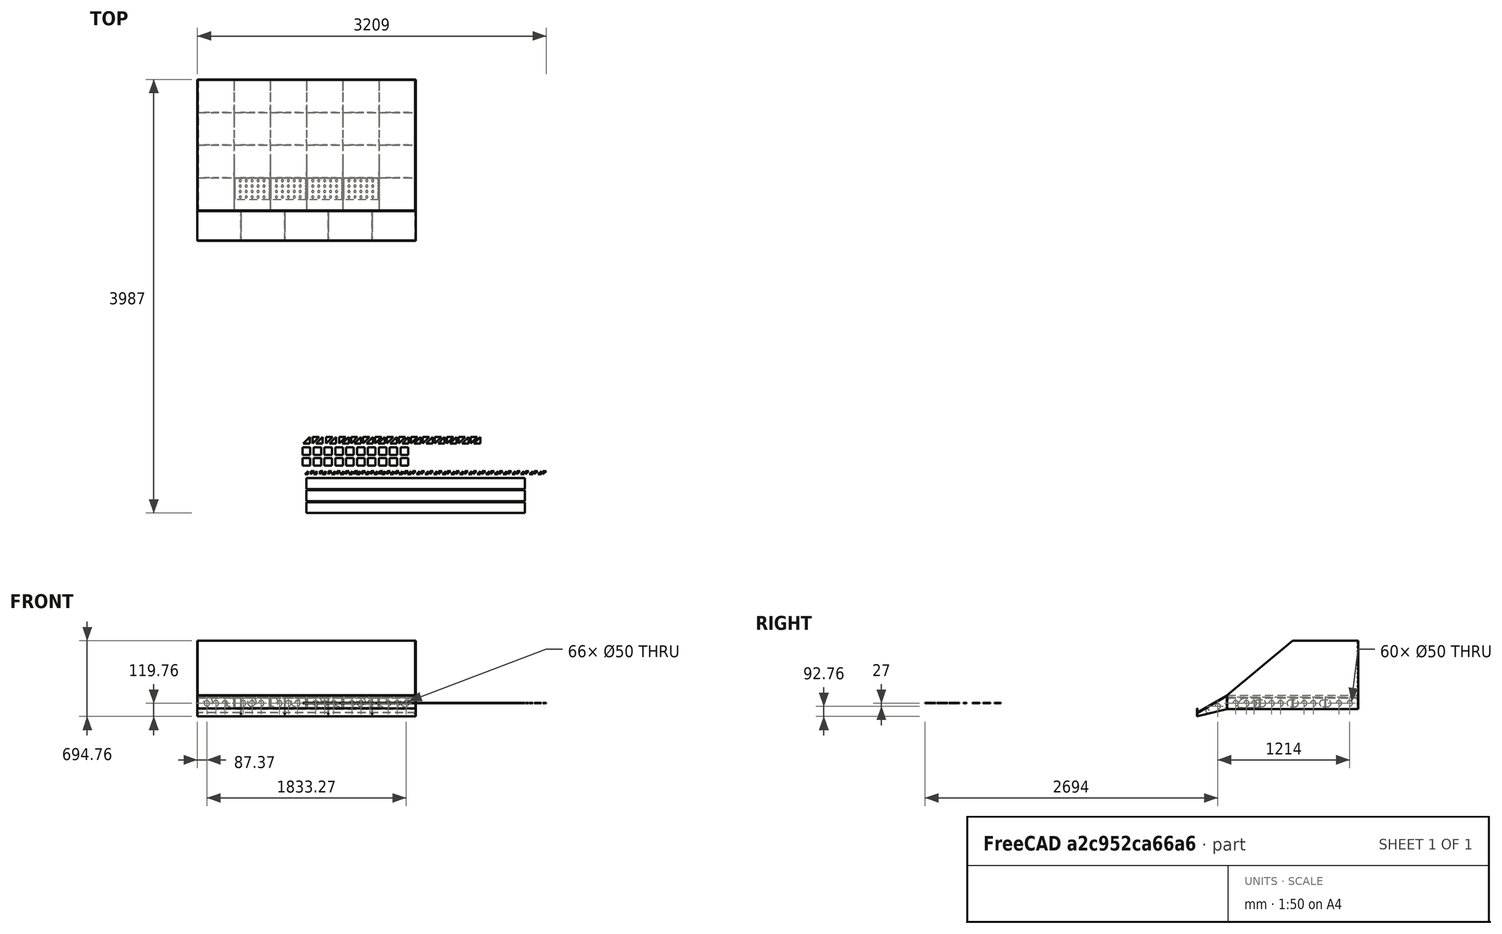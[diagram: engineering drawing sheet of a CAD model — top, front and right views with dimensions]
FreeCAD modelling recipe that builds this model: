
FCSTD DOCUMENT  (FreeCAD 0.19R24291 (Git))
Label: MJ-bord
License: All rights reserved
LicenseURL: http://en.wikipedia.org/wiki/All_rights_reserved
objects: TechDraw::DrawViewDimension×234, Sketcher::SketchObject×198, PartDesign::Pad×155, PartDesign::Body×155, App::DocumentObjectGroupPython×45, PartDesign::Pocket×40, TechDraw::DrawViewPart×18, TechDraw::DrawViewSection×18, TechDraw::DrawSVGTemplate×13, TechDraw::DrawPage×13, PartDesign::Fillet×8, Part::Feature×7, TechDraw::DrawProjGroupItem×3, TechDraw::DrawProjGroup×3, Spreadsheet::Sheet×1, App::DocumentObjectGroup×1
note: 766 computed .brp shape members not serialized (recipe doc carries the construction recipe); baked Part::Feature solids carry a one-line shape summary decoded from their .brp

FEATURE [Sketcher::SketchObject] Sketch
  FullyConstrained = true
  MapMode = 5
  Placement = pos=(0,0,0) rot=(1,0,0;1.5708rad)
  Support = -> [XZ_Plane]
  sketch-geometry (5):
    g0: LineSegment StartX=-1000 StartY=-50 StartZ=0 EndX=-1000 EndY=50 EndZ=0
    g1: LineSegment StartX=-1000 StartY=50 StartZ=0 EndX=1000 EndY=50 EndZ=0
    g2: LineSegment StartX=1000 StartY=50 StartZ=0 EndX=1000 EndY=-50 EndZ=0
    g3: LineSegment StartX=1000 StartY=-50 StartZ=0 EndX=-1000 EndY=-50 EndZ=0
    g4: GeomPoint X=0 Y=0 Z=0
  constraints (12):
    c: Coincident(g0,g1)
    c: Coincident(g1,g2)
    c: Coincident(g2,g3)
    c: Coincident(g3,g0)
    c: Horizontal(g1)
    c: Horizontal(g3)
    c: Vertical(g0)
    c: Vertical(g2)
    c: Symmetric(g1,g0,g4)
    c: Coincident(g4,g-1)
    c: DistanceY(g2,g1) = 100
    c: DistanceX(g0,g1) = 2000
FEATURE [PartDesign::Pad] Pad
  Direction = (0,-1,2e-16)
  Length = 4
  Length2 = 10
  Placement = pos=(0,0,0) rot=(1,0,0;1.5708rad)
  Profile = -> Sketch
  Type = 0
FEATURE [Sketcher::SketchObject] Sketch001
  ExternalGeometry = -> [Pad]
  FullyConstrained = false
  MapMode = 5
  Placement = pos=(0,-4,1.8e-15) rot=(1,0,0;1.5708rad)
  Support = -> [Pad]
  sketch-geometry (94):
    g0: GeomPoint X=-666.66 Y=0 Z=0
    g1: GeomPoint X=333.33 Y=0 Z=0
    g2: GeomPoint X=666.66 Y=0 Z=0
    g3: GeomPoint X=-333.33 Y=0 Z=0
    g4: Circle CenterX=-916.63 CenterY=-1.8e-15 CenterZ=0 NormalX=0 NormalY=0 NormalZ=1 AngleXU=0 Radius=25
    g5: Circle CenterX=-833.3 CenterY=-1.8e-15 CenterZ=0 NormalX=0 NormalY=0 NormalZ=1 AngleXU=0 Radius=25
    g6: Circle CenterX=-583.31 CenterY=-1.8e-15 CenterZ=0 NormalX=0 NormalY=0 NormalZ=1 AngleXU=0 Radius=25
    g7: Circle CenterX=-499.98 CenterY=-1.8e-15 CenterZ=0 NormalX=0 NormalY=0 NormalZ=1 AngleXU=0 Radius=25
    g8: Circle CenterX=-249.99 CenterY=-1.8e-15 CenterZ=0 NormalX=0 NormalY=0 NormalZ=1 AngleXU=0 Radius=25
    g9: Circle CenterX=-166.66 CenterY=-1.8e-15 CenterZ=0 NormalX=0 NormalY=0 NormalZ=1 AngleXU=0 Radius=25
    g10: Circle CenterX=83.33 CenterY=-1.8e-15 CenterZ=0 NormalX=0 NormalY=0 NormalZ=1 AngleXU=0 Radius=25
    g11: Circle CenterX=166.66 CenterY=-1.8e-15 CenterZ=0 NormalX=0 NormalY=0 NormalZ=1 AngleXU=0 Radius=25
    g12: Circle CenterX=416.65 CenterY=-1.8e-15 CenterZ=0 NormalX=0 NormalY=0 NormalZ=1 AngleXU=0 Radius=25
    g13: Circle CenterX=499.98 CenterY=-1.8e-15 CenterZ=0 NormalX=0 NormalY=0 NormalZ=1 AngleXU=0 Radius=25
    g14: Circle CenterX=749.97 CenterY=-1.8e-15 CenterZ=0 NormalX=0 NormalY=0 NormalZ=1 AngleXU=0 Radius=25
    g15: Circle CenterX=833.3 CenterY=-1.8e-15 CenterZ=0 NormalX=0 NormalY=0 NormalZ=1 AngleXU=0 Radius=25
    g16: Circle CenterX=-749.97 CenterY=-1.8e-15 CenterZ=0 NormalX=0 NormalY=0 NormalZ=1 AngleXU=0 Radius=25
    g17: Circle CenterX=-416.65 CenterY=-1.8e-15 CenterZ=0 NormalX=0 NormalY=0 NormalZ=1 AngleXU=0 Radius=25
    g18: Circle CenterX=-83.33 CenterY=-1.8e-15 CenterZ=0 NormalX=0 NormalY=0 NormalZ=1 AngleXU=0 Radius=25
    g19: Circle CenterX=249.99 CenterY=-1.8e-15 CenterZ=0 NormalX=0 NormalY=0 NormalZ=1 AngleXU=0 Radius=25
    g20: Circle CenterX=583.31 CenterY=-1.8e-15 CenterZ=0 NormalX=0 NormalY=0 NormalZ=1 AngleXU=0 Radius=25
    g21: Circle CenterX=916.64 CenterY=-1.8e-15 CenterZ=0 NormalX=0 NormalY=0 NormalZ=1 AngleXU=0 Radius=25
    g22: LineSegment StartX=-1000 StartY=50 StartZ=0 EndX=-996 EndY=50 EndZ=0
    g23: LineSegment StartX=-996 StartY=50 StartZ=0 EndX=-996 EndY=30 EndZ=0
    g24: LineSegment StartX=-996 StartY=30 StartZ=0 EndX=-1000 EndY=30 EndZ=0
    g25: LineSegment StartX=-1000 StartY=30 StartZ=0 EndX=-1000 EndY=50 EndZ=0
    g26: LineSegment StartX=-1000 StartY=10 StartZ=0 EndX=-996 EndY=10 EndZ=0
    g27: LineSegment StartX=-996 StartY=10 StartZ=0 EndX=-996 EndY=-10 EndZ=0
    g28: LineSegment StartX=-996 StartY=-10 StartZ=0 EndX=-1000 EndY=-10 EndZ=0
    g29: LineSegment StartX=-1000 StartY=-10 StartZ=0 EndX=-1000 EndY=10 EndZ=0
    g30: LineSegment StartX=1000 StartY=50 StartZ=0 EndX=996 EndY=50 EndZ=0
    g31: LineSegment StartX=996 StartY=50 StartZ=0 EndX=996 EndY=30 EndZ=0
    g32: LineSegment StartX=996 StartY=30 StartZ=0 EndX=1000 EndY=30 EndZ=0
    g33: LineSegment StartX=1000 StartY=30 StartZ=0 EndX=1000 EndY=50 EndZ=0
    g34: LineSegment StartX=1000 StartY=10 StartZ=0 EndX=996 EndY=10 EndZ=0
    g35: LineSegment StartX=996 StartY=10 StartZ=0 EndX=996 EndY=-10 EndZ=0
    g36: LineSegment StartX=996 StartY=-10 StartZ=0 EndX=1000 EndY=-10 EndZ=0
    g37: LineSegment StartX=1000 StartY=-10 StartZ=0 EndX=1000 EndY=10 EndZ=0
    g38: GeomPoint X=-666.64 Y=-51.5587 Z=0
    g39: GeomPoint X=333.32 Y=-51.5587 Z=0
    g40: GeomPoint X=666.64 Y=-51.5587 Z=0
    g41: GeomPoint X=999.97 Y=-51.5587 Z=0
    g42: GeomPoint X=-999.96 Y=-51.5587 Z=0
    g43: LineSegment StartX=-668.66 StartY=50 StartZ=0 EndX=-664.66 EndY=50 EndZ=0
    g44: LineSegment StartX=-664.66 StartY=50 StartZ=0 EndX=-664.66 EndY=30 EndZ=0
    g45: LineSegment StartX=-664.66 StartY=30 StartZ=0 EndX=-668.66 EndY=30 EndZ=0
    g46: LineSegment StartX=-668.66 StartY=30 StartZ=0 EndX=-668.66 EndY=50 EndZ=0
    g47: LineSegment StartX=-668.66 StartY=-50 StartZ=0 EndX=-664.66 EndY=-50 EndZ=0
    g48: LineSegment StartX=-664.66 StartY=-50 StartZ=0 EndX=-664.66 EndY=-30 EndZ=0
    g49: LineSegment StartX=-664.66 StartY=-30 StartZ=0 EndX=-668.66 EndY=-30 EndZ=0
    g50: LineSegment StartX=-668.66 StartY=-30 StartZ=0 EndX=-668.66 EndY=-50 EndZ=0
    g51: LineSegment StartX=-335.33 StartY=50 StartZ=0 EndX=-331.33 EndY=50 EndZ=0
    g52: LineSegment StartX=-331.33 StartY=50 StartZ=0 EndX=-331.33 EndY=30 EndZ=0
    g53: LineSegment StartX=-331.33 StartY=30 StartZ=0 EndX=-335.33 EndY=30 EndZ=0
    g54: LineSegment StartX=-335.33 StartY=30 StartZ=0 EndX=-335.33 EndY=50 EndZ=0
    g55: LineSegment StartX=-335.33 StartY=-50 StartZ=0 EndX=-331.33 EndY=-50 EndZ=0
    g56: LineSegment StartX=-331.33 StartY=-50 StartZ=0 EndX=-331.33 EndY=-30 EndZ=0
    g57: LineSegment StartX=-331.33 StartY=-30 StartZ=0 EndX=-335.33 EndY=-30 EndZ=0
    g58: LineSegment StartX=-335.33 StartY=-30 StartZ=0 EndX=-335.33 EndY=-50 EndZ=0
    g59: GeomPoint X=-333.32 Y=-51.5587 Z=0
    g60: LineSegment StartX=-2 StartY=50 StartZ=0 EndX=2 EndY=50 EndZ=0
    g61: LineSegment StartX=2 StartY=50 StartZ=0 EndX=2 EndY=30 EndZ=0
    g62: LineSegment StartX=2 StartY=30 StartZ=0 EndX=-2 EndY=30 EndZ=0
    g63: LineSegment StartX=-2 StartY=30 StartZ=0 EndX=-2 EndY=50 EndZ=0
    g64: LineSegment StartX=2 StartY=-50 StartZ=0 EndX=-2 EndY=-50 EndZ=0
    g65: LineSegment StartX=-2 StartY=-50 StartZ=0 EndX=-2 EndY=-30 EndZ=0
    g66: LineSegment StartX=-2 StartY=-30 StartZ=0 EndX=2 EndY=-30 EndZ=0
    g67: LineSegment StartX=2 StartY=-30 StartZ=0 EndX=2 EndY=-50 EndZ=0
    g68: LineSegment StartX=331.33 StartY=50 StartZ=0 EndX=335.33 EndY=50 EndZ=0
    g69: LineSegment StartX=335.33 StartY=50 StartZ=0 EndX=335.33 EndY=30 EndZ=0
    g70: LineSegment StartX=335.33 StartY=30 StartZ=0 EndX=331.33 EndY=30 EndZ=0
    g71: LineSegment StartX=331.33 StartY=30 StartZ=0 EndX=331.33 EndY=50 EndZ=0
    g72: LineSegment StartX=331.33 StartY=-30 StartZ=0 EndX=335.33 EndY=-30 EndZ=0
    g73: LineSegment StartX=335.33 StartY=-30 StartZ=0 EndX=335.33 EndY=-50 EndZ=0
    g74: LineSegment StartX=335.33 StartY=-50 StartZ=0 EndX=331.33 EndY=-50 EndZ=0
    g75: LineSegment StartX=331.33 StartY=-50 StartZ=0 EndX=331.33 EndY=-30 EndZ=0
    g76: LineSegment StartX=664.66 StartY=50 StartZ=0 EndX=668.66 EndY=50 EndZ=0
    g77: LineSegment StartX=668.66 StartY=50 StartZ=0 EndX=668.66 EndY=30 EndZ=0
    g78: LineSegment StartX=668.66 StartY=30 StartZ=0 EndX=664.66 EndY=30 EndZ=0
    g79: LineSegment StartX=664.66 StartY=30 StartZ=0 EndX=664.66 EndY=50 EndZ=0
    g80: LineSegment StartX=668.66 StartY=-50 StartZ=0 EndX=664.66 EndY=-50 EndZ=0
    g81: LineSegment StartX=664.66 StartY=-50 StartZ=0 EndX=664.66 EndY=-30 EndZ=0
    g82: LineSegment StartX=664.66 StartY=-30 StartZ=0 EndX=668.66 EndY=-30 EndZ=0
    g83: LineSegment StartX=668.66 StartY=-30 StartZ=0 EndX=668.66 EndY=-50 EndZ=0
    g84: GeomPoint X=-999.99 Y=50.4552 Z=0
    g85: GeomPoint X=999.99 Y=51.0014 Z=0
    g86: LineSegment StartX=-996 StartY=-50 StartZ=0 EndX=-1000 EndY=-50 EndZ=0
    g87: LineSegment StartX=-1000 StartY=-50 StartZ=0 EndX=-1000 EndY=-30 EndZ=0
    g88: LineSegment StartX=-1000 StartY=-30 StartZ=0 EndX=-996 EndY=-30 EndZ=0
    g89: LineSegment StartX=-996 StartY=-30 StartZ=0 EndX=-996 EndY=-50 EndZ=0
    g90: LineSegment StartX=996 StartY=-30 StartZ=0 EndX=1000 EndY=-30 EndZ=0
    g91: LineSegment StartX=1000 StartY=-30 StartZ=0 EndX=1000 EndY=-50 EndZ=0
    g92: LineSegment StartX=1000 StartY=-50 StartZ=0 EndX=996 EndY=-50 EndZ=0
    g93: LineSegment StartX=996 StartY=-50 StartZ=0 EndX=996 EndY=-30 EndZ=0
  constraints (263):
    c: DistanceY(g-4,g4) = 50
    c: Horizontal(g4,g5)
    c: Horizontal(g5,g16)
    c: Horizontal(g16,g6)
    c: Horizontal(g6,g7)
    c: Horizontal(g7,g17)
    c: Horizontal(g17,g8)
    c: Horizontal(g8,g9)
    c: Horizontal(g9,g18)
    c: Horizontal(g18,g10)
    c: Horizontal(g10,g11)
    c: Horizontal(g11,g19)
    c: Horizontal(g19,g12)
    c: Horizontal(g12,g13)
    c: Horizontal(g13,g20)
    c: Horizontal(g20,g14)
    c: Horizontal(g14,g15)
    c: Horizontal(g15,g21)
    c: Coincident(g22,g23)
    c: Coincident(g23,g24)
    c: Coincident(g24,g25)
    c: Coincident(g25,g22)
    c: Horizontal(g22)
    c: Horizontal(g24)
    c: Vertical(g23)
    c: Vertical(g25)
    c: Coincident(g26,g27)
    c: Coincident(g27,g28)
    c: Coincident(g28,g29)
    c: Coincident(g29,g26)
    c: Horizontal(g26)
    c: Horizontal(g28)
    c: Vertical(g27)
    c: Vertical(g29)
    c: Vertical(g-3,g22)
    c: Vertical(g24,g26)
    c: DistanceX(g-3,g22) = 4
    c: Vertical(g23,g26)
    c: DistanceY(g22,g-3) = 0
    c: DistanceY(g24,g22) = 20
    c: DistanceY(g26,g24) = 20
    c: DistanceY(g28,g26) = 20
    c: Coincident(g30,g31)
    c: Coincident(g31,g32)
    c: Coincident(g32,g33)
    c: Coincident(g33,g30)
    c: Horizontal(g30)
    c: Horizontal(g32)
    c: Vertical(g31)
    c: Vertical(g33)
    c: Coincident(g34,g35)
    c: Coincident(g35,g36)
    c: Coincident(g36,g37)
    c: Coincident(g37,g34)
    c: Horizontal(g34)
    c: Horizontal(g36)
    c: Vertical(g35)
    c: Vertical(g37)
    c: Vertical(g-5,g30)
    c: Vertical(g32,g34)
    c: DistanceX(g30,g30) = 4
    c: Vertical(g31,g34)
    c: Horizontal(g22,g30)
    c: Horizontal(g31,g23)
    c: Horizontal(g26,g34)
    c: Horizontal(g35,g27)
    c: Diameter(g4) = 50
    c: DistanceX(g4,g5) = 83.33
    c: Equal(g4,g5)
    c: DistanceX(g5,g16) = 83.33
    c: Equal(g5,g16)
    c: DistanceX(g0,g3) = 333.33
    c: DistanceX(g3,g-1) = 333.33
    c: DistanceX(g6,g7) = 83.33
    c: DistanceX(g7,g17) = 83.33
    c: Equal(g16,g6)
    c: Equal(g6,g7)
    c: Equal(g7,g17)
    c: DistanceX(g16,g38) = 83.33
    c: DistanceX(g38,g6) = 83.33
    c: DistanceX(g8,g9) = 83.33
    c: DistanceX(g9,g18) = 83.33
    c: DistanceX(g18,g-1) = 83.33
    c: Equal(g17,g8)
    c: Equal(g8,g9)
    c: Equal(g9,g18)
    c: DistanceX(g-1,g10) = 83.33
    c: DistanceX(g10,g11) = 83.33
    c: DistanceX(g11,g19) = 83.33
    c: Equal(g18,g10)
    c: Equal(g10,g11)
    c: Equal(g11,g19)
    c: DistanceX(g19,g39) = 83.33
    c: DistanceX(g39,g12) = 83.33
    c: DistanceX(g12,g13) = 83.33
    c: DistanceX(g13,g20) = 83.33
    c: Equal(g19,g12)
    c: Equal(g12,g13)
    c: Equal(g13,g20)
    c: DistanceX(g20,g40) = 83.33
    c: DistanceX(g40,g14) = 83.33
    c: DistanceX(g14,g15) = 83.33
    c: DistanceX(g15,g21) = 83.34
    c: DistanceX(g21,g41) = 83.33
    c: Equal(g20,g14)
    c: Equal(g14,g15)
    c: Equal(g15,g21)
    c: DistanceX(g42,g4) = 83.33
    c: Coincident(g43,g44)
    c: Coincident(g44,g45)
    c: Coincident(g45,g46)
    c: Coincident(g46,g43)
    c: Horizontal(g43)
    c: Horizontal(g45)
    c: Vertical(g44)
    c: Vertical(g46)
    c: Horizontal(g-3,g43)
    c: DistanceX(g43,g0) = 2
    c: DistanceX(g43,g43) = 4
    c: DistanceY(g45,g43) = 20
    c: Coincident(g47,g48)
    c: Coincident(g48,g49)
    c: Coincident(g49,g50)
    c: Coincident(g50,g47)
    c: Horizontal(g47)
    c: Horizontal(g49)
    c: Vertical(g48)
    c: Vertical(g50)
    c: Vertical(g45,g49)
    c: Vertical(g48,g44)
    c: Horizontal(g-4,g47)
    c: DistanceY(g47,g49) = 20
    c: Coincident(g51,g52)
    c: Coincident(g52,g53)
    c: Coincident(g53,g54)
    c: Coincident(g54,g51)
    c: Horizontal(g51)
    c: Horizontal(g53)
    c: Vertical(g52)
    c: Vertical(g54)
    c: Horizontal(g43,g51)
    c: DistanceX(g51,g3) = 2
    c: DistanceX(g51,g51) = 4
    c: Horizontal(g44,g53)
    c: Coincident(g55,g56)
    c: Coincident(g56,g57)
    c: Coincident(g57,g58)
    c: Coincident(g58,g55)
    c: Horizontal(g55)
    c: Horizontal(g57)
    c: Vertical(g56)
    c: Vertical(g58)
    c: Horizontal(g47,g55)
    c: Horizontal(g57,g48)
    c: Vertical(g53,g57)
    c: Vertical(g56,g52)
    c: DistanceX(g17,g59) = 83.33
    c: DistanceX(g59,g8) = 83.33
    c: Coincident(g60,g61)
    c: Coincident(g61,g62)
    c: Coincident(g62,g63)
    c: Coincident(g63,g60)
    c: Horizontal(g60)
    c: Horizontal(g62)
    c: Vertical(g61)
    c: Vertical(g63)
    c: Coincident(g64,g65)
    c: Coincident(g65,g66)
    c: Coincident(g66,g67)
    c: Coincident(g67,g64)
    c: Horizontal(g64)
    c: Horizontal(g66)
    c: Vertical(g65)
    c: Vertical(g67)
    c: Horizontal(g55,g64)
    c: Horizontal(g65,g56)
    c: Horizontal(g52,g62)
    c: Horizontal(g60,g51)
    c: DistanceX(g60,g-1) = 2
    c: DistanceX(g60,g60) = 4
    c: Vertical(g61,g66)
    c: Vertical(g62,g65)
    c: Coincident(g68,g69)
    c: Coincident(g69,g70)
    c: Coincident(g70,g71)
    c: Coincident(g71,g68)
    c: Horizontal(g68)
    c: Horizontal(g70)
    c: Vertical(g69)
    c: Vertical(g71)
    c: Coincident(g72,g73)
    c: Coincident(g73,g74)
    c: Coincident(g74,g75)
    c: Coincident(g75,g72)
    c: Horizontal(g72)
    c: Horizontal(g74)
    c: Vertical(g73)
    c: Vertical(g75)
    c: Horizontal(g64,g74)
    c: Horizontal(g66,g72)
    c: Horizontal(g68,g60)
    c: Horizontal(g70,g61)
    c: DistanceX(g-1,g1) = 333.33
    c: DistanceX(g68,g1) = 2
    c: DistanceX(g68,g68) = 4
    c: Vertical(g70,g72)
    c: Vertical(g69,g72)
    c: DistanceX(g1,g2) = 333.33
    c: Coincident(g76,g77)
    c: Coincident(g77,g78)
    c: Coincident(g78,g79)
    c: Coincident(g79,g76)
    c: Horizontal(g76)
    c: Horizontal(g78)
    c: Vertical(g77)
    c: Vertical(g79)
    c: Coincident(g80,g81)
    c: Coincident(g81,g82)
    c: Coincident(g82,g83)
    c: Coincident(g83,g80)
    c: Horizontal(g80)
    c: Horizontal(g82)
    c: Vertical(g81)
    c: Vertical(g83)
    c: Horizontal(g73,g80)
    c: Horizontal(g81,g72)
    c: Horizontal(g69,g78)
    c: Horizontal(g76,g68)
    c: DistanceX(g76,g2) = 2
    c: DistanceX(g76,g76) = 4
    c: Vertical(g78,g81)
    c: Vertical(g82,g77)
    c: Horizontal(g42,g38)
    c: Horizontal(g38,g59)
    c: Horizontal(g59,g39)
    c: Horizontal(g39,g40)
    c: Horizontal(g40,g41)
    c: DistanceX(g84,g0) = 333.33
    c: DistanceX(g2,g85) = 333.33
    c: Coincident(g86,g87)
    c: Coincident(g87,g88)
    c: Coincident(g88,g89)
    c: Coincident(g89,g86)
    c: Horizontal(g86)
    c: Horizontal(g88)
    c: Vertical(g87)
    c: Vertical(g89)
    c: Vertical(g88,g27)
    c: Vertical(g28,g87)
    c: DistanceY(g87,g28) = 20
    c: DistanceY(g86,g87) = 20
    c: Coincident(g90,g91)
    c: Coincident(g91,g92)
    c: Coincident(g92,g93)
    c: Coincident(g93,g90)
    c: Horizontal(g90)
    c: Horizontal(g92)
    c: Vertical(g91)
    c: Vertical(g93)
    c: Vertical(g36,g90)
    c: Vertical(g35,g90)
    c: Horizontal(g90,g88)
    c: Horizontal(g86,g92)
FEATURE [PartDesign::Pocket] Pocket
  BaseFeature = -> Pad
  Length = 4
  Length2 = 5
  Placement = pos=(0,0,0) rot=(1,0,0;1.5708rad)
  Profile = -> Sketch001
  Type = 0
FEATURE [PartDesign::Body] Body  label="LangSprygel-1"
  Group = -> [Sketch,Pad,Sketch001,Pocket]
  Origin = -> Origin
  Placement = pos=(0,302,0) rot=(0,0,1;0rad)
  Tip = -> Pocket
FEATURE [Sketcher::SketchObject] Sketch002
  FullyConstrained = true
  MapMode = 5
  Placement = pos=(0,0,0) rot=(1,0,0;1.5708rad)
  Support = -> [XZ_Plane001]
  sketch-geometry (5):
    g0: LineSegment StartX=-1000 StartY=-50 StartZ=0 EndX=-1000 EndY=50 EndZ=0
    g1: LineSegment StartX=-1000 StartY=50 StartZ=0 EndX=1000 EndY=50 EndZ=0
    g2: LineSegment StartX=1000 StartY=50 StartZ=0 EndX=1000 EndY=-50 EndZ=0
    g3: LineSegment StartX=1000 StartY=-50 StartZ=0 EndX=-1000 EndY=-50 EndZ=0
    g4: GeomPoint X=0 Y=0 Z=0
  constraints (12):
    c: Coincident(g0,g1)
    c: Coincident(g1,g2)
    c: Coincident(g2,g3)
    c: Coincident(g3,g0)
    c: Horizontal(g1)
    c: Horizontal(g3)
    c: Vertical(g0)
    c: Vertical(g2)
    c: Symmetric(g1,g0,g4)
    c: Coincident(g4,g-1)
    c: DistanceX(g0,g2) = 2000
    c: DistanceY(g0,g0) = 100
FEATURE [PartDesign::Pad] Pad001
  Direction = (0,-1,2e-16)
  Length = 4
  Length2 = 10
  Placement = pos=(0,0,0) rot=(1,0,0;1.5708rad)
  Profile = -> Sketch002
  Type = 0
FEATURE [Sketcher::SketchObject] Sketch003
  ExternalGeometry = -> [Pad001]
  FullyConstrained = false
  MapMode = 5
  Placement = pos=(0,-4,1.8e-15) rot=(1,0,0;1.5708rad)
  Support = -> [Pad001]
  sketch-geometry (91):
    g0: LineSegment StartX=-1000 StartY=50 StartZ=0 EndX=-996 EndY=50 EndZ=0
    g1: LineSegment StartX=-996 StartY=50 StartZ=0 EndX=-996 EndY=30 EndZ=0
    g2: LineSegment StartX=-996 StartY=30 StartZ=0 EndX=-1000 EndY=30 EndZ=0
    g3: LineSegment StartX=-1000 StartY=30 StartZ=0 EndX=-1000 EndY=50 EndZ=0
    g4: LineSegment StartX=-1000 StartY=10 StartZ=0 EndX=-996 EndY=10 EndZ=0
    g5: LineSegment StartX=-996 StartY=10 StartZ=0 EndX=-996 EndY=-10 EndZ=0
    g6: LineSegment StartX=-996 StartY=-10 StartZ=0 EndX=-1000 EndY=-10 EndZ=0
    g7: LineSegment StartX=-1000 StartY=-10 StartZ=0 EndX=-1000 EndY=10 EndZ=0
    g8: LineSegment StartX=-1000 StartY=-30 StartZ=0 EndX=-996 EndY=-30 EndZ=0
    g9: LineSegment StartX=-996 StartY=-30 StartZ=0 EndX=-996 EndY=-50 EndZ=0
    g10: LineSegment StartX=-996 StartY=-50 StartZ=0 EndX=-1000 EndY=-50 EndZ=0
    g11: LineSegment StartX=-1000 StartY=-50 StartZ=0 EndX=-1000 EndY=-30 EndZ=0
    g12: LineSegment StartX=1000 StartY=50 StartZ=0 EndX=996 EndY=50 EndZ=0
    g13: LineSegment StartX=996 StartY=50 StartZ=0 EndX=996 EndY=30 EndZ=0
    g14: LineSegment StartX=996 StartY=30 StartZ=0 EndX=1000 EndY=30 EndZ=0
    g15: LineSegment StartX=1000 StartY=30 StartZ=0 EndX=1000 EndY=50 EndZ=0
    g16: LineSegment StartX=1000 StartY=-50 StartZ=0 EndX=996 EndY=-50 EndZ=0
    g17: LineSegment StartX=996 StartY=-50 StartZ=0 EndX=996 EndY=-30 EndZ=0
    g18: LineSegment StartX=996 StartY=-30 StartZ=0 EndX=1000 EndY=-30 EndZ=0
    g19: LineSegment StartX=1000 StartY=-30 StartZ=0 EndX=1000 EndY=-50 EndZ=0
    g20: LineSegment StartX=1000 StartY=-10 StartZ=0 EndX=996 EndY=-10 EndZ=0
    g21: LineSegment StartX=996 StartY=-10 StartZ=0 EndX=996 EndY=10 EndZ=0
    g22: LineSegment StartX=996 StartY=10 StartZ=0 EndX=1000 EndY=10 EndZ=0
    g23: LineSegment StartX=1000 StartY=10 StartZ=0 EndX=1000 EndY=-10 EndZ=0
    g24: GeomPoint X=-666.67 Y=0 Z=0
    g25: GeomPoint X=-333.34 Y=0 Z=0
    g26: GeomPoint X=-0.01 Y=0 Z=0
    g27: GeomPoint X=333.32 Y=0 Z=0
    g28: GeomPoint X=666.65 Y=0 Z=0
    g29: GeomPoint X=1000 Y=10 Z=0
    g30: GeomPoint X=999.98 Y=-53.2776 Z=0
    g31: LineSegment StartX=-664.67 StartY=-10 StartZ=0 EndX=-668.67 EndY=-10 EndZ=0
    g32: LineSegment StartX=-668.67 StartY=-10 StartZ=0 EndX=-668.67 EndY=10 EndZ=0
    g33: LineSegment StartX=-668.67 StartY=10 StartZ=0 EndX=-664.67 EndY=10 EndZ=0
    g34: LineSegment StartX=-664.67 StartY=10 StartZ=0 EndX=-664.67 EndY=-10 EndZ=0
    g35: LineSegment StartX=-668.67 StartY=50 StartZ=0 EndX=-664.67 EndY=50 EndZ=0
    g36: LineSegment StartX=-664.67 StartY=50 StartZ=0 EndX=-664.67 EndY=30 EndZ=0
    g37: LineSegment StartX=-664.67 StartY=30 StartZ=0 EndX=-668.67 EndY=30 EndZ=0
    g38: LineSegment StartX=-668.67 StartY=30 StartZ=0 EndX=-668.67 EndY=50 EndZ=0
    g39: LineSegment StartX=-668.67 StartY=-50 StartZ=0 EndX=-664.67 EndY=-50 EndZ=0
    g40: LineSegment StartX=-664.67 StartY=-50 StartZ=0 EndX=-664.67 EndY=-30 EndZ=0
    g41: LineSegment StartX=-664.67 StartY=-30 StartZ=0 EndX=-668.67 EndY=-30 EndZ=0
    g42: LineSegment StartX=-668.67 StartY=-30 StartZ=0 EndX=-668.67 EndY=-50 EndZ=0
    g43: LineSegment StartX=-335.34 StartY=50 StartZ=0 EndX=-331.34 EndY=50 EndZ=0
    g44: LineSegment StartX=-331.34 StartY=50 StartZ=0 EndX=-331.34 EndY=30 EndZ=0
    g45: LineSegment StartX=-331.34 StartY=30 StartZ=0 EndX=-335.34 EndY=30 EndZ=0
    g46: LineSegment StartX=-335.34 StartY=30 StartZ=0 EndX=-335.34 EndY=50 EndZ=0
    g47: LineSegment StartX=-335.34 StartY=10 StartZ=0 EndX=-331.34 EndY=10 EndZ=0
    g48: LineSegment StartX=-331.34 StartY=10 StartZ=0 EndX=-331.34 EndY=-10 EndZ=0
    g49: LineSegment StartX=-331.34 StartY=-10 StartZ=0 EndX=-335.34 EndY=-10 EndZ=0
    g50: LineSegment StartX=-335.34 StartY=-10 StartZ=0 EndX=-335.34 EndY=10 EndZ=0
    g51: LineSegment StartX=-335.34 StartY=-30 StartZ=0 EndX=-331.34 EndY=-30 EndZ=0
    g52: LineSegment StartX=-331.34 StartY=-30 StartZ=0 EndX=-331.34 EndY=-50 EndZ=0
    g53: LineSegment StartX=-331.34 StartY=-50 StartZ=0 EndX=-335.34 EndY=-50 EndZ=0
    g54: LineSegment StartX=-335.34 StartY=-50 StartZ=0 EndX=-335.34 EndY=-30 EndZ=0
    g55: LineSegment StartX=-2.01 StartY=50 StartZ=0 EndX=1.99 EndY=50 EndZ=0
    g56: LineSegment StartX=1.99 StartY=50 StartZ=0 EndX=1.99 EndY=30 EndZ=0
    g57: LineSegment StartX=1.99 StartY=30 StartZ=0 EndX=-2.01 EndY=30 EndZ=0
    g58: LineSegment StartX=-2.01 StartY=30 StartZ=0 EndX=-2.01 EndY=50 EndZ=0
    g59: LineSegment StartX=-2.01 StartY=10 StartZ=0 EndX=1.99 EndY=10 EndZ=0
    g60: LineSegment StartX=1.99 StartY=10 StartZ=0 EndX=1.99 EndY=-10 EndZ=0
    g61: LineSegment StartX=1.99 StartY=-10 StartZ=0 EndX=-2.01 EndY=-10 EndZ=0
    g62: LineSegment StartX=-2.01 StartY=-10 StartZ=0 EndX=-2.01 EndY=10 EndZ=0
    g63: LineSegment StartX=-2.01 StartY=-30 StartZ=0 EndX=1.99 EndY=-30 EndZ=0
    g64: LineSegment StartX=1.99 StartY=-30 StartZ=0 EndX=1.99 EndY=-50 EndZ=0
    g65: LineSegment StartX=1.99 StartY=-50 StartZ=0 EndX=-2.01 EndY=-50 EndZ=0
    g66: LineSegment StartX=-2.01 StartY=-50 StartZ=0 EndX=-2.01 EndY=-30 EndZ=0
    g67: LineSegment StartX=331.32 StartY=50 StartZ=0 EndX=335.32 EndY=50 EndZ=0
    g68: LineSegment StartX=335.32 StartY=50 StartZ=0 EndX=335.32 EndY=30 EndZ=0
    g69: LineSegment StartX=335.32 StartY=30 StartZ=0 EndX=331.32 EndY=30 EndZ=0
    g70: LineSegment StartX=331.32 StartY=30 StartZ=0 EndX=331.32 EndY=50 EndZ=0
    g71: LineSegment StartX=331.32 StartY=10 StartZ=0 EndX=335.32 EndY=10 EndZ=0
    g72: LineSegment StartX=335.32 StartY=10 StartZ=0 EndX=335.32 EndY=-10 EndZ=0
    g73: LineSegment StartX=335.32 StartY=-10 StartZ=0 EndX=331.32 EndY=-10 EndZ=0
    g74: LineSegment StartX=331.32 StartY=-10 StartZ=0 EndX=331.32 EndY=10 EndZ=0
    g75: LineSegment StartX=331.32 StartY=-30 StartZ=0 EndX=335.32 EndY=-30 EndZ=0
    g76: LineSegment StartX=335.32 StartY=-30 StartZ=0 EndX=335.32 EndY=-50 EndZ=0
    g77: LineSegment StartX=335.32 StartY=-50 StartZ=0 EndX=331.32 EndY=-50 EndZ=0
    g78: LineSegment StartX=331.32 StartY=-50 StartZ=0 EndX=331.32 EndY=-30 EndZ=0
    g79: LineSegment StartX=664.65 StartY=50 StartZ=0 EndX=668.65 EndY=50 EndZ=0
    g80: LineSegment StartX=668.65 StartY=50 StartZ=0 EndX=668.65 EndY=30 EndZ=0
    g81: LineSegment StartX=668.65 StartY=30 StartZ=0 EndX=664.65 EndY=30 EndZ=0
    g82: LineSegment StartX=664.65 StartY=30 StartZ=0 EndX=664.65 EndY=50 EndZ=0
    g83: LineSegment StartX=664.65 StartY=10 StartZ=0 EndX=668.65 EndY=10 EndZ=0
    g84: LineSegment StartX=668.65 StartY=10 StartZ=0 EndX=668.65 EndY=-10 EndZ=0
    g85: LineSegment StartX=668.65 StartY=-10 StartZ=0 EndX=664.65 EndY=-10 EndZ=0
    g86: LineSegment StartX=664.65 StartY=-10 StartZ=0 EndX=664.65 EndY=10 EndZ=0
    g87: LineSegment StartX=664.65 StartY=-30 StartZ=0 EndX=668.65 EndY=-30 EndZ=0
    g88: LineSegment StartX=668.65 StartY=-30 StartZ=0 EndX=668.65 EndY=-50 EndZ=0
    g89: LineSegment StartX=668.65 StartY=-50 StartZ=0 EndX=664.65 EndY=-50 EndZ=0
    g90: LineSegment StartX=664.65 StartY=-50 StartZ=0 EndX=664.65 EndY=-30 EndZ=0
  constraints (259):
    c: Coincident(g0,g1)
    c: Coincident(g1,g2)
    c: Coincident(g2,g3)
    c: Coincident(g3,g0)
    c: Horizontal(g0)
    c: Horizontal(g2)
    c: Vertical(g1)
    c: Vertical(g3)
    c: Coincident(g0,g-3)
    c: Coincident(g4,g5)
    c: Coincident(g5,g6)
    c: Coincident(g6,g7)
    c: Coincident(g7,g4)
    c: Horizontal(g4)
    c: Horizontal(g6)
    c: Vertical(g5)
    c: Vertical(g7)
    c: Coincident(g8,g9)
    c: Coincident(g9,g10)
    c: Coincident(g10,g11)
    c: Coincident(g11,g8)
    c: Horizontal(g8)
    c: Horizontal(g10)
    c: Vertical(g9)
    c: Vertical(g11)
    c: DistanceX(g0,g0) = 4
    c: DistanceY(g2,g0) = 20
    c: DistanceY(g4,g2) = 20
    c: DistanceY(g6,g4) = 20
    c: DistanceY(g8,g6) = 20
    c: DistanceY(g10,g8) = 20
    c: Vertical(g4,g1)
    c: Vertical(g8,g5)
    c: Coincident(g12,g13)
    c: Coincident(g13,g14)
    c: Coincident(g14,g15)
    c: Coincident(g15,g12)
    c: Horizontal(g12)
    c: Horizontal(g14)
    c: Vertical(g13)
    c: Vertical(g15)
    c: Coincident(g12,g-5)
    c: Coincident(g16,g17)
    c: Coincident(g17,g18)
    c: Coincident(g18,g19)
    c: Coincident(g19,g16)
    c: Horizontal(g16)
    c: Horizontal(g18)
    c: Vertical(g17)
    c: Vertical(g19)
    c: Coincident(g16,g-6)
    c: Coincident(g20,g21)
    c: Coincident(g21,g22)
    c: Coincident(g22,g23)
    c: Coincident(g23,g20)
    c: Horizontal(g20)
    c: Horizontal(g22)
    c: Vertical(g21)
    c: Vertical(g23)
    c: DistanceX(g12,g12) = 4
    c: Vertical(g21,g13)
    c: Vertical(g17,g20)
    c: Horizontal(g13,g1)
    c: Horizontal(g4,g21)
    c: Horizontal(g20,g5)
    c: Horizontal(g8,g17)
    c: Vertical(g14,g22)
    c: Vertical(g2,g4)
    c: Vertical(g6,g8)
    c: DistanceX(g0,g24) = 333.33
    c: DistanceX(g24,g25) = 333.33
    c: PointOnObject(g26,g-1)
    c: DistanceX(g25,g26) = 333.33
    c: PointOnObject(g27,g-1)
    c: PointOnObject(g28,g-1)
    c: DistanceX(g26,g27) = 333.33
    c: DistanceX(g27,g28) = 333.33
    c: Coincident(g29,g22)
    c: DistanceX(g28,g30) = 333.33
    c: Coincident(g31,g32)
    c: Coincident(g32,g33)
    c: Coincident(g33,g34)
    c: Coincident(g34,g31)
    c: Horizontal(g31)
    c: Horizontal(g33)
    c: Vertical(g32)
    c: Vertical(g34)
    c: Horizontal(g4,g32)
    c: Horizontal(g31,g5)
    c: Coincident(g35,g36)
    c: Coincident(g36,g37)
    c: Coincident(g37,g38)
    c: Coincident(g38,g35)
    c: Horizontal(g35)
    c: Horizontal(g37)
    c: Vertical(g36)
    c: Vertical(g38)
    c: DistanceX(g35,g35) = 4
    c: Horizontal(g35,g0)
    c: DistanceX(g35,g24) = 2
    c: Horizontal(g37,g1)
    c: Vertical(g36,g33)
    c: Vertical(g32,g37)
    c: Coincident(g39,g40)
    c: Coincident(g40,g41)
    c: Coincident(g41,g42)
    c: Coincident(g42,g39)
    c: Horizontal(g39)
    c: Horizontal(g41)
    c: Vertical(g40)
    c: Vertical(g42)
    c: Vertical(g31,g41)
    c: Vertical(g31,g40)
    c: Horizontal(g8,g41)
    c: Horizontal(g39,g9)
    c: Coincident(g43,g44)
    c: Coincident(g44,g45)
    c: Coincident(g45,g46)
    c: Coincident(g46,g43)
    c: Horizontal(g43)
    c: Horizontal(g45)
    c: Vertical(g44)
    c: Vertical(g46)
    c: Coincident(g47,g48)
    c: Coincident(g48,g49)
    c: Coincident(g49,g50)
    c: Coincident(g50,g47)
    c: Horizontal(g47)
    c: Horizontal(g49)
    c: Vertical(g48)
    c: Vertical(g50)
    c: Coincident(g51,g52)
    c: Coincident(g52,g53)
    c: Coincident(g53,g54)
    c: Coincident(g54,g51)
    c: Horizontal(g51)
    c: Horizontal(g53)
    c: Vertical(g52)
    c: Vertical(g54)
    c: Horizontal(g43,g35)
    c: Horizontal(g36,g45)
    c: Horizontal(g33,g47)
    c: Horizontal(g31,g49)
    c: Horizontal(g51,g40)
    c: Horizontal(g39,g53)
    c: Vertical(g45,g47)
    c: Vertical(g44,g47)
    c: Vertical(g51,g49)
    c: Vertical(g51,g48)
    c: DistanceX(g43,g43) = 4
    c: DistanceX(g43,g25) = 2
    c: Coincident(g55,g56)
    c: Coincident(g56,g57)
    c: Coincident(g57,g58)
    c: Coincident(g58,g55)
    c: Horizontal(g55)
    c: Horizontal(g57)
    c: Vertical(g56)
    c: Vertical(g58)
    c: Coincident(g59,g60)
    c: Coincident(g60,g61)
    c: Coincident(g61,g62)
    c: Coincident(g62,g59)
    c: Horizontal(g59)
    c: Horizontal(g61)
    c: Vertical(g60)
    c: Vertical(g62)
    c: Coincident(g63,g64)
    c: Coincident(g64,g65)
    c: Coincident(g65,g66)
    c: Coincident(g66,g63)
    c: Horizontal(g63)
    c: Horizontal(g65)
    c: Vertical(g64)
    c: Vertical(g66)
    c: Horizontal(g43,g55)
    c: Horizontal(g44,g57)
    c: Horizontal(g47,g59)
    c: Horizontal(g48,g61)
    c: Horizontal(g63,g51)
    c: Horizontal(g52,g65)
    c: Vertical(g57,g59)
    c: Vertical(g63,g61)
    c: Vertical(g63,g60)
    c: Vertical(g59,g56)
    c: DistanceX(g55,g55) = 4
    c: DistanceX(g55,g26) = 2
    c: Coincident(g67,g68)
    c: Coincident(g68,g69)
    c: Coincident(g69,g70)
    c: Coincident(g70,g67)
    c: Horizontal(g67)
    c: Horizontal(g69)
    c: Vertical(g68)
    c: Vertical(g70)
    c: Coincident(g71,g72)
    c: Coincident(g72,g73)
    c: Coincident(g73,g74)
    c: Coincident(g74,g71)
    c: Horizontal(g71)
    c: Horizontal(g73)
    c: Vertical(g72)
    c: Vertical(g74)
    c: Coincident(g75,g76)
    c: Coincident(g76,g77)
    c: Coincident(g77,g78)
    c: Coincident(g78,g75)
    c: Horizontal(g75)
    c: Horizontal(g77)
    c: Vertical(g76)
    c: Vertical(g78)
    c: Horizontal(g55,g67)
    c: Horizontal(g56,g69)
    c: Horizontal(g59,g71)
    c: Horizontal(g60,g73)
    c: Horizontal(g63,g75)
    c: Horizontal(g64,g77)
    c: Vertical(g69,g71)
    c: Vertical(g73,g75)
    c: Vertical(g68,g71)
    c: Vertical(g72,g75)
    c: DistanceX(g67,g67) = 4
    c: DistanceX(g67,g27) = 2
    c: Coincident(g79,g80)
    c: Coincident(g80,g81)
    c: Coincident(g81,g82)
    c: Coincident(g82,g79)
    c: Horizontal(g79)
    c: Horizontal(g81)
    c: Vertical(g80)
    c: Vertical(g82)
    c: Coincident(g83,g84)
    c: Coincident(g84,g85)
    c: Coincident(g85,g86)
    c: Coincident(g86,g83)
    c: Horizontal(g83)
    c: Horizontal(g85)
    c: Vertical(g84)
    c: Vertical(g86)
    c: Coincident(g87,g88)
    c: Coincident(g88,g89)
    c: Coincident(g89,g90)
    c: Coincident(g90,g87)
    c: Horizontal(g87)
    c: Horizontal(g89)
    c: Vertical(g88)
    c: Vertical(g90)
    c: Horizontal(g67,g79)
    c: Horizontal(g68,g81)
    c: Horizontal(g71,g83)
    c: Horizontal(g72,g85)
    c: Horizontal(g75,g87)
    c: Horizontal(g76,g89)
    c: Vertical(g81,g83)
    c: Vertical(g85,g87)
    c: Vertical(g80,g83)
    c: Vertical(g84,g87)
    c: DistanceX(g79,g79) = 4
    c: DistanceX(g79,g28) = 2
FEATURE [PartDesign::Pocket] Pocket001
  BaseFeature = -> Pad001
  Length = 4
  Length2 = 5
  Placement = pos=(0,0,0) rot=(1,0,0;1.5708rad)
  Profile = -> Sketch003
  Type = 0
FEATURE [PartDesign::Body] Body001  label="Fram/Bakkant-Inre-1"
  Group = -> [Sketch002,Pad001,Sketch003,Pocket001]
  Origin = -> Origin001
  Placement = pos=(0,-596,0) rot=(0,0,1;0rad)
  Tip = -> Pocket001
FEATURE [Sketcher::SketchObject] Sketch004
  FullyConstrained = true
  MapMode = 5
  Placement = pos=(0,0,0) rot=(1,0,0;1.5708rad)
  Support = -> [XZ_Plane002]
  sketch-geometry (5):
    g0: LineSegment StartX=-1000 StartY=-50 StartZ=0 EndX=-1000 EndY=50 EndZ=0
    g1: LineSegment StartX=-1000 StartY=50 StartZ=0 EndX=1000 EndY=50 EndZ=0
    g2: LineSegment StartX=1000 StartY=50 StartZ=0 EndX=1000 EndY=-50 EndZ=0
    g3: LineSegment StartX=1000 StartY=-50 StartZ=0 EndX=-1000 EndY=-50 EndZ=0
    g4: GeomPoint X=0 Y=0 Z=0
  constraints (12):
    c: Coincident(g0,g1)
    c: Coincident(g1,g2)
    c: Coincident(g2,g3)
    c: Coincident(g3,g0)
    c: Horizontal(g1)
    c: Horizontal(g3)
    c: Vertical(g0)
    c: Vertical(g2)
    c: Symmetric(g1,g0,g4)
    c: Coincident(g4,g-1)
    c: DistanceX(g0,g2) = 2000
    c: DistanceY(g0,g0) = 100
FEATURE [PartDesign::Pad] Pad002
  Direction = (0,-1,-2e-16)
  Length = 4
  Length2 = 10
  Placement = pos=(0,0,0) rot=(1,0,0;1.5708rad)
  Profile = -> Sketch004
  Type = 0
FEATURE [Sketcher::SketchObject] Sketch005
  ExternalGeometry = -> [Pad002]
  FullyConstrained = false
  MapMode = 5
  Placement = pos=(0,-4,0) rot=(1,0,0;1.5708rad)
  Support = -> [Pad002]
  sketch-geometry (91):
    g0: LineSegment StartX=-1000 StartY=50 StartZ=0 EndX=-996 EndY=50 EndZ=0
    g1: LineSegment StartX=-996 StartY=50 StartZ=0 EndX=-996 EndY=30 EndZ=0
    g2: LineSegment StartX=-996 StartY=30 StartZ=0 EndX=-1000 EndY=30 EndZ=0
    g3: LineSegment StartX=-1000 StartY=30 StartZ=0 EndX=-1000 EndY=50 EndZ=0
    g4: LineSegment StartX=-1000 StartY=10 StartZ=0 EndX=-996 EndY=10 EndZ=0
    g5: LineSegment StartX=-996 StartY=10 StartZ=0 EndX=-996 EndY=-10 EndZ=0
    g6: LineSegment StartX=-996 StartY=-10 StartZ=0 EndX=-1000 EndY=-10 EndZ=0
    g7: LineSegment StartX=-1000 StartY=-10 StartZ=0 EndX=-1000 EndY=10 EndZ=0
    g8: LineSegment StartX=-1000 StartY=-30 StartZ=0 EndX=-996 EndY=-30 EndZ=0
    g9: LineSegment StartX=-996 StartY=-30 StartZ=0 EndX=-996 EndY=-50 EndZ=0
    g10: LineSegment StartX=-996 StartY=-50 StartZ=0 EndX=-1000 EndY=-50 EndZ=0
    g11: LineSegment StartX=-1000 StartY=-50 StartZ=0 EndX=-1000 EndY=-30 EndZ=0
    g12: LineSegment StartX=1000 StartY=50 StartZ=0 EndX=996 EndY=50 EndZ=0
    g13: LineSegment StartX=996 StartY=50 StartZ=0 EndX=996 EndY=30 EndZ=0
    g14: LineSegment StartX=996 StartY=30 StartZ=0 EndX=1000 EndY=30 EndZ=0
    g15: LineSegment StartX=1000 StartY=30 StartZ=0 EndX=1000 EndY=50 EndZ=0
    g16: LineSegment StartX=1000 StartY=-50 StartZ=0 EndX=996 EndY=-50 EndZ=0
    g17: LineSegment StartX=996 StartY=-50 StartZ=0 EndX=996 EndY=-30 EndZ=0
    g18: LineSegment StartX=996 StartY=-30 StartZ=0 EndX=1000 EndY=-30 EndZ=0
    g19: LineSegment StartX=1000 StartY=-30 StartZ=0 EndX=1000 EndY=-50 EndZ=0
    g20: LineSegment StartX=1000 StartY=-10 StartZ=0 EndX=996 EndY=-10 EndZ=0
    g21: LineSegment StartX=996 StartY=-10 StartZ=0 EndX=996 EndY=10 EndZ=0
    g22: LineSegment StartX=996 StartY=10 StartZ=0 EndX=1000 EndY=10 EndZ=0
    g23: LineSegment StartX=1000 StartY=10 StartZ=0 EndX=1000 EndY=-10 EndZ=0
    g24: GeomPoint X=-666.67 Y=0 Z=0
    g25: GeomPoint X=-333.34 Y=0 Z=0
    g26: GeomPoint X=-0.01 Y=0 Z=0
    g27: GeomPoint X=333.32 Y=0 Z=0
    g28: GeomPoint X=666.65 Y=0 Z=0
    g29: GeomPoint X=1000 Y=10 Z=0
    g30: GeomPoint X=999.98 Y=-53.2776 Z=0
    g31: LineSegment StartX=-664.67 StartY=-10 StartZ=0 EndX=-668.67 EndY=-10 EndZ=0
    g32: LineSegment StartX=-668.67 StartY=-10 StartZ=0 EndX=-668.67 EndY=10 EndZ=0
    g33: LineSegment StartX=-668.67 StartY=10 StartZ=0 EndX=-664.67 EndY=10 EndZ=0
    g34: LineSegment StartX=-664.67 StartY=10 StartZ=0 EndX=-664.67 EndY=-10 EndZ=0
    g35: LineSegment StartX=-668.67 StartY=50 StartZ=0 EndX=-664.67 EndY=50 EndZ=0
    g36: LineSegment StartX=-664.67 StartY=50 StartZ=0 EndX=-664.67 EndY=30 EndZ=0
    g37: LineSegment StartX=-664.67 StartY=30 StartZ=0 EndX=-668.67 EndY=30 EndZ=0
    g38: LineSegment StartX=-668.67 StartY=30 StartZ=0 EndX=-668.67 EndY=50 EndZ=0
    g39: LineSegment StartX=-668.67 StartY=-50 StartZ=0 EndX=-664.67 EndY=-50 EndZ=0
    g40: LineSegment StartX=-664.67 StartY=-50 StartZ=0 EndX=-664.67 EndY=-30 EndZ=0
    g41: LineSegment StartX=-664.67 StartY=-30 StartZ=0 EndX=-668.67 EndY=-30 EndZ=0
    g42: LineSegment StartX=-668.67 StartY=-30 StartZ=0 EndX=-668.67 EndY=-50 EndZ=0
    g43: LineSegment StartX=-335.34 StartY=50 StartZ=0 EndX=-331.34 EndY=50 EndZ=0
    g44: LineSegment StartX=-331.34 StartY=50 StartZ=0 EndX=-331.34 EndY=30 EndZ=0
    g45: LineSegment StartX=-331.34 StartY=30 StartZ=0 EndX=-335.34 EndY=30 EndZ=0
    g46: LineSegment StartX=-335.34 StartY=30 StartZ=0 EndX=-335.34 EndY=50 EndZ=0
    g47: LineSegment StartX=-335.34 StartY=10 StartZ=0 EndX=-331.34 EndY=10 EndZ=0
    g48: LineSegment StartX=-331.34 StartY=10 StartZ=0 EndX=-331.34 EndY=-10 EndZ=0
    g49: LineSegment StartX=-331.34 StartY=-10 StartZ=0 EndX=-335.34 EndY=-10 EndZ=0
    g50: LineSegment StartX=-335.34 StartY=-10 StartZ=0 EndX=-335.34 EndY=10 EndZ=0
    g51: LineSegment StartX=-335.34 StartY=-30 StartZ=0 EndX=-331.34 EndY=-30 EndZ=0
    g52: LineSegment StartX=-331.34 StartY=-30 StartZ=0 EndX=-331.34 EndY=-50 EndZ=0
    g53: LineSegment StartX=-331.34 StartY=-50 StartZ=0 EndX=-335.34 EndY=-50 EndZ=0
    g54: LineSegment StartX=-335.34 StartY=-50 StartZ=0 EndX=-335.34 EndY=-30 EndZ=0
    g55: LineSegment StartX=-2.01 StartY=50 StartZ=0 EndX=1.99 EndY=50 EndZ=0
    g56: LineSegment StartX=1.99 StartY=50 StartZ=0 EndX=1.99 EndY=30 EndZ=0
    g57: LineSegment StartX=1.99 StartY=30 StartZ=0 EndX=-2.01 EndY=30 EndZ=0
    g58: LineSegment StartX=-2.01 StartY=30 StartZ=0 EndX=-2.01 EndY=50 EndZ=0
    g59: LineSegment StartX=-2.01 StartY=10 StartZ=0 EndX=1.99 EndY=10 EndZ=0
    g60: LineSegment StartX=1.99 StartY=10 StartZ=0 EndX=1.99 EndY=-10 EndZ=0
    g61: LineSegment StartX=1.99 StartY=-10 StartZ=0 EndX=-2.01 EndY=-10 EndZ=0
    g62: LineSegment StartX=-2.01 StartY=-10 StartZ=0 EndX=-2.01 EndY=10 EndZ=0
    g63: LineSegment StartX=-2.01 StartY=-30 StartZ=0 EndX=1.99 EndY=-30 EndZ=0
    g64: LineSegment StartX=1.99 StartY=-30 StartZ=0 EndX=1.99 EndY=-50 EndZ=0
    g65: LineSegment StartX=1.99 StartY=-50 StartZ=0 EndX=-2.01 EndY=-50 EndZ=0
    g66: LineSegment StartX=-2.01 StartY=-50 StartZ=0 EndX=-2.01 EndY=-30 EndZ=0
    g67: LineSegment StartX=331.32 StartY=50 StartZ=0 EndX=335.32 EndY=50 EndZ=0
    g68: LineSegment StartX=335.32 StartY=50 StartZ=0 EndX=335.32 EndY=30 EndZ=0
    g69: LineSegment StartX=335.32 StartY=30 StartZ=0 EndX=331.32 EndY=30 EndZ=0
    g70: LineSegment StartX=331.32 StartY=30 StartZ=0 EndX=331.32 EndY=50 EndZ=0
    g71: LineSegment StartX=331.32 StartY=10 StartZ=0 EndX=335.32 EndY=10 EndZ=0
    g72: LineSegment StartX=335.32 StartY=10 StartZ=0 EndX=335.32 EndY=-10 EndZ=0
    g73: LineSegment StartX=335.32 StartY=-10 StartZ=0 EndX=331.32 EndY=-10 EndZ=0
    g74: LineSegment StartX=331.32 StartY=-10 StartZ=0 EndX=331.32 EndY=10 EndZ=0
    g75: LineSegment StartX=331.32 StartY=-30 StartZ=0 EndX=335.32 EndY=-30 EndZ=0
    g76: LineSegment StartX=335.32 StartY=-30 StartZ=0 EndX=335.32 EndY=-50 EndZ=0
    g77: LineSegment StartX=335.32 StartY=-50 StartZ=0 EndX=331.32 EndY=-50 EndZ=0
    g78: LineSegment StartX=331.32 StartY=-50 StartZ=0 EndX=331.32 EndY=-30 EndZ=0
    g79: LineSegment StartX=664.65 StartY=50 StartZ=0 EndX=668.65 EndY=50 EndZ=0
    g80: LineSegment StartX=668.65 StartY=50 StartZ=0 EndX=668.65 EndY=30 EndZ=0
    g81: LineSegment StartX=668.65 StartY=30 StartZ=0 EndX=664.65 EndY=30 EndZ=0
    g82: LineSegment StartX=664.65 StartY=30 StartZ=0 EndX=664.65 EndY=50 EndZ=0
    g83: LineSegment StartX=664.65 StartY=10 StartZ=0 EndX=668.65 EndY=10 EndZ=0
    g84: LineSegment StartX=668.65 StartY=10 StartZ=0 EndX=668.65 EndY=-10 EndZ=0
    g85: LineSegment StartX=668.65 StartY=-10 StartZ=0 EndX=664.65 EndY=-10 EndZ=0
    g86: LineSegment StartX=664.65 StartY=-10 StartZ=0 EndX=664.65 EndY=10 EndZ=0
    g87: LineSegment StartX=664.65 StartY=-30 StartZ=0 EndX=668.65 EndY=-30 EndZ=0
    g88: LineSegment StartX=668.65 StartY=-30 StartZ=0 EndX=668.65 EndY=-50 EndZ=0
    g89: LineSegment StartX=668.65 StartY=-50 StartZ=0 EndX=664.65 EndY=-50 EndZ=0
    g90: LineSegment StartX=664.65 StartY=-50 StartZ=0 EndX=664.65 EndY=-30 EndZ=0
  constraints (259):
    c: Coincident(g0,g1)
    c: Coincident(g1,g2)
    c: Coincident(g2,g3)
    c: Coincident(g3,g0)
    c: Horizontal(g0)
    c: Horizontal(g2)
    c: Vertical(g1)
    c: Vertical(g3)
    c: Coincident(g0,g-3)
    c: Coincident(g4,g5)
    c: Coincident(g5,g6)
    c: Coincident(g6,g7)
    c: Coincident(g7,g4)
    c: Horizontal(g4)
    c: Horizontal(g6)
    c: Vertical(g5)
    c: Vertical(g7)
    c: Coincident(g8,g9)
    c: Coincident(g9,g10)
    c: Coincident(g10,g11)
    c: Coincident(g11,g8)
    c: Horizontal(g8)
    c: Horizontal(g10)
    c: Vertical(g9)
    c: Vertical(g11)
    c: DistanceX(g0,g0) = 4
    c: DistanceY(g2,g0) = 20
    c: DistanceY(g4,g2) = 20
    c: DistanceY(g6,g4) = 20
    c: DistanceY(g8,g6) = 20
    c: DistanceY(g10,g8) = 20
    c: Vertical(g4,g1)
    c: Vertical(g8,g5)
    c: Coincident(g12,g13)
    c: Coincident(g13,g14)
    c: Coincident(g14,g15)
    c: Coincident(g15,g12)
    c: Horizontal(g12)
    c: Horizontal(g14)
    c: Vertical(g13)
    c: Vertical(g15)
    c: Coincident(g12,g-5)
    c: Coincident(g16,g17)
    c: Coincident(g17,g18)
    c: Coincident(g18,g19)
    c: Coincident(g19,g16)
    c: Horizontal(g16)
    c: Horizontal(g18)
    c: Vertical(g17)
    c: Vertical(g19)
    c: Coincident(g16,g-6)
    c: Coincident(g20,g21)
    c: Coincident(g21,g22)
    c: Coincident(g22,g23)
    c: Coincident(g23,g20)
    c: Horizontal(g20)
    c: Horizontal(g22)
    c: Vertical(g21)
    c: Vertical(g23)
    c: DistanceX(g12,g12) = 4
    c: Vertical(g21,g13)
    c: Vertical(g17,g20)
    c: Horizontal(g13,g1)
    c: Horizontal(g4,g21)
    c: Horizontal(g20,g5)
    c: Horizontal(g8,g17)
    c: Vertical(g14,g22)
    c: Vertical(g2,g4)
    c: Vertical(g6,g8)
    c: DistanceX(g0,g24) = 333.33
    c: DistanceX(g24,g25) = 333.33
    c: PointOnObject(g26,g-1)
    c: DistanceX(g25,g26) = 333.33
    c: PointOnObject(g27,g-1)
    c: PointOnObject(g28,g-1)
    c: DistanceX(g26,g27) = 333.33
    c: DistanceX(g27,g28) = 333.33
    c: Coincident(g29,g22)
    c: DistanceX(g28,g30) = 333.33
    c: Coincident(g31,g32)
    c: Coincident(g32,g33)
    c: Coincident(g33,g34)
    c: Coincident(g34,g31)
    c: Horizontal(g31)
    c: Horizontal(g33)
    c: Vertical(g32)
    c: Vertical(g34)
    c: Horizontal(g4,g32)
    c: Horizontal(g31,g5)
    c: Coincident(g35,g36)
    c: Coincident(g36,g37)
    c: Coincident(g37,g38)
    c: Coincident(g38,g35)
    c: Horizontal(g35)
    c: Horizontal(g37)
    c: Vertical(g36)
    c: Vertical(g38)
    c: DistanceX(g35,g35) = 4
    c: Horizontal(g35,g0)
    c: DistanceX(g35,g24) = 2
    c: Horizontal(g37,g1)
    c: Vertical(g36,g33)
    c: Vertical(g32,g37)
    c: Coincident(g39,g40)
    c: Coincident(g40,g41)
    c: Coincident(g41,g42)
    c: Coincident(g42,g39)
    c: Horizontal(g39)
    c: Horizontal(g41)
    c: Vertical(g40)
    c: Vertical(g42)
    c: Vertical(g31,g41)
    c: Vertical(g31,g40)
    c: Horizontal(g8,g41)
    c: Horizontal(g39,g9)
    c: Coincident(g43,g44)
    c: Coincident(g44,g45)
    c: Coincident(g45,g46)
    c: Coincident(g46,g43)
    c: Horizontal(g43)
    c: Horizontal(g45)
    c: Vertical(g44)
    c: Vertical(g46)
    c: Coincident(g47,g48)
    c: Coincident(g48,g49)
    c: Coincident(g49,g50)
    c: Coincident(g50,g47)
    c: Horizontal(g47)
    c: Horizontal(g49)
    c: Vertical(g48)
    c: Vertical(g50)
    c: Coincident(g51,g52)
    c: Coincident(g52,g53)
    c: Coincident(g53,g54)
    c: Coincident(g54,g51)
    c: Horizontal(g51)
    c: Horizontal(g53)
    c: Vertical(g52)
    c: Vertical(g54)
    c: Horizontal(g43,g35)
    c: Horizontal(g36,g45)
    c: Horizontal(g33,g47)
    c: Horizontal(g31,g49)
    c: Horizontal(g51,g40)
    c: Horizontal(g39,g53)
    c: Vertical(g45,g47)
    c: Vertical(g44,g47)
    c: Vertical(g51,g49)
    c: Vertical(g51,g48)
    c: DistanceX(g43,g43) = 4
    c: DistanceX(g43,g25) = 2
    c: Coincident(g55,g56)
    c: Coincident(g56,g57)
    c: Coincident(g57,g58)
    c: Coincident(g58,g55)
    c: Horizontal(g55)
    c: Horizontal(g57)
    c: Vertical(g56)
    c: Vertical(g58)
    c: Coincident(g59,g60)
    c: Coincident(g60,g61)
    c: Coincident(g61,g62)
    c: Coincident(g62,g59)
    c: Horizontal(g59)
    c: Horizontal(g61)
    c: Vertical(g60)
    c: Vertical(g62)
    c: Coincident(g63,g64)
    c: Coincident(g64,g65)
    c: Coincident(g65,g66)
    c: Coincident(g66,g63)
    c: Horizontal(g63)
    c: Horizontal(g65)
    c: Vertical(g64)
    c: Vertical(g66)
    c: Horizontal(g43,g55)
    c: Horizontal(g44,g57)
    c: Horizontal(g47,g59)
    c: Horizontal(g48,g61)
    c: Horizontal(g63,g51)
    c: Horizontal(g52,g65)
    c: Vertical(g57,g59)
    c: Vertical(g63,g61)
    c: Vertical(g63,g60)
    c: Vertical(g59,g56)
    c: DistanceX(g55,g55) = 4
    c: DistanceX(g55,g26) = 2
    c: Coincident(g67,g68)
    c: Coincident(g68,g69)
    c: Coincident(g69,g70)
    c: Coincident(g70,g67)
    c: Horizontal(g67)
    c: Horizontal(g69)
    c: Vertical(g68)
    c: Vertical(g70)
    c: Coincident(g71,g72)
    c: Coincident(g72,g73)
    c: Coincident(g73,g74)
    c: Coincident(g74,g71)
    c: Horizontal(g71)
    c: Horizontal(g73)
    c: Vertical(g72)
    c: Vertical(g74)
    c: Coincident(g75,g76)
    c: Coincident(g76,g77)
    c: Coincident(g77,g78)
    c: Coincident(g78,g75)
    c: Horizontal(g75)
    c: Horizontal(g77)
    c: Vertical(g76)
    c: Vertical(g78)
    c: Horizontal(g55,g67)
    c: Horizontal(g56,g69)
    c: Horizontal(g59,g71)
    c: Horizontal(g60,g73)
    c: Horizontal(g63,g75)
    c: Horizontal(g64,g77)
    c: Vertical(g69,g71)
    c: Vertical(g73,g75)
    c: Vertical(g68,g71)
    c: Vertical(g72,g75)
    c: DistanceX(g67,g67) = 4
    c: DistanceX(g67,g27) = 2
    c: Coincident(g79,g80)
    c: Coincident(g80,g81)
    c: Coincident(g81,g82)
    c: Coincident(g82,g79)
    c: Horizontal(g79)
    c: Horizontal(g81)
    c: Vertical(g80)
    c: Vertical(g82)
    c: Coincident(g83,g84)
    c: Coincident(g84,g85)
    c: Coincident(g85,g86)
    c: Coincident(g86,g83)
    c: Horizontal(g83)
    c: Horizontal(g85)
    c: Vertical(g84)
    c: Vertical(g86)
    c: Coincident(g87,g88)
    c: Coincident(g88,g89)
    c: Coincident(g89,g90)
    c: Coincident(g90,g87)
    c: Horizontal(g87)
    c: Horizontal(g89)
    c: Vertical(g88)
    c: Vertical(g90)
    c: Horizontal(g67,g79)
    c: Horizontal(g68,g81)
    c: Horizontal(g71,g83)
    c: Horizontal(g72,g85)
    c: Horizontal(g75,g87)
    c: Horizontal(g76,g89)
    c: Vertical(g81,g83)
    c: Vertical(g85,g87)
    c: Vertical(g80,g83)
    c: Vertical(g84,g87)
    c: DistanceX(g79,g79) = 4
    c: DistanceX(g79,g28) = 2
FEATURE [PartDesign::Pocket] Pocket002
  BaseFeature = -> Pad002
  Length = 4
  Length2 = 5
  Placement = pos=(0,0,0) rot=(1,0,0;1.5708rad)
  Profile = -> Sketch005
  Type = 0
FEATURE [PartDesign::Body] Body002  label="Fram/Bakkant-Inre-2"
  Group = -> [Sketch004,Pad002,Sketch005,Pocket002]
  Origin = -> Origin002
  Placement = pos=(0,600,0) rot=(0,0,1;0rad)
  Tip = -> Pocket002
FEATURE [Sketcher::SketchObject] Sketch006
  FullyConstrained = false
  MapMode = 5
  Placement = pos=(0,0,0) rot=(0.57735,0.57735,0.57735;2.0944rad)
  Support = -> [YZ_Plane003]
  sketch-geometry (4):
    g0: LineSegment StartX=-600 StartY=-50 StartZ=0 EndX=-600 EndY=50 EndZ=0
    g1: LineSegment StartX=-600 StartY=50 StartZ=0 EndX=600 EndY=50 EndZ=0
    g2: LineSegment StartX=600 StartY=50 StartZ=0 EndX=600 EndY=-50 EndZ=0
    g3: LineSegment StartX=600 StartY=-50 StartZ=0 EndX=-600 EndY=-50 EndZ=0
  constraints (10):
    c: Coincident(g0,g1)
    c: Coincident(g1,g2)
    c: Coincident(g2,g3)
    c: Coincident(g3,g0)
    c: Horizontal(g1)
    c: Horizontal(g3)
    c: Vertical(g0)
    c: Vertical(g2)
    c: DistanceY(g0,g0) = 100
    c: DistanceX(g0,g2) = 1200
FEATURE [PartDesign::Pad] Pad003
  Direction = (1,-2e-16,3e-16)
  Length = 4
  Length2 = 10
  Placement = pos=(0,0,0) rot=(0.57735,0.57735,0.57735;2.0944rad)
  Profile = -> Sketch006
  Type = 0
FEATURE [Sketcher::SketchObject] Sketch007
  FullyConstrained = true
  MapMode = 5
  Placement = pos=(0,0,0) rot=(0.57735,0.57735,0.57735;2.0944rad)
  Support = -> [YZ_Plane003]
FEATURE [Sketcher::SketchObject] Sketch008
  ExternalGeometry = -> [Pad003]
  FullyConstrained = false
  MapMode = 5
  Placement = pos=(4,-9e-16,9e-16) rot=(0.57735,0.57735,0.57735;2.0944rad)
  Support = -> [Pad003]
  sketch-geometry (45):
    g0: GeomPoint X=-300 Y=0 Z=0
    g1: GeomPoint X=300 Y=0 Z=0
    g2: GeomPoint X=-2.189e-13 Y=0 Z=0
    g3: GeomPoint X=600 Y=0 Z=0
    g4: LineSegment StartX=-600 StartY=30 StartZ=0 EndX=-596 EndY=30 EndZ=0
    g5: LineSegment StartX=-596 StartY=30 StartZ=0 EndX=-596 EndY=10 EndZ=0
    g6: LineSegment StartX=-596 StartY=10 StartZ=0 EndX=-600 EndY=10 EndZ=0
    g7: LineSegment StartX=-600 StartY=10 StartZ=0 EndX=-600 EndY=30 EndZ=0
    g8: LineSegment StartX=-600 StartY=-10 StartZ=0 EndX=-596 EndY=-10 EndZ=0
    g9: LineSegment StartX=-596 StartY=-10 StartZ=0 EndX=-596 EndY=-30 EndZ=0
    g10: LineSegment StartX=-596 StartY=-30 StartZ=0 EndX=-600 EndY=-30 EndZ=0
    g11: LineSegment StartX=-600 StartY=-30 StartZ=0 EndX=-600 EndY=-10 EndZ=0
    g12: LineSegment StartX=-302 StartY=-10 StartZ=0 EndX=-298 EndY=-10 EndZ=0
    g13: LineSegment StartX=-298 StartY=-10 StartZ=0 EndX=-298 EndY=-30 EndZ=0
    g14: LineSegment StartX=-298 StartY=-30 StartZ=0 EndX=-302 EndY=-30 EndZ=0
    g15: LineSegment StartX=-302 StartY=-30 StartZ=0 EndX=-302 EndY=-10 EndZ=0
    g16: LineSegment StartX=-2 StartY=30 StartZ=0 EndX=2 EndY=30 EndZ=0
    g17: LineSegment StartX=2 StartY=30 StartZ=0 EndX=2 EndY=10 EndZ=0
    g18: LineSegment StartX=2 StartY=10 StartZ=0 EndX=-2 EndY=10 EndZ=0
    g19: LineSegment StartX=-2 StartY=10 StartZ=0 EndX=-2 EndY=30 EndZ=0
    g20: LineSegment StartX=-2 StartY=-10 StartZ=0 EndX=2 EndY=-10 EndZ=0
    g21: LineSegment StartX=2 StartY=-10 StartZ=0 EndX=2 EndY=-30 EndZ=0
    g22: LineSegment StartX=2 StartY=-30 StartZ=0 EndX=-2 EndY=-30 EndZ=0
    g23: LineSegment StartX=-2 StartY=-30 StartZ=0 EndX=-2 EndY=-10 EndZ=0
    g24: LineSegment StartX=298 StartY=30 StartZ=0 EndX=302 EndY=30 EndZ=0
    g25: LineSegment StartX=302 StartY=30 StartZ=0 EndX=302 EndY=10 EndZ=0
    g26: LineSegment StartX=302 StartY=10 StartZ=0 EndX=298 EndY=10 EndZ=0
    g27: LineSegment StartX=298 StartY=10 StartZ=0 EndX=298 EndY=30 EndZ=0
    g28: LineSegment StartX=298 StartY=-10 StartZ=0 EndX=302 EndY=-10 EndZ=0
    g29: LineSegment StartX=302 StartY=-10 StartZ=0 EndX=302 EndY=-30 EndZ=0
    g30: LineSegment StartX=302 StartY=-30 StartZ=0 EndX=298 EndY=-30 EndZ=0
    g31: LineSegment StartX=298 StartY=-30 StartZ=0 EndX=298 EndY=-10 EndZ=0
    g32: LineSegment StartX=600 StartY=30 StartZ=0 EndX=596 EndY=30 EndZ=0
    g33: LineSegment StartX=596 StartY=30 StartZ=0 EndX=596 EndY=10 EndZ=0
    g34: LineSegment StartX=596 StartY=10 StartZ=0 EndX=600 EndY=10 EndZ=0
    g35: LineSegment StartX=600 StartY=10 StartZ=0 EndX=600 EndY=30 EndZ=0
    g36: GeomPoint X=-600 Y=-50 Z=0
    g37: LineSegment StartX=-302 StartY=30 StartZ=0 EndX=-298 EndY=30 EndZ=0
    g38: LineSegment StartX=-298 StartY=30 StartZ=0 EndX=-298 EndY=10 EndZ=0
    g39: LineSegment StartX=-298 StartY=10 StartZ=0 EndX=-302 EndY=10 EndZ=0
    g40: LineSegment StartX=-302 StartY=10 StartZ=0 EndX=-302 EndY=30 EndZ=0
    g41: LineSegment StartX=600 StartY=-30 StartZ=0 EndX=596 EndY=-30 EndZ=0
    g42: LineSegment StartX=596 StartY=-30 StartZ=0 EndX=596 EndY=-10 EndZ=0
    g43: LineSegment StartX=596 StartY=-10 StartZ=0 EndX=600 EndY=-10 EndZ=0
    g44: LineSegment StartX=600 StartY=-10 StartZ=0 EndX=600 EndY=-30 EndZ=0
  constraints (125):
    c: DistanceX(g-3,g0) = 300
    c: DistanceX(g0,g2) = 300
    c: DistanceX(g2,g1) = 300
    c: DistanceX(g1,g3) = 300
    c: Coincident(g4,g5)
    c: Coincident(g5,g6)
    c: Coincident(g6,g7)
    c: Coincident(g7,g4)
    c: Horizontal(g4)
    c: Horizontal(g6)
    c: Vertical(g5)
    c: Vertical(g7)
    c: Coincident(g8,g9)
    c: Coincident(g9,g10)
    c: Coincident(g10,g11)
    c: Coincident(g11,g8)
    c: Horizontal(g8)
    c: Horizontal(g10)
    c: Vertical(g9)
    c: Vertical(g11)
    c: Coincident(g12,g13)
    c: Coincident(g13,g14)
    c: Coincident(g14,g15)
    c: Coincident(g15,g12)
    c: Horizontal(g12)
    c: Horizontal(g14)
    c: Vertical(g13)
    c: Vertical(g15)
    c: Coincident(g16,g17)
    c: Coincident(g17,g18)
    c: Coincident(g18,g19)
    c: Coincident(g19,g16)
    c: Horizontal(g16)
    c: Horizontal(g18)
    c: Vertical(g17)
    c: Vertical(g19)
    c: Coincident(g20,g21)
    c: Coincident(g21,g22)
    c: Coincident(g22,g23)
    c: Coincident(g23,g20)
    c: Horizontal(g20)
    c: Horizontal(g22)
    c: Vertical(g21)
    c: Vertical(g23)
    c: Coincident(g24,g25)
    c: Coincident(g25,g26)
    c: Coincident(g26,g27)
    c: Coincident(g27,g24)
    c: Horizontal(g24)
    c: Horizontal(g26)
    c: Vertical(g25)
    c: Vertical(g27)
    c: Coincident(g28,g29)
    c: Coincident(g29,g30)
    c: Coincident(g30,g31)
    c: Coincident(g31,g28)
    c: Horizontal(g28)
    c: Horizontal(g30)
    c: Vertical(g29)
    c: Vertical(g31)
    c: Coincident(g32,g33)
    c: Coincident(g33,g34)
    c: Coincident(g34,g35)
    c: Coincident(g35,g32)
    c: Horizontal(g32)
    c: Horizontal(g34)
    c: Vertical(g33)
    c: Vertical(g35)
    c: Vertical(g-3,g4)
    c: Vertical(g6,g8)
    c: Vertical(g8,g5)
    c: DistanceX(g4,g4) = 4
    c: DistanceY(g4,g-3) = 20
    c: DistanceY(g6,g4) = 20
    c: DistanceY(g8,g6) = 20
    c: DistanceY(g10,g8) = 20
    c: DistanceY(g36,g10) = 20
    c: Coincident(g37,g38)
    c: Coincident(g38,g39)
    c: Coincident(g39,g40)
    c: Coincident(g40,g37)
    c: Horizontal(g37)
    c: Horizontal(g39)
    c: Vertical(g38)
    c: Vertical(g40)
    c: Horizontal(g4,g37)
    c: Horizontal(g5,g39)
    c: Horizontal(g8,g12)
    c: Horizontal(g9,g14)
    c: Vertical(g39,g12)
    c: Vertical(g38,g12)
    c: DistanceX(g37,g37) = 4
    c: DistanceX(g37,g0) = 2
    c: Horizontal(g37,g16)
    c: Horizontal(g38,g18)
    c: Horizontal(g12,g20)
    c: Horizontal(g13,g22)
    c: Vertical(g18,g20)
    c: Vertical(g17,g20)
    c: DistanceX(g16,g16) = 4
    c: DistanceX(g16,g2) = 2
    c: Horizontal(g16,g24)
    c: Horizontal(g17,g26)
    c: Horizontal(g20,g28)
    c: Horizontal(g21,g30)
    c: Vertical(g26,g28)
    c: Vertical(g25,g28)
    c: DistanceX(g24,g24) = 4
    c: DistanceX(g24,g1) = 2
    c: Coincident(g41,g42)
    c: Coincident(g42,g43)
    c: Coincident(g43,g44)
    c: Coincident(g44,g41)
    c: Horizontal(g41)
    c: Horizontal(g43)
    c: Vertical(g42)
    c: Vertical(g44)
    c: Horizontal(g24,g32)
    c: Horizontal(g25,g33)
    c: Horizontal(g28,g42)
    c: Horizontal(g29,g41)
    c: Vertical(g33,g42)
    c: Vertical(g34,g43)
    c: DistanceX(g32,g32) = 4
    c: Vertical(g-6,g32)
FEATURE [PartDesign::Pocket] Pocket003
  BaseFeature = -> Pad003
  Length = 4
  Length2 = 5
  Placement = pos=(0,0,0) rot=(0.57735,0.57735,0.57735;2.0944rad)
  Profile = -> Sketch008
  Type = 0
FEATURE [PartDesign::Body] Body003  label="Sidkant-Inre-1"
  Group = -> [Sketch006,Pad003,Sketch007,Sketch008,Pocket003]
  Origin = -> Origin003
  Placement = pos=(-1000,0,0) rot=(0,0,1;0rad)
  Tip = -> Pocket003
FEATURE [Sketcher::SketchObject] Sketch009
  FullyConstrained = false
  MapMode = 5
  Placement = pos=(0,0,0) rot=(0.57735,0.57735,0.57735;2.0944rad)
  Support = -> [YZ_Plane004]
  sketch-geometry (4):
    g0: LineSegment StartX=-600 StartY=-50 StartZ=0 EndX=-600 EndY=50 EndZ=0
    g1: LineSegment StartX=-600 StartY=50 StartZ=0 EndX=600 EndY=50 EndZ=0
    g2: LineSegment StartX=600 StartY=50 StartZ=0 EndX=600 EndY=-50 EndZ=0
    g3: LineSegment StartX=600 StartY=-50 StartZ=0 EndX=-600 EndY=-50 EndZ=0
  constraints (10):
    c: Coincident(g0,g1)
    c: Coincident(g1,g2)
    c: Coincident(g2,g3)
    c: Coincident(g3,g0)
    c: Horizontal(g1)
    c: Horizontal(g3)
    c: Vertical(g0)
    c: Vertical(g2)
    c: DistanceY(g0,g0) = 100
    c: DistanceX(g0,g2) = 1200
FEATURE [PartDesign::Pad] Pad004
  Direction = (1,-2e-16,3e-16)
  Length = 4
  Length2 = 10
  Placement = pos=(0,0,0) rot=(0.57735,0.57735,0.57735;2.0944rad)
  Profile = -> Sketch009
  Type = 0
FEATURE [Sketcher::SketchObject] Sketch010
  FullyConstrained = true
  MapMode = 5
  Placement = pos=(0,0,0) rot=(0.57735,0.57735,0.57735;2.0944rad)
  Support = -> [YZ_Plane004]
FEATURE [Sketcher::SketchObject] Sketch011
  ExternalGeometry = -> [Pad004]
  FullyConstrained = false
  MapMode = 5
  Placement = pos=(4,-9e-16,9e-16) rot=(0.57735,0.57735,0.57735;2.0944rad)
  Support = -> [Pad004]
  sketch-geometry (45):
    g0: GeomPoint X=-300 Y=0 Z=0
    g1: GeomPoint X=300 Y=0 Z=0
    g2: GeomPoint X=-2.189e-13 Y=0 Z=0
    g3: GeomPoint X=600 Y=0 Z=0
    g4: LineSegment StartX=-600 StartY=30 StartZ=0 EndX=-596 EndY=30 EndZ=0
    g5: LineSegment StartX=-596 StartY=30 StartZ=0 EndX=-596 EndY=10 EndZ=0
    g6: LineSegment StartX=-596 StartY=10 StartZ=0 EndX=-600 EndY=10 EndZ=0
    g7: LineSegment StartX=-600 StartY=10 StartZ=0 EndX=-600 EndY=30 EndZ=0
    g8: LineSegment StartX=-600 StartY=-10 StartZ=0 EndX=-596 EndY=-10 EndZ=0
    g9: LineSegment StartX=-596 StartY=-10 StartZ=0 EndX=-596 EndY=-30 EndZ=0
    g10: LineSegment StartX=-596 StartY=-30 StartZ=0 EndX=-600 EndY=-30 EndZ=0
    g11: LineSegment StartX=-600 StartY=-30 StartZ=0 EndX=-600 EndY=-10 EndZ=0
    g12: LineSegment StartX=-302 StartY=-10 StartZ=0 EndX=-298 EndY=-10 EndZ=0
    g13: LineSegment StartX=-298 StartY=-10 StartZ=0 EndX=-298 EndY=-30 EndZ=0
    g14: LineSegment StartX=-298 StartY=-30 StartZ=0 EndX=-302 EndY=-30 EndZ=0
    g15: LineSegment StartX=-302 StartY=-30 StartZ=0 EndX=-302 EndY=-10 EndZ=0
    g16: LineSegment StartX=-2 StartY=30 StartZ=0 EndX=2 EndY=30 EndZ=0
    g17: LineSegment StartX=2 StartY=30 StartZ=0 EndX=2 EndY=10 EndZ=0
    g18: LineSegment StartX=2 StartY=10 StartZ=0 EndX=-2 EndY=10 EndZ=0
    g19: LineSegment StartX=-2 StartY=10 StartZ=0 EndX=-2 EndY=30 EndZ=0
    g20: LineSegment StartX=-2 StartY=-10 StartZ=0 EndX=2 EndY=-10 EndZ=0
    g21: LineSegment StartX=2 StartY=-10 StartZ=0 EndX=2 EndY=-30 EndZ=0
    g22: LineSegment StartX=2 StartY=-30 StartZ=0 EndX=-2 EndY=-30 EndZ=0
    g23: LineSegment StartX=-2 StartY=-30 StartZ=0 EndX=-2 EndY=-10 EndZ=0
    g24: LineSegment StartX=298 StartY=30 StartZ=0 EndX=302 EndY=30 EndZ=0
    g25: LineSegment StartX=302 StartY=30 StartZ=0 EndX=302 EndY=10 EndZ=0
    g26: LineSegment StartX=302 StartY=10 StartZ=0 EndX=298 EndY=10 EndZ=0
    g27: LineSegment StartX=298 StartY=10 StartZ=0 EndX=298 EndY=30 EndZ=0
    g28: LineSegment StartX=298 StartY=-10 StartZ=0 EndX=302 EndY=-10 EndZ=0
    g29: LineSegment StartX=302 StartY=-10 StartZ=0 EndX=302 EndY=-30 EndZ=0
    g30: LineSegment StartX=302 StartY=-30 StartZ=0 EndX=298 EndY=-30 EndZ=0
    g31: LineSegment StartX=298 StartY=-30 StartZ=0 EndX=298 EndY=-10 EndZ=0
    g32: LineSegment StartX=600 StartY=30 StartZ=0 EndX=596 EndY=30 EndZ=0
    g33: LineSegment StartX=596 StartY=30 StartZ=0 EndX=596 EndY=10 EndZ=0
    g34: LineSegment StartX=596 StartY=10 StartZ=0 EndX=600 EndY=10 EndZ=0
    g35: LineSegment StartX=600 StartY=10 StartZ=0 EndX=600 EndY=30 EndZ=0
    g36: GeomPoint X=-600 Y=-50 Z=0
    g37: LineSegment StartX=-302 StartY=30 StartZ=0 EndX=-298 EndY=30 EndZ=0
    g38: LineSegment StartX=-298 StartY=30 StartZ=0 EndX=-298 EndY=10 EndZ=0
    g39: LineSegment StartX=-298 StartY=10 StartZ=0 EndX=-302 EndY=10 EndZ=0
    g40: LineSegment StartX=-302 StartY=10 StartZ=0 EndX=-302 EndY=30 EndZ=0
    g41: LineSegment StartX=600 StartY=-30 StartZ=0 EndX=596 EndY=-30 EndZ=0
    g42: LineSegment StartX=596 StartY=-30 StartZ=0 EndX=596 EndY=-10 EndZ=0
    g43: LineSegment StartX=596 StartY=-10 StartZ=0 EndX=600 EndY=-10 EndZ=0
    g44: LineSegment StartX=600 StartY=-10 StartZ=0 EndX=600 EndY=-30 EndZ=0
  constraints (125):
    c: DistanceX(g-3,g0) = 300
    c: DistanceX(g0,g2) = 300
    c: DistanceX(g2,g1) = 300
    c: DistanceX(g1,g3) = 300
    c: Coincident(g4,g5)
    c: Coincident(g5,g6)
    c: Coincident(g6,g7)
    c: Coincident(g7,g4)
    c: Horizontal(g4)
    c: Horizontal(g6)
    c: Vertical(g5)
    c: Vertical(g7)
    c: Coincident(g8,g9)
    c: Coincident(g9,g10)
    c: Coincident(g10,g11)
    c: Coincident(g11,g8)
    c: Horizontal(g8)
    c: Horizontal(g10)
    c: Vertical(g9)
    c: Vertical(g11)
    c: Coincident(g12,g13)
    c: Coincident(g13,g14)
    c: Coincident(g14,g15)
    c: Coincident(g15,g12)
    c: Horizontal(g12)
    c: Horizontal(g14)
    c: Vertical(g13)
    c: Vertical(g15)
    c: Coincident(g16,g17)
    c: Coincident(g17,g18)
    c: Coincident(g18,g19)
    c: Coincident(g19,g16)
    c: Horizontal(g16)
    c: Horizontal(g18)
    c: Vertical(g17)
    c: Vertical(g19)
    c: Coincident(g20,g21)
    c: Coincident(g21,g22)
    c: Coincident(g22,g23)
    c: Coincident(g23,g20)
    c: Horizontal(g20)
    c: Horizontal(g22)
    c: Vertical(g21)
    c: Vertical(g23)
    c: Coincident(g24,g25)
    c: Coincident(g25,g26)
    c: Coincident(g26,g27)
    c: Coincident(g27,g24)
    c: Horizontal(g24)
    c: Horizontal(g26)
    c: Vertical(g25)
    c: Vertical(g27)
    c: Coincident(g28,g29)
    c: Coincident(g29,g30)
    c: Coincident(g30,g31)
    c: Coincident(g31,g28)
    c: Horizontal(g28)
    c: Horizontal(g30)
    c: Vertical(g29)
    c: Vertical(g31)
    c: Coincident(g32,g33)
    c: Coincident(g33,g34)
    c: Coincident(g34,g35)
    c: Coincident(g35,g32)
    c: Horizontal(g32)
    c: Horizontal(g34)
    c: Vertical(g33)
    c: Vertical(g35)
    c: Vertical(g-3,g4)
    c: Vertical(g6,g8)
    c: Vertical(g8,g5)
    c: DistanceX(g4,g4) = 4
    c: DistanceY(g4,g-3) = 20
    c: DistanceY(g6,g4) = 20
    c: DistanceY(g8,g6) = 20
    c: DistanceY(g10,g8) = 20
    c: DistanceY(g36,g10) = 20
    c: Coincident(g37,g38)
    c: Coincident(g38,g39)
    c: Coincident(g39,g40)
    c: Coincident(g40,g37)
    c: Horizontal(g37)
    c: Horizontal(g39)
    c: Vertical(g38)
    c: Vertical(g40)
    c: Horizontal(g4,g37)
    c: Horizontal(g5,g39)
    c: Horizontal(g8,g12)
    c: Horizontal(g9,g14)
    c: Vertical(g39,g12)
    c: Vertical(g38,g12)
    c: DistanceX(g37,g37) = 4
    c: DistanceX(g37,g0) = 2
    c: Horizontal(g37,g16)
    c: Horizontal(g38,g18)
    c: Horizontal(g12,g20)
    c: Horizontal(g13,g22)
    c: Vertical(g18,g20)
    c: Vertical(g17,g20)
    c: DistanceX(g16,g16) = 4
    c: DistanceX(g16,g2) = 2
    c: Horizontal(g16,g24)
    c: Horizontal(g17,g26)
    c: Horizontal(g20,g28)
    c: Horizontal(g21,g30)
    c: Vertical(g26,g28)
    c: Vertical(g25,g28)
    c: DistanceX(g24,g24) = 4
    c: DistanceX(g24,g1) = 2
    c: Coincident(g41,g42)
    c: Coincident(g42,g43)
    c: Coincident(g43,g44)
    c: Coincident(g44,g41)
    c: Horizontal(g41)
    c: Horizontal(g43)
    c: Vertical(g42)
    c: Vertical(g44)
    c: Horizontal(g24,g32)
    c: Horizontal(g25,g33)
    c: Horizontal(g28,g42)
    c: Horizontal(g29,g41)
    c: Vertical(g33,g42)
    c: Vertical(g34,g43)
    c: DistanceX(g32,g32) = 4
    c: Vertical(g-6,g32)
FEATURE [PartDesign::Pocket] Pocket004
  BaseFeature = -> Pad004
  Length = 4
  Length2 = 5
  Placement = pos=(0,0,0) rot=(0.57735,0.57735,0.57735;2.0944rad)
  Profile = -> Sketch011
  Type = 0
FEATURE [PartDesign::Body] Body004  label="Sidkant-Inre-2"
  Group = -> [Sketch009,Pad004,Sketch010,Sketch011,Pocket004]
  Origin = -> Origin004
  Placement = pos=(996,0,0) rot=(0,0,1;0rad)
  Tip = -> Pocket004
FEATURE [Sketcher::SketchObject] Sketch012
  FullyConstrained = true
  MapMode = 5
  Placement = pos=(0,0,0) rot=(1,0,0;1.5708rad)
  Support = -> [XZ_Plane005]
  sketch-geometry (5):
    g0: LineSegment StartX=-1000 StartY=-50 StartZ=0 EndX=-1000 EndY=50 EndZ=0
    g1: LineSegment StartX=-1000 StartY=50 StartZ=0 EndX=1000 EndY=50 EndZ=0
    g2: LineSegment StartX=1000 StartY=50 StartZ=0 EndX=1000 EndY=-50 EndZ=0
    g3: LineSegment StartX=1000 StartY=-50 StartZ=0 EndX=-1000 EndY=-50 EndZ=0
    g4: GeomPoint X=0 Y=0 Z=0
  constraints (12):
    c: Coincident(g0,g1)
    c: Coincident(g1,g2)
    c: Coincident(g2,g3)
    c: Coincident(g3,g0)
    c: Horizontal(g1)
    c: Horizontal(g3)
    c: Vertical(g0)
    c: Vertical(g2)
    c: Symmetric(g1,g0,g4)
    c: Coincident(g4,g-1)
    c: DistanceY(g2,g1) = 100
    c: DistanceX(g0,g1) = 2000
FEATURE [PartDesign::Pad] Pad005
  Direction = (0,-1,2e-16)
  Length = 4
  Length2 = 10
  Placement = pos=(0,0,0) rot=(1,0,0;1.5708rad)
  Profile = -> Sketch012
  Type = 0
FEATURE [Sketcher::SketchObject] Sketch013
  ExternalGeometry = -> [Pad005]
  FullyConstrained = false
  MapMode = 5
  Placement = pos=(0,-4,1.8e-15) rot=(1,0,0;1.5708rad)
  Support = -> [Pad005]
  sketch-geometry (94):
    g0: GeomPoint X=-666.66 Y=0 Z=0
    g1: GeomPoint X=333.33 Y=0 Z=0
    g2: GeomPoint X=666.66 Y=0 Z=0
    g3: GeomPoint X=-333.33 Y=0 Z=0
    g4: Circle CenterX=-916.63 CenterY=-1.8e-15 CenterZ=0 NormalX=0 NormalY=0 NormalZ=1 AngleXU=0 Radius=25
    g5: Circle CenterX=-833.3 CenterY=-1.8e-15 CenterZ=0 NormalX=0 NormalY=0 NormalZ=1 AngleXU=0 Radius=25
    g6: Circle CenterX=-583.31 CenterY=-1.8e-15 CenterZ=0 NormalX=0 NormalY=0 NormalZ=1 AngleXU=0 Radius=25
    g7: Circle CenterX=-499.98 CenterY=-1.8e-15 CenterZ=0 NormalX=0 NormalY=0 NormalZ=1 AngleXU=0 Radius=25
    g8: Circle CenterX=-249.99 CenterY=-1.8e-15 CenterZ=0 NormalX=0 NormalY=0 NormalZ=1 AngleXU=0 Radius=25
    g9: Circle CenterX=-166.66 CenterY=-1.8e-15 CenterZ=0 NormalX=0 NormalY=0 NormalZ=1 AngleXU=0 Radius=25
    g10: Circle CenterX=83.33 CenterY=-1.8e-15 CenterZ=0 NormalX=0 NormalY=0 NormalZ=1 AngleXU=0 Radius=25
    g11: Circle CenterX=166.66 CenterY=-1.8e-15 CenterZ=0 NormalX=0 NormalY=0 NormalZ=1 AngleXU=0 Radius=25
    g12: Circle CenterX=416.65 CenterY=-1.8e-15 CenterZ=0 NormalX=0 NormalY=0 NormalZ=1 AngleXU=0 Radius=25
    g13: Circle CenterX=499.98 CenterY=-1.8e-15 CenterZ=0 NormalX=0 NormalY=0 NormalZ=1 AngleXU=0 Radius=25
    g14: Circle CenterX=749.97 CenterY=-1.8e-15 CenterZ=0 NormalX=0 NormalY=0 NormalZ=1 AngleXU=0 Radius=25
    g15: Circle CenterX=833.3 CenterY=-1.8e-15 CenterZ=0 NormalX=0 NormalY=0 NormalZ=1 AngleXU=0 Radius=25
    g16: Circle CenterX=-749.97 CenterY=-1.8e-15 CenterZ=0 NormalX=0 NormalY=0 NormalZ=1 AngleXU=0 Radius=25
    g17: Circle CenterX=-416.65 CenterY=-1.8e-15 CenterZ=0 NormalX=0 NormalY=0 NormalZ=1 AngleXU=0 Radius=25
    g18: Circle CenterX=-83.33 CenterY=-1.8e-15 CenterZ=0 NormalX=0 NormalY=0 NormalZ=1 AngleXU=0 Radius=25
    g19: Circle CenterX=249.99 CenterY=-1.8e-15 CenterZ=0 NormalX=0 NormalY=0 NormalZ=1 AngleXU=0 Radius=25
    g20: Circle CenterX=583.31 CenterY=-1.8e-15 CenterZ=0 NormalX=0 NormalY=0 NormalZ=1 AngleXU=0 Radius=25
    g21: Circle CenterX=916.64 CenterY=-1.8e-15 CenterZ=0 NormalX=0 NormalY=0 NormalZ=1 AngleXU=0 Radius=25
    g22: LineSegment StartX=-1000 StartY=50 StartZ=0 EndX=-996 EndY=50 EndZ=0
    g23: LineSegment StartX=-996 StartY=50 StartZ=0 EndX=-996 EndY=30 EndZ=0
    g24: LineSegment StartX=-996 StartY=30 StartZ=0 EndX=-1000 EndY=30 EndZ=0
    g25: LineSegment StartX=-1000 StartY=30 StartZ=0 EndX=-1000 EndY=50 EndZ=0
    g26: LineSegment StartX=-1000 StartY=10 StartZ=0 EndX=-996 EndY=10 EndZ=0
    g27: LineSegment StartX=-996 StartY=10 StartZ=0 EndX=-996 EndY=-10 EndZ=0
    g28: LineSegment StartX=-996 StartY=-10 StartZ=0 EndX=-1000 EndY=-10 EndZ=0
    g29: LineSegment StartX=-1000 StartY=-10 StartZ=0 EndX=-1000 EndY=10 EndZ=0
    g30: LineSegment StartX=1000 StartY=50 StartZ=0 EndX=996 EndY=50 EndZ=0
    g31: LineSegment StartX=996 StartY=50 StartZ=0 EndX=996 EndY=30 EndZ=0
    g32: LineSegment StartX=996 StartY=30 StartZ=0 EndX=1000 EndY=30 EndZ=0
    g33: LineSegment StartX=1000 StartY=30 StartZ=0 EndX=1000 EndY=50 EndZ=0
    g34: LineSegment StartX=1000 StartY=10 StartZ=0 EndX=996 EndY=10 EndZ=0
    g35: LineSegment StartX=996 StartY=10 StartZ=0 EndX=996 EndY=-10 EndZ=0
    g36: LineSegment StartX=996 StartY=-10 StartZ=0 EndX=1000 EndY=-10 EndZ=0
    g37: LineSegment StartX=1000 StartY=-10 StartZ=0 EndX=1000 EndY=10 EndZ=0
    g38: GeomPoint X=-666.64 Y=-51.5587 Z=0
    g39: GeomPoint X=333.32 Y=-51.5587 Z=0
    g40: GeomPoint X=666.64 Y=-51.5587 Z=0
    g41: GeomPoint X=999.97 Y=-51.5587 Z=0
    g42: GeomPoint X=-999.96 Y=-51.5587 Z=0
    g43: LineSegment StartX=-668.66 StartY=50 StartZ=0 EndX=-664.66 EndY=50 EndZ=0
    g44: LineSegment StartX=-664.66 StartY=50 StartZ=0 EndX=-664.66 EndY=30 EndZ=0
    g45: LineSegment StartX=-664.66 StartY=30 StartZ=0 EndX=-668.66 EndY=30 EndZ=0
    g46: LineSegment StartX=-668.66 StartY=30 StartZ=0 EndX=-668.66 EndY=50 EndZ=0
    g47: LineSegment StartX=-668.66 StartY=-50 StartZ=0 EndX=-664.66 EndY=-50 EndZ=0
    g48: LineSegment StartX=-664.66 StartY=-50 StartZ=0 EndX=-664.66 EndY=-30 EndZ=0
    g49: LineSegment StartX=-664.66 StartY=-30 StartZ=0 EndX=-668.66 EndY=-30 EndZ=0
    g50: LineSegment StartX=-668.66 StartY=-30 StartZ=0 EndX=-668.66 EndY=-50 EndZ=0
    g51: LineSegment StartX=-335.33 StartY=50 StartZ=0 EndX=-331.33 EndY=50 EndZ=0
    g52: LineSegment StartX=-331.33 StartY=50 StartZ=0 EndX=-331.33 EndY=30 EndZ=0
    g53: LineSegment StartX=-331.33 StartY=30 StartZ=0 EndX=-335.33 EndY=30 EndZ=0
    g54: LineSegment StartX=-335.33 StartY=30 StartZ=0 EndX=-335.33 EndY=50 EndZ=0
    g55: LineSegment StartX=-335.33 StartY=-50 StartZ=0 EndX=-331.33 EndY=-50 EndZ=0
    g56: LineSegment StartX=-331.33 StartY=-50 StartZ=0 EndX=-331.33 EndY=-30 EndZ=0
    g57: LineSegment StartX=-331.33 StartY=-30 StartZ=0 EndX=-335.33 EndY=-30 EndZ=0
    g58: LineSegment StartX=-335.33 StartY=-30 StartZ=0 EndX=-335.33 EndY=-50 EndZ=0
    g59: GeomPoint X=-333.32 Y=-51.5587 Z=0
    g60: LineSegment StartX=-2 StartY=50 StartZ=0 EndX=2 EndY=50 EndZ=0
    g61: LineSegment StartX=2 StartY=50 StartZ=0 EndX=2 EndY=30 EndZ=0
    g62: LineSegment StartX=2 StartY=30 StartZ=0 EndX=-2 EndY=30 EndZ=0
    g63: LineSegment StartX=-2 StartY=30 StartZ=0 EndX=-2 EndY=50 EndZ=0
    g64: LineSegment StartX=2 StartY=-50 StartZ=0 EndX=-2 EndY=-50 EndZ=0
    g65: LineSegment StartX=-2 StartY=-50 StartZ=0 EndX=-2 EndY=-30 EndZ=0
    g66: LineSegment StartX=-2 StartY=-30 StartZ=0 EndX=2 EndY=-30 EndZ=0
    g67: LineSegment StartX=2 StartY=-30 StartZ=0 EndX=2 EndY=-50 EndZ=0
    g68: LineSegment StartX=331.33 StartY=50 StartZ=0 EndX=335.33 EndY=50 EndZ=0
    g69: LineSegment StartX=335.33 StartY=50 StartZ=0 EndX=335.33 EndY=30 EndZ=0
    g70: LineSegment StartX=335.33 StartY=30 StartZ=0 EndX=331.33 EndY=30 EndZ=0
    g71: LineSegment StartX=331.33 StartY=30 StartZ=0 EndX=331.33 EndY=50 EndZ=0
    g72: LineSegment StartX=331.33 StartY=-30 StartZ=0 EndX=335.33 EndY=-30 EndZ=0
    g73: LineSegment StartX=335.33 StartY=-30 StartZ=0 EndX=335.33 EndY=-50 EndZ=0
    g74: LineSegment StartX=335.33 StartY=-50 StartZ=0 EndX=331.33 EndY=-50 EndZ=0
    g75: LineSegment StartX=331.33 StartY=-50 StartZ=0 EndX=331.33 EndY=-30 EndZ=0
    g76: LineSegment StartX=664.66 StartY=50 StartZ=0 EndX=668.66 EndY=50 EndZ=0
    g77: LineSegment StartX=668.66 StartY=50 StartZ=0 EndX=668.66 EndY=30 EndZ=0
    g78: LineSegment StartX=668.66 StartY=30 StartZ=0 EndX=664.66 EndY=30 EndZ=0
    g79: LineSegment StartX=664.66 StartY=30 StartZ=0 EndX=664.66 EndY=50 EndZ=0
    g80: LineSegment StartX=668.66 StartY=-50 StartZ=0 EndX=664.66 EndY=-50 EndZ=0
    g81: LineSegment StartX=664.66 StartY=-50 StartZ=0 EndX=664.66 EndY=-30 EndZ=0
    g82: LineSegment StartX=664.66 StartY=-30 StartZ=0 EndX=668.66 EndY=-30 EndZ=0
    g83: LineSegment StartX=668.66 StartY=-30 StartZ=0 EndX=668.66 EndY=-50 EndZ=0
    g84: GeomPoint X=-999.99 Y=50.4552 Z=0
    g85: GeomPoint X=999.99 Y=51.0014 Z=0
    g86: LineSegment StartX=-996 StartY=-50 StartZ=0 EndX=-1000 EndY=-50 EndZ=0
    g87: LineSegment StartX=-1000 StartY=-50 StartZ=0 EndX=-1000 EndY=-30 EndZ=0
    g88: LineSegment StartX=-1000 StartY=-30 StartZ=0 EndX=-996 EndY=-30 EndZ=0
    g89: LineSegment StartX=-996 StartY=-30 StartZ=0 EndX=-996 EndY=-50 EndZ=0
    g90: LineSegment StartX=996 StartY=-30 StartZ=0 EndX=1000 EndY=-30 EndZ=0
    g91: LineSegment StartX=1000 StartY=-30 StartZ=0 EndX=1000 EndY=-50 EndZ=0
    g92: LineSegment StartX=1000 StartY=-50 StartZ=0 EndX=996 EndY=-50 EndZ=0
    g93: LineSegment StartX=996 StartY=-50 StartZ=0 EndX=996 EndY=-30 EndZ=0
  constraints (263):
    c: DistanceY(g-4,g4) = 50
    c: Horizontal(g4,g5)
    c: Horizontal(g5,g16)
    c: Horizontal(g16,g6)
    c: Horizontal(g6,g7)
    c: Horizontal(g7,g17)
    c: Horizontal(g17,g8)
    c: Horizontal(g8,g9)
    c: Horizontal(g9,g18)
    c: Horizontal(g18,g10)
    c: Horizontal(g10,g11)
    c: Horizontal(g11,g19)
    c: Horizontal(g19,g12)
    c: Horizontal(g12,g13)
    c: Horizontal(g13,g20)
    c: Horizontal(g20,g14)
    c: Horizontal(g14,g15)
    c: Horizontal(g15,g21)
    c: Coincident(g22,g23)
    c: Coincident(g23,g24)
    c: Coincident(g24,g25)
    c: Coincident(g25,g22)
    c: Horizontal(g22)
    c: Horizontal(g24)
    c: Vertical(g23)
    c: Vertical(g25)
    c: Coincident(g26,g27)
    c: Coincident(g27,g28)
    c: Coincident(g28,g29)
    c: Coincident(g29,g26)
    c: Horizontal(g26)
    c: Horizontal(g28)
    c: Vertical(g27)
    c: Vertical(g29)
    c: Vertical(g-3,g22)
    c: Vertical(g24,g26)
    c: DistanceX(g-3,g22) = 4
    c: Vertical(g23,g26)
    c: DistanceY(g22,g-3) = 0
    c: DistanceY(g24,g22) = 20
    c: DistanceY(g26,g24) = 20
    c: DistanceY(g28,g26) = 20
    c: Coincident(g30,g31)
    c: Coincident(g31,g32)
    c: Coincident(g32,g33)
    c: Coincident(g33,g30)
    c: Horizontal(g30)
    c: Horizontal(g32)
    c: Vertical(g31)
    c: Vertical(g33)
    c: Coincident(g34,g35)
    c: Coincident(g35,g36)
    c: Coincident(g36,g37)
    c: Coincident(g37,g34)
    c: Horizontal(g34)
    c: Horizontal(g36)
    c: Vertical(g35)
    c: Vertical(g37)
    c: Vertical(g-5,g30)
    c: Vertical(g32,g34)
    c: DistanceX(g30,g30) = 4
    c: Vertical(g31,g34)
    c: Horizontal(g22,g30)
    c: Horizontal(g31,g23)
    c: Horizontal(g26,g34)
    c: Horizontal(g35,g27)
    c: Diameter(g4) = 50
    c: DistanceX(g4,g5) = 83.33
    c: Equal(g4,g5)
    c: DistanceX(g5,g16) = 83.33
    c: Equal(g5,g16)
    c: DistanceX(g0,g3) = 333.33
    c: DistanceX(g3,g-1) = 333.33
    c: DistanceX(g6,g7) = 83.33
    c: DistanceX(g7,g17) = 83.33
    c: Equal(g16,g6)
    c: Equal(g6,g7)
    c: Equal(g7,g17)
    c: DistanceX(g16,g38) = 83.33
    c: DistanceX(g38,g6) = 83.33
    c: DistanceX(g8,g9) = 83.33
    c: DistanceX(g9,g18) = 83.33
    c: DistanceX(g18,g-1) = 83.33
    c: Equal(g17,g8)
    c: Equal(g8,g9)
    c: Equal(g9,g18)
    c: DistanceX(g-1,g10) = 83.33
    c: DistanceX(g10,g11) = 83.33
    c: DistanceX(g11,g19) = 83.33
    c: Equal(g18,g10)
    c: Equal(g10,g11)
    c: Equal(g11,g19)
    c: DistanceX(g19,g39) = 83.33
    c: DistanceX(g39,g12) = 83.33
    c: DistanceX(g12,g13) = 83.33
    c: DistanceX(g13,g20) = 83.33
    c: Equal(g19,g12)
    c: Equal(g12,g13)
    c: Equal(g13,g20)
    c: DistanceX(g20,g40) = 83.33
    c: DistanceX(g40,g14) = 83.33
    c: DistanceX(g14,g15) = 83.33
    c: DistanceX(g15,g21) = 83.34
    c: DistanceX(g21,g41) = 83.33
    c: Equal(g20,g14)
    c: Equal(g14,g15)
    c: Equal(g15,g21)
    c: DistanceX(g42,g4) = 83.33
    c: Coincident(g43,g44)
    c: Coincident(g44,g45)
    c: Coincident(g45,g46)
    c: Coincident(g46,g43)
    c: Horizontal(g43)
    c: Horizontal(g45)
    c: Vertical(g44)
    c: Vertical(g46)
    c: Horizontal(g-3,g43)
    c: DistanceX(g43,g0) = 2
    c: DistanceX(g43,g43) = 4
    c: DistanceY(g45,g43) = 20
    c: Coincident(g47,g48)
    c: Coincident(g48,g49)
    c: Coincident(g49,g50)
    c: Coincident(g50,g47)
    c: Horizontal(g47)
    c: Horizontal(g49)
    c: Vertical(g48)
    c: Vertical(g50)
    c: Vertical(g45,g49)
    c: Vertical(g48,g44)
    c: Horizontal(g-4,g47)
    c: DistanceY(g47,g49) = 20
    c: Coincident(g51,g52)
    c: Coincident(g52,g53)
    c: Coincident(g53,g54)
    c: Coincident(g54,g51)
    c: Horizontal(g51)
    c: Horizontal(g53)
    c: Vertical(g52)
    c: Vertical(g54)
    c: Horizontal(g43,g51)
    c: DistanceX(g51,g3) = 2
    c: DistanceX(g51,g51) = 4
    c: Horizontal(g44,g53)
    c: Coincident(g55,g56)
    c: Coincident(g56,g57)
    c: Coincident(g57,g58)
    c: Coincident(g58,g55)
    c: Horizontal(g55)
    c: Horizontal(g57)
    c: Vertical(g56)
    c: Vertical(g58)
    c: Horizontal(g47,g55)
    c: Horizontal(g57,g48)
    c: Vertical(g53,g57)
    c: Vertical(g56,g52)
    c: DistanceX(g17,g59) = 83.33
    c: DistanceX(g59,g8) = 83.33
    c: Coincident(g60,g61)
    c: Coincident(g61,g62)
    c: Coincident(g62,g63)
    c: Coincident(g63,g60)
    c: Horizontal(g60)
    c: Horizontal(g62)
    c: Vertical(g61)
    c: Vertical(g63)
    c: Coincident(g64,g65)
    c: Coincident(g65,g66)
    c: Coincident(g66,g67)
    c: Coincident(g67,g64)
    c: Horizontal(g64)
    c: Horizontal(g66)
    c: Vertical(g65)
    c: Vertical(g67)
    c: Horizontal(g55,g64)
    c: Horizontal(g65,g56)
    c: Horizontal(g52,g62)
    c: Horizontal(g60,g51)
    c: DistanceX(g60,g-1) = 2
    c: DistanceX(g60,g60) = 4
    c: Vertical(g61,g66)
    c: Vertical(g62,g65)
    c: Coincident(g68,g69)
    c: Coincident(g69,g70)
    c: Coincident(g70,g71)
    c: Coincident(g71,g68)
    c: Horizontal(g68)
    c: Horizontal(g70)
    c: Vertical(g69)
    c: Vertical(g71)
    c: Coincident(g72,g73)
    c: Coincident(g73,g74)
    c: Coincident(g74,g75)
    c: Coincident(g75,g72)
    c: Horizontal(g72)
    c: Horizontal(g74)
    c: Vertical(g73)
    c: Vertical(g75)
    c: Horizontal(g64,g74)
    c: Horizontal(g66,g72)
    c: Horizontal(g68,g60)
    c: Horizontal(g70,g61)
    c: DistanceX(g-1,g1) = 333.33
    c: DistanceX(g68,g1) = 2
    c: DistanceX(g68,g68) = 4
    c: Vertical(g70,g72)
    c: Vertical(g69,g72)
    c: DistanceX(g1,g2) = 333.33
    c: Coincident(g76,g77)
    c: Coincident(g77,g78)
    c: Coincident(g78,g79)
    c: Coincident(g79,g76)
    c: Horizontal(g76)
    c: Horizontal(g78)
    c: Vertical(g77)
    c: Vertical(g79)
    c: Coincident(g80,g81)
    c: Coincident(g81,g82)
    c: Coincident(g82,g83)
    c: Coincident(g83,g80)
    c: Horizontal(g80)
    c: Horizontal(g82)
    c: Vertical(g81)
    c: Vertical(g83)
    c: Horizontal(g73,g80)
    c: Horizontal(g81,g72)
    c: Horizontal(g69,g78)
    c: Horizontal(g76,g68)
    c: DistanceX(g76,g2) = 2
    c: DistanceX(g76,g76) = 4
    c: Vertical(g78,g81)
    c: Vertical(g82,g77)
    c: Horizontal(g42,g38)
    c: Horizontal(g38,g59)
    c: Horizontal(g59,g39)
    c: Horizontal(g39,g40)
    c: Horizontal(g40,g41)
    c: DistanceX(g84,g0) = 333.33
    c: DistanceX(g2,g85) = 333.33
    c: Coincident(g86,g87)
    c: Coincident(g87,g88)
    c: Coincident(g88,g89)
    c: Coincident(g89,g86)
    c: Horizontal(g86)
    c: Horizontal(g88)
    c: Vertical(g87)
    c: Vertical(g89)
    c: Vertical(g88,g27)
    c: Vertical(g28,g87)
    c: DistanceY(g87,g28) = 20
    c: DistanceY(g86,g87) = 20
    c: Coincident(g90,g91)
    c: Coincident(g91,g92)
    c: Coincident(g92,g93)
    c: Coincident(g93,g90)
    c: Horizontal(g90)
    c: Horizontal(g92)
    c: Vertical(g91)
    c: Vertical(g93)
    c: Vertical(g36,g90)
    c: Vertical(g35,g90)
    c: Horizontal(g90,g88)
    c: Horizontal(g86,g92)
FEATURE [PartDesign::Pocket] Pocket005
  BaseFeature = -> Pad005
  Length = 4
  Length2 = 5
  Placement = pos=(0,0,0) rot=(1,0,0;1.5708rad)
  Profile = -> Sketch013
  Type = 0
FEATURE [PartDesign::Body] Body005  label="LangSprygel-2"
  Group = -> [Sketch012,Pad005,Sketch013,Pocket005]
  Origin = -> Origin005
  Placement = pos=(0,2,0) rot=(0,0,1;0rad)
  Tip = -> Pocket005
FEATURE [Sketcher::SketchObject] Sketch014
  FullyConstrained = true
  MapMode = 5
  Placement = pos=(0,0,0) rot=(1,0,0;1.5708rad)
  Support = -> [XZ_Plane006]
  sketch-geometry (5):
    g0: LineSegment StartX=-1000 StartY=-50 StartZ=0 EndX=-1000 EndY=50 EndZ=0
    g1: LineSegment StartX=-1000 StartY=50 StartZ=0 EndX=1000 EndY=50 EndZ=0
    g2: LineSegment StartX=1000 StartY=50 StartZ=0 EndX=1000 EndY=-50 EndZ=0
    g3: LineSegment StartX=1000 StartY=-50 StartZ=0 EndX=-1000 EndY=-50 EndZ=0
    g4: GeomPoint X=0 Y=0 Z=0
  constraints (12):
    c: Coincident(g0,g1)
    c: Coincident(g1,g2)
    c: Coincident(g2,g3)
    c: Coincident(g3,g0)
    c: Horizontal(g1)
    c: Horizontal(g3)
    c: Vertical(g0)
    c: Vertical(g2)
    c: Symmetric(g1,g0,g4)
    c: Coincident(g4,g-1)
    c: DistanceY(g2,g1) = 100
    c: DistanceX(g0,g1) = 2000
FEATURE [PartDesign::Pad] Pad006
  Direction = (0,-1,2e-16)
  Length = 4
  Length2 = 10
  Placement = pos=(0,0,0) rot=(1,0,0;1.5708rad)
  Profile = -> Sketch014
  Type = 0
FEATURE [Sketcher::SketchObject] Sketch015
  ExternalGeometry = -> [Pad006]
  FullyConstrained = false
  MapMode = 5
  Placement = pos=(0,-4,1.8e-15) rot=(1,0,0;1.5708rad)
  Support = -> [Pad006]
  sketch-geometry (94):
    g0: GeomPoint X=-666.66 Y=0 Z=0
    g1: GeomPoint X=333.33 Y=0 Z=0
    g2: GeomPoint X=666.66 Y=0 Z=0
    g3: GeomPoint X=-333.33 Y=0 Z=0
    g4: Circle CenterX=-916.63 CenterY=-1.8e-15 CenterZ=0 NormalX=0 NormalY=0 NormalZ=1 AngleXU=0 Radius=25
    g5: Circle CenterX=-833.3 CenterY=-1.8e-15 CenterZ=0 NormalX=0 NormalY=0 NormalZ=1 AngleXU=0 Radius=25
    g6: Circle CenterX=-583.31 CenterY=-1.8e-15 CenterZ=0 NormalX=0 NormalY=0 NormalZ=1 AngleXU=0 Radius=25
    g7: Circle CenterX=-499.98 CenterY=-1.8e-15 CenterZ=0 NormalX=0 NormalY=0 NormalZ=1 AngleXU=0 Radius=25
    g8: Circle CenterX=-249.99 CenterY=-1.8e-15 CenterZ=0 NormalX=0 NormalY=0 NormalZ=1 AngleXU=0 Radius=25
    g9: Circle CenterX=-166.66 CenterY=-1.8e-15 CenterZ=0 NormalX=0 NormalY=0 NormalZ=1 AngleXU=0 Radius=25
    g10: Circle CenterX=83.33 CenterY=-1.8e-15 CenterZ=0 NormalX=0 NormalY=0 NormalZ=1 AngleXU=0 Radius=25
    g11: Circle CenterX=166.66 CenterY=-1.8e-15 CenterZ=0 NormalX=0 NormalY=0 NormalZ=1 AngleXU=0 Radius=25
    g12: Circle CenterX=416.65 CenterY=-1.8e-15 CenterZ=0 NormalX=0 NormalY=0 NormalZ=1 AngleXU=0 Radius=25
    g13: Circle CenterX=499.98 CenterY=-1.8e-15 CenterZ=0 NormalX=0 NormalY=0 NormalZ=1 AngleXU=0 Radius=25
    g14: Circle CenterX=749.97 CenterY=-1.8e-15 CenterZ=0 NormalX=0 NormalY=0 NormalZ=1 AngleXU=0 Radius=25
    g15: Circle CenterX=833.3 CenterY=-1.8e-15 CenterZ=0 NormalX=0 NormalY=0 NormalZ=1 AngleXU=0 Radius=25
    g16: Circle CenterX=-749.97 CenterY=-1.8e-15 CenterZ=0 NormalX=0 NormalY=0 NormalZ=1 AngleXU=0 Radius=25
    g17: Circle CenterX=-416.65 CenterY=-1.8e-15 CenterZ=0 NormalX=0 NormalY=0 NormalZ=1 AngleXU=0 Radius=25
    g18: Circle CenterX=-83.33 CenterY=-1.8e-15 CenterZ=0 NormalX=0 NormalY=0 NormalZ=1 AngleXU=0 Radius=25
    g19: Circle CenterX=249.99 CenterY=-1.8e-15 CenterZ=0 NormalX=0 NormalY=0 NormalZ=1 AngleXU=0 Radius=25
    g20: Circle CenterX=583.31 CenterY=-1.8e-15 CenterZ=0 NormalX=0 NormalY=0 NormalZ=1 AngleXU=0 Radius=25
    g21: Circle CenterX=916.64 CenterY=-1.8e-15 CenterZ=0 NormalX=0 NormalY=0 NormalZ=1 AngleXU=0 Radius=25
    g22: LineSegment StartX=-1000 StartY=50 StartZ=0 EndX=-996 EndY=50 EndZ=0
    g23: LineSegment StartX=-996 StartY=50 StartZ=0 EndX=-996 EndY=30 EndZ=0
    g24: LineSegment StartX=-996 StartY=30 StartZ=0 EndX=-1000 EndY=30 EndZ=0
    g25: LineSegment StartX=-1000 StartY=30 StartZ=0 EndX=-1000 EndY=50 EndZ=0
    g26: LineSegment StartX=-1000 StartY=10 StartZ=0 EndX=-996 EndY=10 EndZ=0
    g27: LineSegment StartX=-996 StartY=10 StartZ=0 EndX=-996 EndY=-10 EndZ=0
    g28: LineSegment StartX=-996 StartY=-10 StartZ=0 EndX=-1000 EndY=-10 EndZ=0
    g29: LineSegment StartX=-1000 StartY=-10 StartZ=0 EndX=-1000 EndY=10 EndZ=0
    g30: LineSegment StartX=1000 StartY=50 StartZ=0 EndX=996 EndY=50 EndZ=0
    g31: LineSegment StartX=996 StartY=50 StartZ=0 EndX=996 EndY=30 EndZ=0
    g32: LineSegment StartX=996 StartY=30 StartZ=0 EndX=1000 EndY=30 EndZ=0
    g33: LineSegment StartX=1000 StartY=30 StartZ=0 EndX=1000 EndY=50 EndZ=0
    g34: LineSegment StartX=1000 StartY=10 StartZ=0 EndX=996 EndY=10 EndZ=0
    g35: LineSegment StartX=996 StartY=10 StartZ=0 EndX=996 EndY=-10 EndZ=0
    g36: LineSegment StartX=996 StartY=-10 StartZ=0 EndX=1000 EndY=-10 EndZ=0
    g37: LineSegment StartX=1000 StartY=-10 StartZ=0 EndX=1000 EndY=10 EndZ=0
    g38: GeomPoint X=-666.64 Y=-51.5587 Z=0
    g39: GeomPoint X=333.32 Y=-51.5587 Z=0
    g40: GeomPoint X=666.64 Y=-51.5587 Z=0
    g41: GeomPoint X=999.97 Y=-51.5587 Z=0
    g42: GeomPoint X=-999.96 Y=-51.5587 Z=0
    g43: LineSegment StartX=-668.66 StartY=50 StartZ=0 EndX=-664.66 EndY=50 EndZ=0
    g44: LineSegment StartX=-664.66 StartY=50 StartZ=0 EndX=-664.66 EndY=30 EndZ=0
    g45: LineSegment StartX=-664.66 StartY=30 StartZ=0 EndX=-668.66 EndY=30 EndZ=0
    g46: LineSegment StartX=-668.66 StartY=30 StartZ=0 EndX=-668.66 EndY=50 EndZ=0
    g47: LineSegment StartX=-668.66 StartY=-50 StartZ=0 EndX=-664.66 EndY=-50 EndZ=0
    g48: LineSegment StartX=-664.66 StartY=-50 StartZ=0 EndX=-664.66 EndY=-30 EndZ=0
    g49: LineSegment StartX=-664.66 StartY=-30 StartZ=0 EndX=-668.66 EndY=-30 EndZ=0
    g50: LineSegment StartX=-668.66 StartY=-30 StartZ=0 EndX=-668.66 EndY=-50 EndZ=0
    g51: LineSegment StartX=-335.33 StartY=50 StartZ=0 EndX=-331.33 EndY=50 EndZ=0
    g52: LineSegment StartX=-331.33 StartY=50 StartZ=0 EndX=-331.33 EndY=30 EndZ=0
    g53: LineSegment StartX=-331.33 StartY=30 StartZ=0 EndX=-335.33 EndY=30 EndZ=0
    g54: LineSegment StartX=-335.33 StartY=30 StartZ=0 EndX=-335.33 EndY=50 EndZ=0
    g55: LineSegment StartX=-335.33 StartY=-50 StartZ=0 EndX=-331.33 EndY=-50 EndZ=0
    g56: LineSegment StartX=-331.33 StartY=-50 StartZ=0 EndX=-331.33 EndY=-30 EndZ=0
    g57: LineSegment StartX=-331.33 StartY=-30 StartZ=0 EndX=-335.33 EndY=-30 EndZ=0
    g58: LineSegment StartX=-335.33 StartY=-30 StartZ=0 EndX=-335.33 EndY=-50 EndZ=0
    g59: GeomPoint X=-333.32 Y=-51.5587 Z=0
    g60: LineSegment StartX=-2 StartY=50 StartZ=0 EndX=2 EndY=50 EndZ=0
    g61: LineSegment StartX=2 StartY=50 StartZ=0 EndX=2 EndY=30 EndZ=0
    g62: LineSegment StartX=2 StartY=30 StartZ=0 EndX=-2 EndY=30 EndZ=0
    g63: LineSegment StartX=-2 StartY=30 StartZ=0 EndX=-2 EndY=50 EndZ=0
    g64: LineSegment StartX=2 StartY=-50 StartZ=0 EndX=-2 EndY=-50 EndZ=0
    g65: LineSegment StartX=-2 StartY=-50 StartZ=0 EndX=-2 EndY=-30 EndZ=0
    g66: LineSegment StartX=-2 StartY=-30 StartZ=0 EndX=2 EndY=-30 EndZ=0
    g67: LineSegment StartX=2 StartY=-30 StartZ=0 EndX=2 EndY=-50 EndZ=0
    g68: LineSegment StartX=331.33 StartY=50 StartZ=0 EndX=335.33 EndY=50 EndZ=0
    g69: LineSegment StartX=335.33 StartY=50 StartZ=0 EndX=335.33 EndY=30 EndZ=0
    g70: LineSegment StartX=335.33 StartY=30 StartZ=0 EndX=331.33 EndY=30 EndZ=0
    g71: LineSegment StartX=331.33 StartY=30 StartZ=0 EndX=331.33 EndY=50 EndZ=0
    g72: LineSegment StartX=331.33 StartY=-30 StartZ=0 EndX=335.33 EndY=-30 EndZ=0
    g73: LineSegment StartX=335.33 StartY=-30 StartZ=0 EndX=335.33 EndY=-50 EndZ=0
    g74: LineSegment StartX=335.33 StartY=-50 StartZ=0 EndX=331.33 EndY=-50 EndZ=0
    g75: LineSegment StartX=331.33 StartY=-50 StartZ=0 EndX=331.33 EndY=-30 EndZ=0
    g76: LineSegment StartX=664.66 StartY=50 StartZ=0 EndX=668.66 EndY=50 EndZ=0
    g77: LineSegment StartX=668.66 StartY=50 StartZ=0 EndX=668.66 EndY=30 EndZ=0
    g78: LineSegment StartX=668.66 StartY=30 StartZ=0 EndX=664.66 EndY=30 EndZ=0
    g79: LineSegment StartX=664.66 StartY=30 StartZ=0 EndX=664.66 EndY=50 EndZ=0
    g80: LineSegment StartX=668.66 StartY=-50 StartZ=0 EndX=664.66 EndY=-50 EndZ=0
    g81: LineSegment StartX=664.66 StartY=-50 StartZ=0 EndX=664.66 EndY=-30 EndZ=0
    g82: LineSegment StartX=664.66 StartY=-30 StartZ=0 EndX=668.66 EndY=-30 EndZ=0
    g83: LineSegment StartX=668.66 StartY=-30 StartZ=0 EndX=668.66 EndY=-50 EndZ=0
    g84: GeomPoint X=-999.99 Y=50.4552 Z=0
    g85: GeomPoint X=999.99 Y=51.0014 Z=0
    g86: LineSegment StartX=-996 StartY=-50 StartZ=0 EndX=-1000 EndY=-50 EndZ=0
    g87: LineSegment StartX=-1000 StartY=-50 StartZ=0 EndX=-1000 EndY=-30 EndZ=0
    g88: LineSegment StartX=-1000 StartY=-30 StartZ=0 EndX=-996 EndY=-30 EndZ=0
    g89: LineSegment StartX=-996 StartY=-30 StartZ=0 EndX=-996 EndY=-50 EndZ=0
    g90: LineSegment StartX=996 StartY=-30 StartZ=0 EndX=1000 EndY=-30 EndZ=0
    g91: LineSegment StartX=1000 StartY=-30 StartZ=0 EndX=1000 EndY=-50 EndZ=0
    g92: LineSegment StartX=1000 StartY=-50 StartZ=0 EndX=996 EndY=-50 EndZ=0
    g93: LineSegment StartX=996 StartY=-50 StartZ=0 EndX=996 EndY=-30 EndZ=0
  constraints (263):
    c: DistanceY(g-4,g4) = 50
    c: Horizontal(g4,g5)
    c: Horizontal(g5,g16)
    c: Horizontal(g16,g6)
    c: Horizontal(g6,g7)
    c: Horizontal(g7,g17)
    c: Horizontal(g17,g8)
    c: Horizontal(g8,g9)
    c: Horizontal(g9,g18)
    c: Horizontal(g18,g10)
    c: Horizontal(g10,g11)
    c: Horizontal(g11,g19)
    c: Horizontal(g19,g12)
    c: Horizontal(g12,g13)
    c: Horizontal(g13,g20)
    c: Horizontal(g20,g14)
    c: Horizontal(g14,g15)
    c: Horizontal(g15,g21)
    c: Coincident(g22,g23)
    c: Coincident(g23,g24)
    c: Coincident(g24,g25)
    c: Coincident(g25,g22)
    c: Horizontal(g22)
    c: Horizontal(g24)
    c: Vertical(g23)
    c: Vertical(g25)
    c: Coincident(g26,g27)
    c: Coincident(g27,g28)
    c: Coincident(g28,g29)
    c: Coincident(g29,g26)
    c: Horizontal(g26)
    c: Horizontal(g28)
    c: Vertical(g27)
    c: Vertical(g29)
    c: Vertical(g-3,g22)
    c: Vertical(g24,g26)
    c: DistanceX(g-3,g22) = 4
    c: Vertical(g23,g26)
    c: DistanceY(g22,g-3) = 0
    c: DistanceY(g24,g22) = 20
    c: DistanceY(g26,g24) = 20
    c: DistanceY(g28,g26) = 20
    c: Coincident(g30,g31)
    c: Coincident(g31,g32)
    c: Coincident(g32,g33)
    c: Coincident(g33,g30)
    c: Horizontal(g30)
    c: Horizontal(g32)
    c: Vertical(g31)
    c: Vertical(g33)
    c: Coincident(g34,g35)
    c: Coincident(g35,g36)
    c: Coincident(g36,g37)
    c: Coincident(g37,g34)
    c: Horizontal(g34)
    c: Horizontal(g36)
    c: Vertical(g35)
    c: Vertical(g37)
    c: Vertical(g-5,g30)
    c: Vertical(g32,g34)
    c: DistanceX(g30,g30) = 4
    c: Vertical(g31,g34)
    c: Horizontal(g22,g30)
    c: Horizontal(g31,g23)
    c: Horizontal(g26,g34)
    c: Horizontal(g35,g27)
    c: Diameter(g4) = 50
    c: DistanceX(g4,g5) = 83.33
    c: Equal(g4,g5)
    c: DistanceX(g5,g16) = 83.33
    c: Equal(g5,g16)
    c: DistanceX(g0,g3) = 333.33
    c: DistanceX(g3,g-1) = 333.33
    c: DistanceX(g6,g7) = 83.33
    c: DistanceX(g7,g17) = 83.33
    c: Equal(g16,g6)
    c: Equal(g6,g7)
    c: Equal(g7,g17)
    c: DistanceX(g16,g38) = 83.33
    c: DistanceX(g38,g6) = 83.33
    c: DistanceX(g8,g9) = 83.33
    c: DistanceX(g9,g18) = 83.33
    c: DistanceX(g18,g-1) = 83.33
    c: Equal(g17,g8)
    c: Equal(g8,g9)
    c: Equal(g9,g18)
    c: DistanceX(g-1,g10) = 83.33
    c: DistanceX(g10,g11) = 83.33
    c: DistanceX(g11,g19) = 83.33
    c: Equal(g18,g10)
    c: Equal(g10,g11)
    c: Equal(g11,g19)
    c: DistanceX(g19,g39) = 83.33
    c: DistanceX(g39,g12) = 83.33
    c: DistanceX(g12,g13) = 83.33
    c: DistanceX(g13,g20) = 83.33
    c: Equal(g19,g12)
    c: Equal(g12,g13)
    c: Equal(g13,g20)
    c: DistanceX(g20,g40) = 83.33
    c: DistanceX(g40,g14) = 83.33
    c: DistanceX(g14,g15) = 83.33
    c: DistanceX(g15,g21) = 83.34
    c: DistanceX(g21,g41) = 83.33
    c: Equal(g20,g14)
    c: Equal(g14,g15)
    c: Equal(g15,g21)
    c: DistanceX(g42,g4) = 83.33
    c: Coincident(g43,g44)
    c: Coincident(g44,g45)
    c: Coincident(g45,g46)
    c: Coincident(g46,g43)
    c: Horizontal(g43)
    c: Horizontal(g45)
    c: Vertical(g44)
    c: Vertical(g46)
    c: Horizontal(g-3,g43)
    c: DistanceX(g43,g0) = 2
    c: DistanceX(g43,g43) = 4
    c: DistanceY(g45,g43) = 20
    c: Coincident(g47,g48)
    c: Coincident(g48,g49)
    c: Coincident(g49,g50)
    c: Coincident(g50,g47)
    c: Horizontal(g47)
    c: Horizontal(g49)
    c: Vertical(g48)
    c: Vertical(g50)
    c: Vertical(g45,g49)
    c: Vertical(g48,g44)
    c: Horizontal(g-4,g47)
    c: DistanceY(g47,g49) = 20
    c: Coincident(g51,g52)
    c: Coincident(g52,g53)
    c: Coincident(g53,g54)
    c: Coincident(g54,g51)
    c: Horizontal(g51)
    c: Horizontal(g53)
    c: Vertical(g52)
    c: Vertical(g54)
    c: Horizontal(g43,g51)
    c: DistanceX(g51,g3) = 2
    c: DistanceX(g51,g51) = 4
    c: Horizontal(g44,g53)
    c: Coincident(g55,g56)
    c: Coincident(g56,g57)
    c: Coincident(g57,g58)
    c: Coincident(g58,g55)
    c: Horizontal(g55)
    c: Horizontal(g57)
    c: Vertical(g56)
    c: Vertical(g58)
    c: Horizontal(g47,g55)
    c: Horizontal(g57,g48)
    c: Vertical(g53,g57)
    c: Vertical(g56,g52)
    c: DistanceX(g17,g59) = 83.33
    c: DistanceX(g59,g8) = 83.33
    c: Coincident(g60,g61)
    c: Coincident(g61,g62)
    c: Coincident(g62,g63)
    c: Coincident(g63,g60)
    c: Horizontal(g60)
    c: Horizontal(g62)
    c: Vertical(g61)
    c: Vertical(g63)
    c: Coincident(g64,g65)
    c: Coincident(g65,g66)
    c: Coincident(g66,g67)
    c: Coincident(g67,g64)
    c: Horizontal(g64)
    c: Horizontal(g66)
    c: Vertical(g65)
    c: Vertical(g67)
    c: Horizontal(g55,g64)
    c: Horizontal(g65,g56)
    c: Horizontal(g52,g62)
    c: Horizontal(g60,g51)
    c: DistanceX(g60,g-1) = 2
    c: DistanceX(g60,g60) = 4
    c: Vertical(g61,g66)
    c: Vertical(g62,g65)
    c: Coincident(g68,g69)
    c: Coincident(g69,g70)
    c: Coincident(g70,g71)
    c: Coincident(g71,g68)
    c: Horizontal(g68)
    c: Horizontal(g70)
    c: Vertical(g69)
    c: Vertical(g71)
    c: Coincident(g72,g73)
    c: Coincident(g73,g74)
    c: Coincident(g74,g75)
    c: Coincident(g75,g72)
    c: Horizontal(g72)
    c: Horizontal(g74)
    c: Vertical(g73)
    c: Vertical(g75)
    c: Horizontal(g64,g74)
    c: Horizontal(g66,g72)
    c: Horizontal(g68,g60)
    c: Horizontal(g70,g61)
    c: DistanceX(g-1,g1) = 333.33
    c: DistanceX(g68,g1) = 2
    c: DistanceX(g68,g68) = 4
    c: Vertical(g70,g72)
    c: Vertical(g69,g72)
    c: DistanceX(g1,g2) = 333.33
    c: Coincident(g76,g77)
    c: Coincident(g77,g78)
    c: Coincident(g78,g79)
    c: Coincident(g79,g76)
    c: Horizontal(g76)
    c: Horizontal(g78)
    c: Vertical(g77)
    c: Vertical(g79)
    c: Coincident(g80,g81)
    c: Coincident(g81,g82)
    c: Coincident(g82,g83)
    c: Coincident(g83,g80)
    c: Horizontal(g80)
    c: Horizontal(g82)
    c: Vertical(g81)
    c: Vertical(g83)
    c: Horizontal(g73,g80)
    c: Horizontal(g81,g72)
    c: Horizontal(g69,g78)
    c: Horizontal(g76,g68)
    c: DistanceX(g76,g2) = 2
    c: DistanceX(g76,g76) = 4
    c: Vertical(g78,g81)
    c: Vertical(g82,g77)
    c: Horizontal(g42,g38)
    c: Horizontal(g38,g59)
    c: Horizontal(g59,g39)
    c: Horizontal(g39,g40)
    c: Horizontal(g40,g41)
    c: DistanceX(g84,g0) = 333.33
    c: DistanceX(g2,g85) = 333.33
    c: Coincident(g86,g87)
    c: Coincident(g87,g88)
    c: Coincident(g88,g89)
    c: Coincident(g89,g86)
    c: Horizontal(g86)
    c: Horizontal(g88)
    c: Vertical(g87)
    c: Vertical(g89)
    c: Vertical(g88,g27)
    c: Vertical(g28,g87)
    c: DistanceY(g87,g28) = 20
    c: DistanceY(g86,g87) = 20
    c: Coincident(g90,g91)
    c: Coincident(g91,g92)
    c: Coincident(g92,g93)
    c: Coincident(g93,g90)
    c: Horizontal(g90)
    c: Horizontal(g92)
    c: Vertical(g91)
    c: Vertical(g93)
    c: Vertical(g36,g90)
    c: Vertical(g35,g90)
    c: Horizontal(g90,g88)
    c: Horizontal(g86,g92)
FEATURE [PartDesign::Pocket] Pocket006
  BaseFeature = -> Pad006
  Length = 4
  Length2 = 5
  Placement = pos=(0,0,0) rot=(1,0,0;1.5708rad)
  Profile = -> Sketch015
  Type = 0
FEATURE [PartDesign::Body] Body006  label="LangSprygel-3"
  Group = -> [Sketch014,Pad006,Sketch015,Pocket006]
  Origin = -> Origin006
  Placement = pos=(0,-298,0) rot=(0,0,1;0rad)
  Tip = -> Pocket006
FEATURE [Sketcher::SketchObject] Sketch016
  FullyConstrained = true
  MapMode = 5
  Support = -> [XY_Plane007]
  sketch-geometry (5):
    g0: LineSegment StartX=1000 StartY=600 StartZ=0 EndX=1000 EndY=-600 EndZ=0
    g1: LineSegment StartX=1000 StartY=-600 StartZ=0 EndX=-1000 EndY=-600 EndZ=0
    g2: LineSegment StartX=-1000 StartY=-600 StartZ=0 EndX=-1000 EndY=600 EndZ=0
    g3: LineSegment StartX=-1000 StartY=600 StartZ=0 EndX=1000 EndY=600 EndZ=0
    g4: GeomPoint X=0 Y=0 Z=0
  constraints (12):
    c: Coincident(g0,g1)
    c: Coincident(g1,g2)
    c: Coincident(g2,g3)
    c: Coincident(g3,g0)
    c: Horizontal(g1)
    c: Horizontal(g3)
    c: Vertical(g0)
    c: Vertical(g2)
    c: Symmetric(g1,g0,g4)
    c: Coincident(g4,g-1)
    c: DistanceX(g2,g0) = 2000
    c: DistanceY(g0,g0) = 1200
FEATURE [PartDesign::Pad] Pad007
  Direction = (0,0,1)
  Length = 4
  Length2 = 10
  Profile = -> Sketch016
  Type = 0
FEATURE [PartDesign::Body] Body007  label="Bordskiva"
  Group = -> [Sketch016,Pad007]
  Origin = -> Origin007
  Placement = pos=(0,0,50) rot=(0,0,1;0rad)
  Tip = -> Pad007
FEATURE [Sketcher::SketchObject] Sketch017
  FullyConstrained = true
  MapMode = 5
  Placement = pos=(0,0,0) rot=(0.57735,0.57735,0.57735;2.0944rad)
  Support = -> [YZ_Plane008]
  sketch-geometry (10):
    g0: LineSegment StartX=604 StartY=-52 StartZ=0 EndX=-604 EndY=-52 EndZ=0
    g1: LineSegment StartX=-604 StartY=-52 StartZ=0 EndX=-604 EndY=75 EndZ=0
    g2: LineSegment StartX=604 StartY=75 StartZ=0 EndX=604 EndY=-52 EndZ=0
    g3: LineSegment StartX=604 StartY=75 StartZ=0 EndX=604 EndY=575 EndZ=0
    g4: LineSegment StartX=-604 StartY=75 StartZ=0 EndX=0 EndY=575 EndZ=0
    g5: Circle CenterX=0 CenterY=575 CenterZ=0 NormalX=0 NormalY=0 NormalZ=1 AngleXU=0 Radius=1
    g6: Circle CenterX=604 CenterY=575 CenterZ=0 NormalX=0 NormalY=0 NormalZ=1 AngleXU=0 Radius=1
    g7: BSplineCurve PolesCount=2 KnotsCount=2 Degree=1 IsPeriodic=0
    g8: GeomPoint X=0 Y=575 Z=0
    g9: GeomPoint X=604 Y=575 Z=0
  constraints (24):
    c: Coincident(g0,g1)
    c: Coincident(g2,g0)
    c: Horizontal(g0)
    c: Vertical(g1)
    c: Vertical(g2)
    c: DistanceX(g0,g-1) = 604
    c: DistanceX(g0,g0) = 1208
    c: DistanceY(g0,g-1) = 52
    c: DistanceY(g-1,g1) = 75
    c: Coincident(g3,g2)
    c: Vertical(g3)
    c: Horizontal(g1,g2)
    c: DistanceY(g2,g3) = 500
    c: Coincident(g4,g1)
    c: PointOnObject(g4,g-2)
    c: Horizontal(g4,g3)
    c: Weight(g5) = 1
    c: Coincident(g7,g4)
    c: Equal(g5,g6)
    c: Coincident(g7,g3)
    c: InternalAlignment(g5,g7)
    c: InternalAlignment(g6,g7)
    c: InternalAlignment(g8,g7)
    c: InternalAlignment(g9,g7)
FEATURE [PartDesign::Pad] Pad008
  Direction = (1,-2e-16,3e-16)
  Length = 4
  Length2 = 10
  Placement = pos=(0,0,0) rot=(0.57735,0.57735,0.57735;2.0944rad)
  Profile = -> Sketch017
  Type = 0
FEATURE [Sketcher::SketchObject] Sketch018
  ExternalGeometry = -> [Pad008]
  FullyConstrained = true
  MapMode = 5
  Placement = pos=(4,-9e-16,9e-16) rot=(0.57735,0.57735,0.57735;2.0944rad)
  Support = -> [Pad008]
  sketch-geometry (80):
    g0: LineSegment StartX=-604 StartY=-52 StartZ=0 EndX=-600 EndY=-52 EndZ=0
    g1: LineSegment StartX=-600 StartY=-52 StartZ=0 EndX=-600 EndY=-32 EndZ=0
    g2: LineSegment StartX=-600 StartY=-32 StartZ=0 EndX=-604 EndY=-32 EndZ=0
    g3: LineSegment StartX=-604 StartY=-32 StartZ=0 EndX=-604 EndY=-52 EndZ=0
    g4: LineSegment StartX=-604 StartY=48 StartZ=0 EndX=-600 EndY=48 EndZ=0
    g5: LineSegment StartX=-600 StartY=48 StartZ=0 EndX=-600 EndY=28 EndZ=0
    g6: LineSegment StartX=-600 StartY=28 StartZ=0 EndX=-604 EndY=28 EndZ=0
    g7: LineSegment StartX=-604 StartY=28 StartZ=0 EndX=-604 EndY=48 EndZ=0
    g8: LineSegment StartX=604 StartY=-52 StartZ=0 EndX=600 EndY=-52 EndZ=0
    g9: LineSegment StartX=600 StartY=-52 StartZ=0 EndX=600 EndY=-32 EndZ=0
    g10: LineSegment StartX=600 StartY=-32 StartZ=0 EndX=604 EndY=-32 EndZ=0
    g11: LineSegment StartX=604 StartY=-32 StartZ=0 EndX=604 EndY=-52 EndZ=0
    g12: LineSegment StartX=600 StartY=8 StartZ=0 EndX=604 EndY=8 EndZ=0
    g13: LineSegment StartX=604 StartY=8 StartZ=0 EndX=604 EndY=-12 EndZ=0
    g14: LineSegment StartX=604 StartY=-12 StartZ=0 EndX=600 EndY=-12 EndZ=0
    g15: LineSegment StartX=600 StartY=-12 StartZ=0 EndX=600 EndY=8 EndZ=0
    g16: LineSegment StartX=600 StartY=48 StartZ=0 EndX=604 EndY=48 EndZ=0
    g17: LineSegment StartX=604 StartY=48 StartZ=0 EndX=604 EndY=28 EndZ=0
    g18: LineSegment StartX=604 StartY=28 StartZ=0 EndX=600 EndY=28 EndZ=0
    g19: LineSegment StartX=600 StartY=28 StartZ=0 EndX=600 EndY=48 EndZ=0
    g20: LineSegment StartX=600 StartY=88 StartZ=0 EndX=604 EndY=88 EndZ=0
    g21: LineSegment StartX=604 StartY=88 StartZ=0 EndX=604 EndY=68 EndZ=0
    g22: LineSegment StartX=604 StartY=68 StartZ=0 EndX=600 EndY=68 EndZ=0
    g23: LineSegment StartX=600 StartY=68 StartZ=0 EndX=600 EndY=88 EndZ=0
    g24: LineSegment StartX=600 StartY=128 StartZ=0 EndX=604 EndY=128 EndZ=0
    g25: LineSegment StartX=604 StartY=128 StartZ=0 EndX=604 EndY=108 EndZ=0
    g26: LineSegment StartX=604 StartY=108 StartZ=0 EndX=600 EndY=108 EndZ=0
    g27: LineSegment StartX=600 StartY=108 StartZ=0 EndX=600 EndY=128 EndZ=0
    g28: LineSegment StartX=600 StartY=168 StartZ=0 EndX=604 EndY=168 EndZ=0
    g29: LineSegment StartX=604 StartY=168 StartZ=0 EndX=604 EndY=148 EndZ=0
    g30: LineSegment StartX=604 StartY=148 StartZ=0 EndX=600 EndY=148 EndZ=0
    g31: LineSegment StartX=600 StartY=148 StartZ=0 EndX=600 EndY=168 EndZ=0
    g32: LineSegment StartX=604 StartY=208 StartZ=0 EndX=600 EndY=208 EndZ=0
    g33: LineSegment StartX=600 StartY=208 StartZ=0 EndX=600 EndY=188 EndZ=0
    g34: LineSegment StartX=600 StartY=188 StartZ=0 EndX=604 EndY=188 EndZ=0
    g35: LineSegment StartX=604 StartY=188 StartZ=0 EndX=604 EndY=208 EndZ=0
    g36: LineSegment StartX=604 StartY=248 StartZ=0 EndX=600 EndY=248 EndZ=0
    g37: LineSegment StartX=600 StartY=248 StartZ=0 EndX=600 EndY=228 EndZ=0
    g38: LineSegment StartX=600 StartY=228 StartZ=0 EndX=604 EndY=228 EndZ=0
    g39: LineSegment StartX=604 StartY=228 StartZ=0 EndX=604 EndY=248 EndZ=0
    g40: LineSegment StartX=604 StartY=288 StartZ=0 EndX=600 EndY=288 EndZ=0
    g41: LineSegment StartX=600 StartY=288 StartZ=0 EndX=600 EndY=268 EndZ=0
    g42: LineSegment StartX=600 StartY=268 StartZ=0 EndX=604 EndY=268 EndZ=0
    g43: LineSegment StartX=604 StartY=268 StartZ=0 EndX=604 EndY=288 EndZ=0
    g44: LineSegment StartX=604 StartY=328 StartZ=0 EndX=600 EndY=328 EndZ=0
    g45: LineSegment StartX=600 StartY=328 StartZ=0 EndX=600 EndY=308 EndZ=0
    g46: LineSegment StartX=600 StartY=308 StartZ=0 EndX=604 EndY=308 EndZ=0
    g47: LineSegment StartX=604 StartY=308 StartZ=0 EndX=604 EndY=328 EndZ=0
    g48: LineSegment StartX=604 StartY=368 StartZ=0 EndX=600 EndY=368 EndZ=0
    g49: LineSegment StartX=600 StartY=368 StartZ=0 EndX=600 EndY=348 EndZ=0
    g50: LineSegment StartX=600 StartY=348 StartZ=0 EndX=604 EndY=348 EndZ=0
    g51: LineSegment StartX=604 StartY=348 StartZ=0 EndX=604 EndY=368 EndZ=0
    g52: LineSegment StartX=604 StartY=408 StartZ=0 EndX=600 EndY=408 EndZ=0
    g53: LineSegment StartX=600 StartY=408 StartZ=0 EndX=600 EndY=388 EndZ=0
    g54: LineSegment StartX=600 StartY=388 StartZ=0 EndX=604 EndY=388 EndZ=0
    g55: LineSegment StartX=604 StartY=388 StartZ=0 EndX=604 EndY=408 EndZ=0
    g56: LineSegment StartX=604 StartY=448 StartZ=0 EndX=600 EndY=448 EndZ=0
    g57: LineSegment StartX=600 StartY=448 StartZ=0 EndX=600 EndY=428 EndZ=0
    g58: LineSegment StartX=600 StartY=428 StartZ=0 EndX=604 EndY=428 EndZ=0
    g59: LineSegment StartX=604 StartY=428 StartZ=0 EndX=604 EndY=448 EndZ=0
    g60: LineSegment StartX=604 StartY=488 StartZ=0 EndX=600 EndY=488 EndZ=0
    g61: LineSegment StartX=600 StartY=488 StartZ=0 EndX=600 EndY=468 EndZ=0
    g62: LineSegment StartX=600 StartY=468 StartZ=0 EndX=604 EndY=468 EndZ=0
    g63: LineSegment StartX=604 StartY=468 StartZ=0 EndX=604 EndY=488 EndZ=0
    g64: LineSegment StartX=604 StartY=528 StartZ=0 EndX=600 EndY=528 EndZ=0
    g65: LineSegment StartX=600 StartY=528 StartZ=0 EndX=600 EndY=508 EndZ=0
    g66: LineSegment StartX=600 StartY=508 StartZ=0 EndX=604 EndY=508 EndZ=0
    g67: LineSegment StartX=604 StartY=508 StartZ=0 EndX=604 EndY=528 EndZ=0
    g68: LineSegment StartX=604 StartY=568 StartZ=0 EndX=600 EndY=568 EndZ=0
    g69: LineSegment StartX=600 StartY=568 StartZ=0 EndX=600 EndY=548 EndZ=0
    g70: LineSegment StartX=600 StartY=548 StartZ=0 EndX=604 EndY=548 EndZ=0
    g71: LineSegment StartX=604 StartY=548 StartZ=0 EndX=604 EndY=568 EndZ=0
    g72: LineSegment StartX=-604 StartY=8 StartZ=0 EndX=-600 EndY=8 EndZ=0
    g73: LineSegment StartX=-600 StartY=8 StartZ=0 EndX=-600 EndY=-12 EndZ=0
    g74: LineSegment StartX=-600 StartY=-12 StartZ=0 EndX=-604 EndY=-12 EndZ=0
    g75: LineSegment StartX=-604 StartY=-12 StartZ=0 EndX=-604 EndY=8 EndZ=0
    g76: LineSegment StartX=-604 StartY=75 StartZ=0 EndX=-600 EndY=75 EndZ=0
    g77: LineSegment StartX=-600 StartY=75 StartZ=0 EndX=-600 EndY=68 EndZ=0
    g78: LineSegment StartX=-600 StartY=68 StartZ=0 EndX=-604 EndY=68 EndZ=0
    g79: LineSegment StartX=-604 StartY=68 StartZ=0 EndX=-604 EndY=75 EndZ=0
  constraints (239):
    c: Coincident(g0,g1)
    c: Coincident(g1,g2)
    c: Coincident(g2,g3)
    c: Coincident(g3,g0)
    c: Horizontal(g0)
    c: Horizontal(g2)
    c: Vertical(g1)
    c: Vertical(g3)
    c: DistanceX(g-3,g0) = 0
    c: DistanceY(g0,g-3) = 0
    c: DistanceX(g0,g0) = 4
    c: DistanceY(g0,g2) = 20
    c: Coincident(g4,g5)
    c: Coincident(g5,g6)
    c: Coincident(g6,g7)
    c: Coincident(g7,g4)
    c: Horizontal(g4)
    c: Horizontal(g6)
    c: Vertical(g5)
    c: Vertical(g7)
    c: DistanceY(g6,g4) = 20
    c: Coincident(g8,g9)
    c: Coincident(g9,g10)
    c: Coincident(g10,g11)
    c: Coincident(g11,g8)
    c: Horizontal(g8)
    c: Horizontal(g10)
    c: Vertical(g9)
    c: Vertical(g11)
    c: Coincident(g8,g-4)
    c: DistanceX(g8,g8) = 4
    c: DistanceY(g8,g10) = 20
    c: Coincident(g12,g13)
    c: Coincident(g13,g14)
    c: Coincident(g14,g15)
    c: Coincident(g15,g12)
    c: Horizontal(g12)
    c: Horizontal(g14)
    c: Vertical(g13)
    c: Vertical(g15)
    c: Vertical(g9,g14)
    c: Vertical(g13,g10)
    c: DistanceY(g10,g13) = 20
    c: DistanceY(g13,g12) = 20
    c: Coincident(g16,g17)
    c: Coincident(g17,g18)
    c: Coincident(g18,g19)
    c: Coincident(g19,g16)
    c: Horizontal(g16)
    c: Horizontal(g18)
    c: Vertical(g17)
    c: Vertical(g19)
    c: Vertical(g12,g18)
    c: DistanceY(g12,g17) = 20
    c: DistanceY(g17,g16) = 20
    c: Coincident(g20,g21)
    c: Coincident(g21,g22)
    c: Coincident(g22,g23)
    c: Coincident(g23,g20)
    c: Horizontal(g20)
    c: Horizontal(g22)
    c: Vertical(g21)
    c: Vertical(g23)
    c: Coincident(g24,g25)
    c: Coincident(g25,g26)
    c: Coincident(g26,g27)
    c: Coincident(g27,g24)
    c: Horizontal(g24)
    c: Horizontal(g26)
    c: Vertical(g25)
    c: Vertical(g27)
    c: Coincident(g28,g29)
    c: Coincident(g29,g30)
    c: Coincident(g30,g31)
    c: Coincident(g31,g28)
    c: Horizontal(g28)
    c: Horizontal(g30)
    c: Vertical(g29)
    c: Vertical(g31)
    c: Vertical(g16,g21)
    c: Vertical(g20,g25)
    c: Vertical(g24,g29)
    c: Vertical(g30,g24)
    c: Vertical(g26,g20)
    c: Vertical(g22,g16)
    c: DistanceY(g16,g21) = 20
    c: DistanceY(g21,g20) = 20
    c: DistanceY(g20,g25) = 20
    c: DistanceY(g25,g24) = 20
    c: DistanceY(g24,g29) = 20
    c: DistanceY(g29,g28) = 20
    c: Vertical(g12,g17)
    c: Coincident(g32,g33)
    c: Coincident(g33,g34)
    c: Coincident(g34,g35)
    c: Coincident(g35,g32)
    c: Horizontal(g32)
    c: Horizontal(g34)
    c: Vertical(g33)
    c: Vertical(g35)
    c: Coincident(g36,g37)
    c: Coincident(g37,g38)
    c: Coincident(g38,g39)
    c: Coincident(g39,g36)
    c: Horizontal(g36)
    c: Horizontal(g38)
    c: Vertical(g37)
    c: Vertical(g39)
    c: Coincident(g40,g41)
    c: Coincident(g41,g42)
    c: Coincident(g42,g43)
    c: Coincident(g43,g40)
    c: Horizontal(g40)
    c: Horizontal(g42)
    c: Vertical(g41)
    c: Vertical(g43)
    c: Coincident(g44,g45)
    c: Coincident(g45,g46)
    c: Coincident(g46,g47)
    c: Coincident(g47,g44)
    c: Horizontal(g44)
    c: Horizontal(g46)
    c: Vertical(g45)
    c: Vertical(g47)
    c: Coincident(g48,g49)
    c: Coincident(g49,g50)
    c: Coincident(g50,g51)
    c: Coincident(g51,g48)
    c: Horizontal(g48)
    c: Horizontal(g50)
    c: Vertical(g49)
    c: Vertical(g51)
    c: Coincident(g52,g53)
    c: Coincident(g53,g54)
    c: Coincident(g54,g55)
    c: Coincident(g55,g52)
    c: Horizontal(g52)
    c: Horizontal(g54)
    c: Vertical(g53)
    c: Vertical(g55)
    c: Vertical(g28,g34)
    c: Vertical(g28,g33)
    c: Vertical(g32,g37)
    c: Vertical(g38,g32)
    c: Vertical(g36,g42)
    c: Vertical(g36,g41)
    c: Vertical(g40,g45)
    c: Vertical(g46,g40)
    c: Vertical(g49,g44)
    c: Vertical(g44,g50)
    c: Vertical(g48,g53)
    c: Vertical(g54,g48)
    c: DistanceY(g28,g34) = 20
    c: DistanceY(g34,g32) = 20
    c: DistanceY(g32,g38) = 20
    c: DistanceY(g38,g36) = 20
    c: DistanceY(g36,g42) = 20
    c: DistanceY(g42,g40) = 20
    c: DistanceY(g40,g46) = 20
    c: DistanceY(g46,g44) = 20
    c: DistanceY(g44,g50) = 20
    c: DistanceY(g50,g48) = 20
    c: DistanceY(g48,g54) = 20
    c: DistanceY(g54,g52) = 20
    c: Coincident(g56,g57)
    c: Coincident(g57,g58)
    c: Coincident(g58,g59)
    c: Coincident(g59,g56)
    c: Horizontal(g56)
    c: Horizontal(g58)
    c: Vertical(g57)
    c: Vertical(g59)
    c: Coincident(g60,g61)
    c: Coincident(g61,g62)
    c: Coincident(g62,g63)
    c: Coincident(g63,g60)
    c: Horizontal(g60)
    c: Horizontal(g62)
    c: Vertical(g61)
    c: Vertical(g63)
    c: Coincident(g64,g65)
    c: Coincident(g65,g66)
    c: Coincident(g66,g67)
    c: Coincident(g67,g64)
    c: Horizontal(g64)
    c: Horizontal(g66)
    c: Vertical(g65)
    c: Vertical(g67)
    c: Coincident(g68,g69)
    c: Coincident(g69,g70)
    c: Coincident(g70,g71)
    c: Coincident(g71,g68)
    c: Horizontal(g68)
    c: Horizontal(g70)
    c: Vertical(g69)
    c: Vertical(g71)
    c: Vertical(g52,g58)
    c: Vertical(g56,g62)
    c: Vertical(g60,g66)
    c: Vertical(g52,g57)
    c: Vertical(g61,g56)
    c: Vertical(g65,g60)
    c: DistanceY(g52,g58) = 20
    c: DistanceY(g58,g56) = 20
    c: DistanceY(g56,g62) = 20
    c: DistanceY(g62,g60) = 20
    c: DistanceY(g60,g66) = 20
    c: DistanceY(g66,g64) = 20
    c: DistanceY(g64,g70) = 20
    c: Vertical(g70,g64)
    c: Vertical(g64,g69)
    c: DistanceY(g70,g68) = 20
    c: Coincident(g72,g73)
    c: Coincident(g73,g74)
    c: Coincident(g74,g75)
    c: Coincident(g75,g72)
    c: Horizontal(g72)
    c: Horizontal(g74)
    c: Vertical(g73)
    c: Vertical(g75)
    c: Vertical(g2,g74)
    c: Vertical(g72,g6)
    c: Vertical(g72,g5)
    c: Vertical(g73,g1)
    c: DistanceY(g72,g6) = 20
    c: DistanceY(g74,g72) = 20
    c: DistanceY(g2,g74) = 20
    c: Coincident(g76,g77)
    c: Coincident(g77,g78)
    c: Coincident(g78,g79)
    c: Coincident(g79,g76)
    c: Horizontal(g76)
    c: Horizontal(g78)
    c: Vertical(g77)
    c: Vertical(g79)
    c: Vertical(g4,g78)
    c: Vertical(g77,g4)
    c: DistanceY(g4,g78) = 20
    c: DistanceY(g78,g76) = 7
FEATURE [PartDesign::Pocket] Pocket007
  BaseFeature = -> Pad008
  Length = 4
  Length2 = 5
  Placement = pos=(0,0,0) rot=(0.57735,0.57735,0.57735;2.0944rad)
  Profile = -> Sketch018
  Type = 0
FEATURE [PartDesign::Body] Body008  label="Sidkant-Yttre-1"
  Group = -> [Sketch017,Pad008,Sketch018,Pocket007]
  Origin = -> Origin008
  Placement = pos=(1000,0,0) rot=(0,0,1;0rad)
  Tip = -> Pocket007
FEATURE [Sketcher::SketchObject] Sketch019
  FullyConstrained = true
  MapMode = 5
  Placement = pos=(0,0,0) rot=(0.57735,0.57735,0.57735;2.0944rad)
  Support = -> [YZ_Plane009]
  sketch-geometry (10):
    g0: LineSegment StartX=604 StartY=-52 StartZ=0 EndX=-604 EndY=-52 EndZ=0
    g1: LineSegment StartX=-604 StartY=-52 StartZ=0 EndX=-604 EndY=75 EndZ=0
    g2: LineSegment StartX=604 StartY=75 StartZ=0 EndX=604 EndY=-52 EndZ=0
    g3: LineSegment StartX=604 StartY=75 StartZ=0 EndX=604 EndY=575 EndZ=0
    g4: LineSegment StartX=-604 StartY=75 StartZ=0 EndX=0 EndY=575 EndZ=0
    g5: Circle CenterX=0 CenterY=575 CenterZ=0 NormalX=0 NormalY=0 NormalZ=1 AngleXU=0 Radius=1
    g6: Circle CenterX=604 CenterY=575 CenterZ=0 NormalX=0 NormalY=0 NormalZ=1 AngleXU=0 Radius=1
    g7: BSplineCurve PolesCount=2 KnotsCount=2 Degree=1 IsPeriodic=0
    g8: GeomPoint X=0 Y=575 Z=0
    g9: GeomPoint X=604 Y=575 Z=0
  constraints (24):
    c: Coincident(g0,g1)
    c: Coincident(g2,g0)
    c: Horizontal(g0)
    c: Vertical(g1)
    c: Vertical(g2)
    c: DistanceX(g0,g-1) = 604
    c: DistanceX(g0,g0) = 1208
    c: DistanceY(g0,g-1) = 52
    c: DistanceY(g-1,g1) = 75
    c: Coincident(g3,g2)
    c: Vertical(g3)
    c: Horizontal(g1,g2)
    c: DistanceY(g2,g3) = 500
    c: Coincident(g4,g1)
    c: PointOnObject(g4,g-2)
    c: Horizontal(g4,g3)
    c: Weight(g5) = 1
    c: Coincident(g7,g4)
    c: Equal(g5,g6)
    c: Coincident(g7,g3)
    c: InternalAlignment(g5,g7)
    c: InternalAlignment(g6,g7)
    c: InternalAlignment(g8,g7)
    c: InternalAlignment(g9,g7)
FEATURE [PartDesign::Pad] Pad009
  Direction = (1,-2e-16,3e-16)
  Length = 4
  Length2 = 10
  Placement = pos=(0,0,0) rot=(0.57735,0.57735,0.57735;2.0944rad)
  Profile = -> Sketch019
  Type = 0
FEATURE [Sketcher::SketchObject] Sketch020
  ExternalGeometry = -> [Pad009]
  FullyConstrained = true
  MapMode = 5
  Placement = pos=(4,-9e-16,9e-16) rot=(0.57735,0.57735,0.57735;2.0944rad)
  Support = -> [Pad009]
  sketch-geometry (80):
    g0: LineSegment StartX=-604 StartY=-52 StartZ=0 EndX=-600 EndY=-52 EndZ=0
    g1: LineSegment StartX=-600 StartY=-52 StartZ=0 EndX=-600 EndY=-32 EndZ=0
    g2: LineSegment StartX=-600 StartY=-32 StartZ=0 EndX=-604 EndY=-32 EndZ=0
    g3: LineSegment StartX=-604 StartY=-32 StartZ=0 EndX=-604 EndY=-52 EndZ=0
    g4: LineSegment StartX=-604 StartY=48 StartZ=0 EndX=-600 EndY=48 EndZ=0
    g5: LineSegment StartX=-600 StartY=48 StartZ=0 EndX=-600 EndY=28 EndZ=0
    g6: LineSegment StartX=-600 StartY=28 StartZ=0 EndX=-604 EndY=28 EndZ=0
    g7: LineSegment StartX=-604 StartY=28 StartZ=0 EndX=-604 EndY=48 EndZ=0
    g8: LineSegment StartX=604 StartY=-52 StartZ=0 EndX=600 EndY=-52 EndZ=0
    g9: LineSegment StartX=600 StartY=-52 StartZ=0 EndX=600 EndY=-32 EndZ=0
    g10: LineSegment StartX=600 StartY=-32 StartZ=0 EndX=604 EndY=-32 EndZ=0
    g11: LineSegment StartX=604 StartY=-32 StartZ=0 EndX=604 EndY=-52 EndZ=0
    g12: LineSegment StartX=600 StartY=8 StartZ=0 EndX=604 EndY=8 EndZ=0
    g13: LineSegment StartX=604 StartY=8 StartZ=0 EndX=604 EndY=-12 EndZ=0
    g14: LineSegment StartX=604 StartY=-12 StartZ=0 EndX=600 EndY=-12 EndZ=0
    g15: LineSegment StartX=600 StartY=-12 StartZ=0 EndX=600 EndY=8 EndZ=0
    g16: LineSegment StartX=600 StartY=48 StartZ=0 EndX=604 EndY=48 EndZ=0
    g17: LineSegment StartX=604 StartY=48 StartZ=0 EndX=604 EndY=28 EndZ=0
    g18: LineSegment StartX=604 StartY=28 StartZ=0 EndX=600 EndY=28 EndZ=0
    g19: LineSegment StartX=600 StartY=28 StartZ=0 EndX=600 EndY=48 EndZ=0
    g20: LineSegment StartX=600 StartY=88 StartZ=0 EndX=604 EndY=88 EndZ=0
    g21: LineSegment StartX=604 StartY=88 StartZ=0 EndX=604 EndY=68 EndZ=0
    g22: LineSegment StartX=604 StartY=68 StartZ=0 EndX=600 EndY=68 EndZ=0
    g23: LineSegment StartX=600 StartY=68 StartZ=0 EndX=600 EndY=88 EndZ=0
    g24: LineSegment StartX=600 StartY=128 StartZ=0 EndX=604 EndY=128 EndZ=0
    g25: LineSegment StartX=604 StartY=128 StartZ=0 EndX=604 EndY=108 EndZ=0
    g26: LineSegment StartX=604 StartY=108 StartZ=0 EndX=600 EndY=108 EndZ=0
    g27: LineSegment StartX=600 StartY=108 StartZ=0 EndX=600 EndY=128 EndZ=0
    g28: LineSegment StartX=600 StartY=168 StartZ=0 EndX=604 EndY=168 EndZ=0
    g29: LineSegment StartX=604 StartY=168 StartZ=0 EndX=604 EndY=148 EndZ=0
    g30: LineSegment StartX=604 StartY=148 StartZ=0 EndX=600 EndY=148 EndZ=0
    g31: LineSegment StartX=600 StartY=148 StartZ=0 EndX=600 EndY=168 EndZ=0
    g32: LineSegment StartX=604 StartY=208 StartZ=0 EndX=600 EndY=208 EndZ=0
    g33: LineSegment StartX=600 StartY=208 StartZ=0 EndX=600 EndY=188 EndZ=0
    g34: LineSegment StartX=600 StartY=188 StartZ=0 EndX=604 EndY=188 EndZ=0
    g35: LineSegment StartX=604 StartY=188 StartZ=0 EndX=604 EndY=208 EndZ=0
    g36: LineSegment StartX=604 StartY=248 StartZ=0 EndX=600 EndY=248 EndZ=0
    g37: LineSegment StartX=600 StartY=248 StartZ=0 EndX=600 EndY=228 EndZ=0
    g38: LineSegment StartX=600 StartY=228 StartZ=0 EndX=604 EndY=228 EndZ=0
    g39: LineSegment StartX=604 StartY=228 StartZ=0 EndX=604 EndY=248 EndZ=0
    g40: LineSegment StartX=604 StartY=288 StartZ=0 EndX=600 EndY=288 EndZ=0
    g41: LineSegment StartX=600 StartY=288 StartZ=0 EndX=600 EndY=268 EndZ=0
    g42: LineSegment StartX=600 StartY=268 StartZ=0 EndX=604 EndY=268 EndZ=0
    g43: LineSegment StartX=604 StartY=268 StartZ=0 EndX=604 EndY=288 EndZ=0
    g44: LineSegment StartX=604 StartY=328 StartZ=0 EndX=600 EndY=328 EndZ=0
    g45: LineSegment StartX=600 StartY=328 StartZ=0 EndX=600 EndY=308 EndZ=0
    g46: LineSegment StartX=600 StartY=308 StartZ=0 EndX=604 EndY=308 EndZ=0
    g47: LineSegment StartX=604 StartY=308 StartZ=0 EndX=604 EndY=328 EndZ=0
    g48: LineSegment StartX=604 StartY=368 StartZ=0 EndX=600 EndY=368 EndZ=0
    g49: LineSegment StartX=600 StartY=368 StartZ=0 EndX=600 EndY=348 EndZ=0
    g50: LineSegment StartX=600 StartY=348 StartZ=0 EndX=604 EndY=348 EndZ=0
    g51: LineSegment StartX=604 StartY=348 StartZ=0 EndX=604 EndY=368 EndZ=0
    g52: LineSegment StartX=604 StartY=408 StartZ=0 EndX=600 EndY=408 EndZ=0
    g53: LineSegment StartX=600 StartY=408 StartZ=0 EndX=600 EndY=388 EndZ=0
    g54: LineSegment StartX=600 StartY=388 StartZ=0 EndX=604 EndY=388 EndZ=0
    g55: LineSegment StartX=604 StartY=388 StartZ=0 EndX=604 EndY=408 EndZ=0
    g56: LineSegment StartX=604 StartY=448 StartZ=0 EndX=600 EndY=448 EndZ=0
    g57: LineSegment StartX=600 StartY=448 StartZ=0 EndX=600 EndY=428 EndZ=0
    g58: LineSegment StartX=600 StartY=428 StartZ=0 EndX=604 EndY=428 EndZ=0
    g59: LineSegment StartX=604 StartY=428 StartZ=0 EndX=604 EndY=448 EndZ=0
    g60: LineSegment StartX=604 StartY=488 StartZ=0 EndX=600 EndY=488 EndZ=0
    g61: LineSegment StartX=600 StartY=488 StartZ=0 EndX=600 EndY=468 EndZ=0
    g62: LineSegment StartX=600 StartY=468 StartZ=0 EndX=604 EndY=468 EndZ=0
    g63: LineSegment StartX=604 StartY=468 StartZ=0 EndX=604 EndY=488 EndZ=0
    g64: LineSegment StartX=604 StartY=528 StartZ=0 EndX=600 EndY=528 EndZ=0
    g65: LineSegment StartX=600 StartY=528 StartZ=0 EndX=600 EndY=508 EndZ=0
    g66: LineSegment StartX=600 StartY=508 StartZ=0 EndX=604 EndY=508 EndZ=0
    g67: LineSegment StartX=604 StartY=508 StartZ=0 EndX=604 EndY=528 EndZ=0
    g68: LineSegment StartX=604 StartY=568 StartZ=0 EndX=600 EndY=568 EndZ=0
    g69: LineSegment StartX=600 StartY=568 StartZ=0 EndX=600 EndY=548 EndZ=0
    g70: LineSegment StartX=600 StartY=548 StartZ=0 EndX=604 EndY=548 EndZ=0
    g71: LineSegment StartX=604 StartY=548 StartZ=0 EndX=604 EndY=568 EndZ=0
    g72: LineSegment StartX=-604 StartY=8 StartZ=0 EndX=-600 EndY=8 EndZ=0
    g73: LineSegment StartX=-600 StartY=8 StartZ=0 EndX=-600 EndY=-12 EndZ=0
    g74: LineSegment StartX=-600 StartY=-12 StartZ=0 EndX=-604 EndY=-12 EndZ=0
    g75: LineSegment StartX=-604 StartY=-12 StartZ=0 EndX=-604 EndY=8 EndZ=0
    g76: LineSegment StartX=-604 StartY=75 StartZ=0 EndX=-600 EndY=75 EndZ=0
    g77: LineSegment StartX=-600 StartY=75 StartZ=0 EndX=-600 EndY=68 EndZ=0
    g78: LineSegment StartX=-600 StartY=68 StartZ=0 EndX=-604 EndY=68 EndZ=0
    g79: LineSegment StartX=-604 StartY=68 StartZ=0 EndX=-604 EndY=75 EndZ=0
  constraints (239):
    c: Coincident(g0,g1)
    c: Coincident(g1,g2)
    c: Coincident(g2,g3)
    c: Coincident(g3,g0)
    c: Horizontal(g0)
    c: Horizontal(g2)
    c: Vertical(g1)
    c: Vertical(g3)
    c: DistanceX(g-3,g0) = 0
    c: DistanceY(g0,g-3) = 0
    c: DistanceX(g0,g0) = 4
    c: DistanceY(g0,g2) = 20
    c: Coincident(g4,g5)
    c: Coincident(g5,g6)
    c: Coincident(g6,g7)
    c: Coincident(g7,g4)
    c: Horizontal(g4)
    c: Horizontal(g6)
    c: Vertical(g5)
    c: Vertical(g7)
    c: DistanceY(g6,g4) = 20
    c: Coincident(g8,g9)
    c: Coincident(g9,g10)
    c: Coincident(g10,g11)
    c: Coincident(g11,g8)
    c: Horizontal(g8)
    c: Horizontal(g10)
    c: Vertical(g9)
    c: Vertical(g11)
    c: Coincident(g8,g-4)
    c: DistanceX(g8,g8) = 4
    c: DistanceY(g8,g10) = 20
    c: Coincident(g12,g13)
    c: Coincident(g13,g14)
    c: Coincident(g14,g15)
    c: Coincident(g15,g12)
    c: Horizontal(g12)
    c: Horizontal(g14)
    c: Vertical(g13)
    c: Vertical(g15)
    c: Vertical(g9,g14)
    c: Vertical(g13,g10)
    c: DistanceY(g10,g13) = 20
    c: DistanceY(g13,g12) = 20
    c: Coincident(g16,g17)
    c: Coincident(g17,g18)
    c: Coincident(g18,g19)
    c: Coincident(g19,g16)
    c: Horizontal(g16)
    c: Horizontal(g18)
    c: Vertical(g17)
    c: Vertical(g19)
    c: Vertical(g12,g18)
    c: DistanceY(g12,g17) = 20
    c: DistanceY(g17,g16) = 20
    c: Coincident(g20,g21)
    c: Coincident(g21,g22)
    c: Coincident(g22,g23)
    c: Coincident(g23,g20)
    c: Horizontal(g20)
    c: Horizontal(g22)
    c: Vertical(g21)
    c: Vertical(g23)
    c: Coincident(g24,g25)
    c: Coincident(g25,g26)
    c: Coincident(g26,g27)
    c: Coincident(g27,g24)
    c: Horizontal(g24)
    c: Horizontal(g26)
    c: Vertical(g25)
    c: Vertical(g27)
    c: Coincident(g28,g29)
    c: Coincident(g29,g30)
    c: Coincident(g30,g31)
    c: Coincident(g31,g28)
    c: Horizontal(g28)
    c: Horizontal(g30)
    c: Vertical(g29)
    c: Vertical(g31)
    c: Vertical(g16,g21)
    c: Vertical(g20,g25)
    c: Vertical(g24,g29)
    c: Vertical(g30,g24)
    c: Vertical(g26,g20)
    c: Vertical(g22,g16)
    c: DistanceY(g16,g21) = 20
    c: DistanceY(g21,g20) = 20
    c: DistanceY(g20,g25) = 20
    c: DistanceY(g25,g24) = 20
    c: DistanceY(g24,g29) = 20
    c: DistanceY(g29,g28) = 20
    c: Vertical(g12,g17)
    c: Coincident(g32,g33)
    c: Coincident(g33,g34)
    c: Coincident(g34,g35)
    c: Coincident(g35,g32)
    c: Horizontal(g32)
    c: Horizontal(g34)
    c: Vertical(g33)
    c: Vertical(g35)
    c: Coincident(g36,g37)
    c: Coincident(g37,g38)
    c: Coincident(g38,g39)
    c: Coincident(g39,g36)
    c: Horizontal(g36)
    c: Horizontal(g38)
    c: Vertical(g37)
    c: Vertical(g39)
    c: Coincident(g40,g41)
    c: Coincident(g41,g42)
    c: Coincident(g42,g43)
    c: Coincident(g43,g40)
    c: Horizontal(g40)
    c: Horizontal(g42)
    c: Vertical(g41)
    c: Vertical(g43)
    c: Coincident(g44,g45)
    c: Coincident(g45,g46)
    c: Coincident(g46,g47)
    c: Coincident(g47,g44)
    c: Horizontal(g44)
    c: Horizontal(g46)
    c: Vertical(g45)
    c: Vertical(g47)
    c: Coincident(g48,g49)
    c: Coincident(g49,g50)
    c: Coincident(g50,g51)
    c: Coincident(g51,g48)
    c: Horizontal(g48)
    c: Horizontal(g50)
    c: Vertical(g49)
    c: Vertical(g51)
    c: Coincident(g52,g53)
    c: Coincident(g53,g54)
    c: Coincident(g54,g55)
    c: Coincident(g55,g52)
    c: Horizontal(g52)
    c: Horizontal(g54)
    c: Vertical(g53)
    c: Vertical(g55)
    c: Vertical(g28,g34)
    c: Vertical(g28,g33)
    c: Vertical(g32,g37)
    c: Vertical(g38,g32)
    c: Vertical(g36,g42)
    c: Vertical(g36,g41)
    c: Vertical(g40,g45)
    c: Vertical(g46,g40)
    c: Vertical(g49,g44)
    c: Vertical(g44,g50)
    c: Vertical(g48,g53)
    c: Vertical(g54,g48)
    c: DistanceY(g28,g34) = 20
    c: DistanceY(g34,g32) = 20
    c: DistanceY(g32,g38) = 20
    c: DistanceY(g38,g36) = 20
    c: DistanceY(g36,g42) = 20
    c: DistanceY(g42,g40) = 20
    c: DistanceY(g40,g46) = 20
    c: DistanceY(g46,g44) = 20
    c: DistanceY(g44,g50) = 20
    c: DistanceY(g50,g48) = 20
    c: DistanceY(g48,g54) = 20
    c: DistanceY(g54,g52) = 20
    c: Coincident(g56,g57)
    c: Coincident(g57,g58)
    c: Coincident(g58,g59)
    c: Coincident(g59,g56)
    c: Horizontal(g56)
    c: Horizontal(g58)
    c: Vertical(g57)
    c: Vertical(g59)
    c: Coincident(g60,g61)
    c: Coincident(g61,g62)
    c: Coincident(g62,g63)
    c: Coincident(g63,g60)
    c: Horizontal(g60)
    c: Horizontal(g62)
    c: Vertical(g61)
    c: Vertical(g63)
    c: Coincident(g64,g65)
    c: Coincident(g65,g66)
    c: Coincident(g66,g67)
    c: Coincident(g67,g64)
    c: Horizontal(g64)
    c: Horizontal(g66)
    c: Vertical(g65)
    c: Vertical(g67)
    c: Coincident(g68,g69)
    c: Coincident(g69,g70)
    c: Coincident(g70,g71)
    c: Coincident(g71,g68)
    c: Horizontal(g68)
    c: Horizontal(g70)
    c: Vertical(g69)
    c: Vertical(g71)
    c: Vertical(g52,g58)
    c: Vertical(g56,g62)
    c: Vertical(g60,g66)
    c: Vertical(g52,g57)
    c: Vertical(g61,g56)
    c: Vertical(g65,g60)
    c: DistanceY(g52,g58) = 20
    c: DistanceY(g58,g56) = 20
    c: DistanceY(g56,g62) = 20
    c: DistanceY(g62,g60) = 20
    c: DistanceY(g60,g66) = 20
    c: DistanceY(g66,g64) = 20
    c: DistanceY(g64,g70) = 20
    c: Vertical(g70,g64)
    c: Vertical(g64,g69)
    c: DistanceY(g70,g68) = 20
    c: Coincident(g72,g73)
    c: Coincident(g73,g74)
    c: Coincident(g74,g75)
    c: Coincident(g75,g72)
    c: Horizontal(g72)
    c: Horizontal(g74)
    c: Vertical(g73)
    c: Vertical(g75)
    c: Vertical(g2,g74)
    c: Vertical(g72,g6)
    c: Vertical(g5,g72)
    c: Vertical(g73,g1)
    c: DistanceY(g2,g74) = 20
    c: DistanceY(g74,g72) = 20
    c: DistanceY(g72,g6) = 20
    c: Coincident(g76,g77)
    c: Coincident(g77,g78)
    c: Coincident(g78,g79)
    c: Coincident(g79,g76)
    c: Horizontal(g76)
    c: Horizontal(g78)
    c: Vertical(g77)
    c: Vertical(g79)
    c: Vertical(g4,g78)
    c: Vertical(g77,g4)
    c: DistanceY(g4,g78) = 20
    c: DistanceY(g78,g76) = 7
FEATURE [PartDesign::Pocket] Pocket008
  BaseFeature = -> Pad009
  Length = 4
  Length2 = 5
  Placement = pos=(0,0,0) rot=(0.57735,0.57735,0.57735;2.0944rad)
  Profile = -> Sketch020
  Type = 0
FEATURE [PartDesign::Body] Body009  label="Sidkant-Yttre-2"
  Group = -> [Sketch019,Pad009,Sketch020,Pocket008]
  Origin = -> Origin009
  Placement = pos=(-1004,0,0) rot=(0,0,1;0rad)
  Tip = -> Pocket008
FEATURE [Sketcher::SketchObject] Sketch021
  FullyConstrained = true
  MapMode = 5
  Placement = pos=(0,0,0) rot=(1,0,0;1.5708rad)
  Support = -> [XZ_Plane010]
  sketch-geometry (4):
    g0: LineSegment StartX=-1004 StartY=-52 StartZ=0 EndX=1004 EndY=-52 EndZ=0
    g1: LineSegment StartX=1004 StartY=-52 StartZ=0 EndX=1004 EndY=75 EndZ=0
    g2: LineSegment StartX=1004 StartY=75 StartZ=0 EndX=-1004 EndY=75 EndZ=0
    g3: LineSegment StartX=-1004 StartY=75 StartZ=0 EndX=-1004 EndY=-52 EndZ=0
  constraints (12):
    c: Coincident(g0,g1)
    c: Coincident(g1,g2)
    c: Coincident(g2,g3)
    c: Coincident(g3,g0)
    c: Horizontal(g0)
    c: Horizontal(g2)
    c: Vertical(g1)
    c: Vertical(g3)
    c: DistanceY(g0,g-1) = 52
    c: DistanceX(g0,g-1) = 1004
    c: DistanceX(g0,g0) = 2008
    c: DistanceY(g-1,g2) = 75
FEATURE [PartDesign::Pad] Pad010
  Direction = (0,-1,-2e-16)
  Length = 4
  Length2 = 10
  Placement = pos=(0,0,0) rot=(1,0,0;1.5708rad)
  Profile = -> Sketch021
  Type = 0
FEATURE [Sketcher::SketchObject] Sketch024
  FullyConstrained = true
  MapMode = 5
  Placement = pos=(0,0,0) rot=(1,0,0;1.5708rad)
  Support = -> [XZ_Plane011]
  sketch-geometry (4):
    g0: LineSegment StartX=-1004 StartY=575 StartZ=0 EndX=1004 EndY=575 EndZ=0
    g1: LineSegment StartX=1004 StartY=575 StartZ=0 EndX=1004 EndY=-52 EndZ=0
    g2: LineSegment StartX=1004 StartY=-52 StartZ=0 EndX=-1004 EndY=-52 EndZ=0
    g3: LineSegment StartX=-1004 StartY=-52 StartZ=0 EndX=-1004 EndY=575 EndZ=0
  constraints (12):
    c: Coincident(g0,g1)
    c: Coincident(g1,g2)
    c: Coincident(g2,g3)
    c: Coincident(g3,g0)
    c: Horizontal(g0)
    c: Horizontal(g2)
    c: Vertical(g1)
    c: Vertical(g3)
    c: DistanceY(g2,g-1) = 52
    c: DistanceX(g2,g-1) = 1004
    c: DistanceX(g2,g1) = 2008
    c: DistanceY(g-1,g0) = 575
FEATURE [PartDesign::Pad] Pad011
  Direction = (0,-1,2e-16)
  Length = 4
  Length2 = 10
  Placement = pos=(0,0,0) rot=(1,0,0;1.5708rad)
  Profile = -> Sketch024
  Type = 0
FEATURE [Sketcher::SketchObject] Sketch025
  ExternalGeometry = -> [Pad011]
  FullyConstrained = true
  MapMode = 5
  Placement = pos=(0,-4,0) rot=(1,0,0;1.5708rad)
  Support = -> [Pad011]
  sketch-geometry (128):
    g0: LineSegment StartX=-1004 StartY=-12 StartZ=0 EndX=-1000 EndY=-12 EndZ=0
    g1: LineSegment StartX=-1000 StartY=-12 StartZ=0 EndX=-1000 EndY=-32 EndZ=0
    g2: LineSegment StartX=-1000 StartY=-32 StartZ=0 EndX=-1004 EndY=-32 EndZ=0
    g3: LineSegment StartX=-1004 StartY=-32 StartZ=0 EndX=-1004 EndY=-12 EndZ=0
    g4: LineSegment StartX=-1004 StartY=28 StartZ=0 EndX=-1000 EndY=28 EndZ=0
    g5: LineSegment StartX=-1000 StartY=28 StartZ=0 EndX=-1000 EndY=8 EndZ=0
    g6: LineSegment StartX=-1000 StartY=8 StartZ=0 EndX=-1004 EndY=8 EndZ=0
    g7: LineSegment StartX=-1004 StartY=8 StartZ=0 EndX=-1004 EndY=28 EndZ=0
    g8: LineSegment StartX=-1004 StartY=68 StartZ=0 EndX=-1000 EndY=68 EndZ=0
    g9: LineSegment StartX=-1000 StartY=68 StartZ=0 EndX=-1000 EndY=48 EndZ=0
    g10: LineSegment StartX=-1000 StartY=48 StartZ=0 EndX=-1004 EndY=48 EndZ=0
    g11: LineSegment StartX=-1004 StartY=48 StartZ=0 EndX=-1004 EndY=68 EndZ=0
    g12: LineSegment StartX=-1004 StartY=108 StartZ=0 EndX=-1000 EndY=108 EndZ=0
    g13: LineSegment StartX=-1000 StartY=108 StartZ=0 EndX=-1000 EndY=88 EndZ=0
    g14: LineSegment StartX=-1000 StartY=88 StartZ=0 EndX=-1004 EndY=88 EndZ=0
    g15: LineSegment StartX=-1004 StartY=88 StartZ=0 EndX=-1004 EndY=108 EndZ=0
    g16: LineSegment StartX=-1004 StartY=148 StartZ=0 EndX=-1000 EndY=148 EndZ=0
    g17: LineSegment StartX=-1000 StartY=148 StartZ=0 EndX=-1000 EndY=128 EndZ=0
    g18: LineSegment StartX=-1000 StartY=128 StartZ=0 EndX=-1004 EndY=128 EndZ=0
    g19: LineSegment StartX=-1004 StartY=128 StartZ=0 EndX=-1004 EndY=148 EndZ=0
    g20: LineSegment StartX=-1004 StartY=188 StartZ=0 EndX=-1000 EndY=188 EndZ=0
    g21: LineSegment StartX=-1000 StartY=188 StartZ=0 EndX=-1000 EndY=168 EndZ=0
    g22: LineSegment StartX=-1000 StartY=168 StartZ=0 EndX=-1004 EndY=168 EndZ=0
    g23: LineSegment StartX=-1004 StartY=168 StartZ=0 EndX=-1004 EndY=188 EndZ=0
    g24: LineSegment StartX=-1004 StartY=228 StartZ=0 EndX=-1000 EndY=228 EndZ=0
    g25: LineSegment StartX=-1000 StartY=228 StartZ=0 EndX=-1000 EndY=208 EndZ=0
    g26: LineSegment StartX=-1000 StartY=208 StartZ=0 EndX=-1004 EndY=208 EndZ=0
    g27: LineSegment StartX=-1004 StartY=208 StartZ=0 EndX=-1004 EndY=228 EndZ=0
    g28: LineSegment StartX=-1004 StartY=268 StartZ=0 EndX=-1000 EndY=268 EndZ=0
    g29: LineSegment StartX=-1000 StartY=268 StartZ=0 EndX=-1000 EndY=248 EndZ=0
    g30: LineSegment StartX=-1000 StartY=248 StartZ=0 EndX=-1004 EndY=248 EndZ=0
    g31: LineSegment StartX=-1004 StartY=248 StartZ=0 EndX=-1004 EndY=268 EndZ=0
    g32: LineSegment StartX=-1004 StartY=308 StartZ=0 EndX=-1000 EndY=308 EndZ=0
    g33: LineSegment StartX=-1000 StartY=308 StartZ=0 EndX=-1000 EndY=288 EndZ=0
    g34: LineSegment StartX=-1000 StartY=288 StartZ=0 EndX=-1004 EndY=288 EndZ=0
    g35: LineSegment StartX=-1004 StartY=288 StartZ=0 EndX=-1004 EndY=308 EndZ=0
    g36: LineSegment StartX=-1004 StartY=348 StartZ=0 EndX=-1000 EndY=348 EndZ=0
    g37: LineSegment StartX=-1000 StartY=348 StartZ=0 EndX=-1000 EndY=328 EndZ=0
    g38: LineSegment StartX=-1000 StartY=328 StartZ=0 EndX=-1004 EndY=328 EndZ=0
    g39: LineSegment StartX=-1004 StartY=328 StartZ=0 EndX=-1004 EndY=348 EndZ=0
    g40: LineSegment StartX=-1004 StartY=388 StartZ=0 EndX=-1000 EndY=388 EndZ=0
    g41: LineSegment StartX=-1000 StartY=388 StartZ=0 EndX=-1000 EndY=368 EndZ=0
    g42: LineSegment StartX=-1000 StartY=368 StartZ=0 EndX=-1004 EndY=368 EndZ=0
    g43: LineSegment StartX=-1004 StartY=368 StartZ=0 EndX=-1004 EndY=388 EndZ=0
    g44: LineSegment StartX=-1004 StartY=428 StartZ=0 EndX=-1000 EndY=428 EndZ=0
    g45: LineSegment StartX=-1000 StartY=428 StartZ=0 EndX=-1000 EndY=408 EndZ=0
    g46: LineSegment StartX=-1000 StartY=408 StartZ=0 EndX=-1004 EndY=408 EndZ=0
    g47: LineSegment StartX=-1004 StartY=408 StartZ=0 EndX=-1004 EndY=428 EndZ=0
    g48: LineSegment StartX=-1004 StartY=468 StartZ=0 EndX=-1000 EndY=468 EndZ=0
    g49: LineSegment StartX=-1000 StartY=468 StartZ=0 EndX=-1000 EndY=448 EndZ=0
    g50: LineSegment StartX=-1000 StartY=448 StartZ=0 EndX=-1004 EndY=448 EndZ=0
    g51: LineSegment StartX=-1004 StartY=448 StartZ=0 EndX=-1004 EndY=468 EndZ=0
    g52: LineSegment StartX=-1004 StartY=508 StartZ=0 EndX=-1000 EndY=508 EndZ=0
    g53: LineSegment StartX=-1000 StartY=508 StartZ=0 EndX=-1000 EndY=488 EndZ=0
    g54: LineSegment StartX=-1000 StartY=488 StartZ=0 EndX=-1004 EndY=488 EndZ=0
    g55: LineSegment StartX=-1004 StartY=488 StartZ=0 EndX=-1004 EndY=508 EndZ=0
    g56: LineSegment StartX=-1004 StartY=548 StartZ=0 EndX=-1000 EndY=548 EndZ=0
    g57: LineSegment StartX=-1000 StartY=548 StartZ=0 EndX=-1000 EndY=528 EndZ=0
    g58: LineSegment StartX=-1000 StartY=528 StartZ=0 EndX=-1004 EndY=528 EndZ=0
    g59: LineSegment StartX=-1004 StartY=528 StartZ=0 EndX=-1004 EndY=548 EndZ=0
    g60: LineSegment StartX=-1004 StartY=575 StartZ=0 EndX=-1000 EndY=575 EndZ=0
    g61: LineSegment StartX=-1000 StartY=575 StartZ=0 EndX=-1000 EndY=568 EndZ=0
    g62: LineSegment StartX=-1000 StartY=568 StartZ=0 EndX=-1004 EndY=568 EndZ=0
    g63: LineSegment StartX=-1004 StartY=568 StartZ=0 EndX=-1004 EndY=575 EndZ=0
    g64: LineSegment StartX=1000 StartY=-12 StartZ=0 EndX=1004 EndY=-12 EndZ=0
    g65: LineSegment StartX=1004 StartY=-12 StartZ=0 EndX=1004 EndY=-32 EndZ=0
    g66: LineSegment StartX=1004 StartY=-32 StartZ=0 EndX=1000 EndY=-32 EndZ=0
    g67: LineSegment StartX=1000 StartY=-32 StartZ=0 EndX=1000 EndY=-12 EndZ=0
    g68: LineSegment StartX=1000 StartY=28 StartZ=0 EndX=1004 EndY=28 EndZ=0
    g69: LineSegment StartX=1004 StartY=28 StartZ=0 EndX=1004 EndY=8 EndZ=0
    g70: LineSegment StartX=1004 StartY=8 StartZ=0 EndX=1000 EndY=8 EndZ=0
    g71: LineSegment StartX=1000 StartY=8 StartZ=0 EndX=1000 EndY=28 EndZ=0
    g72: LineSegment StartX=1000 StartY=68 StartZ=0 EndX=1004 EndY=68 EndZ=0
    g73: LineSegment StartX=1004 StartY=68 StartZ=0 EndX=1004 EndY=48 EndZ=0
    g74: LineSegment StartX=1004 StartY=48 StartZ=0 EndX=1000 EndY=48 EndZ=0
    g75: LineSegment StartX=1000 StartY=48 StartZ=0 EndX=1000 EndY=68 EndZ=0
    g76: LineSegment StartX=1000 StartY=108 StartZ=0 EndX=1004 EndY=108 EndZ=0
    g77: LineSegment StartX=1004 StartY=108 StartZ=0 EndX=1004 EndY=88 EndZ=0
    g78: LineSegment StartX=1004 StartY=88 StartZ=0 EndX=1000 EndY=88 EndZ=0
    g79: LineSegment StartX=1000 StartY=88 StartZ=0 EndX=1000 EndY=108 EndZ=0
    g80: LineSegment StartX=1000 StartY=148 StartZ=0 EndX=1004 EndY=148 EndZ=0
    g81: LineSegment StartX=1004 StartY=148 StartZ=0 EndX=1004 EndY=128 EndZ=0
    g82: LineSegment StartX=1004 StartY=128 StartZ=0 EndX=1000 EndY=128 EndZ=0
    g83: LineSegment StartX=1000 StartY=128 StartZ=0 EndX=1000 EndY=148 EndZ=0
    g84: LineSegment StartX=1000 StartY=188 StartZ=0 EndX=1004 EndY=188 EndZ=0
    g85: LineSegment StartX=1004 StartY=188 StartZ=0 EndX=1004 EndY=168 EndZ=0
    g86: LineSegment StartX=1004 StartY=168 StartZ=0 EndX=1000 EndY=168 EndZ=0
    g87: LineSegment StartX=1000 StartY=168 StartZ=0 EndX=1000 EndY=188 EndZ=0
    g88: LineSegment StartX=1000 StartY=228 StartZ=0 EndX=1004 EndY=228 EndZ=0
    g89: LineSegment StartX=1004 StartY=228 StartZ=0 EndX=1004 EndY=208 EndZ=0
    g90: LineSegment StartX=1004 StartY=208 StartZ=0 EndX=1000 EndY=208 EndZ=0
    g91: LineSegment StartX=1000 StartY=208 StartZ=0 EndX=1000 EndY=228 EndZ=0
    g92: LineSegment StartX=1000 StartY=268 StartZ=0 EndX=1004 EndY=268 EndZ=0
    g93: LineSegment StartX=1004 StartY=268 StartZ=0 EndX=1004 EndY=248 EndZ=0
    g94: LineSegment StartX=1004 StartY=248 StartZ=0 EndX=1000 EndY=248 EndZ=0
    g95: LineSegment StartX=1000 StartY=248 StartZ=0 EndX=1000 EndY=268 EndZ=0
    g96: LineSegment StartX=1000 StartY=308 StartZ=0 EndX=1004 EndY=308 EndZ=0
    g97: LineSegment StartX=1004 StartY=308 StartZ=0 EndX=1004 EndY=288 EndZ=0
    g98: LineSegment StartX=1004 StartY=288 StartZ=0 EndX=1000 EndY=288 EndZ=0
    g99: LineSegment StartX=1000 StartY=288 StartZ=0 EndX=1000 EndY=308 EndZ=0
    g100: LineSegment StartX=1000 StartY=348 StartZ=0 EndX=1004 EndY=348 EndZ=0
    g101: LineSegment StartX=1004 StartY=348 StartZ=0 EndX=1004 EndY=328 EndZ=0
    g102: LineSegment StartX=1004 StartY=328 StartZ=0 EndX=1000 EndY=328 EndZ=0
    g103: LineSegment StartX=1000 StartY=328 StartZ=0 EndX=1000 EndY=348 EndZ=0
    g104: LineSegment StartX=1000 StartY=388 StartZ=0 EndX=1004 EndY=388 EndZ=0
    g105: LineSegment StartX=1004 StartY=388 StartZ=0 EndX=1004 EndY=368 EndZ=0
    g106: LineSegment StartX=1004 StartY=368 StartZ=0 EndX=1000 EndY=368 EndZ=0
    g107: LineSegment StartX=1000 StartY=368 StartZ=0 EndX=1000 EndY=388 EndZ=0
    g108: LineSegment StartX=1000 StartY=428 StartZ=0 EndX=1004 EndY=428 EndZ=0
    g109: LineSegment StartX=1004 StartY=428 StartZ=0 EndX=1004 EndY=408 EndZ=0
    g110: LineSegment StartX=1004 StartY=408 StartZ=0 EndX=1000 EndY=408 EndZ=0
    g111: LineSegment StartX=1000 StartY=408 StartZ=0 EndX=1000 EndY=428 EndZ=0
    g112: LineSegment StartX=1000 StartY=468 StartZ=0 EndX=1004 EndY=468 EndZ=0
    g113: LineSegment StartX=1004 StartY=468 StartZ=0 EndX=1004 EndY=448 EndZ=0
    g114: LineSegment StartX=1004 StartY=448 StartZ=0 EndX=1000 EndY=448 EndZ=0
    g115: LineSegment StartX=1000 StartY=448 StartZ=0 EndX=1000 EndY=468 EndZ=0
    g116: LineSegment StartX=1000 StartY=508 StartZ=0 EndX=1004 EndY=508 EndZ=0
    g117: LineSegment StartX=1004 StartY=508 StartZ=0 EndX=1004 EndY=488 EndZ=0
    g118: LineSegment StartX=1004 StartY=488 StartZ=0 EndX=1000 EndY=488 EndZ=0
    g119: LineSegment StartX=1000 StartY=488 StartZ=0 EndX=1000 EndY=508 EndZ=0
    g120: LineSegment StartX=1000 StartY=548 StartZ=0 EndX=1004 EndY=548 EndZ=0
    g121: LineSegment StartX=1004 StartY=548 StartZ=0 EndX=1004 EndY=528 EndZ=0
    g122: LineSegment StartX=1004 StartY=528 StartZ=0 EndX=1000 EndY=528 EndZ=0
    g123: LineSegment StartX=1000 StartY=528 StartZ=0 EndX=1000 EndY=548 EndZ=0
    g124: LineSegment StartX=1000 StartY=575 StartZ=0 EndX=1004 EndY=575 EndZ=0
    g125: LineSegment StartX=1004 StartY=575 StartZ=0 EndX=1004 EndY=568 EndZ=0
    g126: LineSegment StartX=1004 StartY=568 StartZ=0 EndX=1000 EndY=568 EndZ=0
    g127: LineSegment StartX=1000 StartY=568 StartZ=0 EndX=1000 EndY=575 EndZ=0
  constraints (384):
    c: Coincident(g0,g1)
    c: Coincident(g1,g2)
    c: Coincident(g2,g3)
    c: Coincident(g3,g0)
    c: Horizontal(g0)
    c: Horizontal(g2)
    c: Vertical(g1)
    c: Vertical(g3)
    c: Coincident(g4,g5)
    c: Coincident(g5,g6)
    c: Coincident(g6,g7)
    c: Coincident(g7,g4)
    c: Horizontal(g4)
    c: Horizontal(g6)
    c: Vertical(g5)
    c: Vertical(g7)
    c: Coincident(g8,g9)
    c: Coincident(g9,g10)
    c: Coincident(g10,g11)
    c: Coincident(g11,g8)
    c: Horizontal(g8)
    c: Horizontal(g10)
    c: Vertical(g9)
    c: Vertical(g11)
    c: Coincident(g12,g13)
    c: Coincident(g13,g14)
    c: Coincident(g14,g15)
    c: Coincident(g15,g12)
    c: Horizontal(g12)
    c: Horizontal(g14)
    c: Vertical(g13)
    c: Vertical(g15)
    c: Vertical(g0,g6)
    c: Vertical(g4,g10)
    c: Vertical(g8,g14)
    c: Vertical(g13,g8)
    c: Vertical(g9,g4)
    c: Vertical(g5,g0)
    c: DistanceY(g2,g0) = 20
    c: DistanceY(g0,g6) = 20
    c: DistanceY(g6,g4) = 20
    c: DistanceY(g4,g10) = 20
    c: DistanceY(g10,g8) = 20
    c: DistanceY(g8,g14) = 20
    c: DistanceY(g14,g12) = 20
    c: DistanceX(g2,g1) = 4
    c: Coincident(g16,g17)
    c: Coincident(g17,g18)
    c: Coincident(g18,g19)
    c: Coincident(g19,g16)
    c: Horizontal(g16)
    c: Horizontal(g18)
    c: Vertical(g17)
    c: Vertical(g19)
    c: Coincident(g20,g21)
    c: Coincident(g21,g22)
    c: Coincident(g22,g23)
    c: Coincident(g23,g20)
    c: Horizontal(g20)
    c: Horizontal(g22)
    c: Vertical(g21)
    c: Vertical(g23)
    c: Coincident(g24,g25)
    c: Coincident(g25,g26)
    c: Coincident(g26,g27)
    c: Coincident(g27,g24)
    c: Horizontal(g24)
    c: Horizontal(g26)
    c: Vertical(g25)
    c: Vertical(g27)
    c: Vertical(g16,g22)
    c: Vertical(g20,g26)
    c: Vertical(g25,g20)
    c: Vertical(g21,g16)
    c: DistanceY(g18,g16) = 20
    c: DistanceY(g16,g22) = 20
    c: DistanceY(g22,g20) = 20
    c: DistanceY(g20,g26) = 20
    c: DistanceY(g26,g24) = 20
    c: Vertical(g18,g12)
    c: Vertical(g12,g17)
    c: DistanceY(g12,g18) = 20
    c: Coincident(g28,g29)
    c: Coincident(g29,g30)
    c: Coincident(g30,g31)
    c: Coincident(g31,g28)
    c: Horizontal(g28)
    c: Horizontal(g30)
    c: Vertical(g29)
    c: Vertical(g31)
    c: Coincident(g32,g33)
    c: Coincident(g33,g34)
    c: Coincident(g34,g35)
    c: Coincident(g35,g32)
    c: Horizontal(g32)
    c: Horizontal(g34)
    c: Vertical(g33)
    c: Vertical(g35)
    c: Coincident(g36,g37)
    c: Coincident(g37,g38)
    c: Coincident(g38,g39)
    c: Coincident(g39,g36)
    c: Horizontal(g36)
    c: Horizontal(g38)
    c: Vertical(g37)
    c: Vertical(g39)
    c: Vertical(g28,g34)
    c: Vertical(g32,g38)
    c: Vertical(g37,g32)
    c: Vertical(g33,g28)
    c: DistanceY(g30,g28) = 20
    c: DistanceY(g28,g34) = 20
    c: DistanceY(g34,g32) = 20
    c: DistanceY(g32,g38) = 20
    c: DistanceY(g38,g36) = 20
    c: Coincident(g40,g41)
    c: Coincident(g41,g42)
    c: Coincident(g42,g43)
    c: Coincident(g43,g40)
    c: Horizontal(g40)
    c: Horizontal(g42)
    c: Vertical(g41)
    c: Vertical(g43)
    c: Coincident(g44,g45)
    c: Coincident(g45,g46)
    c: Coincident(g46,g47)
    c: Coincident(g47,g44)
    c: Horizontal(g44)
    c: Horizontal(g46)
    c: Vertical(g45)
    c: Vertical(g47)
    c: Coincident(g48,g49)
    c: Coincident(g49,g50)
    c: Coincident(g50,g51)
    c: Coincident(g51,g48)
    c: Horizontal(g48)
    c: Horizontal(g50)
    c: Vertical(g49)
    c: Vertical(g51)
    c: Vertical(g40,g46)
    c: Vertical(g44,g50)
    c: Vertical(g49,g44)
    c: Vertical(g45,g40)
    c: DistanceY(g42,g40) = 20
    c: DistanceY(g40,g46) = 20
    c: DistanceY(g46,g44) = 20
    c: DistanceY(g44,g50) = 20
    c: DistanceY(g50,g48) = 20
    c: Vertical(g42,g36)
    c: Vertical(g36,g41)
    c: DistanceY(g36,g42) = 20
    c: Vertical(g30,g24)
    c: Vertical(g29,g24)
    c: DistanceY(g24,g30) = 20
    c: Vertical(g-3,g2)
    c: DistanceY(g-3,g2) = 20
    c: Coincident(g52,g53)
    c: Coincident(g53,g54)
    c: Coincident(g54,g55)
    c: Coincident(g55,g52)
    c: Horizontal(g52)
    c: Horizontal(g54)
    c: Vertical(g53)
    c: Vertical(g55)
    c: Coincident(g56,g57)
    c: Coincident(g57,g58)
    c: Coincident(g58,g59)
    c: Coincident(g59,g56)
    c: Horizontal(g56)
    c: Horizontal(g58)
    c: Vertical(g57)
    c: Vertical(g59)
    c: Coincident(g60,g61)
    c: Coincident(g61,g62)
    c: Coincident(g62,g63)
    c: Coincident(g63,g60)
    c: Horizontal(g60)
    c: Horizontal(g62)
    c: Vertical(g61)
    c: Vertical(g63)
    c: Vertical(g52,g58)
    c: Vertical(g56,g62)
    c: Vertical(g61,g56)
    c: Vertical(g57,g52)
    c: DistanceY(g54,g52) = 20
    c: DistanceY(g52,g58) = 20
    c: DistanceY(g58,g56) = 20
    c: DistanceY(g56,g62) = 20
    c: DistanceY(g62,g60) = 7
    c: Vertical(g54,g48)
    c: Vertical(g53,g48)
    c: DistanceY(g48,g54) = 20
    c: Coincident(g64,g65)
    c: Coincident(g65,g66)
    c: Coincident(g66,g67)
    c: Coincident(g67,g64)
    c: Horizontal(g64)
    c: Horizontal(g66)
    c: Vertical(g65)
    c: Vertical(g67)
    c: Coincident(g68,g69)
    c: Coincident(g69,g70)
    c: Coincident(g70,g71)
    c: Coincident(g71,g68)
    c: Horizontal(g68)
    c: Horizontal(g70)
    c: Vertical(g69)
    c: Vertical(g71)
    c: Coincident(g72,g73)
    c: Coincident(g73,g74)
    c: Coincident(g74,g75)
    c: Coincident(g75,g72)
    c: Horizontal(g72)
    c: Horizontal(g74)
    c: Vertical(g73)
    c: Vertical(g75)
    c: Coincident(g76,g77)
    c: Coincident(g77,g78)
    c: Coincident(g78,g79)
    c: Coincident(g79,g76)
    c: Horizontal(g76)
    c: Horizontal(g78)
    c: Vertical(g77)
    c: Vertical(g79)
    c: Vertical(g64,g70)
    c: Vertical(g68,g74)
    c: Vertical(g72,g78)
    c: Vertical(g77,g72)
    c: Vertical(g73,g68)
    c: Vertical(g69,g64)
    c: DistanceY(g66,g64) = 20
    c: DistanceY(g64,g70) = 20
    c: DistanceY(g70,g68) = 20
    c: DistanceY(g68,g74) = 20
    c: DistanceY(g74,g72) = 20
    c: DistanceY(g72,g78) = 20
    c: DistanceY(g78,g76) = 20
    c: DistanceX(g66,g65) = 4
    c: Coincident(g80,g81)
    c: Coincident(g81,g82)
    c: Coincident(g82,g83)
    c: Coincident(g83,g80)
    c: Horizontal(g80)
    c: Horizontal(g82)
    c: Vertical(g81)
    c: Vertical(g83)
    c: Coincident(g84,g85)
    c: Coincident(g85,g86)
    c: Coincident(g86,g87)
    c: Coincident(g87,g84)
    c: Horizontal(g84)
    c: Horizontal(g86)
    c: Vertical(g85)
    c: Vertical(g87)
    c: Coincident(g88,g89)
    c: Coincident(g89,g90)
    c: Coincident(g90,g91)
    c: Coincident(g91,g88)
    c: Horizontal(g88)
    c: Horizontal(g90)
    c: Vertical(g89)
    c: Vertical(g91)
    c: Vertical(g80,g86)
    c: Vertical(g84,g90)
    c: Vertical(g89,g84)
    c: Vertical(g85,g80)
    c: DistanceY(g82,g80) = 20
    c: DistanceY(g80,g86) = 20
    c: DistanceY(g86,g84) = 20
    c: DistanceY(g84,g90) = 20
    c: DistanceY(g90,g88) = 20
    c: Vertical(g82,g76)
    c: Vertical(g76,g81)
    c: DistanceY(g76,g82) = 20
    c: Coincident(g92,g93)
    c: Coincident(g93,g94)
    c: Coincident(g94,g95)
    c: Coincident(g95,g92)
    c: Horizontal(g92)
    c: Horizontal(g94)
    c: Vertical(g93)
    c: Vertical(g95)
    c: Coincident(g96,g97)
    c: Coincident(g97,g98)
    c: Coincident(g98,g99)
    c: Coincident(g99,g96)
    c: Horizontal(g96)
    c: Horizontal(g98)
    c: Vertical(g97)
    c: Vertical(g99)
    c: Coincident(g100,g101)
    c: Coincident(g101,g102)
    c: Coincident(g102,g103)
    c: Coincident(g103,g100)
    c: Horizontal(g100)
    c: Horizontal(g102)
    c: Vertical(g101)
    c: Vertical(g103)
    c: Vertical(g92,g98)
    c: Vertical(g96,g102)
    c: Vertical(g101,g96)
    c: Vertical(g97,g92)
    c: DistanceY(g94,g92) = 20
    c: DistanceY(g92,g98) = 20
    c: DistanceY(g98,g96) = 20
    c: DistanceY(g96,g102) = 20
    c: DistanceY(g102,g100) = 20
    c: Coincident(g104,g105)
    c: Coincident(g105,g106)
    c: Coincident(g106,g107)
    c: Coincident(g107,g104)
    c: Horizontal(g104)
    c: Horizontal(g106)
    c: Vertical(g105)
    c: Vertical(g107)
    c: Coincident(g108,g109)
    c: Coincident(g109,g110)
    c: Coincident(g110,g111)
    c: Coincident(g111,g108)
    c: Horizontal(g108)
    c: Horizontal(g110)
    c: Vertical(g109)
    c: Vertical(g111)
    c: Coincident(g112,g113)
    c: Coincident(g113,g114)
    c: Coincident(g114,g115)
    c: Coincident(g115,g112)
    c: Horizontal(g112)
    c: Horizontal(g114)
    c: Vertical(g113)
    c: Vertical(g115)
    c: Vertical(g104,g110)
    c: Vertical(g108,g114)
    c: Vertical(g113,g108)
    c: Vertical(g109,g104)
    c: DistanceY(g106,g104) = 20
    c: DistanceY(g104,g110) = 20
    c: DistanceY(g110,g108) = 20
    c: DistanceY(g108,g114) = 20
    c: DistanceY(g114,g112) = 20
    c: Vertical(g106,g100)
    c: Vertical(g100,g105)
    c: DistanceY(g100,g106) = 20
    c: Vertical(g94,g88)
    c: Vertical(g93,g88)
    c: DistanceY(g88,g94) = 20
    c: Coincident(g116,g117)
    c: Coincident(g117,g118)
    c: Coincident(g118,g119)
    c: Coincident(g119,g116)
    c: Horizontal(g116)
    c: Horizontal(g118)
    c: Vertical(g117)
    c: Vertical(g119)
    c: Coincident(g120,g121)
    c: Coincident(g121,g122)
    c: Coincident(g122,g123)
    c: Coincident(g123,g120)
    c: Horizontal(g120)
    c: Horizontal(g122)
    c: Vertical(g121)
    c: Vertical(g123)
    c: Coincident(g124,g125)
    c: Coincident(g125,g126)
    c: Coincident(g126,g127)
    c: Coincident(g127,g124)
    c: Horizontal(g124)
    c: Horizontal(g126)
    c: Vertical(g125)
    c: Vertical(g127)
    c: Vertical(g116,g122)
    c: Vertical(g120,g126)
    c: Vertical(g125,g120)
    c: Vertical(g121,g116)
    c: DistanceY(g118,g116) = 20
    c: DistanceY(g116,g122) = 20
    c: DistanceY(g122,g120) = 20
    c: DistanceY(g120,g126) = 20
    c: DistanceY(g126,g124) = 7
    c: Vertical(g118,g112)
    c: Vertical(g117,g112)
    c: DistanceY(g112,g118) = 20
    c: Vertical(g-5,g65)
    c: DistanceY(g-5,g65) = 20
FEATURE [PartDesign::Pocket] Pocket010
  BaseFeature = -> Pad011
  Length = 4
  Length2 = 5
  Placement = pos=(0,0,0) rot=(1,0,0;1.5708rad)
  Profile = -> Sketch025
  Type = 0
FEATURE [PartDesign::Body] Body011  label="Bakkant-Yttre"
  Group = -> [Sketch024,Pad011,Sketch025,Pocket010]
  Origin = -> Origin011
  Placement = pos=(0,604,0) rot=(0,0,1;0rad)
  Tip = -> Pocket010
FEATURE [Sketcher::SketchObject] Sketch026
  FullyConstrained = true
  MapMode = 5
  Support = -> [XY_Plane012]
  sketch-geometry (5):
    g0: LineSegment StartX=-1000 StartY=-600 StartZ=0 EndX=-1000 EndY=600 EndZ=0
    g1: LineSegment StartX=-1000 StartY=600 StartZ=0 EndX=1000 EndY=600 EndZ=0
    g2: LineSegment StartX=1000 StartY=600 StartZ=0 EndX=1000 EndY=-600 EndZ=0
    g3: LineSegment StartX=1000 StartY=-600 StartZ=0 EndX=-1000 EndY=-600 EndZ=0
    g4: GeomPoint X=0 Y=0 Z=0
  constraints (12):
    c: Coincident(g0,g1)
    c: Coincident(g1,g2)
    c: Coincident(g2,g3)
    c: Coincident(g3,g0)
    c: Horizontal(g1)
    c: Horizontal(g3)
    c: Vertical(g0)
    c: Vertical(g2)
    c: Symmetric(g1,g0,g4)
    c: Coincident(g4,g-1)
    c: DistanceX(g0,g2) = 2000
    c: DistanceY(g0,g0) = 1200
FEATURE [PartDesign::Pad] Pad012
  Direction = (0,0,1)
  Length = 20
  Length2 = 10
  Profile = -> Sketch026
  Type = 0
FEATURE [PartDesign::Body] Body012  label="Cellplast-topp"
  Group = -> [Sketch026,Pad012]
  Origin = -> Origin012
  Placement = pos=(0,0,55) rot=(0,0,1;0rad)
  Tip = -> Pad012
FEATURE [Sketcher::SketchObject] Sketch027
  FullyConstrained = true
  MapMode = 5
  Placement = pos=(0,0,0) rot=(0.57735,0.57735,0.57735;2.0944rad)
  Support = -> [YZ_Plane013]
  sketch-geometry (5):
    g0: LineSegment StartX=-600 StartY=-50 StartZ=0 EndX=-600 EndY=50 EndZ=0
    g1: LineSegment StartX=-600 StartY=50 StartZ=0 EndX=600 EndY=50 EndZ=0
    g2: LineSegment StartX=600 StartY=50 StartZ=0 EndX=600 EndY=-50 EndZ=0
    g3: LineSegment StartX=600 StartY=-50 StartZ=0 EndX=-600 EndY=-50 EndZ=0
    g4: GeomPoint X=0 Y=0 Z=0
  constraints (12):
    c: Coincident(g0,g1)
    c: Coincident(g1,g2)
    c: Coincident(g2,g3)
    c: Coincident(g3,g0)
    c: Horizontal(g1)
    c: Horizontal(g3)
    c: Vertical(g0)
    c: Vertical(g2)
    c: Symmetric(g1,g0,g4)
    c: Coincident(g4,g-1)
    c: DistanceX(g0,g2) = 1200
    c: DistanceY(g0,g0) = 100
FEATURE [PartDesign::Pad] Pad013
  Direction = (1,-2e-16,3e-16)
  Length = 4
  Length2 = 10
  Placement = pos=(0,0,0) rot=(0.57735,0.57735,0.57735;2.0944rad)
  Profile = -> Sketch027
  Type = 0
FEATURE [Sketcher::SketchObject] Sketch028
  ExternalGeometry = -> [Pad013]
  FullyConstrained = false
  MapMode = 5
  Placement = pos=(4,-9e-16,9e-16) rot=(0.57735,0.57735,0.57735;2.0944rad)
  Support = -> [Pad013]
  sketch-geometry (40):
    g0: LineSegment StartX=-600 StartY=-10 StartZ=0 EndX=-596 EndY=-10 EndZ=0
    g1: LineSegment StartX=-596 StartY=-10 StartZ=0 EndX=-596 EndY=-30 EndZ=0
    g2: LineSegment StartX=-596 StartY=-30 StartZ=0 EndX=-600 EndY=-30 EndZ=0
    g3: LineSegment StartX=-600 StartY=-30 StartZ=0 EndX=-600 EndY=-10 EndZ=0
    g4: LineSegment StartX=-600 StartY=30 StartZ=0 EndX=-596 EndY=30 EndZ=0
    g5: LineSegment StartX=-596 StartY=30 StartZ=0 EndX=-596 EndY=10 EndZ=0
    g6: LineSegment StartX=-596 StartY=10 StartZ=0 EndX=-600 EndY=10 EndZ=0
    g7: LineSegment StartX=-600 StartY=10 StartZ=0 EndX=-600 EndY=30 EndZ=0
    g8: LineSegment StartX=596 StartY=-10 StartZ=0 EndX=600 EndY=-10 EndZ=0
    g9: LineSegment StartX=600 StartY=-10 StartZ=0 EndX=600 EndY=-30 EndZ=0
    g10: LineSegment StartX=600 StartY=-30 StartZ=0 EndX=596 EndY=-30 EndZ=0
    g11: LineSegment StartX=596 StartY=-30 StartZ=0 EndX=596 EndY=-10 EndZ=0
    g12: LineSegment StartX=596 StartY=30 StartZ=0 EndX=600 EndY=30 EndZ=0
    g13: LineSegment StartX=600 StartY=30 StartZ=0 EndX=600 EndY=10 EndZ=0
    g14: LineSegment StartX=600 StartY=10 StartZ=0 EndX=596 EndY=10 EndZ=0
    g15: LineSegment StartX=596 StartY=10 StartZ=0 EndX=596 EndY=30 EndZ=0
    g16: GeomPoint X=-300 Y=0 Z=0
    g17: GeomPoint X=-2.222e-13 Y=0 Z=0
    g18: GeomPoint X=300 Y=0 Z=0
    g19: GeomPoint X=600 Y=-50.3976 Z=0
    g20: ArcOfCircle CenterX=-322.5 CenterY=0 CenterZ=0 NormalX=0 NormalY=0 NormalZ=1 AngleXU=0 Radius=30 StartAngle=1.5708 EndAngle=4.71239
    g21: ArcOfCircle CenterX=-277.5 CenterY=-1.4e-15 CenterZ=0 NormalX=0 NormalY=0 NormalZ=1 AngleXU=0 Radius=30 StartAngle=4.71239 EndAngle=7.85398
    g22: LineSegment StartX=-322.5 StartY=-30 StartZ=0 EndX=-277.5 EndY=-30 EndZ=0
    g23: LineSegment StartX=-277.5 StartY=30 StartZ=0 EndX=-322.5 EndY=30 EndZ=0
    g24: ArcOfCircle CenterX=-22.5 CenterY=-1.4e-15 CenterZ=0 NormalX=0 NormalY=0 NormalZ=1 AngleXU=0 Radius=30 StartAngle=1.5708 EndAngle=4.71239
    g25: ArcOfCircle CenterX=22.5 CenterY=-5e-16 CenterZ=0 NormalX=0 NormalY=0 NormalZ=1 AngleXU=0 Radius=30 StartAngle=4.71239 EndAngle=7.85398
    g26: LineSegment StartX=-22.5 StartY=-30 StartZ=0 EndX=22.5 EndY=-30 EndZ=0
    g27: LineSegment StartX=22.5 StartY=30 StartZ=0 EndX=-22.5 EndY=30 EndZ=0
    g28: ArcOfCircle CenterX=277.5 CenterY=-5e-16 CenterZ=0 NormalX=0 NormalY=0 NormalZ=1 AngleXU=0 Radius=30 StartAngle=1.5708 EndAngle=4.71239
    g29: ArcOfCircle CenterX=322.5 CenterY=-1e-15 CenterZ=0 NormalX=0 NormalY=0 NormalZ=1 AngleXU=0 Radius=30 StartAngle=4.71239 EndAngle=7.85398
    g30: LineSegment StartX=277.5 StartY=-30 StartZ=0 EndX=322.5 EndY=-30 EndZ=0
    g31: LineSegment StartX=322.5 StartY=30 StartZ=0 EndX=277.5 EndY=30 EndZ=0
    g32: Circle CenterX=-525 CenterY=0 CenterZ=0 NormalX=0 NormalY=0 NormalZ=1 AngleXU=0 Radius=25
    g33: Circle CenterX=-194.17 CenterY=-1.4e-15 CenterZ=0 NormalX=0 NormalY=0 NormalZ=1 AngleXU=0 Radius=25
    g34: Circle CenterX=105.83 CenterY=-5e-16 CenterZ=0 NormalX=0 NormalY=0 NormalZ=1 AngleXU=0 Radius=25
    g35: Circle CenterX=525 CenterY=-1e-15 CenterZ=0 NormalX=0 NormalY=0 NormalZ=1 AngleXU=0 Radius=25
    g36: Circle CenterX=-425 CenterY=0 CenterZ=0 NormalX=0 NormalY=0 NormalZ=1 AngleXU=0 Radius=25
    g37: Circle CenterX=-110.84 CenterY=0 CenterZ=0 NormalX=0 NormalY=0 NormalZ=1 AngleXU=0 Radius=25
    g38: Circle CenterX=189.16 CenterY=0 CenterZ=0 NormalX=0 NormalY=0 NormalZ=1 AngleXU=0 Radius=25
    g39: Circle CenterX=425 CenterY=0 CenterZ=0 NormalX=0 NormalY=0 NormalZ=1 AngleXU=0 Radius=25
  constraints (109):
    c: Coincident(g0,g1)
    c: Coincident(g1,g2)
    c: Coincident(g2,g3)
    c: Coincident(g3,g0)
    c: Horizontal(g0)
    c: Horizontal(g2)
    c: Vertical(g1)
    c: Vertical(g3)
    c: Coincident(g4,g5)
    c: Coincident(g5,g6)
    c: Coincident(g6,g7)
    c: Coincident(g7,g4)
    c: Horizontal(g4)
    c: Horizontal(g6)
    c: Vertical(g5)
    c: Vertical(g7)
    c: Vertical(g-4,g0)
    c: Vertical(g0,g6)
    c: Vertical(g5,g0)
    c: DistanceY(g2,g0) = 20
    c: DistanceY(g0,g6) = 20
    c: DistanceY(g6,g4) = 20
    c: DistanceX(g2,g1) = 4
    c: Coincident(g8,g9)
    c: Coincident(g9,g10)
    c: Coincident(g10,g11)
    c: Coincident(g11,g8)
    c: Horizontal(g8)
    c: Horizontal(g10)
    c: Vertical(g9)
    c: Vertical(g11)
    c: Coincident(g12,g13)
    c: Coincident(g13,g14)
    c: Coincident(g14,g15)
    c: Coincident(g15,g12)
    c: Horizontal(g12)
    c: Horizontal(g14)
    c: Vertical(g13)
    c: Vertical(g15)
    c: Vertical(g8,g14)
    c: Vertical(g13,g8)
    c: DistanceY(g10,g8) = 20
    c: DistanceY(g8,g14) = 20
    c: DistanceY(g14,g12) = 20
    c: DistanceX(g10,g9) = 4
    c: Vertical(g-6,g9)
    c: DistanceY(g-4,g2) = 20
    c: Horizontal(g4,g12)
    c: PointOnObject(g16,g-1)
    c: DistanceX(g-3,g16) = 300
    c: PointOnObject(g17,g-1)
    c: DistanceX(g16,g17) = 300
    c: PointOnObject(g18,g-1)
    c: DistanceX(g17,g18) = 300
    c: DistanceX(g18,g19) = 300
    c: Tangent(g20,g22) = -1.5708
    c: Tangent(g22,g21) = -1.5708
    c: Tangent(g21,g23) = -1.5708
    c: Tangent(g23,g20) = -1.5708
    c: Equal(g20,g21)
    c: Horizontal(g22)
    c: DistanceY(g20,g20) = 60
    c: DistanceY(g16,g20) = 0
    c: DistanceX(g20,g21) = 45
    c: DistanceX(g20,g16) = 22.5
    c: Tangent(g24,g26) = -1.5708
    c: Tangent(g26,g25) = -1.5708
    c: Tangent(g25,g27) = -1.5708
    c: Tangent(g27,g24) = -1.5708
    c: Equal(g24,g25)
    c: Horizontal(g26)
    c: DistanceY(g24,g24) = 60
    c: DistanceX(g24,g25) = 45
    c: DistanceX(g24,g17) = 22.5
    c: Horizontal(g24,g21)
    c: Tangent(g28,g30) = -1.5708
    c: Tangent(g30,g29) = -1.5708
    c: Tangent(g29,g31) = -1.5708
    c: Tangent(g31,g28) = -1.5708
    c: Equal(g28,g29)
    c: Horizontal(g30)
    c: DistanceY(g28,g28) = 60
    c: DistanceX(g28,g29) = 45
    c: Horizontal(g25,g28)
    c: DistanceX(g28,g18) = 22.5
    c: Horizontal(g20,g32)
    c: Horizontal(g21,g33)
    c: Horizontal(g25,g34)
    c: Horizontal(g29,g35)
    c: Diameter(g32) = 50
    c: Equal(g32,g33)
    c: Equal(g33,g34)
    c: Equal(g34,g35)
    c: DistanceX(g-4,g32) = 75
    c: PointOnObject(g36,g-1)
    c: Equal(g32,g36)
    c: DistanceX(g32,g36) = 100
    c: DistanceX(g21,g33) = 83.33
    c: PointOnObject(g37,g-1)
    c: Equal(g33,g37)
    c: DistanceX(g33,g37) = 83.33
    c: DistanceX(g25,g34) = 83.33
    c: PointOnObject(g38,g-1)
    c: Equal(g34,g38)
    c: DistanceX(g34,g38) = 83.33
    c: DistanceX(g35,g19) = 75
    c: PointOnObject(g39,g-1)
    c: Equal(g35,g39)
    c: DistanceX(g39,g35) = 100
FEATURE [PartDesign::Pocket] Pocket011
  BaseFeature = -> Pad013
  Length = 4
  Length2 = 5
  Placement = pos=(0,0,0) rot=(0.57735,0.57735,0.57735;2.0944rad)
  Profile = -> Sketch028
  Type = 0
FEATURE [PartDesign::Body] Body013  label="KortSprygel-1"
  Group = -> [Sketch027,Pad013,Sketch028,Pocket011]
  Origin = -> Origin013
  Placement = pos=(-668.66,0,0) rot=(0,0,1;0rad)
  Tip = -> Pocket011
FEATURE [Sketcher::SketchObject] Sketch029
  FullyConstrained = true
  MapMode = 5
  Placement = pos=(0,0,0) rot=(0.57735,0.57735,0.57735;2.0944rad)
  Support = -> [YZ_Plane014]
  sketch-geometry (5):
    g0: LineSegment StartX=-600 StartY=-50 StartZ=0 EndX=-600 EndY=50 EndZ=0
    g1: LineSegment StartX=-600 StartY=50 StartZ=0 EndX=600 EndY=50 EndZ=0
    g2: LineSegment StartX=600 StartY=50 StartZ=0 EndX=600 EndY=-50 EndZ=0
    g3: LineSegment StartX=600 StartY=-50 StartZ=0 EndX=-600 EndY=-50 EndZ=0
    g4: GeomPoint X=0 Y=0 Z=0
  constraints (12):
    c: Coincident(g0,g1)
    c: Coincident(g1,g2)
    c: Coincident(g2,g3)
    c: Coincident(g3,g0)
    c: Horizontal(g1)
    c: Horizontal(g3)
    c: Vertical(g0)
    c: Vertical(g2)
    c: Symmetric(g1,g0,g4)
    c: Coincident(g4,g-1)
    c: DistanceX(g0,g2) = 1200
    c: DistanceY(g0,g0) = 100
FEATURE [PartDesign::Pad] Pad014
  Direction = (1,-2e-16,3e-16)
  Length = 4
  Length2 = 10
  Placement = pos=(0,0,0) rot=(0.57735,0.57735,0.57735;2.0944rad)
  Profile = -> Sketch029
  Type = 0
FEATURE [Sketcher::SketchObject] Sketch030
  ExternalGeometry = -> [Pad014]
  FullyConstrained = false
  MapMode = 5
  Placement = pos=(4,-9e-16,9e-16) rot=(0.57735,0.57735,0.57735;2.0944rad)
  Support = -> [Pad014]
  sketch-geometry (40):
    g0: LineSegment StartX=-600 StartY=-10 StartZ=0 EndX=-596 EndY=-10 EndZ=0
    g1: LineSegment StartX=-596 StartY=-10 StartZ=0 EndX=-596 EndY=-30 EndZ=0
    g2: LineSegment StartX=-596 StartY=-30 StartZ=0 EndX=-600 EndY=-30 EndZ=0
    g3: LineSegment StartX=-600 StartY=-30 StartZ=0 EndX=-600 EndY=-10 EndZ=0
    g4: LineSegment StartX=-600 StartY=30 StartZ=0 EndX=-596 EndY=30 EndZ=0
    g5: LineSegment StartX=-596 StartY=30 StartZ=0 EndX=-596 EndY=10 EndZ=0
    g6: LineSegment StartX=-596 StartY=10 StartZ=0 EndX=-600 EndY=10 EndZ=0
    g7: LineSegment StartX=-600 StartY=10 StartZ=0 EndX=-600 EndY=30 EndZ=0
    g8: LineSegment StartX=596 StartY=-10 StartZ=0 EndX=600 EndY=-10 EndZ=0
    g9: LineSegment StartX=600 StartY=-10 StartZ=0 EndX=600 EndY=-30 EndZ=0
    g10: LineSegment StartX=600 StartY=-30 StartZ=0 EndX=596 EndY=-30 EndZ=0
    g11: LineSegment StartX=596 StartY=-30 StartZ=0 EndX=596 EndY=-10 EndZ=0
    g12: LineSegment StartX=596 StartY=30 StartZ=0 EndX=600 EndY=30 EndZ=0
    g13: LineSegment StartX=600 StartY=30 StartZ=0 EndX=600 EndY=10 EndZ=0
    g14: LineSegment StartX=600 StartY=10 StartZ=0 EndX=596 EndY=10 EndZ=0
    g15: LineSegment StartX=596 StartY=10 StartZ=0 EndX=596 EndY=30 EndZ=0
    g16: GeomPoint X=-300 Y=0 Z=0
    g17: GeomPoint X=-2.222e-13 Y=0 Z=0
    g18: GeomPoint X=300 Y=0 Z=0
    g19: GeomPoint X=600 Y=-50.3976 Z=0
    g20: ArcOfCircle CenterX=-322.5 CenterY=0 CenterZ=0 NormalX=0 NormalY=0 NormalZ=1 AngleXU=0 Radius=30 StartAngle=1.5708 EndAngle=4.71239
    g21: ArcOfCircle CenterX=-277.5 CenterY=-1.4e-15 CenterZ=0 NormalX=0 NormalY=0 NormalZ=1 AngleXU=0 Radius=30 StartAngle=4.71239 EndAngle=7.85398
    g22: LineSegment StartX=-322.5 StartY=-30 StartZ=0 EndX=-277.5 EndY=-30 EndZ=0
    g23: LineSegment StartX=-277.5 StartY=30 StartZ=0 EndX=-322.5 EndY=30 EndZ=0
    g24: ArcOfCircle CenterX=-22.5 CenterY=-1.4e-15 CenterZ=0 NormalX=0 NormalY=0 NormalZ=1 AngleXU=0 Radius=30 StartAngle=1.5708 EndAngle=4.71239
    g25: ArcOfCircle CenterX=22.5 CenterY=-5e-16 CenterZ=0 NormalX=0 NormalY=0 NormalZ=1 AngleXU=0 Radius=30 StartAngle=4.71239 EndAngle=7.85398
    g26: LineSegment StartX=-22.5 StartY=-30 StartZ=0 EndX=22.5 EndY=-30 EndZ=0
    g27: LineSegment StartX=22.5 StartY=30 StartZ=0 EndX=-22.5 EndY=30 EndZ=0
    g28: ArcOfCircle CenterX=277.5 CenterY=-5e-16 CenterZ=0 NormalX=0 NormalY=0 NormalZ=1 AngleXU=0 Radius=30 StartAngle=1.5708 EndAngle=4.71239
    g29: ArcOfCircle CenterX=322.5 CenterY=-1e-15 CenterZ=0 NormalX=0 NormalY=0 NormalZ=1 AngleXU=0 Radius=30 StartAngle=4.71239 EndAngle=7.85398
    g30: LineSegment StartX=277.5 StartY=-30 StartZ=0 EndX=322.5 EndY=-30 EndZ=0
    g31: LineSegment StartX=322.5 StartY=30 StartZ=0 EndX=277.5 EndY=30 EndZ=0
    g32: Circle CenterX=-525 CenterY=0 CenterZ=0 NormalX=0 NormalY=0 NormalZ=1 AngleXU=0 Radius=25
    g33: Circle CenterX=-194.17 CenterY=-1.4e-15 CenterZ=0 NormalX=0 NormalY=0 NormalZ=1 AngleXU=0 Radius=25
    g34: Circle CenterX=105.83 CenterY=-5e-16 CenterZ=0 NormalX=0 NormalY=0 NormalZ=1 AngleXU=0 Radius=25
    g35: Circle CenterX=525 CenterY=-1e-15 CenterZ=0 NormalX=0 NormalY=0 NormalZ=1 AngleXU=0 Radius=25
    g36: Circle CenterX=-425 CenterY=0 CenterZ=0 NormalX=0 NormalY=0 NormalZ=1 AngleXU=0 Radius=25
    g37: Circle CenterX=-110.84 CenterY=0 CenterZ=0 NormalX=0 NormalY=0 NormalZ=1 AngleXU=0 Radius=25
    g38: Circle CenterX=189.16 CenterY=0 CenterZ=0 NormalX=0 NormalY=0 NormalZ=1 AngleXU=0 Radius=25
    g39: Circle CenterX=425 CenterY=0 CenterZ=0 NormalX=0 NormalY=0 NormalZ=1 AngleXU=0 Radius=25
  constraints (109):
    c: Coincident(g0,g1)
    c: Coincident(g1,g2)
    c: Coincident(g2,g3)
    c: Coincident(g3,g0)
    c: Horizontal(g0)
    c: Horizontal(g2)
    c: Vertical(g1)
    c: Vertical(g3)
    c: Coincident(g4,g5)
    c: Coincident(g5,g6)
    c: Coincident(g6,g7)
    c: Coincident(g7,g4)
    c: Horizontal(g4)
    c: Horizontal(g6)
    c: Vertical(g5)
    c: Vertical(g7)
    c: Vertical(g-4,g0)
    c: Vertical(g0,g6)
    c: Vertical(g5,g0)
    c: DistanceY(g2,g0) = 20
    c: DistanceY(g0,g6) = 20
    c: DistanceY(g6,g4) = 20
    c: DistanceX(g2,g1) = 4
    c: Coincident(g8,g9)
    c: Coincident(g9,g10)
    c: Coincident(g10,g11)
    c: Coincident(g11,g8)
    c: Horizontal(g8)
    c: Horizontal(g10)
    c: Vertical(g9)
    c: Vertical(g11)
    c: Coincident(g12,g13)
    c: Coincident(g13,g14)
    c: Coincident(g14,g15)
    c: Coincident(g15,g12)
    c: Horizontal(g12)
    c: Horizontal(g14)
    c: Vertical(g13)
    c: Vertical(g15)
    c: Vertical(g8,g14)
    c: Vertical(g13,g8)
    c: DistanceY(g10,g8) = 20
    c: DistanceY(g8,g14) = 20
    c: DistanceY(g14,g12) = 20
    c: DistanceX(g10,g9) = 4
    c: Vertical(g-6,g9)
    c: DistanceY(g-4,g2) = 20
    c: Horizontal(g4,g12)
    c: PointOnObject(g16,g-1)
    c: DistanceX(g-3,g16) = 300
    c: PointOnObject(g17,g-1)
    c: DistanceX(g16,g17) = 300
    c: PointOnObject(g18,g-1)
    c: DistanceX(g17,g18) = 300
    c: DistanceX(g18,g19) = 300
    c: Tangent(g20,g22) = -1.5708
    c: Tangent(g22,g21) = -1.5708
    c: Tangent(g21,g23) = -1.5708
    c: Tangent(g23,g20) = -1.5708
    c: Equal(g20,g21)
    c: Horizontal(g22)
    c: DistanceY(g20,g20) = 60
    c: DistanceY(g16,g20) = 0
    c: DistanceX(g20,g21) = 45
    c: DistanceX(g20,g16) = 22.5
    c: Tangent(g24,g26) = -1.5708
    c: Tangent(g26,g25) = -1.5708
    c: Tangent(g25,g27) = -1.5708
    c: Tangent(g27,g24) = -1.5708
    c: Equal(g24,g25)
    c: Horizontal(g26)
    c: DistanceY(g24,g24) = 60
    c: DistanceX(g24,g25) = 45
    c: DistanceX(g24,g17) = 22.5
    c: Horizontal(g24,g21)
    c: Tangent(g28,g30) = -1.5708
    c: Tangent(g30,g29) = -1.5708
    c: Tangent(g29,g31) = -1.5708
    c: Tangent(g31,g28) = -1.5708
    c: Equal(g28,g29)
    c: Horizontal(g30)
    c: DistanceY(g28,g28) = 60
    c: DistanceX(g28,g29) = 45
    c: Horizontal(g25,g28)
    c: DistanceX(g28,g18) = 22.5
    c: Horizontal(g20,g32)
    c: Horizontal(g21,g33)
    c: Horizontal(g25,g34)
    c: Horizontal(g29,g35)
    c: Diameter(g32) = 50
    c: Equal(g32,g33)
    c: Equal(g33,g34)
    c: Equal(g34,g35)
    c: DistanceX(g-4,g32) = 75
    c: PointOnObject(g36,g-1)
    c: Equal(g32,g36)
    c: DistanceX(g32,g36) = 100
    c: DistanceX(g21,g33) = 83.33
    c: PointOnObject(g37,g-1)
    c: Equal(g33,g37)
    c: DistanceX(g33,g37) = 83.33
    c: DistanceX(g25,g34) = 83.33
    c: PointOnObject(g38,g-1)
    c: Equal(g34,g38)
    c: DistanceX(g34,g38) = 83.33
    c: DistanceX(g35,g19) = 75
    c: PointOnObject(g39,g-1)
    c: Equal(g35,g39)
    c: DistanceX(g39,g35) = 100
FEATURE [PartDesign::Pocket] Pocket012
  BaseFeature = -> Pad014
  Length = 4
  Length2 = 5
  Placement = pos=(0,0,0) rot=(0.57735,0.57735,0.57735;2.0944rad)
  Profile = -> Sketch030
  Type = 0
FEATURE [PartDesign::Body] Body014  label="KortSprygel-2"
  Group = -> [Sketch029,Pad014,Sketch030,Pocket012]
  Origin = -> Origin014
  Placement = pos=(-335.33,0,0) rot=(0,0,1;0rad)
  Tip = -> Pocket012
FEATURE [Sketcher::SketchObject] Sketch031
  FullyConstrained = true
  MapMode = 5
  Placement = pos=(0,0,0) rot=(0.57735,0.57735,0.57735;2.0944rad)
  Support = -> [YZ_Plane015]
  sketch-geometry (5):
    g0: LineSegment StartX=-600 StartY=-50 StartZ=0 EndX=-600 EndY=50 EndZ=0
    g1: LineSegment StartX=-600 StartY=50 StartZ=0 EndX=600 EndY=50 EndZ=0
    g2: LineSegment StartX=600 StartY=50 StartZ=0 EndX=600 EndY=-50 EndZ=0
    g3: LineSegment StartX=600 StartY=-50 StartZ=0 EndX=-600 EndY=-50 EndZ=0
    g4: GeomPoint X=0 Y=0 Z=0
  constraints (12):
    c: Coincident(g0,g1)
    c: Coincident(g1,g2)
    c: Coincident(g2,g3)
    c: Coincident(g3,g0)
    c: Horizontal(g1)
    c: Horizontal(g3)
    c: Vertical(g0)
    c: Vertical(g2)
    c: Symmetric(g1,g0,g4)
    c: Coincident(g4,g-1)
    c: DistanceX(g0,g2) = 1200
    c: DistanceY(g0,g0) = 100
FEATURE [PartDesign::Pad] Pad015
  Direction = (1,-2e-16,3e-16)
  Length = 4
  Length2 = 10
  Placement = pos=(0,0,0) rot=(0.57735,0.57735,0.57735;2.0944rad)
  Profile = -> Sketch031
  Type = 0
FEATURE [Sketcher::SketchObject] Sketch032
  ExternalGeometry = -> [Pad015]
  FullyConstrained = false
  MapMode = 5
  Placement = pos=(4,-9e-16,9e-16) rot=(0.57735,0.57735,0.57735;2.0944rad)
  Support = -> [Pad015]
  sketch-geometry (40):
    g0: LineSegment StartX=-600 StartY=-10 StartZ=0 EndX=-596 EndY=-10 EndZ=0
    g1: LineSegment StartX=-596 StartY=-10 StartZ=0 EndX=-596 EndY=-30 EndZ=0
    g2: LineSegment StartX=-596 StartY=-30 StartZ=0 EndX=-600 EndY=-30 EndZ=0
    g3: LineSegment StartX=-600 StartY=-30 StartZ=0 EndX=-600 EndY=-10 EndZ=0
    g4: LineSegment StartX=-600 StartY=30 StartZ=0 EndX=-596 EndY=30 EndZ=0
    g5: LineSegment StartX=-596 StartY=30 StartZ=0 EndX=-596 EndY=10 EndZ=0
    g6: LineSegment StartX=-596 StartY=10 StartZ=0 EndX=-600 EndY=10 EndZ=0
    g7: LineSegment StartX=-600 StartY=10 StartZ=0 EndX=-600 EndY=30 EndZ=0
    g8: LineSegment StartX=596 StartY=-10 StartZ=0 EndX=600 EndY=-10 EndZ=0
    g9: LineSegment StartX=600 StartY=-10 StartZ=0 EndX=600 EndY=-30 EndZ=0
    g10: LineSegment StartX=600 StartY=-30 StartZ=0 EndX=596 EndY=-30 EndZ=0
    g11: LineSegment StartX=596 StartY=-30 StartZ=0 EndX=596 EndY=-10 EndZ=0
    g12: LineSegment StartX=596 StartY=30 StartZ=0 EndX=600 EndY=30 EndZ=0
    g13: LineSegment StartX=600 StartY=30 StartZ=0 EndX=600 EndY=10 EndZ=0
    g14: LineSegment StartX=600 StartY=10 StartZ=0 EndX=596 EndY=10 EndZ=0
    g15: LineSegment StartX=596 StartY=10 StartZ=0 EndX=596 EndY=30 EndZ=0
    g16: GeomPoint X=-300 Y=0 Z=0
    g17: GeomPoint X=-2.222e-13 Y=0 Z=0
    g18: GeomPoint X=300 Y=0 Z=0
    g19: GeomPoint X=600 Y=-50.3976 Z=0
    g20: ArcOfCircle CenterX=-322.5 CenterY=0 CenterZ=0 NormalX=0 NormalY=0 NormalZ=1 AngleXU=0 Radius=30 StartAngle=1.5708 EndAngle=4.71239
    g21: ArcOfCircle CenterX=-277.5 CenterY=-1.4e-15 CenterZ=0 NormalX=0 NormalY=0 NormalZ=1 AngleXU=0 Radius=30 StartAngle=4.71239 EndAngle=7.85398
    g22: LineSegment StartX=-322.5 StartY=-30 StartZ=0 EndX=-277.5 EndY=-30 EndZ=0
    g23: LineSegment StartX=-277.5 StartY=30 StartZ=0 EndX=-322.5 EndY=30 EndZ=0
    g24: ArcOfCircle CenterX=-22.5 CenterY=-1.4e-15 CenterZ=0 NormalX=0 NormalY=0 NormalZ=1 AngleXU=0 Radius=30 StartAngle=1.5708 EndAngle=4.71239
    g25: ArcOfCircle CenterX=22.5 CenterY=-5e-16 CenterZ=0 NormalX=0 NormalY=0 NormalZ=1 AngleXU=0 Radius=30 StartAngle=4.71239 EndAngle=7.85398
    g26: LineSegment StartX=-22.5 StartY=-30 StartZ=0 EndX=22.5 EndY=-30 EndZ=0
    g27: LineSegment StartX=22.5 StartY=30 StartZ=0 EndX=-22.5 EndY=30 EndZ=0
    g28: ArcOfCircle CenterX=277.5 CenterY=-5e-16 CenterZ=0 NormalX=0 NormalY=0 NormalZ=1 AngleXU=0 Radius=30 StartAngle=1.5708 EndAngle=4.71239
    g29: ArcOfCircle CenterX=322.5 CenterY=-1e-15 CenterZ=0 NormalX=0 NormalY=0 NormalZ=1 AngleXU=0 Radius=30 StartAngle=4.71239 EndAngle=7.85398
    g30: LineSegment StartX=277.5 StartY=-30 StartZ=0 EndX=322.5 EndY=-30 EndZ=0
    g31: LineSegment StartX=322.5 StartY=30 StartZ=0 EndX=277.5 EndY=30 EndZ=0
    g32: Circle CenterX=-525 CenterY=0 CenterZ=0 NormalX=0 NormalY=0 NormalZ=1 AngleXU=0 Radius=25
    g33: Circle CenterX=-194.17 CenterY=-1.4e-15 CenterZ=0 NormalX=0 NormalY=0 NormalZ=1 AngleXU=0 Radius=25
    g34: Circle CenterX=105.83 CenterY=-5e-16 CenterZ=0 NormalX=0 NormalY=0 NormalZ=1 AngleXU=0 Radius=25
    g35: Circle CenterX=525 CenterY=-1e-15 CenterZ=0 NormalX=0 NormalY=0 NormalZ=1 AngleXU=0 Radius=25
    g36: Circle CenterX=-425 CenterY=0 CenterZ=0 NormalX=0 NormalY=0 NormalZ=1 AngleXU=0 Radius=25
    g37: Circle CenterX=-110.84 CenterY=0 CenterZ=0 NormalX=0 NormalY=0 NormalZ=1 AngleXU=0 Radius=25
    g38: Circle CenterX=189.16 CenterY=0 CenterZ=0 NormalX=0 NormalY=0 NormalZ=1 AngleXU=0 Radius=25
    g39: Circle CenterX=425 CenterY=0 CenterZ=0 NormalX=0 NormalY=0 NormalZ=1 AngleXU=0 Radius=25
  constraints (109):
    c: Coincident(g0,g1)
    c: Coincident(g1,g2)
    c: Coincident(g2,g3)
    c: Coincident(g3,g0)
    c: Horizontal(g0)
    c: Horizontal(g2)
    c: Vertical(g1)
    c: Vertical(g3)
    c: Coincident(g4,g5)
    c: Coincident(g5,g6)
    c: Coincident(g6,g7)
    c: Coincident(g7,g4)
    c: Horizontal(g4)
    c: Horizontal(g6)
    c: Vertical(g5)
    c: Vertical(g7)
    c: Vertical(g-4,g0)
    c: Vertical(g0,g6)
    c: Vertical(g5,g0)
    c: DistanceY(g2,g0) = 20
    c: DistanceY(g0,g6) = 20
    c: DistanceY(g6,g4) = 20
    c: DistanceX(g2,g1) = 4
    c: Coincident(g8,g9)
    c: Coincident(g9,g10)
    c: Coincident(g10,g11)
    c: Coincident(g11,g8)
    c: Horizontal(g8)
    c: Horizontal(g10)
    c: Vertical(g9)
    c: Vertical(g11)
    c: Coincident(g12,g13)
    c: Coincident(g13,g14)
    c: Coincident(g14,g15)
    c: Coincident(g15,g12)
    c: Horizontal(g12)
    c: Horizontal(g14)
    c: Vertical(g13)
    c: Vertical(g15)
    c: Vertical(g8,g14)
    c: Vertical(g13,g8)
    c: DistanceY(g10,g8) = 20
    c: DistanceY(g8,g14) = 20
    c: DistanceY(g14,g12) = 20
    c: DistanceX(g10,g9) = 4
    c: Vertical(g-6,g9)
    c: DistanceY(g-4,g2) = 20
    c: Horizontal(g4,g12)
    c: PointOnObject(g16,g-1)
    c: DistanceX(g-3,g16) = 300
    c: PointOnObject(g17,g-1)
    c: DistanceX(g16,g17) = 300
    c: PointOnObject(g18,g-1)
    c: DistanceX(g17,g18) = 300
    c: DistanceX(g18,g19) = 300
    c: Tangent(g20,g22) = -1.5708
    c: Tangent(g22,g21) = -1.5708
    c: Tangent(g21,g23) = -1.5708
    c: Tangent(g23,g20) = -1.5708
    c: Equal(g20,g21)
    c: Horizontal(g22)
    c: DistanceY(g20,g20) = 60
    c: DistanceY(g16,g20) = 0
    c: DistanceX(g20,g21) = 45
    c: DistanceX(g20,g16) = 22.5
    c: Tangent(g24,g26) = -1.5708
    c: Tangent(g26,g25) = -1.5708
    c: Tangent(g25,g27) = -1.5708
    c: Tangent(g27,g24) = -1.5708
    c: Equal(g24,g25)
    c: Horizontal(g26)
    c: DistanceY(g24,g24) = 60
    c: DistanceX(g24,g25) = 45
    c: DistanceX(g24,g17) = 22.5
    c: Horizontal(g24,g21)
    c: Tangent(g28,g30) = -1.5708
    c: Tangent(g30,g29) = -1.5708
    c: Tangent(g29,g31) = -1.5708
    c: Tangent(g31,g28) = -1.5708
    c: Equal(g28,g29)
    c: Horizontal(g30)
    c: DistanceY(g28,g28) = 60
    c: DistanceX(g28,g29) = 45
    c: Horizontal(g25,g28)
    c: DistanceX(g28,g18) = 22.5
    c: Horizontal(g20,g32)
    c: Horizontal(g21,g33)
    c: Horizontal(g25,g34)
    c: Horizontal(g29,g35)
    c: Diameter(g32) = 50
    c: Equal(g32,g33)
    c: Equal(g33,g34)
    c: Equal(g34,g35)
    c: DistanceX(g-4,g32) = 75
    c: PointOnObject(g36,g-1)
    c: Equal(g32,g36)
    c: DistanceX(g32,g36) = 100
    c: DistanceX(g21,g33) = 83.33
    c: PointOnObject(g37,g-1)
    c: Equal(g33,g37)
    c: DistanceX(g33,g37) = 83.33
    c: DistanceX(g25,g34) = 83.33
    c: PointOnObject(g38,g-1)
    c: Equal(g34,g38)
    c: DistanceX(g34,g38) = 83.33
    c: DistanceX(g35,g19) = 75
    c: PointOnObject(g39,g-1)
    c: Equal(g35,g39)
    c: DistanceX(g39,g35) = 100
FEATURE [PartDesign::Pocket] Pocket013
  BaseFeature = -> Pad015
  Length = 4
  Length2 = 5
  Placement = pos=(0,0,0) rot=(0.57735,0.57735,0.57735;2.0944rad)
  Profile = -> Sketch032
  Type = 0
FEATURE [PartDesign::Body] Body015  label="KortSprygel-3"
  Group = -> [Sketch031,Pad015,Sketch032,Pocket013]
  Origin = -> Origin015
  Placement = pos=(-2,0,0) rot=(0,0,1;0rad)
  Tip = -> Pocket013
FEATURE [Sketcher::SketchObject] Sketch033
  FullyConstrained = true
  MapMode = 5
  Placement = pos=(0,0,0) rot=(0.57735,0.57735,0.57735;2.0944rad)
  Support = -> [YZ_Plane016]
  sketch-geometry (5):
    g0: LineSegment StartX=-600 StartY=-50 StartZ=0 EndX=-600 EndY=50 EndZ=0
    g1: LineSegment StartX=-600 StartY=50 StartZ=0 EndX=600 EndY=50 EndZ=0
    g2: LineSegment StartX=600 StartY=50 StartZ=0 EndX=600 EndY=-50 EndZ=0
    g3: LineSegment StartX=600 StartY=-50 StartZ=0 EndX=-600 EndY=-50 EndZ=0
    g4: GeomPoint X=0 Y=0 Z=0
  constraints (12):
    c: Coincident(g0,g1)
    c: Coincident(g1,g2)
    c: Coincident(g2,g3)
    c: Coincident(g3,g0)
    c: Horizontal(g1)
    c: Horizontal(g3)
    c: Vertical(g0)
    c: Vertical(g2)
    c: Symmetric(g1,g0,g4)
    c: Coincident(g4,g-1)
    c: DistanceX(g0,g2) = 1200
    c: DistanceY(g0,g0) = 100
FEATURE [PartDesign::Pad] Pad016
  Direction = (1,-2e-16,3e-16)
  Length = 4
  Length2 = 10
  Placement = pos=(0,0,0) rot=(0.57735,0.57735,0.57735;2.0944rad)
  Profile = -> Sketch033
  Type = 0
FEATURE [Sketcher::SketchObject] Sketch034
  ExternalGeometry = -> [Pad016]
  FullyConstrained = false
  MapMode = 5
  Placement = pos=(4,-9e-16,9e-16) rot=(0.57735,0.57735,0.57735;2.0944rad)
  Support = -> [Pad016]
  sketch-geometry (40):
    g0: LineSegment StartX=-600 StartY=-10 StartZ=0 EndX=-596 EndY=-10 EndZ=0
    g1: LineSegment StartX=-596 StartY=-10 StartZ=0 EndX=-596 EndY=-30 EndZ=0
    g2: LineSegment StartX=-596 StartY=-30 StartZ=0 EndX=-600 EndY=-30 EndZ=0
    g3: LineSegment StartX=-600 StartY=-30 StartZ=0 EndX=-600 EndY=-10 EndZ=0
    g4: LineSegment StartX=-600 StartY=30 StartZ=0 EndX=-596 EndY=30 EndZ=0
    g5: LineSegment StartX=-596 StartY=30 StartZ=0 EndX=-596 EndY=10 EndZ=0
    g6: LineSegment StartX=-596 StartY=10 StartZ=0 EndX=-600 EndY=10 EndZ=0
    g7: LineSegment StartX=-600 StartY=10 StartZ=0 EndX=-600 EndY=30 EndZ=0
    g8: LineSegment StartX=596 StartY=-10 StartZ=0 EndX=600 EndY=-10 EndZ=0
    g9: LineSegment StartX=600 StartY=-10 StartZ=0 EndX=600 EndY=-30 EndZ=0
    g10: LineSegment StartX=600 StartY=-30 StartZ=0 EndX=596 EndY=-30 EndZ=0
    g11: LineSegment StartX=596 StartY=-30 StartZ=0 EndX=596 EndY=-10 EndZ=0
    g12: LineSegment StartX=596 StartY=30 StartZ=0 EndX=600 EndY=30 EndZ=0
    g13: LineSegment StartX=600 StartY=30 StartZ=0 EndX=600 EndY=10 EndZ=0
    g14: LineSegment StartX=600 StartY=10 StartZ=0 EndX=596 EndY=10 EndZ=0
    g15: LineSegment StartX=596 StartY=10 StartZ=0 EndX=596 EndY=30 EndZ=0
    g16: GeomPoint X=-300 Y=0 Z=0
    g17: GeomPoint X=-2.222e-13 Y=0 Z=0
    g18: GeomPoint X=300 Y=0 Z=0
    g19: GeomPoint X=600 Y=-50.3976 Z=0
    g20: ArcOfCircle CenterX=-322.5 CenterY=0 CenterZ=0 NormalX=0 NormalY=0 NormalZ=1 AngleXU=0 Radius=30 StartAngle=1.5708 EndAngle=4.71239
    g21: ArcOfCircle CenterX=-277.5 CenterY=-1.4e-15 CenterZ=0 NormalX=0 NormalY=0 NormalZ=1 AngleXU=0 Radius=30 StartAngle=4.71239 EndAngle=7.85398
    g22: LineSegment StartX=-322.5 StartY=-30 StartZ=0 EndX=-277.5 EndY=-30 EndZ=0
    g23: LineSegment StartX=-277.5 StartY=30 StartZ=0 EndX=-322.5 EndY=30 EndZ=0
    g24: ArcOfCircle CenterX=-22.5 CenterY=-1.4e-15 CenterZ=0 NormalX=0 NormalY=0 NormalZ=1 AngleXU=0 Radius=30 StartAngle=1.5708 EndAngle=4.71239
    g25: ArcOfCircle CenterX=22.5 CenterY=-5e-16 CenterZ=0 NormalX=0 NormalY=0 NormalZ=1 AngleXU=0 Radius=30 StartAngle=4.71239 EndAngle=7.85398
    g26: LineSegment StartX=-22.5 StartY=-30 StartZ=0 EndX=22.5 EndY=-30 EndZ=0
    g27: LineSegment StartX=22.5 StartY=30 StartZ=0 EndX=-22.5 EndY=30 EndZ=0
    g28: ArcOfCircle CenterX=277.5 CenterY=-5e-16 CenterZ=0 NormalX=0 NormalY=0 NormalZ=1 AngleXU=0 Radius=30 StartAngle=1.5708 EndAngle=4.71239
    g29: ArcOfCircle CenterX=322.5 CenterY=-1e-15 CenterZ=0 NormalX=0 NormalY=0 NormalZ=1 AngleXU=0 Radius=30 StartAngle=4.71239 EndAngle=7.85398
    g30: LineSegment StartX=277.5 StartY=-30 StartZ=0 EndX=322.5 EndY=-30 EndZ=0
    g31: LineSegment StartX=322.5 StartY=30 StartZ=0 EndX=277.5 EndY=30 EndZ=0
    g32: Circle CenterX=-525 CenterY=0 CenterZ=0 NormalX=0 NormalY=0 NormalZ=1 AngleXU=0 Radius=25
    g33: Circle CenterX=-194.17 CenterY=-1.4e-15 CenterZ=0 NormalX=0 NormalY=0 NormalZ=1 AngleXU=0 Radius=25
    g34: Circle CenterX=105.83 CenterY=-5e-16 CenterZ=0 NormalX=0 NormalY=0 NormalZ=1 AngleXU=0 Radius=25
    g35: Circle CenterX=525 CenterY=-1e-15 CenterZ=0 NormalX=0 NormalY=0 NormalZ=1 AngleXU=0 Radius=25
    g36: Circle CenterX=-425 CenterY=0 CenterZ=0 NormalX=0 NormalY=0 NormalZ=1 AngleXU=0 Radius=25
    g37: Circle CenterX=-110.84 CenterY=0 CenterZ=0 NormalX=0 NormalY=0 NormalZ=1 AngleXU=0 Radius=25
    g38: Circle CenterX=189.16 CenterY=0 CenterZ=0 NormalX=0 NormalY=0 NormalZ=1 AngleXU=0 Radius=25
    g39: Circle CenterX=425 CenterY=0 CenterZ=0 NormalX=0 NormalY=0 NormalZ=1 AngleXU=0 Radius=25
  constraints (109):
    c: Coincident(g0,g1)
    c: Coincident(g1,g2)
    c: Coincident(g2,g3)
    c: Coincident(g3,g0)
    c: Horizontal(g0)
    c: Horizontal(g2)
    c: Vertical(g1)
    c: Vertical(g3)
    c: Coincident(g4,g5)
    c: Coincident(g5,g6)
    c: Coincident(g6,g7)
    c: Coincident(g7,g4)
    c: Horizontal(g4)
    c: Horizontal(g6)
    c: Vertical(g5)
    c: Vertical(g7)
    c: Vertical(g-4,g0)
    c: Vertical(g0,g6)
    c: Vertical(g5,g0)
    c: DistanceY(g2,g0) = 20
    c: DistanceY(g0,g6) = 20
    c: DistanceY(g6,g4) = 20
    c: DistanceX(g2,g1) = 4
    c: Coincident(g8,g9)
    c: Coincident(g9,g10)
    c: Coincident(g10,g11)
    c: Coincident(g11,g8)
    c: Horizontal(g8)
    c: Horizontal(g10)
    c: Vertical(g9)
    c: Vertical(g11)
    c: Coincident(g12,g13)
    c: Coincident(g13,g14)
    c: Coincident(g14,g15)
    c: Coincident(g15,g12)
    c: Horizontal(g12)
    c: Horizontal(g14)
    c: Vertical(g13)
    c: Vertical(g15)
    c: Vertical(g8,g14)
    c: Vertical(g13,g8)
    c: DistanceY(g10,g8) = 20
    c: DistanceY(g8,g14) = 20
    c: DistanceY(g14,g12) = 20
    c: DistanceX(g10,g9) = 4
    c: Vertical(g-6,g9)
    c: DistanceY(g-4,g2) = 20
    c: Horizontal(g4,g12)
    c: PointOnObject(g16,g-1)
    c: DistanceX(g-3,g16) = 300
    c: PointOnObject(g17,g-1)
    c: DistanceX(g16,g17) = 300
    c: PointOnObject(g18,g-1)
    c: DistanceX(g17,g18) = 300
    c: DistanceX(g18,g19) = 300
    c: Tangent(g20,g22) = -1.5708
    c: Tangent(g22,g21) = -1.5708
    c: Tangent(g21,g23) = -1.5708
    c: Tangent(g23,g20) = -1.5708
    c: Equal(g20,g21)
    c: Horizontal(g22)
    c: DistanceY(g20,g20) = 60
    c: DistanceY(g16,g20) = 0
    c: DistanceX(g20,g21) = 45
    c: DistanceX(g20,g16) = 22.5
    c: Tangent(g24,g26) = -1.5708
    c: Tangent(g26,g25) = -1.5708
    c: Tangent(g25,g27) = -1.5708
    c: Tangent(g27,g24) = -1.5708
    c: Equal(g24,g25)
    c: Horizontal(g26)
    c: DistanceY(g24,g24) = 60
    c: DistanceX(g24,g25) = 45
    c: DistanceX(g24,g17) = 22.5
    c: Horizontal(g24,g21)
    c: Tangent(g28,g30) = -1.5708
    c: Tangent(g30,g29) = -1.5708
    c: Tangent(g29,g31) = -1.5708
    c: Tangent(g31,g28) = -1.5708
    c: Equal(g28,g29)
    c: Horizontal(g30)
    c: DistanceY(g28,g28) = 60
    c: DistanceX(g28,g29) = 45
    c: Horizontal(g25,g28)
    c: DistanceX(g28,g18) = 22.5
    c: Horizontal(g20,g32)
    c: Horizontal(g21,g33)
    c: Horizontal(g25,g34)
    c: Horizontal(g29,g35)
    c: Diameter(g32) = 50
    c: Equal(g32,g33)
    c: Equal(g33,g34)
    c: Equal(g34,g35)
    c: DistanceX(g-4,g32) = 75
    c: PointOnObject(g36,g-1)
    c: Equal(g32,g36)
    c: DistanceX(g32,g36) = 100
    c: DistanceX(g21,g33) = 83.33
    c: PointOnObject(g37,g-1)
    c: Equal(g33,g37)
    c: DistanceX(g33,g37) = 83.33
    c: DistanceX(g25,g34) = 83.33
    c: PointOnObject(g38,g-1)
    c: Equal(g34,g38)
    c: DistanceX(g34,g38) = 83.33
    c: DistanceX(g35,g19) = 75
    c: PointOnObject(g39,g-1)
    c: Equal(g35,g39)
    c: DistanceX(g39,g35) = 100
FEATURE [PartDesign::Pocket] Pocket014
  BaseFeature = -> Pad016
  Length = 4
  Length2 = 5
  Placement = pos=(0,0,0) rot=(0.57735,0.57735,0.57735;2.0944rad)
  Profile = -> Sketch034
  Type = 0
FEATURE [PartDesign::Body] Body016  label="KortSprygel-4"
  Group = -> [Sketch033,Pad016,Sketch034,Pocket014]
  Origin = -> Origin016
  Placement = pos=(331.33,0,0) rot=(0,0,1;0rad)
  Tip = -> Pocket014
FEATURE [Sketcher::SketchObject] Sketch035
  FullyConstrained = true
  MapMode = 5
  Placement = pos=(0,0,0) rot=(0.57735,0.57735,0.57735;2.0944rad)
  Support = -> [YZ_Plane017]
  sketch-geometry (5):
    g0: LineSegment StartX=-600 StartY=-50 StartZ=0 EndX=-600 EndY=50 EndZ=0
    g1: LineSegment StartX=-600 StartY=50 StartZ=0 EndX=600 EndY=50 EndZ=0
    g2: LineSegment StartX=600 StartY=50 StartZ=0 EndX=600 EndY=-50 EndZ=0
    g3: LineSegment StartX=600 StartY=-50 StartZ=0 EndX=-600 EndY=-50 EndZ=0
    g4: GeomPoint X=0 Y=0 Z=0
  constraints (12):
    c: Coincident(g0,g1)
    c: Coincident(g1,g2)
    c: Coincident(g2,g3)
    c: Coincident(g3,g0)
    c: Horizontal(g1)
    c: Horizontal(g3)
    c: Vertical(g0)
    c: Vertical(g2)
    c: Symmetric(g1,g0,g4)
    c: Coincident(g4,g-1)
    c: DistanceX(g0,g2) = 1200
    c: DistanceY(g0,g0) = 100
FEATURE [PartDesign::Pad] Pad017
  Direction = (1,-2e-16,3e-16)
  Length = 4
  Length2 = 10
  Placement = pos=(0,0,0) rot=(0.57735,0.57735,0.57735;2.0944rad)
  Profile = -> Sketch035
  Type = 0
FEATURE [Sketcher::SketchObject] Sketch036
  ExternalGeometry = -> [Pad017]
  FullyConstrained = false
  MapMode = 5
  Placement = pos=(4,-9e-16,9e-16) rot=(0.57735,0.57735,0.57735;2.0944rad)
  Support = -> [Pad017]
  sketch-geometry (40):
    g0: LineSegment StartX=-600 StartY=-10 StartZ=0 EndX=-596 EndY=-10 EndZ=0
    g1: LineSegment StartX=-596 StartY=-10 StartZ=0 EndX=-596 EndY=-30 EndZ=0
    g2: LineSegment StartX=-596 StartY=-30 StartZ=0 EndX=-600 EndY=-30 EndZ=0
    g3: LineSegment StartX=-600 StartY=-30 StartZ=0 EndX=-600 EndY=-10 EndZ=0
    g4: LineSegment StartX=-600 StartY=30 StartZ=0 EndX=-596 EndY=30 EndZ=0
    g5: LineSegment StartX=-596 StartY=30 StartZ=0 EndX=-596 EndY=10 EndZ=0
    g6: LineSegment StartX=-596 StartY=10 StartZ=0 EndX=-600 EndY=10 EndZ=0
    g7: LineSegment StartX=-600 StartY=10 StartZ=0 EndX=-600 EndY=30 EndZ=0
    g8: LineSegment StartX=596 StartY=-10 StartZ=0 EndX=600 EndY=-10 EndZ=0
    g9: LineSegment StartX=600 StartY=-10 StartZ=0 EndX=600 EndY=-30 EndZ=0
    g10: LineSegment StartX=600 StartY=-30 StartZ=0 EndX=596 EndY=-30 EndZ=0
    g11: LineSegment StartX=596 StartY=-30 StartZ=0 EndX=596 EndY=-10 EndZ=0
    g12: LineSegment StartX=596 StartY=30 StartZ=0 EndX=600 EndY=30 EndZ=0
    g13: LineSegment StartX=600 StartY=30 StartZ=0 EndX=600 EndY=10 EndZ=0
    g14: LineSegment StartX=600 StartY=10 StartZ=0 EndX=596 EndY=10 EndZ=0
    g15: LineSegment StartX=596 StartY=10 StartZ=0 EndX=596 EndY=30 EndZ=0
    g16: GeomPoint X=-300 Y=0 Z=0
    g17: GeomPoint X=-2.222e-13 Y=0 Z=0
    g18: GeomPoint X=300 Y=0 Z=0
    g19: GeomPoint X=600 Y=-50.3976 Z=0
    g20: ArcOfCircle CenterX=-322.5 CenterY=0 CenterZ=0 NormalX=0 NormalY=0 NormalZ=1 AngleXU=0 Radius=30 StartAngle=1.5708 EndAngle=4.71239
    g21: ArcOfCircle CenterX=-277.5 CenterY=-1.4e-15 CenterZ=0 NormalX=0 NormalY=0 NormalZ=1 AngleXU=0 Radius=30 StartAngle=4.71239 EndAngle=7.85398
    g22: LineSegment StartX=-322.5 StartY=-30 StartZ=0 EndX=-277.5 EndY=-30 EndZ=0
    g23: LineSegment StartX=-277.5 StartY=30 StartZ=0 EndX=-322.5 EndY=30 EndZ=0
    g24: ArcOfCircle CenterX=-22.5 CenterY=-1.4e-15 CenterZ=0 NormalX=0 NormalY=0 NormalZ=1 AngleXU=0 Radius=30 StartAngle=1.5708 EndAngle=4.71239
    g25: ArcOfCircle CenterX=22.5 CenterY=-5e-16 CenterZ=0 NormalX=0 NormalY=0 NormalZ=1 AngleXU=0 Radius=30 StartAngle=4.71239 EndAngle=7.85398
    g26: LineSegment StartX=-22.5 StartY=-30 StartZ=0 EndX=22.5 EndY=-30 EndZ=0
    g27: LineSegment StartX=22.5 StartY=30 StartZ=0 EndX=-22.5 EndY=30 EndZ=0
    g28: ArcOfCircle CenterX=277.5 CenterY=-5e-16 CenterZ=0 NormalX=0 NormalY=0 NormalZ=1 AngleXU=0 Radius=30 StartAngle=1.5708 EndAngle=4.71239
    g29: ArcOfCircle CenterX=322.5 CenterY=-1e-15 CenterZ=0 NormalX=0 NormalY=0 NormalZ=1 AngleXU=0 Radius=30 StartAngle=4.71239 EndAngle=7.85398
    g30: LineSegment StartX=277.5 StartY=-30 StartZ=0 EndX=322.5 EndY=-30 EndZ=0
    g31: LineSegment StartX=322.5 StartY=30 StartZ=0 EndX=277.5 EndY=30 EndZ=0
    g32: Circle CenterX=-525 CenterY=0 CenterZ=0 NormalX=0 NormalY=0 NormalZ=1 AngleXU=0 Radius=25
    g33: Circle CenterX=-194.17 CenterY=-1.4e-15 CenterZ=0 NormalX=0 NormalY=0 NormalZ=1 AngleXU=0 Radius=25
    g34: Circle CenterX=105.83 CenterY=-5e-16 CenterZ=0 NormalX=0 NormalY=0 NormalZ=1 AngleXU=0 Radius=25
    g35: Circle CenterX=525 CenterY=-1e-15 CenterZ=0 NormalX=0 NormalY=0 NormalZ=1 AngleXU=0 Radius=25
    g36: Circle CenterX=-425 CenterY=0 CenterZ=0 NormalX=0 NormalY=0 NormalZ=1 AngleXU=0 Radius=25
    g37: Circle CenterX=-110.84 CenterY=0 CenterZ=0 NormalX=0 NormalY=0 NormalZ=1 AngleXU=0 Radius=25
    g38: Circle CenterX=189.16 CenterY=0 CenterZ=0 NormalX=0 NormalY=0 NormalZ=1 AngleXU=0 Radius=25
    g39: Circle CenterX=425 CenterY=0 CenterZ=0 NormalX=0 NormalY=0 NormalZ=1 AngleXU=0 Radius=25
  constraints (109):
    c: Coincident(g0,g1)
    c: Coincident(g1,g2)
    c: Coincident(g2,g3)
    c: Coincident(g3,g0)
    c: Horizontal(g0)
    c: Horizontal(g2)
    c: Vertical(g1)
    c: Vertical(g3)
    c: Coincident(g4,g5)
    c: Coincident(g5,g6)
    c: Coincident(g6,g7)
    c: Coincident(g7,g4)
    c: Horizontal(g4)
    c: Horizontal(g6)
    c: Vertical(g5)
    c: Vertical(g7)
    c: Vertical(g-4,g0)
    c: Vertical(g0,g6)
    c: Vertical(g5,g0)
    c: DistanceY(g2,g0) = 20
    c: DistanceY(g0,g6) = 20
    c: DistanceY(g6,g4) = 20
    c: DistanceX(g2,g1) = 4
    c: Coincident(g8,g9)
    c: Coincident(g9,g10)
    c: Coincident(g10,g11)
    c: Coincident(g11,g8)
    c: Horizontal(g8)
    c: Horizontal(g10)
    c: Vertical(g9)
    c: Vertical(g11)
    c: Coincident(g12,g13)
    c: Coincident(g13,g14)
    c: Coincident(g14,g15)
    c: Coincident(g15,g12)
    c: Horizontal(g12)
    c: Horizontal(g14)
    c: Vertical(g13)
    c: Vertical(g15)
    c: Vertical(g8,g14)
    c: Vertical(g13,g8)
    c: DistanceY(g10,g8) = 20
    c: DistanceY(g8,g14) = 20
    c: DistanceY(g14,g12) = 20
    c: DistanceX(g10,g9) = 4
    c: Vertical(g-6,g9)
    c: DistanceY(g-4,g2) = 20
    c: Horizontal(g4,g12)
    c: PointOnObject(g16,g-1)
    c: DistanceX(g-3,g16) = 300
    c: PointOnObject(g17,g-1)
    c: DistanceX(g16,g17) = 300
    c: PointOnObject(g18,g-1)
    c: DistanceX(g17,g18) = 300
    c: DistanceX(g18,g19) = 300
    c: Tangent(g20,g22) = -1.5708
    c: Tangent(g22,g21) = -1.5708
    c: Tangent(g21,g23) = -1.5708
    c: Tangent(g23,g20) = -1.5708
    c: Equal(g20,g21)
    c: Horizontal(g22)
    c: DistanceY(g20,g20) = 60
    c: DistanceY(g16,g20) = 0
    c: DistanceX(g20,g21) = 45
    c: DistanceX(g20,g16) = 22.5
    c: Tangent(g24,g26) = -1.5708
    c: Tangent(g26,g25) = -1.5708
    c: Tangent(g25,g27) = -1.5708
    c: Tangent(g27,g24) = -1.5708
    c: Equal(g24,g25)
    c: Horizontal(g26)
    c: DistanceY(g24,g24) = 60
    c: DistanceX(g24,g25) = 45
    c: DistanceX(g24,g17) = 22.5
    c: Horizontal(g24,g21)
    c: Tangent(g28,g30) = -1.5708
    c: Tangent(g30,g29) = -1.5708
    c: Tangent(g29,g31) = -1.5708
    c: Tangent(g31,g28) = -1.5708
    c: Equal(g28,g29)
    c: Horizontal(g30)
    c: DistanceY(g28,g28) = 60
    c: DistanceX(g28,g29) = 45
    c: Horizontal(g25,g28)
    c: DistanceX(g28,g18) = 22.5
    c: Horizontal(g20,g32)
    c: Horizontal(g21,g33)
    c: Horizontal(g25,g34)
    c: Horizontal(g29,g35)
    c: Diameter(g32) = 50
    c: Equal(g32,g33)
    c: Equal(g33,g34)
    c: Equal(g34,g35)
    c: DistanceX(g-4,g32) = 75
    c: PointOnObject(g36,g-1)
    c: Equal(g32,g36)
    c: DistanceX(g32,g36) = 100
    c: DistanceX(g21,g33) = 83.33
    c: PointOnObject(g37,g-1)
    c: Equal(g33,g37)
    c: DistanceX(g33,g37) = 83.33
    c: DistanceX(g25,g34) = 83.33
    c: PointOnObject(g38,g-1)
    c: Equal(g34,g38)
    c: DistanceX(g34,g38) = 83.33
    c: DistanceX(g35,g19) = 75
    c: PointOnObject(g39,g-1)
    c: Equal(g35,g39)
    c: DistanceX(g39,g35) = 100
FEATURE [PartDesign::Pocket] Pocket015
  BaseFeature = -> Pad017
  Length = 4
  Length2 = 5
  Placement = pos=(0,0,0) rot=(0.57735,0.57735,0.57735;2.0944rad)
  Profile = -> Sketch036
  Type = 0
FEATURE [PartDesign::Body] Body017  label="KortSprygel-5"
  Group = -> [Sketch035,Pad017,Sketch036,Pocket015]
  Origin = -> Origin017
  Placement = pos=(664.66,0,0) rot=(0,0,1;0rad)
  Tip = -> Pocket015
FEATURE [App::DocumentObjectGroupPython] SimpleGroup011  # scripted group (container) (typed FeaturePython)
  AnimationStepTime = 0.01
  AnimationSteps = 200
  Distance = 100
  Revolutions = 0
FEATURE [App::DocumentObjectGroupPython] SimpleGroup012  # scripted group (container) (typed FeaturePython)
  AnimationStepTime = 0.01
  AnimationSteps = 200
  Distance = 3000
  Revolutions = 0
FEATURE [App::DocumentObjectGroupPython] SimpleGroup013  # scripted group (container) (typed FeaturePython)
  AnimationStepTime = 0.01
  AnimationSteps = 200
  Distance = 0
  Revolutions = -0.25
FEATURE [App::DocumentObjectGroupPython] SimpleGroup014  # scripted group (container) (typed FeaturePython)
  AnimationStepTime = 0.01
  AnimationSteps = 200
  Distance = 100
  Revolutions = 0
FEATURE [App::DocumentObjectGroupPython] SimpleGroup015  # scripted group (container) (typed FeaturePython)
  AnimationStepTime = 0.01
  AnimationSteps = 200
  Distance = 2000
  Revolutions = 0
FEATURE [App::DocumentObjectGroupPython] SimpleGroup016  # scripted group (container) (typed FeaturePython)
  AnimationStepTime = 0.01
  AnimationSteps = 200
  Distance = 2000
  Revolutions = 0
FEATURE [App::DocumentObjectGroupPython] SimpleGroup017  # scripted group (container) (typed FeaturePython)
  AnimationStepTime = 0.01
  AnimationSteps = 200
  Distance = 0
  Revolutions = -0.25
FEATURE [App::DocumentObjectGroupPython] SimpleGroup018  # scripted group (container) (typed FeaturePython)
  AnimationStepTime = 0.01
  AnimationSteps = 200
  Distance = 100
  Revolutions = 0
FEATURE [App::DocumentObjectGroupPython] SimpleGroup019  # scripted group (container) (typed FeaturePython)
  AnimationStepTime = 0.01
  AnimationSteps = 200
  Distance = 2000
  Revolutions = 0
FEATURE [App::DocumentObjectGroupPython] SimpleGroup020  # scripted group (container) (typed FeaturePython)
  AnimationStepTime = 0.01
  AnimationSteps = 200
  Distance = 3100
  Revolutions = 0
FEATURE [App::DocumentObjectGroupPython] SimpleGroup021  # scripted group (container) (typed FeaturePython)
  AnimationStepTime = 0.01
  AnimationSteps = 200
  Distance = 0
  Revolutions = -0.25
FEATURE [App::DocumentObjectGroupPython] SimpleGroup022  # scripted group (container) (typed FeaturePython)
  AnimationStepTime = 0.01
  AnimationSteps = 200
  Distance = 100
  Revolutions = 0
FEATURE [App::DocumentObjectGroupPython] SimpleGroup023  # scripted group (container) (typed FeaturePython)
  AnimationStepTime = 0.01
  AnimationSteps = 200
  Distance = 0
  Revolutions = 0.25
FEATURE [App::DocumentObjectGroupPython] SimpleGroup024  # scripted group (container) (typed FeaturePython)
  AnimationStepTime = 0.01
  AnimationSteps = 200
  Distance = 100
  Revolutions = 0
FEATURE [App::DocumentObjectGroupPython] SimpleGroup025  # scripted group (container) (typed FeaturePython)
  AnimationStepTime = 0.01
  AnimationSteps = 200
  Distance = 0
  Revolutions = -0.25
FEATURE [App::DocumentObjectGroupPython] SimpleGroup026  # scripted group (container) (typed FeaturePython)
  AnimationStepTime = 0.01
  AnimationSteps = 200
  Distance = 100
  Revolutions = 0
FEATURE [App::DocumentObjectGroupPython] SimpleGroup027  # scripted group (container) (typed FeaturePython)
  AnimationStepTime = 0.01
  AnimationSteps = 200
  Distance = 0
  Revolutions = -0.25
FEATURE [App::DocumentObjectGroupPython] SimpleGroup028  # scripted group (container) (typed FeaturePython)
  AnimationStepTime = 0.01
  AnimationSteps = 200
  Distance = 100
  Revolutions = 0
FEATURE [App::DocumentObjectGroupPython] SimpleGroup029  # scripted group (container) (typed FeaturePython)
  AnimationStepTime = 0.01
  AnimationSteps = 200
  Distance = 1300
  Revolutions = 0
FEATURE [App::DocumentObjectGroupPython] SimpleGroup030  # scripted group (container) (typed FeaturePython)
  AnimationStepTime = 0.01
  AnimationSteps = 200
  Distance = 0
  Revolutions = -0.25
FEATURE [App::DocumentObjectGroupPython] SimpleGroup031  # scripted group (container) (typed FeaturePython)
  AnimationStepTime = 0.01
  AnimationSteps = 200
  Distance = 0
  Revolutions = 0.25
FEATURE [App::DocumentObjectGroupPython] SimpleGroup032  # scripted group (container) (typed FeaturePython)
  AnimationStepTime = 0.01
  AnimationSteps = 200
  Distance = 2000
  Revolutions = 0
FEATURE [App::DocumentObjectGroupPython] SimpleGroup033  # scripted group (container) (typed FeaturePython)
  AnimationStepTime = 0.01
  AnimationSteps = 200
  Distance = 50
  Revolutions = 0
FEATURE [App::DocumentObjectGroupPython] SimpleGroup034  # scripted group (container) (typed FeaturePython)
  AnimationStepTime = 0.01
  AnimationSteps = 200
  Distance = 0
  Revolutions = 0.25
FEATURE [App::DocumentObjectGroupPython] SimpleGroup035  # scripted group (container) (typed FeaturePython)
  AnimationStepTime = 0.01
  AnimationSteps = 200
  Distance = 2000
  Revolutions = 0
FEATURE [App::DocumentObjectGroupPython] SimpleGroup036  # scripted group (container) (typed FeaturePython)
  AnimationStepTime = 0.01
  AnimationSteps = 200
  Distance = 50
  Revolutions = 0
FEATURE [App::DocumentObjectGroupPython] SimpleGroup037  # scripted group (container) (typed FeaturePython)
  AnimationStepTime = 0.01
  AnimationSteps = 200
  Distance = 0
  Revolutions = 0.25
FEATURE [App::DocumentObjectGroupPython] SimpleGroup038  # scripted group (container) (typed FeaturePython)
  AnimationStepTime = 0.01
  AnimationSteps = 200
  Distance = 2000
  Revolutions = 0
FEATURE [App::DocumentObjectGroupPython] SimpleGroup039  # scripted group (container) (typed FeaturePython)
  AnimationStepTime = 0.01
  AnimationSteps = 50
  Distance = 50
  Revolutions = 0
FEATURE [App::DocumentObjectGroupPython] SimpleGroup040 .. SimpleGroup044  x5 (patterned run collapsed; names and placements below)
  AnimationStepTime = 0.01
  AnimationSteps = 200
  Distance = 0
  Revolutions = 0.25
FEATURE [TechDraw::DrawSVGTemplate] Template
  Height = 297
  Orientation = 1
  Width = 420
FEATURE [TechDraw::DrawViewPart] View
  CoarseView = false
  Direction = (0,1,0)
  Focus = 100
  HardHidden = false
  IsoCount = 0
  IsoHidden = false
  IsoVisible = false
  LockPosition = false
  Perspective = false
  Rotation = 0
  Scale = 0.15
  ScaleType = 0
  SeamHidden = false
  SeamVisible = true
  SmoothHidden = false
  SmoothVisible = true
  Source = -> [Body]
  X = 200.58
  XDirection = (1,0,0)
  Y = 178.5
FEATURE [TechDraw::DrawViewDimension] Dimension
  Arbitrary = false
  ArbitraryTolerances = false
  EqualTolerance = true
  FormatSpec = %.2f
  FormatSpecOverTolerance = %+.2f
  FormatSpecUnderTolerance = %+.2f
  Inverted = false
  LockPosition = false
  MeasureType = 1
  OverTolerance = 0
  References2D = -> [View]
  Rotation = 0
  ScaleType = 0
  TheoreticalExact = false
  Type = 1
  UnderTolerance = 0
  X = 0.939646
  Y = 69.1707
FEATURE [TechDraw::DrawViewDimension] Dimension001
  Arbitrary = false
  ArbitraryTolerances = false
  EqualTolerance = true
  FormatSpec = %.2f
  FormatSpecOverTolerance = %+.2f
  FormatSpecUnderTolerance = %+.2f
  Inverted = false
  LockPosition = false
  MeasureType = 1
  OverTolerance = 0
  References2D = -> [View]
  Rotation = 0
  ScaleType = 0
  TheoreticalExact = false
  Type = 1
  UnderTolerance = 0
  X = -135.55
  Y = 26.4905
FEATURE [TechDraw::DrawViewDimension] Dimension002
  Arbitrary = false
  ArbitraryTolerances = false
  EqualTolerance = true
  FormatSpec = %.2f
  FormatSpecOverTolerance = %+.2f
  FormatSpecUnderTolerance = %+.2f
  Inverted = false
  LockPosition = false
  MeasureType = 1
  OverTolerance = 0
  References2D = -> [View]
  Rotation = 0
  ScaleType = 0
  TheoreticalExact = false
  Type = 1
  UnderTolerance = 0
  X = -126.38
  Y = 34.9769
FEATURE [TechDraw::DrawViewDimension] Dimension009
  Arbitrary = false
  ArbitraryTolerances = false
  EqualTolerance = true
  FormatSpec = %.2f
  FormatSpecOverTolerance = %+.2f
  FormatSpecUnderTolerance = %+.2f
  Inverted = false
  LockPosition = false
  MeasureType = 1
  OverTolerance = 0
  References2D = -> [View]
  Rotation = 0
  ScaleType = 0
  TheoreticalExact = false
  Type = 2
  UnderTolerance = 0
  X = -181.93
  Y = 22.6799
FEATURE [TechDraw::DrawViewDimension] Dimension010
  Arbitrary = false
  ArbitraryTolerances = false
  EqualTolerance = true
  FormatSpec = %.2f
  FormatSpecOverTolerance = %+.2f
  FormatSpecUnderTolerance = %+.2f
  Inverted = false
  LockPosition = false
  MeasureType = 1
  OverTolerance = 0
  References2D = -> [View]
  Rotation = 0
  ScaleType = 0
  TheoreticalExact = false
  Type = 2
  UnderTolerance = 0
  X = -176.257
  Y = 22.5839
FEATURE [TechDraw::DrawViewDimension] Dimension011
  Arbitrary = false
  ArbitraryTolerances = false
  EqualTolerance = true
  FormatSpec = %.2f
  FormatSpecOverTolerance = %+.2f
  FormatSpecUnderTolerance = %+.2f
  Inverted = false
  LockPosition = false
  MeasureType = 1
  OverTolerance = 0
  References2D = -> [View]
  Rotation = 0
  ScaleType = 0
  TheoreticalExact = false
  Type = 2
  UnderTolerance = 0
  X = -170.701
  Y = 22.478
FEATURE [TechDraw::DrawViewDimension] Dimension012
  Arbitrary = false
  ArbitraryTolerances = false
  EqualTolerance = true
  FormatSpec = %.2f
  FormatSpecOverTolerance = %+.2f
  FormatSpecUnderTolerance = %+.2f
  Inverted = false
  LockPosition = false
  MeasureType = 1
  OverTolerance = 0
  References2D = -> [View]
  Rotation = 0
  ScaleType = 0
  TheoreticalExact = false
  Type = 2
  UnderTolerance = 0
  X = -165.243
  Y = 22.4385
FEATURE [TechDraw::DrawViewDimension] Dimension013
  Arbitrary = false
  ArbitraryTolerances = false
  EqualTolerance = true
  FormatSpec = %.2f
  FormatSpecOverTolerance = %+.2f
  FormatSpecUnderTolerance = %+.2f
  Inverted = false
  LockPosition = false
  MeasureType = 1
  OverTolerance = 0
  References2D = -> [View]
  Rotation = 0
  ScaleType = 0
  TheoreticalExact = false
  Type = 1
  UnderTolerance = 0
  X = -84.3708
  Y = 15.0247
FEATURE [TechDraw::DrawViewDimension] Dimension015
  Arbitrary = false
  ArbitraryTolerances = false
  EqualTolerance = true
  FormatSpec = %.2f
  FormatSpecOverTolerance = %+.2f
  FormatSpecUnderTolerance = %+.2f
  Inverted = false
  LockPosition = false
  MeasureType = 1
  OverTolerance = 0
  References2D = -> [View]
  Rotation = 0
  ScaleType = 0
  TheoreticalExact = false
  Type = 1
  UnderTolerance = 0
  X = -124.631
  Y = -152.292
FEATURE [TechDraw::DrawViewDimension] Dimension016
  Arbitrary = false
  ArbitraryTolerances = false
  EqualTolerance = true
  FormatSpec = %.2f
  FormatSpecOverTolerance = %+.2f
  FormatSpecUnderTolerance = %+.2f
  Inverted = false
  LockPosition = false
  MeasureType = 1
  OverTolerance = 0
  References2D = -> [View]
  Rotation = 0
  ScaleType = 0
  TheoreticalExact = false
  Type = 1
  UnderTolerance = 0
  X = -111.172
  Y = -143.752
FEATURE [TechDraw::DrawViewDimension] Dimension017
  Arbitrary = false
  ArbitraryTolerances = false
  EqualTolerance = true
  FormatSpec = %.2f
  FormatSpecOverTolerance = %+.2f
  FormatSpecUnderTolerance = %+.2f
  Inverted = false
  LockPosition = false
  MeasureType = 1
  OverTolerance = 0
  References2D = -> [View]
  Rotation = 0
  ScaleType = 0
  TheoreticalExact = false
  Type = 1
  UnderTolerance = 0
  X = -98.9298
  Y = -135.651
FEATURE [TechDraw::DrawViewDimension] Dimension018
  Arbitrary = false
  ArbitraryTolerances = false
  EqualTolerance = true
  FormatSpec = %.2f
  FormatSpecOverTolerance = %+.2f
  FormatSpecUnderTolerance = %+.2f
  Inverted = false
  LockPosition = false
  MeasureType = 1
  OverTolerance = 0
  References2D = -> [View]
  Rotation = 0
  ScaleType = 0
  TheoreticalExact = false
  Type = 1
  UnderTolerance = 0
  X = -75.1145
  Y = -128.366
FEATURE [TechDraw::DrawViewDimension] Dimension019
  Arbitrary = false
  ArbitraryTolerances = false
  EqualTolerance = true
  FormatSpec = %.2f
  FormatSpecOverTolerance = %+.2f
  FormatSpecUnderTolerance = %+.2f
  Inverted = false
  LockPosition = false
  MeasureType = 1
  OverTolerance = 0
  References2D = -> [View]
  Rotation = 0
  ScaleType = 0
  TheoreticalExact = false
  Type = 1
  UnderTolerance = 0
  X = -61.7272
  Y = -120.258
FEATURE [TechDraw::DrawViewDimension] Dimension020
  Arbitrary = false
  ArbitraryTolerances = false
  EqualTolerance = true
  FormatSpec = %.2f
  FormatSpecOverTolerance = %+.2f
  FormatSpecUnderTolerance = %+.2f
  Inverted = false
  LockPosition = false
  MeasureType = 1
  OverTolerance = 0
  References2D = -> [View]
  Rotation = 0
  ScaleType = 0
  TheoreticalExact = false
  Type = 1
  UnderTolerance = 0
  X = -49.7516
  Y = -113.348
FEATURE [TechDraw::DrawViewDimension] Dimension021
  Arbitrary = false
  ArbitraryTolerances = false
  EqualTolerance = true
  FormatSpec = %.2f
  FormatSpecOverTolerance = %+.2f
  FormatSpecUnderTolerance = %+.2f
  Inverted = false
  LockPosition = false
  MeasureType = 1
  OverTolerance = 0
  References2D = -> [View]
  Rotation = 0
  ScaleType = 0
  TheoreticalExact = false
  Type = 1
  UnderTolerance = 0
  X = -24.4879
  Y = -106.164
FEATURE [TechDraw::DrawViewDimension] Dimension022
  Arbitrary = false
  ArbitraryTolerances = false
  EqualTolerance = true
  FormatSpec = %.2f
  FormatSpecOverTolerance = %+.2f
  FormatSpecUnderTolerance = %+.2f
  Inverted = false
  LockPosition = false
  MeasureType = 1
  OverTolerance = 0
  References2D = -> [View]
  Rotation = 0
  ScaleType = 0
  TheoreticalExact = false
  Type = 1
  UnderTolerance = 0
  X = -11.8737
  Y = -99.4211
FEATURE [TechDraw::DrawViewDimension] Dimension023
  Arbitrary = false
  ArbitraryTolerances = false
  EqualTolerance = true
  FormatSpec = %.2f
  FormatSpecOverTolerance = %+.2f
  FormatSpecUnderTolerance = %+.2f
  Inverted = false
  LockPosition = false
  MeasureType = 1
  OverTolerance = 0
  References2D = -> [View]
  Rotation = 0
  ScaleType = 0
  TheoreticalExact = false
  Type = 1
  UnderTolerance = 0
  X = 1.03011
  Y = -91.7243
FEATURE [TechDraw::DrawViewDimension] Dimension024
  Arbitrary = false
  ArbitraryTolerances = false
  EqualTolerance = true
  FormatSpec = %.2f
  FormatSpecOverTolerance = %+.2f
  FormatSpecUnderTolerance = %+.2f
  Inverted = false
  LockPosition = false
  MeasureType = 1
  OverTolerance = 0
  References2D = -> [View]
  Rotation = 0
  ScaleType = 0
  TheoreticalExact = false
  Type = 1
  UnderTolerance = 0
  X = 26.3552
  Y = -84.7478
FEATURE [TechDraw::DrawViewDimension] Dimension025
  Arbitrary = false
  ArbitraryTolerances = false
  EqualTolerance = true
  FormatSpec = %.2f
  FormatSpecOverTolerance = %+.2f
  FormatSpecUnderTolerance = %+.2f
  Inverted = false
  LockPosition = false
  MeasureType = 1
  OverTolerance = 0
  References2D = -> [View]
  Rotation = 0
  ScaleType = 0
  TheoreticalExact = false
  Type = 1
  UnderTolerance = 0
  X = 38.4663
  Y = -76.9057
FEATURE [TechDraw::DrawViewDimension] Dimension026
  Arbitrary = false
  ArbitraryTolerances = false
  EqualTolerance = true
  FormatSpec = %.2f
  FormatSpecOverTolerance = %+.2f
  FormatSpecUnderTolerance = %+.2f
  Inverted = false
  LockPosition = false
  MeasureType = 1
  OverTolerance = 0
  References2D = -> [View]
  Rotation = 0
  ScaleType = 0
  TheoreticalExact = false
  Type = 1
  UnderTolerance = 0
  X = 50.9443
  Y = -68.8336
FEATURE [TechDraw::DrawViewDimension] Dimension027
  Arbitrary = false
  ArbitraryTolerances = false
  EqualTolerance = true
  FormatSpec = %.2f
  FormatSpecOverTolerance = %+.2f
  FormatSpecUnderTolerance = %+.2f
  Inverted = false
  LockPosition = false
  MeasureType = 1
  OverTolerance = 0
  References2D = -> [View]
  Rotation = 0
  ScaleType = 0
  TheoreticalExact = false
  Type = 1
  UnderTolerance = 0
  X = 75.6093
  Y = -62.0294
FEATURE [TechDraw::DrawViewDimension] Dimension028
  Arbitrary = false
  ArbitraryTolerances = false
  EqualTolerance = true
  FormatSpec = %.2f
  FormatSpecOverTolerance = %+.2f
  FormatSpecUnderTolerance = %+.2f
  Inverted = false
  LockPosition = false
  MeasureType = 1
  OverTolerance = 0
  References2D = -> [View]
  Rotation = 0
  ScaleType = 0
  TheoreticalExact = false
  Type = 1
  UnderTolerance = 0
  X = 87.8695
  Y = -54.5099
FEATURE [TechDraw::DrawViewDimension] Dimension029
  Arbitrary = false
  ArbitraryTolerances = false
  EqualTolerance = true
  FormatSpec = %.2f
  FormatSpecOverTolerance = %+.2f
  FormatSpecUnderTolerance = %+.2f
  Inverted = false
  LockPosition = false
  MeasureType = 1
  OverTolerance = 0
  References2D = -> [View]
  Rotation = 0
  ScaleType = 0
  TheoreticalExact = false
  Type = 1
  UnderTolerance = 0
  X = 100.39
  Y = -46.6054
FEATURE [TechDraw::DrawViewDimension] Dimension030
  Arbitrary = false
  ArbitraryTolerances = false
  EqualTolerance = true
  FormatSpec = %.2f
  FormatSpecOverTolerance = %+.2f
  FormatSpecUnderTolerance = %+.2f
  Inverted = false
  LockPosition = false
  MeasureType = 1
  OverTolerance = 0
  References2D = -> [View]
  Rotation = 0
  ScaleType = 0
  TheoreticalExact = false
  Type = 1
  UnderTolerance = 0
  X = 125.383
  Y = -39.6188
FEATURE [TechDraw::DrawViewDimension] Dimension031
  Arbitrary = false
  ArbitraryTolerances = false
  EqualTolerance = true
  FormatSpec = %.2f
  FormatSpecOverTolerance = %+.2f
  FormatSpecUnderTolerance = %+.2f
  Inverted = false
  LockPosition = false
  MeasureType = 1
  OverTolerance = 0
  References2D = -> [View]
  Rotation = 0
  ScaleType = 0
  TheoreticalExact = false
  Type = 1
  UnderTolerance = 0
  X = 138.779
  Y = -31.9918
FEATURE [TechDraw::DrawViewDimension] Dimension032
  Arbitrary = false
  ArbitraryTolerances = false
  EqualTolerance = true
  FormatSpec = %.2f
  FormatSpecOverTolerance = %+.2f
  FormatSpecUnderTolerance = %+.2f
  Inverted = false
  LockPosition = false
  MeasureType = 1
  OverTolerance = 0
  References2D = -> [View]
  Rotation = 0
  ScaleType = 0
  TheoreticalExact = false
  Type = 1
  UnderTolerance = 0
  X = 152.019
  Y = -23.7622
FEATURE [TechDraw::DrawViewDimension] Dimension033
  Arbitrary = false
  ArbitraryTolerances = false
  EqualTolerance = true
  FormatSpec = ⌀%.2f
  FormatSpecOverTolerance = %+.2f
  FormatSpecUnderTolerance = %+.2f
  Inverted = false
  LockPosition = false
  MeasureType = 1
  OverTolerance = 0
  References2D = -> [View]
  Rotation = 0
  ScaleType = 0
  TheoreticalExact = false
  Type = 5
  UnderTolerance = 0
  X = -123.847
  Y = 18.2977
FEATURE [TechDraw::DrawViewDimension] Dimension034
  Arbitrary = false
  ArbitraryTolerances = false
  EqualTolerance = true
  FormatSpec = %.2f
  FormatSpecOverTolerance = %+.2f
  FormatSpecUnderTolerance = %+.2f
  Inverted = false
  LockPosition = false
  MeasureType = 1
  OverTolerance = 0
  References2D = -> [View]
  Rotation = 0
  ScaleType = 0
  TheoreticalExact = false
  Type = 1
  UnderTolerance = 0
  X = -101.026
  Y = 41.0614
FEATURE [TechDraw::DrawViewDimension] Dimension035
  Arbitrary = false
  ArbitraryTolerances = false
  EqualTolerance = true
  FormatSpec = %.2f
  FormatSpecOverTolerance = %+.2f
  FormatSpecUnderTolerance = %+.2f
  Inverted = false
  LockPosition = false
  MeasureType = 1
  OverTolerance = 0
  References2D = -> [View]
  Rotation = 0
  ScaleType = 0
  TheoreticalExact = false
  Type = 1
  UnderTolerance = 0
  X = -73.1496
  Y = 47.3418
FEATURE [TechDraw::DrawViewDimension] Dimension036
  Arbitrary = false
  ArbitraryTolerances = false
  EqualTolerance = true
  FormatSpec = %.2f
  FormatSpecOverTolerance = %+.2f
  FormatSpecUnderTolerance = %+.2f
  Inverted = false
  LockPosition = false
  MeasureType = 1
  OverTolerance = 0
  References2D = -> [View]
  Rotation = 0
  ScaleType = 0
  TheoreticalExact = false
  Type = 1
  UnderTolerance = 0
  X = -46.4135
  Y = 53.4497
FEATURE [TechDraw::DrawViewDimension] Dimension037
  Arbitrary = false
  ArbitraryTolerances = false
  EqualTolerance = true
  FormatSpec = %.2f
  FormatSpecOverTolerance = %+.2f
  FormatSpecUnderTolerance = %+.2f
  Inverted = false
  LockPosition = false
  MeasureType = 1
  OverTolerance = 0
  References2D = -> [View]
  Rotation = 0
  ScaleType = 0
  TheoreticalExact = false
  Type = 1
  UnderTolerance = 0
  X = -23.8741
  Y = 60.0363
FEATURE [TechDraw::DrawViewSection] SectionView  label="Section A - A"
  BaseView = -> View
  CoarseView = false
  CutSurfaceDisplay = 2
  Direction = (-1,0,0)
  FileGeomPattern = <userpath>/AppData/Local/Programs/FreeCAD 0.19/data/Mod/TechDraw/PAT/FCPAT.pat
  FileHatchPattern = <userpath>/AppData/Local/Programs/FreeCAD 0.19/data/Mod/TechDraw/Patterns/simple.svg
  Focus = 100
  FuseBeforeCut = false
  HardHidden = false
  HatchScale = 1
  IsoCount = 0
  IsoHidden = false
  IsoVisible = false
  LockPosition = false
  NameGeomPattern = Diamond
  Perspective = false
  Rotation = 0
  Scale = 0.15
  ScaleType = 0
  SeamHidden = false
  SeamVisible = true
  SectionDirection = 0
  SectionNormal = (-1,0,0)
  SectionOrigin = (880,300,0)
  SectionSymbol = A
  SmoothHidden = false
  SmoothVisible = true
  Source = -> [Body]
  X = 380
  XDirection = (0,1,0)
  Y = 178.5
FEATURE [TechDraw::DrawViewDimension] Dimension038
  Arbitrary = false
  ArbitraryTolerances = false
  EqualTolerance = true
  FormatSpec = %.2f
  FormatSpecOverTolerance = %+.2f
  FormatSpecUnderTolerance = %+.2f
  Inverted = false
  LockPosition = false
  MeasureType = 1
  OverTolerance = 0
  References2D = -> [SectionView]
  Rotation = 0
  ScaleType = 0
  TheoreticalExact = false
  Type = 1
  UnderTolerance = 0
  X = 12.3066
  Y = 16.3968
FEATURE [TechDraw::DrawSVGTemplate] Template001
  Height = 297
  Orientation = 1
  Width = 420
FEATURE [TechDraw::DrawViewPart] View001
  CoarseView = false
  Direction = (1,0,0)
  Focus = 100
  HardHidden = false
  IsoCount = 0
  IsoHidden = false
  IsoVisible = false
  LockPosition = false
  Perspective = false
  Rotation = 0
  Scale = 0.15
  ScaleType = 0
  SeamHidden = false
  SeamVisible = true
  SmoothHidden = false
  SmoothVisible = true
  Source = -> [Body013]
  X = 210
  XDirection = (1,1,0)
  Y = 128.5
FEATURE [TechDraw::DrawViewDimension] Dimension039
  Arbitrary = false
  ArbitraryTolerances = false
  EqualTolerance = true
  FormatSpec = %.2f
  FormatSpecOverTolerance = %+.2f
  FormatSpecUnderTolerance = %+.2f
  Inverted = false
  LockPosition = false
  MeasureType = 1
  OverTolerance = 0
  References2D = -> [View001]
  Rotation = 0
  ScaleType = 0
  TheoreticalExact = false
  Type = 1
  UnderTolerance = 0
  X = 9.80048
  Y = 116.828
FEATURE [TechDraw::DrawViewDimension] Dimension040
  Arbitrary = false
  ArbitraryTolerances = false
  EqualTolerance = true
  FormatSpec = %.2f
  FormatSpecOverTolerance = %+.2f
  FormatSpecUnderTolerance = %+.2f
  Inverted = false
  LockPosition = false
  MeasureType = 1
  OverTolerance = 0
  References2D = -> [View001]
  Rotation = 0
  ScaleType = 0
  TheoreticalExact = false
  Type = 1
  UnderTolerance = 0
  X = 113.321
  Y = 110.547
FEATURE [TechDraw::DrawViewDimension] Dimension041
  Arbitrary = false
  ArbitraryTolerances = false
  EqualTolerance = true
  FormatSpec = %.2f
  FormatSpecOverTolerance = %+.2f
  FormatSpecUnderTolerance = %+.2f
  Inverted = false
  LockPosition = false
  MeasureType = 1
  OverTolerance = 0
  References2D = -> [View001]
  Rotation = 0
  ScaleType = 0
  TheoreticalExact = false
  Type = 1
  UnderTolerance = 0
  X = 112.576
  Y = 104.917
FEATURE [TechDraw::DrawViewDimension] Dimension042
  Arbitrary = false
  ArbitraryTolerances = false
  EqualTolerance = true
  FormatSpec = %.2f
  FormatSpecOverTolerance = %+.2f
  FormatSpecUnderTolerance = %+.2f
  Inverted = false
  LockPosition = false
  MeasureType = 1
  OverTolerance = 0
  References2D = -> [View001]
  Rotation = 0
  ScaleType = 0
  TheoreticalExact = false
  Type = 1
  UnderTolerance = 0
  X = 112.14
  Y = 99.1999
FEATURE [TechDraw::DrawViewDimension] Dimension043
  Arbitrary = false
  ArbitraryTolerances = false
  EqualTolerance = true
  FormatSpec = %.2f
  FormatSpecOverTolerance = %+.2f
  FormatSpecUnderTolerance = %+.2f
  Inverted = false
  LockPosition = false
  MeasureType = 1
  OverTolerance = 0
  References2D = -> [View001]
  Rotation = 0
  ScaleType = 0
  TheoreticalExact = false
  Type = 1
  UnderTolerance = 0
  X = 112.532
  Y = 93.6292
FEATURE [TechDraw::DrawViewDimension] Dimension044
  Arbitrary = false
  ArbitraryTolerances = false
  EqualTolerance = true
  FormatSpec = %.2f
  FormatSpecOverTolerance = %+.2f
  FormatSpecUnderTolerance = %+.2f
  Inverted = false
  LockPosition = false
  MeasureType = 1
  OverTolerance = 0
  References2D = -> [View001]
  Rotation = 0
  ScaleType = 0
  TheoreticalExact = false
  Type = 1
  UnderTolerance = 0
  X = 111.99
  Y = 88.2291
FEATURE [TechDraw::DrawViewDimension] Dimension045
  Arbitrary = false
  ArbitraryTolerances = false
  EqualTolerance = true
  FormatSpec = %.2f
  FormatSpecOverTolerance = %+.2f
  FormatSpecUnderTolerance = %+.2f
  Inverted = false
  LockPosition = false
  MeasureType = 1
  OverTolerance = 0
  References2D = -> [View001]
  Rotation = 0
  ScaleType = 0
  TheoreticalExact = false
  Type = 1
  UnderTolerance = 0
  X = 112.189
  Y = 83.0256
FEATURE [TechDraw::DrawViewDimension] Dimension046
  Arbitrary = false
  ArbitraryTolerances = false
  EqualTolerance = true
  FormatSpec = %.2f
  FormatSpecOverTolerance = %+.2f
  FormatSpecUnderTolerance = %+.2f
  Inverted = false
  LockPosition = false
  MeasureType = 1
  OverTolerance = 0
  References2D = -> [View001]
  Rotation = 0
  ScaleType = 0
  TheoreticalExact = false
  Type = 1
  UnderTolerance = 0
  X = 112.04
  Y = 77.4215
FEATURE [TechDraw::DrawViewDimension] Dimension047
  Arbitrary = false
  ArbitraryTolerances = false
  EqualTolerance = true
  FormatSpec = %.2f
  FormatSpecOverTolerance = %+.2f
  FormatSpecUnderTolerance = %+.2f
  Inverted = false
  LockPosition = false
  MeasureType = 1
  OverTolerance = 0
  References2D = -> [View001]
  Rotation = 0
  ScaleType = 0
  TheoreticalExact = false
  Type = 1
  UnderTolerance = 0
  X = 112.301
  Y = 71.542
FEATURE [TechDraw::DrawViewDimension] Dimension048
  Arbitrary = false
  ArbitraryTolerances = false
  EqualTolerance = true
  FormatSpec = %.2f
  FormatSpecOverTolerance = %+.2f
  FormatSpecUnderTolerance = %+.2f
  Inverted = false
  LockPosition = false
  MeasureType = 1
  OverTolerance = 0
  References2D = -> [View001]
  Rotation = 0
  ScaleType = 0
  TheoreticalExact = false
  Type = 1
  UnderTolerance = 0
  X = 112.445
  Y = 66.2691
FEATURE [TechDraw::DrawViewDimension] Dimension049
  Arbitrary = false
  ArbitraryTolerances = false
  EqualTolerance = true
  FormatSpec = %.2f
  FormatSpecOverTolerance = %+.2f
  FormatSpecUnderTolerance = %+.2f
  Inverted = false
  LockPosition = false
  MeasureType = 1
  OverTolerance = 0
  References2D = -> [View001]
  Rotation = 0
  ScaleType = 0
  TheoreticalExact = false
  Type = 1
  UnderTolerance = 0
  X = 112.363
  Y = 60.4457
FEATURE [TechDraw::DrawViewDimension] Dimension050
  Arbitrary = false
  ArbitraryTolerances = false
  EqualTolerance = true
  FormatSpec = %.2f
  FormatSpecOverTolerance = %+.2f
  FormatSpecUnderTolerance = %+.2f
  Inverted = false
  LockPosition = false
  MeasureType = 1
  OverTolerance = 0
  References2D = -> [View001]
  Rotation = 0
  ScaleType = 0
  TheoreticalExact = false
  Type = 1
  UnderTolerance = 0
  X = 112.367
  Y = 54.437
FEATURE [TechDraw::DrawViewDimension] Dimension051
  Arbitrary = false
  ArbitraryTolerances = false
  EqualTolerance = true
  FormatSpec = %.2f
  FormatSpecOverTolerance = %+.2f
  FormatSpecUnderTolerance = %+.2f
  Inverted = false
  LockPosition = false
  MeasureType = 1
  OverTolerance = 0
  References2D = -> [View001]
  Rotation = 0
  ScaleType = 0
  TheoreticalExact = false
  Type = 1
  UnderTolerance = 0
  X = 112.361
  Y = 48.5961
FEATURE [TechDraw::DrawViewDimension] Dimension052
  Arbitrary = false
  ArbitraryTolerances = false
  EqualTolerance = true
  FormatSpec = %.2f
  FormatSpecOverTolerance = %+.2f
  FormatSpecUnderTolerance = %+.2f
  Inverted = false
  LockPosition = false
  MeasureType = 1
  OverTolerance = 0
  References2D = -> [View001]
  Rotation = 0
  ScaleType = 0
  TheoreticalExact = false
  Type = 1
  UnderTolerance = 0
  X = 111.66
  Y = 42.0047
FEATURE [TechDraw::DrawViewDimension] Dimension053
  Arbitrary = false
  ArbitraryTolerances = false
  EqualTolerance = true
  FormatSpec = %.2f
  FormatSpecOverTolerance = %+.2f
  FormatSpecUnderTolerance = %+.2f
  Inverted = false
  LockPosition = false
  MeasureType = 1
  OverTolerance = 0
  References2D = -> [View001]
  Rotation = 0
  ScaleType = 0
  TheoreticalExact = false
  Type = 1
  UnderTolerance = 0
  X = 111.591
  Y = 36.0782
FEATURE [TechDraw::DrawViewDimension] Dimension054
  Arbitrary = false
  ArbitraryTolerances = false
  EqualTolerance = true
  FormatSpec = ⌀%.2f
  FormatSpecOverTolerance = %+.2f
  FormatSpecUnderTolerance = %+.2f
  Inverted = false
  LockPosition = false
  MeasureType = 1
  OverTolerance = 0
  References2D = -> [View001]
  Rotation = 0
  ScaleType = 0
  TheoreticalExact = false
  Type = 5
  UnderTolerance = 0
  X = -61.8419
  Y = -15.4867
FEATURE [TechDraw::DrawViewDimension] Dimension055
  Arbitrary = false
  ArbitraryTolerances = false
  EqualTolerance = true
  FormatSpec = R%.2f
  FormatSpecOverTolerance = %+.2f
  FormatSpecUnderTolerance = %+.2f
  Inverted = false
  LockPosition = false
  MeasureType = 1
  OverTolerance = 0
  References2D = -> [View001]
  Rotation = 0
  ScaleType = 0
  TheoreticalExact = false
  Type = 4
  UnderTolerance = 0
  X = -31.0439
  Y = -15.1567
FEATURE [TechDraw::DrawViewDimension] Dimension056
  Arbitrary = false
  ArbitraryTolerances = false
  EqualTolerance = true
  FormatSpec = R%.2f
  FormatSpecOverTolerance = %+.2f
  FormatSpecUnderTolerance = %+.2f
  Inverted = false
  LockPosition = false
  MeasureType = 1
  OverTolerance = 0
  References2D = -> [View001]
  Rotation = 0
  ScaleType = 0
  TheoreticalExact = false
  Type = 4
  UnderTolerance = 0
  X = -23.9221
  Y = -15.1567
FEATURE [TechDraw::DrawViewDimension] Dimension057
  Arbitrary = false
  ArbitraryTolerances = false
  EqualTolerance = true
  FormatSpec = %.2f
  FormatSpecOverTolerance = %+.2f
  FormatSpecUnderTolerance = %+.2f
  Inverted = false
  LockPosition = false
  MeasureType = 1
  OverTolerance = 0
  References2D = -> [View001]
  Rotation = 0
  ScaleType = 0
  TheoreticalExact = false
  Type = 1
  UnderTolerance = 0
  X = -106.495
  Y = -20.372
FEATURE [TechDraw::DrawViewDimension] Dimension058
  Arbitrary = false
  ArbitraryTolerances = false
  EqualTolerance = true
  FormatSpec = %.2f
  FormatSpecOverTolerance = %+.2f
  FormatSpecUnderTolerance = %+.2f
  Inverted = false
  LockPosition = false
  MeasureType = 1
  OverTolerance = 0
  References2D = -> [View001]
  Rotation = 0
  ScaleType = 0
  TheoreticalExact = false
  Type = 2
  UnderTolerance = 0
  X = -136.285
  Y = 21.0815
FEATURE [TechDraw::DrawViewDimension] Dimension059
  Arbitrary = false
  ArbitraryTolerances = false
  EqualTolerance = true
  FormatSpec = %.2f
  FormatSpecOverTolerance = %+.2f
  FormatSpecUnderTolerance = %+.2f
  Inverted = false
  LockPosition = false
  MeasureType = 1
  OverTolerance = 0
  References2D = -> [View001]
  Rotation = 0
  ScaleType = 0
  TheoreticalExact = false
  Type = 2
  UnderTolerance = 0
  X = -129.92
  Y = 21.248
FEATURE [TechDraw::DrawViewSection] SectionView001  label="Section B - B"
  BaseView = -> View001
  CoarseView = false
  CutSurfaceDisplay = 2
  Direction = (0,-1,0)
  FileGeomPattern = <userpath>/AppData/Local/Programs/FreeCAD 0.19/data/Mod/TechDraw/PAT/FCPAT.pat
  FileHatchPattern = <userpath>/AppData/Local/Programs/FreeCAD 0.19/data/Mod/TechDraw/Patterns/simple.svg
  Focus = 100
  FuseBeforeCut = false
  HardHidden = false
  HatchScale = 1
  IsoCount = 0
  IsoHidden = false
  IsoVisible = false
  LockPosition = false
  NameGeomPattern = Diamond
  Perspective = false
  Rotation = 0
  Scale = 0.15
  ScaleType = 0
  SeamHidden = false
  SeamVisible = true
  SectionDirection = 0
  SectionNormal = (0,-1,0)
  SectionOrigin = (-666.66,480,0)
  SectionSymbol = B
  SmoothHidden = false
  SmoothVisible = true
  Source = -> [Body013]
  X = 350
  XDirection = (1,0,0)
  Y = 128.5
FEATURE [TechDraw::DrawViewDimension] Dimension060
  Arbitrary = false
  ArbitraryTolerances = false
  EqualTolerance = true
  FormatSpec = %.2f
  FormatSpecOverTolerance = %+.2f
  FormatSpecUnderTolerance = %+.2f
  Inverted = false
  LockPosition = false
  MeasureType = 1
  OverTolerance = 0
  References2D = -> [SectionView001]
  Rotation = 0
  ScaleType = 0
  TheoreticalExact = false
  Type = 1
  UnderTolerance = 0
  X = 18.6264
  Y = 19.3332
FEATURE [TechDraw::DrawSVGTemplate] Template002
  Height = 297
  Orientation = 1
  Width = 420
FEATURE [TechDraw::DrawViewPart] View002
  CoarseView = false
  Direction = (0,-1,0)
  Focus = 100
  HardHidden = false
  IsoCount = 0
  IsoHidden = false
  IsoVisible = false
  LockPosition = false
  Perspective = false
  Rotation = 0
  Scale = 0.15
  ScaleType = 0
  SeamHidden = false
  SeamVisible = true
  SmoothHidden = false
  SmoothVisible = true
  Source = -> [Body001]
  X = 210
  XDirection = (1,0,0)
  Y = 148.5
FEATURE [TechDraw::DrawViewDimension] Dimension061
  Arbitrary = false
  ArbitraryTolerances = false
  EqualTolerance = true
  FormatSpec = %.2f
  FormatSpecOverTolerance = %+.2f
  FormatSpecUnderTolerance = %+.2f
  Inverted = false
  LockPosition = false
  MeasureType = 1
  OverTolerance = 0
  References2D = -> [View002]
  Rotation = 0
  Scale = 0.15
  ScaleType = 0
  TheoreticalExact = false
  Type = 1
  UnderTolerance = 0
  X = 1.67781
  Y = 71.8795
FEATURE [TechDraw::DrawViewDimension] Dimension062
  Arbitrary = false
  ArbitraryTolerances = false
  EqualTolerance = true
  FormatSpec = %.2f
  FormatSpecOverTolerance = %+.2f
  FormatSpecUnderTolerance = %+.2f
  Inverted = false
  LockPosition = false
  MeasureType = 1
  OverTolerance = 0
  References2D = -> [View002]
  Rotation = 0
  Scale = 0.15
  ScaleType = 0
  TheoreticalExact = false
  Type = 1
  UnderTolerance = 0
  X = 123.968
  Y = 64.9592
FEATURE [TechDraw::DrawViewDimension] Dimension063
  Arbitrary = false
  ArbitraryTolerances = false
  EqualTolerance = true
  FormatSpec = %.2f
  FormatSpecOverTolerance = %+.2f
  FormatSpecUnderTolerance = %+.2f
  Inverted = false
  LockPosition = false
  MeasureType = 1
  OverTolerance = 0
  References2D = -> [View002]
  Rotation = 0
  Scale = 0.15
  ScaleType = 0
  TheoreticalExact = false
  Type = 1
  UnderTolerance = 0
  X = 123.83
  Y = 59.0251
FEATURE [TechDraw::DrawViewDimension] Dimension064
  Arbitrary = false
  ArbitraryTolerances = false
  EqualTolerance = true
  FormatSpec = %.2f
  FormatSpecOverTolerance = %+.2f
  FormatSpecUnderTolerance = %+.2f
  Inverted = false
  LockPosition = false
  MeasureType = 1
  OverTolerance = 0
  References2D = -> [View002]
  Rotation = 0
  Scale = 0.15
  ScaleType = 0
  TheoreticalExact = false
  Type = 1
  UnderTolerance = 0
  X = 123.731
  Y = 53.5871
FEATURE [TechDraw::DrawViewDimension] Dimension065
  Arbitrary = false
  ArbitraryTolerances = false
  EqualTolerance = true
  FormatSpec = %.2f
  FormatSpecOverTolerance = %+.2f
  FormatSpecUnderTolerance = %+.2f
  Inverted = false
  LockPosition = false
  MeasureType = 1
  OverTolerance = 0
  References2D = -> [View002]
  Rotation = 0
  Scale = 0.15
  ScaleType = 0
  TheoreticalExact = false
  Type = 1
  UnderTolerance = 0
  X = 123.725
  Y = 47.1954
FEATURE [TechDraw::DrawViewDimension] Dimension066
  Arbitrary = false
  ArbitraryTolerances = false
  EqualTolerance = true
  FormatSpec = %.2f
  FormatSpecOverTolerance = %+.2f
  FormatSpecUnderTolerance = %+.2f
  Inverted = false
  LockPosition = false
  MeasureType = 1
  OverTolerance = 0
  References2D = -> [View002]
  Rotation = 0
  Scale = 0.15
  ScaleType = 0
  TheoreticalExact = false
  Type = 1
  UnderTolerance = 0
  X = 123.463
  Y = 40.9439
FEATURE [TechDraw::DrawViewDimension] Dimension068
  Arbitrary = false
  ArbitraryTolerances = false
  EqualTolerance = true
  FormatSpec = %.2f
  FormatSpecOverTolerance = %+.2f
  FormatSpecUnderTolerance = %+.2f
  Inverted = false
  LockPosition = false
  MeasureType = 1
  OverTolerance = 0
  References2D = -> [View002]
  Rotation = 0
  Scale = 0.15
  ScaleType = 0
  TheoreticalExact = false
  Type = 2
  UnderTolerance = 0
  X = -191.519
  Y = 29.8048
FEATURE [TechDraw::DrawViewDimension] Dimension069
  Arbitrary = false
  ArbitraryTolerances = false
  EqualTolerance = true
  FormatSpec = %.2f
  FormatSpecOverTolerance = %+.2f
  FormatSpecUnderTolerance = %+.2f
  Inverted = false
  LockPosition = false
  MeasureType = 1
  OverTolerance = 0
  References2D = -> [View002]
  Rotation = 0
  Scale = 0.15
  ScaleType = 0
  TheoreticalExact = false
  Type = 2
  UnderTolerance = 0
  X = -185.518
  Y = 29.6054
FEATURE [TechDraw::DrawViewDimension] Dimension070
  Arbitrary = false
  ArbitraryTolerances = false
  EqualTolerance = true
  FormatSpec = %.2f
  FormatSpecOverTolerance = %+.2f
  FormatSpecUnderTolerance = %+.2f
  Inverted = false
  LockPosition = false
  MeasureType = 1
  OverTolerance = 0
  References2D = -> [View002]
  Rotation = 0
  Scale = 0.15
  ScaleType = 0
  TheoreticalExact = false
  Type = 2
  UnderTolerance = 0
  X = -179.917
  Y = 29.406
FEATURE [TechDraw::DrawViewDimension] Dimension071
  Arbitrary = false
  ArbitraryTolerances = false
  EqualTolerance = true
  FormatSpec = %.2f
  FormatSpecOverTolerance = %+.2f
  FormatSpecUnderTolerance = %+.2f
  Inverted = false
  LockPosition = false
  MeasureType = 1
  OverTolerance = 0
  References2D = -> [View002]
  Rotation = 0
  Scale = 0.15
  ScaleType = 0
  TheoreticalExact = false
  Type = 2
  UnderTolerance = 0
  X = -173.915
  Y = 29.6066
FEATURE [TechDraw::DrawViewDimension] Dimension072
  Arbitrary = false
  ArbitraryTolerances = false
  EqualTolerance = true
  FormatSpec = %.2f
  FormatSpecOverTolerance = %+.2f
  FormatSpecUnderTolerance = %+.2f
  Inverted = false
  LockPosition = false
  MeasureType = 1
  OverTolerance = 0
  References2D = -> [View002]
  Rotation = 0
  Scale = 0.15
  ScaleType = 0
  TheoreticalExact = false
  Type = 2
  UnderTolerance = 0
  X = -168.114
  Y = 29.4072
FEATURE [TechDraw::DrawViewDimension] Dimension073
  Arbitrary = false
  ArbitraryTolerances = false
  EqualTolerance = true
  FormatSpec = %.2f
  FormatSpecOverTolerance = %+.2f
  FormatSpecUnderTolerance = %+.2f
  Inverted = false
  LockPosition = false
  MeasureType = 1
  OverTolerance = 0
  References2D = -> [View002]
  Rotation = 0
  Scale = 0.15
  ScaleType = 0
  TheoreticalExact = false
  Type = 1
  UnderTolerance = 0
  X = -138.355
  Y = -17.0322
FEATURE [TechDraw::DrawViewDimension] Dimension074
  Arbitrary = false
  ArbitraryTolerances = false
  EqualTolerance = true
  FormatSpec = %.2f
  FormatSpecOverTolerance = %+.2f
  FormatSpecUnderTolerance = %+.2f
  Inverted = false
  LockPosition = false
  MeasureType = 1
  OverTolerance = 0
  References2D = -> [View002]
  Rotation = 0
  Scale = 0.15
  ScaleType = 0
  TheoreticalExact = false
  Type = 1
  UnderTolerance = 0
  X = -89.2344
  Y = -16.9263
FEATURE [TechDraw::DrawViewSection] SectionView002  label="Section C - C"
  BaseView = -> View002
  CoarseView = false
  CutSurfaceDisplay = 2
  Direction = (-1,0,0)
  FileGeomPattern = <userpath>/AppData/Local/Programs/FreeCAD 0.19/data/Mod/TechDraw/PAT/FCPAT.pat
  FileHatchPattern = <userpath>/AppData/Local/Programs/FreeCAD 0.19/data/Mod/TechDraw/Patterns/simple.svg
  Focus = 100
  FuseBeforeCut = false
  HardHidden = false
  HatchScale = 1
  IsoCount = 0
  IsoHidden = false
  IsoVisible = false
  LockPosition = false
  NameGeomPattern = Diamond
  Perspective = false
  Rotation = 0
  Scale = 0.15
  ScaleType = 0
  SeamHidden = false
  SeamVisible = true
  SectionDirection = 0
  SectionNormal = (-1,0,0)
  SectionOrigin = (840,-598,0)
  SectionSymbol = C
  SmoothHidden = false
  SmoothVisible = true
  Source = -> [Body001]
  X = 380
  XDirection = (0,-1,0)
  Y = 148.5
FEATURE [TechDraw::DrawSVGTemplate] Template003
  Height = 297
  Orientation = 1
  Width = 420
FEATURE [TechDraw::DrawViewPart] View003
  CoarseView = false
  Direction = (1,0,0)
  Focus = 100
  HardHidden = false
  IsoCount = 0
  IsoHidden = false
  IsoVisible = false
  LockPosition = false
  Perspective = false
  Rotation = 0
  Scale = 0.15
  ScaleType = 0
  SeamHidden = false
  SeamVisible = true
  SmoothHidden = false
  SmoothVisible = true
  Source = -> [Body003]
  X = 190
  XDirection = (-0.707107,0.707107,0)
  Y = 148.5
FEATURE [TechDraw::DrawViewDimension] Dimension075
  Arbitrary = false
  ArbitraryTolerances = false
  EqualTolerance = true
  FormatSpec = %.2f
  FormatSpecOverTolerance = %+.2f
  FormatSpecUnderTolerance = %+.2f
  Inverted = false
  LockPosition = false
  MeasureType = 1
  OverTolerance = 0
  References2D = -> [View003]
  Rotation = 0
  ScaleType = 0
  TheoreticalExact = false
  Type = 1
  UnderTolerance = 0
  X = -0.84804
  Y = 59.1216
FEATURE [TechDraw::DrawViewDimension] Dimension076
  Arbitrary = false
  ArbitraryTolerances = false
  EqualTolerance = true
  FormatSpec = %.2f
  FormatSpecOverTolerance = %+.2f
  FormatSpecUnderTolerance = %+.2f
  Inverted = false
  LockPosition = false
  MeasureType = 1
  OverTolerance = 0
  References2D = -> [View]
  Rotation = 0
  ScaleType = 0
  TheoreticalExact = false
  Type = 2
  UnderTolerance = 0
  X = 199.81
  Y = 33.1267
FEATURE [TechDraw::DrawPage] Page  label="Long_Table_structure_Drawing"
  KeepUpdated = true
  NextBalloonIndex = 1
  ProjectionType = 0
  Template = -> Template
  Views = -> [View,Dimension,Dimension001,Dimension002,Dimension009,Dimension010,Dimension011,Dimension012,Dimension013,Dimension015,Dimension016,Dimension017,Dimension018,Dimension019,Dimension020,Dimension021,Dimension022,Dimension023,Dimension024,Dimension025,Dimension026,Dimension027,Dimension028,Dimension029,Dimension030,Dimension031,Dimension032,Dimension033,Dimension034,Dimension035,Dimension036,+4 more]
FEATURE [TechDraw::DrawViewDimension] Dimension077
  Arbitrary = false
  ArbitraryTolerances = false
  EqualTolerance = true
  FormatSpec = %.2f
  FormatSpecOverTolerance = %+.2f
  FormatSpecUnderTolerance = %+.2f
  Inverted = false
  LockPosition = false
  MeasureType = 1
  OverTolerance = 0
  References2D = -> [View001]
  Rotation = 0
  ScaleType = 0
  TheoreticalExact = false
  Type = 2
  UnderTolerance = 0
  X = 174.253
  Y = 26.1909
FEATURE [TechDraw::DrawViewDimension] Dimension078
  Arbitrary = false
  ArbitraryTolerances = false
  EqualTolerance = true
  FormatSpec = %.2f
  FormatSpecOverTolerance = %+.2f
  FormatSpecUnderTolerance = %+.2f
  Inverted = false
  LockPosition = false
  MeasureType = 1
  OverTolerance = 0
  References2D = -> [View003]
  Rotation = 0
  ScaleType = 0
  TheoreticalExact = false
  Type = 1
  UnderTolerance = 0
  X = 64.3352
  Y = 52.4303
FEATURE [TechDraw::DrawViewDimension] Dimension079
  Arbitrary = false
  ArbitraryTolerances = false
  EqualTolerance = true
  FormatSpec = %.2f
  FormatSpecOverTolerance = %+.2f
  FormatSpecUnderTolerance = %+.2f
  Inverted = false
  LockPosition = false
  MeasureType = 1
  OverTolerance = 0
  References2D = -> [View003]
  Rotation = 0
  ScaleType = 0
  TheoreticalExact = false
  Type = 1
  UnderTolerance = 0
  X = 64.6307
  Y = 46.8309
FEATURE [TechDraw::DrawViewDimension] Dimension080
  Arbitrary = false
  ArbitraryTolerances = false
  EqualTolerance = true
  FormatSpec = %.2f
  FormatSpecOverTolerance = %+.2f
  FormatSpecUnderTolerance = %+.2f
  Inverted = false
  LockPosition = false
  MeasureType = 1
  OverTolerance = 0
  References2D = -> [View003]
  Rotation = 0
  ScaleType = 0
  TheoreticalExact = false
  Type = 1
  UnderTolerance = 0
  X = 64.4549
  Y = 40.9507
FEATURE [TechDraw::DrawViewDimension] Dimension081
  Arbitrary = false
  ArbitraryTolerances = false
  EqualTolerance = true
  FormatSpec = %.2f
  FormatSpecOverTolerance = %+.2f
  FormatSpecUnderTolerance = %+.2f
  Inverted = false
  LockPosition = false
  MeasureType = 1
  OverTolerance = 0
  References2D = -> [SectionView002]
  Rotation = 0
  Scale = 0.15
  ScaleType = 0
  TheoreticalExact = false
  Type = 1
  UnderTolerance = 0
  X = 11.6754
  Y = 22.331
FEATURE [TechDraw::DrawViewDimension] Dimension082
  Arbitrary = false
  ArbitraryTolerances = false
  EqualTolerance = true
  FormatSpec = %.2f
  FormatSpecOverTolerance = %+.2f
  FormatSpecUnderTolerance = %+.2f
  Inverted = false
  LockPosition = false
  MeasureType = 1
  OverTolerance = 0
  References2D = -> [View002]
  Rotation = 0
  Scale = 0.15
  ScaleType = 0
  TheoreticalExact = false
  Type = 2
  UnderTolerance = 0
  X = 191.053
  Y = 30.6086
FEATURE [TechDraw::DrawPage] Page002  label="Inner_front_rear_frame_Drawing"
  KeepUpdated = true
  NextBalloonIndex = 1
  ProjectionType = 0
  Scale = 0.15
  Template = -> Template002
  Views = -> [View002,Dimension061,Dimension062,Dimension063,Dimension064,Dimension065,Dimension066,Dimension068,Dimension069,Dimension070,Dimension071,Dimension072,Dimension073,Dimension074,SectionView002,Dimension081,Dimension082]
FEATURE [TechDraw::DrawViewDimension] Dimension083
  Arbitrary = false
  ArbitraryTolerances = false
  EqualTolerance = true
  FormatSpec = %.2f
  FormatSpecOverTolerance = %+.2f
  FormatSpecUnderTolerance = %+.2f
  Inverted = false
  LockPosition = false
  MeasureType = 1
  OverTolerance = 0
  References2D = -> [View003]
  Rotation = 0
  ScaleType = 0
  TheoreticalExact = false
  Type = 1
  UnderTolerance = 0
  X = -33.5977
  Y = -20.105
FEATURE [TechDraw::DrawViewDimension] Dimension084
  Arbitrary = false
  ArbitraryTolerances = false
  EqualTolerance = true
  FormatSpec = %.2f
  FormatSpecOverTolerance = %+.2f
  FormatSpecUnderTolerance = %+.2f
  Inverted = false
  LockPosition = false
  MeasureType = 1
  OverTolerance = 0
  References2D = -> [View003]
  Rotation = 0
  ScaleType = 0
  TheoreticalExact = false
  Type = 1
  UnderTolerance = 0
  X = -78.2977
  Y = -20.3051
FEATURE [TechDraw::DrawViewDimension] Dimension085
  Arbitrary = false
  ArbitraryTolerances = false
  EqualTolerance = true
  FormatSpec = %.2f
  FormatSpecOverTolerance = %+.2f
  FormatSpecUnderTolerance = %+.2f
  Inverted = false
  LockPosition = false
  MeasureType = 1
  OverTolerance = 0
  References2D = -> [View003]
  Rotation = 0
  ScaleType = 0
  TheoreticalExact = false
  Type = 2
  UnderTolerance = 0
  X = -122.316
  Y = 20.6048
FEATURE [TechDraw::DrawViewDimension] Dimension086
  Arbitrary = false
  ArbitraryTolerances = false
  EqualTolerance = true
  FormatSpec = %.2f
  FormatSpecOverTolerance = %+.2f
  FormatSpecUnderTolerance = %+.2f
  Inverted = false
  LockPosition = false
  MeasureType = 1
  OverTolerance = 0
  References2D = -> [View003]
  Rotation = 0
  ScaleType = 0
  TheoreticalExact = false
  Type = 2
  UnderTolerance = 0
  X = -116.715
  Y = 20.6042
FEATURE [TechDraw::DrawViewDimension] Dimension087
  Arbitrary = false
  ArbitraryTolerances = false
  EqualTolerance = true
  FormatSpec = %.2f
  FormatSpecOverTolerance = %+.2f
  FormatSpecUnderTolerance = %+.2f
  Inverted = false
  LockPosition = false
  MeasureType = 1
  OverTolerance = 0
  References2D = -> [View003]
  Rotation = 0
  ScaleType = 0
  TheoreticalExact = false
  Type = 2
  UnderTolerance = 0
  X = -111.113
  Y = 20.4035
FEATURE [TechDraw::DrawViewDimension] Dimension088
  Arbitrary = false
  ArbitraryTolerances = false
  EqualTolerance = true
  FormatSpec = %.2f
  FormatSpecOverTolerance = %+.2f
  FormatSpecUnderTolerance = %+.2f
  Inverted = false
  LockPosition = false
  MeasureType = 1
  OverTolerance = 0
  References2D = -> [View003]
  Rotation = 0
  ScaleType = 0
  TheoreticalExact = false
  Type = 2
  UnderTolerance = 0
  X = -105.458
  Y = 20.2029
FEATURE [TechDraw::DrawViewDimension] Dimension089
  Arbitrary = false
  ArbitraryTolerances = false
  EqualTolerance = true
  FormatSpec = %.2f
  FormatSpecOverTolerance = %+.2f
  FormatSpecUnderTolerance = %+.2f
  Inverted = false
  LockPosition = false
  MeasureType = 1
  OverTolerance = 0
  References2D = -> [View001]
  Rotation = 0
  ScaleType = 0
  TheoreticalExact = false
  Type = 2
  UnderTolerance = 0
  X = -123.833
  Y = 21.2428
FEATURE [TechDraw::DrawViewDimension] Dimension090
  Arbitrary = false
  ArbitraryTolerances = false
  EqualTolerance = true
  FormatSpec = %.2f
  FormatSpecOverTolerance = %+.2f
  FormatSpecUnderTolerance = %+.2f
  Inverted = false
  LockPosition = false
  MeasureType = 1
  OverTolerance = 0
  References2D = -> [View001]
  Rotation = 0
  ScaleType = 0
  TheoreticalExact = false
  Type = 2
  UnderTolerance = 0
  X = -116.844
  Y = 21.4699
FEATURE [TechDraw::DrawViewDimension] Dimension091
  Arbitrary = false
  ArbitraryTolerances = false
  EqualTolerance = true
  FormatSpec = %.2f
  FormatSpecOverTolerance = %+.2f
  FormatSpecUnderTolerance = %+.2f
  Inverted = false
  LockPosition = false
  MeasureType = 1
  OverTolerance = 0
  References2D = -> [View001]
  Rotation = 0
  ScaleType = 0
  TheoreticalExact = false
  Type = 2
  UnderTolerance = 0
  X = -109.539
  Y = 21.7569
FEATURE [TechDraw::DrawPage] Page001  label="Short_Table_structure_Drawing"
  KeepUpdated = true
  NextBalloonIndex = 1
  ProjectionType = 0
  Template = -> Template001
  Views = -> [View001,Dimension039,Dimension040,Dimension041,Dimension042,Dimension043,Dimension044,Dimension045,Dimension046,Dimension047,Dimension048,Dimension049,Dimension050,Dimension051,Dimension052,Dimension053,Dimension054,Dimension055,Dimension056,Dimension057,Dimension058,Dimension059,SectionView001,Dimension060,Dimension077,Dimension089,Dimension090,Dimension091]
FEATURE [TechDraw::DrawViewSection] SectionView003  label="Section D - D"
  BaseView = -> View003
  CoarseView = false
  CutSurfaceDisplay = 2
  Direction = (0,-1,0)
  FileGeomPattern = <userpath>/AppData/Local/Programs/FreeCAD 0.19/data/Mod/TechDraw/PAT/FCPAT.pat
  FileHatchPattern = <userpath>/AppData/Local/Programs/FreeCAD 0.19/data/Mod/TechDraw/Patterns/simple.svg
  Focus = 100
  FuseBeforeCut = false
  HardHidden = false
  HatchScale = 1
  IsoCount = 0
  IsoHidden = false
  IsoVisible = false
  LockPosition = false
  NameGeomPattern = Diamond
  Perspective = false
  Rotation = 0
  Scale = 0.15
  ScaleType = 0
  SeamHidden = false
  SeamVisible = true
  SectionDirection = 0
  SectionNormal = (0,-1,0)
  SectionOrigin = (-998,445,0)
  SectionSymbol = D
  SmoothHidden = false
  SmoothVisible = true
  Source = -> [Body003]
  X = 310
  XDirection = (1,0,0)
  Y = 148.5
FEATURE [TechDraw::DrawViewDimension] Dimension092
  Arbitrary = false
  ArbitraryTolerances = false
  EqualTolerance = true
  FormatSpec = %.2f
  FormatSpecOverTolerance = %+.2f
  FormatSpecUnderTolerance = %+.2f
  Inverted = false
  LockPosition = false
  MeasureType = 1
  OverTolerance = 0
  References2D = -> [View003]
  Rotation = 0
  ScaleType = 0
  TheoreticalExact = false
  Type = 2
  UnderTolerance = 0
  X = 144.011
  Y = 29.606
FEATURE [TechDraw::DrawViewDimension] Dimension093
  Arbitrary = false
  ArbitraryTolerances = false
  EqualTolerance = true
  FormatSpec = %.2f
  FormatSpecOverTolerance = %+.2f
  FormatSpecUnderTolerance = %+.2f
  Inverted = false
  LockPosition = false
  MeasureType = 1
  OverTolerance = 0
  References2D = -> [SectionView003]
  Rotation = 0
  ScaleType = 0
  TheoreticalExact = false
  Type = 1
  UnderTolerance = 0
  X = 11.4023
  Y = 32.105
FEATURE [TechDraw::DrawPage] Page003  label="Inner_side_frame_Drawing"
  KeepUpdated = true
  NextBalloonIndex = 1
  ProjectionType = 0
  Template = -> Template003
  Views = -> [View003,Dimension075,Dimension078,Dimension079,Dimension080,Dimension083,Dimension084,Dimension085,Dimension086,Dimension087,Dimension088,SectionView003,Dimension092,Dimension093]
FEATURE [TechDraw::DrawSVGTemplate] Template004
  Height = 297
  Orientation = 1
  Width = 420
FEATURE [TechDraw::DrawViewPart] View004
  CoarseView = false
  Direction = (0,-1,0)
  Focus = 100
  HardHidden = false
  IsoCount = 0
  IsoHidden = false
  IsoVisible = false
  LockPosition = false
  Perspective = false
  Rotation = 0
  Scale = 0.15
  ScaleType = 0
  SeamHidden = false
  SeamVisible = true
  SmoothHidden = false
  SmoothVisible = true
  Source = -> [Body011]
  X = 200
  XDirection = (1,0,0)
  Y = 148.5
FEATURE [TechDraw::DrawViewDimension] Dimension094
  Arbitrary = false
  ArbitraryTolerances = false
  EqualTolerance = true
  FormatSpec = %.2f
  FormatSpecOverTolerance = %+.2f
  FormatSpecUnderTolerance = %+.2f
  Inverted = false
  LockPosition = false
  MeasureType = 1
  OverTolerance = 0
  References2D = -> [View004]
  Rotation = 0
  ScaleType = 0
  TheoreticalExact = false
  Type = 1
  UnderTolerance = 0
  X = -162.903
  Y = 73.6492
FEATURE [TechDraw::DrawViewDimension] Dimension095
  Arbitrary = false
  ArbitraryTolerances = false
  EqualTolerance = true
  FormatSpec = %.2f
  FormatSpecOverTolerance = %+.2f
  FormatSpecUnderTolerance = %+.2f
  Inverted = false
  LockPosition = false
  MeasureType = 1
  OverTolerance = 0
  References2D = -> [View004]
  Rotation = 0
  ScaleType = 0
  TheoreticalExact = false
  Type = 2
  UnderTolerance = 0
  X = -182.086
  Y = 60.2822
FEATURE [TechDraw::DrawViewDimension] Dimension096
  Arbitrary = false
  ArbitraryTolerances = false
  EqualTolerance = true
  FormatSpec = %.2f
  FormatSpecOverTolerance = %+.2f
  FormatSpecUnderTolerance = %+.2f
  Inverted = false
  LockPosition = false
  MeasureType = 1
  OverTolerance = 0
  References2D = -> [View004]
  Rotation = 0
  ScaleType = 0
  TheoreticalExact = false
  Type = 2
  UnderTolerance = 0
  X = -175.621
  Y = 60.9629
FEATURE [TechDraw::DrawViewDimension] Dimension097
  Arbitrary = false
  ArbitraryTolerances = false
  EqualTolerance = true
  FormatSpec = %.2f
  FormatSpecOverTolerance = %+.2f
  FormatSpecUnderTolerance = %+.2f
  Inverted = false
  LockPosition = false
  MeasureType = 1
  OverTolerance = 0
  References2D = -> [View004]
  Rotation = 0
  ScaleType = 0
  TheoreticalExact = false
  Type = 2
  UnderTolerance = 0
  X = -169.056
  Y = 60.8668
FEATURE [TechDraw::DrawViewDimension] Dimension098
  Arbitrary = false
  ArbitraryTolerances = false
  EqualTolerance = true
  FormatSpec = %.2f
  FormatSpecOverTolerance = %+.2f
  FormatSpecUnderTolerance = %+.2f
  Inverted = false
  LockPosition = false
  MeasureType = 1
  OverTolerance = 0
  References2D = -> [View004]
  Rotation = 0
  ScaleType = 0
  TheoreticalExact = false
  Type = 2
  UnderTolerance = 0
  X = -166.937
  Y = -59.2112
FEATURE [TechDraw::DrawViewDimension] Dimension099
  Arbitrary = false
  ArbitraryTolerances = false
  EqualTolerance = true
  FormatSpec = %.2f
  FormatSpecOverTolerance = %+.2f
  FormatSpecUnderTolerance = %+.2f
  Inverted = false
  LockPosition = false
  MeasureType = 1
  OverTolerance = 0
  References2D = -> [View004]
  Rotation = 0
  ScaleType = 0
  TheoreticalExact = false
  Type = 1
  UnderTolerance = 0
  X = -0.060236
  Y = 81.269
FEATURE [TechDraw::DrawViewSection] SectionView004  label="Section  - "
  BaseView = -> View004
  CoarseView = false
  CutSurfaceDisplay = 2
  Direction = (-1,0,0)
  FileGeomPattern = <userpath>/AppData/Local/Programs/FreeCAD 0.19/data/Mod/TechDraw/PAT/FCPAT.pat
  FileHatchPattern = <userpath>/AppData/Local/Programs/FreeCAD 0.19/data/Mod/TechDraw/Patterns/simple.svg
  Focus = 100
  FuseBeforeCut = false
  HardHidden = false
  HatchScale = 1
  IsoCount = 0
  IsoHidden = false
  IsoVisible = false
  LockPosition = false
  NameGeomPattern = Diamond
  Perspective = false
  Rotation = 0
  Scale = 0.15
  ScaleType = 0
  SeamHidden = false
  SeamVisible = true
  SectionDirection = 0
  SectionNormal = (-1,0,0)
  SectionOrigin = (940,602,262.5)
  SmoothHidden = false
  SmoothVisible = true
  Source = -> [Body011]
  X = 380
  XDirection = (0,-1,0)
  Y = 148.5
FEATURE [TechDraw::DrawViewDimension] Dimension100
  Arbitrary = false
  ArbitraryTolerances = false
  EqualTolerance = true
  FormatSpec = %.2f
  FormatSpecOverTolerance = %+.2f
  FormatSpecUnderTolerance = %+.2f
  Inverted = false
  LockPosition = false
  MeasureType = 1
  OverTolerance = 0
  References2D = -> [SectionView004]
  Rotation = 0
  ScaleType = 0
  TheoreticalExact = false
  Type = 1
  UnderTolerance = 0
  X = 11.3356
  Y = 68.7128
FEATURE [TechDraw::DrawViewDimension] Dimension101
  Arbitrary = false
  ArbitraryTolerances = false
  EqualTolerance = true
  FormatSpec = %.2f
  FormatSpecOverTolerance = %+.2f
  FormatSpecUnderTolerance = %+.2f
  Inverted = false
  LockPosition = false
  MeasureType = 1
  OverTolerance = 0
  References2D = -> [View004]
  Rotation = 0
  ScaleType = 0
  TheoreticalExact = false
  Type = 2
  UnderTolerance = 0
  X = 195.003
  Y = -2.6296
FEATURE [TechDraw::DrawPage] Page004  label="Outer_rear_frame_Drawing"
  KeepUpdated = true
  NextBalloonIndex = 1
  ProjectionType = 0
  Template = -> Template004
  Views = -> [View004,Dimension094,Dimension095,Dimension096,Dimension097,Dimension098,Dimension099,SectionView004,Dimension100,Dimension101]
FEATURE [TechDraw::DrawSVGTemplate] Template005
  Height = 297
  Orientation = 1
  Width = 420
FEATURE [TechDraw::DrawViewPart] View005
  CoarseView = false
  Direction = (1,0,0)
  Focus = 100
  HardHidden = false
  IsoCount = 0
  IsoHidden = false
  IsoVisible = false
  LockPosition = false
  Perspective = false
  Rotation = 0
  Scale = 0.15
  ScaleType = 0
  SeamHidden = false
  SeamVisible = true
  SmoothHidden = false
  SmoothVisible = true
  Source = -> [Body008]
  X = 209.944
  XDirection = (0,1,0)
  Y = 148.5
FEATURE [TechDraw::DrawViewDimension] Dimension107
  Arbitrary = false
  ArbitraryTolerances = false
  EqualTolerance = true
  FormatSpec = %.2f
  FormatSpecOverTolerance = %+.2f
  FormatSpecUnderTolerance = %+.2f
  Inverted = false
  LockPosition = false
  MeasureType = 1
  OverTolerance = 0
  References2D = -> [View005]
  Rotation = 0
  ScaleType = 0
  TheoreticalExact = false
  Type = 2
  UnderTolerance = 0
  X = -136.889
  Y = -2.82077
FEATURE [TechDraw::DrawViewDimension] Dimension112
  Arbitrary = false
  ArbitraryTolerances = false
  EqualTolerance = true
  FormatSpec = %.2f
  FormatSpecOverTolerance = %+.2f
  FormatSpecUnderTolerance = %+.2f
  Inverted = false
  LockPosition = false
  MeasureType = 1
  OverTolerance = 0
  References2D = -> [View005]
  Rotation = 0
  ScaleType = 0
  TheoreticalExact = false
  Type = 1
  UnderTolerance = 0
  X = 78.3148
  Y = 74.0433
FEATURE [TechDraw::DrawViewSection] SectionView005  label="Section F - F"
  BaseView = -> View005
  CoarseView = false
  CutSurfaceDisplay = 2
  Direction = (0,-1,0)
  FileGeomPattern = <userpath>/AppData/Local/Programs/FreeCAD 0.19/data/Mod/TechDraw/PAT/FCPAT.pat
  FileHatchPattern = <userpath>/AppData/Local/Programs/FreeCAD 0.19/data/Mod/TechDraw/Patterns/simple.svg
  Focus = 100
  FuseBeforeCut = false
  HardHidden = false
  HatchScale = 1
  IsoCount = 0
  IsoHidden = false
  IsoVisible = false
  LockPosition = false
  NameGeomPattern = Diamond
  Perspective = false
  Rotation = 0
  Scale = 0.15
  ScaleType = 0
  SeamHidden = false
  SeamVisible = true
  SectionDirection = 0
  SectionNormal = (0,-1,0)
  SectionOrigin = (1002,571,262.5)
  SectionSymbol = F
  SmoothHidden = false
  SmoothVisible = true
  Source = -> [Body008]
  X = 370
  XDirection = (1,0,0)
  Y = 148.5
FEATURE [TechDraw::DrawViewDimension] Dimension117
  Arbitrary = false
  ArbitraryTolerances = false
  EqualTolerance = true
  FormatSpec = %.2f
  FormatSpecOverTolerance = %+.2f
  FormatSpecUnderTolerance = %+.2f
  Inverted = false
  LockPosition = false
  MeasureType = 1
  OverTolerance = 0
  References2D = -> [SectionView005]
  Rotation = 0
  ScaleType = 0
  TheoreticalExact = false
  Type = 1
  UnderTolerance = 0
  X = 24.196
  Y = 61.7883
FEATURE [TechDraw::DrawViewSection] SectionView006  label="Section G - G"
  BaseView = -> View005
  CoarseView = false
  CutSurfaceDisplay = 2
  Direction = (0,1,0)
  FileGeomPattern = <userpath>/AppData/Local/Programs/FreeCAD 0.19/data/Mod/TechDraw/PAT/FCPAT.pat
  FileHatchPattern = <userpath>/AppData/Local/Programs/FreeCAD 0.19/data/Mod/TechDraw/Patterns/simple.svg
  Focus = 100
  FuseBeforeCut = false
  HardHidden = false
  HatchScale = 1
  IsoCount = 0
  IsoHidden = false
  IsoVisible = false
  LockPosition = false
  NameGeomPattern = Diamond
  Perspective = false
  Rotation = 0
  Scale = 0.15
  ScaleType = 0
  SeamHidden = false
  SeamVisible = true
  SectionDirection = 1
  SectionNormal = (0,1,0)
  SectionOrigin = (1002,-603,262.5)
  SectionSymbol = G
  SmoothHidden = false
  SmoothVisible = true
  Source = -> [Body008]
  X = 53.9646
  XDirection = (-1,0,0)
  Y = 112.5
FEATURE [TechDraw::DrawViewDimension] Dimension119
  Arbitrary = false
  ArbitraryTolerances = false
  EqualTolerance = true
  FormatSpec = %.2f
  FormatSpecOverTolerance = %+.2f
  FormatSpecUnderTolerance = %+.2f
  Inverted = false
  LockPosition = false
  MeasureType = 1
  OverTolerance = 0
  References2D = -> [SectionView006]
  Rotation = 0
  ScaleType = 0
  TheoreticalExact = false
  Type = 1
  UnderTolerance = 0
  X = -12.8305
  Y = 20.8111
FEATURE [TechDraw::DrawSVGTemplate] Template006
  Height = 297
  Orientation = 1
  Width = 420
FEATURE [TechDraw::DrawSVGTemplate] Template007
  Height = 297
  Orientation = 1
  Width = 420
FEATURE [TechDraw::DrawViewPart] View007
  CoarseView = false
  Direction = (0,0,1)
  Focus = 100
  HardHidden = false
  IsoCount = 0
  IsoHidden = false
  IsoVisible = false
  LockPosition = false
  Perspective = false
  Rotation = 0
  Scale = 0.15
  ScaleType = 0
  SeamHidden = false
  SeamVisible = true
  SmoothHidden = false
  SmoothVisible = true
  Source = -> [Body007]
  X = 200
  XDirection = (1,0,0)
  Y = 170.5
FEATURE [TechDraw::DrawViewDimension] Dimension120
  Arbitrary = false
  ArbitraryTolerances = false
  EqualTolerance = true
  FormatSpec = %.2f
  FormatSpecOverTolerance = %+.2f
  FormatSpecUnderTolerance = %+.2f
  Inverted = false
  LockPosition = false
  MeasureType = 1
  OverTolerance = 0
  References2D = -> [View007]
  Rotation = 0
  ScaleType = 0
  TheoreticalExact = false
  Type = 1
  UnderTolerance = 0
  X = 1.57626
  Y = 107.754
FEATURE [TechDraw::DrawViewDimension] Dimension121
  Arbitrary = false
  ArbitraryTolerances = false
  EqualTolerance = true
  FormatSpec = %.2f
  FormatSpecOverTolerance = %+.2f
  FormatSpecUnderTolerance = %+.2f
  Inverted = false
  LockPosition = false
  MeasureType = 1
  OverTolerance = 0
  References2D = -> [View007]
  Rotation = 0
  ScaleType = 0
  TheoreticalExact = false
  Type = 2
  UnderTolerance = 0
  X = 199.279
  Y = 3.23548
FEATURE [TechDraw::DrawViewSection] SectionView007  label="Section I - I"
  BaseView = -> View007
  CoarseView = false
  CutSurfaceDisplay = 2
  Direction = (-1,0,0)
  FileGeomPattern = <userpath>/AppData/Local/Programs/FreeCAD 0.19/data/Mod/TechDraw/PAT/FCPAT.pat
  FileHatchPattern = <userpath>/AppData/Local/Programs/FreeCAD 0.19/data/Mod/TechDraw/Patterns/simple.svg
  Focus = 100
  FuseBeforeCut = false
  HardHidden = false
  HatchScale = 1
  IsoCount = 0
  IsoHidden = false
  IsoVisible = false
  LockPosition = false
  NameGeomPattern = Diamond
  Perspective = false
  Rotation = 0
  Scale = 0.15
  ScaleType = 0
  SeamHidden = false
  SeamVisible = true
  SectionDirection = 0
  SectionNormal = (-1,0,0)
  SectionOrigin = (0,0,52)
  SectionSymbol = I
  SmoothHidden = false
  SmoothVisible = true
  Source = -> [Body007]
  X = 380
  XDirection = (0,0,1)
  Y = 170.5
FEATURE [TechDraw::DrawViewDimension] Dimension122
  Arbitrary = false
  ArbitraryTolerances = false
  EqualTolerance = true
  FormatSpec = %.2f
  FormatSpecOverTolerance = %+.2f
  FormatSpecUnderTolerance = %+.2f
  Inverted = false
  LockPosition = false
  MeasureType = 1
  OverTolerance = 0
  References2D = -> [SectionView007]
  Rotation = 0
  ScaleType = 0
  TheoreticalExact = false
  Type = 1
  UnderTolerance = 0
  X = 15.2809
  Y = 105.698
FEATURE [TechDraw::DrawPage] Page007  label="Top_structure_Drawing"
  KeepUpdated = true
  NextBalloonIndex = 1
  ProjectionType = 0
  Template = -> Template007
  Views = -> [View007,Dimension120,Dimension121,SectionView007,Dimension122]
FEATURE [TechDraw::DrawSVGTemplate] Template008
  Height = 297
  Orientation = 1
  Width = 420
FEATURE [TechDraw::DrawViewPart] View008
  CoarseView = false
  Direction = (0,0,1)
  Focus = 100
  HardHidden = false
  IsoCount = 0
  IsoHidden = false
  IsoVisible = false
  LockPosition = false
  Perspective = false
  Rotation = 0
  Scale = 0.15
  ScaleType = 0
  SeamHidden = false
  SeamVisible = true
  SmoothHidden = false
  SmoothVisible = true
  Source = -> [Body012]
  X = 199.502
  XDirection = (0,0,0.06)
  Y = 170.5
FEATURE [TechDraw::DrawViewDimension] Dimension123
  Arbitrary = false
  ArbitraryTolerances = false
  EqualTolerance = true
  FormatSpec = %.2f
  FormatSpecOverTolerance = %+.2f
  FormatSpecUnderTolerance = %+.2f
  Inverted = false
  LockPosition = false
  MeasureType = 1
  OverTolerance = 0
  References2D = -> [View008]
  Rotation = 0
  ScaleType = 0
  TheoreticalExact = false
  Type = 1
  UnderTolerance = 0
  X = -7.60475
  Y = 113.851
FEATURE [TechDraw::DrawViewSection] SectionView008  label="Section  - 001"
  BaseView = -> View008
  CoarseView = false
  CutSurfaceDisplay = 2
  Direction = (-1,0,0)
  FileGeomPattern = <userpath>/AppData/Local/Programs/FreeCAD 0.19/data/Mod/TechDraw/PAT/FCPAT.pat
  FileHatchPattern = <userpath>/AppData/Local/Programs/FreeCAD 0.19/data/Mod/TechDraw/Patterns/simple.svg
  Focus = 100
  FuseBeforeCut = false
  HardHidden = false
  HatchScale = 1
  IsoCount = 0
  IsoHidden = false
  IsoVisible = false
  LockPosition = false
  NameGeomPattern = Diamond
  Perspective = false
  Rotation = 0
  Scale = 0.15
  ScaleType = 0
  SeamHidden = false
  SeamVisible = true
  SectionDirection = 0
  SectionNormal = (-1,0,0)
  SectionOrigin = (0,0,65)
  SmoothHidden = false
  SmoothVisible = true
  Source = -> [Body012]
  X = 380
  XDirection = (0,0,1)
  Y = 170.5
FEATURE [TechDraw::DrawViewDimension] Dimension125
  Arbitrary = false
  ArbitraryTolerances = false
  EqualTolerance = true
  FormatSpec = %.2f
  FormatSpecOverTolerance = %+.2f
  FormatSpecUnderTolerance = %+.2f
  Inverted = false
  LockPosition = false
  MeasureType = 1
  OverTolerance = 0
  References2D = -> [View008]
  Rotation = 0
  ScaleType = 0
  TheoreticalExact = false
  Type = 2
  UnderTolerance = 0
  X = 192.863
  Y = -1.03701
FEATURE [TechDraw::DrawViewDimension] Dimension126
  Arbitrary = false
  ArbitraryTolerances = false
  EqualTolerance = true
  FormatSpec = %.2f
  FormatSpecOverTolerance = %+.2f
  FormatSpecUnderTolerance = %+.2f
  Inverted = false
  LockPosition = false
  MeasureType = 1
  OverTolerance = 0
  References2D = -> [SectionView008]
  Rotation = 0
  ScaleType = 0
  TheoreticalExact = false
  Type = 1
  UnderTolerance = 0
  X = 0
  Y = 105.901
FEATURE [TechDraw::DrawPage] Page008  label="Top_foam_surface_Drawing"
  KeepUpdated = true
  NextBalloonIndex = 1
  ProjectionType = 0
  Template = -> Template008
  Views = -> [View008,Dimension123,SectionView008,Dimension125,Dimension126]
FEATURE [Spreadsheet::Sheet] Spreadsheet  label="PartSpecification"
  cells = A1=Part Name:; B1=No Pieces:; C1=Material:; D1=Material thickness [mm]:; E1=Material density [Kg/dm2]:; F1=Part volume [dm2]; G1=Part mass [kg]:; H1=Total mass:; I1=Post CNC cutout processing; A2=Langsprygel; B2=3; C2=Oak plywood; D2=4; E2=0.6; F2==<<LangSprygel-1>>.Shape.Volume / 1000000; G2==E2 * F2; H2==G2 * B2; A3=Kortsprygel; B3=5; C3=Oak plywood; D3=4; E3=0.6; F3==<<KortSprygel-1>>.Shape.Volume / 1000000; G3==E3 * F3; H3==G3 * B3; A4=Sidkant-inre; B4=2; C4=Oak plywood; D4=4; E4=0.6; F4==<<Sidkant-Inre-1>>.Shape.Volume / 1000000; G4==E4 * F4; H4==G4 * B4; A5=Fram/Bakkant-inre; B5=2; C5=Oak plywood; D5=4; E5=0.6; F5==<<Fram/Bakkant-Inre-1>>.Shape.Volume / 1000000; G5==E5 * F5; H5==G5 * B5; A6=Framkant-yttre; B6=1; C6=Oak plywood; D6=4; E6=0.6; F6==<<Framkant-Yttre-1>>.Shape.Volume / 1000000; G6==E6 * F6; H6==G6 * B6; A7=Bakkant-yttre; B7=1; C7=Oak plywood; D7=4; E7=0.6; F7==<<Bakkant-Yttre>>.Shape.Volume / 1000000; G7==E7 * F7; H7==G7 * B7; I7=2.29; A8=Sidkant-yttre; B8=2; C8=Oak plywood; D8=4; E8=0.6; F8==<<Sidkant-Yttre-1>>.Shape.Volume / 1000000; G8==E8 * F8; H8==G8 * B8; I8=2.84; A9=Bordskiva; B9=1; C9=Oak plywood; D9=4; E9=0.6; F9==<<Bordskiva>>.Shape.Volume / 1000000; G9==E9 * F9; H9==G9 * B9; A10=Foamskiva; B10=1; C10=Extruded foam; D10=20; E10=0.02; F10==<<Cellplast-topp>>.Shape.Volume / 1000000; G10==E10 * F10; H10==G10 * B10; A11=Undersida; B11=1; C11=Oak plywood; D11=2; E11=0.6; F11==<<Undersida>>.Shape.Volume / 1000000; G11==E11 * F11; H11==G11 * B11; A12=Körbord-bakkant; B12=1; C12=Oak plywood; D12=4; E12=0.6; F12==<<KorbordBaksida>>.Shape.Volume / 1000000; G12==E12 * F12; H12==G12 * B12; A13=Körbord-framkant; B13=1; C13=Oak plywood; D13=4; E13=0.6; F13==<<KorbordFramsida>>.Shape.Volume / 1000000; G13==E13 * F13; H13==G13 * B13; A14=Körbord-sidor; B14=2; C14=Oak plywood; D14=4; E14=0.6; F14==<<KorBordSida-1>>.Shape.Volume / 1000000; G14==E14 * F14; H14==G14 * B14; A15=Körbord-spryglar; B15=4; C15=Oak plywood; D15=4; E15=0.6; F15==<<KorbordSprygel-1>>.Shape.Volume / 1000000; G15==E15 * F15; H15==G15 * B15; A16=Utrustnings-box; B16=4; C16=-; D16=-; E16=-; F16=-; G16==H17 + H18 + H19; H16==G16 * B16; A17=Utrustnings-box-baksida; B17=1; C17=Oak plywood; D17=4; E17=0.6; F17==<<UtrustningsBoxBakkant-1>>.Shape.Volume / 1000000; G17==E17 * F17; H17==G17 * B17; A18=Utrustnings-box-botten; B18=1; C18=Oak plywood; D18=4; E18=0.6; F18==<<UtrustningsBoxBakkant-1>>.Shape.Volume / 1000000; G18==E18 * F18; H18==G18 * B18; A19=Utrustnings-box-sidor; B19=2; C19=Oak plywood; D19=4; E19=0.6; F19==<<UtrustningsBoxSida-V-1>>.Shape.Volume / 1000000; G19==E19 * F19; H19==G19 * B19; A20=Totalweight; H20==sum(H2; H3; H4; H5; H6; H7; H8; H9; H10; H11; H12; H13; H14; H15; H16)
FEATURE [Sketcher::SketchObject] Sketch037
  ExternalGeometry = -> [Pad010]
  FullyConstrained = true
  MapMode = 5
  Placement = pos=(0,-4,0) rot=(1,0,0;1.5708rad)
  Support = -> [Pad010]
  sketch-geometry (24):
    g0: LineSegment StartX=-1000 StartY=-32 StartZ=0 EndX=-1004 EndY=-32 EndZ=0
    g1: LineSegment StartX=-1004 StartY=-32 StartZ=0 EndX=-1004 EndY=-12 EndZ=0
    g2: LineSegment StartX=-1004 StartY=-12 StartZ=0 EndX=-1000 EndY=-12 EndZ=0
    g3: LineSegment StartX=-1000 StartY=-12 StartZ=0 EndX=-1000 EndY=-32 EndZ=0
    g4: LineSegment StartX=-1004 StartY=28 StartZ=0 EndX=-1000 EndY=28 EndZ=0
    g5: LineSegment StartX=-1000 StartY=28 StartZ=0 EndX=-1000 EndY=8 EndZ=0
    g6: LineSegment StartX=-1000 StartY=8 StartZ=0 EndX=-1004 EndY=8 EndZ=0
    g7: LineSegment StartX=-1004 StartY=8 StartZ=0 EndX=-1004 EndY=28 EndZ=0
    g8: LineSegment StartX=-1004 StartY=68 StartZ=0 EndX=-1000 EndY=68 EndZ=0
    g9: LineSegment StartX=-1000 StartY=68 StartZ=0 EndX=-1000 EndY=48 EndZ=0
    g10: LineSegment StartX=-1000 StartY=48 StartZ=0 EndX=-1004 EndY=48 EndZ=0
    g11: LineSegment StartX=-1004 StartY=48 StartZ=0 EndX=-1004 EndY=68 EndZ=0
    g12: LineSegment StartX=1004 StartY=-32 StartZ=0 EndX=1000 EndY=-32 EndZ=0
    g13: LineSegment StartX=1000 StartY=-32 StartZ=0 EndX=1000 EndY=-12 EndZ=0
    g14: LineSegment StartX=1000 StartY=-12 StartZ=0 EndX=1004 EndY=-12 EndZ=0
    g15: LineSegment StartX=1004 StartY=-12 StartZ=0 EndX=1004 EndY=-32 EndZ=0
    g16: LineSegment StartX=1004 StartY=8 StartZ=0 EndX=1000 EndY=8 EndZ=0
    g17: LineSegment StartX=1000 StartY=8 StartZ=0 EndX=1000 EndY=28 EndZ=0
    g18: LineSegment StartX=1000 StartY=28 StartZ=0 EndX=1004 EndY=28 EndZ=0
    g19: LineSegment StartX=1004 StartY=28 StartZ=0 EndX=1004 EndY=8 EndZ=0
    g20: LineSegment StartX=1000 StartY=68 StartZ=0 EndX=1004 EndY=68 EndZ=0
    g21: LineSegment StartX=1004 StartY=68 StartZ=0 EndX=1004 EndY=48 EndZ=0
    g22: LineSegment StartX=1004 StartY=48 StartZ=0 EndX=1000 EndY=48 EndZ=0
    g23: LineSegment StartX=1000 StartY=48 StartZ=0 EndX=1000 EndY=68 EndZ=0
  constraints (72):
    c: Coincident(g0,g1)
    c: Coincident(g1,g2)
    c: Coincident(g2,g3)
    c: Coincident(g3,g0)
    c: Horizontal(g0)
    c: Horizontal(g2)
    c: Vertical(g1)
    c: Vertical(g3)
    c: Coincident(g4,g5)
    c: Coincident(g5,g6)
    c: Coincident(g6,g7)
    c: Coincident(g7,g4)
    c: Horizontal(g4)
    c: Horizontal(g6)
    c: Vertical(g5)
    c: Vertical(g7)
    c: Coincident(g8,g9)
    c: Coincident(g9,g10)
    c: Coincident(g10,g11)
    c: Coincident(g11,g8)
    c: Horizontal(g8)
    c: Horizontal(g10)
    c: Vertical(g9)
    c: Vertical(g11)
    c: Vertical(g1,g6)
    c: Vertical(g4,g10)
    c: Vertical(g2,g5)
    c: Vertical(g4,g9)
    c: DistanceY(g0,g1) = 20
    c: DistanceY(g1,g6) = 20
    c: DistanceY(g6,g4) = 20
    c: DistanceY(g4,g10) = 20
    c: DistanceY(g10,g8) = 20
    c: Coincident(g12,g13)
    c: Coincident(g13,g14)
    c: Coincident(g14,g15)
    c: Coincident(g15,g12)
    c: Horizontal(g12)
    c: Horizontal(g14)
    c: Vertical(g13)
    c: Vertical(g15)
    c: Coincident(g16,g17)
    c: Coincident(g17,g18)
    c: Coincident(g18,g19)
    c: Coincident(g19,g16)
    c: Horizontal(g16)
    c: Horizontal(g18)
    c: Vertical(g17)
    c: Vertical(g19)
    c: Vertical(g13,g16)
    c: Horizontal(g0,g12)
    c: Horizontal(g13,g2)
    c: Horizontal(g5,g16)
    c: Horizontal(g17,g4)
    c: DistanceY(g-3,g0) = 20
    c: DistanceX(g0,g0) = 4
    c: Coincident(g20,g21)
    c: Coincident(g21,g22)
    c: Coincident(g22,g23)
    c: Coincident(g23,g20)
    c: Horizontal(g20)
    c: Horizontal(g22)
    c: Vertical(g21)
    c: Vertical(g23)
    c: Vertical(g17,g22)
    c: Vertical(g18,g21)
    c: Horizontal(g22,g9)
    c: Horizontal(g8,g20)
    c: DistanceX(g-3,g0) = 0
    c: DistanceX(g12,g-6) = 0
    c: DistanceX(g12,g12) = 4
    c: Vertical(g14,g16)
FEATURE [PartDesign::Pocket] Pocket016
  BaseFeature = -> Pad010
  Length = 4
  Length2 = 100
  Placement = pos=(0,0,0) rot=(1,0,0;1.5708rad)
  Profile = -> Sketch037
  Type = 0
FEATURE [PartDesign::Body] Body010  label="Framkant-Yttre-1"
  Group = -> [Sketch021,Pad010,Sketch037,Pocket016]
  Origin = -> Origin010
  Placement = pos=(0,-600,0) rot=(0,0,1;0rad)
  Tip = -> Pocket016
FEATURE [TechDraw::DrawViewPart] View009
  CoarseView = false
  Direction = (0,-1,0)
  Focus = 100
  HardHidden = false
  IsoCount = 0
  IsoHidden = false
  IsoVisible = false
  LockPosition = false
  Perspective = false
  Rotation = 0
  Scale = 0.15
  ScaleType = 0
  SeamHidden = false
  SeamVisible = true
  SmoothHidden = false
  SmoothVisible = true
  Source = -> [Body010]
  X = 210
  XDirection = (1,0,0)
  Y = 148.5
FEATURE [TechDraw::DrawViewDimension] Dimension127
  Arbitrary = false
  ArbitraryTolerances = false
  EqualTolerance = true
  FormatSpec = %.2f
  FormatSpecOverTolerance = %+.2f
  FormatSpecUnderTolerance = %+.2f
  Inverted = false
  LockPosition = false
  MeasureType = 1
  OverTolerance = 0
  References2D = -> [View009]
  Rotation = 0
  ScaleType = 0
  TheoreticalExact = false
  Type = 1
  UnderTolerance = 0
  X = 1.30198
  Y = 36.3387
FEATURE [TechDraw::DrawViewDimension] Dimension128
  Arbitrary = false
  ArbitraryTolerances = false
  EqualTolerance = true
  FormatSpec = %.2f
  FormatSpecOverTolerance = %+.2f
  FormatSpecUnderTolerance = %+.2f
  Inverted = false
  LockPosition = false
  MeasureType = 1
  OverTolerance = 0
  References2D = -> [View009]
  Rotation = 0
  ScaleType = 0
  TheoreticalExact = false
  Type = 1
  UnderTolerance = 0
  X = -135.653
  Y = -19.1378
FEATURE [TechDraw::DrawViewDimension] Dimension129
  Arbitrary = false
  ArbitraryTolerances = false
  EqualTolerance = true
  FormatSpec = %.2f
  FormatSpecOverTolerance = %+.2f
  FormatSpecUnderTolerance = %+.2f
  Inverted = false
  LockPosition = false
  MeasureType = 1
  OverTolerance = 0
  References2D = -> [View009]
  Rotation = 0
  ScaleType = 0
  TheoreticalExact = false
  Type = 2
  UnderTolerance = 0
  X = -192.853
  Y = 24.9624
FEATURE [TechDraw::DrawViewDimension] Dimension130
  Arbitrary = false
  ArbitraryTolerances = false
  EqualTolerance = true
  FormatSpec = %.2f
  FormatSpecOverTolerance = %+.2f
  FormatSpecUnderTolerance = %+.2f
  Inverted = false
  LockPosition = false
  MeasureType = 1
  OverTolerance = 0
  References2D = -> [View009]
  Rotation = 0
  ScaleType = 0
  TheoreticalExact = false
  Type = 2
  UnderTolerance = 0
  X = -186.312
  Y = 23.7389
FEATURE [TechDraw::DrawViewDimension] Dimension131
  Arbitrary = false
  ArbitraryTolerances = false
  EqualTolerance = true
  FormatSpec = %.2f
  FormatSpecOverTolerance = %+.2f
  FormatSpecUnderTolerance = %+.2f
  Inverted = false
  LockPosition = false
  MeasureType = 1
  OverTolerance = 0
  References2D = -> [View009]
  Rotation = 0
  ScaleType = 0
  TheoreticalExact = false
  Type = 2
  UnderTolerance = 0
  X = -179.988
  Y = 23.6548
FEATURE [TechDraw::DrawViewDimension] Dimension132
  Arbitrary = false
  ArbitraryTolerances = false
  EqualTolerance = true
  FormatSpec = %.2f
  FormatSpecOverTolerance = %+.2f
  FormatSpecUnderTolerance = %+.2f
  Inverted = false
  LockPosition = false
  MeasureType = 1
  OverTolerance = 0
  References2D = -> [View009]
  Rotation = 0
  ScaleType = 0
  TheoreticalExact = false
  Type = 2
  UnderTolerance = 0
  X = -173.85
  Y = 23.6307
FEATURE [TechDraw::DrawViewDimension] Dimension133
  Arbitrary = false
  ArbitraryTolerances = false
  EqualTolerance = true
  FormatSpec = %.2f
  FormatSpecOverTolerance = %+.2f
  FormatSpecUnderTolerance = %+.2f
  Inverted = false
  LockPosition = false
  MeasureType = 1
  OverTolerance = 0
  References2D = -> [View009]
  Rotation = 0
  ScaleType = 0
  TheoreticalExact = false
  Type = 2
  UnderTolerance = 0
  X = -167.712
  Y = 23.7927
FEATURE [TechDraw::DrawViewDimension] Dimension134
  Arbitrary = false
  ArbitraryTolerances = false
  EqualTolerance = true
  FormatSpec = %.2f
  FormatSpecOverTolerance = %+.2f
  FormatSpecUnderTolerance = %+.2f
  Inverted = false
  LockPosition = false
  MeasureType = 1
  OverTolerance = 0
  References2D = -> [View009]
  Rotation = 0
  ScaleType = 0
  TheoreticalExact = false
  Type = 2
  UnderTolerance = 0
  X = -161.946
  Y = 23.7687
FEATURE [TechDraw::DrawViewDimension] Dimension135
  Arbitrary = false
  ArbitraryTolerances = false
  EqualTolerance = true
  FormatSpec = %.2f
  FormatSpecOverTolerance = %+.2f
  FormatSpecUnderTolerance = %+.2f
  Inverted = false
  LockPosition = false
  MeasureType = 1
  OverTolerance = 0
  References2D = -> [View009]
  Rotation = 0
  ScaleType = 0
  TheoreticalExact = false
  Type = 2
  UnderTolerance = 0
  X = -156.438
  Y = 23.5586
FEATURE [TechDraw::DrawViewSection] SectionView009  label="Section H - H"
  BaseView = -> View009
  CoarseView = false
  CutSurfaceDisplay = 2
  Direction = (-1,0,0)
  FileGeomPattern = <userpath>/AppData/Local/Programs/FreeCAD 0.19/data/Mod/TechDraw/PAT/FCPAT.pat
  FileHatchPattern = <userpath>/AppData/Local/Programs/FreeCAD 0.19/data/Mod/TechDraw/Patterns/simple.svg
  Focus = 100
  FuseBeforeCut = false
  HardHidden = false
  HatchScale = 1
  IsoCount = 0
  IsoHidden = false
  IsoVisible = false
  LockPosition = false
  NameGeomPattern = Diamond
  Perspective = false
  Rotation = 0
  Scale = 0.15
  ScaleType = 0
  SeamHidden = false
  SeamVisible = true
  SectionDirection = 0
  SectionNormal = (-1,0,0)
  SectionOrigin = (0,-602,12.5)
  SectionSymbol = H
  SmoothHidden = false
  SmoothVisible = true
  Source = -> [Body010]
  X = 383.036
  XDirection = (0,-1,0)
  Y = 148.5
FEATURE [TechDraw::DrawViewDimension] Dimension137
  Arbitrary = false
  ArbitraryTolerances = false
  EqualTolerance = true
  FormatSpec = %.2f
  FormatSpecOverTolerance = %+.2f
  FormatSpecUnderTolerance = %+.2f
  Inverted = false
  LockPosition = false
  MeasureType = 1
  OverTolerance = 0
  References2D = -> [SectionView009]
  Rotation = 0
  ScaleType = 0
  TheoreticalExact = false
  Type = 1
  UnderTolerance = 0
  X = -14.0968
  Y = 24.0377
FEATURE [TechDraw::DrawSVGTemplate] Template009
  Height = 297
  Orientation = 1
  Width = 420
FEATURE [TechDraw::DrawProjGroupItem] ProjItem  label="Front"
  CoarseView = false
  Direction = (0.299,-0.914,0.273)
  Focus = 100
  HardHidden = false
  IsoCount = 0
  IsoHidden = false
  IsoVisible = false
  LockPosition = true
  Perspective = false
  Rotation = 0
  RotationVector = (0.943,0.327,0.064)
  Scale = 0.07
  ScaleType = 2
  SeamHidden = false
  SeamVisible = true
  SmoothHidden = false
  SmoothVisible = true
  Source = -> [Body,Body001,Body002,Body003,Body004,Body005,Body006,Body013,Body014,Body015,Body016,Body017]
  Type = 0
  X = 0
  XDirection = (0.943,0.327,0.064)
  Y = 0
FEATURE [TechDraw::DrawProjGroup] ProjGroup
  Anchor = -> ProjItem
  AutoDistribute = true
  LockPosition = false
  ProjectionType = 0
  Rotation = 0
  Scale = 0.07
  ScaleType = 2
  Source = -> [Body,Body001,Body002,Body003,Body004,Body005,Body006,Body013,Body014,Body015,Body016,Body017]
  Views = -> [ProjItem]
  X = 124.937
  Y = 218.84
  spacingX = 15
  spacingY = 15
FEATURE [TechDraw::DrawProjGroupItem] ProjItem001  label="Front001"
  CoarseView = false
  Direction = (0.299,-0.914,0.273)
  Focus = 100
  HardHidden = false
  IsoCount = 0
  IsoHidden = false
  IsoVisible = false
  LockPosition = true
  Perspective = false
  Rotation = 0
  RotationVector = (0.943,0.327,0.064)
  Scale = 0.066667
  ScaleType = 2
  SeamHidden = false
  SeamVisible = true
  SmoothHidden = false
  SmoothVisible = true
  Source = -> [Body,Body002,Body003,Body004,Body005,Body006,Body008,Body009,Body010,Body011,Body013,Body014,Body015,Body016,Body017]
  Type = 0
  X = 0
  XDirection = (0.943,0.327,0.064)
  Y = 0
FEATURE [TechDraw::DrawProjGroup] ProjGroup001
  Anchor = -> ProjItem001
  AutoDistribute = true
  LockPosition = false
  ProjectionType = 0
  Rotation = 0
  Scale = 0.066667
  ScaleType = 2
  Source = -> [Body,Body002,Body003,Body004,Body005,Body006,Body008,Body009,Body010,Body011,Body013,Body014,Body015,Body016,Body017]
  Views = -> [ProjItem001]
  X = 312.512
  Y = 227.02
  spacingX = 15
  spacingY = 15
FEATURE [TechDraw::DrawProjGroupItem] ProjItem002  label="Front002"
  CoarseView = false
  Direction = (0.299,-0.914,0.273)
  Focus = 100
  HardHidden = false
  IsoCount = 0
  IsoHidden = false
  IsoVisible = false
  LockPosition = true
  Perspective = false
  Rotation = 0
  RotationVector = (0.943,0.327,0.064)
  Scale = 0.066667
  ScaleType = 2
  SeamHidden = false
  SeamVisible = true
  SmoothHidden = false
  SmoothVisible = true
  Source = -> [Body017,Body,Body001,Body002,Body003,Body004,Body005,Body006,Body007,Body008,Body009,Body010,Body011,Body012,Body013,Body014,Body015,Body016]
  Type = 0
  X = 0
  XDirection = (0.943,0.327,0.064)
  Y = 0
FEATURE [TechDraw::DrawProjGroup] ProjGroup002
  Anchor = -> ProjItem002
  AutoDistribute = true
  LockPosition = false
  ProjectionType = 0
  Rotation = 0
  Scale = 0.066667
  ScaleType = 2
  Source = -> [Body017,Body,Body001,Body002,Body003,Body004,Body005,Body006,Body007,Body008,Body009,Body010,Body011,Body012,Body013,Body014,Body015,Body016]
  Views = -> [ProjItem002]
  X = 126.028
  Y = 104.333
  spacingX = 15
  spacingY = 15
FEATURE [TechDraw::DrawPage] Page009  label="Explosion_Drawing"
  KeepUpdated = true
  NextBalloonIndex = 1
  ProjectionType = 0
  Template = -> Template009
  Views = -> [ProjGroup,ProjGroup001,ProjGroup002]
FEATURE [TechDraw::DrawViewDimension] Dimension138
  Arbitrary = false
  ArbitraryTolerances = false
  EqualTolerance = true
  FormatSpec = %.2f
  FormatSpecOverTolerance = %+.2f
  FormatSpecUnderTolerance = %+.2f
  Inverted = false
  LockPosition = false
  MeasureType = 1
  OverTolerance = 0
  References2D = -> [View009]
  Rotation = 0
  ScaleType = 0
  TheoreticalExact = false
  Type = 2
  UnderTolerance = 0
  X = 187.589
  Y = 24.1742
FEATURE [TechDraw::DrawViewDimension] Dimension139
  Arbitrary = false
  ArbitraryTolerances = false
  EqualTolerance = true
  FormatSpec = %.2f
  FormatSpecOverTolerance = %+.2f
  FormatSpecUnderTolerance = %+.2f
  Inverted = false
  LockPosition = false
  MeasureType = 1
  OverTolerance = 0
  References2D = -> [View005]
  Rotation = 0
  ScaleType = 0
  TheoreticalExact = false
  Type = 2
  UnderTolerance = 0
  X = -130.842
  Y = -3.012
FEATURE [TechDraw::DrawViewDimension] Dimension140
  Arbitrary = false
  ArbitraryTolerances = false
  EqualTolerance = true
  FormatSpec = %.2f
  FormatSpecOverTolerance = %+.2f
  FormatSpecUnderTolerance = %+.2f
  Inverted = false
  LockPosition = false
  MeasureType = 1
  OverTolerance = 0
  References2D = -> [View005]
  Rotation = 0
  ScaleType = 0
  TheoreticalExact = false
  Type = 2
  UnderTolerance = 0
  X = -125.122
  Y = -3.09239
FEATURE [TechDraw::DrawViewDimension] Dimension141
  Arbitrary = false
  ArbitraryTolerances = false
  EqualTolerance = true
  FormatSpec = %.2f
  FormatSpecOverTolerance = %+.2f
  FormatSpecUnderTolerance = %+.2f
  Inverted = false
  LockPosition = false
  MeasureType = 1
  OverTolerance = 0
  References2D = -> [View005]
  Rotation = 0
  ScaleType = 0
  TheoreticalExact = false
  Type = 2
  UnderTolerance = 0
  X = -119.3
  Y = -3.4264
FEATURE [TechDraw::DrawViewDimension] Dimension142
  Arbitrary = false
  ArbitraryTolerances = false
  EqualTolerance = true
  FormatSpec = %.2f
  FormatSpecOverTolerance = %+.2f
  FormatSpecUnderTolerance = %+.2f
  Inverted = false
  LockPosition = false
  MeasureType = 1
  OverTolerance = 0
  References2D = -> [View005]
  Rotation = 0
  ScaleType = 0
  TheoreticalExact = false
  Type = 2
  UnderTolerance = 0
  X = -113.478
  Y = -3.51889
FEATURE [TechDraw::DrawViewDimension] Dimension143
  Arbitrary = false
  ArbitraryTolerances = false
  EqualTolerance = true
  FormatSpec = %.2f
  FormatSpecOverTolerance = %+.2f
  FormatSpecUnderTolerance = %+.2f
  Inverted = false
  LockPosition = false
  MeasureType = 1
  OverTolerance = 0
  References2D = -> [View005]
  Rotation = 0
  ScaleType = 0
  TheoreticalExact = false
  Type = 2
  UnderTolerance = 0
  X = -107.667
  Y = -3.59928
FEATURE [TechDraw::DrawViewDimension] Dimension144
  Arbitrary = false
  ArbitraryTolerances = false
  EqualTolerance = true
  FormatSpec = %.2f
  FormatSpecOverTolerance = %+.2f
  FormatSpecUnderTolerance = %+.2f
  Inverted = false
  LockPosition = false
  MeasureType = 1
  OverTolerance = 0
  References2D = -> [View005]
  Rotation = 0
  ScaleType = 0
  TheoreticalExact = false
  Type = 2
  UnderTolerance = 0
  X = -101.893
  Y = -2.85507
FEATURE [TechDraw::DrawViewDimension] Dimension145
  Arbitrary = false
  ArbitraryTolerances = false
  EqualTolerance = true
  FormatSpec = %.2f
  FormatSpecOverTolerance = %+.2f
  FormatSpecUnderTolerance = %+.2f
  Inverted = false
  LockPosition = false
  MeasureType = 1
  OverTolerance = 0
  References2D = -> [View005]
  Rotation = 0
  ScaleType = 0
  TheoreticalExact = false
  Type = 2
  UnderTolerance = 0
  X = -190.144
  Y = 0.47803
FEATURE [TechDraw::DrawViewDimension] Dimension146
  Arbitrary = false
  ArbitraryTolerances = false
  EqualTolerance = true
  FormatSpec = %.2f
  FormatSpecOverTolerance = %+.2f
  FormatSpecUnderTolerance = %+.2f
  Inverted = false
  LockPosition = false
  MeasureType = 1
  OverTolerance = 0
  References2D = -> [View005]
  Rotation = 0
  ScaleType = 0
  TheoreticalExact = false
  Type = 1
  UnderTolerance = 0
  X = 47.7197
  Y = 81.9377
FEATURE [TechDraw::DrawViewDimension] Dimension147
  Arbitrary = false
  ArbitraryTolerances = false
  EqualTolerance = true
  FormatSpec = %.2f
  FormatSpecOverTolerance = %+.2f
  FormatSpecUnderTolerance = %+.2f
  Inverted = false
  LockPosition = false
  MeasureType = 1
  OverTolerance = 0
  References2D = -> [View005]
  Rotation = 0
  ScaleType = 0
  TheoreticalExact = false
  Type = 1
  UnderTolerance = 0
  X = -1.84072
  Y = -64.6298
FEATURE [TechDraw::DrawViewDimension] Dimension148
  Arbitrary = false
  ArbitraryTolerances = false
  EqualTolerance = true
  FormatSpec = %.2f
  FormatSpecOverTolerance = %+.2f
  FormatSpecUnderTolerance = %+.2f
  Inverted = false
  LockPosition = false
  MeasureType = 1
  OverTolerance = 0
  References2D = -> [View005]
  Rotation = 0
  ScaleType = 0
  TheoreticalExact = false
  Type = 2
  UnderTolerance = 0
  X = 182.719
  Y = 2.20045
FEATURE [TechDraw::DrawViewDimension] Dimension149
  Arbitrary = false
  ArbitraryTolerances = false
  EqualTolerance = true
  FormatSpec = %.2f
  FormatSpecOverTolerance = %+.2f
  FormatSpecUnderTolerance = %+.2f
  Inverted = false
  LockPosition = false
  MeasureType = 1
  OverTolerance = 0
  References2D = -> [View005]
  Rotation = 0
  ScaleType = 0
  TheoreticalExact = false
  Type = 2
  UnderTolerance = 0
  X = 105.103
  Y = -54.9269
FEATURE [TechDraw::DrawViewDimension] Dimension150
  Arbitrary = false
  ArbitraryTolerances = false
  EqualTolerance = true
  FormatSpec = %.2f
  FormatSpecOverTolerance = %+.2f
  FormatSpecUnderTolerance = %+.2f
  Inverted = false
  LockPosition = false
  MeasureType = 1
  OverTolerance = 0
  References2D = -> [View005]
  Rotation = 0
  ScaleType = 0
  TheoreticalExact = false
  Type = 2
  UnderTolerance = 0
  X = 114.705
  Y = -55.0156
FEATURE [TechDraw::DrawViewDimension] Dimension151
  Arbitrary = false
  ArbitraryTolerances = false
  EqualTolerance = true
  FormatSpec = %.2f
  FormatSpecOverTolerance = %+.2f
  FormatSpecUnderTolerance = %+.2f
  Inverted = false
  LockPosition = false
  MeasureType = 1
  OverTolerance = 0
  References2D = -> [View005]
  Rotation = 0
  ScaleType = 0
  TheoreticalExact = false
  Type = 2
  UnderTolerance = 0
  X = 104.625
  Y = 61.182
FEATURE [TechDraw::DrawViewDimension] Dimension152
  Arbitrary = false
  ArbitraryTolerances = false
  EqualTolerance = true
  FormatSpec = %.2f
  FormatSpecOverTolerance = %+.2f
  FormatSpecUnderTolerance = %+.2f
  Inverted = false
  LockPosition = false
  MeasureType = 1
  OverTolerance = 0
  References2D = -> [View005]
  Rotation = 0
  ScaleType = 0
  TheoreticalExact = false
  Type = 1
  UnderTolerance = 0
  X = -103.996
  Y = -83.4691
FEATURE [TechDraw::DrawPage] Page005  label="Outer_side_frame_Drawing"
  KeepUpdated = true
  NextBalloonIndex = 1
  ProjectionType = 0
  Template = -> Template005
  Views = -> [View005,Dimension107,Dimension112,SectionView005,Dimension117,SectionView006,Dimension119,Dimension139,Dimension140,Dimension141,Dimension142,Dimension143,Dimension144,Dimension145,Dimension146,Dimension147,Dimension148,Dimension149,Dimension150,Dimension151,Dimension152]
FEATURE [Sketcher::SketchObject] Sketch038
  FullyConstrained = true
  MapMode = 5
  Support = -> [XY_Plane018]
  sketch-geometry (4):
    g0: LineSegment StartX=-1000 StartY=600 StartZ=0 EndX=1000 EndY=600 EndZ=0
    g1: LineSegment StartX=1000 StartY=600 StartZ=0 EndX=1000 EndY=-600 EndZ=0
    g2: LineSegment StartX=1000 StartY=-600 StartZ=0 EndX=-1000 EndY=-600 EndZ=0
    g3: LineSegment StartX=-1000 StartY=-600 StartZ=0 EndX=-1000 EndY=600 EndZ=0
  constraints (11):
    c: Coincident(g0,g1)
    c: Coincident(g1,g2)
    c: Coincident(g2,g3)
    c: Coincident(g3,g0)
    c: Horizontal(g0)
    c: Horizontal(g2)
    c: Vertical(g1)
    c: Vertical(g3)
    c: Symmetric(g0,g1,g-1)
    c: DistanceX(g0,g0) = 2000
    c: DistanceY(g2,g0) = 1200
FEATURE [PartDesign::Pad] Pad018
  Direction = (1,1,1)
  Length = 2
  Length2 = 100
  Profile = -> Sketch038
  Type = 0
FEATURE [PartDesign::Body] Body018  label="Undersida"
  Group = -> [Sketch038,Pad018]
  Origin = -> Origin018
  Placement = pos=(0,0,-52) rot=(0,0,1;0rad)
  Tip = -> Pad018
FEATURE [App::DocumentObjectGroupPython] SimpleGroup045  label="SimpleGroup007"  # scripted group (container) (typed FeaturePython)
  AnimationStepTime = 0.01
  AnimationSteps = 200
  Distance = 1500
  Revolutions = 0
FEATURE [App::DocumentObjectGroupPython] SimpleGroup046  label="SimpleGroup008"  # scripted group (container) (typed FeaturePython)
  AnimationStepTime = 0.01
  AnimationSteps = 200
  Distance = 3000
  Revolutions = 0
FEATURE [App::DocumentObjectGroupPython] SimpleGroup047  label="SimpleGroup009"  # scripted group (container) (typed FeaturePython)
  AnimationStepTime = 0.01
  AnimationSteps = 200
  Distance = 0
  Revolutions = 0.25
FEATURE [Part::Feature] trajectory_line
  shape: bbox 2e-07 x 2e-07 x 600 mm, 0 faces, 0 solids (baked)
FEATURE [App::DocumentObjectGroupPython] SimpleGroup  # scripted group (container) (typed FeaturePython)
  AnimationStepTime = 0.01
  AnimationSteps = 200
  Distance = 600
  Group = -> [trajectory_line]
  Revolutions = 0
FEATURE [Part::Feature] trajectory_line001
  shape: bbox 3000 x 2e-07 x 2e-07 mm, 0 faces, 0 solids (baked)
FEATURE [App::DocumentObjectGroupPython] SimpleGroup001  # scripted group (container) (typed FeaturePython)
  AnimationStepTime = 0.01
  AnimationSteps = 200
  Distance = 3000
  Group = -> [trajectory_line001]
  Revolutions = 0
FEATURE [Part::Feature] trajectory_line002
  shape: bbox 2e-07 x 2e-07 x 704 mm, 0 faces, 0 solids (baked)
FEATURE [App::DocumentObjectGroupPython] SimpleGroup002  # scripted group (container) (typed FeaturePython)
  AnimationStepTime = 0.01
  AnimationSteps = 200
  Distance = 704
  Group = -> [trajectory_line002]
  Revolutions = 0
FEATURE [Part::Feature] trajectory_line003
  shape: bbox 2e-07 x 2e-07 x 600 mm, 0 faces, 0 solids (baked)
FEATURE [App::DocumentObjectGroupPython] SimpleGroup003  # scripted group (container) (typed FeaturePython)
  AnimationStepTime = 0.01
  AnimationSteps = 200
  Distance = 600
  Group = -> [trajectory_line003]
  Revolutions = 0
FEATURE [Part::Feature] trajectory_line004
  shape: bbox 3000 x 2e-07 x 2e-07 mm, 0 faces, 0 solids (baked)
FEATURE [App::DocumentObjectGroupPython] SimpleGroup004  # scripted group (container) (typed FeaturePython)
  AnimationStepTime = 0.01
  AnimationSteps = 200
  Distance = 3000
  Group = -> [trajectory_line004]
  Revolutions = 0
FEATURE [Part::Feature] trajectory_line005
  shape: bbox 2e-07 x 1300 x 2e-07 mm, 0 faces, 0 solids (baked)
FEATURE [App::DocumentObjectGroupPython] SimpleGroup005  # scripted group (container) (typed FeaturePython)
  AnimationStepTime = 0.01
  AnimationSteps = 200
  Distance = 1300
  Group = -> [trajectory_line005]
  Revolutions = 0
FEATURE [Part::Feature] trajectory_line006
  shape: bbox 2e-07 x 2e-07 x 700 mm, 0 faces, 0 solids (baked)
FEATURE [App::DocumentObjectGroupPython] SimpleGroup006  # scripted group (container) (typed FeaturePython)
  AnimationStepTime = 0.01
  AnimationSteps = 200
  Distance = 700
  Group = -> [trajectory_line006]
  Revolutions = 0
FEATURE [App::DocumentObjectGroupPython] ExplodedAssembly  # scripted group (container) (typed FeaturePython)
  AnimationStep = 0
  CurrentTrajectory = 0
  Group = -> [SimpleGroup,SimpleGroup001,SimpleGroup002,SimpleGroup003,SimpleGroup004,SimpleGroup005,SimpleGroup006,SimpleGroup045,SimpleGroup046,SimpleGroup047,SimpleGroup011,SimpleGroup012,SimpleGroup013,SimpleGroup014,SimpleGroup015,SimpleGroup016,SimpleGroup017,SimpleGroup018,SimpleGroup019,SimpleGroup020,SimpleGroup021,SimpleGroup022,SimpleGroup023,SimpleGroup024,SimpleGroup025,SimpleGroup026,+18 more]
  InAnimation = false
  RemoveAllTrajectories = false
  ResetAnimation = false
FEATURE [TechDraw::DrawSVGTemplate] Template010
  Height = 297
  Orientation = 1
  Width = 420
FEATURE [TechDraw::DrawViewPart] View010
  CoarseView = false
  Direction = (0,0,1)
  Focus = 100
  HardHidden = false
  IsoCount = 0
  IsoHidden = false
  IsoVisible = false
  LockPosition = false
  Perspective = false
  Rotation = 0
  Scale = 0.15
  ScaleType = 0
  SeamHidden = false
  SeamVisible = true
  SmoothHidden = false
  SmoothVisible = true
  Source = -> [Body018]
  X = 182.583
  XDirection = (1,0,0)
  Y = 166.798
FEATURE [TechDraw::DrawViewDimension] Dimension153
  Arbitrary = false
  ArbitraryTolerances = false
  EqualTolerance = true
  FormatSpec = %.2f
  FormatSpecOverTolerance = %+.2f
  FormatSpecUnderTolerance = %+.2f
  Inverted = false
  LockPosition = false
  MeasureType = 1
  OverTolerance = 0
  References2D = -> [View010]
  Rotation = 0
  ScaleType = 0
  TheoreticalExact = false
  Type = 1
  UnderTolerance = 0
  X = -0.497765
  Y = 117.211
FEATURE [TechDraw::DrawViewSection] SectionView010  label="Section K - K"
  BaseView = -> View010
  CoarseView = false
  CutSurfaceDisplay = 2
  Direction = (-1,0,0)
  FileGeomPattern = <userpath>/AppData/Local/Programs/FreeCAD 0.19/data/Mod/TechDraw/PAT/FCPAT.pat
  FileHatchPattern = <userpath>/AppData/Local/Programs/FreeCAD 0.19/data/Mod/TechDraw/Patterns/simple.svg
  Focus = 100
  FuseBeforeCut = false
  HardHidden = false
  HatchScale = 1
  IsoCount = 0
  IsoHidden = false
  IsoVisible = false
  LockPosition = false
  NameGeomPattern = Diamond
  Perspective = false
  Rotation = 0
  Scale = 0.15
  ScaleType = 0
  SeamHidden = false
  SeamVisible = true
  SectionDirection = 0
  SectionNormal = (-1,0,0)
  SectionOrigin = (0,0,-51)
  SectionSymbol = K
  SmoothHidden = false
  SmoothVisible = true
  Source = -> [Body018]
  X = 366.677
  XDirection = (0,0,1)
  Y = 166.915
FEATURE [TechDraw::DrawViewDimension] Dimension154
  Arbitrary = false
  ArbitraryTolerances = false
  EqualTolerance = true
  FormatSpec = %.2f
  FormatSpecOverTolerance = %+.2f
  FormatSpecUnderTolerance = %+.2f
  Inverted = false
  LockPosition = false
  MeasureType = 1
  OverTolerance = 0
  References2D = -> [View010]
  Rotation = 0
  ScaleType = 0
  TheoreticalExact = false
  Type = 2
  UnderTolerance = 0
  X = 206.413
  Y = -2.48883
FEATURE [TechDraw::DrawViewDimension] Dimension155
  Arbitrary = false
  ArbitraryTolerances = false
  EqualTolerance = true
  FormatSpec = %.2f
  FormatSpecOverTolerance = %+.2f
  FormatSpecUnderTolerance = %+.2f
  Inverted = false
  LockPosition = false
  MeasureType = 1
  OverTolerance = 0
  References2D = -> [SectionView010]
  Rotation = 0
  ScaleType = 0
  TheoreticalExact = false
  Type = 1
  UnderTolerance = 0
  X = 14.0034
  Y = 100.514
FEATURE [TechDraw::DrawPage] Page010  label="Bottom_cover_Drawing"
  KeepUpdated = true
  NextBalloonIndex = 1
  ProjectionType = 0
  Template = -> Template010
  Views = -> [View010,Dimension153,SectionView010,Dimension154,Dimension155]
FEATURE [Sketcher::SketchObject] Sketch039
  FullyConstrained = true
  MapMode = 5
  Placement = pos=(0,0,0) rot=(0.57735,0.57735,0.57735;2.0944rad)
  Support = -> [YZ_Plane019]
  sketch-geometry (7):
    g0: GeomPoint X=0 Y=70.3 Z=0
    g1: GeomPoint X=0 Y=-52 Z=0
    g2: LineSegment StartX=0 StartY=-52 StartZ=0 EndX=0 EndY=70.3 EndZ=0
    g3: LineSegment StartX=0 StartY=70.3 StartZ=0 EndX=-277.128 EndY=-89.7 EndZ=0
    g4: GeomPoint X=-277.128 Y=-119.7 Z=0
    g5: LineSegment StartX=-277.128 StartY=-89.7 StartZ=0 EndX=-277.128 EndY=-119.7 EndZ=0
    g6: LineSegment StartX=-277.128 StartY=-119.7 StartZ=0 EndX=0 EndY=-52 EndZ=0
  constraints (15):
    c: PointOnObject(g0,g-2)
    c: DistanceY(g-1,g0) = 70.3
    c: PointOnObject(g1,g-2)
    c: DistanceY(g1,g-1) = 52
    c: Coincident(g2,g1)
    c: Coincident(g2,g0)
    c: Coincident(g3,g2)
    c: Angle(g3,g2) = 1.0472
    c: Distance(g2,g3) = 320
    c: Vertical(g3,g4)
    c: Coincident(g5,g3)
    c: Coincident(g5,g4)
    c: Coincident(g6,g5)
    c: Coincident(g6,g2)
    c: DistanceY(g5,g3) = 30
FEATURE [PartDesign::Pad] Pad019
  Direction = (1,1,1)
  Length = 4
  Length2 = 100
  Placement = pos=(0,0,0) rot=(0.57735,0.57735,0.57735;2.0944rad)
  Profile = -> Sketch039
  Type = 0
FEATURE [Sketcher::SketchObject] Sketch040
  ExternalGeometry = -> [Pad019]
  FullyConstrained = true
  MapMode = 5
  Placement = pos=(4,-9e-16,9e-16) rot=(0.57735,0.57735,0.57735;2.0944rad)
  Support = -> [Pad019]
  sketch-geometry (20):
    g0: LineSegment StartX=0 StartY=-52 StartZ=0 EndX=-4 EndY=-52 EndZ=0
    g1: LineSegment StartX=-4 StartY=-52 StartZ=0 EndX=-4 EndY=-34.53 EndZ=0
    g2: LineSegment StartX=-4 StartY=-34.53 StartZ=0 EndX=0 EndY=-34.53 EndZ=0
    g3: LineSegment StartX=0 StartY=-34.53 StartZ=0 EndX=0 EndY=-52 EndZ=0
    g4: LineSegment StartX=0 StartY=-17.06 StartZ=0 EndX=-4 EndY=-17.06 EndZ=0
    g5: LineSegment StartX=-4 StartY=-17.06 StartZ=0 EndX=-4 EndY=0.41 EndZ=0
    g6: LineSegment StartX=-4 StartY=0.41 StartZ=0 EndX=0 EndY=0.41 EndZ=0
    g7: LineSegment StartX=0 StartY=0.41 StartZ=0 EndX=0 EndY=-17.06 EndZ=0
    g8: LineSegment StartX=0 StartY=17.88 StartZ=0 EndX=-4 EndY=17.88 EndZ=0
    g9: LineSegment StartX=-4 StartY=17.88 StartZ=0 EndX=-4 EndY=35.35 EndZ=0
    g10: LineSegment StartX=-4 StartY=35.35 StartZ=0 EndX=0 EndY=35.35 EndZ=0
    g11: LineSegment StartX=0 StartY=35.35 StartZ=0 EndX=0 EndY=17.88 EndZ=0
    g12: LineSegment StartX=-277.128 StartY=-99.7 StartZ=0 EndX=-273.128 EndY=-99.7 EndZ=0
    g13: LineSegment StartX=-273.128 StartY=-99.7 StartZ=0 EndX=-273.128 EndY=-109.7 EndZ=0
    g14: LineSegment StartX=-273.128 StartY=-109.7 StartZ=0 EndX=-277.128 EndY=-109.7 EndZ=0
    g15: LineSegment StartX=-277.128 StartY=-109.7 StartZ=0 EndX=-277.128 EndY=-99.7 EndZ=0
    g16: LineSegment StartX=0 StartY=52.83 StartZ=0 EndX=2.34e-14 EndY=70.3 EndZ=0
    g17: LineSegment StartX=2.34e-14 StartY=70.3 StartZ=0 EndX=-4 EndY=67.9906 EndZ=0
    g18: LineSegment StartX=-4 StartY=67.9906 StartZ=0 EndX=-4 EndY=52.83 EndZ=0
    g19: LineSegment StartX=-4 StartY=52.83 StartZ=0 EndX=0 EndY=52.83 EndZ=0
  constraints (59):
    c: DistanceY(g-4,g-3) = 122.3
    c: Coincident(g0,g1)
    c: Coincident(g1,g2)
    c: Coincident(g2,g3)
    c: Coincident(g3,g0)
    c: Horizontal(g0)
    c: Horizontal(g2)
    c: Vertical(g1)
    c: Vertical(g3)
    c: Coincident(g0,g-4)
    c: Coincident(g4,g5)
    c: Coincident(g5,g6)
    c: Coincident(g6,g7)
    c: Coincident(g7,g4)
    c: Horizontal(g4)
    c: Horizontal(g6)
    c: Vertical(g5)
    c: Vertical(g7)
    c: PointOnObject(g4,g-2)
    c: Coincident(g8,g9)
    c: Coincident(g9,g10)
    c: Coincident(g10,g11)
    c: Coincident(g11,g8)
    c: Horizontal(g8)
    c: Horizontal(g10)
    c: Vertical(g9)
    c: Vertical(g11)
    c: PointOnObject(g8,g-2)
    c: DistanceY(g0,g2) = 17.47
    c: Equal(g3,g7)
    c: Equal(g7,g11)
    c: DistanceY(g2,g4) = 17.47
    c: DistanceY(g6,g8) = 17.47
    c: Vertical(g1,g4)
    c: Vertical(g5,g8)
    c: DistanceX(g0,g0) = 4
    c: Coincident(g12,g13)
    c: Coincident(g13,g14)
    c: Coincident(g14,g15)
    c: Coincident(g15,g12)
    c: Horizontal(g12)
    c: Horizontal(g14)
    c: Vertical(g13)
    c: Vertical(g15)
    c: PointOnObject(g12,g-5)
    c: DistanceY(g-5,g14) = 10
    c: DistanceY(g14,g12) = 10
    c: DistanceX(g14,g13) = 4
    c: PointOnObject(g16,g-2)
    c: Coincident(g16,g-3)
    c: Equal(g11,g16)
    c: Coincident(g17,g16)
    c: PointOnObject(g17,g-3)
    c: Coincident(g18,g17)
    c: Vertical(g18)
    c: Coincident(g19,g18)
    c: Coincident(g19,g16)
    c: Horizontal(g18,g16)
    c: Vertical(g9,g18)
FEATURE [PartDesign::Pocket] Pocket017
  BaseFeature = -> Pad019
  Length = 4
  Length2 = 100
  Placement = pos=(0,0,0) rot=(0.57735,0.57735,0.57735;2.0944rad)
  Profile = -> Sketch040
  Type = 0
FEATURE [Sketcher::SketchObject] Sketch041
  FullyConstrained = true
  MapMode = 5
  Placement = pos=(0,0,0) rot=(1,0,0;1.5708rad)
  Support = -> [XZ_Plane020]
  sketch-geometry (4):
    g0: LineSegment StartX=-1004 StartY=75 StartZ=0 EndX=1004 EndY=75 EndZ=0
    g1: LineSegment StartX=1004 StartY=75 StartZ=0 EndX=1004 EndY=-52 EndZ=0
    g2: LineSegment StartX=1004 StartY=-52 StartZ=0 EndX=-1004 EndY=-52 EndZ=0
    g3: LineSegment StartX=-1004 StartY=-52 StartZ=0 EndX=-1004 EndY=75 EndZ=0
  constraints (12):
    c: Coincident(g0,g1)
    c: Coincident(g1,g2)
    c: Coincident(g2,g3)
    c: Coincident(g3,g0)
    c: Horizontal(g0)
    c: Horizontal(g2)
    c: Vertical(g1)
    c: Vertical(g3)
    c: DistanceX(g0,g0) = 2008
    c: DistanceX(g2,g-1) = 1004
    c: DistanceY(g1,g-1) = 52
    c: DistanceY(g-1,g0) = 75
FEATURE [PartDesign::Pad] Pad020
  Direction = (1,1,1)
  Length = 4
  Length2 = 100
  Placement = pos=(0,0,0) rot=(1,0,0;1.5708rad)
  Profile = -> Sketch041
  Type = 0
FEATURE [Sketcher::SketchObject] Sketch042
  ExternalGeometry = -> [Pad020]
  FullyConstrained = true
  MapMode = 5
  Placement = pos=(0,-4,1.8e-15) rot=(1,0,0;1.5708rad)
  Support = -> [Pad020]
  sketch-geometry (96):
    g0: GeomPoint X=100.4 Y=11.5 Z=0
    g1: GeomPoint X=301.2 Y=11.5 Z=0
    g2: GeomPoint X=502 Y=11.5 Z=0
    g3: GeomPoint X=702.8 Y=11.5 Z=0
    g4: GeomPoint X=903.6 Y=11.5 Z=0
    g5: Circle CenterX=100.4 CenterY=11.5 CenterZ=0 NormalX=0 NormalY=0 NormalZ=1 AngleXU=0 Radius=40
    g6: Circle CenterX=301.2 CenterY=11.5 CenterZ=0 NormalX=0 NormalY=0 NormalZ=1 AngleXU=0 Radius=40
    g7: Circle CenterX=502 CenterY=11.5 CenterZ=0 NormalX=0 NormalY=0 NormalZ=1 AngleXU=0 Radius=40
    g8: Circle CenterX=702.8 CenterY=11.5 CenterZ=0 NormalX=0 NormalY=0 NormalZ=1 AngleXU=0 Radius=40
    g9: Circle CenterX=903.6 CenterY=11.5 CenterZ=0 NormalX=0 NormalY=0 NormalZ=1 AngleXU=0 Radius=40
    g10: GeomPoint X=-100.4 Y=11.5 Z=0
    g11: GeomPoint X=-301.2 Y=11.5 Z=0
    g12: GeomPoint X=-502 Y=11.5 Z=0
    g13: GeomPoint X=-702.8 Y=11.5 Z=0
    g14: GeomPoint X=-903.6 Y=11.5 Z=0
    g15: Circle CenterX=-100.4 CenterY=11.5 CenterZ=0 NormalX=0 NormalY=0 NormalZ=1 AngleXU=0 Radius=40
    g16: Circle CenterX=-301.2 CenterY=11.5 CenterZ=0 NormalX=0 NormalY=0 NormalZ=1 AngleXU=0 Radius=40
    g17: Circle CenterX=-502 CenterY=11.5 CenterZ=0 NormalX=0 NormalY=0 NormalZ=1 AngleXU=0 Radius=40
    g18: Circle CenterX=-702.8 CenterY=11.5 CenterZ=0 NormalX=0 NormalY=0 NormalZ=1 AngleXU=0 Radius=40
    g19: Circle CenterX=-903.6 CenterY=11.5 CenterZ=0 NormalX=0 NormalY=0 NormalZ=1 AngleXU=0 Radius=40
    g20: LineSegment StartX=1004 StartY=-34.53 StartZ=0 EndX=1000 EndY=-34.53 EndZ=0
    g21: LineSegment StartX=1000 StartY=-34.53 StartZ=0 EndX=1000 EndY=-17.06 EndZ=0
    g22: LineSegment StartX=1000 StartY=-17.06 StartZ=0 EndX=1004 EndY=-17.06 EndZ=0
    g23: LineSegment StartX=1004 StartY=-17.06 StartZ=0 EndX=1004 EndY=-34.53 EndZ=0
    g24: LineSegment StartX=1004 StartY=0.39 StartZ=0 EndX=1000 EndY=0.39 EndZ=0
    g25: LineSegment StartX=1000 StartY=0.39 StartZ=0 EndX=1000 EndY=17.86 EndZ=0
    g26: LineSegment StartX=1000 StartY=17.86 StartZ=0 EndX=1004 EndY=17.86 EndZ=0
    g27: LineSegment StartX=1004 StartY=17.86 StartZ=0 EndX=1004 EndY=0.39 EndZ=0
    g28: LineSegment StartX=1004 StartY=35.33 StartZ=0 EndX=1000 EndY=35.33 EndZ=0
    g29: LineSegment StartX=1000 StartY=35.33 StartZ=0 EndX=1000 EndY=52.8 EndZ=0
    g30: LineSegment StartX=1000 StartY=52.8 StartZ=0 EndX=1004 EndY=52.8 EndZ=0
    g31: LineSegment StartX=1004 StartY=52.8 StartZ=0 EndX=1004 EndY=35.33 EndZ=0
    g32: LineSegment StartX=-1004 StartY=52.8 StartZ=0 EndX=-1000 EndY=52.8 EndZ=0
    g33: LineSegment StartX=-1000 StartY=52.8 StartZ=0 EndX=-1000 EndY=35.33 EndZ=0
    g34: LineSegment StartX=-1000 StartY=35.33 StartZ=0 EndX=-1004 EndY=35.33 EndZ=0
    g35: LineSegment StartX=-1004 StartY=35.33 StartZ=0 EndX=-1004 EndY=52.8 EndZ=0
    g36: LineSegment StartX=-1004 StartY=17.86 StartZ=0 EndX=-1000 EndY=17.86 EndZ=0
    g37: LineSegment StartX=-1000 StartY=17.86 StartZ=0 EndX=-1000 EndY=0.39 EndZ=0
    g38: LineSegment StartX=-1000 StartY=0.39 StartZ=0 EndX=-1004 EndY=0.39 EndZ=0
    g39: LineSegment StartX=-1004 StartY=0.39 StartZ=0 EndX=-1004 EndY=17.86 EndZ=0
    g40: LineSegment StartX=-1004 StartY=-17.06 StartZ=0 EndX=-1000 EndY=-17.06 EndZ=0
    g41: LineSegment StartX=-1000 StartY=-17.06 StartZ=0 EndX=-1000 EndY=-34.53 EndZ=0
    g42: LineSegment StartX=-1000 StartY=-34.53 StartZ=0 EndX=-1004 EndY=-34.53 EndZ=0
    g43: LineSegment StartX=-1004 StartY=-34.53 StartZ=0 EndX=-1004 EndY=-17.06 EndZ=0
    g44: LineSegment StartX=600.4 StartY=52.8 StartZ=0 EndX=604.4 EndY=52.8 EndZ=0
    g45: LineSegment StartX=604.4 StartY=52.8 StartZ=0 EndX=604.4 EndY=35.33 EndZ=0
    g46: LineSegment StartX=604.4 StartY=35.33 StartZ=0 EndX=600.4 EndY=35.33 EndZ=0
    g47: LineSegment StartX=600.4 StartY=35.33 StartZ=0 EndX=600.4 EndY=52.8 EndZ=0
    g48: LineSegment StartX=600.4 StartY=17.86 StartZ=0 EndX=604.4 EndY=17.86 EndZ=0
    g49: LineSegment StartX=604.4 StartY=17.86 StartZ=0 EndX=604.4 EndY=0.39 EndZ=0
    g50: LineSegment StartX=604.4 StartY=0.39 StartZ=0 EndX=600.4 EndY=0.39 EndZ=0
    g51: LineSegment StartX=600.4 StartY=0.39 StartZ=0 EndX=600.4 EndY=17.86 EndZ=0
    g52: LineSegment StartX=600.4 StartY=-17.06 StartZ=0 EndX=604.4 EndY=-17.06 EndZ=0
    g53: LineSegment StartX=604.4 StartY=-17.06 StartZ=0 EndX=604.4 EndY=-34.53 EndZ=0
    g54: LineSegment StartX=604.4 StartY=-34.53 StartZ=0 EndX=600.4 EndY=-34.53 EndZ=0
    g55: LineSegment StartX=600.4 StartY=-34.53 StartZ=0 EndX=600.4 EndY=-17.06 EndZ=0
    g56: GeomPoint X=602.4 Y=0 Z=0
    g57: LineSegment StartX=198.8 StartY=52.8 StartZ=0 EndX=202.8 EndY=52.8 EndZ=0
    g58: LineSegment StartX=202.8 StartY=52.8 StartZ=0 EndX=202.8 EndY=35.33 EndZ=0
    g59: LineSegment StartX=202.8 StartY=35.33 StartZ=0 EndX=198.8 EndY=35.33 EndZ=0
    g60: LineSegment StartX=198.8 StartY=35.33 StartZ=0 EndX=198.8 EndY=52.8 EndZ=0
    g61: LineSegment StartX=198.8 StartY=17.86 StartZ=0 EndX=202.8 EndY=17.86 EndZ=0
    g62: LineSegment StartX=202.8 StartY=17.86 StartZ=0 EndX=202.8 EndY=0.39 EndZ=0
    g63: LineSegment StartX=202.8 StartY=0.39 StartZ=0 EndX=198.8 EndY=0.39 EndZ=0
    g64: LineSegment StartX=198.8 StartY=0.39 StartZ=0 EndX=198.8 EndY=17.86 EndZ=0
    g65: LineSegment StartX=198.8 StartY=-17.06 StartZ=0 EndX=202.8 EndY=-17.06 EndZ=0
    g66: LineSegment StartX=202.8 StartY=-17.06 StartZ=0 EndX=202.8 EndY=-34.53 EndZ=0
    g67: LineSegment StartX=202.8 StartY=-34.53 StartZ=0 EndX=198.8 EndY=-34.53 EndZ=0
    g68: LineSegment StartX=198.8 StartY=-34.53 StartZ=0 EndX=198.8 EndY=-17.06 EndZ=0
    g69: GeomPoint X=200.8 Y=0 Z=0
    g70: LineSegment StartX=-202.8 StartY=52.8 StartZ=0 EndX=-198.8 EndY=52.8 EndZ=0
    g71: LineSegment StartX=-198.8 StartY=52.8 StartZ=0 EndX=-198.8 EndY=35.33 EndZ=0
    g72: LineSegment StartX=-198.8 StartY=35.33 StartZ=0 EndX=-202.8 EndY=35.33 EndZ=0
    g73: LineSegment StartX=-202.8 StartY=35.33 StartZ=0 EndX=-202.8 EndY=52.8 EndZ=0
    g74: LineSegment StartX=-202.8 StartY=17.86 StartZ=0 EndX=-198.8 EndY=17.86 EndZ=0
    g75: LineSegment StartX=-198.8 StartY=17.86 StartZ=0 EndX=-198.8 EndY=0.39 EndZ=0
    g76: LineSegment StartX=-198.8 StartY=0.39 StartZ=0 EndX=-202.8 EndY=0.39 EndZ=0
    g77: LineSegment StartX=-202.8 StartY=0.39 StartZ=0 EndX=-202.8 EndY=17.86 EndZ=0
    g78: LineSegment StartX=-202.8 StartY=-17.06 StartZ=0 EndX=-198.8 EndY=-17.06 EndZ=0
    g79: LineSegment StartX=-198.8 StartY=-17.06 StartZ=0 EndX=-198.8 EndY=-34.53 EndZ=0
    g80: LineSegment StartX=-198.8 StartY=-34.53 StartZ=0 EndX=-202.8 EndY=-34.53 EndZ=0
    g81: LineSegment StartX=-202.8 StartY=-34.53 StartZ=0 EndX=-202.8 EndY=-17.06 EndZ=0
    g82: GeomPoint X=-200.8 Y=0 Z=0
    g83: LineSegment StartX=-604.4 StartY=52.8 StartZ=0 EndX=-600.4 EndY=52.8 EndZ=0
    g84: LineSegment StartX=-600.4 StartY=52.8 StartZ=0 EndX=-600.4 EndY=35.33 EndZ=0
    g85: LineSegment StartX=-600.4 StartY=35.33 StartZ=0 EndX=-604.4 EndY=35.33 EndZ=0
    g86: LineSegment StartX=-604.4 StartY=35.33 StartZ=0 EndX=-604.4 EndY=52.8 EndZ=0
    g87: LineSegment StartX=-604.4 StartY=17.86 StartZ=0 EndX=-600.4 EndY=17.86 EndZ=0
    g88: LineSegment StartX=-600.4 StartY=17.86 StartZ=0 EndX=-600.4 EndY=0.39 EndZ=0
    g89: LineSegment StartX=-600.4 StartY=0.39 StartZ=0 EndX=-604.4 EndY=0.39 EndZ=0
    g90: LineSegment StartX=-604.4 StartY=0.39 StartZ=0 EndX=-604.4 EndY=17.86 EndZ=0
    g91: LineSegment StartX=-604.4 StartY=-17.06 StartZ=0 EndX=-600.4 EndY=-17.06 EndZ=0
    g92: LineSegment StartX=-600.4 StartY=-17.06 StartZ=0 EndX=-600.4 EndY=-34.53 EndZ=0
    g93: LineSegment StartX=-600.4 StartY=-34.53 StartZ=0 EndX=-604.4 EndY=-34.53 EndZ=0
    g94: LineSegment StartX=-604.4 StartY=-34.53 StartZ=0 EndX=-604.4 EndY=-17.06 EndZ=0
    g95: GeomPoint X=-602.4 Y=0 Z=0
  constraints (264):
    c: DistanceX(g4,g-3) = 100.4
    c: DistanceX(g3,g4) = 200.8
    c: DistanceX(g2,g3) = 200.8
    c: DistanceX(g1,g2) = 200.8
    c: DistanceX(g0,g1) = 200.8
    c: Horizontal(g4,g3)
    c: Horizontal(g3,g2)
    c: Horizontal(g2,g1)
    c: Horizontal(g1,g0)
    c: DistanceY(g4,g-4) = 63.5
    c: Coincident(g5,g0)
    c: Coincident(g6,g1)
    c: Coincident(g7,g2)
    c: Coincident(g8,g3)
    c: Coincident(g9,g4)
    c: Radius(g9) = 40
    c: Radius(g8) = 40
    c: Radius(g7) = 40
    c: Radius(g6) = 40
    c: Radius(g5) = 40
    c: Horizontal(g5,g10)
    c: Horizontal(g10,g11)
    c: Horizontal(g11,g12)
    c: Horizontal(g12,g13)
    c: Horizontal(g13,g14)
    c: DistanceX(g10,g5) = 200.8
    c: DistanceX(g11,g10) = 200.8
    c: DistanceX(g12,g11) = 200.8
    c: DistanceX(g13,g12) = 200.8
    c: DistanceX(g14,g13) = 200.8
    c: Coincident(g15,g10)
    c: Coincident(g16,g11)
    c: Coincident(g17,g12)
    c: Coincident(g18,g13)
    c: Coincident(g19,g14)
    c: Radius(g19) = 40
    c: Radius(g18) = 40
    c: Radius(g17) = 40
    c: Radius(g16) = 40
    c: Radius(g15) = 40
    c: Coincident(g20,g21)
    c: Coincident(g21,g22)
    c: Coincident(g22,g23)
    c: Coincident(g23,g20)
    c: Horizontal(g20)
    c: Horizontal(g22)
    c: Vertical(g21)
    c: Vertical(g23)
    c: Coincident(g24,g25)
    c: Coincident(g25,g26)
    c: Coincident(g26,g27)
    c: Coincident(g27,g24)
    c: Horizontal(g24)
    c: Horizontal(g26)
    c: Vertical(g25)
    c: Vertical(g27)
    c: Coincident(g28,g29)
    c: Coincident(g29,g30)
    c: Coincident(g30,g31)
    c: Coincident(g31,g28)
    c: Horizontal(g28)
    c: Horizontal(g30)
    c: Vertical(g29)
    c: Vertical(g31)
    c: Vertical(g-3,g20)
    c: Vertical(g22,g24)
    c: Vertical(g26,g28)
    c: Vertical(g21,g24)
    c: Vertical(g25,g28)
    c: Equal(g23,g27)
    c: Equal(g27,g31)
    c: DistanceY(g-3,g20) = 17.47
    c: DistanceY(g20,g22) = 17.47
    c: DistanceY(g22,g24) = 17.45
    c: DistanceY(g26,g28) = 17.47
    c: DistanceX(g20,g20) = 4
    c: Coincident(g32,g33)
    c: Coincident(g33,g34)
    c: Coincident(g34,g35)
    c: Coincident(g35,g32)
    c: Horizontal(g32)
    c: Horizontal(g34)
    c: Vertical(g33)
    c: Vertical(g35)
    c: Coincident(g36,g37)
    c: Coincident(g37,g38)
    c: Coincident(g38,g39)
    c: Coincident(g39,g36)
    c: Horizontal(g36)
    c: Horizontal(g38)
    c: Vertical(g37)
    c: Vertical(g39)
    c: Coincident(g40,g41)
    c: Coincident(g41,g42)
    c: Coincident(g42,g43)
    c: Coincident(g43,g40)
    c: Horizontal(g40)
    c: Horizontal(g42)
    c: Vertical(g41)
    c: Vertical(g43)
    c: Vertical(g-5,g42)
    c: Vertical(g40,g38)
    c: Vertical(g36,g34)
    c: Vertical(g40,g37)
    c: Vertical(g36,g33)
    c: DistanceX(g42,g41) = 4
    c: Horizontal(g41,g20)
    c: Horizontal(g21,g40)
    c: Horizontal(g37,g24)
    c: Horizontal(g25,g36)
    c: Horizontal(g33,g28)
    c: Equal(g39,g35)
    c: Coincident(g44,g45)
    c: Coincident(g45,g46)
    c: Coincident(g46,g47)
    c: Coincident(g47,g44)
    c: Horizontal(g44)
    c: Horizontal(g46)
    c: Vertical(g45)
    c: Vertical(g47)
    c: Coincident(g48,g49)
    c: Coincident(g49,g50)
    c: Coincident(g50,g51)
    c: Coincident(g51,g48)
    c: Horizontal(g48)
    c: Horizontal(g50)
    c: Vertical(g49)
    c: Vertical(g51)
    c: Coincident(g52,g53)
    c: Coincident(g53,g54)
    c: Coincident(g54,g55)
    c: Coincident(g55,g52)
    c: Horizontal(g52)
    c: Horizontal(g54)
    c: Vertical(g53)
    c: Vertical(g55)
    c: Vertical(g52,g49)
    c: Vertical(g48,g45)
    c: Vertical(g52,g50)
    c: Vertical(g48,g46)
    c: DistanceX(g54,g53) = 4
    c: PointOnObject(g56,g-1)
    c: DistanceX(g54,g56) = 2
    c: Coincident(g57,g58)
    c: Coincident(g58,g59)
    c: Coincident(g59,g60)
    c: Coincident(g60,g57)
    c: Horizontal(g57)
    c: Horizontal(g59)
    c: Vertical(g58)
    c: Vertical(g60)
    c: Coincident(g61,g62)
    c: Coincident(g62,g63)
    c: Coincident(g63,g64)
    c: Coincident(g64,g61)
    c: Horizontal(g61)
    c: Horizontal(g63)
    c: Vertical(g62)
    c: Vertical(g64)
    c: Coincident(g65,g66)
    c: Coincident(g66,g67)
    c: Coincident(g67,g68)
    c: Coincident(g68,g65)
    c: Horizontal(g65)
    c: Horizontal(g67)
    c: Vertical(g66)
    c: Vertical(g68)
    c: Vertical(g65,g62)
    c: Vertical(g61,g58)
    c: Vertical(g65,g63)
    c: Vertical(g61,g59)
    c: DistanceX(g67,g66) = 4
    c: DistanceX(g67,g69) = 2
    c: PointOnObject(g69,g-1)
    c: Coincident(g70,g71)
    c: Coincident(g71,g72)
    c: Coincident(g72,g73)
    c: Coincident(g73,g70)
    c: Horizontal(g70)
    c: Horizontal(g72)
    c: Vertical(g71)
    c: Vertical(g73)
    c: Coincident(g74,g75)
    c: Coincident(g75,g76)
    c: Coincident(g76,g77)
    c: Coincident(g77,g74)
    c: Horizontal(g74)
    c: Horizontal(g76)
    c: Vertical(g75)
    c: Vertical(g77)
    c: Coincident(g78,g79)
    c: Coincident(g79,g80)
    c: Coincident(g80,g81)
    c: Coincident(g81,g78)
    c: Horizontal(g78)
    c: Horizontal(g80)
    c: Vertical(g79)
    c: Vertical(g81)
    c: Vertical(g78,g75)
    c: Vertical(g74,g71)
    c: Vertical(g78,g76)
    c: Vertical(g74,g72)
    c: DistanceX(g80,g79) = 4
    c: DistanceX(g80,g82) = 2
    c: PointOnObject(g82,g-1)
    c: Coincident(g83,g84)
    c: Coincident(g84,g85)
    c: Coincident(g85,g86)
    c: Coincident(g86,g83)
    c: Horizontal(g83)
    c: Horizontal(g85)
    c: Vertical(g84)
    c: Vertical(g86)
    c: Coincident(g87,g88)
    c: Coincident(g88,g89)
    c: Coincident(g89,g90)
    c: Coincident(g90,g87)
    c: Horizontal(g87)
    c: Horizontal(g89)
    c: Vertical(g88)
    c: Vertical(g90)
    c: Coincident(g91,g92)
    c: Coincident(g92,g93)
    c: Coincident(g93,g94)
    c: Coincident(g94,g91)
    c: Horizontal(g91)
    c: Horizontal(g93)
    c: Vertical(g92)
    c: Vertical(g94)
    c: Vertical(g91,g88)
    c: Vertical(g87,g84)
    c: Vertical(g91,g89)
    c: Vertical(g87,g85)
    c: DistanceX(g93,g92) = 4
    c: DistanceX(g93,g95) = 2
    c: PointOnObject(g95,g-1)
    c: Horizontal(g41,g93)
    c: Horizontal(g91,g40)
    c: Horizontal(g37,g89)
    c: Horizontal(g87,g36)
    c: Horizontal(g33,g85)
    c: Horizontal(g83,g32)
    c: Horizontal(g92,g80)
    c: Horizontal(g91,g78)
    c: Horizontal(g76,g88)
    c: Horizontal(g74,g87)
    c: Horizontal(g84,g72)
    c: Horizontal(g83,g70)
    c: Horizontal(g79,g67)
    c: Horizontal(g78,g65)
    c: Horizontal(g75,g63)
    c: Horizontal(g74,g61)
    c: Horizontal(g71,g59)
    c: Horizontal(g70,g57)
    c: Horizontal(g66,g54)
    c: Horizontal(g65,g52)
    c: Horizontal(g62,g50)
    c: Horizontal(g61,g48)
    c: Horizontal(g58,g46)
    c: DistanceX(g-5,g95) = 401.6
    c: DistanceX(g95,g82) = 401.6
    c: DistanceX(g82,g69) = 401.6
    c: DistanceX(g69,g56) = 401.6
    c: Horizontal(g57,g44)
FEATURE [PartDesign::Pocket] Pocket018
  BaseFeature = -> Pad020
  Length = 4
  Length2 = 100
  Placement = pos=(0,0,0) rot=(1,0,0;1.5708rad)
  Profile = -> Sketch042
  Type = 0
FEATURE [PartDesign::Body] Body020  label="KorbordBaksida"
  Group = -> [Sketch041,Pad020,Sketch042,Pocket018]
  Origin = -> Origin020
  Placement = pos=(0,-604,0) rot=(0,0,1;0rad)
  Tip = -> Pocket018
FEATURE [Sketcher::SketchObject] Sketch043
  FullyConstrained = true
  MapMode = 5
  Placement = pos=(0,0,0) rot=(0.57735,0.57735,0.57735;2.0944rad)
  Support = -> [YZ_Plane021]
  sketch-geometry (7):
    g0: GeomPoint X=0 Y=70.3 Z=0
    g1: GeomPoint X=0 Y=-52 Z=0
    g2: LineSegment StartX=0 StartY=-52 StartZ=0 EndX=0 EndY=70.3 EndZ=0
    g3: LineSegment StartX=0 StartY=70.3 StartZ=0 EndX=-277.128 EndY=-89.7 EndZ=0
    g4: GeomPoint X=-277.128 Y=-119.7 Z=0
    g5: LineSegment StartX=-277.128 StartY=-89.7 StartZ=0 EndX=-277.128 EndY=-119.7 EndZ=0
    g6: LineSegment StartX=-277.128 StartY=-119.7 StartZ=0 EndX=0 EndY=-52 EndZ=0
  constraints (15):
    c: PointOnObject(g0,g-2)
    c: DistanceY(g-1,g0) = 70.3
    c: PointOnObject(g1,g-2)
    c: DistanceY(g1,g-1) = 52
    c: Coincident(g2,g1)
    c: Coincident(g2,g0)
    c: Coincident(g3,g2)
    c: Angle(g3,g2) = 1.0472
    c: Distance(g2,g3) = 320
    c: Vertical(g3,g4)
    c: Coincident(g5,g3)
    c: Coincident(g5,g4)
    c: Coincident(g6,g5)
    c: Coincident(g6,g2)
    c: DistanceY(g5,g3) = 30
FEATURE [PartDesign::Pad] Pad021
  Direction = (1,1,1)
  Length = 4
  Length2 = 100
  Placement = pos=(0,0,0) rot=(0.57735,0.57735,0.57735;2.0944rad)
  Profile = -> Sketch043
  Type = 0
FEATURE [Sketcher::SketchObject] Sketch044
  ExternalGeometry = -> [Pad021]
  FullyConstrained = true
  MapMode = 5
  Placement = pos=(4,-9e-16,9e-16) rot=(0.57735,0.57735,0.57735;2.0944rad)
  Support = -> [Pad021]
  sketch-geometry (20):
    g0: LineSegment StartX=0 StartY=-52 StartZ=0 EndX=-4 EndY=-52 EndZ=0
    g1: LineSegment StartX=-4 StartY=-52 StartZ=0 EndX=-4 EndY=-34.53 EndZ=0
    g2: LineSegment StartX=-4 StartY=-34.53 StartZ=0 EndX=0 EndY=-34.53 EndZ=0
    g3: LineSegment StartX=0 StartY=-34.53 StartZ=0 EndX=0 EndY=-52 EndZ=0
    g4: LineSegment StartX=0 StartY=-17.06 StartZ=0 EndX=-4 EndY=-17.06 EndZ=0
    g5: LineSegment StartX=-4 StartY=-17.06 StartZ=0 EndX=-4 EndY=0.41 EndZ=0
    g6: LineSegment StartX=-4 StartY=0.41 StartZ=0 EndX=0 EndY=0.41 EndZ=0
    g7: LineSegment StartX=0 StartY=0.41 StartZ=0 EndX=0 EndY=-17.06 EndZ=0
    g8: LineSegment StartX=0 StartY=17.88 StartZ=0 EndX=-4 EndY=17.88 EndZ=0
    g9: LineSegment StartX=-4 StartY=17.88 StartZ=0 EndX=-4 EndY=35.35 EndZ=0
    g10: LineSegment StartX=-4 StartY=35.35 StartZ=0 EndX=0 EndY=35.35 EndZ=0
    g11: LineSegment StartX=0 StartY=35.35 StartZ=0 EndX=0 EndY=17.88 EndZ=0
    g12: LineSegment StartX=-277.128 StartY=-99.7 StartZ=0 EndX=-273.128 EndY=-99.7 EndZ=0
    g13: LineSegment StartX=-273.128 StartY=-99.7 StartZ=0 EndX=-273.128 EndY=-109.7 EndZ=0
    g14: LineSegment StartX=-273.128 StartY=-109.7 StartZ=0 EndX=-277.128 EndY=-109.7 EndZ=0
    g15: LineSegment StartX=-277.128 StartY=-109.7 StartZ=0 EndX=-277.128 EndY=-99.7 EndZ=0
    g16: LineSegment StartX=0 StartY=52.83 StartZ=0 EndX=2.34e-14 EndY=70.3 EndZ=0
    g17: LineSegment StartX=2.34e-14 StartY=70.3 StartZ=0 EndX=-4 EndY=67.9906 EndZ=0
    g18: LineSegment StartX=-4 StartY=67.9906 StartZ=0 EndX=-4 EndY=52.83 EndZ=0
    g19: LineSegment StartX=-4 StartY=52.83 StartZ=0 EndX=0 EndY=52.83 EndZ=0
  constraints (59):
    c: DistanceY(g-4,g-3) = 122.3
    c: Coincident(g0,g1)
    c: Coincident(g1,g2)
    c: Coincident(g2,g3)
    c: Coincident(g3,g0)
    c: Horizontal(g0)
    c: Horizontal(g2)
    c: Vertical(g1)
    c: Vertical(g3)
    c: Coincident(g0,g-4)
    c: Coincident(g4,g5)
    c: Coincident(g5,g6)
    c: Coincident(g6,g7)
    c: Coincident(g7,g4)
    c: Horizontal(g4)
    c: Horizontal(g6)
    c: Vertical(g5)
    c: Vertical(g7)
    c: PointOnObject(g4,g-2)
    c: Coincident(g8,g9)
    c: Coincident(g9,g10)
    c: Coincident(g10,g11)
    c: Coincident(g11,g8)
    c: Horizontal(g8)
    c: Horizontal(g10)
    c: Vertical(g9)
    c: Vertical(g11)
    c: PointOnObject(g8,g-2)
    c: DistanceY(g0,g2) = 17.47
    c: Equal(g3,g7)
    c: Equal(g7,g11)
    c: DistanceY(g2,g4) = 17.47
    c: DistanceY(g6,g8) = 17.47
    c: Vertical(g1,g4)
    c: Vertical(g5,g8)
    c: DistanceX(g0,g0) = 4
    c: Coincident(g12,g13)
    c: Coincident(g13,g14)
    c: Coincident(g14,g15)
    c: Coincident(g15,g12)
    c: Horizontal(g12)
    c: Horizontal(g14)
    c: Vertical(g13)
    c: Vertical(g15)
    c: PointOnObject(g12,g-5)
    c: DistanceY(g-5,g14) = 10
    c: DistanceY(g14,g12) = 10
    c: DistanceX(g14,g13) = 4
    c: PointOnObject(g16,g-2)
    c: Coincident(g16,g-3)
    c: Equal(g11,g16)
    c: Coincident(g17,g16)
    c: PointOnObject(g17,g-3)
    c: Coincident(g18,g17)
    c: Vertical(g18)
    c: Coincident(g19,g18)
    c: Coincident(g19,g16)
    c: Horizontal(g18,g16)
    c: Vertical(g9,g18)
FEATURE [PartDesign::Pocket] Pocket019
  BaseFeature = -> Pad021
  Length = 4
  Length2 = 100
  Placement = pos=(0,0,0) rot=(0.57735,0.57735,0.57735;2.0944rad)
  Profile = -> Sketch044
  Type = 0
FEATURE [PartDesign::Body] Body021  label="KorbordSida-2"
  Group = -> [Sketch043,Pad021,Sketch044,Pocket019]
  Origin = -> Origin021
  Placement = pos=(1000,-604,0) rot=(0,0,1;0rad)
  Tip = -> Pocket019
FEATURE [Sketcher::SketchObject] Sketch046
  FullyConstrained = true
  MapMode = 5
  Placement = pos=(0,0,0) rot=(0.57735,0.57735,0.57735;2.0944rad)
  Support = -> [YZ_Plane022]
  sketch-geometry (7):
    g0: GeomPoint X=0 Y=70.3 Z=0
    g1: GeomPoint X=0 Y=-52 Z=0
    g2: LineSegment StartX=0 StartY=-52 StartZ=0 EndX=0 EndY=70.3 EndZ=0
    g3: LineSegment StartX=0 StartY=70.3 StartZ=0 EndX=-277.128 EndY=-89.7 EndZ=0
    g4: GeomPoint X=-277.128 Y=-119.7 Z=0
    g5: LineSegment StartX=-277.128 StartY=-89.7 StartZ=0 EndX=-277.128 EndY=-119.7 EndZ=0
    g6: LineSegment StartX=-277.128 StartY=-119.7 StartZ=0 EndX=0 EndY=-52 EndZ=0
  constraints (15):
    c: PointOnObject(g0,g-2)
    c: DistanceY(g-1,g0) = 70.3
    c: PointOnObject(g1,g-2)
    c: DistanceY(g1,g-1) = 52
    c: Coincident(g2,g1)
    c: Coincident(g2,g0)
    c: Coincident(g3,g2)
    c: Angle(g3,g2) = 1.0472
    c: Distance(g2,g3) = 320
    c: Vertical(g3,g4)
    c: Coincident(g5,g3)
    c: Coincident(g5,g4)
    c: Coincident(g6,g5)
    c: Coincident(g6,g2)
    c: DistanceY(g5,g3) = 30
FEATURE [PartDesign::Pad] Pad022
  Direction = (1,1,1)
  Length = 4
  Length2 = 100
  Placement = pos=(0,0,0) rot=(0.57735,0.57735,0.57735;2.0944rad)
  Profile = -> Sketch046
  Type = 0
FEATURE [Sketcher::SketchObject] Sketch045
  ExternalGeometry = -> [Pad022]
  FullyConstrained = true
  MapMode = 5
  Placement = pos=(4,-9e-16,9e-16) rot=(0.57735,0.57735,0.57735;2.0944rad)
  Support = -> [Pad022]
  sketch-geometry (22):
    g0: LineSegment StartX=0 StartY=-52 StartZ=0 EndX=-4 EndY=-52 EndZ=0
    g1: LineSegment StartX=-4 StartY=-52 StartZ=0 EndX=-4 EndY=-34.53 EndZ=0
    g2: LineSegment StartX=-4 StartY=-34.53 StartZ=0 EndX=0 EndY=-34.53 EndZ=0
    g3: LineSegment StartX=0 StartY=-34.53 StartZ=0 EndX=0 EndY=-52 EndZ=0
    g4: LineSegment StartX=0 StartY=-17.06 StartZ=0 EndX=-4 EndY=-17.06 EndZ=0
    g5: LineSegment StartX=-4 StartY=-17.06 StartZ=0 EndX=-4 EndY=0.41 EndZ=0
    g6: LineSegment StartX=-4 StartY=0.41 StartZ=0 EndX=0 EndY=0.41 EndZ=0
    g7: LineSegment StartX=0 StartY=0.41 StartZ=0 EndX=0 EndY=-17.06 EndZ=0
    g8: LineSegment StartX=0 StartY=17.88 StartZ=0 EndX=-4 EndY=17.88 EndZ=0
    g9: LineSegment StartX=-4 StartY=17.88 StartZ=0 EndX=-4 EndY=35.35 EndZ=0
    g10: LineSegment StartX=-4 StartY=35.35 StartZ=0 EndX=0 EndY=35.35 EndZ=0
    g11: LineSegment StartX=0 StartY=35.35 StartZ=0 EndX=0 EndY=17.88 EndZ=0
    g12: LineSegment StartX=-277.128 StartY=-99.7 StartZ=0 EndX=-273.128 EndY=-99.7 EndZ=0
    g13: LineSegment StartX=-273.128 StartY=-99.7 StartZ=0 EndX=-273.128 EndY=-109.7 EndZ=0
    g14: LineSegment StartX=-273.128 StartY=-109.7 StartZ=0 EndX=-277.128 EndY=-109.7 EndZ=0
    g15: LineSegment StartX=-277.128 StartY=-109.7 StartZ=0 EndX=-277.128 EndY=-99.7 EndZ=0
    g16: LineSegment StartX=0 StartY=52.83 StartZ=0 EndX=-1.1e-15 EndY=70.3 EndZ=0
    g17: LineSegment StartX=-1.1e-15 StartY=70.3 StartZ=0 EndX=-4 EndY=67.9906 EndZ=0
    g18: LineSegment StartX=-4 StartY=67.9906 StartZ=0 EndX=-4 EndY=52.83 EndZ=0
    g19: LineSegment StartX=-4 StartY=52.83 StartZ=0 EndX=0 EndY=52.83 EndZ=0
    g20: Circle CenterX=-85 CenterY=-27 CenterZ=0 NormalX=0 NormalY=0 NormalZ=1 AngleXU=0 Radius=25
    g21: Circle CenterX=-180 CenterY=-68 CenterZ=0 NormalX=0 NormalY=0 NormalZ=1 AngleXU=0 Radius=16
  constraints (65):
    c: DistanceY(g-4,g-3) = 122.3
    c: Coincident(g0,g1)
    c: Coincident(g1,g2)
    c: Coincident(g2,g3)
    c: Coincident(g3,g0)
    c: Horizontal(g0)
    c: Horizontal(g2)
    c: Vertical(g1)
    c: Vertical(g3)
    c: Coincident(g0,g-4)
    c: Coincident(g4,g5)
    c: Coincident(g5,g6)
    c: Coincident(g6,g7)
    c: Coincident(g7,g4)
    c: Horizontal(g4)
    c: Horizontal(g6)
    c: Vertical(g5)
    c: Vertical(g7)
    c: PointOnObject(g4,g-2)
    c: Coincident(g8,g9)
    c: Coincident(g9,g10)
    c: Coincident(g10,g11)
    c: Coincident(g11,g8)
    c: Horizontal(g8)
    c: Horizontal(g10)
    c: Vertical(g9)
    c: Vertical(g11)
    c: PointOnObject(g8,g-2)
    c: DistanceY(g0,g2) = 17.47
    c: Equal(g3,g7)
    c: Equal(g7,g11)
    c: DistanceY(g2,g4) = 17.47
    c: DistanceY(g6,g8) = 17.47
    c: Vertical(g1,g4)
    c: Vertical(g5,g8)
    c: DistanceX(g0,g0) = 4
    c: Coincident(g12,g13)
    c: Coincident(g13,g14)
    c: Coincident(g14,g15)
    c: Coincident(g15,g12)
    c: Horizontal(g12)
    c: Horizontal(g14)
    c: Vertical(g13)
    c: Vertical(g15)
    c: PointOnObject(g12,g-5)
    c: DistanceY(g-5,g14) = 10
    c: DistanceY(g14,g12) = 10
    c: DistanceX(g14,g13) = 4
    c: PointOnObject(g16,g-2)
    c: Coincident(g16,g-3)
    c: Equal(g11,g16)
    c: Coincident(g17,g16)
    c: PointOnObject(g17,g-3)
    c: Coincident(g18,g17)
    c: Vertical(g18)
    c: Coincident(g19,g18)
    c: Coincident(g19,g16)
    c: Horizontal(g18,g16)
    c: Vertical(g9,g18)
    c: DistanceX(g20,g0) = 85
    c: DistanceY(g0,g20) = 25
    c: DistanceX(g21,g0) = 180
    c: DistanceY(g21,g0) = 16
    c: Radius(g21) = 16
    c: Radius(g20) = 25
FEATURE [PartDesign::Pocket] Pocket020
  BaseFeature = -> Pad022
  Length = 4
  Length2 = 100
  Placement = pos=(0,0,0) rot=(0.57735,0.57735,0.57735;2.0944rad)
  Profile = -> Sketch045
  Type = 0
FEATURE [PartDesign::Body] Body022  label="KorbordSprygel-1"
  Group = -> [Sketch046,Pad022,Sketch045,Pocket020]
  Origin = -> Origin022
  Placement = pos=(-604.4,-604,0) rot=(0,0,1;0rad)
  Tip = -> Pocket020
FEATURE [Sketcher::SketchObject] Sketch047
  FullyConstrained = true
  MapMode = 5
  Placement = pos=(0,0,0) rot=(0.57735,0.57735,0.57735;2.0944rad)
  Support = -> [YZ_Plane023]
  sketch-geometry (7):
    g0: GeomPoint X=0 Y=70.3 Z=0
    g1: GeomPoint X=0 Y=-52 Z=0
    g2: LineSegment StartX=0 StartY=-52 StartZ=0 EndX=0 EndY=70.3 EndZ=0
    g3: LineSegment StartX=0 StartY=70.3 StartZ=0 EndX=-277.128 EndY=-89.7 EndZ=0
    g4: GeomPoint X=-277.128 Y=-119.7 Z=0
    g5: LineSegment StartX=-277.128 StartY=-89.7 StartZ=0 EndX=-277.128 EndY=-119.7 EndZ=0
    g6: LineSegment StartX=-277.128 StartY=-119.7 StartZ=0 EndX=0 EndY=-52 EndZ=0
  constraints (15):
    c: PointOnObject(g0,g-2)
    c: DistanceY(g-1,g0) = 70.3
    c: PointOnObject(g1,g-2)
    c: DistanceY(g1,g-1) = 52
    c: Coincident(g2,g1)
    c: Coincident(g2,g0)
    c: Coincident(g3,g2)
    c: Angle(g3,g2) = 1.0472
    c: Distance(g2,g3) = 320
    c: Vertical(g3,g4)
    c: Coincident(g5,g3)
    c: Coincident(g5,g4)
    c: Coincident(g6,g5)
    c: Coincident(g6,g2)
    c: DistanceY(g5,g3) = 30
FEATURE [PartDesign::Pad] Pad023
  Direction = (1,1,1)
  Length = 4
  Length2 = 100
  Placement = pos=(0,0,0) rot=(0.57735,0.57735,0.57735;2.0944rad)
  Profile = -> Sketch047
  Type = 0
FEATURE [Sketcher::SketchObject] Sketch048
  ExternalGeometry = -> [Pad023]
  FullyConstrained = true
  MapMode = 5
  Placement = pos=(4,-9e-16,9e-16) rot=(0.57735,0.57735,0.57735;2.0944rad)
  Support = -> [Pad023]
  sketch-geometry (22):
    g0: LineSegment StartX=0 StartY=-52 StartZ=0 EndX=-4 EndY=-52 EndZ=0
    g1: LineSegment StartX=-4 StartY=-52 StartZ=0 EndX=-4 EndY=-34.53 EndZ=0
    g2: LineSegment StartX=-4 StartY=-34.53 StartZ=0 EndX=0 EndY=-34.53 EndZ=0
    g3: LineSegment StartX=0 StartY=-34.53 StartZ=0 EndX=0 EndY=-52 EndZ=0
    g4: LineSegment StartX=0 StartY=-17.06 StartZ=0 EndX=-4 EndY=-17.06 EndZ=0
    g5: LineSegment StartX=-4 StartY=-17.06 StartZ=0 EndX=-4 EndY=0.41 EndZ=0
    g6: LineSegment StartX=-4 StartY=0.41 StartZ=0 EndX=0 EndY=0.41 EndZ=0
    g7: LineSegment StartX=0 StartY=0.41 StartZ=0 EndX=0 EndY=-17.06 EndZ=0
    g8: LineSegment StartX=0 StartY=17.88 StartZ=0 EndX=-4 EndY=17.88 EndZ=0
    g9: LineSegment StartX=-4 StartY=17.88 StartZ=0 EndX=-4 EndY=35.35 EndZ=0
    g10: LineSegment StartX=-4 StartY=35.35 StartZ=0 EndX=0 EndY=35.35 EndZ=0
    g11: LineSegment StartX=0 StartY=35.35 StartZ=0 EndX=0 EndY=17.88 EndZ=0
    g12: LineSegment StartX=-277.128 StartY=-99.7 StartZ=0 EndX=-273.128 EndY=-99.7 EndZ=0
    g13: LineSegment StartX=-273.128 StartY=-99.7 StartZ=0 EndX=-273.128 EndY=-109.7 EndZ=0
    g14: LineSegment StartX=-273.128 StartY=-109.7 StartZ=0 EndX=-277.128 EndY=-109.7 EndZ=0
    g15: LineSegment StartX=-277.128 StartY=-109.7 StartZ=0 EndX=-277.128 EndY=-99.7 EndZ=0
    g16: LineSegment StartX=0 StartY=52.83 StartZ=0 EndX=-1.1e-15 EndY=70.3 EndZ=0
    g17: LineSegment StartX=-1.1e-15 StartY=70.3 StartZ=0 EndX=-4 EndY=67.9906 EndZ=0
    g18: LineSegment StartX=-4 StartY=67.9906 StartZ=0 EndX=-4 EndY=52.83 EndZ=0
    g19: LineSegment StartX=-4 StartY=52.83 StartZ=0 EndX=0 EndY=52.83 EndZ=0
    g20: Circle CenterX=-85 CenterY=-27 CenterZ=0 NormalX=0 NormalY=0 NormalZ=1 AngleXU=0 Radius=25
    g21: Circle CenterX=-180 CenterY=-68 CenterZ=0 NormalX=0 NormalY=0 NormalZ=1 AngleXU=0 Radius=16
  constraints (65):
    c: DistanceY(g-4,g-3) = 122.3
    c: Coincident(g0,g1)
    c: Coincident(g1,g2)
    c: Coincident(g2,g3)
    c: Coincident(g3,g0)
    c: Horizontal(g0)
    c: Horizontal(g2)
    c: Vertical(g1)
    c: Vertical(g3)
    c: Coincident(g0,g-4)
    c: Coincident(g4,g5)
    c: Coincident(g5,g6)
    c: Coincident(g6,g7)
    c: Coincident(g7,g4)
    c: Horizontal(g4)
    c: Horizontal(g6)
    c: Vertical(g5)
    c: Vertical(g7)
    c: PointOnObject(g4,g-2)
    c: Coincident(g8,g9)
    c: Coincident(g9,g10)
    c: Coincident(g10,g11)
    c: Coincident(g11,g8)
    c: Horizontal(g8)
    c: Horizontal(g10)
    c: Vertical(g9)
    c: Vertical(g11)
    c: PointOnObject(g8,g-2)
    c: DistanceY(g0,g2) = 17.47
    c: Equal(g3,g7)
    c: Equal(g7,g11)
    c: DistanceY(g2,g4) = 17.47
    c: DistanceY(g6,g8) = 17.47
    c: Vertical(g1,g4)
    c: Vertical(g5,g8)
    c: DistanceX(g0,g0) = 4
    c: Coincident(g12,g13)
    c: Coincident(g13,g14)
    c: Coincident(g14,g15)
    c: Coincident(g15,g12)
    c: Horizontal(g12)
    c: Horizontal(g14)
    c: Vertical(g13)
    c: Vertical(g15)
    c: PointOnObject(g12,g-5)
    c: DistanceY(g-5,g14) = 10
    c: DistanceY(g14,g12) = 10
    c: DistanceX(g14,g13) = 4
    c: PointOnObject(g16,g-2)
    c: Coincident(g16,g-3)
    c: Equal(g11,g16)
    c: Coincident(g17,g16)
    c: PointOnObject(g17,g-3)
    c: Coincident(g18,g17)
    c: Vertical(g18)
    c: Coincident(g19,g18)
    c: Coincident(g19,g16)
    c: Horizontal(g18,g16)
    c: Vertical(g9,g18)
    c: DistanceX(g20,g0) = 85
    c: DistanceY(g0,g20) = 25
    c: DistanceX(g21,g0) = 180
    c: DistanceY(g21,g0) = 16
    c: Radius(g21) = 16
    c: Radius(g20) = 25
FEATURE [PartDesign::Pocket] Pocket021
  BaseFeature = -> Pad023
  Length = 4
  Length2 = 100
  Placement = pos=(0,0,0) rot=(0.57735,0.57735,0.57735;2.0944rad)
  Profile = -> Sketch048
  Type = 0
FEATURE [PartDesign::Body] Body023  label="KorbordSprygel-2"
  Group = -> [Sketch047,Pad023,Sketch048,Pocket021]
  Origin = -> Origin023
  Placement = pos=(-202.8,-604,0) rot=(0,0,1;0rad)
  Tip = -> Pocket021
FEATURE [Sketcher::SketchObject] Sketch049
  FullyConstrained = true
  MapMode = 5
  Placement = pos=(0,0,0) rot=(0.57735,0.57735,0.57735;2.0944rad)
  Support = -> [YZ_Plane024]
  sketch-geometry (7):
    g0: GeomPoint X=0 Y=70.3 Z=0
    g1: GeomPoint X=0 Y=-52 Z=0
    g2: LineSegment StartX=0 StartY=-52 StartZ=0 EndX=0 EndY=70.3 EndZ=0
    g3: LineSegment StartX=0 StartY=70.3 StartZ=0 EndX=-277.128 EndY=-89.7 EndZ=0
    g4: GeomPoint X=-277.128 Y=-119.7 Z=0
    g5: LineSegment StartX=-277.128 StartY=-89.7 StartZ=0 EndX=-277.128 EndY=-119.7 EndZ=0
    g6: LineSegment StartX=-277.128 StartY=-119.7 StartZ=0 EndX=0 EndY=-52 EndZ=0
  constraints (15):
    c: PointOnObject(g0,g-2)
    c: DistanceY(g-1,g0) = 70.3
    c: PointOnObject(g1,g-2)
    c: DistanceY(g1,g-1) = 52
    c: Coincident(g2,g1)
    c: Coincident(g2,g0)
    c: Coincident(g3,g2)
    c: Angle(g3,g2) = 1.0472
    c: Distance(g2,g3) = 320
    c: Vertical(g3,g4)
    c: Coincident(g5,g3)
    c: Coincident(g5,g4)
    c: Coincident(g6,g5)
    c: Coincident(g6,g2)
    c: DistanceY(g5,g3) = 30
FEATURE [PartDesign::Pad] Pad024
  Direction = (1,1,1)
  Length = 4
  Length2 = 100
  Placement = pos=(0,0,0) rot=(0.57735,0.57735,0.57735;2.0944rad)
  Profile = -> Sketch049
  Type = 0
FEATURE [Sketcher::SketchObject] Sketch050
  ExternalGeometry = -> [Pad024]
  FullyConstrained = true
  MapMode = 5
  Placement = pos=(4,-9e-16,9e-16) rot=(0.57735,0.57735,0.57735;2.0944rad)
  Support = -> [Pad024]
  sketch-geometry (22):
    g0: LineSegment StartX=0 StartY=-52 StartZ=0 EndX=-4 EndY=-52 EndZ=0
    g1: LineSegment StartX=-4 StartY=-52 StartZ=0 EndX=-4 EndY=-34.53 EndZ=0
    g2: LineSegment StartX=-4 StartY=-34.53 StartZ=0 EndX=0 EndY=-34.53 EndZ=0
    g3: LineSegment StartX=0 StartY=-34.53 StartZ=0 EndX=0 EndY=-52 EndZ=0
    g4: LineSegment StartX=0 StartY=-17.06 StartZ=0 EndX=-4 EndY=-17.06 EndZ=0
    g5: LineSegment StartX=-4 StartY=-17.06 StartZ=0 EndX=-4 EndY=0.41 EndZ=0
    g6: LineSegment StartX=-4 StartY=0.41 StartZ=0 EndX=0 EndY=0.41 EndZ=0
    g7: LineSegment StartX=0 StartY=0.41 StartZ=0 EndX=0 EndY=-17.06 EndZ=0
    g8: LineSegment StartX=0 StartY=17.88 StartZ=0 EndX=-4 EndY=17.88 EndZ=0
    g9: LineSegment StartX=-4 StartY=17.88 StartZ=0 EndX=-4 EndY=35.35 EndZ=0
    g10: LineSegment StartX=-4 StartY=35.35 StartZ=0 EndX=0 EndY=35.35 EndZ=0
    g11: LineSegment StartX=0 StartY=35.35 StartZ=0 EndX=0 EndY=17.88 EndZ=0
    g12: LineSegment StartX=-277.128 StartY=-99.7 StartZ=0 EndX=-273.128 EndY=-99.7 EndZ=0
    g13: LineSegment StartX=-273.128 StartY=-99.7 StartZ=0 EndX=-273.128 EndY=-109.7 EndZ=0
    g14: LineSegment StartX=-273.128 StartY=-109.7 StartZ=0 EndX=-277.128 EndY=-109.7 EndZ=0
    g15: LineSegment StartX=-277.128 StartY=-109.7 StartZ=0 EndX=-277.128 EndY=-99.7 EndZ=0
    g16: LineSegment StartX=0 StartY=52.83 StartZ=0 EndX=-1.1e-15 EndY=70.3 EndZ=0
    g17: LineSegment StartX=-1.1e-15 StartY=70.3 StartZ=0 EndX=-4 EndY=67.9906 EndZ=0
    g18: LineSegment StartX=-4 StartY=67.9906 StartZ=0 EndX=-4 EndY=52.83 EndZ=0
    g19: LineSegment StartX=-4 StartY=52.83 StartZ=0 EndX=0 EndY=52.83 EndZ=0
    g20: Circle CenterX=-85 CenterY=-27 CenterZ=0 NormalX=0 NormalY=0 NormalZ=1 AngleXU=0 Radius=25
    g21: Circle CenterX=-180 CenterY=-68 CenterZ=0 NormalX=0 NormalY=0 NormalZ=1 AngleXU=0 Radius=16
  constraints (65):
    c: DistanceY(g-4,g-3) = 122.3
    c: Coincident(g0,g1)
    c: Coincident(g1,g2)
    c: Coincident(g2,g3)
    c: Coincident(g3,g0)
    c: Horizontal(g0)
    c: Horizontal(g2)
    c: Vertical(g1)
    c: Vertical(g3)
    c: Coincident(g0,g-4)
    c: Coincident(g4,g5)
    c: Coincident(g5,g6)
    c: Coincident(g6,g7)
    c: Coincident(g7,g4)
    c: Horizontal(g4)
    c: Horizontal(g6)
    c: Vertical(g5)
    c: Vertical(g7)
    c: PointOnObject(g4,g-2)
    c: Coincident(g8,g9)
    c: Coincident(g9,g10)
    c: Coincident(g10,g11)
    c: Coincident(g11,g8)
    c: Horizontal(g8)
    c: Horizontal(g10)
    c: Vertical(g9)
    c: Vertical(g11)
    c: PointOnObject(g8,g-2)
    c: DistanceY(g0,g2) = 17.47
    c: Equal(g3,g7)
    c: Equal(g7,g11)
    c: DistanceY(g2,g4) = 17.47
    c: DistanceY(g6,g8) = 17.47
    c: Vertical(g1,g4)
    c: Vertical(g5,g8)
    c: DistanceX(g0,g0) = 4
    c: Coincident(g12,g13)
    c: Coincident(g13,g14)
    c: Coincident(g14,g15)
    c: Coincident(g15,g12)
    c: Horizontal(g12)
    c: Horizontal(g14)
    c: Vertical(g13)
    c: Vertical(g15)
    c: PointOnObject(g12,g-5)
    c: DistanceY(g-5,g14) = 10
    c: DistanceY(g14,g12) = 10
    c: DistanceX(g14,g13) = 4
    c: PointOnObject(g16,g-2)
    c: Coincident(g16,g-3)
    c: Equal(g11,g16)
    c: Coincident(g17,g16)
    c: PointOnObject(g17,g-3)
    c: Coincident(g18,g17)
    c: Vertical(g18)
    c: Coincident(g19,g18)
    c: Coincident(g19,g16)
    c: Horizontal(g18,g16)
    c: Vertical(g9,g18)
    c: DistanceX(g20,g0) = 85
    c: DistanceY(g0,g20) = 25
    c: DistanceX(g21,g0) = 180
    c: DistanceY(g21,g0) = 16
    c: Radius(g21) = 16
    c: Radius(g20) = 25
FEATURE [PartDesign::Pocket] Pocket022
  BaseFeature = -> Pad024
  Length = 4
  Length2 = 100
  Placement = pos=(0,0,0) rot=(0.57735,0.57735,0.57735;2.0944rad)
  Profile = -> Sketch050
  Type = 0
FEATURE [PartDesign::Body] Body024  label="KorbordSprygel-3"
  Group = -> [Sketch049,Pad024,Sketch050,Pocket022]
  Origin = -> Origin024
  Placement = pos=(198.8,-604,0) rot=(0,0,1;0rad)
  Tip = -> Pocket022
FEATURE [Sketcher::SketchObject] Sketch052
  FullyConstrained = true
  MapMode = 5
  Placement = pos=(0,0,0) rot=(0.57735,0.57735,0.57735;2.0944rad)
  Support = -> [YZ_Plane025]
  sketch-geometry (7):
    g0: GeomPoint X=0 Y=70.3 Z=0
    g1: GeomPoint X=0 Y=-52 Z=0
    g2: LineSegment StartX=0 StartY=-52 StartZ=0 EndX=0 EndY=70.3 EndZ=0
    g3: LineSegment StartX=0 StartY=70.3 StartZ=0 EndX=-277.128 EndY=-89.7 EndZ=0
    g4: GeomPoint X=-277.128 Y=-119.7 Z=0
    g5: LineSegment StartX=-277.128 StartY=-89.7 StartZ=0 EndX=-277.128 EndY=-119.7 EndZ=0
    g6: LineSegment StartX=-277.128 StartY=-119.7 StartZ=0 EndX=0 EndY=-52 EndZ=0
  constraints (15):
    c: PointOnObject(g0,g-2)
    c: DistanceY(g-1,g0) = 70.3
    c: PointOnObject(g1,g-2)
    c: DistanceY(g1,g-1) = 52
    c: Coincident(g2,g1)
    c: Coincident(g2,g0)
    c: Coincident(g3,g2)
    c: Angle(g3,g2) = 1.0472
    c: Distance(g2,g3) = 320
    c: Vertical(g3,g4)
    c: Coincident(g5,g3)
    c: Coincident(g5,g4)
    c: Coincident(g6,g5)
    c: Coincident(g6,g2)
    c: DistanceY(g5,g3) = 30
FEATURE [PartDesign::Pad] Pad025
  Direction = (1,1,1)
  Length = 4
  Length2 = 100
  Placement = pos=(0,0,0) rot=(0.57735,0.57735,0.57735;2.0944rad)
  Profile = -> Sketch052
  Type = 0
FEATURE [Sketcher::SketchObject] Sketch051
  ExternalGeometry = -> [Pad025]
  FullyConstrained = true
  MapMode = 5
  Placement = pos=(4,-9e-16,9e-16) rot=(0.57735,0.57735,0.57735;2.0944rad)
  Support = -> [Pad025]
  sketch-geometry (22):
    g0: LineSegment StartX=0 StartY=-52 StartZ=0 EndX=-4 EndY=-52 EndZ=0
    g1: LineSegment StartX=-4 StartY=-52 StartZ=0 EndX=-4 EndY=-34.53 EndZ=0
    g2: LineSegment StartX=-4 StartY=-34.53 StartZ=0 EndX=0 EndY=-34.53 EndZ=0
    g3: LineSegment StartX=0 StartY=-34.53 StartZ=0 EndX=0 EndY=-52 EndZ=0
    g4: LineSegment StartX=0 StartY=-17.06 StartZ=0 EndX=-4 EndY=-17.06 EndZ=0
    g5: LineSegment StartX=-4 StartY=-17.06 StartZ=0 EndX=-4 EndY=0.41 EndZ=0
    g6: LineSegment StartX=-4 StartY=0.41 StartZ=0 EndX=0 EndY=0.41 EndZ=0
    g7: LineSegment StartX=0 StartY=0.41 StartZ=0 EndX=0 EndY=-17.06 EndZ=0
    g8: LineSegment StartX=0 StartY=17.88 StartZ=0 EndX=-4 EndY=17.88 EndZ=0
    g9: LineSegment StartX=-4 StartY=17.88 StartZ=0 EndX=-4 EndY=35.35 EndZ=0
    g10: LineSegment StartX=-4 StartY=35.35 StartZ=0 EndX=0 EndY=35.35 EndZ=0
    g11: LineSegment StartX=0 StartY=35.35 StartZ=0 EndX=0 EndY=17.88 EndZ=0
    g12: LineSegment StartX=-277.128 StartY=-99.7 StartZ=0 EndX=-273.128 EndY=-99.7 EndZ=0
    g13: LineSegment StartX=-273.128 StartY=-99.7 StartZ=0 EndX=-273.128 EndY=-109.7 EndZ=0
    g14: LineSegment StartX=-273.128 StartY=-109.7 StartZ=0 EndX=-277.128 EndY=-109.7 EndZ=0
    g15: LineSegment StartX=-277.128 StartY=-109.7 StartZ=0 EndX=-277.128 EndY=-99.7 EndZ=0
    g16: LineSegment StartX=0 StartY=52.83 StartZ=0 EndX=-1.1e-15 EndY=70.3 EndZ=0
    g17: LineSegment StartX=-1.1e-15 StartY=70.3 StartZ=0 EndX=-4 EndY=67.9906 EndZ=0
    g18: LineSegment StartX=-4 StartY=67.9906 StartZ=0 EndX=-4 EndY=52.83 EndZ=0
    g19: LineSegment StartX=-4 StartY=52.83 StartZ=0 EndX=0 EndY=52.83 EndZ=0
    g20: Circle CenterX=-85 CenterY=-27 CenterZ=0 NormalX=0 NormalY=0 NormalZ=1 AngleXU=0 Radius=25
    g21: Circle CenterX=-180 CenterY=-68 CenterZ=0 NormalX=0 NormalY=0 NormalZ=1 AngleXU=0 Radius=16
  constraints (65):
    c: DistanceY(g-4,g-3) = 122.3
    c: Coincident(g0,g1)
    c: Coincident(g1,g2)
    c: Coincident(g2,g3)
    c: Coincident(g3,g0)
    c: Horizontal(g0)
    c: Horizontal(g2)
    c: Vertical(g1)
    c: Vertical(g3)
    c: Coincident(g0,g-4)
    c: Coincident(g4,g5)
    c: Coincident(g5,g6)
    c: Coincident(g6,g7)
    c: Coincident(g7,g4)
    c: Horizontal(g4)
    c: Horizontal(g6)
    c: Vertical(g5)
    c: Vertical(g7)
    c: PointOnObject(g4,g-2)
    c: Coincident(g8,g9)
    c: Coincident(g9,g10)
    c: Coincident(g10,g11)
    c: Coincident(g11,g8)
    c: Horizontal(g8)
    c: Horizontal(g10)
    c: Vertical(g9)
    c: Vertical(g11)
    c: PointOnObject(g8,g-2)
    c: DistanceY(g0,g2) = 17.47
    c: Equal(g3,g7)
    c: Equal(g7,g11)
    c: DistanceY(g2,g4) = 17.47
    c: DistanceY(g6,g8) = 17.47
    c: Vertical(g1,g4)
    c: Vertical(g5,g8)
    c: DistanceX(g0,g0) = 4
    c: Coincident(g12,g13)
    c: Coincident(g13,g14)
    c: Coincident(g14,g15)
    c: Coincident(g15,g12)
    c: Horizontal(g12)
    c: Horizontal(g14)
    c: Vertical(g13)
    c: Vertical(g15)
    c: PointOnObject(g12,g-5)
    c: DistanceY(g-5,g14) = 10
    c: DistanceY(g14,g12) = 10
    c: DistanceX(g14,g13) = 4
    c: PointOnObject(g16,g-2)
    c: Coincident(g16,g-3)
    c: Equal(g11,g16)
    c: Coincident(g17,g16)
    c: PointOnObject(g17,g-3)
    c: Coincident(g18,g17)
    c: Vertical(g18)
    c: Coincident(g19,g18)
    c: Coincident(g19,g16)
    c: Horizontal(g18,g16)
    c: Vertical(g9,g18)
    c: DistanceX(g20,g0) = 85
    c: DistanceY(g0,g20) = 25
    c: DistanceX(g21,g0) = 180
    c: DistanceY(g21,g0) = 16
    c: Radius(g21) = 16
    c: Radius(g20) = 25
FEATURE [PartDesign::Pocket] Pocket023
  BaseFeature = -> Pad025
  Length = 4
  Length2 = 100
  Placement = pos=(0,0,0) rot=(0.57735,0.57735,0.57735;2.0944rad)
  Profile = -> Sketch051
  Type = 0
FEATURE [PartDesign::Body] Body025  label="KorbordSprygel-4"
  Group = -> [Sketch052,Pad025,Sketch051,Pocket023]
  Origin = -> Origin025
  Placement = pos=(600.4,-604,0) rot=(0,0,1;0rad)
  Tip = -> Pocket023
FEATURE [Sketcher::SketchObject] Sketch054
  FullyConstrained = true
  MapMode = 5
  Placement = pos=(-1.83e-13,-273.128,0) rot=(0.57735,0.57735,-0.57735;2.0944rad)
  Support = -> [Pocket017]
FEATURE [PartDesign::Body] Body019  label="KorBordSida-1"
  Group = -> [Sketch039,Pad019,Sketch040,Pocket017,Sketch054]
  Origin = -> Origin019
  Placement = pos=(-1004,-604,0) rot=(0,0,1;0rad)
  Tip = -> Pocket017
FEATURE [Sketcher::SketchObject] Sketch055
  FullyConstrained = true
  MapMode = 5
  Support = -> [XY_Plane026]
  sketch-geometry (4):
    g0: LineSegment StartX=-1004 StartY=0 StartZ=0 EndX=1004 EndY=0 EndZ=0
    g1: LineSegment StartX=1004 StartY=0 StartZ=0 EndX=1004 EndY=-313 EndZ=0
    g2: LineSegment StartX=1004 StartY=-313 StartZ=0 EndX=-1004 EndY=-313 EndZ=0
    g3: LineSegment StartX=-1004 StartY=-313 StartZ=0 EndX=-1004 EndY=0 EndZ=0
  constraints (12):
    c: Coincident(g0,g1)
    c: Coincident(g1,g2)
    c: Coincident(g2,g3)
    c: Coincident(g3,g0)
    c: Horizontal(g0)
    c: Horizontal(g2)
    c: Vertical(g1)
    c: Vertical(g3)
    c: DistanceY(g-1,g0) = 0
    c: DistanceX(g2,g1) = 2008
    c: DistanceX(g2,g-1) = 1004
    c: Distance(g0,g2) = 313
FEATURE [PartDesign::Pad] Pad027
  Direction = (1,1,1)
  Length = 4
  Length2 = 100
  Profile = -> Sketch055
  Type = 0
FEATURE [PartDesign::Body] Body026  label="KorbordTop"
  Group = -> [Sketch055,Pad027]
  Origin = -> Origin026
  Placement = pos=(0,-606,69.1) rot=(1,0,0;0.523599rad)
  Tip = -> Pad027
FEATURE [Sketcher::SketchObject] Sketch056
  FullyConstrained = true
  MapMode = 5
  Placement = pos=(0,0,0) rot=(1,0,0;1.5708rad)
  Support = -> [XZ_Plane027]
  sketch-geometry (4):
    g0: LineSegment StartX=-1004 StartY=59.7 StartZ=0 EndX=1004 EndY=59.7 EndZ=0
    g1: LineSegment StartX=1004 StartY=59.7 StartZ=0 EndX=1004 EndY=-15 EndZ=0
    g2: LineSegment StartX=1004 StartY=-15 StartZ=0 EndX=-1004 EndY=-15 EndZ=0
    g3: LineSegment StartX=-1004 StartY=-15 StartZ=0 EndX=-1004 EndY=59.7 EndZ=0
  constraints (12):
    c: Coincident(g0,g1)
    c: Coincident(g1,g2)
    c: Coincident(g2,g3)
    c: Coincident(g3,g0)
    c: Horizontal(g0)
    c: Horizontal(g2)
    c: Vertical(g1)
    c: Vertical(g3)
    c: DistanceX(g2,g1) = 2008
    c: DistanceX(g2,g-1) = 1004
    c: DistanceY(g-1,g0) = 59.7
    c: DistanceY(g2,g-1) = 15
FEATURE [PartDesign::Pad] Pad028
  Direction = (1,1,1)
  Length = 4
  Length2 = 100
  Placement = pos=(0,0,0) rot=(1,0,0;1.5708rad)
  Profile = -> Sketch056
  Type = 0
FEATURE [Sketcher::SketchObject] Sketch057
  ExternalGeometry = -> [Pad028]
  FullyConstrained = true
  MapMode = 5
  Placement = pos=(0,-4,1.8e-15) rot=(1,0,0;1.5708rad)
  Support = -> [Pad028]
  sketch-geometry (53):
    g0: LineSegment StartX=-1004 StartY=-15 StartZ=0 EndX=-1000 EndY=-15 EndZ=0
    g1: LineSegment StartX=-1000 StartY=-15 StartZ=0 EndX=-1000 EndY=-5 EndZ=0
    g2: LineSegment StartX=-1000 StartY=-5 StartZ=0 EndX=-1004 EndY=-5 EndZ=0
    g3: LineSegment StartX=-1004 StartY=-5 StartZ=0 EndX=-1004 EndY=-15 EndZ=0
    g4: LineSegment StartX=-1004 StartY=5 StartZ=0 EndX=-1000 EndY=5 EndZ=0
    g5: LineSegment StartX=-1000 StartY=5 StartZ=0 EndX=-1000 EndY=15 EndZ=0
    g6: LineSegment StartX=-1000 StartY=15 StartZ=0 EndX=-1004 EndY=15 EndZ=0
    g7: LineSegment StartX=-1004 StartY=15 StartZ=0 EndX=-1004 EndY=5 EndZ=0
    g8: LineSegment StartX=-604.4 StartY=15 StartZ=0 EndX=-600.4 EndY=15 EndZ=0
    g9: LineSegment StartX=-600.4 StartY=15 StartZ=0 EndX=-600.4 EndY=5 EndZ=0
    g10: LineSegment StartX=-600.4 StartY=5 StartZ=0 EndX=-604.4 EndY=5 EndZ=0
    g11: LineSegment StartX=-604.4 StartY=5 StartZ=0 EndX=-604.4 EndY=15 EndZ=0
    g12: LineSegment StartX=-604.4 StartY=-5 StartZ=0 EndX=-600.4 EndY=-5 EndZ=0
    g13: LineSegment StartX=-600.4 StartY=-5 StartZ=0 EndX=-600.4 EndY=-15 EndZ=0
    g14: LineSegment StartX=-600.4 StartY=-15 StartZ=0 EndX=-604.4 EndY=-15 EndZ=0
    g15: LineSegment StartX=-604.4 StartY=-15 StartZ=0 EndX=-604.4 EndY=-5 EndZ=0
    g16: GeomPoint X=-602.4 Y=0 Z=0
    g17: LineSegment StartX=-202.8 StartY=15 StartZ=0 EndX=-198.8 EndY=15 EndZ=0
    g18: LineSegment StartX=-198.8 StartY=15 StartZ=0 EndX=-198.8 EndY=5 EndZ=0
    g19: LineSegment StartX=-198.8 StartY=5 StartZ=0 EndX=-202.8 EndY=5 EndZ=0
    g20: LineSegment StartX=-202.8 StartY=5 StartZ=0 EndX=-202.8 EndY=15 EndZ=0
    g21: LineSegment StartX=-202.8 StartY=-5 StartZ=0 EndX=-198.8 EndY=-5 EndZ=0
    g22: LineSegment StartX=-198.8 StartY=-5 StartZ=0 EndX=-198.8 EndY=-15 EndZ=0
    g23: LineSegment StartX=-198.8 StartY=-15 StartZ=0 EndX=-202.8 EndY=-15 EndZ=0
    g24: LineSegment StartX=-202.8 StartY=-15 StartZ=0 EndX=-202.8 EndY=-5 EndZ=0
    g25: GeomPoint X=-200.8 Y=0 Z=0
    g26: LineSegment StartX=198.8 StartY=15 StartZ=0 EndX=202.8 EndY=15 EndZ=0
    g27: LineSegment StartX=202.8 StartY=15 StartZ=0 EndX=202.8 EndY=5 EndZ=0
    g28: LineSegment StartX=202.8 StartY=5 StartZ=0 EndX=198.8 EndY=5 EndZ=0
    g29: LineSegment StartX=198.8 StartY=5 StartZ=0 EndX=198.8 EndY=15 EndZ=0
    g30: LineSegment StartX=198.8 StartY=-5 StartZ=0 EndX=202.8 EndY=-5 EndZ=0
    g31: LineSegment StartX=202.8 StartY=-5 StartZ=0 EndX=202.8 EndY=-15 EndZ=0
    g32: LineSegment StartX=202.8 StartY=-15 StartZ=0 EndX=198.8 EndY=-15 EndZ=0
    g33: LineSegment StartX=198.8 StartY=-15 StartZ=0 EndX=198.8 EndY=-5 EndZ=0
    g34: GeomPoint X=200.8 Y=0 Z=0
    g35: LineSegment StartX=600.4 StartY=15 StartZ=0 EndX=604.4 EndY=15 EndZ=0
    g36: LineSegment StartX=604.4 StartY=15 StartZ=0 EndX=604.4 EndY=5 EndZ=0
    g37: LineSegment StartX=604.4 StartY=5 StartZ=0 EndX=600.4 EndY=5 EndZ=0
    g38: LineSegment StartX=600.4 StartY=5 StartZ=0 EndX=600.4 EndY=15 EndZ=0
    g39: LineSegment StartX=600.4 StartY=-5 StartZ=0 EndX=604.4 EndY=-5 EndZ=0
    g40: LineSegment StartX=604.4 StartY=-5 StartZ=0 EndX=604.4 EndY=-15 EndZ=0
    g41: LineSegment StartX=604.4 StartY=-15 StartZ=0 EndX=600.4 EndY=-15 EndZ=0
    g42: LineSegment StartX=600.4 StartY=-15 StartZ=0 EndX=600.4 EndY=-5 EndZ=0
    g43: GeomPoint X=602.4 Y=0 Z=0
    g44: LineSegment StartX=1000 StartY=15 StartZ=0 EndX=1004 EndY=15 EndZ=0
    g45: LineSegment StartX=1004 StartY=15 StartZ=0 EndX=1004 EndY=5 EndZ=0
    g46: LineSegment StartX=1004 StartY=5 StartZ=0 EndX=1000 EndY=5 EndZ=0
    g47: LineSegment StartX=1000 StartY=5 StartZ=0 EndX=1000 EndY=15 EndZ=0
    g48: LineSegment StartX=1000 StartY=-5 StartZ=0 EndX=1004 EndY=-5 EndZ=0
    g49: LineSegment StartX=1004 StartY=-5 StartZ=0 EndX=1004 EndY=-15 EndZ=0
    g50: LineSegment StartX=1004 StartY=-15 StartZ=0 EndX=1000 EndY=-15 EndZ=0
    g51: LineSegment StartX=1000 StartY=-15 StartZ=0 EndX=1000 EndY=-5 EndZ=0
    g52: GeomPoint X=1002 Y=0 Z=0
  constraints (153):
    c: Coincident(g0,g1)
    c: Coincident(g1,g2)
    c: Coincident(g2,g3)
    c: Coincident(g3,g0)
    c: Horizontal(g0)
    c: Horizontal(g2)
    c: Vertical(g1)
    c: Vertical(g3)
    c: Coincident(g0,g-3)
    c: Coincident(g4,g5)
    c: Coincident(g5,g6)
    c: Coincident(g6,g7)
    c: Coincident(g7,g4)
    c: Horizontal(g4)
    c: Horizontal(g6)
    c: Vertical(g5)
    c: Vertical(g7)
    c: DistanceY(g0,g2) = 10
    c: Equal(g3,g7)
    c: Vertical(g4,g1)
    c: Vertical(g2,g4)
    c: DistanceY(g2,g4) = 10
    c: DistanceX(g0,g0) = 4
    c: Coincident(g8,g9)
    c: Coincident(g9,g10)
    c: Coincident(g10,g11)
    c: Coincident(g11,g8)
    c: Horizontal(g8)
    c: Horizontal(g10)
    c: Vertical(g9)
    c: Vertical(g11)
    c: Coincident(g12,g13)
    c: Coincident(g13,g14)
    c: Coincident(g14,g15)
    c: Coincident(g15,g12)
    c: Horizontal(g12)
    c: Horizontal(g14)
    c: Vertical(g13)
    c: Vertical(g15)
    c: PointOnObject(g16,g-1)
    c: Horizontal(g0,g14)
    c: Horizontal(g1,g12)
    c: Horizontal(g4,g10)
    c: Horizontal(g8,g5)
    c: Vertical(g12,g10)
    c: Vertical(g9,g12)
    c: DistanceX(g14,g13) = 4
    c: DistanceX(g14,g16) = 2
    c: DistanceX(g0,g16) = 401.6
    c: Coincident(g17,g18)
    c: Coincident(g18,g19)
    c: Coincident(g19,g20)
    c: Coincident(g20,g17)
    c: Horizontal(g17)
    c: Horizontal(g19)
    c: Vertical(g18)
    c: Vertical(g20)
    c: Coincident(g21,g22)
    c: Coincident(g22,g23)
    c: Coincident(g23,g24)
    c: Coincident(g24,g21)
    c: Horizontal(g21)
    c: Horizontal(g23)
    c: Vertical(g22)
    c: Vertical(g24)
    c: Vertical(g21,g19)
    c: Vertical(g18,g21)
    c: DistanceX(g23,g22) = 4
    c: DistanceX(g23,g25) = 2
    c: PointOnObject(g25,g-1)
    c: Horizontal(g13,g23)
    c: Horizontal(g21,g12)
    c: Horizontal(g19,g9)
    c: Horizontal(g8,g17)
    c: DistanceX(g16,g25) = 401.6
    c: Coincident(g26,g27)
    c: Coincident(g27,g28)
    c: Coincident(g28,g29)
    c: Coincident(g29,g26)
    c: Horizontal(g26)
    c: Horizontal(g28)
    c: Vertical(g27)
    c: Vertical(g29)
    c: Coincident(g30,g31)
    c: Coincident(g31,g32)
    c: Coincident(g32,g33)
    c: Coincident(g33,g30)
    c: Horizontal(g30)
    c: Horizontal(g32)
    c: Vertical(g31)
    c: Vertical(g33)
    c: Vertical(g30,g28)
    c: Vertical(g27,g30)
    c: DistanceX(g32,g31) = 4
    c: DistanceX(g32,g34) = 2
    c: PointOnObject(g34,g-1)
    c: Horizontal(g17,g26)
    c: Horizontal(g28,g18)
    c: Horizontal(g32,g22)
    c: Horizontal(g21,g30)
    c: DistanceX(g25,g34) = 401.6
    c: Coincident(g35,g36)
    c: Coincident(g36,g37)
    c: Coincident(g37,g38)
    c: Coincident(g38,g35)
    c: Horizontal(g35)
    c: Horizontal(g37)
    c: Vertical(g36)
    c: Vertical(g38)
    c: Coincident(g39,g40)
    c: Coincident(g40,g41)
    c: Coincident(g41,g42)
    c: Coincident(g42,g39)
    c: Horizontal(g39)
    c: Horizontal(g41)
    c: Vertical(g40)
    c: Vertical(g42)
    c: Vertical(g39,g37)
    c: Vertical(g36,g39)
    c: DistanceX(g41,g40) = 4
    c: DistanceX(g41,g43) = 2
    c: PointOnObject(g43,g-1)
    c: Horizontal(g41,g31)
    c: Horizontal(g30,g39)
    c: Horizontal(g27,g37)
    c: Horizontal(g35,g26)
    c: DistanceX(g34,g43) = 401.6
    c: Coincident(g44,g45)
    c: Coincident(g45,g46)
    c: Coincident(g46,g47)
    c: Coincident(g47,g44)
    c: Horizontal(g44)
    c: Horizontal(g46)
    c: Vertical(g45)
    c: Vertical(g47)
    c: Coincident(g48,g49)
    c: Coincident(g49,g50)
    c: Coincident(g50,g51)
    c: Coincident(g51,g48)
    c: Horizontal(g48)
    c: Horizontal(g50)
    c: Vertical(g49)
    c: Vertical(g51)
    c: Vertical(g48,g46)
    c: Vertical(g45,g48)
    c: DistanceX(g50,g49) = 4
    c: DistanceX(g50,g52) = 2
    c: PointOnObject(g52,g-1)
    c: Horizontal(g50,g40)
    c: Horizontal(g39,g48)
    c: Horizontal(g46,g36)
    c: Horizontal(g44,g35)
    c: DistanceX(g43,g52) = 399.6
FEATURE [TechDraw::DrawSVGTemplate] Template014
  Height = 297
  Orientation = 1
  Width = 420
FEATURE [TechDraw::DrawViewPart] View011
  CoarseView = false
  Direction = (-1,0,0)
  Focus = 100
  HardHidden = false
  IsoCount = 0
  IsoHidden = false
  IsoVisible = false
  LockPosition = false
  Perspective = false
  Rotation = 0
  Scale = 0.15
  ScaleType = 0
  SeamHidden = false
  SeamVisible = true
  SmoothHidden = false
  SmoothVisible = true
  Source = -> [Body019]
  X = 61.8711
  XDirection = (0,-1,0)
  Y = 54.394
FEATURE [TechDraw::DrawViewDimension] Dimension156
  Arbitrary = false
  ArbitraryTolerances = false
  EqualTolerance = true
  FormatSpec = %.2f
  FormatSpecOverTolerance = %+.2f
  FormatSpecUnderTolerance = %+.2f
  Inverted = false
  LockPosition = false
  MeasureType = 1
  OverTolerance = 0
  References2D = -> [View011]
  Rotation = 0
  Scale = 0.15
  ScaleType = 0
  TheoreticalExact = false
  Type = 1
  UnderTolerance = 0
  X = -1.96542
  Y = -35.9966
FEATURE [TechDraw::DrawViewDimension] Dimension157
  Arbitrary = false
  ArbitraryTolerances = false
  EqualTolerance = true
  FormatSpec = %.2f
  FormatSpecOverTolerance = %+.2f
  FormatSpecUnderTolerance = %+.2f
  Inverted = false
  LockPosition = false
  MeasureType = 1
  OverTolerance = 0
  References2D = -> [View011]
  Rotation = 0
  Scale = 0.15
  ScaleType = 0
  TheoreticalExact = false
  Type = 2
  UnderTolerance = 0
  X = -40.5638
  Y = -27.892
FEATURE [TechDraw::DrawViewDimension] Dimension158
  Arbitrary = false
  ArbitraryTolerances = false
  EqualTolerance = true
  FormatSpec = %.2f
  FormatSpecOverTolerance = %+.2f
  FormatSpecUnderTolerance = %+.2f
  Inverted = false
  LockPosition = false
  MeasureType = 1
  OverTolerance = 0
  References2D = -> [View011]
  Rotation = 0
  Scale = 0.15
  ScaleType = 0
  TheoreticalExact = false
  Type = 2
  UnderTolerance = 0
  X = -45.9065
  Y = 32.5831
FEATURE [TechDraw::DrawViewDimension] Dimension159
  Arbitrary = false
  ArbitraryTolerances = false
  EqualTolerance = true
  FormatSpec = %.2f
  FormatSpecOverTolerance = %+.2f
  FormatSpecUnderTolerance = %+.2f
  Inverted = false
  LockPosition = false
  MeasureType = 1
  OverTolerance = 0
  References2D = -> [View011]
  Rotation = 0
  Scale = 0.15
  ScaleType = 0
  TheoreticalExact = false
  Type = 1
  UnderTolerance = 0
  X = -10.7604
  Y = 33.6384
FEATURE [TechDraw::DrawViewDimension] Dimension160
  Arbitrary = false
  ArbitraryTolerances = false
  EqualTolerance = true
  FormatSpec = %.2f
  FormatSpecOverTolerance = %+.2f
  FormatSpecUnderTolerance = %+.2f
  Inverted = false
  LockPosition = false
  MeasureType = 1
  OverTolerance = 0
  References2D = -> [View011]
  Rotation = 0
  Scale = 0.15
  ScaleType = 0
  TheoreticalExact = false
  Type = 1
  UnderTolerance = 0
  X = 30.7645
  Y = 34.1267
FEATURE [TechDraw::DrawViewDimension] Dimension161
  Arbitrary = false
  ArbitraryTolerances = false
  EqualTolerance = true
  FormatSpec = %.2f
  FormatSpecOverTolerance = %+.2f
  FormatSpecUnderTolerance = %+.2f
  Inverted = false
  LockPosition = false
  MeasureType = 1
  OverTolerance = 0
  References2D = -> [View011]
  Rotation = 0
  Scale = 0.15
  ScaleType = 0
  TheoreticalExact = false
  Type = 2
  UnderTolerance = 0
  X = -37.9882
  Y = 33.6384
FEATURE [TechDraw::DrawViewDimension] Dimension162
  Arbitrary = false
  ArbitraryTolerances = false
  EqualTolerance = true
  FormatSpec = %.2f
  FormatSpecOverTolerance = %+.2f
  FormatSpecUnderTolerance = %+.2f
  Inverted = false
  LockPosition = false
  MeasureType = 1
  OverTolerance = 0
  References2D = -> [View011]
  Rotation = 0
  Scale = 0.15
  ScaleType = 0
  TheoreticalExact = false
  Type = 2
  UnderTolerance = 0
  X = 29.4573
  Y = -27.1015
FEATURE [TechDraw::DrawViewSection] SectionView011  label="Section L - L"
  BaseView = -> View011
  CoarseView = false
  CutSurfaceDisplay = 2
  Direction = (0,1,0)
  FileGeomPattern = <userpath>/AppData/Local/Programs/FreeCAD 0.19/data/Mod/TechDraw/PAT/FCPAT.pat
  FileHatchPattern = <userpath>/AppData/Local/Programs/FreeCAD 0.19/data/Mod/TechDraw/Patterns/simple.svg
  Focus = 100
  FuseBeforeCut = false
  HardHidden = false
  HatchScale = 1
  IsoCount = 0
  IsoHidden = false
  IsoVisible = false
  LockPosition = false
  NameGeomPattern = Diamond
  Perspective = false
  Rotation = 0
  Scale = 0.15
  ScaleType = 0
  SeamHidden = false
  SeamVisible = true
  SectionDirection = 0
  SectionNormal = (0,1,0)
  SectionOrigin = (-1002,-742.56,-25.85)
  SectionSymbol = L
  SmoothHidden = false
  SmoothVisible = true
  Source = -> [Body019]
  X = 119.74
  XDirection = (-1,0,0)
  Y = 48.4288
FEATURE [TechDraw::DrawViewDimension] Dimension163
  Arbitrary = false
  ArbitraryTolerances = false
  EqualTolerance = true
  FormatSpec = %.2f
  FormatSpecOverTolerance = %+.2f
  FormatSpecUnderTolerance = %+.2f
  Inverted = false
  LockPosition = false
  MeasureType = 1
  OverTolerance = 0
  References2D = -> [SectionView011]
  Rotation = 0
  Scale = 0.15
  ScaleType = 0
  TheoreticalExact = false
  Type = 1
  UnderTolerance = 0
  X = 21.545
  Y = 21.6756
FEATURE [TechDraw::DrawViewDimension] Dimension164
  Arbitrary = false
  ArbitraryTolerances = false
  EqualTolerance = true
  FormatSpec = %.2f
  FormatSpecOverTolerance = %+.2f
  FormatSpecUnderTolerance = %+.2f
  Inverted = false
  LockPosition = false
  MeasureType = 1
  OverTolerance = 0
  References2D = -> [View011]
  Rotation = 0
  Scale = 0.15
  ScaleType = 0
  TheoreticalExact = false
  Type = 2
  UnderTolerance = 0
  X = 34.3708
  Y = 11.6476
FEATURE [TechDraw::DrawViewDimension] Dimension165
  Arbitrary = false
  ArbitraryTolerances = false
  EqualTolerance = true
  FormatSpec = %.2f
  FormatSpecOverTolerance = %+.2f
  FormatSpecUnderTolerance = %+.2f
  Inverted = false
  LockPosition = false
  MeasureType = 1
  OverTolerance = 0
  References2D = -> [View011]
  Rotation = 0
  Scale = 0.15
  ScaleType = 0
  TheoreticalExact = false
  Type = 2
  UnderTolerance = 0
  X = 23.9199
  Y = -27.1013
FEATURE [TechDraw::DrawViewPart] View012
  CoarseView = false
  Direction = (-1,0,0)
  Focus = 100
  HardHidden = false
  IsoCount = 0
  IsoHidden = false
  IsoVisible = false
  LockPosition = false
  Perspective = false
  Rotation = 0
  Scale = 0.15
  ScaleType = 0
  SeamHidden = false
  SeamVisible = true
  SmoothHidden = false
  SmoothVisible = true
  Source = -> [Pocket020]
  X = 192.82
  XDirection = (0,-1,0)
  Y = 54.4765
FEATURE [TechDraw::DrawViewDimension] Dimension166
  Arbitrary = false
  ArbitraryTolerances = false
  EqualTolerance = true
  FormatSpec = %.2f
  FormatSpecOverTolerance = %+.2f
  FormatSpecUnderTolerance = %+.2f
  Inverted = false
  LockPosition = false
  MeasureType = 1
  OverTolerance = 0
  References2D = -> [View012]
  Rotation = 0
  Scale = 0.15
  ScaleType = 0
  TheoreticalExact = false
  Type = 2
  UnderTolerance = 0
  X = -38.8359
  Y = 23.3056
FEATURE [TechDraw::DrawViewDimension] Dimension167
  Arbitrary = false
  ArbitraryTolerances = false
  EqualTolerance = true
  FormatSpec = %.2f
  FormatSpecOverTolerance = %+.2f
  FormatSpecUnderTolerance = %+.2f
  Inverted = false
  LockPosition = false
  MeasureType = 1
  OverTolerance = 0
  References2D = -> [View012]
  Rotation = 0
  Scale = 0.15
  ScaleType = 0
  TheoreticalExact = false
  Type = 2
  UnderTolerance = 0
  X = -30.3217
  Y = 23.1247
FEATURE [TechDraw::DrawViewDimension] Dimension168
  Arbitrary = false
  ArbitraryTolerances = false
  EqualTolerance = true
  FormatSpec = %.2f
  FormatSpecOverTolerance = %+.2f
  FormatSpecUnderTolerance = %+.2f
  Inverted = false
  LockPosition = false
  MeasureType = 1
  OverTolerance = 0
  References2D = -> [View012]
  Rotation = 0
  Scale = 0.15
  ScaleType = 0
  TheoreticalExact = false
  Type = 1
  UnderTolerance = 0
  X = -36.3585
  Y = -22.6065
FEATURE [TechDraw::DrawViewDimension] Dimension169
  Arbitrary = false
  ArbitraryTolerances = false
  EqualTolerance = true
  FormatSpec = %.2f
  FormatSpecOverTolerance = %+.2f
  FormatSpecUnderTolerance = %+.2f
  Inverted = false
  LockPosition = false
  MeasureType = 1
  OverTolerance = 0
  References2D = -> [View012]
  Rotation = 0
  Scale = 0.15
  ScaleType = 0
  TheoreticalExact = false
  Type = 1
  UnderTolerance = 0
  X = -36.9573
  Y = -32.294
FEATURE [TechDraw::DrawViewDimension] Dimension170
  Arbitrary = false
  ArbitraryTolerances = false
  EqualTolerance = true
  FormatSpec = ⌀%.2f
  FormatSpecOverTolerance = %+.2f
  FormatSpecUnderTolerance = %+.2f
  Inverted = false
  LockPosition = false
  MeasureType = 1
  OverTolerance = 0
  References2D = -> [View012]
  Rotation = 0
  Scale = 0.15
  ScaleType = 0
  TheoreticalExact = false
  Type = 5
  UnderTolerance = 0
  X = 0.833503
  Y = 19.3373
FEATURE [TechDraw::DrawViewDimension] Dimension171
  Arbitrary = false
  ArbitraryTolerances = false
  EqualTolerance = true
  FormatSpec = ⌀%.2f
  FormatSpecOverTolerance = %+.2f
  FormatSpecUnderTolerance = %+.2f
  Inverted = false
  LockPosition = false
  MeasureType = 1
  OverTolerance = 0
  References2D = -> [View012]
  Rotation = 0
  Scale = 0.15
  ScaleType = 0
  TheoreticalExact = false
  Type = 5
  UnderTolerance = 0
  X = 17.6703
  Y = 18.6705
FEATURE [TechDraw::DrawViewPart] View013
  CoarseView = false
  Direction = (0,-1,0)
  Focus = 100
  HardHidden = false
  IsoCount = 0
  IsoHidden = false
  IsoVisible = false
  LockPosition = false
  Perspective = false
  Rotation = 0
  Scale = 0.15
  ScaleType = 0
  SeamHidden = false
  SeamVisible = true
  SmoothHidden = false
  SmoothVisible = true
  Source = -> [Pocket018]
  X = 206.682
  XDirection = (1,0,0)
  Y = 265.582
FEATURE [TechDraw::DrawViewDimension] Dimension172
  Arbitrary = false
  ArbitraryTolerances = false
  EqualTolerance = true
  FormatSpec = %.2f
  FormatSpecOverTolerance = %+.2f
  FormatSpecUnderTolerance = %+.2f
  Inverted = false
  LockPosition = false
  MeasureType = 1
  OverTolerance = 0
  References2D = -> [View013]
  Rotation = 0
  Scale = 0.15
  ScaleType = 0
  TheoreticalExact = false
  Type = 1
  UnderTolerance = 0
  X = -0.888596
  Y = -24.4948
FEATURE [TechDraw::DrawViewDimension] Dimension173
  Arbitrary = false
  ArbitraryTolerances = false
  EqualTolerance = true
  FormatSpec = %.2f
  FormatSpecOverTolerance = %+.2f
  FormatSpecUnderTolerance = %+.2f
  Inverted = false
  LockPosition = false
  MeasureType = 1
  OverTolerance = 0
  References2D = -> [View013]
  Rotation = 0
  Scale = 0.15
  ScaleType = 0
  TheoreticalExact = false
  Type = 1
  UnderTolerance = 0
  X = -123.907
  Y = -18.7579
FEATURE [TechDraw::DrawViewDimension] Dimension174
  Arbitrary = false
  ArbitraryTolerances = false
  EqualTolerance = true
  FormatSpec = %.2f
  FormatSpecOverTolerance = %+.2f
  FormatSpecUnderTolerance = %+.2f
  Inverted = false
  LockPosition = false
  MeasureType = 1
  OverTolerance = 0
  References2D = -> [View013]
  Rotation = 0
  Scale = 0.15
  ScaleType = 0
  TheoreticalExact = false
  Type = 1
  UnderTolerance = 0
  X = -83.9618
  Y = -11.7587
FEATURE [TechDraw::DrawViewDimension] Dimension175
  Arbitrary = false
  ArbitraryTolerances = false
  EqualTolerance = true
  FormatSpec = %.2f
  FormatSpecOverTolerance = %+.2f
  FormatSpecUnderTolerance = %+.2f
  Inverted = false
  LockPosition = false
  MeasureType = 1
  OverTolerance = 0
  References2D = -> [View013]
  Rotation = 0
  Scale = 0.15
  ScaleType = 0
  TheoreticalExact = false
  Type = 2
  UnderTolerance = 0
  X = -166.332
  Y = -28.3593
FEATURE [TechDraw::DrawViewDimension] Dimension176
  Arbitrary = false
  ArbitraryTolerances = false
  EqualTolerance = true
  FormatSpec = %.2f
  FormatSpecOverTolerance = %+.2f
  FormatSpecUnderTolerance = %+.2f
  Inverted = false
  LockPosition = false
  MeasureType = 1
  OverTolerance = 0
  References2D = -> [View013]
  Rotation = 0
  Scale = 0.15
  ScaleType = 0
  TheoreticalExact = false
  Type = 2
  UnderTolerance = 0
  X = -175.228
  Y = -28.3477
FEATURE [TechDraw::DrawViewDimension] Dimension177
  Arbitrary = false
  ArbitraryTolerances = false
  EqualTolerance = true
  FormatSpec = %.2f
  FormatSpecOverTolerance = %+.2f
  FormatSpecUnderTolerance = %+.2f
  Inverted = false
  LockPosition = false
  MeasureType = 1
  OverTolerance = 0
  References2D = -> [View013]
  Rotation = 0
  Scale = 0.15
  ScaleType = 0
  TheoreticalExact = false
  Type = 2
  UnderTolerance = 0
  X = -184.095
  Y = -27.853
FEATURE [TechDraw::DrawViewDimension] Dimension178
  Arbitrary = false
  ArbitraryTolerances = false
  EqualTolerance = true
  FormatSpec = %.2f
  FormatSpecOverTolerance = %+.2f
  FormatSpecUnderTolerance = %+.2f
  Inverted = false
  LockPosition = false
  MeasureType = 1
  OverTolerance = 0
  References2D = -> [View013]
  Rotation = 0
  Scale = 0.15
  ScaleType = 0
  TheoreticalExact = false
  Type = 2
  UnderTolerance = 0
  X = -191.968
  Y = -28.6334
FEATURE [TechDraw::DrawViewDimension] Dimension179
  Arbitrary = false
  ArbitraryTolerances = false
  EqualTolerance = true
  FormatSpec = ⌀%.2f
  FormatSpecOverTolerance = %+.2f
  FormatSpecUnderTolerance = %+.2f
  Inverted = false
  LockPosition = false
  MeasureType = 1
  OverTolerance = 0
  References2D = -> [View013]
  Rotation = 0
  Scale = 0.15
  ScaleType = 0
  TheoreticalExact = false
  Type = 5
  UnderTolerance = 0
  X = -52.2555
  Y = -16.2825
FEATURE [TechDraw::DrawViewSection] SectionView012  label="Section M - M"
  BaseView = -> View013
  CoarseView = false
  CutSurfaceDisplay = 2
  Direction = (-1,0,0)
  FileGeomPattern = <userpath>/AppData/Local/Programs/FreeCAD 0.19/data/Mod/TechDraw/PAT/FCPAT.pat
  FileHatchPattern = <userpath>/AppData/Local/Programs/FreeCAD 0.19/data/Mod/TechDraw/Patterns/simple.svg
  Focus = 100
  FuseBeforeCut = false
  HardHidden = false
  HatchScale = 1
  IsoCount = 0
  IsoHidden = false
  IsoVisible = false
  LockPosition = false
  NameGeomPattern = Diamond
  Perspective = false
  Rotation = 0
  Scale = 0.15
  ScaleType = 0
  SeamHidden = false
  SeamVisible = true
  SectionDirection = 0
  SectionNormal = (-1,0,0)
  SectionOrigin = (0,-2,11.5)
  SectionSymbol = M
  SmoothHidden = false
  SmoothVisible = true
  Source = -> [Pocket018]
  X = 383.29
  XDirection = (0,-1,0)
  Y = 265.63
FEATURE [TechDraw::DrawViewDimension] Dimension180
  Arbitrary = false
  ArbitraryTolerances = false
  EqualTolerance = true
  FormatSpec = %.2f
  FormatSpecOverTolerance = %+.2f
  FormatSpecUnderTolerance = %+.2f
  Inverted = false
  LockPosition = false
  MeasureType = 1
  OverTolerance = 0
  References2D = -> [SectionView012]
  Rotation = 0
  Scale = 0.15
  ScaleType = 0
  TheoreticalExact = false
  Type = 1
  UnderTolerance = 0
  X = 14.603
  Y = -23.5279
FEATURE [PartDesign::Pocket] Pocket024
  BaseFeature = -> Pad028
  Length = 4
  Length2 = 100
  Placement = pos=(0,0,0) rot=(1,0,0;1.5708rad)
  Profile = -> Sketch057
  Type = 0
FEATURE [PartDesign::Body] Body027  label="KorbordFramsida"
  Group = -> [Sketch056,Pad028,Sketch057,Pocket024]
  Origin = -> Origin027
  Placement = pos=(0,-877.1,-104.76) rot=(0,0,1;0rad)
  Tip = -> Pocket024
FEATURE [TechDraw::DrawViewPart] View014
  CoarseView = false
  Direction = (0,-1,0)
  Focus = 100
  HardHidden = false
  IsoCount = 0
  IsoHidden = false
  IsoVisible = false
  LockPosition = false
  Perspective = false
  Rotation = 0
  Scale = 0.15
  ScaleType = 0
  SeamHidden = false
  SeamVisible = true
  SmoothHidden = false
  SmoothVisible = true
  Source = -> [Pocket024]
  X = 205.94
  XDirection = (1,0,0)
  Y = 212.523
FEATURE [TechDraw::DrawViewDimension] Dimension181
  Arbitrary = false
  ArbitraryTolerances = false
  EqualTolerance = true
  FormatSpec = %.2f
  FormatSpecOverTolerance = %+.2f
  FormatSpecUnderTolerance = %+.2f
  Inverted = false
  LockPosition = false
  MeasureType = 1
  OverTolerance = 0
  References2D = -> [View014]
  Rotation = 0
  Scale = 0.15
  ScaleType = 0
  TheoreticalExact = false
  Type = 1
  UnderTolerance = 0
  X = 16.4572
  Y = -22.36
FEATURE [TechDraw::DrawViewDimension] Dimension182
  Arbitrary = false
  ArbitraryTolerances = false
  EqualTolerance = true
  FormatSpec = %.2f
  FormatSpecOverTolerance = %+.2f
  FormatSpecUnderTolerance = %+.2f
  Inverted = false
  LockPosition = false
  MeasureType = 1
  OverTolerance = 0
  References2D = -> [View013]
  Rotation = 0
  Scale = 0.15
  ScaleType = 0
  TheoreticalExact = false
  Type = 1
  UnderTolerance = 0
  X = -169.629
  Y = 20.8995
FEATURE [TechDraw::DrawViewDimension] Dimension183
  Arbitrary = false
  ArbitraryTolerances = false
  EqualTolerance = true
  FormatSpec = %.2f
  FormatSpecOverTolerance = %+.2f
  FormatSpecUnderTolerance = %+.2f
  Inverted = false
  LockPosition = false
  MeasureType = 1
  OverTolerance = 0
  References2D = -> [View014]
  Rotation = 0
  Scale = 0.15
  ScaleType = 0
  TheoreticalExact = false
  Type = 1
  UnderTolerance = 0
  X = -130.136
  Y = 18.8216
FEATURE [TechDraw::DrawViewDimension] Dimension187
  Arbitrary = false
  ArbitraryTolerances = false
  EqualTolerance = true
  FormatSpec = %.2f
  FormatSpecOverTolerance = %+.2f
  FormatSpecUnderTolerance = %+.2f
  Inverted = false
  LockPosition = false
  MeasureType = 1
  OverTolerance = 0
  References2D = -> [View014]
  Rotation = 0
  Scale = 0.15
  ScaleType = 0
  TheoreticalExact = false
  Type = 2
  UnderTolerance = 0
  X = -179.189
  Y = -25.7431
FEATURE [TechDraw::DrawViewDimension] Dimension188
  Arbitrary = false
  ArbitraryTolerances = false
  EqualTolerance = true
  FormatSpec = %.2f
  FormatSpecOverTolerance = %+.2f
  FormatSpecUnderTolerance = %+.2f
  Inverted = false
  LockPosition = false
  MeasureType = 1
  OverTolerance = 0
  References2D = -> [View014]
  Rotation = 0
  Scale = 0.15
  ScaleType = 0
  TheoreticalExact = false
  Type = 2
  UnderTolerance = 0
  X = -160.125
  Y = -25.6702
FEATURE [TechDraw::DrawViewDimension] Dimension189
  Arbitrary = false
  ArbitraryTolerances = false
  EqualTolerance = true
  FormatSpec = %.2f
  FormatSpecOverTolerance = %+.2f
  FormatSpecUnderTolerance = %+.2f
  Inverted = false
  LockPosition = false
  MeasureType = 1
  OverTolerance = 0
  References2D = -> [View014]
  Rotation = 0
  Scale = 0.15
  ScaleType = 0
  TheoreticalExact = false
  Type = 2
  UnderTolerance = 0
  X = -166.261
  Y = -25.485
FEATURE [TechDraw::DrawViewDimension] Dimension190
  Arbitrary = false
  ArbitraryTolerances = false
  EqualTolerance = true
  FormatSpec = %.2f
  FormatSpecOverTolerance = %+.2f
  FormatSpecUnderTolerance = %+.2f
  Inverted = false
  LockPosition = false
  MeasureType = 1
  OverTolerance = 0
  References2D = -> [View014]
  Rotation = 0
  Scale = 0.15
  ScaleType = 0
  TheoreticalExact = false
  Type = 2
  UnderTolerance = 0
  X = -172.397
  Y = -25.2998
FEATURE [TechDraw::DrawViewDimension] Dimension191
  Arbitrary = false
  ArbitraryTolerances = false
  EqualTolerance = true
  FormatSpec = %.2f
  FormatSpecOverTolerance = %+.2f
  FormatSpecUnderTolerance = %+.2f
  Inverted = false
  LockPosition = false
  MeasureType = 1
  OverTolerance = 0
  References2D = -> [View014]
  Rotation = 0
  Scale = 0.15
  ScaleType = 0
  TheoreticalExact = false
  Type = 1
  UnderTolerance = 0
  X = -117.197
  Y = -8.22317
FEATURE [TechDraw::DrawViewDimension] Dimension192
  Arbitrary = false
  ArbitraryTolerances = false
  EqualTolerance = true
  FormatSpec = %.2f
  FormatSpecOverTolerance = %+.2f
  FormatSpecUnderTolerance = %+.2f
  Inverted = false
  LockPosition = false
  MeasureType = 1
  OverTolerance = 0
  References2D = -> [View014]
  Rotation = 0
  Scale = 0.15
  ScaleType = 0
  TheoreticalExact = false
  Type = 1
  UnderTolerance = 0
  X = -60.8062
  Y = -8.59406
FEATURE [TechDraw::DrawViewSection] SectionView013  label="Section N - N"
  BaseView = -> View014
  CoarseView = false
  CutSurfaceDisplay = 2
  Direction = (-1,0,0)
  FileGeomPattern = <userpath>/AppData/Local/Programs/FreeCAD 0.19/data/Mod/TechDraw/PAT/FCPAT.pat
  FileHatchPattern = <userpath>/AppData/Local/Programs/FreeCAD 0.19/data/Mod/TechDraw/Patterns/simple.svg
  Focus = 100
  FuseBeforeCut = false
  HardHidden = false
  HatchScale = 1
  IsoCount = 0
  IsoHidden = false
  IsoVisible = false
  LockPosition = false
  NameGeomPattern = Diamond
  Perspective = false
  Rotation = 0
  Scale = 0.15
  ScaleType = 0
  SeamHidden = false
  SeamVisible = true
  SectionDirection = 0
  SectionNormal = (-1,0,0)
  SectionOrigin = (0,-2,22.35)
  SectionSymbol = N
  SmoothHidden = false
  SmoothVisible = true
  Source = -> [Pocket024]
  X = 383.21
  XDirection = (0,-1,0)
  Y = 212.517
FEATURE [TechDraw::DrawViewDimension] Dimension193
  Arbitrary = false
  ArbitraryTolerances = false
  EqualTolerance = true
  FormatSpec = %.2f
  FormatSpecOverTolerance = %+.2f
  FormatSpecUnderTolerance = %+.2f
  Inverted = false
  LockPosition = false
  MeasureType = 1
  OverTolerance = 0
  References2D = -> [SectionView013]
  Rotation = 0
  Scale = 0.15
  ScaleType = 0
  TheoreticalExact = false
  Type = 1
  UnderTolerance = 0
  X = 14.643
  Y = -21.9258
FEATURE [TechDraw::DrawViewPart] View015
  CoarseView = false
  Direction = (0,0,1)
  Focus = 100
  HardHidden = false
  IsoCount = 0
  IsoHidden = false
  IsoVisible = false
  LockPosition = false
  Perspective = false
  Rotation = 0
  Scale = 0.15
  ScaleType = 0
  SeamHidden = false
  SeamVisible = true
  SmoothHidden = false
  SmoothVisible = true
  Source = -> [Pad027]
  X = 205.83
  XDirection = (1,0,0)
  Y = 141.4
FEATURE [TechDraw::DrawViewDimension] Dimension194
  Arbitrary = false
  ArbitraryTolerances = false
  EqualTolerance = true
  FormatSpec = %.2f
  FormatSpecOverTolerance = %+.2f
  FormatSpecUnderTolerance = %+.2f
  Inverted = false
  LockPosition = false
  MeasureType = 1
  OverTolerance = 0
  References2D = -> [View015]
  Rotation = 0
  Scale = 0.15
  ScaleType = 0
  TheoreticalExact = false
  Type = 1
  UnderTolerance = 0
  X = 14.424
  Y = -30.3665
FEATURE [TechDraw::DrawViewDimension] Dimension195
  Arbitrary = false
  ArbitraryTolerances = false
  EqualTolerance = true
  FormatSpec = %.2f
  FormatSpecOverTolerance = %+.2f
  FormatSpecUnderTolerance = %+.2f
  Inverted = false
  LockPosition = false
  MeasureType = 1
  OverTolerance = 0
  References2D = -> [View015]
  Rotation = 0
  Scale = 0.15
  ScaleType = 0
  TheoreticalExact = false
  Type = 2
  UnderTolerance = 0
  X = -169.154
  Y = 3.40797
FEATURE [TechDraw::DrawViewSection] SectionView014  label="Section O - O"
  BaseView = -> View015
  CoarseView = false
  CutSurfaceDisplay = 2
  Direction = (-1,0,0)
  FileGeomPattern = <userpath>/AppData/Local/Programs/FreeCAD 0.19/data/Mod/TechDraw/PAT/FCPAT.pat
  FileHatchPattern = <userpath>/AppData/Local/Programs/FreeCAD 0.19/data/Mod/TechDraw/Patterns/simple.svg
  Focus = 100
  FuseBeforeCut = false
  HardHidden = false
  HatchScale = 1
  IsoCount = 0
  IsoHidden = false
  IsoVisible = false
  LockPosition = false
  NameGeomPattern = Diamond
  Perspective = false
  Rotation = 0
  Scale = 0.15
  ScaleType = 0
  SeamHidden = false
  SeamVisible = true
  SectionDirection = 0
  SectionNormal = (-1,0,0)
  SectionOrigin = (0,-156.5,2)
  SectionSymbol = O
  SmoothHidden = false
  SmoothVisible = true
  Source = -> [Pad027]
  X = 383.52
  XDirection = (0,0,1)
  Y = 141.4
FEATURE [TechDraw::DrawViewDimension] Dimension196
  Arbitrary = false
  ArbitraryTolerances = false
  EqualTolerance = true
  FormatSpec = %.2f
  FormatSpecOverTolerance = %+.2f
  FormatSpecUnderTolerance = %+.2f
  Inverted = false
  LockPosition = false
  MeasureType = 1
  OverTolerance = 0
  References2D = -> [SectionView014]
  Rotation = 0
  Scale = 0.15
  ScaleType = 0
  TheoreticalExact = false
  Type = 1
  UnderTolerance = 0
  X = 13.5401
  Y = -35.2837
FEATURE [Sketcher::SketchObject] Sketch058
  FullyConstrained = true
  MapMode = 5
  Placement = pos=(0,0,0) rot=(1,0,0;1.5708rad)
  Support = -> [XZ_Plane028]
  sketch-geometry (4):
    g0: LineSegment StartX=-164 StartY=-45 StartZ=0 EndX=164 EndY=-45 EndZ=0
    g1: LineSegment StartX=164 StartY=-45 StartZ=0 EndX=164 EndY=45 EndZ=0
    g2: LineSegment StartX=164 StartY=45 StartZ=0 EndX=-164 EndY=45 EndZ=0
    g3: LineSegment StartX=-164 StartY=45 StartZ=0 EndX=-164 EndY=-45 EndZ=0
  constraints (11):
    c: Coincident(g0,g1)
    c: Coincident(g1,g2)
    c: Coincident(g2,g3)
    c: Coincident(g3,g0)
    c: Horizontal(g0)
    c: Horizontal(g2)
    c: Vertical(g1)
    c: Vertical(g3)
    c: Symmetric(g0,g1,g-1)
    c: DistanceX(g0,g0) = 328
    c: DistanceY(g0,g2) = 90
FEATURE [PartDesign::Pad] Pad029
  Direction = (1,1,1)
  Length = 4
  Length2 = 100
  Placement = pos=(0,0,0) rot=(1,0,0;1.5708rad)
  Profile = -> Sketch058
  Type = 0
FEATURE [Sketcher::SketchObject] Sketch059
  ExternalGeometry = -> [Pad029]
  FullyConstrained = true
  MapMode = 5
  Placement = pos=(0,-4,1.8e-15) rot=(1,0,0;1.5708rad)
  Support = -> [Pad029]
  sketch-geometry (71):
    g0: Circle CenterX=-83.33 CenterY=0 CenterZ=0 NormalX=0 NormalY=0 NormalZ=1 AngleXU=0 Radius=25
    g1: Circle CenterX=0 CenterY=0 CenterZ=0 NormalX=0 NormalY=0 NormalZ=1 AngleXU=0 Radius=25
    g2: Circle CenterX=83.33 CenterY=0 CenterZ=0 NormalX=0 NormalY=0 NormalZ=1 AngleXU=0 Radius=25
    g3: LineSegment StartX=-160 StartY=-37.5 StartZ=0 EndX=-164 EndY=-37.5 EndZ=0
    g4: LineSegment StartX=-164 StartY=-37.5 StartZ=0 EndX=-164 EndY=-22.5 EndZ=0
    g5: LineSegment StartX=-164 StartY=-22.5 StartZ=0 EndX=-160 EndY=-22.5 EndZ=0
    g6: LineSegment StartX=-160 StartY=-22.5 StartZ=0 EndX=-160 EndY=-37.5 EndZ=0
    g7: LineSegment StartX=-160 StartY=-7.5 StartZ=0 EndX=-164 EndY=-7.5 EndZ=0
    g8: LineSegment StartX=-164 StartY=-7.5 StartZ=0 EndX=-164 EndY=7.5 EndZ=0
    g9: LineSegment StartX=-164 StartY=7.5 StartZ=0 EndX=-160 EndY=7.5 EndZ=0
    g10: LineSegment StartX=-160 StartY=7.5 StartZ=0 EndX=-160 EndY=-7.5 EndZ=0
    g11: LineSegment StartX=-160 StartY=22.5 StartZ=0 EndX=-164 EndY=22.5 EndZ=0
    g12: LineSegment StartX=-164 StartY=22.5 StartZ=0 EndX=-164 EndY=37.5 EndZ=0
    g13: LineSegment StartX=-164 StartY=37.5 StartZ=0 EndX=-160 EndY=37.5 EndZ=0
    g14: LineSegment StartX=-160 StartY=37.5 StartZ=0 EndX=-160 EndY=22.5 EndZ=0
    g15: LineSegment StartX=160 StartY=-37.5 StartZ=0 EndX=164 EndY=-37.5 EndZ=0
    g16: LineSegment StartX=164 StartY=-37.5 StartZ=0 EndX=164 EndY=-22.5 EndZ=0
    g17: LineSegment StartX=164 StartY=-22.5 StartZ=0 EndX=160 EndY=-22.5 EndZ=0
    g18: LineSegment StartX=160 StartY=-22.5 StartZ=0 EndX=160 EndY=-37.5 EndZ=0
    g19: LineSegment StartX=160 StartY=-7.5 StartZ=0 EndX=164 EndY=-7.5 EndZ=0
    g20: LineSegment StartX=164 StartY=-7.5 StartZ=0 EndX=164 EndY=7.5 EndZ=0
    g21: LineSegment StartX=164 StartY=7.5 StartZ=0 EndX=160 EndY=7.5 EndZ=0
    g22: LineSegment StartX=160 StartY=7.5 StartZ=0 EndX=160 EndY=-7.5 EndZ=0
    g23: LineSegment StartX=160 StartY=22.5 StartZ=0 EndX=164 EndY=22.5 EndZ=0
    g24: LineSegment StartX=164 StartY=22.5 StartZ=0 EndX=164 EndY=37.5 EndZ=0
    g25: LineSegment StartX=164 StartY=37.5 StartZ=0 EndX=160 EndY=37.5 EndZ=0
    g26: LineSegment StartX=160 StartY=37.5 StartZ=0 EndX=160 EndY=22.5 EndZ=0
    g27: LineSegment StartX=-156.55 StartY=-41 StartZ=0 EndX=-141.64 EndY=-41 EndZ=0
    g28: LineSegment StartX=-141.64 StartY=-41 StartZ=0 EndX=-141.64 EndY=-45 EndZ=0
    g29: LineSegment StartX=-141.64 StartY=-45 StartZ=0 EndX=-156.55 EndY=-45 EndZ=0
    g30: LineSegment StartX=-156.55 StartY=-45 StartZ=0 EndX=-156.55 EndY=-41 EndZ=0
    g31: LineSegment StartX=-126.73 StartY=-41 StartZ=0 EndX=-111.82 EndY=-41 EndZ=0
    g32: LineSegment StartX=-111.82 StartY=-41 StartZ=0 EndX=-111.82 EndY=-45 EndZ=0
    g33: LineSegment StartX=-111.82 StartY=-45 StartZ=0 EndX=-126.73 EndY=-45 EndZ=0
    g34: LineSegment StartX=-126.73 StartY=-45 StartZ=0 EndX=-126.73 EndY=-41 EndZ=0
    g35: LineSegment StartX=-96.91 StartY=-41 StartZ=0 EndX=-82 EndY=-41 EndZ=0
    g36: LineSegment StartX=-82 StartY=-41 StartZ=0 EndX=-82 EndY=-45 EndZ=0
    g37: LineSegment StartX=-82 StartY=-45 StartZ=0 EndX=-96.91 EndY=-45 EndZ=0
    g38: LineSegment StartX=-96.91 StartY=-45 StartZ=0 EndX=-96.91 EndY=-41 EndZ=0
    g39: LineSegment StartX=-67.09 StartY=-41 StartZ=0 EndX=-52.18 EndY=-41 EndZ=0
    g40: LineSegment StartX=-52.18 StartY=-41 StartZ=0 EndX=-52.18 EndY=-45 EndZ=0
    g41: LineSegment StartX=-52.18 StartY=-45 StartZ=0 EndX=-67.09 EndY=-45 EndZ=0
    g42: LineSegment StartX=-67.09 StartY=-45 StartZ=0 EndX=-67.09 EndY=-41 EndZ=0
    g43: LineSegment StartX=-37.27 StartY=-41 StartZ=0 EndX=-22.36 EndY=-41 EndZ=0
    g44: LineSegment StartX=-22.36 StartY=-41 StartZ=0 EndX=-22.36 EndY=-45 EndZ=0
    g45: LineSegment StartX=-22.36 StartY=-45 StartZ=0 EndX=-37.27 EndY=-45 EndZ=0
    g46: LineSegment StartX=-37.27 StartY=-45 StartZ=0 EndX=-37.27 EndY=-41 EndZ=0
    g47: LineSegment StartX=-7.45 StartY=-41 StartZ=0 EndX=7.46 EndY=-41 EndZ=0
    g48: LineSegment StartX=7.46 StartY=-41 StartZ=0 EndX=7.46 EndY=-45 EndZ=0
    g49: LineSegment StartX=7.46 StartY=-45 StartZ=0 EndX=-7.45 EndY=-45 EndZ=0
    g50: LineSegment StartX=-7.45 StartY=-45 StartZ=0 EndX=-7.45 EndY=-41 EndZ=0
    g51: LineSegment StartX=22.37 StartY=-41 StartZ=0 EndX=37.28 EndY=-41 EndZ=0
    g52: LineSegment StartX=37.28 StartY=-41 StartZ=0 EndX=37.28 EndY=-45 EndZ=0
    g53: LineSegment StartX=37.28 StartY=-45 StartZ=0 EndX=22.37 EndY=-45 EndZ=0
    g54: LineSegment StartX=22.37 StartY=-45 StartZ=0 EndX=22.37 EndY=-41 EndZ=0
    g55: LineSegment StartX=52.19 StartY=-41 StartZ=0 EndX=67.1 EndY=-41 EndZ=0
    g56: LineSegment StartX=67.1 StartY=-41 StartZ=0 EndX=67.1 EndY=-45 EndZ=0
    g57: LineSegment StartX=67.1 StartY=-45 StartZ=0 EndX=52.19 EndY=-45 EndZ=0
    g58: LineSegment StartX=52.19 StartY=-45 StartZ=0 EndX=52.19 EndY=-41 EndZ=0
    g59: LineSegment StartX=82.01 StartY=-41 StartZ=0 EndX=96.92 EndY=-41 EndZ=0
    g60: LineSegment StartX=96.92 StartY=-41 StartZ=0 EndX=96.92 EndY=-45 EndZ=0
    g61: LineSegment StartX=96.92 StartY=-45 StartZ=0 EndX=82.01 EndY=-45 EndZ=0
    g62: LineSegment StartX=82.01 StartY=-45 StartZ=0 EndX=82.01 EndY=-41 EndZ=0
    g63: LineSegment StartX=111.83 StartY=-41 StartZ=0 EndX=126.74 EndY=-41 EndZ=0
    g64: LineSegment StartX=126.74 StartY=-41 StartZ=0 EndX=126.74 EndY=-45 EndZ=0
    g65: LineSegment StartX=126.74 StartY=-45 StartZ=0 EndX=111.83 EndY=-45 EndZ=0
    g66: LineSegment StartX=111.83 StartY=-45 StartZ=0 EndX=111.83 EndY=-41 EndZ=0
    g67: LineSegment StartX=141.65 StartY=-41 StartZ=0 EndX=156.56 EndY=-41 EndZ=0
    g68: LineSegment StartX=156.56 StartY=-41 StartZ=0 EndX=156.56 EndY=-45 EndZ=0
    g69: LineSegment StartX=156.56 StartY=-45 StartZ=0 EndX=141.65 EndY=-45 EndZ=0
    g70: LineSegment StartX=141.65 StartY=-45 StartZ=0 EndX=141.65 EndY=-41 EndZ=0
  constraints (212):
    c: PointOnObject(g0,g-1)
    c: Coincident(g1,g-1)
    c: PointOnObject(g2,g-1)
    c: Radius(g1) = 25
    c: Radius(g0) = 25
    c: Radius(g2) = 25
    c: DistanceX(g0,g1) = 83.33
    c: DistanceX(g1,g2) = 83.33
    c: Coincident(g3,g4)
    c: Coincident(g4,g5)
    c: Coincident(g5,g6)
    c: Coincident(g6,g3)
    c: Horizontal(g3)
    c: Horizontal(g5)
    c: Vertical(g4)
    c: Vertical(g6)
    c: Coincident(g7,g8)
    c: Coincident(g8,g9)
    c: Coincident(g9,g10)
    c: Coincident(g10,g7)
    c: Horizontal(g7)
    c: Horizontal(g9)
    c: Vertical(g8)
    c: Vertical(g10)
    c: Coincident(g11,g12)
    c: Coincident(g12,g13)
    c: Coincident(g13,g14)
    c: Coincident(g14,g11)
    c: Horizontal(g11)
    c: Horizontal(g13)
    c: Vertical(g12)
    c: Vertical(g14)
    c: Vertical(g3,g-3)
    c: Vertical(g7,g4)
    c: Vertical(g11,g8)
    c: Vertical(g5,g7)
    c: Vertical(g9,g11)
    c: DistanceY(g-3,g3) = 7.5
    c: DistanceY(g3,g4) = 15
    c: Equal(g4,g8)
    c: Equal(g8,g12)
    c: DistanceY(g4,g7) = 15
    c: DistanceY(g8,g11) = 15
    c: Coincident(g15,g16)
    c: Coincident(g16,g17)
    c: Coincident(g17,g18)
    c: Coincident(g18,g15)
    c: Horizontal(g15)
    c: Horizontal(g17)
    c: Vertical(g16)
    c: Vertical(g18)
    c: Coincident(g19,g20)
    c: Coincident(g20,g21)
    c: Coincident(g21,g22)
    c: Coincident(g22,g19)
    c: Horizontal(g19)
    c: Horizontal(g21)
    c: Vertical(g20)
    c: Vertical(g22)
    c: Coincident(g23,g24)
    c: Coincident(g24,g25)
    c: Coincident(g25,g26)
    c: Coincident(g26,g23)
    c: Horizontal(g23)
    c: Horizontal(g25)
    c: Vertical(g24)
    c: Vertical(g26)
    c: Vertical(g19,g16)
    c: Vertical(g23,g20)
    c: Vertical(g17,g19)
    c: Vertical(g21,g23)
    c: DistanceY(g15,g16) = 15
    c: Equal(g16,g20)
    c: Equal(g20,g24)
    c: DistanceY(g16,g19) = 15
    c: DistanceY(g20,g23) = 15
    c: Vertical(g15,g-4)
    c: DistanceY(g-4,g15) = 7.5
    c: DistanceX(g15,g15) = 4
    c: DistanceX(g3,g3) = 4
    c: Coincident(g27,g28)
    c: Coincident(g28,g29)
    c: Coincident(g29,g30)
    c: Coincident(g30,g27)
    c: Horizontal(g27)
    c: Horizontal(g29)
    c: Vertical(g28)
    c: Vertical(g30)
    c: Coincident(g31,g32)
    c: Coincident(g32,g33)
    c: Coincident(g33,g34)
    c: Coincident(g34,g31)
    c: Horizontal(g31)
    c: Horizontal(g33)
    c: Vertical(g32)
    c: Vertical(g34)
    c: Coincident(g35,g36)
    c: Coincident(g36,g37)
    c: Coincident(g37,g38)
    c: Coincident(g38,g35)
    c: Horizontal(g35)
    c: Horizontal(g37)
    c: Vertical(g36)
    c: Vertical(g38)
    c: Coincident(g39,g40)
    c: Coincident(g40,g41)
    c: Coincident(g41,g42)
    c: Coincident(g42,g39)
    c: Horizontal(g39)
    c: Horizontal(g41)
    c: Vertical(g40)
    c: Vertical(g42)
    c: Coincident(g43,g44)
    c: Coincident(g44,g45)
    c: Coincident(g45,g46)
    c: Coincident(g46,g43)
    c: Horizontal(g43)
    c: Horizontal(g45)
    c: Vertical(g44)
    c: Vertical(g46)
    c: Coincident(g47,g48)
    c: Coincident(g48,g49)
    c: Coincident(g49,g50)
    c: Coincident(g50,g47)
    c: Horizontal(g47)
    c: Horizontal(g49)
    c: Vertical(g48)
    c: Vertical(g50)
    c: Coincident(g51,g52)
    c: Coincident(g52,g53)
    c: Coincident(g53,g54)
    c: Coincident(g54,g51)
    c: Horizontal(g51)
    c: Horizontal(g53)
    c: Vertical(g52)
    c: Vertical(g54)
    c: Coincident(g55,g56)
    c: Coincident(g56,g57)
    c: Coincident(g57,g58)
    c: Coincident(g58,g55)
    c: Horizontal(g55)
    c: Horizontal(g57)
    c: Vertical(g56)
    c: Vertical(g58)
    c: Coincident(g59,g60)
    c: Coincident(g60,g61)
    c: Coincident(g61,g62)
    c: Coincident(g62,g59)
    c: Horizontal(g59)
    c: Horizontal(g61)
    c: Vertical(g60)
    c: Vertical(g62)
    c: Coincident(g63,g64)
    c: Coincident(g64,g65)
    c: Coincident(g65,g66)
    c: Coincident(g66,g63)
    c: Horizontal(g63)
    c: Horizontal(g65)
    c: Vertical(g64)
    c: Vertical(g66)
    c: Coincident(g67,g68)
    c: Coincident(g68,g69)
    c: Coincident(g69,g70)
    c: Coincident(g70,g67)
    c: Horizontal(g67)
    c: Horizontal(g69)
    c: Vertical(g68)
    c: Vertical(g70)
    c: Horizontal(g27,g31)
    c: Horizontal(g31,g35)
    c: Horizontal(g35,g39)
    c: Horizontal(g39,g43)
    c: Horizontal(g43,g47)
    c: Horizontal(g47,g51)
    c: Horizontal(g51,g55)
    c: Horizontal(g55,g59)
    c: Horizontal(g59,g63)
    c: Horizontal(g63,g67)
    c: Horizontal(g28,g32)
    c: Horizontal(g32,g36)
    c: Horizontal(g36,g40)
    c: Horizontal(g40,g44)
    c: Horizontal(g44,g48)
    c: Horizontal(g48,g52)
    c: Horizontal(g52,g56)
    c: Horizontal(g56,g60)
    c: Horizontal(g60,g64)
    c: Horizontal(g64,g68)
    c: Horizontal(g-3,g29)
    c: DistanceX(g29,g28) = 14.91
    c: Equal(g29,g69)
    c: Equal(g69,g65)
    c: Equal(g61,g65)
    c: Equal(g61,g57)
    c: Equal(g57,g53)
    c: Equal(g53,g49)
    c: Equal(g49,g45)
    c: Equal(g45,g41)
    c: Equal(g37,g41)
    c: Equal(g33,g37)
    c: DistanceX(g-3,g29) = 7.45
    c: DistanceX(g28,g33) = 14.91
    c: DistanceX(g32,g37) = 14.91
    c: DistanceX(g36,g41) = 14.91
    c: DistanceX(g40,g45) = 14.91
    c: DistanceX(g44,g49) = 14.91
    c: DistanceX(g48,g53) = 14.91
    c: DistanceX(g52,g57) = 14.91
    c: DistanceX(g56,g61) = 14.91
    c: DistanceX(g60,g65) = 14.91
    c: DistanceX(g64,g69) = 14.91
    c: DistanceY(g-3,g27) = 4
FEATURE [PartDesign::Pocket] Pocket025
  BaseFeature = -> Pad029
  Length = 4
  Length2 = 100
  Placement = pos=(0,0,0) rot=(1,0,0;1.5708rad)
  Profile = -> Sketch059
  Type = 0
FEATURE [PartDesign::Body] Body028  label="UtrustningsBoxBakkant-1"
  Group = -> [Sketch058,Pad029,Sketch059,Pocket025]
  Origin = -> Origin028
  Placement = pos=(-500,-302,0) rot=(0,0,1;0rad)
  Tip = -> Pocket025
FEATURE [Sketcher::SketchObject] Sketch060
  FullyConstrained = true
  MapMode = 5
  Support = -> [XY_Plane029]
  sketch-geometry (4):
    g0: LineSegment StartX=164 StartY=-100 StartZ=0 EndX=-164 EndY=-100 EndZ=0
    g1: LineSegment StartX=-164 StartY=-100 StartZ=0 EndX=-164 EndY=100 EndZ=0
    g2: LineSegment StartX=-164 StartY=100 StartZ=0 EndX=164 EndY=100 EndZ=0
    g3: LineSegment StartX=164 StartY=100 StartZ=0 EndX=164 EndY=-100 EndZ=0
  constraints (11):
    c: Coincident(g0,g1)
    c: Coincident(g1,g2)
    c: Coincident(g2,g3)
    c: Coincident(g3,g0)
    c: Horizontal(g0)
    c: Horizontal(g2)
    c: Vertical(g1)
    c: Vertical(g3)
    c: Symmetric(g1,g0,g-1)
    c: DistanceX(g1,g2) = 328
    c: DistanceY(g0,g1) = 200
FEATURE [PartDesign::Pad] Pad030
  Direction = (1,1,1)
  Length = 4
  Length2 = 100
  Profile = -> Sketch060
  Type = 0
FEATURE [Sketcher::SketchObject] Sketch061
  ExternalGeometry = -> [Pad030]
  FullyConstrained = true
  MapMode = 5
  Placement = pos=(0,0,4) rot=(0,0,1;0rad)
  Support = -> [Pad030]
  sketch-geometry (124):
    g0: LineSegment StartX=-164 StartY=100 StartZ=0 EndX=-156.55 EndY=100 EndZ=0
    g1: LineSegment StartX=-156.55 StartY=100 StartZ=0 EndX=-156.55 EndY=96 EndZ=0
    g2: LineSegment StartX=-156.55 StartY=96 StartZ=0 EndX=-164 EndY=96 EndZ=0
    g3: LineSegment StartX=-164 StartY=96 StartZ=0 EndX=-164 EndY=100 EndZ=0
    g4: LineSegment StartX=-141.64 StartY=100 StartZ=0 EndX=-126.73 EndY=100 EndZ=0
    g5: LineSegment StartX=-126.73 StartY=100 StartZ=0 EndX=-126.73 EndY=96 EndZ=0
    g6: LineSegment StartX=-126.73 StartY=96 StartZ=0 EndX=-141.64 EndY=96 EndZ=0
    g7: LineSegment StartX=-141.64 StartY=96 StartZ=0 EndX=-141.64 EndY=100 EndZ=0
    g8: LineSegment StartX=-111.82 StartY=100 StartZ=0 EndX=-96.91 EndY=100 EndZ=0
    g9: LineSegment StartX=-96.91 StartY=100 StartZ=0 EndX=-96.91 EndY=96 EndZ=0
    g10: LineSegment StartX=-96.91 StartY=96 StartZ=0 EndX=-111.82 EndY=96 EndZ=0
    g11: LineSegment StartX=-111.82 StartY=96 StartZ=0 EndX=-111.82 EndY=100 EndZ=0
    g12: LineSegment StartX=-82 StartY=100 StartZ=0 EndX=-67.09 EndY=100 EndZ=0
    g13: LineSegment StartX=-67.09 StartY=100 StartZ=0 EndX=-67.09 EndY=96 EndZ=0
    g14: LineSegment StartX=-67.09 StartY=96 StartZ=0 EndX=-82 EndY=96 EndZ=0
    g15: LineSegment StartX=-82 StartY=96 StartZ=0 EndX=-82 EndY=100 EndZ=0
    g16: LineSegment StartX=-52.18 StartY=100 StartZ=0 EndX=-37.27 EndY=100 EndZ=0
    g17: LineSegment StartX=-37.27 StartY=100 StartZ=0 EndX=-37.27 EndY=96 EndZ=0
    g18: LineSegment StartX=-37.27 StartY=96 StartZ=0 EndX=-52.18 EndY=96 EndZ=0
    g19: LineSegment StartX=-52.18 StartY=96 StartZ=0 EndX=-52.18 EndY=100 EndZ=0
    g20: LineSegment StartX=-22.36 StartY=100 StartZ=0 EndX=-7.45 EndY=100 EndZ=0
    g21: LineSegment StartX=-7.45 StartY=100 StartZ=0 EndX=-7.45 EndY=96 EndZ=0
    g22: LineSegment StartX=-7.45 StartY=96 StartZ=0 EndX=-22.36 EndY=96 EndZ=0
    g23: LineSegment StartX=-22.36 StartY=96 StartZ=0 EndX=-22.36 EndY=100 EndZ=0
    g24: LineSegment StartX=7.46 StartY=100 StartZ=0 EndX=22.37 EndY=100 EndZ=0
    g25: LineSegment StartX=22.37 StartY=100 StartZ=0 EndX=22.37 EndY=96 EndZ=0
    g26: LineSegment StartX=22.37 StartY=96 StartZ=0 EndX=7.46 EndY=96 EndZ=0
    g27: LineSegment StartX=7.46 StartY=96 StartZ=0 EndX=7.46 EndY=100 EndZ=0
    g28: LineSegment StartX=37.28 StartY=100 StartZ=0 EndX=52.19 EndY=100 EndZ=0
    g29: LineSegment StartX=52.19 StartY=100 StartZ=0 EndX=52.19 EndY=96 EndZ=0
    g30: LineSegment StartX=52.19 StartY=96 StartZ=0 EndX=37.28 EndY=96 EndZ=0
    g31: LineSegment StartX=37.28 StartY=96 StartZ=0 EndX=37.28 EndY=100 EndZ=0
    g32: LineSegment StartX=67.1 StartY=100 StartZ=0 EndX=82.01 EndY=100 EndZ=0
    g33: LineSegment StartX=82.01 StartY=100 StartZ=0 EndX=82.01 EndY=96 EndZ=0
    g34: LineSegment StartX=82.01 StartY=96 StartZ=0 EndX=67.1 EndY=96 EndZ=0
    g35: LineSegment StartX=67.1 StartY=96 StartZ=0 EndX=67.1 EndY=100 EndZ=0
    g36: LineSegment StartX=96.92 StartY=100 StartZ=0 EndX=111.83 EndY=100 EndZ=0
    g37: LineSegment StartX=111.83 StartY=100 StartZ=0 EndX=111.83 EndY=96 EndZ=0
    g38: LineSegment StartX=111.83 StartY=96 StartZ=0 EndX=96.92 EndY=96 EndZ=0
    g39: LineSegment StartX=96.92 StartY=96 StartZ=0 EndX=96.92 EndY=100 EndZ=0
    g40: LineSegment StartX=126.74 StartY=100 StartZ=0 EndX=141.65 EndY=100 EndZ=0
    g41: LineSegment StartX=141.65 StartY=100 StartZ=0 EndX=141.65 EndY=96 EndZ=0
    g42: LineSegment StartX=141.65 StartY=96 StartZ=0 EndX=126.74 EndY=96 EndZ=0
    g43: LineSegment StartX=126.74 StartY=96 StartZ=0 EndX=126.74 EndY=100 EndZ=0
    g44: LineSegment StartX=156.56 StartY=100 StartZ=0 EndX=164.01 EndY=100 EndZ=0
    g45: LineSegment StartX=164.01 StartY=100 StartZ=0 EndX=164.01 EndY=96 EndZ=0
    g46: LineSegment StartX=164.01 StartY=96 StartZ=0 EndX=156.56 EndY=96 EndZ=0
    g47: LineSegment StartX=156.56 StartY=96 StartZ=0 EndX=156.56 EndY=100 EndZ=0
    g48: LineSegment StartX=-164 StartY=89 StartZ=0 EndX=-160 EndY=89 EndZ=0
    g49: LineSegment StartX=-160 StartY=89 StartZ=0 EndX=-160 EndY=75 EndZ=0
    g50: LineSegment StartX=-160 StartY=75 StartZ=0 EndX=-164 EndY=75 EndZ=0
    g51: LineSegment StartX=-164 StartY=75 StartZ=0 EndX=-164 EndY=89 EndZ=0
    g52: LineSegment StartX=-164 StartY=61 StartZ=0 EndX=-160 EndY=61 EndZ=0
    g53: LineSegment StartX=-160 StartY=61 StartZ=0 EndX=-160 EndY=47 EndZ=0
    g54: LineSegment StartX=-160 StartY=47 StartZ=0 EndX=-164 EndY=47 EndZ=0
    g55: LineSegment StartX=-164 StartY=47 StartZ=0 EndX=-164 EndY=61 EndZ=0
    g56: LineSegment StartX=-164 StartY=33 StartZ=0 EndX=-160 EndY=33 EndZ=0
    g57: LineSegment StartX=-160 StartY=33 StartZ=0 EndX=-160 EndY=19 EndZ=0
    g58: LineSegment StartX=-160 StartY=19 StartZ=0 EndX=-164 EndY=19 EndZ=0
    g59: LineSegment StartX=-164 StartY=19 StartZ=0 EndX=-164 EndY=33 EndZ=0
    g60: LineSegment StartX=-164 StartY=5 StartZ=0 EndX=-160 EndY=5 EndZ=0
    g61: LineSegment StartX=-160 StartY=5 StartZ=0 EndX=-160 EndY=-9 EndZ=0
    g62: LineSegment StartX=-160 StartY=-9 StartZ=0 EndX=-164 EndY=-9 EndZ=0
    g63: LineSegment StartX=-164 StartY=-9 StartZ=0 EndX=-164 EndY=5 EndZ=0
    g64: LineSegment StartX=-164 StartY=-23 StartZ=0 EndX=-160 EndY=-23 EndZ=0
    g65: LineSegment StartX=-160 StartY=-23 StartZ=0 EndX=-160 EndY=-37 EndZ=0
    g66: LineSegment StartX=-160 StartY=-37 StartZ=0 EndX=-164 EndY=-37 EndZ=0
    g67: LineSegment StartX=-164 StartY=-37 StartZ=0 EndX=-164 EndY=-23 EndZ=0
    g68: LineSegment StartX=-164 StartY=-51 StartZ=0 EndX=-160 EndY=-51 EndZ=0
    g69: LineSegment StartX=-160 StartY=-51 StartZ=0 EndX=-160 EndY=-65 EndZ=0
    g70: LineSegment StartX=-160 StartY=-65 StartZ=0 EndX=-164 EndY=-65 EndZ=0
    g71: LineSegment StartX=-164 StartY=-65 StartZ=0 EndX=-164 EndY=-51 EndZ=0
    g72: LineSegment StartX=-164 StartY=-79 StartZ=0 EndX=-160 EndY=-79 EndZ=0
    g73: LineSegment StartX=-160 StartY=-79 StartZ=0 EndX=-160 EndY=-93 EndZ=0
    g74: LineSegment StartX=-160 StartY=-93 StartZ=0 EndX=-164 EndY=-93 EndZ=0
    g75: LineSegment StartX=-164 StartY=-93 StartZ=0 EndX=-164 EndY=-79 EndZ=0
    g76: LineSegment StartX=160 StartY=89 StartZ=0 EndX=164 EndY=89 EndZ=0
    g77: LineSegment StartX=164 StartY=89 StartZ=0 EndX=164 EndY=75 EndZ=0
    g78: LineSegment StartX=164 StartY=75 StartZ=0 EndX=160 EndY=75 EndZ=0
    g79: LineSegment StartX=160 StartY=75 StartZ=0 EndX=160 EndY=89 EndZ=0
    g80: LineSegment StartX=160 StartY=61 StartZ=0 EndX=164 EndY=61 EndZ=0
    g81: LineSegment StartX=164 StartY=61 StartZ=0 EndX=164 EndY=47 EndZ=0
    g82: LineSegment StartX=164 StartY=47 StartZ=0 EndX=160 EndY=47 EndZ=0
    g83: LineSegment StartX=160 StartY=47 StartZ=0 EndX=160 EndY=61 EndZ=0
    g84: LineSegment StartX=160 StartY=33 StartZ=0 EndX=164 EndY=33 EndZ=0
    g85: LineSegment StartX=164 StartY=33 StartZ=0 EndX=164 EndY=19 EndZ=0
    g86: LineSegment StartX=164 StartY=19 StartZ=0 EndX=160 EndY=19 EndZ=0
    g87: LineSegment StartX=160 StartY=19 StartZ=0 EndX=160 EndY=33 EndZ=0
    g88: LineSegment StartX=160 StartY=5 StartZ=0 EndX=164 EndY=5 EndZ=0
    g89: LineSegment StartX=164 StartY=5 StartZ=0 EndX=164 EndY=-9 EndZ=0
    g90: LineSegment StartX=164 StartY=-9 StartZ=0 EndX=160 EndY=-9 EndZ=0
    g91: LineSegment StartX=160 StartY=-9 StartZ=0 EndX=160 EndY=5 EndZ=0
    g92: LineSegment StartX=160 StartY=-23 StartZ=0 EndX=164 EndY=-23 EndZ=0
    g93: LineSegment StartX=164 StartY=-23 StartZ=0 EndX=164 EndY=-37 EndZ=0
    g94: LineSegment StartX=164 StartY=-37 StartZ=0 EndX=160 EndY=-37 EndZ=0
    g95: LineSegment StartX=160 StartY=-37 StartZ=0 EndX=160 EndY=-23 EndZ=0
    g96: LineSegment StartX=160 StartY=-51 StartZ=0 EndX=164 EndY=-51 EndZ=0
    g97: LineSegment StartX=164 StartY=-51 StartZ=0 EndX=164 EndY=-65 EndZ=0
    g98: LineSegment StartX=164 StartY=-65 StartZ=0 EndX=160 EndY=-65 EndZ=0
    g99: LineSegment StartX=160 StartY=-65 StartZ=0 EndX=160 EndY=-51 EndZ=0
    g100: LineSegment StartX=160 StartY=-79 StartZ=0 EndX=164 EndY=-79 EndZ=0
    g101: LineSegment StartX=164 StartY=-79 StartZ=0 EndX=164 EndY=-93 EndZ=0
    g102: LineSegment StartX=164 StartY=-93 StartZ=0 EndX=160 EndY=-93 EndZ=0
    g103: LineSegment StartX=160 StartY=-93 StartZ=0 EndX=160 EndY=-79 EndZ=0
    g104: Circle CenterX=0 CenterY=75 CenterZ=0 NormalX=0 NormalY=0 NormalZ=1 AngleXU=0 Radius=10
    g105: Circle CenterX=0 CenterY=25 CenterZ=0 NormalX=0 NormalY=0 NormalZ=1 AngleXU=0 Radius=10
    g106: Circle CenterX=0 CenterY=-25 CenterZ=0 NormalX=0 NormalY=0 NormalZ=1 AngleXU=0 Radius=10
    g107: Circle CenterX=0 CenterY=-75 CenterZ=0 NormalX=0 NormalY=0 NormalZ=1 AngleXU=0 Radius=10
    g108: Circle CenterX=54.7 CenterY=75 CenterZ=0 NormalX=0 NormalY=0 NormalZ=1 AngleXU=0 Radius=10
    g109: Circle CenterX=54.7 CenterY=25 CenterZ=0 NormalX=0 NormalY=0 NormalZ=1 AngleXU=0 Radius=10
    g110: Circle CenterX=54.7 CenterY=-25 CenterZ=0 NormalX=0 NormalY=0 NormalZ=1 AngleXU=0 Radius=10
    g111: Circle CenterX=54.7 CenterY=-75 CenterZ=0 NormalX=0 NormalY=0 NormalZ=1 AngleXU=0 Radius=10
    g112: Circle CenterX=109.4 CenterY=75 CenterZ=0 NormalX=0 NormalY=0 NormalZ=1 AngleXU=0 Radius=10
    g113: Circle CenterX=109.4 CenterY=25 CenterZ=0 NormalX=0 NormalY=0 NormalZ=1 AngleXU=0 Radius=10
    g114: Circle CenterX=109.4 CenterY=-25 CenterZ=0 NormalX=0 NormalY=0 NormalZ=1 AngleXU=0 Radius=10
    g115: Circle CenterX=109.4 CenterY=-75 CenterZ=0 NormalX=0 NormalY=0 NormalZ=1 AngleXU=0 Radius=10
    g116: Circle CenterX=-109.4 CenterY=75 CenterZ=0 NormalX=0 NormalY=0 NormalZ=1 AngleXU=0 Radius=10
    g117: Circle CenterX=-109.4 CenterY=25 CenterZ=0 NormalX=0 NormalY=0 NormalZ=1 AngleXU=0 Radius=10
    g118: Circle CenterX=-109.4 CenterY=-25 CenterZ=0 NormalX=0 NormalY=0 NormalZ=1 AngleXU=0 Radius=10
    g119: Circle CenterX=-109.4 CenterY=-75 CenterZ=0 NormalX=0 NormalY=0 NormalZ=1 AngleXU=0 Radius=10
    g120: Circle CenterX=-54.7 CenterY=75 CenterZ=0 NormalX=0 NormalY=0 NormalZ=1 AngleXU=0 Radius=10
    g121: Circle CenterX=-54.7 CenterY=25 CenterZ=0 NormalX=0 NormalY=0 NormalZ=1 AngleXU=0 Radius=10
    g122: Circle CenterX=-54.7 CenterY=-25 CenterZ=0 NormalX=0 NormalY=0 NormalZ=1 AngleXU=0 Radius=10
    g123: Circle CenterX=-54.7 CenterY=-75 CenterZ=0 NormalX=0 NormalY=0 NormalZ=1 AngleXU=0 Radius=10
  constraints (372):
    c: Coincident(g0,g1)
    c: Coincident(g1,g2)
    c: Coincident(g2,g3)
    c: Coincident(g3,g0)
    c: Horizontal(g0)
    c: Horizontal(g2)
    c: Vertical(g1)
    c: Vertical(g3)
    c: Coincident(g4,g5)
    c: Coincident(g5,g6)
    c: Coincident(g6,g7)
    c: Coincident(g7,g4)
    c: Horizontal(g4)
    c: Horizontal(g6)
    c: Vertical(g5)
    c: Vertical(g7)
    c: Coincident(g8,g9)
    c: Coincident(g9,g10)
    c: Coincident(g10,g11)
    c: Coincident(g11,g8)
    c: Horizontal(g8)
    c: Horizontal(g10)
    c: Vertical(g9)
    c: Vertical(g11)
    c: Coincident(g12,g13)
    c: Coincident(g13,g14)
    c: Coincident(g14,g15)
    c: Coincident(g15,g12)
    c: Horizontal(g12)
    c: Horizontal(g14)
    c: Vertical(g13)
    c: Vertical(g15)
    c: Coincident(g16,g17)
    c: Coincident(g17,g18)
    c: Coincident(g18,g19)
    c: Coincident(g19,g16)
    c: Horizontal(g16)
    c: Horizontal(g18)
    c: Vertical(g17)
    c: Vertical(g19)
    c: Coincident(g20,g21)
    c: Coincident(g21,g22)
    c: Coincident(g22,g23)
    c: Coincident(g23,g20)
    c: Horizontal(g20)
    c: Horizontal(g22)
    c: Vertical(g21)
    c: Vertical(g23)
    c: Horizontal(g0,g4)
    c: Horizontal(g4,g8)
    c: Horizontal(g8,g12)
    c: Horizontal(g12,g16)
    c: Horizontal(g16,g20)
    c: Horizontal(g1,g5)
    c: Horizontal(g5,g9)
    c: Horizontal(g9,g13)
    c: Horizontal(g13,g17)
    c: Horizontal(g17,g21)
    c: PointOnObject(g0,g-4)
    c: PointOnObject(g0,g-5)
    c: DistanceX(g0,g0) = 7.45
    c: DistanceX(g0,g4) = 14.91
    c: DistanceX(g4,g4) = 14.91
    c: Equal(g4,g8)
    c: Equal(g8,g12)
    c: Equal(g12,g16)
    c: Equal(g20,g16)
    c: DistanceX(g16,g20) = 14.91
    c: DistanceX(g12,g16) = 14.91
    c: DistanceX(g4,g8) = 14.91
    c: DistanceX(g8,g12) = 14.91
    c: Coincident(g24,g25)
    c: Coincident(g25,g26)
    c: Coincident(g26,g27)
    c: Coincident(g27,g24)
    c: Horizontal(g24)
    c: Horizontal(g26)
    c: Vertical(g25)
    c: Vertical(g27)
    c: Coincident(g28,g29)
    c: Coincident(g29,g30)
    c: Coincident(g30,g31)
    c: Coincident(g31,g28)
    c: Horizontal(g28)
    c: Horizontal(g30)
    c: Vertical(g29)
    c: Vertical(g31)
    c: Coincident(g32,g33)
    c: Coincident(g33,g34)
    c: Coincident(g34,g35)
    c: Coincident(g35,g32)
    c: Horizontal(g32)
    c: Horizontal(g34)
    c: Vertical(g33)
    c: Vertical(g35)
    c: Coincident(g36,g37)
    c: Coincident(g37,g38)
    c: Coincident(g38,g39)
    c: Coincident(g39,g36)
    c: Horizontal(g36)
    c: Horizontal(g38)
    c: Vertical(g37)
    c: Vertical(g39)
    c: Horizontal(g24,g28)
    c: Horizontal(g28,g32)
    c: Horizontal(g32,g36)
    c: Horizontal(g25,g29)
    c: Horizontal(g29,g33)
    c: Horizontal(g33,g37)
    c: Equal(g24,g28)
    c: Equal(g28,g32)
    c: Equal(g36,g32)
    c: DistanceX(g32,g36) = 14.91
    c: DistanceX(g28,g32) = 14.91
    c: DistanceX(g24,g28) = 14.91
    c: DistanceX(g20,g24) = 14.91
    c: Horizontal(g24,g20)
    c: Horizontal(g21,g26)
    c: Equal(g22,g26)
    c: Coincident(g40,g41)
    c: Coincident(g41,g42)
    c: Coincident(g42,g43)
    c: Coincident(g43,g40)
    c: Horizontal(g40)
    c: Horizontal(g42)
    c: Vertical(g41)
    c: Vertical(g43)
    c: Horizontal(g42,g37)
    c: Horizontal(g40,g36)
    c: Equal(g36,g40)
    c: DistanceX(g36,g40) = 14.91
    c: Coincident(g44,g45)
    c: Coincident(g45,g46)
    c: Coincident(g46,g47)
    c: Coincident(g47,g44)
    c: Horizontal(g44)
    c: Horizontal(g46)
    c: Vertical(g45)
    c: Vertical(g47)
    c: Horizontal(g40,g44)
    c: Horizontal(g41,g46)
    c: DistanceX(g40,g44) = 14.91
    c: DistanceX(g44,g44) = 7.45
    c: DistanceY(g2,g0) = 4
    c: Coincident(g48,g49)
    c: Coincident(g49,g50)
    c: Coincident(g50,g51)
    c: Coincident(g51,g48)
    c: Horizontal(g48)
    c: Horizontal(g50)
    c: Vertical(g49)
    c: Vertical(g51)
    c: PointOnObject(g48,g-5)
    c: Coincident(g52,g53)
    c: Coincident(g53,g54)
    c: Coincident(g54,g55)
    c: Coincident(g55,g52)
    c: Horizontal(g52)
    c: Horizontal(g54)
    c: Vertical(g53)
    c: Vertical(g55)
    c: PointOnObject(g52,g-5)
    c: Coincident(g56,g57)
    c: Coincident(g57,g58)
    c: Coincident(g58,g59)
    c: Coincident(g59,g56)
    c: Horizontal(g56)
    c: Horizontal(g58)
    c: Vertical(g57)
    c: Vertical(g59)
    c: PointOnObject(g56,g-5)
    c: Coincident(g60,g61)
    c: Coincident(g61,g62)
    c: Coincident(g62,g63)
    c: Coincident(g63,g60)
    c: Horizontal(g60)
    c: Horizontal(g62)
    c: Vertical(g61)
    c: Vertical(g63)
    c: PointOnObject(g60,g-5)
    c: Coincident(g64,g65)
    c: Coincident(g65,g66)
    c: Coincident(g66,g67)
    c: Coincident(g67,g64)
    c: Horizontal(g64)
    c: Horizontal(g66)
    c: Vertical(g65)
    c: Vertical(g67)
    c: PointOnObject(g64,g-5)
    c: Vertical(g53,g49)
    c: Vertical(g49,g57)
    c: Vertical(g57,g61)
    c: DistanceY(g48,g2) = 7
    c: DistanceY(g50,g48) = 14
    c: Equal(g49,g53)
    c: Equal(g53,g57)
    c: Equal(g57,g61)
    c: Equal(g61,g65)
    c: DistanceY(g52,g50) = 14
    c: DistanceY(g56,g54) = 14
    c: DistanceY(g60,g58) = 14
    c: DistanceY(g64,g62) = 14
    c: Coincident(g68,g69)
    c: Coincident(g69,g70)
    c: Coincident(g70,g71)
    c: Coincident(g71,g68)
    c: Horizontal(g68)
    c: Horizontal(g70)
    c: Vertical(g69)
    c: Vertical(g71)
    c: Coincident(g72,g73)
    c: Coincident(g73,g74)
    c: Coincident(g74,g75)
    c: Coincident(g75,g72)
    c: Horizontal(g72)
    c: Horizontal(g74)
    c: Vertical(g73)
    c: Vertical(g75)
    c: Equal(g69,g73)
    c: DistanceY(g72,g70) = 14
    c: PointOnObject(g74,g-5)
    c: PointOnObject(g70,g-5)
    c: Vertical(g65,g68)
    c: Vertical(g61,g64)
    c: DistanceY(g68,g66) = 14
    c: Equal(g69,g65)
    c: DistanceX(g48,g48) = 4
    c: Vertical(g69,g72)
    c: Coincident(g76,g77)
    c: Coincident(g77,g78)
    c: Coincident(g78,g79)
    c: Coincident(g79,g76)
    c: Horizontal(g76)
    c: Horizontal(g78)
    c: Vertical(g77)
    c: Vertical(g79)
    c: Coincident(g80,g81)
    c: Coincident(g81,g82)
    c: Coincident(g82,g83)
    c: Coincident(g83,g80)
    c: Horizontal(g80)
    c: Horizontal(g82)
    c: Vertical(g81)
    c: Vertical(g83)
    c: Coincident(g84,g85)
    c: Coincident(g85,g86)
    c: Coincident(g86,g87)
    c: Coincident(g87,g84)
    c: Horizontal(g84)
    c: Horizontal(g86)
    c: Vertical(g85)
    c: Vertical(g87)
    c: Coincident(g88,g89)
    c: Coincident(g89,g90)
    c: Coincident(g90,g91)
    c: Coincident(g91,g88)
    c: Horizontal(g88)
    c: Horizontal(g90)
    c: Vertical(g89)
    c: Vertical(g91)
    c: Coincident(g92,g93)
    c: Coincident(g93,g94)
    c: Coincident(g94,g95)
    c: Coincident(g95,g92)
    c: Horizontal(g92)
    c: Horizontal(g94)
    c: Vertical(g93)
    c: Vertical(g95)
    c: Vertical(g81,g77)
    c: Vertical(g77,g85)
    c: Vertical(g85,g89)
    c: DistanceY(g78,g76) = 14
    c: Equal(g77,g81)
    c: Equal(g81,g85)
    c: Equal(g85,g89)
    c: Equal(g89,g93)
    c: DistanceY(g80,g78) = 14
    c: DistanceY(g84,g82) = 14
    c: DistanceY(g88,g86) = 14
    c: DistanceY(g92,g90) = 14
    c: Coincident(g96,g97)
    c: Coincident(g97,g98)
    c: Coincident(g98,g99)
    c: Coincident(g99,g96)
    c: Horizontal(g96)
    c: Horizontal(g98)
    c: Vertical(g97)
    c: Vertical(g99)
    c: Coincident(g100,g101)
    c: Coincident(g101,g102)
    c: Coincident(g102,g103)
    c: Coincident(g103,g100)
    c: Horizontal(g100)
    c: Horizontal(g102)
    c: Vertical(g101)
    c: Vertical(g103)
    c: Equal(g97,g101)
    c: DistanceY(g100,g98) = 14
    c: Vertical(g93,g96)
    c: Vertical(g89,g92)
    c: DistanceY(g96,g94) = 14
    c: Equal(g97,g93)
    c: Equal(g48,g76) = 4
    c: Vertical(g97,g100)
    c: Vertical(g80,g78)
    c: Vertical(g82,g86)
    c: Vertical(g86,g90)
    c: Vertical(g90,g94)
    c: Vertical(g94,g98)
    c: Vertical(g98,g102)
    c: DistanceY(g76,g45) = 7
    c: PointOnObject(g104,g-2)
    c: PointOnObject(g105,g-2)
    c: PointOnObject(g106,g-2)
    c: PointOnObject(g107,g-2)
    c: Radius(g107) = 10
    c: Equal(g107,g106)
    c: Equal(g106,g105)
    c: Equal(g105,g104)
    c: DistanceY(g106,g-1) = 25
    c: DistanceY(g107,g106) = 50
    c: DistanceY(g-1,g105) = 25
    c: DistanceY(g105,g104) = 50
    c: Equal(g107,g111) = 10
    c: Equal(g111,g110)
    c: Equal(g110,g109)
    c: Equal(g109,g108)
    c: DistanceY(g111,g110) = 50
    c: DistanceY(g109,g108) = 50
    c: DistanceY(g110,g109) = 50
    c: Vertical(g111,g110)
    c: Vertical(g110,g109)
    c: Vertical(g109,g108)
    c: Equal(g115,g114)
    c: Equal(g114,g113)
    c: Equal(g113,g112)
    c: DistanceY(g115,g114) = 50
    c: DistanceY(g113,g112) = 50
    c: DistanceY(g114,g113) = 50
    c: Vertical(g115,g114)
    c: Vertical(g114,g113)
    c: Vertical(g113,g112)
    c: DistanceX(g107,g111) = 54.7
    c: DistanceX(g111,g115) = 54.7
    c: Horizontal(g107,g111)
    c: Horizontal(g111,g115)
    c: Radius(g115) = 10
    c: Equal(g119,g118)
    c: Equal(g118,g117)
    c: Equal(g117,g116)
    c: DistanceY(g119,g118) = 50
    c: DistanceY(g117,g116) = 50
    c: DistanceY(g118,g117) = 50
    c: Vertical(g119,g118)
    c: Vertical(g118,g117)
    c: Vertical(g117,g116)
    c: Equal(g123,g122)
    c: Equal(g122,g121)
    c: Equal(g121,g120)
    c: DistanceY(g123,g122) = 50
    c: DistanceY(g121,g120) = 50
    c: DistanceY(g122,g121) = 50
    c: Vertical(g123,g122)
    c: Vertical(g122,g121)
    c: Vertical(g121,g120)
    c: DistanceX(g119,g123) = 54.7
    c: Horizontal(g119,g123)
    c: Equal(g115,g123) = 10
    c: Horizontal(g107,g123)
    c: DistanceX(g123,g107) = 54.7
    c: Radius(g119) = 10
    c: PointOnObject(g76,g-6)
FEATURE [PartDesign::Pocket] Pocket026
  BaseFeature = -> Pad030
  Length = 4
  Length2 = 100
  Profile = -> Sketch061
  Type = 0
FEATURE [PartDesign::Body] Body029  label="UtrustningsBoxBotten-1"
  Group = -> [Sketch060,Pad030,Sketch061,Pocket026]
  Origin = -> Origin029
  Placement = pos=(-500,-402,-45) rot=(0,0,1;0rad)
  Tip = -> Pocket026
FEATURE [Sketcher::SketchObject] Sketch062
  FullyConstrained = true
  MapMode = 5
  Placement = pos=(0,0,0) rot=(0.57735,0.57735,0.57735;2.0944rad)
  Support = -> [YZ_Plane031]
  sketch-geometry (4):
    g0: LineSegment StartX=-100 StartY=-45 StartZ=0 EndX=100 EndY=-45 EndZ=0
    g1: LineSegment StartX=100 StartY=-45 StartZ=0 EndX=100 EndY=45 EndZ=0
    g2: LineSegment StartX=100 StartY=45 StartZ=0 EndX=-100 EndY=45 EndZ=0
    g3: LineSegment StartX=-100 StartY=45 StartZ=0 EndX=-100 EndY=-45 EndZ=0
  constraints (11):
    c: Coincident(g0,g1)
    c: Coincident(g1,g2)
    c: Coincident(g2,g3)
    c: Coincident(g3,g0)
    c: Horizontal(g0)
    c: Horizontal(g2)
    c: Vertical(g1)
    c: Vertical(g3)
    c: Symmetric(g0,g2,g-1)
    c: DistanceX(g0,g0) = 200
    c: DistanceY(g0,g2) = 90
FEATURE [PartDesign::Pad] Pad031
  Direction = (1,1,1)
  Length = 4
  Length2 = 100
  Placement = pos=(0,0,0) rot=(0.57735,0.57735,0.57735;2.0944rad)
  Profile = -> Sketch062
  Type = 0
FEATURE [Sketcher::SketchObject] Sketch063
  ExternalGeometry = -> [Pad031]
  FullyConstrained = true
  MapMode = 5
  Placement = pos=(4,-9e-16,9e-16) rot=(0.57735,0.57735,0.57735;2.0944rad)
  Support = -> [Pad031]
  sketch-geometry (48):
    g0: LineSegment StartX=-93 StartY=-45 StartZ=0 EndX=-100 EndY=-45 EndZ=0
    g1: LineSegment StartX=-100 StartY=-45 StartZ=0 EndX=-100 EndY=-41 EndZ=0
    g2: LineSegment StartX=-100 StartY=-41 StartZ=0 EndX=-93 EndY=-41 EndZ=0
    g3: LineSegment StartX=-93 StartY=-41 StartZ=0 EndX=-93 EndY=-45 EndZ=0
    g4: LineSegment StartX=-79 StartY=-45 StartZ=0 EndX=-65 EndY=-45 EndZ=0
    g5: LineSegment StartX=-65 StartY=-45 StartZ=0 EndX=-65 EndY=-41 EndZ=0
    g6: LineSegment StartX=-65 StartY=-41 StartZ=0 EndX=-79 EndY=-41 EndZ=0
    g7: LineSegment StartX=-79 StartY=-41 StartZ=0 EndX=-79 EndY=-45 EndZ=0
    g8: LineSegment StartX=-51 StartY=-45 StartZ=0 EndX=-37 EndY=-45 EndZ=0
    g9: LineSegment StartX=-37 StartY=-45 StartZ=0 EndX=-37 EndY=-41 EndZ=0
    g10: LineSegment StartX=-37 StartY=-41 StartZ=0 EndX=-51 EndY=-41 EndZ=0
    g11: LineSegment StartX=-51 StartY=-41 StartZ=0 EndX=-51 EndY=-45 EndZ=0
    g12: LineSegment StartX=-23 StartY=-45 StartZ=0 EndX=-9 EndY=-45 EndZ=0
    g13: LineSegment StartX=-9 StartY=-45 StartZ=0 EndX=-9 EndY=-41 EndZ=0
    g14: LineSegment StartX=-9 StartY=-41 StartZ=0 EndX=-23 EndY=-41 EndZ=0
    g15: LineSegment StartX=-23 StartY=-41 StartZ=0 EndX=-23 EndY=-45 EndZ=0
    g16: LineSegment StartX=5 StartY=-45 StartZ=0 EndX=19 EndY=-45 EndZ=0
    g17: LineSegment StartX=19 StartY=-45 StartZ=0 EndX=19 EndY=-41 EndZ=0
    g18: LineSegment StartX=19 StartY=-41 StartZ=0 EndX=5 EndY=-41 EndZ=0
    g19: LineSegment StartX=5 StartY=-41 StartZ=0 EndX=5 EndY=-45 EndZ=0
    g20: LineSegment StartX=33 StartY=-45 StartZ=0 EndX=47 EndY=-45 EndZ=0
    g21: LineSegment StartX=47 StartY=-45 StartZ=0 EndX=47 EndY=-41 EndZ=0
    g22: LineSegment StartX=47 StartY=-41 StartZ=0 EndX=33 EndY=-41 EndZ=0
    g23: LineSegment StartX=33 StartY=-41 StartZ=0 EndX=33 EndY=-45 EndZ=0
    g24: LineSegment StartX=61 StartY=-45 StartZ=0 EndX=75 EndY=-45 EndZ=0
    g25: LineSegment StartX=75 StartY=-45 StartZ=0 EndX=75 EndY=-41 EndZ=0
    g26: LineSegment StartX=75 StartY=-41 StartZ=0 EndX=61 EndY=-41 EndZ=0
    g27: LineSegment StartX=61 StartY=-41 StartZ=0 EndX=61 EndY=-45 EndZ=0
    g28: LineSegment StartX=100 StartY=-22.5 StartZ=0 EndX=96 EndY=-22.5 EndZ=0
    g29: LineSegment StartX=96 StartY=-22.5 StartZ=0 EndX=96 EndY=-7.5 EndZ=0
    g30: LineSegment StartX=96 StartY=-7.5 StartZ=0 EndX=100 EndY=-7.5 EndZ=0
    g31: LineSegment StartX=100 StartY=-7.5 StartZ=0 EndX=100 EndY=-22.5 EndZ=0
    g32: LineSegment StartX=100 StartY=7.5 StartZ=0 EndX=96 EndY=7.5 EndZ=0
    g33: LineSegment StartX=96 StartY=7.5 StartZ=0 EndX=96 EndY=22.5 EndZ=0
    g34: LineSegment StartX=96 StartY=22.5 StartZ=0 EndX=100 EndY=22.5 EndZ=0
    g35: LineSegment StartX=100 StartY=22.5 StartZ=0 EndX=100 EndY=7.5 EndZ=0
    g36: LineSegment StartX=100 StartY=37.5 StartZ=0 EndX=96 EndY=37.5 EndZ=0
    g37: LineSegment StartX=96 StartY=37.5 StartZ=0 EndX=96 EndY=45 EndZ=0
    g38: LineSegment StartX=96 StartY=45 StartZ=0 EndX=100 EndY=45 EndZ=0
    g39: LineSegment StartX=100 StartY=45 StartZ=0 EndX=100 EndY=37.5 EndZ=0
    g40: LineSegment StartX=89 StartY=-45 StartZ=0 EndX=89 EndY=-41 EndZ=0
    g41: LineSegment StartX=89 StartY=-41 StartZ=0 EndX=96 EndY=-41 EndZ=0
    g42: LineSegment StartX=96 StartY=-41 StartZ=0 EndX=96 EndY=-37.5 EndZ=0
    g43: LineSegment StartX=96 StartY=-37.5 StartZ=0 EndX=100 EndY=-37.5 EndZ=0
    g44: LineSegment StartX=100 StartY=-37.5 StartZ=0 EndX=100 EndY=-45 EndZ=0
    g45: LineSegment StartX=100 StartY=-45 StartZ=0 EndX=89 EndY=-45 EndZ=0
    g46: Circle CenterX=-23 CenterY=0 CenterZ=0 NormalX=0 NormalY=0 NormalZ=1 AngleXU=0 Radius=25
    g47: Circle CenterX=47 CenterY=0 CenterZ=0 NormalX=0 NormalY=0 NormalZ=1 AngleXU=0 Radius=25
  constraints (143):
    c: Coincident(g0,g1)
    c: Coincident(g1,g2)
    c: Coincident(g2,g3)
    c: Coincident(g3,g0)
    c: Horizontal(g0)
    c: Horizontal(g2)
    c: Vertical(g1)
    c: Vertical(g3)
    c: PointOnObject(g1,g-4)
    c: Coincident(g4,g5)
    c: Coincident(g5,g6)
    c: Coincident(g6,g7)
    c: Coincident(g7,g4)
    c: Horizontal(g4)
    c: Horizontal(g6)
    c: Vertical(g5)
    c: Vertical(g7)
    c: Coincident(g8,g9)
    c: Coincident(g9,g10)
    c: Coincident(g10,g11)
    c: Coincident(g11,g8)
    c: Horizontal(g8)
    c: Horizontal(g10)
    c: Vertical(g9)
    c: Vertical(g11)
    c: Coincident(g12,g13)
    c: Coincident(g13,g14)
    c: Coincident(g14,g15)
    c: Coincident(g15,g12)
    c: Horizontal(g12)
    c: Horizontal(g14)
    c: Vertical(g13)
    c: Vertical(g15)
    c: Coincident(g16,g17)
    c: Coincident(g17,g18)
    c: Coincident(g18,g19)
    c: Coincident(g19,g16)
    c: Horizontal(g16)
    c: Horizontal(g18)
    c: Vertical(g17)
    c: Vertical(g19)
    c: Coincident(g20,g21)
    c: Coincident(g21,g22)
    c: Coincident(g22,g23)
    c: Coincident(g23,g20)
    c: Horizontal(g20)
    c: Horizontal(g22)
    c: Vertical(g21)
    c: Vertical(g23)
    c: Coincident(g24,g25)
    c: Coincident(g25,g26)
    c: Coincident(g26,g27)
    c: Coincident(g27,g24)
    c: Horizontal(g24)
    c: Horizontal(g26)
    c: Vertical(g25)
    c: Vertical(g27)
    c: Horizontal(g2,g5)
    c: Horizontal(g5,g9)
    c: Horizontal(g9,g13)
    c: Horizontal(g13,g17)
    c: Horizontal(g17,g21)
    c: Horizontal(g21,g25)
    c: DistanceX(g0,g0) = 7
    c: DistanceX(g0,g4) = 14
    c: DistanceX(g4,g4) = 14
    c: Equal(g8,g4)
    c: Equal(g8,g12)
    c: Equal(g12,g16)
    c: Equal(g16,g20)
    c: Equal(g20,g24)
    c: DistanceX(g4,g8) = 14
    c: DistanceX(g8,g12) = 14
    c: DistanceX(g12,g16) = 14
    c: DistanceX(g16,g20) = 14
    c: DistanceX(g20,g24) = 14
    c: Coincident(g28,g29)
    c: Coincident(g29,g30)
    c: Coincident(g30,g31)
    c: Coincident(g31,g28)
    c: Horizontal(g28)
    c: Horizontal(g30)
    c: Vertical(g29)
    c: Vertical(g31)
    c: Coincident(g32,g33)
    c: Coincident(g33,g34)
    c: Coincident(g34,g35)
    c: Coincident(g35,g32)
    c: Horizontal(g32)
    c: Horizontal(g34)
    c: Vertical(g33)
    c: Vertical(g35)
    c: Coincident(g36,g37)
    c: Coincident(g37,g38)
    c: Coincident(g38,g39)
    c: Coincident(g39,g36)
    c: Horizontal(g36)
    c: Horizontal(g38)
    c: Vertical(g37)
    c: Vertical(g39)
    c: PointOnObject(g37,g-5)
    c: DistanceY(g36,g38) = 7.5
    c: DistanceY(g32,g34) = 15
    c: Equal(g35,g31)
    c: DistanceY(g30,g32) = 15
    c: Vertical(g36,g32)
    c: Vertical(g32,g28)
    c: DistanceY(g0,g1) = 4
    c: PointOnObject(g0,g-7)
    c: PointOnObject(g4,g-7)
    c: PointOnObject(g8,g-7)
    c: PointOnObject(g12,g-7)
    c: PointOnObject(g16,g-7)
    c: PointOnObject(g20,g-7)
    c: PointOnObject(g24,g-7)
    c: PointOnObject(g40,g-7)
    c: Coincident(g40,g41)
    c: Horizontal(g41)
    c: Coincident(g41,g42)
    c: Vertical(g42)
    c: Coincident(g42,g43)
    c: PointOnObject(g43,g-6)
    c: Horizontal(g43)
    c: Coincident(g43,g44)
    c: Coincident(g44,g-7)
    c: Coincident(g44,g45)
    c: Coincident(g45,g40)
    c: Parallel(g-6,g40)
    c: Horizontal(g40,g25)
    c: DistanceX(g40,g44) = 11
    c: DistanceY(g44,g43) = 7.5
    c: PointOnObject(g30,g-6)
    c: PointOnObject(g34,g-6)
    c: PointOnObject(g36,g-6)
    c: Vertical(g42,g28)
    c: DistanceX(g41,g44) = 4
    c: DistanceY(g43,g28) = 15
    c: PointOnObject(g46,g-1)
    c: Radius(g46) = 25
    c: DistanceX(g46,g44) = 123
    c: PointOnObject(g47,g-1)
    c: Radius(g47) = 25
    c: DistanceX(g46,g47) = 70
FEATURE [PartDesign::Pocket] Pocket027
  BaseFeature = -> Pad031
  Length = 4
  Length2 = 100
  Placement = pos=(0,0,0) rot=(0.57735,0.57735,0.57735;2.0944rad)
  Profile = -> Sketch063
  Type = 0
FEATURE [PartDesign::Fillet] Fillet
  Base = -> Pocket027 [Edge98]
  BaseFeature = -> Pocket027
  Placement = pos=(0,0,0) rot=(0.57735,0.57735,0.57735;2.0944rad)
  Radius = 65
  SupportTransform = false
FEATURE [PartDesign::Body] Body031  label="UtrustningsBoxSida-V-1"
  Group = -> [Sketch062,Pad031,Sketch063,Pocket027,Fillet]
  Origin = -> Origin031
  Placement = pos=(-664,-402,0) rot=(0,0,1;0rad)
  Tip = -> Fillet
FEATURE [Sketcher::SketchObject] Sketch065
  FullyConstrained = true
  MapMode = 5
  Placement = pos=(0,0,0) rot=(0.57735,0.57735,0.57735;2.0944rad)
  Support = -> [YZ_Plane032]
  sketch-geometry (4):
    g0: LineSegment StartX=-100 StartY=-45 StartZ=0 EndX=100 EndY=-45 EndZ=0
    g1: LineSegment StartX=100 StartY=-45 StartZ=0 EndX=100 EndY=45 EndZ=0
    g2: LineSegment StartX=100 StartY=45 StartZ=0 EndX=-100 EndY=45 EndZ=0
    g3: LineSegment StartX=-100 StartY=45 StartZ=0 EndX=-100 EndY=-45 EndZ=0
  constraints (11):
    c: Coincident(g0,g1)
    c: Coincident(g1,g2)
    c: Coincident(g2,g3)
    c: Coincident(g3,g0)
    c: Horizontal(g0)
    c: Horizontal(g2)
    c: Vertical(g1)
    c: Vertical(g3)
    c: Symmetric(g0,g2,g-1)
    c: DistanceX(g0,g0) = 200
    c: DistanceY(g0,g2) = 90
FEATURE [PartDesign::Pad] Pad032
  Direction = (1,1,1)
  Length = 4
  Length2 = 100
  Placement = pos=(0,0,0) rot=(0.57735,0.57735,0.57735;2.0944rad)
  Profile = -> Sketch065
  Type = 0
FEATURE [Sketcher::SketchObject] Sketch064
  ExternalGeometry = -> [Pad032]
  FullyConstrained = true
  MapMode = 5
  Placement = pos=(4,-9e-16,9e-16) rot=(0.57735,0.57735,0.57735;2.0944rad)
  Support = -> [Pad032]
  sketch-geometry (48):
    g0: LineSegment StartX=-93 StartY=-45 StartZ=0 EndX=-100 EndY=-45 EndZ=0
    g1: LineSegment StartX=-100 StartY=-45 StartZ=0 EndX=-100 EndY=-41 EndZ=0
    g2: LineSegment StartX=-100 StartY=-41 StartZ=0 EndX=-93 EndY=-41 EndZ=0
    g3: LineSegment StartX=-93 StartY=-41 StartZ=0 EndX=-93 EndY=-45 EndZ=0
    g4: LineSegment StartX=-79 StartY=-45 StartZ=0 EndX=-65 EndY=-45 EndZ=0
    g5: LineSegment StartX=-65 StartY=-45 StartZ=0 EndX=-65 EndY=-41 EndZ=0
    g6: LineSegment StartX=-65 StartY=-41 StartZ=0 EndX=-79 EndY=-41 EndZ=0
    g7: LineSegment StartX=-79 StartY=-41 StartZ=0 EndX=-79 EndY=-45 EndZ=0
    g8: LineSegment StartX=-51 StartY=-45 StartZ=0 EndX=-37 EndY=-45 EndZ=0
    g9: LineSegment StartX=-37 StartY=-45 StartZ=0 EndX=-37 EndY=-41 EndZ=0
    g10: LineSegment StartX=-37 StartY=-41 StartZ=0 EndX=-51 EndY=-41 EndZ=0
    g11: LineSegment StartX=-51 StartY=-41 StartZ=0 EndX=-51 EndY=-45 EndZ=0
    g12: LineSegment StartX=-23 StartY=-45 StartZ=0 EndX=-9 EndY=-45 EndZ=0
    g13: LineSegment StartX=-9 StartY=-45 StartZ=0 EndX=-9 EndY=-41 EndZ=0
    g14: LineSegment StartX=-9 StartY=-41 StartZ=0 EndX=-23 EndY=-41 EndZ=0
    g15: LineSegment StartX=-23 StartY=-41 StartZ=0 EndX=-23 EndY=-45 EndZ=0
    g16: LineSegment StartX=5 StartY=-45 StartZ=0 EndX=19 EndY=-45 EndZ=0
    g17: LineSegment StartX=19 StartY=-45 StartZ=0 EndX=19 EndY=-41 EndZ=0
    g18: LineSegment StartX=19 StartY=-41 StartZ=0 EndX=5 EndY=-41 EndZ=0
    g19: LineSegment StartX=5 StartY=-41 StartZ=0 EndX=5 EndY=-45 EndZ=0
    g20: LineSegment StartX=33 StartY=-45 StartZ=0 EndX=47 EndY=-45 EndZ=0
    g21: LineSegment StartX=47 StartY=-45 StartZ=0 EndX=47 EndY=-41 EndZ=0
    g22: LineSegment StartX=47 StartY=-41 StartZ=0 EndX=33 EndY=-41 EndZ=0
    g23: LineSegment StartX=33 StartY=-41 StartZ=0 EndX=33 EndY=-45 EndZ=0
    g24: LineSegment StartX=61 StartY=-45 StartZ=0 EndX=75 EndY=-45 EndZ=0
    g25: LineSegment StartX=75 StartY=-45 StartZ=0 EndX=75 EndY=-41 EndZ=0
    g26: LineSegment StartX=75 StartY=-41 StartZ=0 EndX=61 EndY=-41 EndZ=0
    g27: LineSegment StartX=61 StartY=-41 StartZ=0 EndX=61 EndY=-45 EndZ=0
    g28: LineSegment StartX=100 StartY=-22.5 StartZ=0 EndX=96 EndY=-22.5 EndZ=0
    g29: LineSegment StartX=96 StartY=-22.5 StartZ=0 EndX=96 EndY=-7.5 EndZ=0
    g30: LineSegment StartX=96 StartY=-7.5 StartZ=0 EndX=100 EndY=-7.5 EndZ=0
    g31: LineSegment StartX=100 StartY=-7.5 StartZ=0 EndX=100 EndY=-22.5 EndZ=0
    g32: LineSegment StartX=100 StartY=7.5 StartZ=0 EndX=96 EndY=7.5 EndZ=0
    g33: LineSegment StartX=96 StartY=7.5 StartZ=0 EndX=96 EndY=22.5 EndZ=0
    g34: LineSegment StartX=96 StartY=22.5 StartZ=0 EndX=100 EndY=22.5 EndZ=0
    g35: LineSegment StartX=100 StartY=22.5 StartZ=0 EndX=100 EndY=7.5 EndZ=0
    g36: LineSegment StartX=100 StartY=37.5 StartZ=0 EndX=96 EndY=37.5 EndZ=0
    g37: LineSegment StartX=96 StartY=37.5 StartZ=0 EndX=96 EndY=45 EndZ=0
    g38: LineSegment StartX=96 StartY=45 StartZ=0 EndX=100 EndY=45 EndZ=0
    g39: LineSegment StartX=100 StartY=45 StartZ=0 EndX=100 EndY=37.5 EndZ=0
    g40: LineSegment StartX=89 StartY=-45 StartZ=0 EndX=89 EndY=-41 EndZ=0
    g41: LineSegment StartX=89 StartY=-41 StartZ=0 EndX=96 EndY=-41 EndZ=0
    g42: LineSegment StartX=96 StartY=-41 StartZ=0 EndX=96 EndY=-37.5 EndZ=0
    g43: LineSegment StartX=96 StartY=-37.5 StartZ=0 EndX=100 EndY=-37.5 EndZ=0
    g44: LineSegment StartX=100 StartY=-37.5 StartZ=0 EndX=100 EndY=-45 EndZ=0
    g45: LineSegment StartX=100 StartY=-45 StartZ=0 EndX=89 EndY=-45 EndZ=0
    g46: Circle CenterX=-23 CenterY=0 CenterZ=0 NormalX=0 NormalY=0 NormalZ=1 AngleXU=0 Radius=25
    g47: Circle CenterX=47 CenterY=0 CenterZ=0 NormalX=0 NormalY=0 NormalZ=1 AngleXU=0 Radius=25
  constraints (143):
    c: Coincident(g0,g1)
    c: Coincident(g1,g2)
    c: Coincident(g2,g3)
    c: Coincident(g3,g0)
    c: Horizontal(g0)
    c: Horizontal(g2)
    c: Vertical(g1)
    c: Vertical(g3)
    c: PointOnObject(g1,g-4)
    c: Coincident(g4,g5)
    c: Coincident(g5,g6)
    c: Coincident(g6,g7)
    c: Coincident(g7,g4)
    c: Horizontal(g4)
    c: Horizontal(g6)
    c: Vertical(g5)
    c: Vertical(g7)
    c: Coincident(g8,g9)
    c: Coincident(g9,g10)
    c: Coincident(g10,g11)
    c: Coincident(g11,g8)
    c: Horizontal(g8)
    c: Horizontal(g10)
    c: Vertical(g9)
    c: Vertical(g11)
    c: Coincident(g12,g13)
    c: Coincident(g13,g14)
    c: Coincident(g14,g15)
    c: Coincident(g15,g12)
    c: Horizontal(g12)
    c: Horizontal(g14)
    c: Vertical(g13)
    c: Vertical(g15)
    c: Coincident(g16,g17)
    c: Coincident(g17,g18)
    c: Coincident(g18,g19)
    c: Coincident(g19,g16)
    c: Horizontal(g16)
    c: Horizontal(g18)
    c: Vertical(g17)
    c: Vertical(g19)
    c: Coincident(g20,g21)
    c: Coincident(g21,g22)
    c: Coincident(g22,g23)
    c: Coincident(g23,g20)
    c: Horizontal(g20)
    c: Horizontal(g22)
    c: Vertical(g21)
    c: Vertical(g23)
    c: Coincident(g24,g25)
    c: Coincident(g25,g26)
    c: Coincident(g26,g27)
    c: Coincident(g27,g24)
    c: Horizontal(g24)
    c: Horizontal(g26)
    c: Vertical(g25)
    c: Vertical(g27)
    c: Horizontal(g2,g5)
    c: Horizontal(g5,g9)
    c: Horizontal(g9,g13)
    c: Horizontal(g13,g17)
    c: Horizontal(g17,g21)
    c: Horizontal(g21,g25)
    c: DistanceX(g0,g0) = 7
    c: DistanceX(g0,g4) = 14
    c: DistanceX(g4,g4) = 14
    c: Equal(g8,g4)
    c: Equal(g8,g12)
    c: Equal(g12,g16)
    c: Equal(g16,g20)
    c: Equal(g20,g24)
    c: DistanceX(g4,g8) = 14
    c: DistanceX(g8,g12) = 14
    c: DistanceX(g12,g16) = 14
    c: DistanceX(g16,g20) = 14
    c: DistanceX(g20,g24) = 14
    c: Coincident(g28,g29)
    c: Coincident(g29,g30)
    c: Coincident(g30,g31)
    c: Coincident(g31,g28)
    c: Horizontal(g28)
    c: Horizontal(g30)
    c: Vertical(g29)
    c: Vertical(g31)
    c: Coincident(g32,g33)
    c: Coincident(g33,g34)
    c: Coincident(g34,g35)
    c: Coincident(g35,g32)
    c: Horizontal(g32)
    c: Horizontal(g34)
    c: Vertical(g33)
    c: Vertical(g35)
    c: Coincident(g36,g37)
    c: Coincident(g37,g38)
    c: Coincident(g38,g39)
    c: Coincident(g39,g36)
    c: Horizontal(g36)
    c: Horizontal(g38)
    c: Vertical(g37)
    c: Vertical(g39)
    c: PointOnObject(g37,g-5)
    c: DistanceY(g36,g38) = 7.5
    c: DistanceY(g32,g34) = 15
    c: Equal(g35,g31)
    c: DistanceY(g30,g32) = 15
    c: Vertical(g36,g32)
    c: Vertical(g32,g28)
    c: DistanceY(g0,g1) = 4
    c: PointOnObject(g0,g-7)
    c: PointOnObject(g4,g-7)
    c: PointOnObject(g8,g-7)
    c: PointOnObject(g12,g-7)
    c: PointOnObject(g16,g-7)
    c: PointOnObject(g20,g-7)
    c: PointOnObject(g24,g-7)
    c: PointOnObject(g40,g-7)
    c: Coincident(g40,g41)
    c: Horizontal(g41)
    c: Coincident(g41,g42)
    c: Vertical(g42)
    c: Coincident(g42,g43)
    c: PointOnObject(g43,g-6)
    c: Horizontal(g43)
    c: Coincident(g43,g44)
    c: Coincident(g44,g-7)
    c: Coincident(g44,g45)
    c: Coincident(g45,g40)
    c: Parallel(g-6,g40)
    c: Horizontal(g40,g25)
    c: DistanceX(g40,g44) = 11
    c: DistanceY(g44,g43) = 7.5
    c: PointOnObject(g30,g-6)
    c: PointOnObject(g34,g-6)
    c: PointOnObject(g36,g-6)
    c: Vertical(g42,g28)
    c: DistanceX(g41,g44) = 4
    c: DistanceY(g43,g28) = 15
    c: PointOnObject(g46,g-1)
    c: Radius(g46) = 25
    c: DistanceX(g46,g44) = 123
    c: PointOnObject(g47,g-1)
    c: Radius(g47) = 25
    c: DistanceX(g46,g47) = 70
FEATURE [PartDesign::Pocket] Pocket028
  BaseFeature = -> Pad032
  Length = 4
  Length2 = 100
  Placement = pos=(0,0,0) rot=(0.57735,0.57735,0.57735;2.0944rad)
  Profile = -> Sketch064
  Type = 0
FEATURE [PartDesign::Fillet] Fillet001
  Base = -> Pocket028 [Edge98]
  BaseFeature = -> Pocket028
  Placement = pos=(0,0,0) rot=(0.57735,0.57735,0.57735;2.0944rad)
  Radius = 65
  SupportTransform = false
FEATURE [PartDesign::Body] Body032  label="UtrustningsBoxSida-H-1"
  Group = -> [Sketch065,Pad032,Sketch064,Pocket028,Fillet001]
  Origin = -> Origin032
  Placement = pos=(-340,-402,0) rot=(0,0,1;0rad)
  Tip = -> Fillet001
FEATURE [Sketcher::SketchObject] Sketch066
  FullyConstrained = true
  MapMode = 5
  Placement = pos=(0,0,0) rot=(1,0,0;1.5708rad)
  Support = -> [XZ_Plane033]
  sketch-geometry (4):
    g0: LineSegment StartX=-164 StartY=-45 StartZ=0 EndX=164 EndY=-45 EndZ=0
    g1: LineSegment StartX=164 StartY=-45 StartZ=0 EndX=164 EndY=45 EndZ=0
    g2: LineSegment StartX=164 StartY=45 StartZ=0 EndX=-164 EndY=45 EndZ=0
    g3: LineSegment StartX=-164 StartY=45 StartZ=0 EndX=-164 EndY=-45 EndZ=0
  constraints (11):
    c: Coincident(g0,g1)
    c: Coincident(g1,g2)
    c: Coincident(g2,g3)
    c: Coincident(g3,g0)
    c: Horizontal(g0)
    c: Horizontal(g2)
    c: Vertical(g1)
    c: Vertical(g3)
    c: Symmetric(g0,g1,g-1)
    c: DistanceX(g0,g0) = 328
    c: DistanceY(g0,g2) = 90
FEATURE [PartDesign::Pad] Pad033
  Direction = (1,1,1)
  Length = 4
  Length2 = 100
  Placement = pos=(0,0,0) rot=(1,0,0;1.5708rad)
  Profile = -> Sketch066
  Type = 0
FEATURE [Sketcher::SketchObject] Sketch067
  ExternalGeometry = -> [Pad033]
  FullyConstrained = true
  MapMode = 5
  Placement = pos=(0,-4,1.8e-15) rot=(1,0,0;1.5708rad)
  Support = -> [Pad033]
  sketch-geometry (71):
    g0: Circle CenterX=-83.33 CenterY=0 CenterZ=0 NormalX=0 NormalY=0 NormalZ=1 AngleXU=0 Radius=25
    g1: Circle CenterX=0 CenterY=0 CenterZ=0 NormalX=0 NormalY=0 NormalZ=1 AngleXU=0 Radius=25
    g2: Circle CenterX=83.33 CenterY=0 CenterZ=0 NormalX=0 NormalY=0 NormalZ=1 AngleXU=0 Radius=25
    g3: LineSegment StartX=-160 StartY=-37.5 StartZ=0 EndX=-164 EndY=-37.5 EndZ=0
    g4: LineSegment StartX=-164 StartY=-37.5 StartZ=0 EndX=-164 EndY=-22.5 EndZ=0
    g5: LineSegment StartX=-164 StartY=-22.5 StartZ=0 EndX=-160 EndY=-22.5 EndZ=0
    g6: LineSegment StartX=-160 StartY=-22.5 StartZ=0 EndX=-160 EndY=-37.5 EndZ=0
    g7: LineSegment StartX=-160 StartY=-7.5 StartZ=0 EndX=-164 EndY=-7.5 EndZ=0
    g8: LineSegment StartX=-164 StartY=-7.5 StartZ=0 EndX=-164 EndY=7.5 EndZ=0
    g9: LineSegment StartX=-164 StartY=7.5 StartZ=0 EndX=-160 EndY=7.5 EndZ=0
    g10: LineSegment StartX=-160 StartY=7.5 StartZ=0 EndX=-160 EndY=-7.5 EndZ=0
    g11: LineSegment StartX=-160 StartY=22.5 StartZ=0 EndX=-164 EndY=22.5 EndZ=0
    g12: LineSegment StartX=-164 StartY=22.5 StartZ=0 EndX=-164 EndY=37.5 EndZ=0
    g13: LineSegment StartX=-164 StartY=37.5 StartZ=0 EndX=-160 EndY=37.5 EndZ=0
    g14: LineSegment StartX=-160 StartY=37.5 StartZ=0 EndX=-160 EndY=22.5 EndZ=0
    g15: LineSegment StartX=160 StartY=-37.5 StartZ=0 EndX=164 EndY=-37.5 EndZ=0
    g16: LineSegment StartX=164 StartY=-37.5 StartZ=0 EndX=164 EndY=-22.5 EndZ=0
    g17: LineSegment StartX=164 StartY=-22.5 StartZ=0 EndX=160 EndY=-22.5 EndZ=0
    g18: LineSegment StartX=160 StartY=-22.5 StartZ=0 EndX=160 EndY=-37.5 EndZ=0
    g19: LineSegment StartX=160 StartY=-7.5 StartZ=0 EndX=164 EndY=-7.5 EndZ=0
    g20: LineSegment StartX=164 StartY=-7.5 StartZ=0 EndX=164 EndY=7.5 EndZ=0
    g21: LineSegment StartX=164 StartY=7.5 StartZ=0 EndX=160 EndY=7.5 EndZ=0
    g22: LineSegment StartX=160 StartY=7.5 StartZ=0 EndX=160 EndY=-7.5 EndZ=0
    g23: LineSegment StartX=160 StartY=22.5 StartZ=0 EndX=164 EndY=22.5 EndZ=0
    g24: LineSegment StartX=164 StartY=22.5 StartZ=0 EndX=164 EndY=37.5 EndZ=0
    g25: LineSegment StartX=164 StartY=37.5 StartZ=0 EndX=160 EndY=37.5 EndZ=0
    g26: LineSegment StartX=160 StartY=37.5 StartZ=0 EndX=160 EndY=22.5 EndZ=0
    g27: LineSegment StartX=-156.55 StartY=-41 StartZ=0 EndX=-141.64 EndY=-41 EndZ=0
    g28: LineSegment StartX=-141.64 StartY=-41 StartZ=0 EndX=-141.64 EndY=-45 EndZ=0
    g29: LineSegment StartX=-141.64 StartY=-45 StartZ=0 EndX=-156.55 EndY=-45 EndZ=0
    g30: LineSegment StartX=-156.55 StartY=-45 StartZ=0 EndX=-156.55 EndY=-41 EndZ=0
    g31: LineSegment StartX=-126.73 StartY=-41 StartZ=0 EndX=-111.82 EndY=-41 EndZ=0
    g32: LineSegment StartX=-111.82 StartY=-41 StartZ=0 EndX=-111.82 EndY=-45 EndZ=0
    g33: LineSegment StartX=-111.82 StartY=-45 StartZ=0 EndX=-126.73 EndY=-45 EndZ=0
    g34: LineSegment StartX=-126.73 StartY=-45 StartZ=0 EndX=-126.73 EndY=-41 EndZ=0
    g35: LineSegment StartX=-96.91 StartY=-41 StartZ=0 EndX=-82 EndY=-41 EndZ=0
    g36: LineSegment StartX=-82 StartY=-41 StartZ=0 EndX=-82 EndY=-45 EndZ=0
    g37: LineSegment StartX=-82 StartY=-45 StartZ=0 EndX=-96.91 EndY=-45 EndZ=0
    g38: LineSegment StartX=-96.91 StartY=-45 StartZ=0 EndX=-96.91 EndY=-41 EndZ=0
    g39: LineSegment StartX=-67.09 StartY=-41 StartZ=0 EndX=-52.18 EndY=-41 EndZ=0
    g40: LineSegment StartX=-52.18 StartY=-41 StartZ=0 EndX=-52.18 EndY=-45 EndZ=0
    g41: LineSegment StartX=-52.18 StartY=-45 StartZ=0 EndX=-67.09 EndY=-45 EndZ=0
    g42: LineSegment StartX=-67.09 StartY=-45 StartZ=0 EndX=-67.09 EndY=-41 EndZ=0
    g43: LineSegment StartX=-37.27 StartY=-41 StartZ=0 EndX=-22.36 EndY=-41 EndZ=0
    g44: LineSegment StartX=-22.36 StartY=-41 StartZ=0 EndX=-22.36 EndY=-45 EndZ=0
    g45: LineSegment StartX=-22.36 StartY=-45 StartZ=0 EndX=-37.27 EndY=-45 EndZ=0
    g46: LineSegment StartX=-37.27 StartY=-45 StartZ=0 EndX=-37.27 EndY=-41 EndZ=0
    g47: LineSegment StartX=-7.45 StartY=-41 StartZ=0 EndX=7.46 EndY=-41 EndZ=0
    g48: LineSegment StartX=7.46 StartY=-41 StartZ=0 EndX=7.46 EndY=-45 EndZ=0
    g49: LineSegment StartX=7.46 StartY=-45 StartZ=0 EndX=-7.45 EndY=-45 EndZ=0
    g50: LineSegment StartX=-7.45 StartY=-45 StartZ=0 EndX=-7.45 EndY=-41 EndZ=0
    g51: LineSegment StartX=22.37 StartY=-41 StartZ=0 EndX=37.28 EndY=-41 EndZ=0
    g52: LineSegment StartX=37.28 StartY=-41 StartZ=0 EndX=37.28 EndY=-45 EndZ=0
    g53: LineSegment StartX=37.28 StartY=-45 StartZ=0 EndX=22.37 EndY=-45 EndZ=0
    g54: LineSegment StartX=22.37 StartY=-45 StartZ=0 EndX=22.37 EndY=-41 EndZ=0
    g55: LineSegment StartX=52.19 StartY=-41 StartZ=0 EndX=67.1 EndY=-41 EndZ=0
    g56: LineSegment StartX=67.1 StartY=-41 StartZ=0 EndX=67.1 EndY=-45 EndZ=0
    g57: LineSegment StartX=67.1 StartY=-45 StartZ=0 EndX=52.19 EndY=-45 EndZ=0
    g58: LineSegment StartX=52.19 StartY=-45 StartZ=0 EndX=52.19 EndY=-41 EndZ=0
    g59: LineSegment StartX=82.01 StartY=-41 StartZ=0 EndX=96.92 EndY=-41 EndZ=0
    g60: LineSegment StartX=96.92 StartY=-41 StartZ=0 EndX=96.92 EndY=-45 EndZ=0
    g61: LineSegment StartX=96.92 StartY=-45 StartZ=0 EndX=82.01 EndY=-45 EndZ=0
    g62: LineSegment StartX=82.01 StartY=-45 StartZ=0 EndX=82.01 EndY=-41 EndZ=0
    g63: LineSegment StartX=111.83 StartY=-41 StartZ=0 EndX=126.74 EndY=-41 EndZ=0
    g64: LineSegment StartX=126.74 StartY=-41 StartZ=0 EndX=126.74 EndY=-45 EndZ=0
    g65: LineSegment StartX=126.74 StartY=-45 StartZ=0 EndX=111.83 EndY=-45 EndZ=0
    g66: LineSegment StartX=111.83 StartY=-45 StartZ=0 EndX=111.83 EndY=-41 EndZ=0
    g67: LineSegment StartX=141.65 StartY=-41 StartZ=0 EndX=156.56 EndY=-41 EndZ=0
    g68: LineSegment StartX=156.56 StartY=-41 StartZ=0 EndX=156.56 EndY=-45 EndZ=0
    g69: LineSegment StartX=156.56 StartY=-45 StartZ=0 EndX=141.65 EndY=-45 EndZ=0
    g70: LineSegment StartX=141.65 StartY=-45 StartZ=0 EndX=141.65 EndY=-41 EndZ=0
  constraints (212):
    c: PointOnObject(g0,g-1)
    c: Coincident(g1,g-1)
    c: PointOnObject(g2,g-1)
    c: Radius(g1) = 25
    c: Radius(g0) = 25
    c: Radius(g2) = 25
    c: DistanceX(g0,g1) = 83.33
    c: DistanceX(g1,g2) = 83.33
    c: Coincident(g3,g4)
    c: Coincident(g4,g5)
    c: Coincident(g5,g6)
    c: Coincident(g6,g3)
    c: Horizontal(g3)
    c: Horizontal(g5)
    c: Vertical(g4)
    c: Vertical(g6)
    c: Coincident(g7,g8)
    c: Coincident(g8,g9)
    c: Coincident(g9,g10)
    c: Coincident(g10,g7)
    c: Horizontal(g7)
    c: Horizontal(g9)
    c: Vertical(g8)
    c: Vertical(g10)
    c: Coincident(g11,g12)
    c: Coincident(g12,g13)
    c: Coincident(g13,g14)
    c: Coincident(g14,g11)
    c: Horizontal(g11)
    c: Horizontal(g13)
    c: Vertical(g12)
    c: Vertical(g14)
    c: Vertical(g3,g-3)
    c: Vertical(g7,g4)
    c: Vertical(g11,g8)
    c: Vertical(g5,g7)
    c: Vertical(g9,g11)
    c: DistanceY(g-3,g3) = 7.5
    c: DistanceY(g3,g4) = 15
    c: Equal(g4,g8)
    c: Equal(g8,g12)
    c: DistanceY(g4,g7) = 15
    c: DistanceY(g8,g11) = 15
    c: Coincident(g15,g16)
    c: Coincident(g16,g17)
    c: Coincident(g17,g18)
    c: Coincident(g18,g15)
    c: Horizontal(g15)
    c: Horizontal(g17)
    c: Vertical(g16)
    c: Vertical(g18)
    c: Coincident(g19,g20)
    c: Coincident(g20,g21)
    c: Coincident(g21,g22)
    c: Coincident(g22,g19)
    c: Horizontal(g19)
    c: Horizontal(g21)
    c: Vertical(g20)
    c: Vertical(g22)
    c: Coincident(g23,g24)
    c: Coincident(g24,g25)
    c: Coincident(g25,g26)
    c: Coincident(g26,g23)
    c: Horizontal(g23)
    c: Horizontal(g25)
    c: Vertical(g24)
    c: Vertical(g26)
    c: Vertical(g19,g16)
    c: Vertical(g23,g20)
    c: Vertical(g17,g19)
    c: Vertical(g21,g23)
    c: DistanceY(g15,g16) = 15
    c: Equal(g16,g20)
    c: Equal(g20,g24)
    c: DistanceY(g16,g19) = 15
    c: DistanceY(g20,g23) = 15
    c: Vertical(g15,g-4)
    c: DistanceY(g-4,g15) = 7.5
    c: DistanceX(g15,g15) = 4
    c: DistanceX(g3,g3) = 4
    c: Coincident(g27,g28)
    c: Coincident(g28,g29)
    c: Coincident(g29,g30)
    c: Coincident(g30,g27)
    c: Horizontal(g27)
    c: Horizontal(g29)
    c: Vertical(g28)
    c: Vertical(g30)
    c: Coincident(g31,g32)
    c: Coincident(g32,g33)
    c: Coincident(g33,g34)
    c: Coincident(g34,g31)
    c: Horizontal(g31)
    c: Horizontal(g33)
    c: Vertical(g32)
    c: Vertical(g34)
    c: Coincident(g35,g36)
    c: Coincident(g36,g37)
    c: Coincident(g37,g38)
    c: Coincident(g38,g35)
    c: Horizontal(g35)
    c: Horizontal(g37)
    c: Vertical(g36)
    c: Vertical(g38)
    c: Coincident(g39,g40)
    c: Coincident(g40,g41)
    c: Coincident(g41,g42)
    c: Coincident(g42,g39)
    c: Horizontal(g39)
    c: Horizontal(g41)
    c: Vertical(g40)
    c: Vertical(g42)
    c: Coincident(g43,g44)
    c: Coincident(g44,g45)
    c: Coincident(g45,g46)
    c: Coincident(g46,g43)
    c: Horizontal(g43)
    c: Horizontal(g45)
    c: Vertical(g44)
    c: Vertical(g46)
    c: Coincident(g47,g48)
    c: Coincident(g48,g49)
    c: Coincident(g49,g50)
    c: Coincident(g50,g47)
    c: Horizontal(g47)
    c: Horizontal(g49)
    c: Vertical(g48)
    c: Vertical(g50)
    c: Coincident(g51,g52)
    c: Coincident(g52,g53)
    c: Coincident(g53,g54)
    c: Coincident(g54,g51)
    c: Horizontal(g51)
    c: Horizontal(g53)
    c: Vertical(g52)
    c: Vertical(g54)
    c: Coincident(g55,g56)
    c: Coincident(g56,g57)
    c: Coincident(g57,g58)
    c: Coincident(g58,g55)
    c: Horizontal(g55)
    c: Horizontal(g57)
    c: Vertical(g56)
    c: Vertical(g58)
    c: Coincident(g59,g60)
    c: Coincident(g60,g61)
    c: Coincident(g61,g62)
    c: Coincident(g62,g59)
    c: Horizontal(g59)
    c: Horizontal(g61)
    c: Vertical(g60)
    c: Vertical(g62)
    c: Coincident(g63,g64)
    c: Coincident(g64,g65)
    c: Coincident(g65,g66)
    c: Coincident(g66,g63)
    c: Horizontal(g63)
    c: Horizontal(g65)
    c: Vertical(g64)
    c: Vertical(g66)
    c: Coincident(g67,g68)
    c: Coincident(g68,g69)
    c: Coincident(g69,g70)
    c: Coincident(g70,g67)
    c: Horizontal(g67)
    c: Horizontal(g69)
    c: Vertical(g68)
    c: Vertical(g70)
    c: Horizontal(g27,g31)
    c: Horizontal(g31,g35)
    c: Horizontal(g35,g39)
    c: Horizontal(g39,g43)
    c: Horizontal(g43,g47)
    c: Horizontal(g47,g51)
    c: Horizontal(g51,g55)
    c: Horizontal(g55,g59)
    c: Horizontal(g59,g63)
    c: Horizontal(g63,g67)
    c: Horizontal(g28,g32)
    c: Horizontal(g32,g36)
    c: Horizontal(g36,g40)
    c: Horizontal(g40,g44)
    c: Horizontal(g44,g48)
    c: Horizontal(g48,g52)
    c: Horizontal(g52,g56)
    c: Horizontal(g56,g60)
    c: Horizontal(g60,g64)
    c: Horizontal(g64,g68)
    c: Horizontal(g-3,g29)
    c: DistanceX(g29,g28) = 14.91
    c: Equal(g29,g69)
    c: Equal(g69,g65)
    c: Equal(g61,g65)
    c: Equal(g61,g57)
    c: Equal(g57,g53)
    c: Equal(g53,g49)
    c: Equal(g49,g45)
    c: Equal(g45,g41)
    c: Equal(g37,g41)
    c: Equal(g33,g37)
    c: DistanceX(g-3,g29) = 7.45
    c: DistanceX(g28,g33) = 14.91
    c: DistanceX(g32,g37) = 14.91
    c: DistanceX(g36,g41) = 14.91
    c: DistanceX(g40,g45) = 14.91
    c: DistanceX(g44,g49) = 14.91
    c: DistanceX(g48,g53) = 14.91
    c: DistanceX(g52,g57) = 14.91
    c: DistanceX(g56,g61) = 14.91
    c: DistanceX(g60,g65) = 14.91
    c: DistanceX(g64,g69) = 14.91
    c: DistanceY(g-3,g27) = 4
FEATURE [PartDesign::Pocket] Pocket029
  BaseFeature = -> Pad033
  Length = 4
  Length2 = 100
  Placement = pos=(0,0,0) rot=(1,0,0;1.5708rad)
  Profile = -> Sketch067
  Type = 0
FEATURE [PartDesign::Body] Body033  label="UtrustningsBoxBakkant-2"
  Group = -> [Sketch066,Pad033,Sketch067,Pocket029]
  Origin = -> Origin033
  Placement = pos=(-167,-302,0) rot=(0,0,1;0rad)
  Tip = -> Pocket029
FEATURE [Sketcher::SketchObject] Sketch068
  FullyConstrained = true
  MapMode = 5
  Support = -> [XY_Plane034]
  sketch-geometry (4):
    g0: LineSegment StartX=164 StartY=-100 StartZ=0 EndX=-164 EndY=-100 EndZ=0
    g1: LineSegment StartX=-164 StartY=-100 StartZ=0 EndX=-164 EndY=100 EndZ=0
    g2: LineSegment StartX=-164 StartY=100 StartZ=0 EndX=164 EndY=100 EndZ=0
    g3: LineSegment StartX=164 StartY=100 StartZ=0 EndX=164 EndY=-100 EndZ=0
  constraints (11):
    c: Coincident(g0,g1)
    c: Coincident(g1,g2)
    c: Coincident(g2,g3)
    c: Coincident(g3,g0)
    c: Horizontal(g0)
    c: Horizontal(g2)
    c: Vertical(g1)
    c: Vertical(g3)
    c: Symmetric(g1,g0,g-1)
    c: DistanceX(g1,g2) = 328
    c: DistanceY(g0,g1) = 200
FEATURE [PartDesign::Pad] Pad034
  Direction = (1,1,1)
  Length = 4
  Length2 = 100
  Profile = -> Sketch068
  Type = 0
FEATURE [Sketcher::SketchObject] Sketch069
  ExternalGeometry = -> [Pad034]
  FullyConstrained = true
  MapMode = 5
  Placement = pos=(0,0,4) rot=(0,0,1;0rad)
  Support = -> [Pad034]
  sketch-geometry (124):
    g0: LineSegment StartX=-164 StartY=100 StartZ=0 EndX=-156.55 EndY=100 EndZ=0
    g1: LineSegment StartX=-156.55 StartY=100 StartZ=0 EndX=-156.55 EndY=96 EndZ=0
    g2: LineSegment StartX=-156.55 StartY=96 StartZ=0 EndX=-164 EndY=96 EndZ=0
    g3: LineSegment StartX=-164 StartY=96 StartZ=0 EndX=-164 EndY=100 EndZ=0
    g4: LineSegment StartX=-141.64 StartY=100 StartZ=0 EndX=-126.73 EndY=100 EndZ=0
    g5: LineSegment StartX=-126.73 StartY=100 StartZ=0 EndX=-126.73 EndY=96 EndZ=0
    g6: LineSegment StartX=-126.73 StartY=96 StartZ=0 EndX=-141.64 EndY=96 EndZ=0
    g7: LineSegment StartX=-141.64 StartY=96 StartZ=0 EndX=-141.64 EndY=100 EndZ=0
    g8: LineSegment StartX=-111.82 StartY=100 StartZ=0 EndX=-96.91 EndY=100 EndZ=0
    g9: LineSegment StartX=-96.91 StartY=100 StartZ=0 EndX=-96.91 EndY=96 EndZ=0
    g10: LineSegment StartX=-96.91 StartY=96 StartZ=0 EndX=-111.82 EndY=96 EndZ=0
    g11: LineSegment StartX=-111.82 StartY=96 StartZ=0 EndX=-111.82 EndY=100 EndZ=0
    g12: LineSegment StartX=-82 StartY=100 StartZ=0 EndX=-67.09 EndY=100 EndZ=0
    g13: LineSegment StartX=-67.09 StartY=100 StartZ=0 EndX=-67.09 EndY=96 EndZ=0
    g14: LineSegment StartX=-67.09 StartY=96 StartZ=0 EndX=-82 EndY=96 EndZ=0
    g15: LineSegment StartX=-82 StartY=96 StartZ=0 EndX=-82 EndY=100 EndZ=0
    g16: LineSegment StartX=-52.18 StartY=100 StartZ=0 EndX=-37.27 EndY=100 EndZ=0
    g17: LineSegment StartX=-37.27 StartY=100 StartZ=0 EndX=-37.27 EndY=96 EndZ=0
    g18: LineSegment StartX=-37.27 StartY=96 StartZ=0 EndX=-52.18 EndY=96 EndZ=0
    g19: LineSegment StartX=-52.18 StartY=96 StartZ=0 EndX=-52.18 EndY=100 EndZ=0
    g20: LineSegment StartX=-22.36 StartY=100 StartZ=0 EndX=-7.45 EndY=100 EndZ=0
    g21: LineSegment StartX=-7.45 StartY=100 StartZ=0 EndX=-7.45 EndY=96 EndZ=0
    g22: LineSegment StartX=-7.45 StartY=96 StartZ=0 EndX=-22.36 EndY=96 EndZ=0
    g23: LineSegment StartX=-22.36 StartY=96 StartZ=0 EndX=-22.36 EndY=100 EndZ=0
    g24: LineSegment StartX=7.46 StartY=100 StartZ=0 EndX=22.37 EndY=100 EndZ=0
    g25: LineSegment StartX=22.37 StartY=100 StartZ=0 EndX=22.37 EndY=96 EndZ=0
    g26: LineSegment StartX=22.37 StartY=96 StartZ=0 EndX=7.46 EndY=96 EndZ=0
    g27: LineSegment StartX=7.46 StartY=96 StartZ=0 EndX=7.46 EndY=100 EndZ=0
    g28: LineSegment StartX=37.28 StartY=100 StartZ=0 EndX=52.19 EndY=100 EndZ=0
    g29: LineSegment StartX=52.19 StartY=100 StartZ=0 EndX=52.19 EndY=96 EndZ=0
    g30: LineSegment StartX=52.19 StartY=96 StartZ=0 EndX=37.28 EndY=96 EndZ=0
    g31: LineSegment StartX=37.28 StartY=96 StartZ=0 EndX=37.28 EndY=100 EndZ=0
    g32: LineSegment StartX=67.1 StartY=100 StartZ=0 EndX=82.01 EndY=100 EndZ=0
    g33: LineSegment StartX=82.01 StartY=100 StartZ=0 EndX=82.01 EndY=96 EndZ=0
    g34: LineSegment StartX=82.01 StartY=96 StartZ=0 EndX=67.1 EndY=96 EndZ=0
    g35: LineSegment StartX=67.1 StartY=96 StartZ=0 EndX=67.1 EndY=100 EndZ=0
    g36: LineSegment StartX=96.92 StartY=100 StartZ=0 EndX=111.83 EndY=100 EndZ=0
    g37: LineSegment StartX=111.83 StartY=100 StartZ=0 EndX=111.83 EndY=96 EndZ=0
    g38: LineSegment StartX=111.83 StartY=96 StartZ=0 EndX=96.92 EndY=96 EndZ=0
    g39: LineSegment StartX=96.92 StartY=96 StartZ=0 EndX=96.92 EndY=100 EndZ=0
    g40: LineSegment StartX=126.74 StartY=100 StartZ=0 EndX=141.65 EndY=100 EndZ=0
    g41: LineSegment StartX=141.65 StartY=100 StartZ=0 EndX=141.65 EndY=96 EndZ=0
    g42: LineSegment StartX=141.65 StartY=96 StartZ=0 EndX=126.74 EndY=96 EndZ=0
    g43: LineSegment StartX=126.74 StartY=96 StartZ=0 EndX=126.74 EndY=100 EndZ=0
    g44: LineSegment StartX=156.56 StartY=100 StartZ=0 EndX=164.01 EndY=100 EndZ=0
    g45: LineSegment StartX=164.01 StartY=100 StartZ=0 EndX=164.01 EndY=96 EndZ=0
    g46: LineSegment StartX=164.01 StartY=96 StartZ=0 EndX=156.56 EndY=96 EndZ=0
    g47: LineSegment StartX=156.56 StartY=96 StartZ=0 EndX=156.56 EndY=100 EndZ=0
    g48: LineSegment StartX=-164 StartY=89 StartZ=0 EndX=-160 EndY=89 EndZ=0
    g49: LineSegment StartX=-160 StartY=89 StartZ=0 EndX=-160 EndY=75 EndZ=0
    g50: LineSegment StartX=-160 StartY=75 StartZ=0 EndX=-164 EndY=75 EndZ=0
    g51: LineSegment StartX=-164 StartY=75 StartZ=0 EndX=-164 EndY=89 EndZ=0
    g52: LineSegment StartX=-164 StartY=61 StartZ=0 EndX=-160 EndY=61 EndZ=0
    g53: LineSegment StartX=-160 StartY=61 StartZ=0 EndX=-160 EndY=47 EndZ=0
    g54: LineSegment StartX=-160 StartY=47 StartZ=0 EndX=-164 EndY=47 EndZ=0
    g55: LineSegment StartX=-164 StartY=47 StartZ=0 EndX=-164 EndY=61 EndZ=0
    g56: LineSegment StartX=-164 StartY=33 StartZ=0 EndX=-160 EndY=33 EndZ=0
    g57: LineSegment StartX=-160 StartY=33 StartZ=0 EndX=-160 EndY=19 EndZ=0
    g58: LineSegment StartX=-160 StartY=19 StartZ=0 EndX=-164 EndY=19 EndZ=0
    g59: LineSegment StartX=-164 StartY=19 StartZ=0 EndX=-164 EndY=33 EndZ=0
    g60: LineSegment StartX=-164 StartY=5 StartZ=0 EndX=-160 EndY=5 EndZ=0
    g61: LineSegment StartX=-160 StartY=5 StartZ=0 EndX=-160 EndY=-9 EndZ=0
    g62: LineSegment StartX=-160 StartY=-9 StartZ=0 EndX=-164 EndY=-9 EndZ=0
    g63: LineSegment StartX=-164 StartY=-9 StartZ=0 EndX=-164 EndY=5 EndZ=0
    g64: LineSegment StartX=-164 StartY=-23 StartZ=0 EndX=-160 EndY=-23 EndZ=0
    g65: LineSegment StartX=-160 StartY=-23 StartZ=0 EndX=-160 EndY=-37 EndZ=0
    g66: LineSegment StartX=-160 StartY=-37 StartZ=0 EndX=-164 EndY=-37 EndZ=0
    g67: LineSegment StartX=-164 StartY=-37 StartZ=0 EndX=-164 EndY=-23 EndZ=0
    g68: LineSegment StartX=-164 StartY=-51 StartZ=0 EndX=-160 EndY=-51 EndZ=0
    g69: LineSegment StartX=-160 StartY=-51 StartZ=0 EndX=-160 EndY=-65 EndZ=0
    g70: LineSegment StartX=-160 StartY=-65 StartZ=0 EndX=-164 EndY=-65 EndZ=0
    g71: LineSegment StartX=-164 StartY=-65 StartZ=0 EndX=-164 EndY=-51 EndZ=0
    g72: LineSegment StartX=-164 StartY=-79 StartZ=0 EndX=-160 EndY=-79 EndZ=0
    g73: LineSegment StartX=-160 StartY=-79 StartZ=0 EndX=-160 EndY=-93 EndZ=0
    g74: LineSegment StartX=-160 StartY=-93 StartZ=0 EndX=-164 EndY=-93 EndZ=0
    g75: LineSegment StartX=-164 StartY=-93 StartZ=0 EndX=-164 EndY=-79 EndZ=0
    g76: LineSegment StartX=160 StartY=89 StartZ=0 EndX=164 EndY=89 EndZ=0
    g77: LineSegment StartX=164 StartY=89 StartZ=0 EndX=164 EndY=75 EndZ=0
    g78: LineSegment StartX=164 StartY=75 StartZ=0 EndX=160 EndY=75 EndZ=0
    g79: LineSegment StartX=160 StartY=75 StartZ=0 EndX=160 EndY=89 EndZ=0
    g80: LineSegment StartX=160 StartY=61 StartZ=0 EndX=164 EndY=61 EndZ=0
    g81: LineSegment StartX=164 StartY=61 StartZ=0 EndX=164 EndY=47 EndZ=0
    g82: LineSegment StartX=164 StartY=47 StartZ=0 EndX=160 EndY=47 EndZ=0
    g83: LineSegment StartX=160 StartY=47 StartZ=0 EndX=160 EndY=61 EndZ=0
    g84: LineSegment StartX=160 StartY=33 StartZ=0 EndX=164 EndY=33 EndZ=0
    g85: LineSegment StartX=164 StartY=33 StartZ=0 EndX=164 EndY=19 EndZ=0
    g86: LineSegment StartX=164 StartY=19 StartZ=0 EndX=160 EndY=19 EndZ=0
    g87: LineSegment StartX=160 StartY=19 StartZ=0 EndX=160 EndY=33 EndZ=0
    g88: LineSegment StartX=160 StartY=5 StartZ=0 EndX=164 EndY=5 EndZ=0
    g89: LineSegment StartX=164 StartY=5 StartZ=0 EndX=164 EndY=-9 EndZ=0
    g90: LineSegment StartX=164 StartY=-9 StartZ=0 EndX=160 EndY=-9 EndZ=0
    g91: LineSegment StartX=160 StartY=-9 StartZ=0 EndX=160 EndY=5 EndZ=0
    g92: LineSegment StartX=160 StartY=-23 StartZ=0 EndX=164 EndY=-23 EndZ=0
    g93: LineSegment StartX=164 StartY=-23 StartZ=0 EndX=164 EndY=-37 EndZ=0
    g94: LineSegment StartX=164 StartY=-37 StartZ=0 EndX=160 EndY=-37 EndZ=0
    g95: LineSegment StartX=160 StartY=-37 StartZ=0 EndX=160 EndY=-23 EndZ=0
    g96: LineSegment StartX=160 StartY=-51 StartZ=0 EndX=164 EndY=-51 EndZ=0
    g97: LineSegment StartX=164 StartY=-51 StartZ=0 EndX=164 EndY=-65 EndZ=0
    g98: LineSegment StartX=164 StartY=-65 StartZ=0 EndX=160 EndY=-65 EndZ=0
    g99: LineSegment StartX=160 StartY=-65 StartZ=0 EndX=160 EndY=-51 EndZ=0
    g100: LineSegment StartX=160 StartY=-79 StartZ=0 EndX=164 EndY=-79 EndZ=0
    g101: LineSegment StartX=164 StartY=-79 StartZ=0 EndX=164 EndY=-93 EndZ=0
    g102: LineSegment StartX=164 StartY=-93 StartZ=0 EndX=160 EndY=-93 EndZ=0
    g103: LineSegment StartX=160 StartY=-93 StartZ=0 EndX=160 EndY=-79 EndZ=0
    g104: Circle CenterX=0 CenterY=75 CenterZ=0 NormalX=0 NormalY=0 NormalZ=1 AngleXU=0 Radius=10
    g105: Circle CenterX=0 CenterY=25 CenterZ=0 NormalX=0 NormalY=0 NormalZ=1 AngleXU=0 Radius=10
    g106: Circle CenterX=0 CenterY=-25 CenterZ=0 NormalX=0 NormalY=0 NormalZ=1 AngleXU=0 Radius=10
    g107: Circle CenterX=0 CenterY=-75 CenterZ=0 NormalX=0 NormalY=0 NormalZ=1 AngleXU=0 Radius=10
    g108: Circle CenterX=54.7 CenterY=75 CenterZ=0 NormalX=0 NormalY=0 NormalZ=1 AngleXU=0 Radius=10
    g109: Circle CenterX=54.7 CenterY=25 CenterZ=0 NormalX=0 NormalY=0 NormalZ=1 AngleXU=0 Radius=10
    g110: Circle CenterX=54.7 CenterY=-25 CenterZ=0 NormalX=0 NormalY=0 NormalZ=1 AngleXU=0 Radius=10
    g111: Circle CenterX=54.7 CenterY=-75 CenterZ=0 NormalX=0 NormalY=0 NormalZ=1 AngleXU=0 Radius=10
    g112: Circle CenterX=109.4 CenterY=75 CenterZ=0 NormalX=0 NormalY=0 NormalZ=1 AngleXU=0 Radius=10
    g113: Circle CenterX=109.4 CenterY=25 CenterZ=0 NormalX=0 NormalY=0 NormalZ=1 AngleXU=0 Radius=10
    g114: Circle CenterX=109.4 CenterY=-25 CenterZ=0 NormalX=0 NormalY=0 NormalZ=1 AngleXU=0 Radius=10
    g115: Circle CenterX=109.4 CenterY=-75 CenterZ=0 NormalX=0 NormalY=0 NormalZ=1 AngleXU=0 Radius=10
    g116: Circle CenterX=-109.4 CenterY=75 CenterZ=0 NormalX=0 NormalY=0 NormalZ=1 AngleXU=0 Radius=10
    g117: Circle CenterX=-109.4 CenterY=25 CenterZ=0 NormalX=0 NormalY=0 NormalZ=1 AngleXU=0 Radius=10
    g118: Circle CenterX=-109.4 CenterY=-25 CenterZ=0 NormalX=0 NormalY=0 NormalZ=1 AngleXU=0 Radius=10
    g119: Circle CenterX=-109.4 CenterY=-75 CenterZ=0 NormalX=0 NormalY=0 NormalZ=1 AngleXU=0 Radius=10
    g120: Circle CenterX=-54.7 CenterY=75 CenterZ=0 NormalX=0 NormalY=0 NormalZ=1 AngleXU=0 Radius=10
    g121: Circle CenterX=-54.7 CenterY=25 CenterZ=0 NormalX=0 NormalY=0 NormalZ=1 AngleXU=0 Radius=10
    g122: Circle CenterX=-54.7 CenterY=-25 CenterZ=0 NormalX=0 NormalY=0 NormalZ=1 AngleXU=0 Radius=10
    g123: Circle CenterX=-54.7 CenterY=-75 CenterZ=0 NormalX=0 NormalY=0 NormalZ=1 AngleXU=0 Radius=10
  constraints (372):
    c: Coincident(g0,g1)
    c: Coincident(g1,g2)
    c: Coincident(g2,g3)
    c: Coincident(g3,g0)
    c: Horizontal(g0)
    c: Horizontal(g2)
    c: Vertical(g1)
    c: Vertical(g3)
    c: Coincident(g4,g5)
    c: Coincident(g5,g6)
    c: Coincident(g6,g7)
    c: Coincident(g7,g4)
    c: Horizontal(g4)
    c: Horizontal(g6)
    c: Vertical(g5)
    c: Vertical(g7)
    c: Coincident(g8,g9)
    c: Coincident(g9,g10)
    c: Coincident(g10,g11)
    c: Coincident(g11,g8)
    c: Horizontal(g8)
    c: Horizontal(g10)
    c: Vertical(g9)
    c: Vertical(g11)
    c: Coincident(g12,g13)
    c: Coincident(g13,g14)
    c: Coincident(g14,g15)
    c: Coincident(g15,g12)
    c: Horizontal(g12)
    c: Horizontal(g14)
    c: Vertical(g13)
    c: Vertical(g15)
    c: Coincident(g16,g17)
    c: Coincident(g17,g18)
    c: Coincident(g18,g19)
    c: Coincident(g19,g16)
    c: Horizontal(g16)
    c: Horizontal(g18)
    c: Vertical(g17)
    c: Vertical(g19)
    c: Coincident(g20,g21)
    c: Coincident(g21,g22)
    c: Coincident(g22,g23)
    c: Coincident(g23,g20)
    c: Horizontal(g20)
    c: Horizontal(g22)
    c: Vertical(g21)
    c: Vertical(g23)
    c: Horizontal(g0,g4)
    c: Horizontal(g4,g8)
    c: Horizontal(g8,g12)
    c: Horizontal(g12,g16)
    c: Horizontal(g16,g20)
    c: Horizontal(g1,g5)
    c: Horizontal(g5,g9)
    c: Horizontal(g9,g13)
    c: Horizontal(g13,g17)
    c: Horizontal(g17,g21)
    c: PointOnObject(g0,g-4)
    c: PointOnObject(g0,g-5)
    c: DistanceX(g0,g0) = 7.45
    c: DistanceX(g0,g4) = 14.91
    c: DistanceX(g4,g4) = 14.91
    c: Equal(g4,g8)
    c: Equal(g8,g12)
    c: Equal(g12,g16)
    c: Equal(g20,g16)
    c: DistanceX(g16,g20) = 14.91
    c: DistanceX(g12,g16) = 14.91
    c: DistanceX(g4,g8) = 14.91
    c: DistanceX(g8,g12) = 14.91
    c: Coincident(g24,g25)
    c: Coincident(g25,g26)
    c: Coincident(g26,g27)
    c: Coincident(g27,g24)
    c: Horizontal(g24)
    c: Horizontal(g26)
    c: Vertical(g25)
    c: Vertical(g27)
    c: Coincident(g28,g29)
    c: Coincident(g29,g30)
    c: Coincident(g30,g31)
    c: Coincident(g31,g28)
    c: Horizontal(g28)
    c: Horizontal(g30)
    c: Vertical(g29)
    c: Vertical(g31)
    c: Coincident(g32,g33)
    c: Coincident(g33,g34)
    c: Coincident(g34,g35)
    c: Coincident(g35,g32)
    c: Horizontal(g32)
    c: Horizontal(g34)
    c: Vertical(g33)
    c: Vertical(g35)
    c: Coincident(g36,g37)
    c: Coincident(g37,g38)
    c: Coincident(g38,g39)
    c: Coincident(g39,g36)
    c: Horizontal(g36)
    c: Horizontal(g38)
    c: Vertical(g37)
    c: Vertical(g39)
    c: Horizontal(g24,g28)
    c: Horizontal(g28,g32)
    c: Horizontal(g32,g36)
    c: Horizontal(g25,g29)
    c: Horizontal(g29,g33)
    c: Horizontal(g33,g37)
    c: Equal(g24,g28)
    c: Equal(g28,g32)
    c: Equal(g36,g32)
    c: DistanceX(g32,g36) = 14.91
    c: DistanceX(g28,g32) = 14.91
    c: DistanceX(g24,g28) = 14.91
    c: DistanceX(g20,g24) = 14.91
    c: Horizontal(g24,g20)
    c: Horizontal(g21,g26)
    c: Equal(g22,g26)
    c: Coincident(g40,g41)
    c: Coincident(g41,g42)
    c: Coincident(g42,g43)
    c: Coincident(g43,g40)
    c: Horizontal(g40)
    c: Horizontal(g42)
    c: Vertical(g41)
    c: Vertical(g43)
    c: Horizontal(g42,g37)
    c: Horizontal(g40,g36)
    c: Equal(g36,g40)
    c: DistanceX(g36,g40) = 14.91
    c: Coincident(g44,g45)
    c: Coincident(g45,g46)
    c: Coincident(g46,g47)
    c: Coincident(g47,g44)
    c: Horizontal(g44)
    c: Horizontal(g46)
    c: Vertical(g45)
    c: Vertical(g47)
    c: Horizontal(g40,g44)
    c: Horizontal(g41,g46)
    c: DistanceX(g40,g44) = 14.91
    c: DistanceX(g44,g44) = 7.45
    c: DistanceY(g2,g0) = 4
    c: Coincident(g48,g49)
    c: Coincident(g49,g50)
    c: Coincident(g50,g51)
    c: Coincident(g51,g48)
    c: Horizontal(g48)
    c: Horizontal(g50)
    c: Vertical(g49)
    c: Vertical(g51)
    c: PointOnObject(g48,g-5)
    c: Coincident(g52,g53)
    c: Coincident(g53,g54)
    c: Coincident(g54,g55)
    c: Coincident(g55,g52)
    c: Horizontal(g52)
    c: Horizontal(g54)
    c: Vertical(g53)
    c: Vertical(g55)
    c: PointOnObject(g52,g-5)
    c: Coincident(g56,g57)
    c: Coincident(g57,g58)
    c: Coincident(g58,g59)
    c: Coincident(g59,g56)
    c: Horizontal(g56)
    c: Horizontal(g58)
    c: Vertical(g57)
    c: Vertical(g59)
    c: PointOnObject(g56,g-5)
    c: Coincident(g60,g61)
    c: Coincident(g61,g62)
    c: Coincident(g62,g63)
    c: Coincident(g63,g60)
    c: Horizontal(g60)
    c: Horizontal(g62)
    c: Vertical(g61)
    c: Vertical(g63)
    c: PointOnObject(g60,g-5)
    c: Coincident(g64,g65)
    c: Coincident(g65,g66)
    c: Coincident(g66,g67)
    c: Coincident(g67,g64)
    c: Horizontal(g64)
    c: Horizontal(g66)
    c: Vertical(g65)
    c: Vertical(g67)
    c: PointOnObject(g64,g-5)
    c: Vertical(g53,g49)
    c: Vertical(g49,g57)
    c: Vertical(g57,g61)
    c: DistanceY(g48,g2) = 7
    c: DistanceY(g50,g48) = 14
    c: Equal(g49,g53)
    c: Equal(g53,g57)
    c: Equal(g57,g61)
    c: Equal(g61,g65)
    c: DistanceY(g52,g50) = 14
    c: DistanceY(g56,g54) = 14
    c: DistanceY(g60,g58) = 14
    c: DistanceY(g64,g62) = 14
    c: Coincident(g68,g69)
    c: Coincident(g69,g70)
    c: Coincident(g70,g71)
    c: Coincident(g71,g68)
    c: Horizontal(g68)
    c: Horizontal(g70)
    c: Vertical(g69)
    c: Vertical(g71)
    c: Coincident(g72,g73)
    c: Coincident(g73,g74)
    c: Coincident(g74,g75)
    c: Coincident(g75,g72)
    c: Horizontal(g72)
    c: Horizontal(g74)
    c: Vertical(g73)
    c: Vertical(g75)
    c: Equal(g69,g73)
    c: DistanceY(g72,g70) = 14
    c: PointOnObject(g74,g-5)
    c: PointOnObject(g70,g-5)
    c: Vertical(g65,g68)
    c: Vertical(g61,g64)
    c: DistanceY(g68,g66) = 14
    c: Equal(g69,g65)
    c: DistanceX(g48,g48) = 4
    c: Vertical(g69,g72)
    c: Coincident(g76,g77)
    c: Coincident(g77,g78)
    c: Coincident(g78,g79)
    c: Coincident(g79,g76)
    c: Horizontal(g76)
    c: Horizontal(g78)
    c: Vertical(g77)
    c: Vertical(g79)
    c: Coincident(g80,g81)
    c: Coincident(g81,g82)
    c: Coincident(g82,g83)
    c: Coincident(g83,g80)
    c: Horizontal(g80)
    c: Horizontal(g82)
    c: Vertical(g81)
    c: Vertical(g83)
    c: Coincident(g84,g85)
    c: Coincident(g85,g86)
    c: Coincident(g86,g87)
    c: Coincident(g87,g84)
    c: Horizontal(g84)
    c: Horizontal(g86)
    c: Vertical(g85)
    c: Vertical(g87)
    c: Coincident(g88,g89)
    c: Coincident(g89,g90)
    c: Coincident(g90,g91)
    c: Coincident(g91,g88)
    c: Horizontal(g88)
    c: Horizontal(g90)
    c: Vertical(g89)
    c: Vertical(g91)
    c: Coincident(g92,g93)
    c: Coincident(g93,g94)
    c: Coincident(g94,g95)
    c: Coincident(g95,g92)
    c: Horizontal(g92)
    c: Horizontal(g94)
    c: Vertical(g93)
    c: Vertical(g95)
    c: Vertical(g81,g77)
    c: Vertical(g77,g85)
    c: Vertical(g85,g89)
    c: DistanceY(g78,g76) = 14
    c: Equal(g77,g81)
    c: Equal(g81,g85)
    c: Equal(g85,g89)
    c: Equal(g89,g93)
    c: DistanceY(g80,g78) = 14
    c: DistanceY(g84,g82) = 14
    c: DistanceY(g88,g86) = 14
    c: DistanceY(g92,g90) = 14
    c: Coincident(g96,g97)
    c: Coincident(g97,g98)
    c: Coincident(g98,g99)
    c: Coincident(g99,g96)
    c: Horizontal(g96)
    c: Horizontal(g98)
    c: Vertical(g97)
    c: Vertical(g99)
    c: Coincident(g100,g101)
    c: Coincident(g101,g102)
    c: Coincident(g102,g103)
    c: Coincident(g103,g100)
    c: Horizontal(g100)
    c: Horizontal(g102)
    c: Vertical(g101)
    c: Vertical(g103)
    c: Equal(g97,g101)
    c: DistanceY(g100,g98) = 14
    c: Vertical(g93,g96)
    c: Vertical(g89,g92)
    c: DistanceY(g96,g94) = 14
    c: Equal(g97,g93)
    c: Equal(g48,g76) = 4
    c: Vertical(g97,g100)
    c: Vertical(g80,g78)
    c: Vertical(g82,g86)
    c: Vertical(g86,g90)
    c: Vertical(g90,g94)
    c: Vertical(g94,g98)
    c: Vertical(g98,g102)
    c: DistanceY(g76,g45) = 7
    c: PointOnObject(g104,g-2)
    c: PointOnObject(g105,g-2)
    c: PointOnObject(g106,g-2)
    c: PointOnObject(g107,g-2)
    c: Radius(g107) = 10
    c: Equal(g107,g106)
    c: Equal(g106,g105)
    c: Equal(g105,g104)
    c: DistanceY(g106,g-1) = 25
    c: DistanceY(g107,g106) = 50
    c: DistanceY(g-1,g105) = 25
    c: DistanceY(g105,g104) = 50
    c: Equal(g107,g111) = 10
    c: Equal(g111,g110)
    c: Equal(g110,g109)
    c: Equal(g109,g108)
    c: DistanceY(g111,g110) = 50
    c: DistanceY(g109,g108) = 50
    c: DistanceY(g110,g109) = 50
    c: Vertical(g111,g110)
    c: Vertical(g110,g109)
    c: Vertical(g109,g108)
    c: Equal(g115,g114)
    c: Equal(g114,g113)
    c: Equal(g113,g112)
    c: DistanceY(g115,g114) = 50
    c: DistanceY(g113,g112) = 50
    c: DistanceY(g114,g113) = 50
    c: Vertical(g115,g114)
    c: Vertical(g114,g113)
    c: Vertical(g113,g112)
    c: DistanceX(g107,g111) = 54.7
    c: DistanceX(g111,g115) = 54.7
    c: Horizontal(g107,g111)
    c: Horizontal(g111,g115)
    c: Radius(g115) = 10
    c: Equal(g119,g118)
    c: Equal(g118,g117)
    c: Equal(g117,g116)
    c: DistanceY(g119,g118) = 50
    c: DistanceY(g117,g116) = 50
    c: DistanceY(g118,g117) = 50
    c: Vertical(g119,g118)
    c: Vertical(g118,g117)
    c: Vertical(g117,g116)
    c: Equal(g123,g122)
    c: Equal(g122,g121)
    c: Equal(g121,g120)
    c: DistanceY(g123,g122) = 50
    c: DistanceY(g121,g120) = 50
    c: DistanceY(g122,g121) = 50
    c: Vertical(g123,g122)
    c: Vertical(g122,g121)
    c: Vertical(g121,g120)
    c: DistanceX(g119,g123) = 54.7
    c: Horizontal(g119,g123)
    c: Equal(g115,g123) = 10
    c: Horizontal(g107,g123)
    c: DistanceX(g123,g107) = 54.7
    c: Radius(g119) = 10
    c: PointOnObject(g76,g-6)
FEATURE [PartDesign::Pocket] Pocket030
  BaseFeature = -> Pad034
  Length = 4
  Length2 = 100
  Profile = -> Sketch069
  Type = 0
FEATURE [PartDesign::Body] Body034  label="UtrustningsBoxBotten-2"
  Group = -> [Sketch068,Pad034,Sketch069,Pocket030]
  Origin = -> Origin034
  Placement = pos=(-167,-402,-45) rot=(0,0,1;0rad)
  Tip = -> Pocket030
FEATURE [Sketcher::SketchObject] Sketch071
  FullyConstrained = true
  MapMode = 5
  Placement = pos=(0,0,0) rot=(0.57735,0.57735,0.57735;2.0944rad)
  Support = -> [YZ_Plane035]
  sketch-geometry (4):
    g0: LineSegment StartX=-100 StartY=-45 StartZ=0 EndX=100 EndY=-45 EndZ=0
    g1: LineSegment StartX=100 StartY=-45 StartZ=0 EndX=100 EndY=45 EndZ=0
    g2: LineSegment StartX=100 StartY=45 StartZ=0 EndX=-100 EndY=45 EndZ=0
    g3: LineSegment StartX=-100 StartY=45 StartZ=0 EndX=-100 EndY=-45 EndZ=0
  constraints (11):
    c: Coincident(g0,g1)
    c: Coincident(g1,g2)
    c: Coincident(g2,g3)
    c: Coincident(g3,g0)
    c: Horizontal(g0)
    c: Horizontal(g2)
    c: Vertical(g1)
    c: Vertical(g3)
    c: Symmetric(g0,g2,g-1)
    c: DistanceX(g0,g0) = 200
    c: DistanceY(g0,g2) = 90
FEATURE [PartDesign::Pad] Pad035
  Direction = (1,1,1)
  Length = 4
  Length2 = 100
  Placement = pos=(0,0,0) rot=(0.57735,0.57735,0.57735;2.0944rad)
  Profile = -> Sketch071
  Type = 0
FEATURE [Sketcher::SketchObject] Sketch070
  ExternalGeometry = -> [Pad035]
  FullyConstrained = true
  MapMode = 5
  Placement = pos=(4,-9e-16,9e-16) rot=(0.57735,0.57735,0.57735;2.0944rad)
  Support = -> [Pad035]
  sketch-geometry (48):
    g0: LineSegment StartX=-93 StartY=-45 StartZ=0 EndX=-100 EndY=-45 EndZ=0
    g1: LineSegment StartX=-100 StartY=-45 StartZ=0 EndX=-100 EndY=-41 EndZ=0
    g2: LineSegment StartX=-100 StartY=-41 StartZ=0 EndX=-93 EndY=-41 EndZ=0
    g3: LineSegment StartX=-93 StartY=-41 StartZ=0 EndX=-93 EndY=-45 EndZ=0
    g4: LineSegment StartX=-79 StartY=-45 StartZ=0 EndX=-65 EndY=-45 EndZ=0
    g5: LineSegment StartX=-65 StartY=-45 StartZ=0 EndX=-65 EndY=-41 EndZ=0
    g6: LineSegment StartX=-65 StartY=-41 StartZ=0 EndX=-79 EndY=-41 EndZ=0
    g7: LineSegment StartX=-79 StartY=-41 StartZ=0 EndX=-79 EndY=-45 EndZ=0
    g8: LineSegment StartX=-51 StartY=-45 StartZ=0 EndX=-37 EndY=-45 EndZ=0
    g9: LineSegment StartX=-37 StartY=-45 StartZ=0 EndX=-37 EndY=-41 EndZ=0
    g10: LineSegment StartX=-37 StartY=-41 StartZ=0 EndX=-51 EndY=-41 EndZ=0
    g11: LineSegment StartX=-51 StartY=-41 StartZ=0 EndX=-51 EndY=-45 EndZ=0
    g12: LineSegment StartX=-23 StartY=-45 StartZ=0 EndX=-9 EndY=-45 EndZ=0
    g13: LineSegment StartX=-9 StartY=-45 StartZ=0 EndX=-9 EndY=-41 EndZ=0
    g14: LineSegment StartX=-9 StartY=-41 StartZ=0 EndX=-23 EndY=-41 EndZ=0
    g15: LineSegment StartX=-23 StartY=-41 StartZ=0 EndX=-23 EndY=-45 EndZ=0
    g16: LineSegment StartX=5 StartY=-45 StartZ=0 EndX=19 EndY=-45 EndZ=0
    g17: LineSegment StartX=19 StartY=-45 StartZ=0 EndX=19 EndY=-41 EndZ=0
    g18: LineSegment StartX=19 StartY=-41 StartZ=0 EndX=5 EndY=-41 EndZ=0
    g19: LineSegment StartX=5 StartY=-41 StartZ=0 EndX=5 EndY=-45 EndZ=0
    g20: LineSegment StartX=33 StartY=-45 StartZ=0 EndX=47 EndY=-45 EndZ=0
    g21: LineSegment StartX=47 StartY=-45 StartZ=0 EndX=47 EndY=-41 EndZ=0
    g22: LineSegment StartX=47 StartY=-41 StartZ=0 EndX=33 EndY=-41 EndZ=0
    g23: LineSegment StartX=33 StartY=-41 StartZ=0 EndX=33 EndY=-45 EndZ=0
    g24: LineSegment StartX=61 StartY=-45 StartZ=0 EndX=75 EndY=-45 EndZ=0
    g25: LineSegment StartX=75 StartY=-45 StartZ=0 EndX=75 EndY=-41 EndZ=0
    g26: LineSegment StartX=75 StartY=-41 StartZ=0 EndX=61 EndY=-41 EndZ=0
    g27: LineSegment StartX=61 StartY=-41 StartZ=0 EndX=61 EndY=-45 EndZ=0
    g28: LineSegment StartX=100 StartY=-22.5 StartZ=0 EndX=96 EndY=-22.5 EndZ=0
    g29: LineSegment StartX=96 StartY=-22.5 StartZ=0 EndX=96 EndY=-7.5 EndZ=0
    g30: LineSegment StartX=96 StartY=-7.5 StartZ=0 EndX=100 EndY=-7.5 EndZ=0
    g31: LineSegment StartX=100 StartY=-7.5 StartZ=0 EndX=100 EndY=-22.5 EndZ=0
    g32: LineSegment StartX=100 StartY=7.5 StartZ=0 EndX=96 EndY=7.5 EndZ=0
    g33: LineSegment StartX=96 StartY=7.5 StartZ=0 EndX=96 EndY=22.5 EndZ=0
    g34: LineSegment StartX=96 StartY=22.5 StartZ=0 EndX=100 EndY=22.5 EndZ=0
    g35: LineSegment StartX=100 StartY=22.5 StartZ=0 EndX=100 EndY=7.5 EndZ=0
    g36: LineSegment StartX=100 StartY=37.5 StartZ=0 EndX=96 EndY=37.5 EndZ=0
    g37: LineSegment StartX=96 StartY=37.5 StartZ=0 EndX=96 EndY=45 EndZ=0
    g38: LineSegment StartX=96 StartY=45 StartZ=0 EndX=100 EndY=45 EndZ=0
    g39: LineSegment StartX=100 StartY=45 StartZ=0 EndX=100 EndY=37.5 EndZ=0
    g40: LineSegment StartX=89 StartY=-45 StartZ=0 EndX=89 EndY=-41 EndZ=0
    g41: LineSegment StartX=89 StartY=-41 StartZ=0 EndX=96 EndY=-41 EndZ=0
    g42: LineSegment StartX=96 StartY=-41 StartZ=0 EndX=96 EndY=-37.5 EndZ=0
    g43: LineSegment StartX=96 StartY=-37.5 StartZ=0 EndX=100 EndY=-37.5 EndZ=0
    g44: LineSegment StartX=100 StartY=-37.5 StartZ=0 EndX=100 EndY=-45 EndZ=0
    g45: LineSegment StartX=100 StartY=-45 StartZ=0 EndX=89 EndY=-45 EndZ=0
    g46: Circle CenterX=-23 CenterY=0 CenterZ=0 NormalX=0 NormalY=0 NormalZ=1 AngleXU=0 Radius=25
    g47: Circle CenterX=47 CenterY=0 CenterZ=0 NormalX=0 NormalY=0 NormalZ=1 AngleXU=0 Radius=25
  constraints (143):
    c: Coincident(g0,g1)
    c: Coincident(g1,g2)
    c: Coincident(g2,g3)
    c: Coincident(g3,g0)
    c: Horizontal(g0)
    c: Horizontal(g2)
    c: Vertical(g1)
    c: Vertical(g3)
    c: PointOnObject(g1,g-4)
    c: Coincident(g4,g5)
    c: Coincident(g5,g6)
    c: Coincident(g6,g7)
    c: Coincident(g7,g4)
    c: Horizontal(g4)
    c: Horizontal(g6)
    c: Vertical(g5)
    c: Vertical(g7)
    c: Coincident(g8,g9)
    c: Coincident(g9,g10)
    c: Coincident(g10,g11)
    c: Coincident(g11,g8)
    c: Horizontal(g8)
    c: Horizontal(g10)
    c: Vertical(g9)
    c: Vertical(g11)
    c: Coincident(g12,g13)
    c: Coincident(g13,g14)
    c: Coincident(g14,g15)
    c: Coincident(g15,g12)
    c: Horizontal(g12)
    c: Horizontal(g14)
    c: Vertical(g13)
    c: Vertical(g15)
    c: Coincident(g16,g17)
    c: Coincident(g17,g18)
    c: Coincident(g18,g19)
    c: Coincident(g19,g16)
    c: Horizontal(g16)
    c: Horizontal(g18)
    c: Vertical(g17)
    c: Vertical(g19)
    c: Coincident(g20,g21)
    c: Coincident(g21,g22)
    c: Coincident(g22,g23)
    c: Coincident(g23,g20)
    c: Horizontal(g20)
    c: Horizontal(g22)
    c: Vertical(g21)
    c: Vertical(g23)
    c: Coincident(g24,g25)
    c: Coincident(g25,g26)
    c: Coincident(g26,g27)
    c: Coincident(g27,g24)
    c: Horizontal(g24)
    c: Horizontal(g26)
    c: Vertical(g25)
    c: Vertical(g27)
    c: Horizontal(g2,g5)
    c: Horizontal(g5,g9)
    c: Horizontal(g9,g13)
    c: Horizontal(g13,g17)
    c: Horizontal(g17,g21)
    c: Horizontal(g21,g25)
    c: DistanceX(g0,g0) = 7
    c: DistanceX(g0,g4) = 14
    c: DistanceX(g4,g4) = 14
    c: Equal(g8,g4)
    c: Equal(g8,g12)
    c: Equal(g12,g16)
    c: Equal(g16,g20)
    c: Equal(g20,g24)
    c: DistanceX(g4,g8) = 14
    c: DistanceX(g8,g12) = 14
    c: DistanceX(g12,g16) = 14
    c: DistanceX(g16,g20) = 14
    c: DistanceX(g20,g24) = 14
    c: Coincident(g28,g29)
    c: Coincident(g29,g30)
    c: Coincident(g30,g31)
    c: Coincident(g31,g28)
    c: Horizontal(g28)
    c: Horizontal(g30)
    c: Vertical(g29)
    c: Vertical(g31)
    c: Coincident(g32,g33)
    c: Coincident(g33,g34)
    c: Coincident(g34,g35)
    c: Coincident(g35,g32)
    c: Horizontal(g32)
    c: Horizontal(g34)
    c: Vertical(g33)
    c: Vertical(g35)
    c: Coincident(g36,g37)
    c: Coincident(g37,g38)
    c: Coincident(g38,g39)
    c: Coincident(g39,g36)
    c: Horizontal(g36)
    c: Horizontal(g38)
    c: Vertical(g37)
    c: Vertical(g39)
    c: PointOnObject(g37,g-5)
    c: DistanceY(g36,g38) = 7.5
    c: DistanceY(g32,g34) = 15
    c: Equal(g35,g31)
    c: DistanceY(g30,g32) = 15
    c: Vertical(g36,g32)
    c: Vertical(g32,g28)
    c: DistanceY(g0,g1) = 4
    c: PointOnObject(g0,g-7)
    c: PointOnObject(g4,g-7)
    c: PointOnObject(g8,g-7)
    c: PointOnObject(g12,g-7)
    c: PointOnObject(g16,g-7)
    c: PointOnObject(g20,g-7)
    c: PointOnObject(g24,g-7)
    c: PointOnObject(g40,g-7)
    c: Coincident(g40,g41)
    c: Horizontal(g41)
    c: Coincident(g41,g42)
    c: Vertical(g42)
    c: Coincident(g42,g43)
    c: PointOnObject(g43,g-6)
    c: Horizontal(g43)
    c: Coincident(g43,g44)
    c: Coincident(g44,g-7)
    c: Coincident(g44,g45)
    c: Coincident(g45,g40)
    c: Parallel(g-6,g40)
    c: Horizontal(g40,g25)
    c: DistanceX(g40,g44) = 11
    c: DistanceY(g44,g43) = 7.5
    c: PointOnObject(g30,g-6)
    c: PointOnObject(g34,g-6)
    c: PointOnObject(g36,g-6)
    c: Vertical(g42,g28)
    c: DistanceX(g41,g44) = 4
    c: DistanceY(g43,g28) = 15
    c: PointOnObject(g46,g-1)
    c: Radius(g46) = 25
    c: DistanceX(g46,g44) = 123
    c: PointOnObject(g47,g-1)
    c: Radius(g47) = 25
    c: DistanceX(g46,g47) = 70
FEATURE [PartDesign::Pocket] Pocket031
  BaseFeature = -> Pad035
  Length = 4
  Length2 = 100
  Placement = pos=(0,0,0) rot=(0.57735,0.57735,0.57735;2.0944rad)
  Profile = -> Sketch070
  Type = 0
FEATURE [PartDesign::Fillet] Fillet002
  Base = -> Pocket031 [Edge98]
  BaseFeature = -> Pocket031
  Placement = pos=(0,0,0) rot=(0.57735,0.57735,0.57735;2.0944rad)
  Radius = 65
  SupportTransform = false
FEATURE [PartDesign::Body] Body035  label="UtrustningsBoxSida-V-2"
  Group = -> [Sketch071,Pad035,Sketch070,Pocket031,Fillet002]
  Origin = -> Origin035
  Placement = pos=(-331,-402,0) rot=(0,0,1;0rad)
  Tip = -> Fillet002
FEATURE [Sketcher::SketchObject] Sketch072
  FullyConstrained = true
  MapMode = 5
  Placement = pos=(0,0,0) rot=(0.57735,0.57735,0.57735;2.0944rad)
  Support = -> [YZ_Plane036]
  sketch-geometry (4):
    g0: LineSegment StartX=-100 StartY=-45 StartZ=0 EndX=100 EndY=-45 EndZ=0
    g1: LineSegment StartX=100 StartY=-45 StartZ=0 EndX=100 EndY=45 EndZ=0
    g2: LineSegment StartX=100 StartY=45 StartZ=0 EndX=-100 EndY=45 EndZ=0
    g3: LineSegment StartX=-100 StartY=45 StartZ=0 EndX=-100 EndY=-45 EndZ=0
  constraints (11):
    c: Coincident(g0,g1)
    c: Coincident(g1,g2)
    c: Coincident(g2,g3)
    c: Coincident(g3,g0)
    c: Horizontal(g0)
    c: Horizontal(g2)
    c: Vertical(g1)
    c: Vertical(g3)
    c: Symmetric(g0,g2,g-1)
    c: DistanceX(g0,g0) = 200
    c: DistanceY(g0,g2) = 90
FEATURE [PartDesign::Pad] Pad036
  Direction = (1,1,1)
  Length = 4
  Length2 = 100
  Placement = pos=(0,0,0) rot=(0.57735,0.57735,0.57735;2.0944rad)
  Profile = -> Sketch072
  Type = 0
FEATURE [Sketcher::SketchObject] Sketch073
  ExternalGeometry = -> [Pad036]
  FullyConstrained = true
  MapMode = 5
  Placement = pos=(4,-9e-16,9e-16) rot=(0.57735,0.57735,0.57735;2.0944rad)
  Support = -> [Pad036]
  sketch-geometry (48):
    g0: LineSegment StartX=-93 StartY=-45 StartZ=0 EndX=-100 EndY=-45 EndZ=0
    g1: LineSegment StartX=-100 StartY=-45 StartZ=0 EndX=-100 EndY=-41 EndZ=0
    g2: LineSegment StartX=-100 StartY=-41 StartZ=0 EndX=-93 EndY=-41 EndZ=0
    g3: LineSegment StartX=-93 StartY=-41 StartZ=0 EndX=-93 EndY=-45 EndZ=0
    g4: LineSegment StartX=-79 StartY=-45 StartZ=0 EndX=-65 EndY=-45 EndZ=0
    g5: LineSegment StartX=-65 StartY=-45 StartZ=0 EndX=-65 EndY=-41 EndZ=0
    g6: LineSegment StartX=-65 StartY=-41 StartZ=0 EndX=-79 EndY=-41 EndZ=0
    g7: LineSegment StartX=-79 StartY=-41 StartZ=0 EndX=-79 EndY=-45 EndZ=0
    g8: LineSegment StartX=-51 StartY=-45 StartZ=0 EndX=-37 EndY=-45 EndZ=0
    g9: LineSegment StartX=-37 StartY=-45 StartZ=0 EndX=-37 EndY=-41 EndZ=0
    g10: LineSegment StartX=-37 StartY=-41 StartZ=0 EndX=-51 EndY=-41 EndZ=0
    g11: LineSegment StartX=-51 StartY=-41 StartZ=0 EndX=-51 EndY=-45 EndZ=0
    g12: LineSegment StartX=-23 StartY=-45 StartZ=0 EndX=-9 EndY=-45 EndZ=0
    g13: LineSegment StartX=-9 StartY=-45 StartZ=0 EndX=-9 EndY=-41 EndZ=0
    g14: LineSegment StartX=-9 StartY=-41 StartZ=0 EndX=-23 EndY=-41 EndZ=0
    g15: LineSegment StartX=-23 StartY=-41 StartZ=0 EndX=-23 EndY=-45 EndZ=0
    g16: LineSegment StartX=5 StartY=-45 StartZ=0 EndX=19 EndY=-45 EndZ=0
    g17: LineSegment StartX=19 StartY=-45 StartZ=0 EndX=19 EndY=-41 EndZ=0
    g18: LineSegment StartX=19 StartY=-41 StartZ=0 EndX=5 EndY=-41 EndZ=0
    g19: LineSegment StartX=5 StartY=-41 StartZ=0 EndX=5 EndY=-45 EndZ=0
    g20: LineSegment StartX=33 StartY=-45 StartZ=0 EndX=47 EndY=-45 EndZ=0
    g21: LineSegment StartX=47 StartY=-45 StartZ=0 EndX=47 EndY=-41 EndZ=0
    g22: LineSegment StartX=47 StartY=-41 StartZ=0 EndX=33 EndY=-41 EndZ=0
    g23: LineSegment StartX=33 StartY=-41 StartZ=0 EndX=33 EndY=-45 EndZ=0
    g24: LineSegment StartX=61 StartY=-45 StartZ=0 EndX=75 EndY=-45 EndZ=0
    g25: LineSegment StartX=75 StartY=-45 StartZ=0 EndX=75 EndY=-41 EndZ=0
    g26: LineSegment StartX=75 StartY=-41 StartZ=0 EndX=61 EndY=-41 EndZ=0
    g27: LineSegment StartX=61 StartY=-41 StartZ=0 EndX=61 EndY=-45 EndZ=0
    g28: LineSegment StartX=100 StartY=-22.5 StartZ=0 EndX=96 EndY=-22.5 EndZ=0
    g29: LineSegment StartX=96 StartY=-22.5 StartZ=0 EndX=96 EndY=-7.5 EndZ=0
    g30: LineSegment StartX=96 StartY=-7.5 StartZ=0 EndX=100 EndY=-7.5 EndZ=0
    g31: LineSegment StartX=100 StartY=-7.5 StartZ=0 EndX=100 EndY=-22.5 EndZ=0
    g32: LineSegment StartX=100 StartY=7.5 StartZ=0 EndX=96 EndY=7.5 EndZ=0
    g33: LineSegment StartX=96 StartY=7.5 StartZ=0 EndX=96 EndY=22.5 EndZ=0
    g34: LineSegment StartX=96 StartY=22.5 StartZ=0 EndX=100 EndY=22.5 EndZ=0
    g35: LineSegment StartX=100 StartY=22.5 StartZ=0 EndX=100 EndY=7.5 EndZ=0
    g36: LineSegment StartX=100 StartY=37.5 StartZ=0 EndX=96 EndY=37.5 EndZ=0
    g37: LineSegment StartX=96 StartY=37.5 StartZ=0 EndX=96 EndY=45 EndZ=0
    g38: LineSegment StartX=96 StartY=45 StartZ=0 EndX=100 EndY=45 EndZ=0
    g39: LineSegment StartX=100 StartY=45 StartZ=0 EndX=100 EndY=37.5 EndZ=0
    g40: LineSegment StartX=89 StartY=-45 StartZ=0 EndX=89 EndY=-41 EndZ=0
    g41: LineSegment StartX=89 StartY=-41 StartZ=0 EndX=96 EndY=-41 EndZ=0
    g42: LineSegment StartX=96 StartY=-41 StartZ=0 EndX=96 EndY=-37.5 EndZ=0
    g43: LineSegment StartX=96 StartY=-37.5 StartZ=0 EndX=100 EndY=-37.5 EndZ=0
    g44: LineSegment StartX=100 StartY=-37.5 StartZ=0 EndX=100 EndY=-45 EndZ=0
    g45: LineSegment StartX=100 StartY=-45 StartZ=0 EndX=89 EndY=-45 EndZ=0
    g46: Circle CenterX=-23 CenterY=0 CenterZ=0 NormalX=0 NormalY=0 NormalZ=1 AngleXU=0 Radius=25
    g47: Circle CenterX=47 CenterY=0 CenterZ=0 NormalX=0 NormalY=0 NormalZ=1 AngleXU=0 Radius=25
  constraints (143):
    c: Coincident(g0,g1)
    c: Coincident(g1,g2)
    c: Coincident(g2,g3)
    c: Coincident(g3,g0)
    c: Horizontal(g0)
    c: Horizontal(g2)
    c: Vertical(g1)
    c: Vertical(g3)
    c: PointOnObject(g1,g-4)
    c: Coincident(g4,g5)
    c: Coincident(g5,g6)
    c: Coincident(g6,g7)
    c: Coincident(g7,g4)
    c: Horizontal(g4)
    c: Horizontal(g6)
    c: Vertical(g5)
    c: Vertical(g7)
    c: Coincident(g8,g9)
    c: Coincident(g9,g10)
    c: Coincident(g10,g11)
    c: Coincident(g11,g8)
    c: Horizontal(g8)
    c: Horizontal(g10)
    c: Vertical(g9)
    c: Vertical(g11)
    c: Coincident(g12,g13)
    c: Coincident(g13,g14)
    c: Coincident(g14,g15)
    c: Coincident(g15,g12)
    c: Horizontal(g12)
    c: Horizontal(g14)
    c: Vertical(g13)
    c: Vertical(g15)
    c: Coincident(g16,g17)
    c: Coincident(g17,g18)
    c: Coincident(g18,g19)
    c: Coincident(g19,g16)
    c: Horizontal(g16)
    c: Horizontal(g18)
    c: Vertical(g17)
    c: Vertical(g19)
    c: Coincident(g20,g21)
    c: Coincident(g21,g22)
    c: Coincident(g22,g23)
    c: Coincident(g23,g20)
    c: Horizontal(g20)
    c: Horizontal(g22)
    c: Vertical(g21)
    c: Vertical(g23)
    c: Coincident(g24,g25)
    c: Coincident(g25,g26)
    c: Coincident(g26,g27)
    c: Coincident(g27,g24)
    c: Horizontal(g24)
    c: Horizontal(g26)
    c: Vertical(g25)
    c: Vertical(g27)
    c: Horizontal(g2,g5)
    c: Horizontal(g5,g9)
    c: Horizontal(g9,g13)
    c: Horizontal(g13,g17)
    c: Horizontal(g17,g21)
    c: Horizontal(g21,g25)
    c: DistanceX(g0,g0) = 7
    c: DistanceX(g0,g4) = 14
    c: DistanceX(g4,g4) = 14
    c: Equal(g8,g4)
    c: Equal(g8,g12)
    c: Equal(g12,g16)
    c: Equal(g16,g20)
    c: Equal(g20,g24)
    c: DistanceX(g4,g8) = 14
    c: DistanceX(g8,g12) = 14
    c: DistanceX(g12,g16) = 14
    c: DistanceX(g16,g20) = 14
    c: DistanceX(g20,g24) = 14
    c: Coincident(g28,g29)
    c: Coincident(g29,g30)
    c: Coincident(g30,g31)
    c: Coincident(g31,g28)
    c: Horizontal(g28)
    c: Horizontal(g30)
    c: Vertical(g29)
    c: Vertical(g31)
    c: Coincident(g32,g33)
    c: Coincident(g33,g34)
    c: Coincident(g34,g35)
    c: Coincident(g35,g32)
    c: Horizontal(g32)
    c: Horizontal(g34)
    c: Vertical(g33)
    c: Vertical(g35)
    c: Coincident(g36,g37)
    c: Coincident(g37,g38)
    c: Coincident(g38,g39)
    c: Coincident(g39,g36)
    c: Horizontal(g36)
    c: Horizontal(g38)
    c: Vertical(g37)
    c: Vertical(g39)
    c: PointOnObject(g37,g-5)
    c: DistanceY(g36,g38) = 7.5
    c: DistanceY(g32,g34) = 15
    c: Equal(g35,g31)
    c: DistanceY(g30,g32) = 15
    c: Vertical(g36,g32)
    c: Vertical(g32,g28)
    c: DistanceY(g0,g1) = 4
    c: PointOnObject(g0,g-7)
    c: PointOnObject(g4,g-7)
    c: PointOnObject(g8,g-7)
    c: PointOnObject(g12,g-7)
    c: PointOnObject(g16,g-7)
    c: PointOnObject(g20,g-7)
    c: PointOnObject(g24,g-7)
    c: PointOnObject(g40,g-7)
    c: Coincident(g40,g41)
    c: Horizontal(g41)
    c: Coincident(g41,g42)
    c: Vertical(g42)
    c: Coincident(g42,g43)
    c: PointOnObject(g43,g-6)
    c: Horizontal(g43)
    c: Coincident(g43,g44)
    c: Coincident(g44,g-7)
    c: Coincident(g44,g45)
    c: Coincident(g45,g40)
    c: Parallel(g-6,g40)
    c: Horizontal(g40,g25)
    c: DistanceX(g40,g44) = 11
    c: DistanceY(g44,g43) = 7.5
    c: PointOnObject(g30,g-6)
    c: PointOnObject(g34,g-6)
    c: PointOnObject(g36,g-6)
    c: Vertical(g42,g28)
    c: DistanceX(g41,g44) = 4
    c: DistanceY(g43,g28) = 15
    c: PointOnObject(g46,g-1)
    c: Radius(g46) = 25
    c: DistanceX(g46,g44) = 123
    c: PointOnObject(g47,g-1)
    c: Radius(g47) = 25
    c: DistanceX(g46,g47) = 70
FEATURE [PartDesign::Pocket] Pocket032
  BaseFeature = -> Pad036
  Length = 4
  Length2 = 100
  Placement = pos=(0,0,0) rot=(0.57735,0.57735,0.57735;2.0944rad)
  Profile = -> Sketch073
  Type = 0
FEATURE [PartDesign::Fillet] Fillet003
  Base = -> Pocket032 [Edge98]
  BaseFeature = -> Pocket032
  Placement = pos=(0,0,0) rot=(0.57735,0.57735,0.57735;2.0944rad)
  Radius = 65
  SupportTransform = false
FEATURE [PartDesign::Body] Body036  label="UtrustningsBoxSida-H-2"
  Group = -> [Sketch072,Pad036,Sketch073,Pocket032,Fillet003]
  Origin = -> Origin036
  Placement = pos=(-7,-402,0) rot=(0,0,1;0rad)
  Tip = -> Fillet003
FEATURE [Sketcher::SketchObject] Sketch074
  FullyConstrained = true
  MapMode = 5
  Placement = pos=(0,0,0) rot=(1,0,0;1.5708rad)
  Support = -> [XZ_Plane037]
  sketch-geometry (4):
    g0: LineSegment StartX=-164 StartY=-45 StartZ=0 EndX=164 EndY=-45 EndZ=0
    g1: LineSegment StartX=164 StartY=-45 StartZ=0 EndX=164 EndY=45 EndZ=0
    g2: LineSegment StartX=164 StartY=45 StartZ=0 EndX=-164 EndY=45 EndZ=0
    g3: LineSegment StartX=-164 StartY=45 StartZ=0 EndX=-164 EndY=-45 EndZ=0
  constraints (11):
    c: Coincident(g0,g1)
    c: Coincident(g1,g2)
    c: Coincident(g2,g3)
    c: Coincident(g3,g0)
    c: Horizontal(g0)
    c: Horizontal(g2)
    c: Vertical(g1)
    c: Vertical(g3)
    c: Symmetric(g0,g1,g-1)
    c: DistanceX(g0,g0) = 328
    c: DistanceY(g0,g2) = 90
FEATURE [PartDesign::Pad] Pad037
  Direction = (1,1,1)
  Length = 4
  Length2 = 100
  Placement = pos=(0,0,0) rot=(1,0,0;1.5708rad)
  Profile = -> Sketch074
  Type = 0
FEATURE [Sketcher::SketchObject] Sketch075
  ExternalGeometry = -> [Pad037]
  FullyConstrained = true
  MapMode = 5
  Placement = pos=(0,-4,1.8e-15) rot=(1,0,0;1.5708rad)
  Support = -> [Pad037]
  sketch-geometry (71):
    g0: Circle CenterX=-83.33 CenterY=0 CenterZ=0 NormalX=0 NormalY=0 NormalZ=1 AngleXU=0 Radius=25
    g1: Circle CenterX=0 CenterY=0 CenterZ=0 NormalX=0 NormalY=0 NormalZ=1 AngleXU=0 Radius=25
    g2: Circle CenterX=83.33 CenterY=0 CenterZ=0 NormalX=0 NormalY=0 NormalZ=1 AngleXU=0 Radius=25
    g3: LineSegment StartX=-160 StartY=-37.5 StartZ=0 EndX=-164 EndY=-37.5 EndZ=0
    g4: LineSegment StartX=-164 StartY=-37.5 StartZ=0 EndX=-164 EndY=-22.5 EndZ=0
    g5: LineSegment StartX=-164 StartY=-22.5 StartZ=0 EndX=-160 EndY=-22.5 EndZ=0
    g6: LineSegment StartX=-160 StartY=-22.5 StartZ=0 EndX=-160 EndY=-37.5 EndZ=0
    g7: LineSegment StartX=-160 StartY=-7.5 StartZ=0 EndX=-164 EndY=-7.5 EndZ=0
    g8: LineSegment StartX=-164 StartY=-7.5 StartZ=0 EndX=-164 EndY=7.5 EndZ=0
    g9: LineSegment StartX=-164 StartY=7.5 StartZ=0 EndX=-160 EndY=7.5 EndZ=0
    g10: LineSegment StartX=-160 StartY=7.5 StartZ=0 EndX=-160 EndY=-7.5 EndZ=0
    g11: LineSegment StartX=-160 StartY=22.5 StartZ=0 EndX=-164 EndY=22.5 EndZ=0
    g12: LineSegment StartX=-164 StartY=22.5 StartZ=0 EndX=-164 EndY=37.5 EndZ=0
    g13: LineSegment StartX=-164 StartY=37.5 StartZ=0 EndX=-160 EndY=37.5 EndZ=0
    g14: LineSegment StartX=-160 StartY=37.5 StartZ=0 EndX=-160 EndY=22.5 EndZ=0
    g15: LineSegment StartX=160 StartY=-37.5 StartZ=0 EndX=164 EndY=-37.5 EndZ=0
    g16: LineSegment StartX=164 StartY=-37.5 StartZ=0 EndX=164 EndY=-22.5 EndZ=0
    g17: LineSegment StartX=164 StartY=-22.5 StartZ=0 EndX=160 EndY=-22.5 EndZ=0
    g18: LineSegment StartX=160 StartY=-22.5 StartZ=0 EndX=160 EndY=-37.5 EndZ=0
    g19: LineSegment StartX=160 StartY=-7.5 StartZ=0 EndX=164 EndY=-7.5 EndZ=0
    g20: LineSegment StartX=164 StartY=-7.5 StartZ=0 EndX=164 EndY=7.5 EndZ=0
    g21: LineSegment StartX=164 StartY=7.5 StartZ=0 EndX=160 EndY=7.5 EndZ=0
    g22: LineSegment StartX=160 StartY=7.5 StartZ=0 EndX=160 EndY=-7.5 EndZ=0
    g23: LineSegment StartX=160 StartY=22.5 StartZ=0 EndX=164 EndY=22.5 EndZ=0
    g24: LineSegment StartX=164 StartY=22.5 StartZ=0 EndX=164 EndY=37.5 EndZ=0
    g25: LineSegment StartX=164 StartY=37.5 StartZ=0 EndX=160 EndY=37.5 EndZ=0
    g26: LineSegment StartX=160 StartY=37.5 StartZ=0 EndX=160 EndY=22.5 EndZ=0
    g27: LineSegment StartX=-156.55 StartY=-41 StartZ=0 EndX=-141.64 EndY=-41 EndZ=0
    g28: LineSegment StartX=-141.64 StartY=-41 StartZ=0 EndX=-141.64 EndY=-45 EndZ=0
    g29: LineSegment StartX=-141.64 StartY=-45 StartZ=0 EndX=-156.55 EndY=-45 EndZ=0
    g30: LineSegment StartX=-156.55 StartY=-45 StartZ=0 EndX=-156.55 EndY=-41 EndZ=0
    g31: LineSegment StartX=-126.73 StartY=-41 StartZ=0 EndX=-111.82 EndY=-41 EndZ=0
    g32: LineSegment StartX=-111.82 StartY=-41 StartZ=0 EndX=-111.82 EndY=-45 EndZ=0
    g33: LineSegment StartX=-111.82 StartY=-45 StartZ=0 EndX=-126.73 EndY=-45 EndZ=0
    g34: LineSegment StartX=-126.73 StartY=-45 StartZ=0 EndX=-126.73 EndY=-41 EndZ=0
    g35: LineSegment StartX=-96.91 StartY=-41 StartZ=0 EndX=-82 EndY=-41 EndZ=0
    g36: LineSegment StartX=-82 StartY=-41 StartZ=0 EndX=-82 EndY=-45 EndZ=0
    g37: LineSegment StartX=-82 StartY=-45 StartZ=0 EndX=-96.91 EndY=-45 EndZ=0
    g38: LineSegment StartX=-96.91 StartY=-45 StartZ=0 EndX=-96.91 EndY=-41 EndZ=0
    g39: LineSegment StartX=-67.09 StartY=-41 StartZ=0 EndX=-52.18 EndY=-41 EndZ=0
    g40: LineSegment StartX=-52.18 StartY=-41 StartZ=0 EndX=-52.18 EndY=-45 EndZ=0
    g41: LineSegment StartX=-52.18 StartY=-45 StartZ=0 EndX=-67.09 EndY=-45 EndZ=0
    g42: LineSegment StartX=-67.09 StartY=-45 StartZ=0 EndX=-67.09 EndY=-41 EndZ=0
    g43: LineSegment StartX=-37.27 StartY=-41 StartZ=0 EndX=-22.36 EndY=-41 EndZ=0
    g44: LineSegment StartX=-22.36 StartY=-41 StartZ=0 EndX=-22.36 EndY=-45 EndZ=0
    g45: LineSegment StartX=-22.36 StartY=-45 StartZ=0 EndX=-37.27 EndY=-45 EndZ=0
    g46: LineSegment StartX=-37.27 StartY=-45 StartZ=0 EndX=-37.27 EndY=-41 EndZ=0
    g47: LineSegment StartX=-7.45 StartY=-41 StartZ=0 EndX=7.46 EndY=-41 EndZ=0
    g48: LineSegment StartX=7.46 StartY=-41 StartZ=0 EndX=7.46 EndY=-45 EndZ=0
    g49: LineSegment StartX=7.46 StartY=-45 StartZ=0 EndX=-7.45 EndY=-45 EndZ=0
    g50: LineSegment StartX=-7.45 StartY=-45 StartZ=0 EndX=-7.45 EndY=-41 EndZ=0
    g51: LineSegment StartX=22.37 StartY=-41 StartZ=0 EndX=37.28 EndY=-41 EndZ=0
    g52: LineSegment StartX=37.28 StartY=-41 StartZ=0 EndX=37.28 EndY=-45 EndZ=0
    g53: LineSegment StartX=37.28 StartY=-45 StartZ=0 EndX=22.37 EndY=-45 EndZ=0
    g54: LineSegment StartX=22.37 StartY=-45 StartZ=0 EndX=22.37 EndY=-41 EndZ=0
    g55: LineSegment StartX=52.19 StartY=-41 StartZ=0 EndX=67.1 EndY=-41 EndZ=0
    g56: LineSegment StartX=67.1 StartY=-41 StartZ=0 EndX=67.1 EndY=-45 EndZ=0
    g57: LineSegment StartX=67.1 StartY=-45 StartZ=0 EndX=52.19 EndY=-45 EndZ=0
    g58: LineSegment StartX=52.19 StartY=-45 StartZ=0 EndX=52.19 EndY=-41 EndZ=0
    g59: LineSegment StartX=82.01 StartY=-41 StartZ=0 EndX=96.92 EndY=-41 EndZ=0
    g60: LineSegment StartX=96.92 StartY=-41 StartZ=0 EndX=96.92 EndY=-45 EndZ=0
    g61: LineSegment StartX=96.92 StartY=-45 StartZ=0 EndX=82.01 EndY=-45 EndZ=0
    g62: LineSegment StartX=82.01 StartY=-45 StartZ=0 EndX=82.01 EndY=-41 EndZ=0
    g63: LineSegment StartX=111.83 StartY=-41 StartZ=0 EndX=126.74 EndY=-41 EndZ=0
    g64: LineSegment StartX=126.74 StartY=-41 StartZ=0 EndX=126.74 EndY=-45 EndZ=0
    g65: LineSegment StartX=126.74 StartY=-45 StartZ=0 EndX=111.83 EndY=-45 EndZ=0
    g66: LineSegment StartX=111.83 StartY=-45 StartZ=0 EndX=111.83 EndY=-41 EndZ=0
    g67: LineSegment StartX=141.65 StartY=-41 StartZ=0 EndX=156.56 EndY=-41 EndZ=0
    g68: LineSegment StartX=156.56 StartY=-41 StartZ=0 EndX=156.56 EndY=-45 EndZ=0
    g69: LineSegment StartX=156.56 StartY=-45 StartZ=0 EndX=141.65 EndY=-45 EndZ=0
    g70: LineSegment StartX=141.65 StartY=-45 StartZ=0 EndX=141.65 EndY=-41 EndZ=0
  constraints (212):
    c: PointOnObject(g0,g-1)
    c: Coincident(g1,g-1)
    c: PointOnObject(g2,g-1)
    c: Radius(g1) = 25
    c: Radius(g0) = 25
    c: Radius(g2) = 25
    c: DistanceX(g0,g1) = 83.33
    c: DistanceX(g1,g2) = 83.33
    c: Coincident(g3,g4)
    c: Coincident(g4,g5)
    c: Coincident(g5,g6)
    c: Coincident(g6,g3)
    c: Horizontal(g3)
    c: Horizontal(g5)
    c: Vertical(g4)
    c: Vertical(g6)
    c: Coincident(g7,g8)
    c: Coincident(g8,g9)
    c: Coincident(g9,g10)
    c: Coincident(g10,g7)
    c: Horizontal(g7)
    c: Horizontal(g9)
    c: Vertical(g8)
    c: Vertical(g10)
    c: Coincident(g11,g12)
    c: Coincident(g12,g13)
    c: Coincident(g13,g14)
    c: Coincident(g14,g11)
    c: Horizontal(g11)
    c: Horizontal(g13)
    c: Vertical(g12)
    c: Vertical(g14)
    c: Vertical(g3,g-3)
    c: Vertical(g7,g4)
    c: Vertical(g11,g8)
    c: Vertical(g5,g7)
    c: Vertical(g9,g11)
    c: DistanceY(g-3,g3) = 7.5
    c: DistanceY(g3,g4) = 15
    c: Equal(g4,g8)
    c: Equal(g8,g12)
    c: DistanceY(g4,g7) = 15
    c: DistanceY(g8,g11) = 15
    c: Coincident(g15,g16)
    c: Coincident(g16,g17)
    c: Coincident(g17,g18)
    c: Coincident(g18,g15)
    c: Horizontal(g15)
    c: Horizontal(g17)
    c: Vertical(g16)
    c: Vertical(g18)
    c: Coincident(g19,g20)
    c: Coincident(g20,g21)
    c: Coincident(g21,g22)
    c: Coincident(g22,g19)
    c: Horizontal(g19)
    c: Horizontal(g21)
    c: Vertical(g20)
    c: Vertical(g22)
    c: Coincident(g23,g24)
    c: Coincident(g24,g25)
    c: Coincident(g25,g26)
    c: Coincident(g26,g23)
    c: Horizontal(g23)
    c: Horizontal(g25)
    c: Vertical(g24)
    c: Vertical(g26)
    c: Vertical(g19,g16)
    c: Vertical(g23,g20)
    c: Vertical(g17,g19)
    c: Vertical(g21,g23)
    c: DistanceY(g15,g16) = 15
    c: Equal(g16,g20)
    c: Equal(g20,g24)
    c: DistanceY(g16,g19) = 15
    c: DistanceY(g20,g23) = 15
    c: Vertical(g15,g-4)
    c: DistanceY(g-4,g15) = 7.5
    c: DistanceX(g15,g15) = 4
    c: DistanceX(g3,g3) = 4
    c: Coincident(g27,g28)
    c: Coincident(g28,g29)
    c: Coincident(g29,g30)
    c: Coincident(g30,g27)
    c: Horizontal(g27)
    c: Horizontal(g29)
    c: Vertical(g28)
    c: Vertical(g30)
    c: Coincident(g31,g32)
    c: Coincident(g32,g33)
    c: Coincident(g33,g34)
    c: Coincident(g34,g31)
    c: Horizontal(g31)
    c: Horizontal(g33)
    c: Vertical(g32)
    c: Vertical(g34)
    c: Coincident(g35,g36)
    c: Coincident(g36,g37)
    c: Coincident(g37,g38)
    c: Coincident(g38,g35)
    c: Horizontal(g35)
    c: Horizontal(g37)
    c: Vertical(g36)
    c: Vertical(g38)
    c: Coincident(g39,g40)
    c: Coincident(g40,g41)
    c: Coincident(g41,g42)
    c: Coincident(g42,g39)
    c: Horizontal(g39)
    c: Horizontal(g41)
    c: Vertical(g40)
    c: Vertical(g42)
    c: Coincident(g43,g44)
    c: Coincident(g44,g45)
    c: Coincident(g45,g46)
    c: Coincident(g46,g43)
    c: Horizontal(g43)
    c: Horizontal(g45)
    c: Vertical(g44)
    c: Vertical(g46)
    c: Coincident(g47,g48)
    c: Coincident(g48,g49)
    c: Coincident(g49,g50)
    c: Coincident(g50,g47)
    c: Horizontal(g47)
    c: Horizontal(g49)
    c: Vertical(g48)
    c: Vertical(g50)
    c: Coincident(g51,g52)
    c: Coincident(g52,g53)
    c: Coincident(g53,g54)
    c: Coincident(g54,g51)
    c: Horizontal(g51)
    c: Horizontal(g53)
    c: Vertical(g52)
    c: Vertical(g54)
    c: Coincident(g55,g56)
    c: Coincident(g56,g57)
    c: Coincident(g57,g58)
    c: Coincident(g58,g55)
    c: Horizontal(g55)
    c: Horizontal(g57)
    c: Vertical(g56)
    c: Vertical(g58)
    c: Coincident(g59,g60)
    c: Coincident(g60,g61)
    c: Coincident(g61,g62)
    c: Coincident(g62,g59)
    c: Horizontal(g59)
    c: Horizontal(g61)
    c: Vertical(g60)
    c: Vertical(g62)
    c: Coincident(g63,g64)
    c: Coincident(g64,g65)
    c: Coincident(g65,g66)
    c: Coincident(g66,g63)
    c: Horizontal(g63)
    c: Horizontal(g65)
    c: Vertical(g64)
    c: Vertical(g66)
    c: Coincident(g67,g68)
    c: Coincident(g68,g69)
    c: Coincident(g69,g70)
    c: Coincident(g70,g67)
    c: Horizontal(g67)
    c: Horizontal(g69)
    c: Vertical(g68)
    c: Vertical(g70)
    c: Horizontal(g27,g31)
    c: Horizontal(g31,g35)
    c: Horizontal(g35,g39)
    c: Horizontal(g39,g43)
    c: Horizontal(g43,g47)
    c: Horizontal(g47,g51)
    c: Horizontal(g51,g55)
    c: Horizontal(g55,g59)
    c: Horizontal(g59,g63)
    c: Horizontal(g63,g67)
    c: Horizontal(g28,g32)
    c: Horizontal(g32,g36)
    c: Horizontal(g36,g40)
    c: Horizontal(g40,g44)
    c: Horizontal(g44,g48)
    c: Horizontal(g48,g52)
    c: Horizontal(g52,g56)
    c: Horizontal(g56,g60)
    c: Horizontal(g60,g64)
    c: Horizontal(g64,g68)
    c: Horizontal(g-3,g29)
    c: DistanceX(g29,g28) = 14.91
    c: Equal(g29,g69)
    c: Equal(g69,g65)
    c: Equal(g61,g65)
    c: Equal(g61,g57)
    c: Equal(g57,g53)
    c: Equal(g53,g49)
    c: Equal(g49,g45)
    c: Equal(g45,g41)
    c: Equal(g37,g41)
    c: Equal(g33,g37)
    c: DistanceX(g-3,g29) = 7.45
    c: DistanceX(g28,g33) = 14.91
    c: DistanceX(g32,g37) = 14.91
    c: DistanceX(g36,g41) = 14.91
    c: DistanceX(g40,g45) = 14.91
    c: DistanceX(g44,g49) = 14.91
    c: DistanceX(g48,g53) = 14.91
    c: DistanceX(g52,g57) = 14.91
    c: DistanceX(g56,g61) = 14.91
    c: DistanceX(g60,g65) = 14.91
    c: DistanceX(g64,g69) = 14.91
    c: DistanceY(g-3,g27) = 4
FEATURE [PartDesign::Pocket] Pocket033
  BaseFeature = -> Pad037
  Length = 4
  Length2 = 100
  Placement = pos=(0,0,0) rot=(1,0,0;1.5708rad)
  Profile = -> Sketch075
  Type = 0
FEATURE [PartDesign::Body] Body037  label="UtrustningsBoxBakkant-3"
  Group = -> [Sketch074,Pad037,Sketch075,Pocket033]
  Origin = -> Origin037
  Placement = pos=(167,-302,0) rot=(0,0,1;0rad)
  Tip = -> Pocket033
FEATURE [Sketcher::SketchObject] Sketch076
  FullyConstrained = true
  MapMode = 5
  Support = -> [XY_Plane038]
  sketch-geometry (4):
    g0: LineSegment StartX=164 StartY=-100 StartZ=0 EndX=-164 EndY=-100 EndZ=0
    g1: LineSegment StartX=-164 StartY=-100 StartZ=0 EndX=-164 EndY=100 EndZ=0
    g2: LineSegment StartX=-164 StartY=100 StartZ=0 EndX=164 EndY=100 EndZ=0
    g3: LineSegment StartX=164 StartY=100 StartZ=0 EndX=164 EndY=-100 EndZ=0
  constraints (11):
    c: Coincident(g0,g1)
    c: Coincident(g1,g2)
    c: Coincident(g2,g3)
    c: Coincident(g3,g0)
    c: Horizontal(g0)
    c: Horizontal(g2)
    c: Vertical(g1)
    c: Vertical(g3)
    c: Symmetric(g1,g0,g-1)
    c: DistanceX(g1,g2) = 328
    c: DistanceY(g0,g1) = 200
FEATURE [PartDesign::Pad] Pad038
  Direction = (1,1,1)
  Length = 4
  Length2 = 100
  Profile = -> Sketch076
  Type = 0
FEATURE [Sketcher::SketchObject] Sketch077
  ExternalGeometry = -> [Pad038]
  FullyConstrained = true
  MapMode = 5
  Placement = pos=(0,0,4) rot=(0,0,1;0rad)
  Support = -> [Pad038]
  sketch-geometry (124):
    g0: LineSegment StartX=-164 StartY=100 StartZ=0 EndX=-156.55 EndY=100 EndZ=0
    g1: LineSegment StartX=-156.55 StartY=100 StartZ=0 EndX=-156.55 EndY=96 EndZ=0
    g2: LineSegment StartX=-156.55 StartY=96 StartZ=0 EndX=-164 EndY=96 EndZ=0
    g3: LineSegment StartX=-164 StartY=96 StartZ=0 EndX=-164 EndY=100 EndZ=0
    g4: LineSegment StartX=-141.64 StartY=100 StartZ=0 EndX=-126.73 EndY=100 EndZ=0
    g5: LineSegment StartX=-126.73 StartY=100 StartZ=0 EndX=-126.73 EndY=96 EndZ=0
    g6: LineSegment StartX=-126.73 StartY=96 StartZ=0 EndX=-141.64 EndY=96 EndZ=0
    g7: LineSegment StartX=-141.64 StartY=96 StartZ=0 EndX=-141.64 EndY=100 EndZ=0
    g8: LineSegment StartX=-111.82 StartY=100 StartZ=0 EndX=-96.91 EndY=100 EndZ=0
    g9: LineSegment StartX=-96.91 StartY=100 StartZ=0 EndX=-96.91 EndY=96 EndZ=0
    g10: LineSegment StartX=-96.91 StartY=96 StartZ=0 EndX=-111.82 EndY=96 EndZ=0
    g11: LineSegment StartX=-111.82 StartY=96 StartZ=0 EndX=-111.82 EndY=100 EndZ=0
    g12: LineSegment StartX=-82 StartY=100 StartZ=0 EndX=-67.09 EndY=100 EndZ=0
    g13: LineSegment StartX=-67.09 StartY=100 StartZ=0 EndX=-67.09 EndY=96 EndZ=0
    g14: LineSegment StartX=-67.09 StartY=96 StartZ=0 EndX=-82 EndY=96 EndZ=0
    g15: LineSegment StartX=-82 StartY=96 StartZ=0 EndX=-82 EndY=100 EndZ=0
    g16: LineSegment StartX=-52.18 StartY=100 StartZ=0 EndX=-37.27 EndY=100 EndZ=0
    g17: LineSegment StartX=-37.27 StartY=100 StartZ=0 EndX=-37.27 EndY=96 EndZ=0
    g18: LineSegment StartX=-37.27 StartY=96 StartZ=0 EndX=-52.18 EndY=96 EndZ=0
    g19: LineSegment StartX=-52.18 StartY=96 StartZ=0 EndX=-52.18 EndY=100 EndZ=0
    g20: LineSegment StartX=-22.36 StartY=100 StartZ=0 EndX=-7.45 EndY=100 EndZ=0
    g21: LineSegment StartX=-7.45 StartY=100 StartZ=0 EndX=-7.45 EndY=96 EndZ=0
    g22: LineSegment StartX=-7.45 StartY=96 StartZ=0 EndX=-22.36 EndY=96 EndZ=0
    g23: LineSegment StartX=-22.36 StartY=96 StartZ=0 EndX=-22.36 EndY=100 EndZ=0
    g24: LineSegment StartX=7.46 StartY=100 StartZ=0 EndX=22.37 EndY=100 EndZ=0
    g25: LineSegment StartX=22.37 StartY=100 StartZ=0 EndX=22.37 EndY=96 EndZ=0
    g26: LineSegment StartX=22.37 StartY=96 StartZ=0 EndX=7.46 EndY=96 EndZ=0
    g27: LineSegment StartX=7.46 StartY=96 StartZ=0 EndX=7.46 EndY=100 EndZ=0
    g28: LineSegment StartX=37.28 StartY=100 StartZ=0 EndX=52.19 EndY=100 EndZ=0
    g29: LineSegment StartX=52.19 StartY=100 StartZ=0 EndX=52.19 EndY=96 EndZ=0
    g30: LineSegment StartX=52.19 StartY=96 StartZ=0 EndX=37.28 EndY=96 EndZ=0
    g31: LineSegment StartX=37.28 StartY=96 StartZ=0 EndX=37.28 EndY=100 EndZ=0
    g32: LineSegment StartX=67.1 StartY=100 StartZ=0 EndX=82.01 EndY=100 EndZ=0
    g33: LineSegment StartX=82.01 StartY=100 StartZ=0 EndX=82.01 EndY=96 EndZ=0
    g34: LineSegment StartX=82.01 StartY=96 StartZ=0 EndX=67.1 EndY=96 EndZ=0
    g35: LineSegment StartX=67.1 StartY=96 StartZ=0 EndX=67.1 EndY=100 EndZ=0
    g36: LineSegment StartX=96.92 StartY=100 StartZ=0 EndX=111.83 EndY=100 EndZ=0
    g37: LineSegment StartX=111.83 StartY=100 StartZ=0 EndX=111.83 EndY=96 EndZ=0
    g38: LineSegment StartX=111.83 StartY=96 StartZ=0 EndX=96.92 EndY=96 EndZ=0
    g39: LineSegment StartX=96.92 StartY=96 StartZ=0 EndX=96.92 EndY=100 EndZ=0
    g40: LineSegment StartX=126.74 StartY=100 StartZ=0 EndX=141.65 EndY=100 EndZ=0
    g41: LineSegment StartX=141.65 StartY=100 StartZ=0 EndX=141.65 EndY=96 EndZ=0
    g42: LineSegment StartX=141.65 StartY=96 StartZ=0 EndX=126.74 EndY=96 EndZ=0
    g43: LineSegment StartX=126.74 StartY=96 StartZ=0 EndX=126.74 EndY=100 EndZ=0
    g44: LineSegment StartX=156.56 StartY=100 StartZ=0 EndX=164.01 EndY=100 EndZ=0
    g45: LineSegment StartX=164.01 StartY=100 StartZ=0 EndX=164.01 EndY=96 EndZ=0
    g46: LineSegment StartX=164.01 StartY=96 StartZ=0 EndX=156.56 EndY=96 EndZ=0
    g47: LineSegment StartX=156.56 StartY=96 StartZ=0 EndX=156.56 EndY=100 EndZ=0
    g48: LineSegment StartX=-164 StartY=89 StartZ=0 EndX=-160 EndY=89 EndZ=0
    g49: LineSegment StartX=-160 StartY=89 StartZ=0 EndX=-160 EndY=75 EndZ=0
    g50: LineSegment StartX=-160 StartY=75 StartZ=0 EndX=-164 EndY=75 EndZ=0
    g51: LineSegment StartX=-164 StartY=75 StartZ=0 EndX=-164 EndY=89 EndZ=0
    g52: LineSegment StartX=-164 StartY=61 StartZ=0 EndX=-160 EndY=61 EndZ=0
    g53: LineSegment StartX=-160 StartY=61 StartZ=0 EndX=-160 EndY=47 EndZ=0
    g54: LineSegment StartX=-160 StartY=47 StartZ=0 EndX=-164 EndY=47 EndZ=0
    g55: LineSegment StartX=-164 StartY=47 StartZ=0 EndX=-164 EndY=61 EndZ=0
    g56: LineSegment StartX=-164 StartY=33 StartZ=0 EndX=-160 EndY=33 EndZ=0
    g57: LineSegment StartX=-160 StartY=33 StartZ=0 EndX=-160 EndY=19 EndZ=0
    g58: LineSegment StartX=-160 StartY=19 StartZ=0 EndX=-164 EndY=19 EndZ=0
    g59: LineSegment StartX=-164 StartY=19 StartZ=0 EndX=-164 EndY=33 EndZ=0
    g60: LineSegment StartX=-164 StartY=5 StartZ=0 EndX=-160 EndY=5 EndZ=0
    g61: LineSegment StartX=-160 StartY=5 StartZ=0 EndX=-160 EndY=-9 EndZ=0
    g62: LineSegment StartX=-160 StartY=-9 StartZ=0 EndX=-164 EndY=-9 EndZ=0
    g63: LineSegment StartX=-164 StartY=-9 StartZ=0 EndX=-164 EndY=5 EndZ=0
    g64: LineSegment StartX=-164 StartY=-23 StartZ=0 EndX=-160 EndY=-23 EndZ=0
    g65: LineSegment StartX=-160 StartY=-23 StartZ=0 EndX=-160 EndY=-37 EndZ=0
    g66: LineSegment StartX=-160 StartY=-37 StartZ=0 EndX=-164 EndY=-37 EndZ=0
    g67: LineSegment StartX=-164 StartY=-37 StartZ=0 EndX=-164 EndY=-23 EndZ=0
    g68: LineSegment StartX=-164 StartY=-51 StartZ=0 EndX=-160 EndY=-51 EndZ=0
    g69: LineSegment StartX=-160 StartY=-51 StartZ=0 EndX=-160 EndY=-65 EndZ=0
    g70: LineSegment StartX=-160 StartY=-65 StartZ=0 EndX=-164 EndY=-65 EndZ=0
    g71: LineSegment StartX=-164 StartY=-65 StartZ=0 EndX=-164 EndY=-51 EndZ=0
    g72: LineSegment StartX=-164 StartY=-79 StartZ=0 EndX=-160 EndY=-79 EndZ=0
    g73: LineSegment StartX=-160 StartY=-79 StartZ=0 EndX=-160 EndY=-93 EndZ=0
    g74: LineSegment StartX=-160 StartY=-93 StartZ=0 EndX=-164 EndY=-93 EndZ=0
    g75: LineSegment StartX=-164 StartY=-93 StartZ=0 EndX=-164 EndY=-79 EndZ=0
    g76: LineSegment StartX=160 StartY=89 StartZ=0 EndX=164 EndY=89 EndZ=0
    g77: LineSegment StartX=164 StartY=89 StartZ=0 EndX=164 EndY=75 EndZ=0
    g78: LineSegment StartX=164 StartY=75 StartZ=0 EndX=160 EndY=75 EndZ=0
    g79: LineSegment StartX=160 StartY=75 StartZ=0 EndX=160 EndY=89 EndZ=0
    g80: LineSegment StartX=160 StartY=61 StartZ=0 EndX=164 EndY=61 EndZ=0
    g81: LineSegment StartX=164 StartY=61 StartZ=0 EndX=164 EndY=47 EndZ=0
    g82: LineSegment StartX=164 StartY=47 StartZ=0 EndX=160 EndY=47 EndZ=0
    g83: LineSegment StartX=160 StartY=47 StartZ=0 EndX=160 EndY=61 EndZ=0
    g84: LineSegment StartX=160 StartY=33 StartZ=0 EndX=164 EndY=33 EndZ=0
    g85: LineSegment StartX=164 StartY=33 StartZ=0 EndX=164 EndY=19 EndZ=0
    g86: LineSegment StartX=164 StartY=19 StartZ=0 EndX=160 EndY=19 EndZ=0
    g87: LineSegment StartX=160 StartY=19 StartZ=0 EndX=160 EndY=33 EndZ=0
    g88: LineSegment StartX=160 StartY=5 StartZ=0 EndX=164 EndY=5 EndZ=0
    g89: LineSegment StartX=164 StartY=5 StartZ=0 EndX=164 EndY=-9 EndZ=0
    g90: LineSegment StartX=164 StartY=-9 StartZ=0 EndX=160 EndY=-9 EndZ=0
    g91: LineSegment StartX=160 StartY=-9 StartZ=0 EndX=160 EndY=5 EndZ=0
    g92: LineSegment StartX=160 StartY=-23 StartZ=0 EndX=164 EndY=-23 EndZ=0
    g93: LineSegment StartX=164 StartY=-23 StartZ=0 EndX=164 EndY=-37 EndZ=0
    g94: LineSegment StartX=164 StartY=-37 StartZ=0 EndX=160 EndY=-37 EndZ=0
    g95: LineSegment StartX=160 StartY=-37 StartZ=0 EndX=160 EndY=-23 EndZ=0
    g96: LineSegment StartX=160 StartY=-51 StartZ=0 EndX=164 EndY=-51 EndZ=0
    g97: LineSegment StartX=164 StartY=-51 StartZ=0 EndX=164 EndY=-65 EndZ=0
    g98: LineSegment StartX=164 StartY=-65 StartZ=0 EndX=160 EndY=-65 EndZ=0
    g99: LineSegment StartX=160 StartY=-65 StartZ=0 EndX=160 EndY=-51 EndZ=0
    g100: LineSegment StartX=160 StartY=-79 StartZ=0 EndX=164 EndY=-79 EndZ=0
    g101: LineSegment StartX=164 StartY=-79 StartZ=0 EndX=164 EndY=-93 EndZ=0
    g102: LineSegment StartX=164 StartY=-93 StartZ=0 EndX=160 EndY=-93 EndZ=0
    g103: LineSegment StartX=160 StartY=-93 StartZ=0 EndX=160 EndY=-79 EndZ=0
    g104: Circle CenterX=0 CenterY=75 CenterZ=0 NormalX=0 NormalY=0 NormalZ=1 AngleXU=0 Radius=10
    g105: Circle CenterX=0 CenterY=25 CenterZ=0 NormalX=0 NormalY=0 NormalZ=1 AngleXU=0 Radius=10
    g106: Circle CenterX=0 CenterY=-25 CenterZ=0 NormalX=0 NormalY=0 NormalZ=1 AngleXU=0 Radius=10
    g107: Circle CenterX=0 CenterY=-75 CenterZ=0 NormalX=0 NormalY=0 NormalZ=1 AngleXU=0 Radius=10
    g108: Circle CenterX=54.7 CenterY=75 CenterZ=0 NormalX=0 NormalY=0 NormalZ=1 AngleXU=0 Radius=10
    g109: Circle CenterX=54.7 CenterY=25 CenterZ=0 NormalX=0 NormalY=0 NormalZ=1 AngleXU=0 Radius=10
    g110: Circle CenterX=54.7 CenterY=-25 CenterZ=0 NormalX=0 NormalY=0 NormalZ=1 AngleXU=0 Radius=10
    g111: Circle CenterX=54.7 CenterY=-75 CenterZ=0 NormalX=0 NormalY=0 NormalZ=1 AngleXU=0 Radius=10
    g112: Circle CenterX=109.4 CenterY=75 CenterZ=0 NormalX=0 NormalY=0 NormalZ=1 AngleXU=0 Radius=10
    g113: Circle CenterX=109.4 CenterY=25 CenterZ=0 NormalX=0 NormalY=0 NormalZ=1 AngleXU=0 Radius=10
    g114: Circle CenterX=109.4 CenterY=-25 CenterZ=0 NormalX=0 NormalY=0 NormalZ=1 AngleXU=0 Radius=10
    g115: Circle CenterX=109.4 CenterY=-75 CenterZ=0 NormalX=0 NormalY=0 NormalZ=1 AngleXU=0 Radius=10
    g116: Circle CenterX=-109.4 CenterY=75 CenterZ=0 NormalX=0 NormalY=0 NormalZ=1 AngleXU=0 Radius=10
    g117: Circle CenterX=-109.4 CenterY=25 CenterZ=0 NormalX=0 NormalY=0 NormalZ=1 AngleXU=0 Radius=10
    g118: Circle CenterX=-109.4 CenterY=-25 CenterZ=0 NormalX=0 NormalY=0 NormalZ=1 AngleXU=0 Radius=10
    g119: Circle CenterX=-109.4 CenterY=-75 CenterZ=0 NormalX=0 NormalY=0 NormalZ=1 AngleXU=0 Radius=10
    g120: Circle CenterX=-54.7 CenterY=75 CenterZ=0 NormalX=0 NormalY=0 NormalZ=1 AngleXU=0 Radius=10
    g121: Circle CenterX=-54.7 CenterY=25 CenterZ=0 NormalX=0 NormalY=0 NormalZ=1 AngleXU=0 Radius=10
    g122: Circle CenterX=-54.7 CenterY=-25 CenterZ=0 NormalX=0 NormalY=0 NormalZ=1 AngleXU=0 Radius=10
    g123: Circle CenterX=-54.7 CenterY=-75 CenterZ=0 NormalX=0 NormalY=0 NormalZ=1 AngleXU=0 Radius=10
  constraints (372):
    c: Coincident(g0,g1)
    c: Coincident(g1,g2)
    c: Coincident(g2,g3)
    c: Coincident(g3,g0)
    c: Horizontal(g0)
    c: Horizontal(g2)
    c: Vertical(g1)
    c: Vertical(g3)
    c: Coincident(g4,g5)
    c: Coincident(g5,g6)
    c: Coincident(g6,g7)
    c: Coincident(g7,g4)
    c: Horizontal(g4)
    c: Horizontal(g6)
    c: Vertical(g5)
    c: Vertical(g7)
    c: Coincident(g8,g9)
    c: Coincident(g9,g10)
    c: Coincident(g10,g11)
    c: Coincident(g11,g8)
    c: Horizontal(g8)
    c: Horizontal(g10)
    c: Vertical(g9)
    c: Vertical(g11)
    c: Coincident(g12,g13)
    c: Coincident(g13,g14)
    c: Coincident(g14,g15)
    c: Coincident(g15,g12)
    c: Horizontal(g12)
    c: Horizontal(g14)
    c: Vertical(g13)
    c: Vertical(g15)
    c: Coincident(g16,g17)
    c: Coincident(g17,g18)
    c: Coincident(g18,g19)
    c: Coincident(g19,g16)
    c: Horizontal(g16)
    c: Horizontal(g18)
    c: Vertical(g17)
    c: Vertical(g19)
    c: Coincident(g20,g21)
    c: Coincident(g21,g22)
    c: Coincident(g22,g23)
    c: Coincident(g23,g20)
    c: Horizontal(g20)
    c: Horizontal(g22)
    c: Vertical(g21)
    c: Vertical(g23)
    c: Horizontal(g0,g4)
    c: Horizontal(g4,g8)
    c: Horizontal(g8,g12)
    c: Horizontal(g12,g16)
    c: Horizontal(g16,g20)
    c: Horizontal(g1,g5)
    c: Horizontal(g5,g9)
    c: Horizontal(g9,g13)
    c: Horizontal(g13,g17)
    c: Horizontal(g17,g21)
    c: PointOnObject(g0,g-4)
    c: PointOnObject(g0,g-5)
    c: DistanceX(g0,g0) = 7.45
    c: DistanceX(g0,g4) = 14.91
    c: DistanceX(g4,g4) = 14.91
    c: Equal(g4,g8)
    c: Equal(g8,g12)
    c: Equal(g12,g16)
    c: Equal(g20,g16)
    c: DistanceX(g16,g20) = 14.91
    c: DistanceX(g12,g16) = 14.91
    c: DistanceX(g4,g8) = 14.91
    c: DistanceX(g8,g12) = 14.91
    c: Coincident(g24,g25)
    c: Coincident(g25,g26)
    c: Coincident(g26,g27)
    c: Coincident(g27,g24)
    c: Horizontal(g24)
    c: Horizontal(g26)
    c: Vertical(g25)
    c: Vertical(g27)
    c: Coincident(g28,g29)
    c: Coincident(g29,g30)
    c: Coincident(g30,g31)
    c: Coincident(g31,g28)
    c: Horizontal(g28)
    c: Horizontal(g30)
    c: Vertical(g29)
    c: Vertical(g31)
    c: Coincident(g32,g33)
    c: Coincident(g33,g34)
    c: Coincident(g34,g35)
    c: Coincident(g35,g32)
    c: Horizontal(g32)
    c: Horizontal(g34)
    c: Vertical(g33)
    c: Vertical(g35)
    c: Coincident(g36,g37)
    c: Coincident(g37,g38)
    c: Coincident(g38,g39)
    c: Coincident(g39,g36)
    c: Horizontal(g36)
    c: Horizontal(g38)
    c: Vertical(g37)
    c: Vertical(g39)
    c: Horizontal(g24,g28)
    c: Horizontal(g28,g32)
    c: Horizontal(g32,g36)
    c: Horizontal(g25,g29)
    c: Horizontal(g29,g33)
    c: Horizontal(g33,g37)
    c: Equal(g24,g28)
    c: Equal(g28,g32)
    c: Equal(g36,g32)
    c: DistanceX(g32,g36) = 14.91
    c: DistanceX(g28,g32) = 14.91
    c: DistanceX(g24,g28) = 14.91
    c: DistanceX(g20,g24) = 14.91
    c: Horizontal(g24,g20)
    c: Horizontal(g21,g26)
    c: Equal(g22,g26)
    c: Coincident(g40,g41)
    c: Coincident(g41,g42)
    c: Coincident(g42,g43)
    c: Coincident(g43,g40)
    c: Horizontal(g40)
    c: Horizontal(g42)
    c: Vertical(g41)
    c: Vertical(g43)
    c: Horizontal(g42,g37)
    c: Horizontal(g40,g36)
    c: Equal(g36,g40)
    c: DistanceX(g36,g40) = 14.91
    c: Coincident(g44,g45)
    c: Coincident(g45,g46)
    c: Coincident(g46,g47)
    c: Coincident(g47,g44)
    c: Horizontal(g44)
    c: Horizontal(g46)
    c: Vertical(g45)
    c: Vertical(g47)
    c: Horizontal(g40,g44)
    c: Horizontal(g41,g46)
    c: DistanceX(g40,g44) = 14.91
    c: DistanceX(g44,g44) = 7.45
    c: DistanceY(g2,g0) = 4
    c: Coincident(g48,g49)
    c: Coincident(g49,g50)
    c: Coincident(g50,g51)
    c: Coincident(g51,g48)
    c: Horizontal(g48)
    c: Horizontal(g50)
    c: Vertical(g49)
    c: Vertical(g51)
    c: PointOnObject(g48,g-5)
    c: Coincident(g52,g53)
    c: Coincident(g53,g54)
    c: Coincident(g54,g55)
    c: Coincident(g55,g52)
    c: Horizontal(g52)
    c: Horizontal(g54)
    c: Vertical(g53)
    c: Vertical(g55)
    c: PointOnObject(g52,g-5)
    c: Coincident(g56,g57)
    c: Coincident(g57,g58)
    c: Coincident(g58,g59)
    c: Coincident(g59,g56)
    c: Horizontal(g56)
    c: Horizontal(g58)
    c: Vertical(g57)
    c: Vertical(g59)
    c: PointOnObject(g56,g-5)
    c: Coincident(g60,g61)
    c: Coincident(g61,g62)
    c: Coincident(g62,g63)
    c: Coincident(g63,g60)
    c: Horizontal(g60)
    c: Horizontal(g62)
    c: Vertical(g61)
    c: Vertical(g63)
    c: PointOnObject(g60,g-5)
    c: Coincident(g64,g65)
    c: Coincident(g65,g66)
    c: Coincident(g66,g67)
    c: Coincident(g67,g64)
    c: Horizontal(g64)
    c: Horizontal(g66)
    c: Vertical(g65)
    c: Vertical(g67)
    c: PointOnObject(g64,g-5)
    c: Vertical(g53,g49)
    c: Vertical(g49,g57)
    c: Vertical(g57,g61)
    c: DistanceY(g48,g2) = 7
    c: DistanceY(g50,g48) = 14
    c: Equal(g49,g53)
    c: Equal(g53,g57)
    c: Equal(g57,g61)
    c: Equal(g61,g65)
    c: DistanceY(g52,g50) = 14
    c: DistanceY(g56,g54) = 14
    c: DistanceY(g60,g58) = 14
    c: DistanceY(g64,g62) = 14
    c: Coincident(g68,g69)
    c: Coincident(g69,g70)
    c: Coincident(g70,g71)
    c: Coincident(g71,g68)
    c: Horizontal(g68)
    c: Horizontal(g70)
    c: Vertical(g69)
    c: Vertical(g71)
    c: Coincident(g72,g73)
    c: Coincident(g73,g74)
    c: Coincident(g74,g75)
    c: Coincident(g75,g72)
    c: Horizontal(g72)
    c: Horizontal(g74)
    c: Vertical(g73)
    c: Vertical(g75)
    c: Equal(g69,g73)
    c: DistanceY(g72,g70) = 14
    c: PointOnObject(g74,g-5)
    c: PointOnObject(g70,g-5)
    c: Vertical(g65,g68)
    c: Vertical(g61,g64)
    c: DistanceY(g68,g66) = 14
    c: Equal(g69,g65)
    c: DistanceX(g48,g48) = 4
    c: Vertical(g69,g72)
    c: Coincident(g76,g77)
    c: Coincident(g77,g78)
    c: Coincident(g78,g79)
    c: Coincident(g79,g76)
    c: Horizontal(g76)
    c: Horizontal(g78)
    c: Vertical(g77)
    c: Vertical(g79)
    c: Coincident(g80,g81)
    c: Coincident(g81,g82)
    c: Coincident(g82,g83)
    c: Coincident(g83,g80)
    c: Horizontal(g80)
    c: Horizontal(g82)
    c: Vertical(g81)
    c: Vertical(g83)
    c: Coincident(g84,g85)
    c: Coincident(g85,g86)
    c: Coincident(g86,g87)
    c: Coincident(g87,g84)
    c: Horizontal(g84)
    c: Horizontal(g86)
    c: Vertical(g85)
    c: Vertical(g87)
    c: Coincident(g88,g89)
    c: Coincident(g89,g90)
    c: Coincident(g90,g91)
    c: Coincident(g91,g88)
    c: Horizontal(g88)
    c: Horizontal(g90)
    c: Vertical(g89)
    c: Vertical(g91)
    c: Coincident(g92,g93)
    c: Coincident(g93,g94)
    c: Coincident(g94,g95)
    c: Coincident(g95,g92)
    c: Horizontal(g92)
    c: Horizontal(g94)
    c: Vertical(g93)
    c: Vertical(g95)
    c: Vertical(g81,g77)
    c: Vertical(g77,g85)
    c: Vertical(g85,g89)
    c: DistanceY(g78,g76) = 14
    c: Equal(g77,g81)
    c: Equal(g81,g85)
    c: Equal(g85,g89)
    c: Equal(g89,g93)
    c: DistanceY(g80,g78) = 14
    c: DistanceY(g84,g82) = 14
    c: DistanceY(g88,g86) = 14
    c: DistanceY(g92,g90) = 14
    c: Coincident(g96,g97)
    c: Coincident(g97,g98)
    c: Coincident(g98,g99)
    c: Coincident(g99,g96)
    c: Horizontal(g96)
    c: Horizontal(g98)
    c: Vertical(g97)
    c: Vertical(g99)
    c: Coincident(g100,g101)
    c: Coincident(g101,g102)
    c: Coincident(g102,g103)
    c: Coincident(g103,g100)
    c: Horizontal(g100)
    c: Horizontal(g102)
    c: Vertical(g101)
    c: Vertical(g103)
    c: Equal(g97,g101)
    c: DistanceY(g100,g98) = 14
    c: Vertical(g93,g96)
    c: Vertical(g89,g92)
    c: DistanceY(g96,g94) = 14
    c: Equal(g97,g93)
    c: Equal(g48,g76) = 4
    c: Vertical(g97,g100)
    c: Vertical(g80,g78)
    c: Vertical(g82,g86)
    c: Vertical(g86,g90)
    c: Vertical(g90,g94)
    c: Vertical(g94,g98)
    c: Vertical(g98,g102)
    c: DistanceY(g76,g45) = 7
    c: PointOnObject(g104,g-2)
    c: PointOnObject(g105,g-2)
    c: PointOnObject(g106,g-2)
    c: PointOnObject(g107,g-2)
    c: Radius(g107) = 10
    c: Equal(g107,g106)
    c: Equal(g106,g105)
    c: Equal(g105,g104)
    c: DistanceY(g106,g-1) = 25
    c: DistanceY(g107,g106) = 50
    c: DistanceY(g-1,g105) = 25
    c: DistanceY(g105,g104) = 50
    c: Equal(g107,g111) = 10
    c: Equal(g111,g110)
    c: Equal(g110,g109)
    c: Equal(g109,g108)
    c: DistanceY(g111,g110) = 50
    c: DistanceY(g109,g108) = 50
    c: DistanceY(g110,g109) = 50
    c: Vertical(g111,g110)
    c: Vertical(g110,g109)
    c: Vertical(g109,g108)
    c: Equal(g115,g114)
    c: Equal(g114,g113)
    c: Equal(g113,g112)
    c: DistanceY(g115,g114) = 50
    c: DistanceY(g113,g112) = 50
    c: DistanceY(g114,g113) = 50
    c: Vertical(g115,g114)
    c: Vertical(g114,g113)
    c: Vertical(g113,g112)
    c: DistanceX(g107,g111) = 54.7
    c: DistanceX(g111,g115) = 54.7
    c: Horizontal(g107,g111)
    c: Horizontal(g111,g115)
    c: Radius(g115) = 10
    c: Equal(g119,g118)
    c: Equal(g118,g117)
    c: Equal(g117,g116)
    c: DistanceY(g119,g118) = 50
    c: DistanceY(g117,g116) = 50
    c: DistanceY(g118,g117) = 50
    c: Vertical(g119,g118)
    c: Vertical(g118,g117)
    c: Vertical(g117,g116)
    c: Equal(g123,g122)
    c: Equal(g122,g121)
    c: Equal(g121,g120)
    c: DistanceY(g123,g122) = 50
    c: DistanceY(g121,g120) = 50
    c: DistanceY(g122,g121) = 50
    c: Vertical(g123,g122)
    c: Vertical(g122,g121)
    c: Vertical(g121,g120)
    c: DistanceX(g119,g123) = 54.7
    c: Horizontal(g119,g123)
    c: Equal(g115,g123) = 10
    c: Horizontal(g107,g123)
    c: DistanceX(g123,g107) = 54.7
    c: Radius(g119) = 10
    c: PointOnObject(g76,g-6)
FEATURE [PartDesign::Pocket] Pocket034
  BaseFeature = -> Pad038
  Length = 4
  Length2 = 100
  Profile = -> Sketch077
  Type = 0
FEATURE [PartDesign::Body] Body038  label="UtrustningsBoxBotten-3"
  Group = -> [Sketch076,Pad038,Sketch077,Pocket034]
  Origin = -> Origin038
  Placement = pos=(167,-402,-45) rot=(0,0,1;0rad)
  Tip = -> Pocket034
FEATURE [Sketcher::SketchObject] Sketch079
  FullyConstrained = true
  MapMode = 5
  Placement = pos=(0,0,0) rot=(0.57735,0.57735,0.57735;2.0944rad)
  Support = -> [YZ_Plane039]
  sketch-geometry (4):
    g0: LineSegment StartX=-100 StartY=-45 StartZ=0 EndX=100 EndY=-45 EndZ=0
    g1: LineSegment StartX=100 StartY=-45 StartZ=0 EndX=100 EndY=45 EndZ=0
    g2: LineSegment StartX=100 StartY=45 StartZ=0 EndX=-100 EndY=45 EndZ=0
    g3: LineSegment StartX=-100 StartY=45 StartZ=0 EndX=-100 EndY=-45 EndZ=0
  constraints (11):
    c: Coincident(g0,g1)
    c: Coincident(g1,g2)
    c: Coincident(g2,g3)
    c: Coincident(g3,g0)
    c: Horizontal(g0)
    c: Horizontal(g2)
    c: Vertical(g1)
    c: Vertical(g3)
    c: Symmetric(g0,g2,g-1)
    c: DistanceX(g0,g0) = 200
    c: DistanceY(g0,g2) = 90
FEATURE [PartDesign::Pad] Pad039
  Direction = (1,1,1)
  Length = 4
  Length2 = 100
  Placement = pos=(0,0,0) rot=(0.57735,0.57735,0.57735;2.0944rad)
  Profile = -> Sketch079
  Type = 0
FEATURE [Sketcher::SketchObject] Sketch078
  ExternalGeometry = -> [Pad039]
  FullyConstrained = true
  MapMode = 5
  Placement = pos=(4,-9e-16,9e-16) rot=(0.57735,0.57735,0.57735;2.0944rad)
  Support = -> [Pad039]
  sketch-geometry (48):
    g0: LineSegment StartX=-93 StartY=-45 StartZ=0 EndX=-100 EndY=-45 EndZ=0
    g1: LineSegment StartX=-100 StartY=-45 StartZ=0 EndX=-100 EndY=-41 EndZ=0
    g2: LineSegment StartX=-100 StartY=-41 StartZ=0 EndX=-93 EndY=-41 EndZ=0
    g3: LineSegment StartX=-93 StartY=-41 StartZ=0 EndX=-93 EndY=-45 EndZ=0
    g4: LineSegment StartX=-79 StartY=-45 StartZ=0 EndX=-65 EndY=-45 EndZ=0
    g5: LineSegment StartX=-65 StartY=-45 StartZ=0 EndX=-65 EndY=-41 EndZ=0
    g6: LineSegment StartX=-65 StartY=-41 StartZ=0 EndX=-79 EndY=-41 EndZ=0
    g7: LineSegment StartX=-79 StartY=-41 StartZ=0 EndX=-79 EndY=-45 EndZ=0
    g8: LineSegment StartX=-51 StartY=-45 StartZ=0 EndX=-37 EndY=-45 EndZ=0
    g9: LineSegment StartX=-37 StartY=-45 StartZ=0 EndX=-37 EndY=-41 EndZ=0
    g10: LineSegment StartX=-37 StartY=-41 StartZ=0 EndX=-51 EndY=-41 EndZ=0
    g11: LineSegment StartX=-51 StartY=-41 StartZ=0 EndX=-51 EndY=-45 EndZ=0
    g12: LineSegment StartX=-23 StartY=-45 StartZ=0 EndX=-9 EndY=-45 EndZ=0
    g13: LineSegment StartX=-9 StartY=-45 StartZ=0 EndX=-9 EndY=-41 EndZ=0
    g14: LineSegment StartX=-9 StartY=-41 StartZ=0 EndX=-23 EndY=-41 EndZ=0
    g15: LineSegment StartX=-23 StartY=-41 StartZ=0 EndX=-23 EndY=-45 EndZ=0
    g16: LineSegment StartX=5 StartY=-45 StartZ=0 EndX=19 EndY=-45 EndZ=0
    g17: LineSegment StartX=19 StartY=-45 StartZ=0 EndX=19 EndY=-41 EndZ=0
    g18: LineSegment StartX=19 StartY=-41 StartZ=0 EndX=5 EndY=-41 EndZ=0
    g19: LineSegment StartX=5 StartY=-41 StartZ=0 EndX=5 EndY=-45 EndZ=0
    g20: LineSegment StartX=33 StartY=-45 StartZ=0 EndX=47 EndY=-45 EndZ=0
    g21: LineSegment StartX=47 StartY=-45 StartZ=0 EndX=47 EndY=-41 EndZ=0
    g22: LineSegment StartX=47 StartY=-41 StartZ=0 EndX=33 EndY=-41 EndZ=0
    g23: LineSegment StartX=33 StartY=-41 StartZ=0 EndX=33 EndY=-45 EndZ=0
    g24: LineSegment StartX=61 StartY=-45 StartZ=0 EndX=75 EndY=-45 EndZ=0
    g25: LineSegment StartX=75 StartY=-45 StartZ=0 EndX=75 EndY=-41 EndZ=0
    g26: LineSegment StartX=75 StartY=-41 StartZ=0 EndX=61 EndY=-41 EndZ=0
    g27: LineSegment StartX=61 StartY=-41 StartZ=0 EndX=61 EndY=-45 EndZ=0
    g28: LineSegment StartX=100 StartY=-22.5 StartZ=0 EndX=96 EndY=-22.5 EndZ=0
    g29: LineSegment StartX=96 StartY=-22.5 StartZ=0 EndX=96 EndY=-7.5 EndZ=0
    g30: LineSegment StartX=96 StartY=-7.5 StartZ=0 EndX=100 EndY=-7.5 EndZ=0
    g31: LineSegment StartX=100 StartY=-7.5 StartZ=0 EndX=100 EndY=-22.5 EndZ=0
    g32: LineSegment StartX=100 StartY=7.5 StartZ=0 EndX=96 EndY=7.5 EndZ=0
    g33: LineSegment StartX=96 StartY=7.5 StartZ=0 EndX=96 EndY=22.5 EndZ=0
    g34: LineSegment StartX=96 StartY=22.5 StartZ=0 EndX=100 EndY=22.5 EndZ=0
    g35: LineSegment StartX=100 StartY=22.5 StartZ=0 EndX=100 EndY=7.5 EndZ=0
    g36: LineSegment StartX=100 StartY=37.5 StartZ=0 EndX=96 EndY=37.5 EndZ=0
    g37: LineSegment StartX=96 StartY=37.5 StartZ=0 EndX=96 EndY=45 EndZ=0
    g38: LineSegment StartX=96 StartY=45 StartZ=0 EndX=100 EndY=45 EndZ=0
    g39: LineSegment StartX=100 StartY=45 StartZ=0 EndX=100 EndY=37.5 EndZ=0
    g40: LineSegment StartX=89 StartY=-45 StartZ=0 EndX=89 EndY=-41 EndZ=0
    g41: LineSegment StartX=89 StartY=-41 StartZ=0 EndX=96 EndY=-41 EndZ=0
    g42: LineSegment StartX=96 StartY=-41 StartZ=0 EndX=96 EndY=-37.5 EndZ=0
    g43: LineSegment StartX=96 StartY=-37.5 StartZ=0 EndX=100 EndY=-37.5 EndZ=0
    g44: LineSegment StartX=100 StartY=-37.5 StartZ=0 EndX=100 EndY=-45 EndZ=0
    g45: LineSegment StartX=100 StartY=-45 StartZ=0 EndX=89 EndY=-45 EndZ=0
    g46: Circle CenterX=-23 CenterY=0 CenterZ=0 NormalX=0 NormalY=0 NormalZ=1 AngleXU=0 Radius=25
    g47: Circle CenterX=47 CenterY=0 CenterZ=0 NormalX=0 NormalY=0 NormalZ=1 AngleXU=0 Radius=25
  constraints (143):
    c: Coincident(g0,g1)
    c: Coincident(g1,g2)
    c: Coincident(g2,g3)
    c: Coincident(g3,g0)
    c: Horizontal(g0)
    c: Horizontal(g2)
    c: Vertical(g1)
    c: Vertical(g3)
    c: PointOnObject(g1,g-4)
    c: Coincident(g4,g5)
    c: Coincident(g5,g6)
    c: Coincident(g6,g7)
    c: Coincident(g7,g4)
    c: Horizontal(g4)
    c: Horizontal(g6)
    c: Vertical(g5)
    c: Vertical(g7)
    c: Coincident(g8,g9)
    c: Coincident(g9,g10)
    c: Coincident(g10,g11)
    c: Coincident(g11,g8)
    c: Horizontal(g8)
    c: Horizontal(g10)
    c: Vertical(g9)
    c: Vertical(g11)
    c: Coincident(g12,g13)
    c: Coincident(g13,g14)
    c: Coincident(g14,g15)
    c: Coincident(g15,g12)
    c: Horizontal(g12)
    c: Horizontal(g14)
    c: Vertical(g13)
    c: Vertical(g15)
    c: Coincident(g16,g17)
    c: Coincident(g17,g18)
    c: Coincident(g18,g19)
    c: Coincident(g19,g16)
    c: Horizontal(g16)
    c: Horizontal(g18)
    c: Vertical(g17)
    c: Vertical(g19)
    c: Coincident(g20,g21)
    c: Coincident(g21,g22)
    c: Coincident(g22,g23)
    c: Coincident(g23,g20)
    c: Horizontal(g20)
    c: Horizontal(g22)
    c: Vertical(g21)
    c: Vertical(g23)
    c: Coincident(g24,g25)
    c: Coincident(g25,g26)
    c: Coincident(g26,g27)
    c: Coincident(g27,g24)
    c: Horizontal(g24)
    c: Horizontal(g26)
    c: Vertical(g25)
    c: Vertical(g27)
    c: Horizontal(g2,g5)
    c: Horizontal(g5,g9)
    c: Horizontal(g9,g13)
    c: Horizontal(g13,g17)
    c: Horizontal(g17,g21)
    c: Horizontal(g21,g25)
    c: DistanceX(g0,g0) = 7
    c: DistanceX(g0,g4) = 14
    c: DistanceX(g4,g4) = 14
    c: Equal(g8,g4)
    c: Equal(g8,g12)
    c: Equal(g12,g16)
    c: Equal(g16,g20)
    c: Equal(g20,g24)
    c: DistanceX(g4,g8) = 14
    c: DistanceX(g8,g12) = 14
    c: DistanceX(g12,g16) = 14
    c: DistanceX(g16,g20) = 14
    c: DistanceX(g20,g24) = 14
    c: Coincident(g28,g29)
    c: Coincident(g29,g30)
    c: Coincident(g30,g31)
    c: Coincident(g31,g28)
    c: Horizontal(g28)
    c: Horizontal(g30)
    c: Vertical(g29)
    c: Vertical(g31)
    c: Coincident(g32,g33)
    c: Coincident(g33,g34)
    c: Coincident(g34,g35)
    c: Coincident(g35,g32)
    c: Horizontal(g32)
    c: Horizontal(g34)
    c: Vertical(g33)
    c: Vertical(g35)
    c: Coincident(g36,g37)
    c: Coincident(g37,g38)
    c: Coincident(g38,g39)
    c: Coincident(g39,g36)
    c: Horizontal(g36)
    c: Horizontal(g38)
    c: Vertical(g37)
    c: Vertical(g39)
    c: PointOnObject(g37,g-5)
    c: DistanceY(g36,g38) = 7.5
    c: DistanceY(g32,g34) = 15
    c: Equal(g35,g31)
    c: DistanceY(g30,g32) = 15
    c: Vertical(g36,g32)
    c: Vertical(g32,g28)
    c: DistanceY(g0,g1) = 4
    c: PointOnObject(g0,g-7)
    c: PointOnObject(g4,g-7)
    c: PointOnObject(g8,g-7)
    c: PointOnObject(g12,g-7)
    c: PointOnObject(g16,g-7)
    c: PointOnObject(g20,g-7)
    c: PointOnObject(g24,g-7)
    c: PointOnObject(g40,g-7)
    c: Coincident(g40,g41)
    c: Horizontal(g41)
    c: Coincident(g41,g42)
    c: Vertical(g42)
    c: Coincident(g42,g43)
    c: PointOnObject(g43,g-6)
    c: Horizontal(g43)
    c: Coincident(g43,g44)
    c: Coincident(g44,g-7)
    c: Coincident(g44,g45)
    c: Coincident(g45,g40)
    c: Parallel(g-6,g40)
    c: Horizontal(g40,g25)
    c: DistanceX(g40,g44) = 11
    c: DistanceY(g44,g43) = 7.5
    c: PointOnObject(g30,g-6)
    c: PointOnObject(g34,g-6)
    c: PointOnObject(g36,g-6)
    c: Vertical(g42,g28)
    c: DistanceX(g41,g44) = 4
    c: DistanceY(g43,g28) = 15
    c: PointOnObject(g46,g-1)
    c: Radius(g46) = 25
    c: DistanceX(g46,g44) = 123
    c: PointOnObject(g47,g-1)
    c: Radius(g47) = 25
    c: DistanceX(g46,g47) = 70
FEATURE [PartDesign::Pocket] Pocket035
  BaseFeature = -> Pad039
  Length = 4
  Length2 = 100
  Placement = pos=(0,0,0) rot=(0.57735,0.57735,0.57735;2.0944rad)
  Profile = -> Sketch078
  Type = 0
FEATURE [PartDesign::Fillet] Fillet004
  Base = -> Pocket035 [Edge98]
  BaseFeature = -> Pocket035
  Placement = pos=(0,0,0) rot=(0.57735,0.57735,0.57735;2.0944rad)
  Radius = 65
  SupportTransform = false
FEATURE [PartDesign::Body] Body039  label="UtrustningsBoxSida-V-3"
  Group = -> [Sketch079,Pad039,Sketch078,Pocket035,Fillet004]
  Origin = -> Origin039
  Placement = pos=(3,-402,0) rot=(0,0,1;0rad)
  Tip = -> Fillet004
FEATURE [Sketcher::SketchObject] Sketch080
  FullyConstrained = true
  MapMode = 5
  Placement = pos=(0,0,0) rot=(0.57735,0.57735,0.57735;2.0944rad)
  Support = -> [YZ_Plane040]
  sketch-geometry (4):
    g0: LineSegment StartX=-100 StartY=-45 StartZ=0 EndX=100 EndY=-45 EndZ=0
    g1: LineSegment StartX=100 StartY=-45 StartZ=0 EndX=100 EndY=45 EndZ=0
    g2: LineSegment StartX=100 StartY=45 StartZ=0 EndX=-100 EndY=45 EndZ=0
    g3: LineSegment StartX=-100 StartY=45 StartZ=0 EndX=-100 EndY=-45 EndZ=0
  constraints (11):
    c: Coincident(g0,g1)
    c: Coincident(g1,g2)
    c: Coincident(g2,g3)
    c: Coincident(g3,g0)
    c: Horizontal(g0)
    c: Horizontal(g2)
    c: Vertical(g1)
    c: Vertical(g3)
    c: Symmetric(g0,g2,g-1)
    c: DistanceX(g0,g0) = 200
    c: DistanceY(g0,g2) = 90
FEATURE [PartDesign::Pad] Pad040
  Direction = (1,1,1)
  Length = 4
  Length2 = 100
  Placement = pos=(0,0,0) rot=(0.57735,0.57735,0.57735;2.0944rad)
  Profile = -> Sketch080
  Type = 0
FEATURE [Sketcher::SketchObject] Sketch081
  ExternalGeometry = -> [Pad040]
  FullyConstrained = true
  MapMode = 5
  Placement = pos=(4,-9e-16,9e-16) rot=(0.57735,0.57735,0.57735;2.0944rad)
  Support = -> [Pad040]
  sketch-geometry (48):
    g0: LineSegment StartX=-93 StartY=-45 StartZ=0 EndX=-100 EndY=-45 EndZ=0
    g1: LineSegment StartX=-100 StartY=-45 StartZ=0 EndX=-100 EndY=-41 EndZ=0
    g2: LineSegment StartX=-100 StartY=-41 StartZ=0 EndX=-93 EndY=-41 EndZ=0
    g3: LineSegment StartX=-93 StartY=-41 StartZ=0 EndX=-93 EndY=-45 EndZ=0
    g4: LineSegment StartX=-79 StartY=-45 StartZ=0 EndX=-65 EndY=-45 EndZ=0
    g5: LineSegment StartX=-65 StartY=-45 StartZ=0 EndX=-65 EndY=-41 EndZ=0
    g6: LineSegment StartX=-65 StartY=-41 StartZ=0 EndX=-79 EndY=-41 EndZ=0
    g7: LineSegment StartX=-79 StartY=-41 StartZ=0 EndX=-79 EndY=-45 EndZ=0
    g8: LineSegment StartX=-51 StartY=-45 StartZ=0 EndX=-37 EndY=-45 EndZ=0
    g9: LineSegment StartX=-37 StartY=-45 StartZ=0 EndX=-37 EndY=-41 EndZ=0
    g10: LineSegment StartX=-37 StartY=-41 StartZ=0 EndX=-51 EndY=-41 EndZ=0
    g11: LineSegment StartX=-51 StartY=-41 StartZ=0 EndX=-51 EndY=-45 EndZ=0
    g12: LineSegment StartX=-23 StartY=-45 StartZ=0 EndX=-9 EndY=-45 EndZ=0
    g13: LineSegment StartX=-9 StartY=-45 StartZ=0 EndX=-9 EndY=-41 EndZ=0
    g14: LineSegment StartX=-9 StartY=-41 StartZ=0 EndX=-23 EndY=-41 EndZ=0
    g15: LineSegment StartX=-23 StartY=-41 StartZ=0 EndX=-23 EndY=-45 EndZ=0
    g16: LineSegment StartX=5 StartY=-45 StartZ=0 EndX=19 EndY=-45 EndZ=0
    g17: LineSegment StartX=19 StartY=-45 StartZ=0 EndX=19 EndY=-41 EndZ=0
    g18: LineSegment StartX=19 StartY=-41 StartZ=0 EndX=5 EndY=-41 EndZ=0
    g19: LineSegment StartX=5 StartY=-41 StartZ=0 EndX=5 EndY=-45 EndZ=0
    g20: LineSegment StartX=33 StartY=-45 StartZ=0 EndX=47 EndY=-45 EndZ=0
    g21: LineSegment StartX=47 StartY=-45 StartZ=0 EndX=47 EndY=-41 EndZ=0
    g22: LineSegment StartX=47 StartY=-41 StartZ=0 EndX=33 EndY=-41 EndZ=0
    g23: LineSegment StartX=33 StartY=-41 StartZ=0 EndX=33 EndY=-45 EndZ=0
    g24: LineSegment StartX=61 StartY=-45 StartZ=0 EndX=75 EndY=-45 EndZ=0
    g25: LineSegment StartX=75 StartY=-45 StartZ=0 EndX=75 EndY=-41 EndZ=0
    g26: LineSegment StartX=75 StartY=-41 StartZ=0 EndX=61 EndY=-41 EndZ=0
    g27: LineSegment StartX=61 StartY=-41 StartZ=0 EndX=61 EndY=-45 EndZ=0
    g28: LineSegment StartX=100 StartY=-22.5 StartZ=0 EndX=96 EndY=-22.5 EndZ=0
    g29: LineSegment StartX=96 StartY=-22.5 StartZ=0 EndX=96 EndY=-7.5 EndZ=0
    g30: LineSegment StartX=96 StartY=-7.5 StartZ=0 EndX=100 EndY=-7.5 EndZ=0
    g31: LineSegment StartX=100 StartY=-7.5 StartZ=0 EndX=100 EndY=-22.5 EndZ=0
    g32: LineSegment StartX=100 StartY=7.5 StartZ=0 EndX=96 EndY=7.5 EndZ=0
    g33: LineSegment StartX=96 StartY=7.5 StartZ=0 EndX=96 EndY=22.5 EndZ=0
    g34: LineSegment StartX=96 StartY=22.5 StartZ=0 EndX=100 EndY=22.5 EndZ=0
    g35: LineSegment StartX=100 StartY=22.5 StartZ=0 EndX=100 EndY=7.5 EndZ=0
    g36: LineSegment StartX=100 StartY=37.5 StartZ=0 EndX=96 EndY=37.5 EndZ=0
    g37: LineSegment StartX=96 StartY=37.5 StartZ=0 EndX=96 EndY=45 EndZ=0
    g38: LineSegment StartX=96 StartY=45 StartZ=0 EndX=100 EndY=45 EndZ=0
    g39: LineSegment StartX=100 StartY=45 StartZ=0 EndX=100 EndY=37.5 EndZ=0
    g40: LineSegment StartX=89 StartY=-45 StartZ=0 EndX=89 EndY=-41 EndZ=0
    g41: LineSegment StartX=89 StartY=-41 StartZ=0 EndX=96 EndY=-41 EndZ=0
    g42: LineSegment StartX=96 StartY=-41 StartZ=0 EndX=96 EndY=-37.5 EndZ=0
    g43: LineSegment StartX=96 StartY=-37.5 StartZ=0 EndX=100 EndY=-37.5 EndZ=0
    g44: LineSegment StartX=100 StartY=-37.5 StartZ=0 EndX=100 EndY=-45 EndZ=0
    g45: LineSegment StartX=100 StartY=-45 StartZ=0 EndX=89 EndY=-45 EndZ=0
    g46: Circle CenterX=-23 CenterY=0 CenterZ=0 NormalX=0 NormalY=0 NormalZ=1 AngleXU=0 Radius=25
    g47: Circle CenterX=47 CenterY=0 CenterZ=0 NormalX=0 NormalY=0 NormalZ=1 AngleXU=0 Radius=25
  constraints (143):
    c: Coincident(g0,g1)
    c: Coincident(g1,g2)
    c: Coincident(g2,g3)
    c: Coincident(g3,g0)
    c: Horizontal(g0)
    c: Horizontal(g2)
    c: Vertical(g1)
    c: Vertical(g3)
    c: PointOnObject(g1,g-4)
    c: Coincident(g4,g5)
    c: Coincident(g5,g6)
    c: Coincident(g6,g7)
    c: Coincident(g7,g4)
    c: Horizontal(g4)
    c: Horizontal(g6)
    c: Vertical(g5)
    c: Vertical(g7)
    c: Coincident(g8,g9)
    c: Coincident(g9,g10)
    c: Coincident(g10,g11)
    c: Coincident(g11,g8)
    c: Horizontal(g8)
    c: Horizontal(g10)
    c: Vertical(g9)
    c: Vertical(g11)
    c: Coincident(g12,g13)
    c: Coincident(g13,g14)
    c: Coincident(g14,g15)
    c: Coincident(g15,g12)
    c: Horizontal(g12)
    c: Horizontal(g14)
    c: Vertical(g13)
    c: Vertical(g15)
    c: Coincident(g16,g17)
    c: Coincident(g17,g18)
    c: Coincident(g18,g19)
    c: Coincident(g19,g16)
    c: Horizontal(g16)
    c: Horizontal(g18)
    c: Vertical(g17)
    c: Vertical(g19)
    c: Coincident(g20,g21)
    c: Coincident(g21,g22)
    c: Coincident(g22,g23)
    c: Coincident(g23,g20)
    c: Horizontal(g20)
    c: Horizontal(g22)
    c: Vertical(g21)
    c: Vertical(g23)
    c: Coincident(g24,g25)
    c: Coincident(g25,g26)
    c: Coincident(g26,g27)
    c: Coincident(g27,g24)
    c: Horizontal(g24)
    c: Horizontal(g26)
    c: Vertical(g25)
    c: Vertical(g27)
    c: Horizontal(g2,g5)
    c: Horizontal(g5,g9)
    c: Horizontal(g9,g13)
    c: Horizontal(g13,g17)
    c: Horizontal(g17,g21)
    c: Horizontal(g21,g25)
    c: DistanceX(g0,g0) = 7
    c: DistanceX(g0,g4) = 14
    c: DistanceX(g4,g4) = 14
    c: Equal(g8,g4)
    c: Equal(g8,g12)
    c: Equal(g12,g16)
    c: Equal(g16,g20)
    c: Equal(g20,g24)
    c: DistanceX(g4,g8) = 14
    c: DistanceX(g8,g12) = 14
    c: DistanceX(g12,g16) = 14
    c: DistanceX(g16,g20) = 14
    c: DistanceX(g20,g24) = 14
    c: Coincident(g28,g29)
    c: Coincident(g29,g30)
    c: Coincident(g30,g31)
    c: Coincident(g31,g28)
    c: Horizontal(g28)
    c: Horizontal(g30)
    c: Vertical(g29)
    c: Vertical(g31)
    c: Coincident(g32,g33)
    c: Coincident(g33,g34)
    c: Coincident(g34,g35)
    c: Coincident(g35,g32)
    c: Horizontal(g32)
    c: Horizontal(g34)
    c: Vertical(g33)
    c: Vertical(g35)
    c: Coincident(g36,g37)
    c: Coincident(g37,g38)
    c: Coincident(g38,g39)
    c: Coincident(g39,g36)
    c: Horizontal(g36)
    c: Horizontal(g38)
    c: Vertical(g37)
    c: Vertical(g39)
    c: PointOnObject(g37,g-5)
    c: DistanceY(g36,g38) = 7.5
    c: DistanceY(g32,g34) = 15
    c: Equal(g35,g31)
    c: DistanceY(g30,g32) = 15
    c: Vertical(g36,g32)
    c: Vertical(g32,g28)
    c: DistanceY(g0,g1) = 4
    c: PointOnObject(g0,g-7)
    c: PointOnObject(g4,g-7)
    c: PointOnObject(g8,g-7)
    c: PointOnObject(g12,g-7)
    c: PointOnObject(g16,g-7)
    c: PointOnObject(g20,g-7)
    c: PointOnObject(g24,g-7)
    c: PointOnObject(g40,g-7)
    c: Coincident(g40,g41)
    c: Horizontal(g41)
    c: Coincident(g41,g42)
    c: Vertical(g42)
    c: Coincident(g42,g43)
    c: PointOnObject(g43,g-6)
    c: Horizontal(g43)
    c: Coincident(g43,g44)
    c: Coincident(g44,g-7)
    c: Coincident(g44,g45)
    c: Coincident(g45,g40)
    c: Parallel(g-6,g40)
    c: Horizontal(g40,g25)
    c: DistanceX(g40,g44) = 11
    c: DistanceY(g44,g43) = 7.5
    c: PointOnObject(g30,g-6)
    c: PointOnObject(g34,g-6)
    c: PointOnObject(g36,g-6)
    c: Vertical(g42,g28)
    c: DistanceX(g41,g44) = 4
    c: DistanceY(g43,g28) = 15
    c: PointOnObject(g46,g-1)
    c: Radius(g46) = 25
    c: DistanceX(g46,g44) = 123
    c: PointOnObject(g47,g-1)
    c: Radius(g47) = 25
    c: DistanceX(g46,g47) = 70
FEATURE [PartDesign::Pocket] Pocket036
  BaseFeature = -> Pad040
  Length = 4
  Length2 = 100
  Placement = pos=(0,0,0) rot=(0.57735,0.57735,0.57735;2.0944rad)
  Profile = -> Sketch081
  Type = 0
FEATURE [PartDesign::Fillet] Fillet005
  Base = -> Pocket036 [Edge98]
  BaseFeature = -> Pocket036
  Placement = pos=(0,0,0) rot=(0.57735,0.57735,0.57735;2.0944rad)
  Radius = 65
  SupportTransform = false
FEATURE [PartDesign::Body] Body040  label="UtrustningsBoxSida-H-3"
  Group = -> [Sketch080,Pad040,Sketch081,Pocket036,Fillet005]
  Origin = -> Origin040
  Placement = pos=(327,-402,0) rot=(0,0,1;0rad)
  Tip = -> Fillet005
FEATURE [Sketcher::SketchObject] Sketch082
  FullyConstrained = true
  MapMode = 5
  Placement = pos=(0,0,0) rot=(1,0,0;1.5708rad)
  Support = -> [XZ_Plane041]
  sketch-geometry (4):
    g0: LineSegment StartX=-164 StartY=-45 StartZ=0 EndX=164 EndY=-45 EndZ=0
    g1: LineSegment StartX=164 StartY=-45 StartZ=0 EndX=164 EndY=45 EndZ=0
    g2: LineSegment StartX=164 StartY=45 StartZ=0 EndX=-164 EndY=45 EndZ=0
    g3: LineSegment StartX=-164 StartY=45 StartZ=0 EndX=-164 EndY=-45 EndZ=0
  constraints (11):
    c: Coincident(g0,g1)
    c: Coincident(g1,g2)
    c: Coincident(g2,g3)
    c: Coincident(g3,g0)
    c: Horizontal(g0)
    c: Horizontal(g2)
    c: Vertical(g1)
    c: Vertical(g3)
    c: Symmetric(g0,g1,g-1)
    c: DistanceX(g0,g0) = 328
    c: DistanceY(g0,g2) = 90
FEATURE [PartDesign::Pad] Pad041
  Direction = (1,1,1)
  Length = 4
  Length2 = 100
  Placement = pos=(0,0,0) rot=(1,0,0;1.5708rad)
  Profile = -> Sketch082
  Type = 0
FEATURE [Sketcher::SketchObject] Sketch083
  ExternalGeometry = -> [Pad041]
  FullyConstrained = true
  MapMode = 5
  Placement = pos=(0,-4,1.8e-15) rot=(1,0,0;1.5708rad)
  Support = -> [Pad041]
  sketch-geometry (71):
    g0: Circle CenterX=-83.33 CenterY=0 CenterZ=0 NormalX=0 NormalY=0 NormalZ=1 AngleXU=0 Radius=25
    g1: Circle CenterX=0 CenterY=0 CenterZ=0 NormalX=0 NormalY=0 NormalZ=1 AngleXU=0 Radius=25
    g2: Circle CenterX=83.33 CenterY=0 CenterZ=0 NormalX=0 NormalY=0 NormalZ=1 AngleXU=0 Radius=25
    g3: LineSegment StartX=-160 StartY=-37.5 StartZ=0 EndX=-164 EndY=-37.5 EndZ=0
    g4: LineSegment StartX=-164 StartY=-37.5 StartZ=0 EndX=-164 EndY=-22.5 EndZ=0
    g5: LineSegment StartX=-164 StartY=-22.5 StartZ=0 EndX=-160 EndY=-22.5 EndZ=0
    g6: LineSegment StartX=-160 StartY=-22.5 StartZ=0 EndX=-160 EndY=-37.5 EndZ=0
    g7: LineSegment StartX=-160 StartY=-7.5 StartZ=0 EndX=-164 EndY=-7.5 EndZ=0
    g8: LineSegment StartX=-164 StartY=-7.5 StartZ=0 EndX=-164 EndY=7.5 EndZ=0
    g9: LineSegment StartX=-164 StartY=7.5 StartZ=0 EndX=-160 EndY=7.5 EndZ=0
    g10: LineSegment StartX=-160 StartY=7.5 StartZ=0 EndX=-160 EndY=-7.5 EndZ=0
    g11: LineSegment StartX=-160 StartY=22.5 StartZ=0 EndX=-164 EndY=22.5 EndZ=0
    g12: LineSegment StartX=-164 StartY=22.5 StartZ=0 EndX=-164 EndY=37.5 EndZ=0
    g13: LineSegment StartX=-164 StartY=37.5 StartZ=0 EndX=-160 EndY=37.5 EndZ=0
    g14: LineSegment StartX=-160 StartY=37.5 StartZ=0 EndX=-160 EndY=22.5 EndZ=0
    g15: LineSegment StartX=160 StartY=-37.5 StartZ=0 EndX=164 EndY=-37.5 EndZ=0
    g16: LineSegment StartX=164 StartY=-37.5 StartZ=0 EndX=164 EndY=-22.5 EndZ=0
    g17: LineSegment StartX=164 StartY=-22.5 StartZ=0 EndX=160 EndY=-22.5 EndZ=0
    g18: LineSegment StartX=160 StartY=-22.5 StartZ=0 EndX=160 EndY=-37.5 EndZ=0
    g19: LineSegment StartX=160 StartY=-7.5 StartZ=0 EndX=164 EndY=-7.5 EndZ=0
    g20: LineSegment StartX=164 StartY=-7.5 StartZ=0 EndX=164 EndY=7.5 EndZ=0
    g21: LineSegment StartX=164 StartY=7.5 StartZ=0 EndX=160 EndY=7.5 EndZ=0
    g22: LineSegment StartX=160 StartY=7.5 StartZ=0 EndX=160 EndY=-7.5 EndZ=0
    g23: LineSegment StartX=160 StartY=22.5 StartZ=0 EndX=164 EndY=22.5 EndZ=0
    g24: LineSegment StartX=164 StartY=22.5 StartZ=0 EndX=164 EndY=37.5 EndZ=0
    g25: LineSegment StartX=164 StartY=37.5 StartZ=0 EndX=160 EndY=37.5 EndZ=0
    g26: LineSegment StartX=160 StartY=37.5 StartZ=0 EndX=160 EndY=22.5 EndZ=0
    g27: LineSegment StartX=-156.55 StartY=-41 StartZ=0 EndX=-141.64 EndY=-41 EndZ=0
    g28: LineSegment StartX=-141.64 StartY=-41 StartZ=0 EndX=-141.64 EndY=-45 EndZ=0
    g29: LineSegment StartX=-141.64 StartY=-45 StartZ=0 EndX=-156.55 EndY=-45 EndZ=0
    g30: LineSegment StartX=-156.55 StartY=-45 StartZ=0 EndX=-156.55 EndY=-41 EndZ=0
    g31: LineSegment StartX=-126.73 StartY=-41 StartZ=0 EndX=-111.82 EndY=-41 EndZ=0
    g32: LineSegment StartX=-111.82 StartY=-41 StartZ=0 EndX=-111.82 EndY=-45 EndZ=0
    g33: LineSegment StartX=-111.82 StartY=-45 StartZ=0 EndX=-126.73 EndY=-45 EndZ=0
    g34: LineSegment StartX=-126.73 StartY=-45 StartZ=0 EndX=-126.73 EndY=-41 EndZ=0
    g35: LineSegment StartX=-96.91 StartY=-41 StartZ=0 EndX=-82 EndY=-41 EndZ=0
    g36: LineSegment StartX=-82 StartY=-41 StartZ=0 EndX=-82 EndY=-45 EndZ=0
    g37: LineSegment StartX=-82 StartY=-45 StartZ=0 EndX=-96.91 EndY=-45 EndZ=0
    g38: LineSegment StartX=-96.91 StartY=-45 StartZ=0 EndX=-96.91 EndY=-41 EndZ=0
    g39: LineSegment StartX=-67.09 StartY=-41 StartZ=0 EndX=-52.18 EndY=-41 EndZ=0
    g40: LineSegment StartX=-52.18 StartY=-41 StartZ=0 EndX=-52.18 EndY=-45 EndZ=0
    g41: LineSegment StartX=-52.18 StartY=-45 StartZ=0 EndX=-67.09 EndY=-45 EndZ=0
    g42: LineSegment StartX=-67.09 StartY=-45 StartZ=0 EndX=-67.09 EndY=-41 EndZ=0
    g43: LineSegment StartX=-37.27 StartY=-41 StartZ=0 EndX=-22.36 EndY=-41 EndZ=0
    g44: LineSegment StartX=-22.36 StartY=-41 StartZ=0 EndX=-22.36 EndY=-45 EndZ=0
    g45: LineSegment StartX=-22.36 StartY=-45 StartZ=0 EndX=-37.27 EndY=-45 EndZ=0
    g46: LineSegment StartX=-37.27 StartY=-45 StartZ=0 EndX=-37.27 EndY=-41 EndZ=0
    g47: LineSegment StartX=-7.45 StartY=-41 StartZ=0 EndX=7.46 EndY=-41 EndZ=0
    g48: LineSegment StartX=7.46 StartY=-41 StartZ=0 EndX=7.46 EndY=-45 EndZ=0
    g49: LineSegment StartX=7.46 StartY=-45 StartZ=0 EndX=-7.45 EndY=-45 EndZ=0
    g50: LineSegment StartX=-7.45 StartY=-45 StartZ=0 EndX=-7.45 EndY=-41 EndZ=0
    g51: LineSegment StartX=22.37 StartY=-41 StartZ=0 EndX=37.28 EndY=-41 EndZ=0
    g52: LineSegment StartX=37.28 StartY=-41 StartZ=0 EndX=37.28 EndY=-45 EndZ=0
    g53: LineSegment StartX=37.28 StartY=-45 StartZ=0 EndX=22.37 EndY=-45 EndZ=0
    g54: LineSegment StartX=22.37 StartY=-45 StartZ=0 EndX=22.37 EndY=-41 EndZ=0
    g55: LineSegment StartX=52.19 StartY=-41 StartZ=0 EndX=67.1 EndY=-41 EndZ=0
    g56: LineSegment StartX=67.1 StartY=-41 StartZ=0 EndX=67.1 EndY=-45 EndZ=0
    g57: LineSegment StartX=67.1 StartY=-45 StartZ=0 EndX=52.19 EndY=-45 EndZ=0
    g58: LineSegment StartX=52.19 StartY=-45 StartZ=0 EndX=52.19 EndY=-41 EndZ=0
    g59: LineSegment StartX=82.01 StartY=-41 StartZ=0 EndX=96.92 EndY=-41 EndZ=0
    g60: LineSegment StartX=96.92 StartY=-41 StartZ=0 EndX=96.92 EndY=-45 EndZ=0
    g61: LineSegment StartX=96.92 StartY=-45 StartZ=0 EndX=82.01 EndY=-45 EndZ=0
    g62: LineSegment StartX=82.01 StartY=-45 StartZ=0 EndX=82.01 EndY=-41 EndZ=0
    g63: LineSegment StartX=111.83 StartY=-41 StartZ=0 EndX=126.74 EndY=-41 EndZ=0
    g64: LineSegment StartX=126.74 StartY=-41 StartZ=0 EndX=126.74 EndY=-45 EndZ=0
    g65: LineSegment StartX=126.74 StartY=-45 StartZ=0 EndX=111.83 EndY=-45 EndZ=0
    g66: LineSegment StartX=111.83 StartY=-45 StartZ=0 EndX=111.83 EndY=-41 EndZ=0
    g67: LineSegment StartX=141.65 StartY=-41 StartZ=0 EndX=156.56 EndY=-41 EndZ=0
    g68: LineSegment StartX=156.56 StartY=-41 StartZ=0 EndX=156.56 EndY=-45 EndZ=0
    g69: LineSegment StartX=156.56 StartY=-45 StartZ=0 EndX=141.65 EndY=-45 EndZ=0
    g70: LineSegment StartX=141.65 StartY=-45 StartZ=0 EndX=141.65 EndY=-41 EndZ=0
  constraints (212):
    c: PointOnObject(g0,g-1)
    c: Coincident(g1,g-1)
    c: PointOnObject(g2,g-1)
    c: Radius(g1) = 25
    c: Radius(g0) = 25
    c: Radius(g2) = 25
    c: DistanceX(g0,g1) = 83.33
    c: DistanceX(g1,g2) = 83.33
    c: Coincident(g3,g4)
    c: Coincident(g4,g5)
    c: Coincident(g5,g6)
    c: Coincident(g6,g3)
    c: Horizontal(g3)
    c: Horizontal(g5)
    c: Vertical(g4)
    c: Vertical(g6)
    c: Coincident(g7,g8)
    c: Coincident(g8,g9)
    c: Coincident(g9,g10)
    c: Coincident(g10,g7)
    c: Horizontal(g7)
    c: Horizontal(g9)
    c: Vertical(g8)
    c: Vertical(g10)
    c: Coincident(g11,g12)
    c: Coincident(g12,g13)
    c: Coincident(g13,g14)
    c: Coincident(g14,g11)
    c: Horizontal(g11)
    c: Horizontal(g13)
    c: Vertical(g12)
    c: Vertical(g14)
    c: Vertical(g3,g-3)
    c: Vertical(g7,g4)
    c: Vertical(g11,g8)
    c: Vertical(g5,g7)
    c: Vertical(g9,g11)
    c: DistanceY(g-3,g3) = 7.5
    c: DistanceY(g3,g4) = 15
    c: Equal(g4,g8)
    c: Equal(g8,g12)
    c: DistanceY(g4,g7) = 15
    c: DistanceY(g8,g11) = 15
    c: Coincident(g15,g16)
    c: Coincident(g16,g17)
    c: Coincident(g17,g18)
    c: Coincident(g18,g15)
    c: Horizontal(g15)
    c: Horizontal(g17)
    c: Vertical(g16)
    c: Vertical(g18)
    c: Coincident(g19,g20)
    c: Coincident(g20,g21)
    c: Coincident(g21,g22)
    c: Coincident(g22,g19)
    c: Horizontal(g19)
    c: Horizontal(g21)
    c: Vertical(g20)
    c: Vertical(g22)
    c: Coincident(g23,g24)
    c: Coincident(g24,g25)
    c: Coincident(g25,g26)
    c: Coincident(g26,g23)
    c: Horizontal(g23)
    c: Horizontal(g25)
    c: Vertical(g24)
    c: Vertical(g26)
    c: Vertical(g19,g16)
    c: Vertical(g23,g20)
    c: Vertical(g17,g19)
    c: Vertical(g21,g23)
    c: DistanceY(g15,g16) = 15
    c: Equal(g16,g20)
    c: Equal(g20,g24)
    c: DistanceY(g16,g19) = 15
    c: DistanceY(g20,g23) = 15
    c: Vertical(g15,g-4)
    c: DistanceY(g-4,g15) = 7.5
    c: DistanceX(g15,g15) = 4
    c: DistanceX(g3,g3) = 4
    c: Coincident(g27,g28)
    c: Coincident(g28,g29)
    c: Coincident(g29,g30)
    c: Coincident(g30,g27)
    c: Horizontal(g27)
    c: Horizontal(g29)
    c: Vertical(g28)
    c: Vertical(g30)
    c: Coincident(g31,g32)
    c: Coincident(g32,g33)
    c: Coincident(g33,g34)
    c: Coincident(g34,g31)
    c: Horizontal(g31)
    c: Horizontal(g33)
    c: Vertical(g32)
    c: Vertical(g34)
    c: Coincident(g35,g36)
    c: Coincident(g36,g37)
    c: Coincident(g37,g38)
    c: Coincident(g38,g35)
    c: Horizontal(g35)
    c: Horizontal(g37)
    c: Vertical(g36)
    c: Vertical(g38)
    c: Coincident(g39,g40)
    c: Coincident(g40,g41)
    c: Coincident(g41,g42)
    c: Coincident(g42,g39)
    c: Horizontal(g39)
    c: Horizontal(g41)
    c: Vertical(g40)
    c: Vertical(g42)
    c: Coincident(g43,g44)
    c: Coincident(g44,g45)
    c: Coincident(g45,g46)
    c: Coincident(g46,g43)
    c: Horizontal(g43)
    c: Horizontal(g45)
    c: Vertical(g44)
    c: Vertical(g46)
    c: Coincident(g47,g48)
    c: Coincident(g48,g49)
    c: Coincident(g49,g50)
    c: Coincident(g50,g47)
    c: Horizontal(g47)
    c: Horizontal(g49)
    c: Vertical(g48)
    c: Vertical(g50)
    c: Coincident(g51,g52)
    c: Coincident(g52,g53)
    c: Coincident(g53,g54)
    c: Coincident(g54,g51)
    c: Horizontal(g51)
    c: Horizontal(g53)
    c: Vertical(g52)
    c: Vertical(g54)
    c: Coincident(g55,g56)
    c: Coincident(g56,g57)
    c: Coincident(g57,g58)
    c: Coincident(g58,g55)
    c: Horizontal(g55)
    c: Horizontal(g57)
    c: Vertical(g56)
    c: Vertical(g58)
    c: Coincident(g59,g60)
    c: Coincident(g60,g61)
    c: Coincident(g61,g62)
    c: Coincident(g62,g59)
    c: Horizontal(g59)
    c: Horizontal(g61)
    c: Vertical(g60)
    c: Vertical(g62)
    c: Coincident(g63,g64)
    c: Coincident(g64,g65)
    c: Coincident(g65,g66)
    c: Coincident(g66,g63)
    c: Horizontal(g63)
    c: Horizontal(g65)
    c: Vertical(g64)
    c: Vertical(g66)
    c: Coincident(g67,g68)
    c: Coincident(g68,g69)
    c: Coincident(g69,g70)
    c: Coincident(g70,g67)
    c: Horizontal(g67)
    c: Horizontal(g69)
    c: Vertical(g68)
    c: Vertical(g70)
    c: Horizontal(g27,g31)
    c: Horizontal(g31,g35)
    c: Horizontal(g35,g39)
    c: Horizontal(g39,g43)
    c: Horizontal(g43,g47)
    c: Horizontal(g47,g51)
    c: Horizontal(g51,g55)
    c: Horizontal(g55,g59)
    c: Horizontal(g59,g63)
    c: Horizontal(g63,g67)
    c: Horizontal(g28,g32)
    c: Horizontal(g32,g36)
    c: Horizontal(g36,g40)
    c: Horizontal(g40,g44)
    c: Horizontal(g44,g48)
    c: Horizontal(g48,g52)
    c: Horizontal(g52,g56)
    c: Horizontal(g56,g60)
    c: Horizontal(g60,g64)
    c: Horizontal(g64,g68)
    c: Horizontal(g-3,g29)
    c: DistanceX(g29,g28) = 14.91
    c: Equal(g29,g69)
    c: Equal(g69,g65)
    c: Equal(g61,g65)
    c: Equal(g61,g57)
    c: Equal(g57,g53)
    c: Equal(g53,g49)
    c: Equal(g49,g45)
    c: Equal(g45,g41)
    c: Equal(g37,g41)
    c: Equal(g33,g37)
    c: DistanceX(g-3,g29) = 7.45
    c: DistanceX(g28,g33) = 14.91
    c: DistanceX(g32,g37) = 14.91
    c: DistanceX(g36,g41) = 14.91
    c: DistanceX(g40,g45) = 14.91
    c: DistanceX(g44,g49) = 14.91
    c: DistanceX(g48,g53) = 14.91
    c: DistanceX(g52,g57) = 14.91
    c: DistanceX(g56,g61) = 14.91
    c: DistanceX(g60,g65) = 14.91
    c: DistanceX(g64,g69) = 14.91
    c: DistanceY(g-3,g27) = 4
FEATURE [PartDesign::Pocket] Pocket037
  BaseFeature = -> Pad041
  Length = 4
  Length2 = 100
  Placement = pos=(0,0,0) rot=(1,0,0;1.5708rad)
  Profile = -> Sketch083
  Type = 0
FEATURE [PartDesign::Body] Body041  label="UtrustningsBoxBakkant-4"
  Group = -> [Sketch082,Pad041,Sketch083,Pocket037]
  Origin = -> Origin041
  Placement = pos=(500,-302,0) rot=(0,0,1;0rad)
  Tip = -> Pocket037
FEATURE [Sketcher::SketchObject] Sketch085
  FullyConstrained = true
  MapMode = 5
  Support = -> [XY_Plane042]
  sketch-geometry (4):
    g0: LineSegment StartX=164 StartY=-100 StartZ=0 EndX=-164 EndY=-100 EndZ=0
    g1: LineSegment StartX=-164 StartY=-100 StartZ=0 EndX=-164 EndY=100 EndZ=0
    g2: LineSegment StartX=-164 StartY=100 StartZ=0 EndX=164 EndY=100 EndZ=0
    g3: LineSegment StartX=164 StartY=100 StartZ=0 EndX=164 EndY=-100 EndZ=0
  constraints (11):
    c: Coincident(g0,g1)
    c: Coincident(g1,g2)
    c: Coincident(g2,g3)
    c: Coincident(g3,g0)
    c: Horizontal(g0)
    c: Horizontal(g2)
    c: Vertical(g1)
    c: Vertical(g3)
    c: Symmetric(g1,g0,g-1)
    c: DistanceX(g1,g2) = 328
    c: DistanceY(g0,g1) = 200
FEATURE [PartDesign::Pad] Pad042
  Direction = (1,1,1)
  Length = 4
  Length2 = 100
  Profile = -> Sketch085
  Type = 0
FEATURE [Sketcher::SketchObject] Sketch084
  ExternalGeometry = -> [Pad042]
  FullyConstrained = true
  MapMode = 5
  Placement = pos=(0,0,4) rot=(0,0,1;0rad)
  Support = -> [Pad042]
  sketch-geometry (124):
    g0: LineSegment StartX=-164 StartY=100 StartZ=0 EndX=-156.55 EndY=100 EndZ=0
    g1: LineSegment StartX=-156.55 StartY=100 StartZ=0 EndX=-156.55 EndY=96 EndZ=0
    g2: LineSegment StartX=-156.55 StartY=96 StartZ=0 EndX=-164 EndY=96 EndZ=0
    g3: LineSegment StartX=-164 StartY=96 StartZ=0 EndX=-164 EndY=100 EndZ=0
    g4: LineSegment StartX=-141.64 StartY=100 StartZ=0 EndX=-126.73 EndY=100 EndZ=0
    g5: LineSegment StartX=-126.73 StartY=100 StartZ=0 EndX=-126.73 EndY=96 EndZ=0
    g6: LineSegment StartX=-126.73 StartY=96 StartZ=0 EndX=-141.64 EndY=96 EndZ=0
    g7: LineSegment StartX=-141.64 StartY=96 StartZ=0 EndX=-141.64 EndY=100 EndZ=0
    g8: LineSegment StartX=-111.82 StartY=100 StartZ=0 EndX=-96.91 EndY=100 EndZ=0
    g9: LineSegment StartX=-96.91 StartY=100 StartZ=0 EndX=-96.91 EndY=96 EndZ=0
    g10: LineSegment StartX=-96.91 StartY=96 StartZ=0 EndX=-111.82 EndY=96 EndZ=0
    g11: LineSegment StartX=-111.82 StartY=96 StartZ=0 EndX=-111.82 EndY=100 EndZ=0
    g12: LineSegment StartX=-82 StartY=100 StartZ=0 EndX=-67.09 EndY=100 EndZ=0
    g13: LineSegment StartX=-67.09 StartY=100 StartZ=0 EndX=-67.09 EndY=96 EndZ=0
    g14: LineSegment StartX=-67.09 StartY=96 StartZ=0 EndX=-82 EndY=96 EndZ=0
    g15: LineSegment StartX=-82 StartY=96 StartZ=0 EndX=-82 EndY=100 EndZ=0
    g16: LineSegment StartX=-52.18 StartY=100 StartZ=0 EndX=-37.27 EndY=100 EndZ=0
    g17: LineSegment StartX=-37.27 StartY=100 StartZ=0 EndX=-37.27 EndY=96 EndZ=0
    g18: LineSegment StartX=-37.27 StartY=96 StartZ=0 EndX=-52.18 EndY=96 EndZ=0
    g19: LineSegment StartX=-52.18 StartY=96 StartZ=0 EndX=-52.18 EndY=100 EndZ=0
    g20: LineSegment StartX=-22.36 StartY=100 StartZ=0 EndX=-7.45 EndY=100 EndZ=0
    g21: LineSegment StartX=-7.45 StartY=100 StartZ=0 EndX=-7.45 EndY=96 EndZ=0
    g22: LineSegment StartX=-7.45 StartY=96 StartZ=0 EndX=-22.36 EndY=96 EndZ=0
    g23: LineSegment StartX=-22.36 StartY=96 StartZ=0 EndX=-22.36 EndY=100 EndZ=0
    g24: LineSegment StartX=7.46 StartY=100 StartZ=0 EndX=22.37 EndY=100 EndZ=0
    g25: LineSegment StartX=22.37 StartY=100 StartZ=0 EndX=22.37 EndY=96 EndZ=0
    g26: LineSegment StartX=22.37 StartY=96 StartZ=0 EndX=7.46 EndY=96 EndZ=0
    g27: LineSegment StartX=7.46 StartY=96 StartZ=0 EndX=7.46 EndY=100 EndZ=0
    g28: LineSegment StartX=37.28 StartY=100 StartZ=0 EndX=52.19 EndY=100 EndZ=0
    g29: LineSegment StartX=52.19 StartY=100 StartZ=0 EndX=52.19 EndY=96 EndZ=0
    g30: LineSegment StartX=52.19 StartY=96 StartZ=0 EndX=37.28 EndY=96 EndZ=0
    g31: LineSegment StartX=37.28 StartY=96 StartZ=0 EndX=37.28 EndY=100 EndZ=0
    g32: LineSegment StartX=67.1 StartY=100 StartZ=0 EndX=82.01 EndY=100 EndZ=0
    g33: LineSegment StartX=82.01 StartY=100 StartZ=0 EndX=82.01 EndY=96 EndZ=0
    g34: LineSegment StartX=82.01 StartY=96 StartZ=0 EndX=67.1 EndY=96 EndZ=0
    g35: LineSegment StartX=67.1 StartY=96 StartZ=0 EndX=67.1 EndY=100 EndZ=0
    g36: LineSegment StartX=96.92 StartY=100 StartZ=0 EndX=111.83 EndY=100 EndZ=0
    g37: LineSegment StartX=111.83 StartY=100 StartZ=0 EndX=111.83 EndY=96 EndZ=0
    g38: LineSegment StartX=111.83 StartY=96 StartZ=0 EndX=96.92 EndY=96 EndZ=0
    g39: LineSegment StartX=96.92 StartY=96 StartZ=0 EndX=96.92 EndY=100 EndZ=0
    g40: LineSegment StartX=126.74 StartY=100 StartZ=0 EndX=141.65 EndY=100 EndZ=0
    g41: LineSegment StartX=141.65 StartY=100 StartZ=0 EndX=141.65 EndY=96 EndZ=0
    g42: LineSegment StartX=141.65 StartY=96 StartZ=0 EndX=126.74 EndY=96 EndZ=0
    g43: LineSegment StartX=126.74 StartY=96 StartZ=0 EndX=126.74 EndY=100 EndZ=0
    g44: LineSegment StartX=156.56 StartY=100 StartZ=0 EndX=164.01 EndY=100 EndZ=0
    g45: LineSegment StartX=164.01 StartY=100 StartZ=0 EndX=164.01 EndY=96 EndZ=0
    g46: LineSegment StartX=164.01 StartY=96 StartZ=0 EndX=156.56 EndY=96 EndZ=0
    g47: LineSegment StartX=156.56 StartY=96 StartZ=0 EndX=156.56 EndY=100 EndZ=0
    g48: LineSegment StartX=-164 StartY=89 StartZ=0 EndX=-160 EndY=89 EndZ=0
    g49: LineSegment StartX=-160 StartY=89 StartZ=0 EndX=-160 EndY=75 EndZ=0
    g50: LineSegment StartX=-160 StartY=75 StartZ=0 EndX=-164 EndY=75 EndZ=0
    g51: LineSegment StartX=-164 StartY=75 StartZ=0 EndX=-164 EndY=89 EndZ=0
    g52: LineSegment StartX=-164 StartY=61 StartZ=0 EndX=-160 EndY=61 EndZ=0
    g53: LineSegment StartX=-160 StartY=61 StartZ=0 EndX=-160 EndY=47 EndZ=0
    g54: LineSegment StartX=-160 StartY=47 StartZ=0 EndX=-164 EndY=47 EndZ=0
    g55: LineSegment StartX=-164 StartY=47 StartZ=0 EndX=-164 EndY=61 EndZ=0
    g56: LineSegment StartX=-164 StartY=33 StartZ=0 EndX=-160 EndY=33 EndZ=0
    g57: LineSegment StartX=-160 StartY=33 StartZ=0 EndX=-160 EndY=19 EndZ=0
    g58: LineSegment StartX=-160 StartY=19 StartZ=0 EndX=-164 EndY=19 EndZ=0
    g59: LineSegment StartX=-164 StartY=19 StartZ=0 EndX=-164 EndY=33 EndZ=0
    g60: LineSegment StartX=-164 StartY=5 StartZ=0 EndX=-160 EndY=5 EndZ=0
    g61: LineSegment StartX=-160 StartY=5 StartZ=0 EndX=-160 EndY=-9 EndZ=0
    g62: LineSegment StartX=-160 StartY=-9 StartZ=0 EndX=-164 EndY=-9 EndZ=0
    g63: LineSegment StartX=-164 StartY=-9 StartZ=0 EndX=-164 EndY=5 EndZ=0
    g64: LineSegment StartX=-164 StartY=-23 StartZ=0 EndX=-160 EndY=-23 EndZ=0
    g65: LineSegment StartX=-160 StartY=-23 StartZ=0 EndX=-160 EndY=-37 EndZ=0
    g66: LineSegment StartX=-160 StartY=-37 StartZ=0 EndX=-164 EndY=-37 EndZ=0
    g67: LineSegment StartX=-164 StartY=-37 StartZ=0 EndX=-164 EndY=-23 EndZ=0
    g68: LineSegment StartX=-164 StartY=-51 StartZ=0 EndX=-160 EndY=-51 EndZ=0
    g69: LineSegment StartX=-160 StartY=-51 StartZ=0 EndX=-160 EndY=-65 EndZ=0
    g70: LineSegment StartX=-160 StartY=-65 StartZ=0 EndX=-164 EndY=-65 EndZ=0
    g71: LineSegment StartX=-164 StartY=-65 StartZ=0 EndX=-164 EndY=-51 EndZ=0
    g72: LineSegment StartX=-164 StartY=-79 StartZ=0 EndX=-160 EndY=-79 EndZ=0
    g73: LineSegment StartX=-160 StartY=-79 StartZ=0 EndX=-160 EndY=-93 EndZ=0
    g74: LineSegment StartX=-160 StartY=-93 StartZ=0 EndX=-164 EndY=-93 EndZ=0
    g75: LineSegment StartX=-164 StartY=-93 StartZ=0 EndX=-164 EndY=-79 EndZ=0
    g76: LineSegment StartX=160 StartY=89 StartZ=0 EndX=164 EndY=89 EndZ=0
    g77: LineSegment StartX=164 StartY=89 StartZ=0 EndX=164 EndY=75 EndZ=0
    g78: LineSegment StartX=164 StartY=75 StartZ=0 EndX=160 EndY=75 EndZ=0
    g79: LineSegment StartX=160 StartY=75 StartZ=0 EndX=160 EndY=89 EndZ=0
    g80: LineSegment StartX=160 StartY=61 StartZ=0 EndX=164 EndY=61 EndZ=0
    g81: LineSegment StartX=164 StartY=61 StartZ=0 EndX=164 EndY=47 EndZ=0
    g82: LineSegment StartX=164 StartY=47 StartZ=0 EndX=160 EndY=47 EndZ=0
    g83: LineSegment StartX=160 StartY=47 StartZ=0 EndX=160 EndY=61 EndZ=0
    g84: LineSegment StartX=160 StartY=33 StartZ=0 EndX=164 EndY=33 EndZ=0
    g85: LineSegment StartX=164 StartY=33 StartZ=0 EndX=164 EndY=19 EndZ=0
    g86: LineSegment StartX=164 StartY=19 StartZ=0 EndX=160 EndY=19 EndZ=0
    g87: LineSegment StartX=160 StartY=19 StartZ=0 EndX=160 EndY=33 EndZ=0
    g88: LineSegment StartX=160 StartY=5 StartZ=0 EndX=164 EndY=5 EndZ=0
    g89: LineSegment StartX=164 StartY=5 StartZ=0 EndX=164 EndY=-9 EndZ=0
    g90: LineSegment StartX=164 StartY=-9 StartZ=0 EndX=160 EndY=-9 EndZ=0
    g91: LineSegment StartX=160 StartY=-9 StartZ=0 EndX=160 EndY=5 EndZ=0
    g92: LineSegment StartX=160 StartY=-23 StartZ=0 EndX=164 EndY=-23 EndZ=0
    g93: LineSegment StartX=164 StartY=-23 StartZ=0 EndX=164 EndY=-37 EndZ=0
    g94: LineSegment StartX=164 StartY=-37 StartZ=0 EndX=160 EndY=-37 EndZ=0
    g95: LineSegment StartX=160 StartY=-37 StartZ=0 EndX=160 EndY=-23 EndZ=0
    g96: LineSegment StartX=160 StartY=-51 StartZ=0 EndX=164 EndY=-51 EndZ=0
    g97: LineSegment StartX=164 StartY=-51 StartZ=0 EndX=164 EndY=-65 EndZ=0
    g98: LineSegment StartX=164 StartY=-65 StartZ=0 EndX=160 EndY=-65 EndZ=0
    g99: LineSegment StartX=160 StartY=-65 StartZ=0 EndX=160 EndY=-51 EndZ=0
    g100: LineSegment StartX=160 StartY=-79 StartZ=0 EndX=164 EndY=-79 EndZ=0
    g101: LineSegment StartX=164 StartY=-79 StartZ=0 EndX=164 EndY=-93 EndZ=0
    g102: LineSegment StartX=164 StartY=-93 StartZ=0 EndX=160 EndY=-93 EndZ=0
    g103: LineSegment StartX=160 StartY=-93 StartZ=0 EndX=160 EndY=-79 EndZ=0
    g104: Circle CenterX=0 CenterY=75 CenterZ=0 NormalX=0 NormalY=0 NormalZ=1 AngleXU=0 Radius=10
    g105: Circle CenterX=0 CenterY=25 CenterZ=0 NormalX=0 NormalY=0 NormalZ=1 AngleXU=0 Radius=10
    g106: Circle CenterX=0 CenterY=-25 CenterZ=0 NormalX=0 NormalY=0 NormalZ=1 AngleXU=0 Radius=10
    g107: Circle CenterX=0 CenterY=-75 CenterZ=0 NormalX=0 NormalY=0 NormalZ=1 AngleXU=0 Radius=10
    g108: Circle CenterX=54.7 CenterY=75 CenterZ=0 NormalX=0 NormalY=0 NormalZ=1 AngleXU=0 Radius=10
    g109: Circle CenterX=54.7 CenterY=25 CenterZ=0 NormalX=0 NormalY=0 NormalZ=1 AngleXU=0 Radius=10
    g110: Circle CenterX=54.7 CenterY=-25 CenterZ=0 NormalX=0 NormalY=0 NormalZ=1 AngleXU=0 Radius=10
    g111: Circle CenterX=54.7 CenterY=-75 CenterZ=0 NormalX=0 NormalY=0 NormalZ=1 AngleXU=0 Radius=10
    g112: Circle CenterX=109.4 CenterY=75 CenterZ=0 NormalX=0 NormalY=0 NormalZ=1 AngleXU=0 Radius=10
    g113: Circle CenterX=109.4 CenterY=25 CenterZ=0 NormalX=0 NormalY=0 NormalZ=1 AngleXU=0 Radius=10
    g114: Circle CenterX=109.4 CenterY=-25 CenterZ=0 NormalX=0 NormalY=0 NormalZ=1 AngleXU=0 Radius=10
    g115: Circle CenterX=109.4 CenterY=-75 CenterZ=0 NormalX=0 NormalY=0 NormalZ=1 AngleXU=0 Radius=10
    g116: Circle CenterX=-109.4 CenterY=75 CenterZ=0 NormalX=0 NormalY=0 NormalZ=1 AngleXU=0 Radius=10
    g117: Circle CenterX=-109.4 CenterY=25 CenterZ=0 NormalX=0 NormalY=0 NormalZ=1 AngleXU=0 Radius=10
    g118: Circle CenterX=-109.4 CenterY=-25 CenterZ=0 NormalX=0 NormalY=0 NormalZ=1 AngleXU=0 Radius=10
    g119: Circle CenterX=-109.4 CenterY=-75 CenterZ=0 NormalX=0 NormalY=0 NormalZ=1 AngleXU=0 Radius=10
    g120: Circle CenterX=-54.7 CenterY=75 CenterZ=0 NormalX=0 NormalY=0 NormalZ=1 AngleXU=0 Radius=10
    g121: Circle CenterX=-54.7 CenterY=25 CenterZ=0 NormalX=0 NormalY=0 NormalZ=1 AngleXU=0 Radius=10
    g122: Circle CenterX=-54.7 CenterY=-25 CenterZ=0 NormalX=0 NormalY=0 NormalZ=1 AngleXU=0 Radius=10
    g123: Circle CenterX=-54.7 CenterY=-75 CenterZ=0 NormalX=0 NormalY=0 NormalZ=1 AngleXU=0 Radius=10
  constraints (372):
    c: Coincident(g0,g1)
    c: Coincident(g1,g2)
    c: Coincident(g2,g3)
    c: Coincident(g3,g0)
    c: Horizontal(g0)
    c: Horizontal(g2)
    c: Vertical(g1)
    c: Vertical(g3)
    c: Coincident(g4,g5)
    c: Coincident(g5,g6)
    c: Coincident(g6,g7)
    c: Coincident(g7,g4)
    c: Horizontal(g4)
    c: Horizontal(g6)
    c: Vertical(g5)
    c: Vertical(g7)
    c: Coincident(g8,g9)
    c: Coincident(g9,g10)
    c: Coincident(g10,g11)
    c: Coincident(g11,g8)
    c: Horizontal(g8)
    c: Horizontal(g10)
    c: Vertical(g9)
    c: Vertical(g11)
    c: Coincident(g12,g13)
    c: Coincident(g13,g14)
    c: Coincident(g14,g15)
    c: Coincident(g15,g12)
    c: Horizontal(g12)
    c: Horizontal(g14)
    c: Vertical(g13)
    c: Vertical(g15)
    c: Coincident(g16,g17)
    c: Coincident(g17,g18)
    c: Coincident(g18,g19)
    c: Coincident(g19,g16)
    c: Horizontal(g16)
    c: Horizontal(g18)
    c: Vertical(g17)
    c: Vertical(g19)
    c: Coincident(g20,g21)
    c: Coincident(g21,g22)
    c: Coincident(g22,g23)
    c: Coincident(g23,g20)
    c: Horizontal(g20)
    c: Horizontal(g22)
    c: Vertical(g21)
    c: Vertical(g23)
    c: Horizontal(g0,g4)
    c: Horizontal(g4,g8)
    c: Horizontal(g8,g12)
    c: Horizontal(g12,g16)
    c: Horizontal(g16,g20)
    c: Horizontal(g1,g5)
    c: Horizontal(g5,g9)
    c: Horizontal(g9,g13)
    c: Horizontal(g13,g17)
    c: Horizontal(g17,g21)
    c: PointOnObject(g0,g-4)
    c: PointOnObject(g0,g-5)
    c: DistanceX(g0,g0) = 7.45
    c: DistanceX(g0,g4) = 14.91
    c: DistanceX(g4,g4) = 14.91
    c: Equal(g4,g8)
    c: Equal(g8,g12)
    c: Equal(g12,g16)
    c: Equal(g20,g16)
    c: DistanceX(g16,g20) = 14.91
    c: DistanceX(g12,g16) = 14.91
    c: DistanceX(g4,g8) = 14.91
    c: DistanceX(g8,g12) = 14.91
    c: Coincident(g24,g25)
    c: Coincident(g25,g26)
    c: Coincident(g26,g27)
    c: Coincident(g27,g24)
    c: Horizontal(g24)
    c: Horizontal(g26)
    c: Vertical(g25)
    c: Vertical(g27)
    c: Coincident(g28,g29)
    c: Coincident(g29,g30)
    c: Coincident(g30,g31)
    c: Coincident(g31,g28)
    c: Horizontal(g28)
    c: Horizontal(g30)
    c: Vertical(g29)
    c: Vertical(g31)
    c: Coincident(g32,g33)
    c: Coincident(g33,g34)
    c: Coincident(g34,g35)
    c: Coincident(g35,g32)
    c: Horizontal(g32)
    c: Horizontal(g34)
    c: Vertical(g33)
    c: Vertical(g35)
    c: Coincident(g36,g37)
    c: Coincident(g37,g38)
    c: Coincident(g38,g39)
    c: Coincident(g39,g36)
    c: Horizontal(g36)
    c: Horizontal(g38)
    c: Vertical(g37)
    c: Vertical(g39)
    c: Horizontal(g24,g28)
    c: Horizontal(g28,g32)
    c: Horizontal(g32,g36)
    c: Horizontal(g25,g29)
    c: Horizontal(g29,g33)
    c: Horizontal(g33,g37)
    c: Equal(g24,g28)
    c: Equal(g28,g32)
    c: Equal(g36,g32)
    c: DistanceX(g32,g36) = 14.91
    c: DistanceX(g28,g32) = 14.91
    c: DistanceX(g24,g28) = 14.91
    c: DistanceX(g20,g24) = 14.91
    c: Horizontal(g24,g20)
    c: Horizontal(g21,g26)
    c: Equal(g22,g26)
    c: Coincident(g40,g41)
    c: Coincident(g41,g42)
    c: Coincident(g42,g43)
    c: Coincident(g43,g40)
    c: Horizontal(g40)
    c: Horizontal(g42)
    c: Vertical(g41)
    c: Vertical(g43)
    c: Horizontal(g42,g37)
    c: Horizontal(g40,g36)
    c: Equal(g36,g40)
    c: DistanceX(g36,g40) = 14.91
    c: Coincident(g44,g45)
    c: Coincident(g45,g46)
    c: Coincident(g46,g47)
    c: Coincident(g47,g44)
    c: Horizontal(g44)
    c: Horizontal(g46)
    c: Vertical(g45)
    c: Vertical(g47)
    c: Horizontal(g40,g44)
    c: Horizontal(g41,g46)
    c: DistanceX(g40,g44) = 14.91
    c: DistanceX(g44,g44) = 7.45
    c: DistanceY(g2,g0) = 4
    c: Coincident(g48,g49)
    c: Coincident(g49,g50)
    c: Coincident(g50,g51)
    c: Coincident(g51,g48)
    c: Horizontal(g48)
    c: Horizontal(g50)
    c: Vertical(g49)
    c: Vertical(g51)
    c: PointOnObject(g48,g-5)
    c: Coincident(g52,g53)
    c: Coincident(g53,g54)
    c: Coincident(g54,g55)
    c: Coincident(g55,g52)
    c: Horizontal(g52)
    c: Horizontal(g54)
    c: Vertical(g53)
    c: Vertical(g55)
    c: PointOnObject(g52,g-5)
    c: Coincident(g56,g57)
    c: Coincident(g57,g58)
    c: Coincident(g58,g59)
    c: Coincident(g59,g56)
    c: Horizontal(g56)
    c: Horizontal(g58)
    c: Vertical(g57)
    c: Vertical(g59)
    c: PointOnObject(g56,g-5)
    c: Coincident(g60,g61)
    c: Coincident(g61,g62)
    c: Coincident(g62,g63)
    c: Coincident(g63,g60)
    c: Horizontal(g60)
    c: Horizontal(g62)
    c: Vertical(g61)
    c: Vertical(g63)
    c: PointOnObject(g60,g-5)
    c: Coincident(g64,g65)
    c: Coincident(g65,g66)
    c: Coincident(g66,g67)
    c: Coincident(g67,g64)
    c: Horizontal(g64)
    c: Horizontal(g66)
    c: Vertical(g65)
    c: Vertical(g67)
    c: PointOnObject(g64,g-5)
    c: Vertical(g53,g49)
    c: Vertical(g49,g57)
    c: Vertical(g57,g61)
    c: DistanceY(g48,g2) = 7
    c: DistanceY(g50,g48) = 14
    c: Equal(g49,g53)
    c: Equal(g53,g57)
    c: Equal(g57,g61)
    c: Equal(g61,g65)
    c: DistanceY(g52,g50) = 14
    c: DistanceY(g56,g54) = 14
    c: DistanceY(g60,g58) = 14
    c: DistanceY(g64,g62) = 14
    c: Coincident(g68,g69)
    c: Coincident(g69,g70)
    c: Coincident(g70,g71)
    c: Coincident(g71,g68)
    c: Horizontal(g68)
    c: Horizontal(g70)
    c: Vertical(g69)
    c: Vertical(g71)
    c: Coincident(g72,g73)
    c: Coincident(g73,g74)
    c: Coincident(g74,g75)
    c: Coincident(g75,g72)
    c: Horizontal(g72)
    c: Horizontal(g74)
    c: Vertical(g73)
    c: Vertical(g75)
    c: Equal(g69,g73)
    c: DistanceY(g72,g70) = 14
    c: PointOnObject(g74,g-5)
    c: PointOnObject(g70,g-5)
    c: Vertical(g65,g68)
    c: Vertical(g61,g64)
    c: DistanceY(g68,g66) = 14
    c: Equal(g69,g65)
    c: DistanceX(g48,g48) = 4
    c: Vertical(g69,g72)
    c: Coincident(g76,g77)
    c: Coincident(g77,g78)
    c: Coincident(g78,g79)
    c: Coincident(g79,g76)
    c: Horizontal(g76)
    c: Horizontal(g78)
    c: Vertical(g77)
    c: Vertical(g79)
    c: Coincident(g80,g81)
    c: Coincident(g81,g82)
    c: Coincident(g82,g83)
    c: Coincident(g83,g80)
    c: Horizontal(g80)
    c: Horizontal(g82)
    c: Vertical(g81)
    c: Vertical(g83)
    c: Coincident(g84,g85)
    c: Coincident(g85,g86)
    c: Coincident(g86,g87)
    c: Coincident(g87,g84)
    c: Horizontal(g84)
    c: Horizontal(g86)
    c: Vertical(g85)
    c: Vertical(g87)
    c: Coincident(g88,g89)
    c: Coincident(g89,g90)
    c: Coincident(g90,g91)
    c: Coincident(g91,g88)
    c: Horizontal(g88)
    c: Horizontal(g90)
    c: Vertical(g89)
    c: Vertical(g91)
    c: Coincident(g92,g93)
    c: Coincident(g93,g94)
    c: Coincident(g94,g95)
    c: Coincident(g95,g92)
    c: Horizontal(g92)
    c: Horizontal(g94)
    c: Vertical(g93)
    c: Vertical(g95)
    c: Vertical(g81,g77)
    c: Vertical(g77,g85)
    c: Vertical(g85,g89)
    c: DistanceY(g78,g76) = 14
    c: Equal(g77,g81)
    c: Equal(g81,g85)
    c: Equal(g85,g89)
    c: Equal(g89,g93)
    c: DistanceY(g80,g78) = 14
    c: DistanceY(g84,g82) = 14
    c: DistanceY(g88,g86) = 14
    c: DistanceY(g92,g90) = 14
    c: Coincident(g96,g97)
    c: Coincident(g97,g98)
    c: Coincident(g98,g99)
    c: Coincident(g99,g96)
    c: Horizontal(g96)
    c: Horizontal(g98)
    c: Vertical(g97)
    c: Vertical(g99)
    c: Coincident(g100,g101)
    c: Coincident(g101,g102)
    c: Coincident(g102,g103)
    c: Coincident(g103,g100)
    c: Horizontal(g100)
    c: Horizontal(g102)
    c: Vertical(g101)
    c: Vertical(g103)
    c: Equal(g97,g101)
    c: DistanceY(g100,g98) = 14
    c: Vertical(g93,g96)
    c: Vertical(g89,g92)
    c: DistanceY(g96,g94) = 14
    c: Equal(g97,g93)
    c: Equal(g48,g76) = 4
    c: Vertical(g97,g100)
    c: Vertical(g80,g78)
    c: Vertical(g82,g86)
    c: Vertical(g86,g90)
    c: Vertical(g90,g94)
    c: Vertical(g94,g98)
    c: Vertical(g98,g102)
    c: DistanceY(g76,g45) = 7
    c: PointOnObject(g104,g-2)
    c: PointOnObject(g105,g-2)
    c: PointOnObject(g106,g-2)
    c: PointOnObject(g107,g-2)
    c: Radius(g107) = 10
    c: Equal(g107,g106)
    c: Equal(g106,g105)
    c: Equal(g105,g104)
    c: DistanceY(g106,g-1) = 25
    c: DistanceY(g107,g106) = 50
    c: DistanceY(g-1,g105) = 25
    c: DistanceY(g105,g104) = 50
    c: Equal(g107,g111) = 10
    c: Equal(g111,g110)
    c: Equal(g110,g109)
    c: Equal(g109,g108)
    c: DistanceY(g111,g110) = 50
    c: DistanceY(g109,g108) = 50
    c: DistanceY(g110,g109) = 50
    c: Vertical(g111,g110)
    c: Vertical(g110,g109)
    c: Vertical(g109,g108)
    c: Equal(g115,g114)
    c: Equal(g114,g113)
    c: Equal(g113,g112)
    c: DistanceY(g115,g114) = 50
    c: DistanceY(g113,g112) = 50
    c: DistanceY(g114,g113) = 50
    c: Vertical(g115,g114)
    c: Vertical(g114,g113)
    c: Vertical(g113,g112)
    c: DistanceX(g107,g111) = 54.7
    c: DistanceX(g111,g115) = 54.7
    c: Horizontal(g107,g111)
    c: Horizontal(g111,g115)
    c: Radius(g115) = 10
    c: Equal(g119,g118)
    c: Equal(g118,g117)
    c: Equal(g117,g116)
    c: DistanceY(g119,g118) = 50
    c: DistanceY(g117,g116) = 50
    c: DistanceY(g118,g117) = 50
    c: Vertical(g119,g118)
    c: Vertical(g118,g117)
    c: Vertical(g117,g116)
    c: Equal(g123,g122)
    c: Equal(g122,g121)
    c: Equal(g121,g120)
    c: DistanceY(g123,g122) = 50
    c: DistanceY(g121,g120) = 50
    c: DistanceY(g122,g121) = 50
    c: Vertical(g123,g122)
    c: Vertical(g122,g121)
    c: Vertical(g121,g120)
    c: DistanceX(g119,g123) = 54.7
    c: Horizontal(g119,g123)
    c: Equal(g115,g123) = 10
    c: Horizontal(g107,g123)
    c: DistanceX(g123,g107) = 54.7
    c: Radius(g119) = 10
    c: PointOnObject(g76,g-6)
FEATURE [PartDesign::Pocket] Pocket038
  BaseFeature = -> Pad042
  Length = 4
  Length2 = 100
  Profile = -> Sketch084
  Type = 0
FEATURE [PartDesign::Body] Body042  label="UtrustningsBoxBotten-4"
  Group = -> [Sketch085,Pad042,Sketch084,Pocket038]
  Origin = -> Origin042
  Placement = pos=(500,-402,-45) rot=(0,0,1;0rad)
  Tip = -> Pocket038
FEATURE [Sketcher::SketchObject] Sketch086
  FullyConstrained = true
  MapMode = 5
  Placement = pos=(0,0,0) rot=(0.57735,0.57735,0.57735;2.0944rad)
  Support = -> [YZ_Plane043]
  sketch-geometry (4):
    g0: LineSegment StartX=-100 StartY=-45 StartZ=0 EndX=100 EndY=-45 EndZ=0
    g1: LineSegment StartX=100 StartY=-45 StartZ=0 EndX=100 EndY=45 EndZ=0
    g2: LineSegment StartX=100 StartY=45 StartZ=0 EndX=-100 EndY=45 EndZ=0
    g3: LineSegment StartX=-100 StartY=45 StartZ=0 EndX=-100 EndY=-45 EndZ=0
  constraints (11):
    c: Coincident(g0,g1)
    c: Coincident(g1,g2)
    c: Coincident(g2,g3)
    c: Coincident(g3,g0)
    c: Horizontal(g0)
    c: Horizontal(g2)
    c: Vertical(g1)
    c: Vertical(g3)
    c: Symmetric(g0,g2,g-1)
    c: DistanceX(g0,g0) = 200
    c: DistanceY(g0,g2) = 90
FEATURE [PartDesign::Pad] Pad043
  Direction = (1,1,1)
  Length = 4
  Length2 = 100
  Placement = pos=(0,0,0) rot=(0.57735,0.57735,0.57735;2.0944rad)
  Profile = -> Sketch086
  Type = 0
FEATURE [Sketcher::SketchObject] Sketch087
  ExternalGeometry = -> [Pad043]
  FullyConstrained = true
  MapMode = 5
  Placement = pos=(4,-9e-16,9e-16) rot=(0.57735,0.57735,0.57735;2.0944rad)
  Support = -> [Pad043]
  sketch-geometry (48):
    g0: LineSegment StartX=-93 StartY=-45 StartZ=0 EndX=-100 EndY=-45 EndZ=0
    g1: LineSegment StartX=-100 StartY=-45 StartZ=0 EndX=-100 EndY=-41 EndZ=0
    g2: LineSegment StartX=-100 StartY=-41 StartZ=0 EndX=-93 EndY=-41 EndZ=0
    g3: LineSegment StartX=-93 StartY=-41 StartZ=0 EndX=-93 EndY=-45 EndZ=0
    g4: LineSegment StartX=-79 StartY=-45 StartZ=0 EndX=-65 EndY=-45 EndZ=0
    g5: LineSegment StartX=-65 StartY=-45 StartZ=0 EndX=-65 EndY=-41 EndZ=0
    g6: LineSegment StartX=-65 StartY=-41 StartZ=0 EndX=-79 EndY=-41 EndZ=0
    g7: LineSegment StartX=-79 StartY=-41 StartZ=0 EndX=-79 EndY=-45 EndZ=0
    g8: LineSegment StartX=-51 StartY=-45 StartZ=0 EndX=-37 EndY=-45 EndZ=0
    g9: LineSegment StartX=-37 StartY=-45 StartZ=0 EndX=-37 EndY=-41 EndZ=0
    g10: LineSegment StartX=-37 StartY=-41 StartZ=0 EndX=-51 EndY=-41 EndZ=0
    g11: LineSegment StartX=-51 StartY=-41 StartZ=0 EndX=-51 EndY=-45 EndZ=0
    g12: LineSegment StartX=-23 StartY=-45 StartZ=0 EndX=-9 EndY=-45 EndZ=0
    g13: LineSegment StartX=-9 StartY=-45 StartZ=0 EndX=-9 EndY=-41 EndZ=0
    g14: LineSegment StartX=-9 StartY=-41 StartZ=0 EndX=-23 EndY=-41 EndZ=0
    g15: LineSegment StartX=-23 StartY=-41 StartZ=0 EndX=-23 EndY=-45 EndZ=0
    g16: LineSegment StartX=5 StartY=-45 StartZ=0 EndX=19 EndY=-45 EndZ=0
    g17: LineSegment StartX=19 StartY=-45 StartZ=0 EndX=19 EndY=-41 EndZ=0
    g18: LineSegment StartX=19 StartY=-41 StartZ=0 EndX=5 EndY=-41 EndZ=0
    g19: LineSegment StartX=5 StartY=-41 StartZ=0 EndX=5 EndY=-45 EndZ=0
    g20: LineSegment StartX=33 StartY=-45 StartZ=0 EndX=47 EndY=-45 EndZ=0
    g21: LineSegment StartX=47 StartY=-45 StartZ=0 EndX=47 EndY=-41 EndZ=0
    g22: LineSegment StartX=47 StartY=-41 StartZ=0 EndX=33 EndY=-41 EndZ=0
    g23: LineSegment StartX=33 StartY=-41 StartZ=0 EndX=33 EndY=-45 EndZ=0
    g24: LineSegment StartX=61 StartY=-45 StartZ=0 EndX=75 EndY=-45 EndZ=0
    g25: LineSegment StartX=75 StartY=-45 StartZ=0 EndX=75 EndY=-41 EndZ=0
    g26: LineSegment StartX=75 StartY=-41 StartZ=0 EndX=61 EndY=-41 EndZ=0
    g27: LineSegment StartX=61 StartY=-41 StartZ=0 EndX=61 EndY=-45 EndZ=0
    g28: LineSegment StartX=100 StartY=-22.5 StartZ=0 EndX=96 EndY=-22.5 EndZ=0
    g29: LineSegment StartX=96 StartY=-22.5 StartZ=0 EndX=96 EndY=-7.5 EndZ=0
    g30: LineSegment StartX=96 StartY=-7.5 StartZ=0 EndX=100 EndY=-7.5 EndZ=0
    g31: LineSegment StartX=100 StartY=-7.5 StartZ=0 EndX=100 EndY=-22.5 EndZ=0
    g32: LineSegment StartX=100 StartY=7.5 StartZ=0 EndX=96 EndY=7.5 EndZ=0
    g33: LineSegment StartX=96 StartY=7.5 StartZ=0 EndX=96 EndY=22.5 EndZ=0
    g34: LineSegment StartX=96 StartY=22.5 StartZ=0 EndX=100 EndY=22.5 EndZ=0
    g35: LineSegment StartX=100 StartY=22.5 StartZ=0 EndX=100 EndY=7.5 EndZ=0
    g36: LineSegment StartX=100 StartY=37.5 StartZ=0 EndX=96 EndY=37.5 EndZ=0
    g37: LineSegment StartX=96 StartY=37.5 StartZ=0 EndX=96 EndY=45 EndZ=0
    g38: LineSegment StartX=96 StartY=45 StartZ=0 EndX=100 EndY=45 EndZ=0
    g39: LineSegment StartX=100 StartY=45 StartZ=0 EndX=100 EndY=37.5 EndZ=0
    g40: LineSegment StartX=89 StartY=-45 StartZ=0 EndX=89 EndY=-41 EndZ=0
    g41: LineSegment StartX=89 StartY=-41 StartZ=0 EndX=96 EndY=-41 EndZ=0
    g42: LineSegment StartX=96 StartY=-41 StartZ=0 EndX=96 EndY=-37.5 EndZ=0
    g43: LineSegment StartX=96 StartY=-37.5 StartZ=0 EndX=100 EndY=-37.5 EndZ=0
    g44: LineSegment StartX=100 StartY=-37.5 StartZ=0 EndX=100 EndY=-45 EndZ=0
    g45: LineSegment StartX=100 StartY=-45 StartZ=0 EndX=89 EndY=-45 EndZ=0
    g46: Circle CenterX=-23 CenterY=0 CenterZ=0 NormalX=0 NormalY=0 NormalZ=1 AngleXU=0 Radius=25
    g47: Circle CenterX=47 CenterY=0 CenterZ=0 NormalX=0 NormalY=0 NormalZ=1 AngleXU=0 Radius=25
  constraints (143):
    c: Coincident(g0,g1)
    c: Coincident(g1,g2)
    c: Coincident(g2,g3)
    c: Coincident(g3,g0)
    c: Horizontal(g0)
    c: Horizontal(g2)
    c: Vertical(g1)
    c: Vertical(g3)
    c: PointOnObject(g1,g-4)
    c: Coincident(g4,g5)
    c: Coincident(g5,g6)
    c: Coincident(g6,g7)
    c: Coincident(g7,g4)
    c: Horizontal(g4)
    c: Horizontal(g6)
    c: Vertical(g5)
    c: Vertical(g7)
    c: Coincident(g8,g9)
    c: Coincident(g9,g10)
    c: Coincident(g10,g11)
    c: Coincident(g11,g8)
    c: Horizontal(g8)
    c: Horizontal(g10)
    c: Vertical(g9)
    c: Vertical(g11)
    c: Coincident(g12,g13)
    c: Coincident(g13,g14)
    c: Coincident(g14,g15)
    c: Coincident(g15,g12)
    c: Horizontal(g12)
    c: Horizontal(g14)
    c: Vertical(g13)
    c: Vertical(g15)
    c: Coincident(g16,g17)
    c: Coincident(g17,g18)
    c: Coincident(g18,g19)
    c: Coincident(g19,g16)
    c: Horizontal(g16)
    c: Horizontal(g18)
    c: Vertical(g17)
    c: Vertical(g19)
    c: Coincident(g20,g21)
    c: Coincident(g21,g22)
    c: Coincident(g22,g23)
    c: Coincident(g23,g20)
    c: Horizontal(g20)
    c: Horizontal(g22)
    c: Vertical(g21)
    c: Vertical(g23)
    c: Coincident(g24,g25)
    c: Coincident(g25,g26)
    c: Coincident(g26,g27)
    c: Coincident(g27,g24)
    c: Horizontal(g24)
    c: Horizontal(g26)
    c: Vertical(g25)
    c: Vertical(g27)
    c: Horizontal(g2,g5)
    c: Horizontal(g5,g9)
    c: Horizontal(g9,g13)
    c: Horizontal(g13,g17)
    c: Horizontal(g17,g21)
    c: Horizontal(g21,g25)
    c: DistanceX(g0,g0) = 7
    c: DistanceX(g0,g4) = 14
    c: DistanceX(g4,g4) = 14
    c: Equal(g8,g4)
    c: Equal(g8,g12)
    c: Equal(g12,g16)
    c: Equal(g16,g20)
    c: Equal(g20,g24)
    c: DistanceX(g4,g8) = 14
    c: DistanceX(g8,g12) = 14
    c: DistanceX(g12,g16) = 14
    c: DistanceX(g16,g20) = 14
    c: DistanceX(g20,g24) = 14
    c: Coincident(g28,g29)
    c: Coincident(g29,g30)
    c: Coincident(g30,g31)
    c: Coincident(g31,g28)
    c: Horizontal(g28)
    c: Horizontal(g30)
    c: Vertical(g29)
    c: Vertical(g31)
    c: Coincident(g32,g33)
    c: Coincident(g33,g34)
    c: Coincident(g34,g35)
    c: Coincident(g35,g32)
    c: Horizontal(g32)
    c: Horizontal(g34)
    c: Vertical(g33)
    c: Vertical(g35)
    c: Coincident(g36,g37)
    c: Coincident(g37,g38)
    c: Coincident(g38,g39)
    c: Coincident(g39,g36)
    c: Horizontal(g36)
    c: Horizontal(g38)
    c: Vertical(g37)
    c: Vertical(g39)
    c: PointOnObject(g37,g-5)
    c: DistanceY(g36,g38) = 7.5
    c: DistanceY(g32,g34) = 15
    c: Equal(g35,g31)
    c: DistanceY(g30,g32) = 15
    c: Vertical(g36,g32)
    c: Vertical(g32,g28)
    c: DistanceY(g0,g1) = 4
    c: PointOnObject(g0,g-7)
    c: PointOnObject(g4,g-7)
    c: PointOnObject(g8,g-7)
    c: PointOnObject(g12,g-7)
    c: PointOnObject(g16,g-7)
    c: PointOnObject(g20,g-7)
    c: PointOnObject(g24,g-7)
    c: PointOnObject(g40,g-7)
    c: Coincident(g40,g41)
    c: Horizontal(g41)
    c: Coincident(g41,g42)
    c: Vertical(g42)
    c: Coincident(g42,g43)
    c: PointOnObject(g43,g-6)
    c: Horizontal(g43)
    c: Coincident(g43,g44)
    c: Coincident(g44,g-7)
    c: Coincident(g44,g45)
    c: Coincident(g45,g40)
    c: Parallel(g-6,g40)
    c: Horizontal(g40,g25)
    c: DistanceX(g40,g44) = 11
    c: DistanceY(g44,g43) = 7.5
    c: PointOnObject(g30,g-6)
    c: PointOnObject(g34,g-6)
    c: PointOnObject(g36,g-6)
    c: Vertical(g42,g28)
    c: DistanceX(g41,g44) = 4
    c: DistanceY(g43,g28) = 15
    c: PointOnObject(g46,g-1)
    c: Radius(g46) = 25
    c: DistanceX(g46,g44) = 123
    c: PointOnObject(g47,g-1)
    c: Radius(g47) = 25
    c: DistanceX(g46,g47) = 70
FEATURE [PartDesign::Pocket] Pocket039
  BaseFeature = -> Pad043
  Length = 4
  Length2 = 100
  Placement = pos=(0,0,0) rot=(0.57735,0.57735,0.57735;2.0944rad)
  Profile = -> Sketch087
  Type = 0
FEATURE [PartDesign::Fillet] Fillet006
  Base = -> Pocket039 [Edge98]
  BaseFeature = -> Pocket039
  Placement = pos=(0,0,0) rot=(0.57735,0.57735,0.57735;2.0944rad)
  Radius = 65
  SupportTransform = false
FEATURE [PartDesign::Body] Body043  label="UtrustningsBoxSida-V-4"
  Group = -> [Sketch086,Pad043,Sketch087,Pocket039,Fillet006]
  Origin = -> Origin043
  Placement = pos=(336,-402,0) rot=(0,0,1;0rad)
  Tip = -> Fillet006
FEATURE [Sketcher::SketchObject] Sketch089
  FullyConstrained = true
  MapMode = 5
  Placement = pos=(0,0,0) rot=(0.57735,0.57735,0.57735;2.0944rad)
  Support = -> [YZ_Plane044]
  sketch-geometry (4):
    g0: LineSegment StartX=-100 StartY=-45 StartZ=0 EndX=100 EndY=-45 EndZ=0
    g1: LineSegment StartX=100 StartY=-45 StartZ=0 EndX=100 EndY=45 EndZ=0
    g2: LineSegment StartX=100 StartY=45 StartZ=0 EndX=-100 EndY=45 EndZ=0
    g3: LineSegment StartX=-100 StartY=45 StartZ=0 EndX=-100 EndY=-45 EndZ=0
  constraints (11):
    c: Coincident(g0,g1)
    c: Coincident(g1,g2)
    c: Coincident(g2,g3)
    c: Coincident(g3,g0)
    c: Horizontal(g0)
    c: Horizontal(g2)
    c: Vertical(g1)
    c: Vertical(g3)
    c: Symmetric(g0,g2,g-1)
    c: DistanceX(g0,g0) = 200
    c: DistanceY(g0,g2) = 90
FEATURE [PartDesign::Pad] Pad044
  Direction = (1,1,1)
  Length = 4
  Length2 = 100
  Placement = pos=(0,0,0) rot=(0.57735,0.57735,0.57735;2.0944rad)
  Profile = -> Sketch089
  Type = 0
FEATURE [Sketcher::SketchObject] Sketch088
  ExternalGeometry = -> [Pad044]
  FullyConstrained = true
  MapMode = 5
  Placement = pos=(4,-9e-16,9e-16) rot=(0.57735,0.57735,0.57735;2.0944rad)
  Support = -> [Pad044]
  sketch-geometry (48):
    g0: LineSegment StartX=-93 StartY=-45 StartZ=0 EndX=-100 EndY=-45 EndZ=0
    g1: LineSegment StartX=-100 StartY=-45 StartZ=0 EndX=-100 EndY=-41 EndZ=0
    g2: LineSegment StartX=-100 StartY=-41 StartZ=0 EndX=-93 EndY=-41 EndZ=0
    g3: LineSegment StartX=-93 StartY=-41 StartZ=0 EndX=-93 EndY=-45 EndZ=0
    g4: LineSegment StartX=-79 StartY=-45 StartZ=0 EndX=-65 EndY=-45 EndZ=0
    g5: LineSegment StartX=-65 StartY=-45 StartZ=0 EndX=-65 EndY=-41 EndZ=0
    g6: LineSegment StartX=-65 StartY=-41 StartZ=0 EndX=-79 EndY=-41 EndZ=0
    g7: LineSegment StartX=-79 StartY=-41 StartZ=0 EndX=-79 EndY=-45 EndZ=0
    g8: LineSegment StartX=-51 StartY=-45 StartZ=0 EndX=-37 EndY=-45 EndZ=0
    g9: LineSegment StartX=-37 StartY=-45 StartZ=0 EndX=-37 EndY=-41 EndZ=0
    g10: LineSegment StartX=-37 StartY=-41 StartZ=0 EndX=-51 EndY=-41 EndZ=0
    g11: LineSegment StartX=-51 StartY=-41 StartZ=0 EndX=-51 EndY=-45 EndZ=0
    g12: LineSegment StartX=-23 StartY=-45 StartZ=0 EndX=-9 EndY=-45 EndZ=0
    g13: LineSegment StartX=-9 StartY=-45 StartZ=0 EndX=-9 EndY=-41 EndZ=0
    g14: LineSegment StartX=-9 StartY=-41 StartZ=0 EndX=-23 EndY=-41 EndZ=0
    g15: LineSegment StartX=-23 StartY=-41 StartZ=0 EndX=-23 EndY=-45 EndZ=0
    g16: LineSegment StartX=5 StartY=-45 StartZ=0 EndX=19 EndY=-45 EndZ=0
    g17: LineSegment StartX=19 StartY=-45 StartZ=0 EndX=19 EndY=-41 EndZ=0
    g18: LineSegment StartX=19 StartY=-41 StartZ=0 EndX=5 EndY=-41 EndZ=0
    g19: LineSegment StartX=5 StartY=-41 StartZ=0 EndX=5 EndY=-45 EndZ=0
    g20: LineSegment StartX=33 StartY=-45 StartZ=0 EndX=47 EndY=-45 EndZ=0
    g21: LineSegment StartX=47 StartY=-45 StartZ=0 EndX=47 EndY=-41 EndZ=0
    g22: LineSegment StartX=47 StartY=-41 StartZ=0 EndX=33 EndY=-41 EndZ=0
    g23: LineSegment StartX=33 StartY=-41 StartZ=0 EndX=33 EndY=-45 EndZ=0
    g24: LineSegment StartX=61 StartY=-45 StartZ=0 EndX=75 EndY=-45 EndZ=0
    g25: LineSegment StartX=75 StartY=-45 StartZ=0 EndX=75 EndY=-41 EndZ=0
    g26: LineSegment StartX=75 StartY=-41 StartZ=0 EndX=61 EndY=-41 EndZ=0
    g27: LineSegment StartX=61 StartY=-41 StartZ=0 EndX=61 EndY=-45 EndZ=0
    g28: LineSegment StartX=100 StartY=-22.5 StartZ=0 EndX=96 EndY=-22.5 EndZ=0
    g29: LineSegment StartX=96 StartY=-22.5 StartZ=0 EndX=96 EndY=-7.5 EndZ=0
    g30: LineSegment StartX=96 StartY=-7.5 StartZ=0 EndX=100 EndY=-7.5 EndZ=0
    g31: LineSegment StartX=100 StartY=-7.5 StartZ=0 EndX=100 EndY=-22.5 EndZ=0
    g32: LineSegment StartX=100 StartY=7.5 StartZ=0 EndX=96 EndY=7.5 EndZ=0
    g33: LineSegment StartX=96 StartY=7.5 StartZ=0 EndX=96 EndY=22.5 EndZ=0
    g34: LineSegment StartX=96 StartY=22.5 StartZ=0 EndX=100 EndY=22.5 EndZ=0
    g35: LineSegment StartX=100 StartY=22.5 StartZ=0 EndX=100 EndY=7.5 EndZ=0
    g36: LineSegment StartX=100 StartY=37.5 StartZ=0 EndX=96 EndY=37.5 EndZ=0
    g37: LineSegment StartX=96 StartY=37.5 StartZ=0 EndX=96 EndY=45 EndZ=0
    g38: LineSegment StartX=96 StartY=45 StartZ=0 EndX=100 EndY=45 EndZ=0
    g39: LineSegment StartX=100 StartY=45 StartZ=0 EndX=100 EndY=37.5 EndZ=0
    g40: LineSegment StartX=89 StartY=-45 StartZ=0 EndX=89 EndY=-41 EndZ=0
    g41: LineSegment StartX=89 StartY=-41 StartZ=0 EndX=96 EndY=-41 EndZ=0
    g42: LineSegment StartX=96 StartY=-41 StartZ=0 EndX=96 EndY=-37.5 EndZ=0
    g43: LineSegment StartX=96 StartY=-37.5 StartZ=0 EndX=100 EndY=-37.5 EndZ=0
    g44: LineSegment StartX=100 StartY=-37.5 StartZ=0 EndX=100 EndY=-45 EndZ=0
    g45: LineSegment StartX=100 StartY=-45 StartZ=0 EndX=89 EndY=-45 EndZ=0
    g46: Circle CenterX=-23 CenterY=0 CenterZ=0 NormalX=0 NormalY=0 NormalZ=1 AngleXU=0 Radius=25
    g47: Circle CenterX=47 CenterY=0 CenterZ=0 NormalX=0 NormalY=0 NormalZ=1 AngleXU=0 Radius=25
  constraints (143):
    c: Coincident(g0,g1)
    c: Coincident(g1,g2)
    c: Coincident(g2,g3)
    c: Coincident(g3,g0)
    c: Horizontal(g0)
    c: Horizontal(g2)
    c: Vertical(g1)
    c: Vertical(g3)
    c: PointOnObject(g1,g-4)
    c: Coincident(g4,g5)
    c: Coincident(g5,g6)
    c: Coincident(g6,g7)
    c: Coincident(g7,g4)
    c: Horizontal(g4)
    c: Horizontal(g6)
    c: Vertical(g5)
    c: Vertical(g7)
    c: Coincident(g8,g9)
    c: Coincident(g9,g10)
    c: Coincident(g10,g11)
    c: Coincident(g11,g8)
    c: Horizontal(g8)
    c: Horizontal(g10)
    c: Vertical(g9)
    c: Vertical(g11)
    c: Coincident(g12,g13)
    c: Coincident(g13,g14)
    c: Coincident(g14,g15)
    c: Coincident(g15,g12)
    c: Horizontal(g12)
    c: Horizontal(g14)
    c: Vertical(g13)
    c: Vertical(g15)
    c: Coincident(g16,g17)
    c: Coincident(g17,g18)
    c: Coincident(g18,g19)
    c: Coincident(g19,g16)
    c: Horizontal(g16)
    c: Horizontal(g18)
    c: Vertical(g17)
    c: Vertical(g19)
    c: Coincident(g20,g21)
    c: Coincident(g21,g22)
    c: Coincident(g22,g23)
    c: Coincident(g23,g20)
    c: Horizontal(g20)
    c: Horizontal(g22)
    c: Vertical(g21)
    c: Vertical(g23)
    c: Coincident(g24,g25)
    c: Coincident(g25,g26)
    c: Coincident(g26,g27)
    c: Coincident(g27,g24)
    c: Horizontal(g24)
    c: Horizontal(g26)
    c: Vertical(g25)
    c: Vertical(g27)
    c: Horizontal(g2,g5)
    c: Horizontal(g5,g9)
    c: Horizontal(g9,g13)
    c: Horizontal(g13,g17)
    c: Horizontal(g17,g21)
    c: Horizontal(g21,g25)
    c: DistanceX(g0,g0) = 7
    c: DistanceX(g0,g4) = 14
    c: DistanceX(g4,g4) = 14
    c: Equal(g8,g4)
    c: Equal(g8,g12)
    c: Equal(g12,g16)
    c: Equal(g16,g20)
    c: Equal(g20,g24)
    c: DistanceX(g4,g8) = 14
    c: DistanceX(g8,g12) = 14
    c: DistanceX(g12,g16) = 14
    c: DistanceX(g16,g20) = 14
    c: DistanceX(g20,g24) = 14
    c: Coincident(g28,g29)
    c: Coincident(g29,g30)
    c: Coincident(g30,g31)
    c: Coincident(g31,g28)
    c: Horizontal(g28)
    c: Horizontal(g30)
    c: Vertical(g29)
    c: Vertical(g31)
    c: Coincident(g32,g33)
    c: Coincident(g33,g34)
    c: Coincident(g34,g35)
    c: Coincident(g35,g32)
    c: Horizontal(g32)
    c: Horizontal(g34)
    c: Vertical(g33)
    c: Vertical(g35)
    c: Coincident(g36,g37)
    c: Coincident(g37,g38)
    c: Coincident(g38,g39)
    c: Coincident(g39,g36)
    c: Horizontal(g36)
    c: Horizontal(g38)
    c: Vertical(g37)
    c: Vertical(g39)
    c: PointOnObject(g37,g-5)
    c: DistanceY(g36,g38) = 7.5
    c: DistanceY(g32,g34) = 15
    c: Equal(g35,g31)
    c: DistanceY(g30,g32) = 15
    c: Vertical(g36,g32)
    c: Vertical(g32,g28)
    c: DistanceY(g0,g1) = 4
    c: PointOnObject(g0,g-7)
    c: PointOnObject(g4,g-7)
    c: PointOnObject(g8,g-7)
    c: PointOnObject(g12,g-7)
    c: PointOnObject(g16,g-7)
    c: PointOnObject(g20,g-7)
    c: PointOnObject(g24,g-7)
    c: PointOnObject(g40,g-7)
    c: Coincident(g40,g41)
    c: Horizontal(g41)
    c: Coincident(g41,g42)
    c: Vertical(g42)
    c: Coincident(g42,g43)
    c: PointOnObject(g43,g-6)
    c: Horizontal(g43)
    c: Coincident(g43,g44)
    c: Coincident(g44,g-7)
    c: Coincident(g44,g45)
    c: Coincident(g45,g40)
    c: Parallel(g-6,g40)
    c: Horizontal(g40,g25)
    c: DistanceX(g40,g44) = 11
    c: DistanceY(g44,g43) = 7.5
    c: PointOnObject(g30,g-6)
    c: PointOnObject(g34,g-6)
    c: PointOnObject(g36,g-6)
    c: Vertical(g42,g28)
    c: DistanceX(g41,g44) = 4
    c: DistanceY(g43,g28) = 15
    c: PointOnObject(g46,g-1)
    c: Radius(g46) = 25
    c: DistanceX(g46,g44) = 123
    c: PointOnObject(g47,g-1)
    c: Radius(g47) = 25
    c: DistanceX(g46,g47) = 70
FEATURE [PartDesign::Pocket] Pocket040
  BaseFeature = -> Pad044
  Length = 4
  Length2 = 100
  Placement = pos=(0,0,0) rot=(0.57735,0.57735,0.57735;2.0944rad)
  Profile = -> Sketch088
  Type = 0
FEATURE [PartDesign::Fillet] Fillet007
  Base = -> Pocket040 [Edge98]
  BaseFeature = -> Pocket040
  Placement = pos=(0,0,0) rot=(0.57735,0.57735,0.57735;2.0944rad)
  Radius = 65
  SupportTransform = false
FEATURE [PartDesign::Body] Body044  label="UtrustningsBoxSida-H-4"
  Group = -> [Sketch089,Pad044,Sketch088,Pocket040,Fillet007]
  Origin = -> Origin044
  Placement = pos=(660,-402,0) rot=(0,0,1;0rad)
  Tip = -> Fillet007
FEATURE [TechDraw::DrawSVGTemplate] Template015
  Height = 297
  Orientation = 1
  Width = 420
FEATURE [TechDraw::DrawViewPart] View016
  CoarseView = false
  Direction = (0,-1,0)
  Focus = 100
  HardHidden = false
  IsoCount = 0
  IsoHidden = false
  IsoVisible = false
  LockPosition = false
  Perspective = false
  Rotation = 0
  Scale = 0.15
  ScaleType = 0
  SeamHidden = false
  SeamVisible = true
  SmoothHidden = false
  SmoothVisible = true
  Source = -> [Pocket025]
  X = 100.881
  XDirection = (1,0,0)
  Y = 224.738
FEATURE [TechDraw::DrawViewDimension] Dimension197
  Arbitrary = false
  ArbitraryTolerances = false
  EqualTolerance = true
  FormatSpec = %.2f
  FormatSpecOverTolerance = %+.2f
  FormatSpecUnderTolerance = %+.2f
  Inverted = false
  LockPosition = false
  MeasureType = 1
  OverTolerance = 0
  References2D = -> [View016]
  Rotation = 0
  Scale = 0.15
  ScaleType = 0
  TheoreticalExact = false
  Type = 1
  UnderTolerance = 0
  X = -0.490757
  Y = -50.2963
FEATURE [TechDraw::DrawViewDimension] Dimension198
  Arbitrary = false
  ArbitraryTolerances = false
  EqualTolerance = true
  FormatSpec = %.2f
  FormatSpecOverTolerance = %+.2f
  FormatSpecUnderTolerance = %+.2f
  Inverted = false
  LockPosition = false
  MeasureType = 1
  OverTolerance = 0
  References2D = -> [View016]
  Rotation = 0
  Scale = 0.15
  ScaleType = 0
  TheoreticalExact = false
  Type = 1
  UnderTolerance = 0
  X = 1.97196
  Y = -43.2258
FEATURE [TechDraw::DrawViewDimension] Dimension199
  Arbitrary = false
  ArbitraryTolerances = false
  EqualTolerance = true
  FormatSpec = %.2f
  FormatSpecOverTolerance = %+.2f
  FormatSpecUnderTolerance = %+.2f
  Inverted = false
  LockPosition = false
  MeasureType = 1
  OverTolerance = 0
  References2D = -> [View016]
  Rotation = 0
  Scale = 0.15
  ScaleType = 0
  TheoreticalExact = false
  Type = 1
  UnderTolerance = 0
  X = 0.773267
  Y = -36.6346
FEATURE [TechDraw::DrawViewDimension] Dimension200
  Arbitrary = false
  ArbitraryTolerances = false
  EqualTolerance = true
  FormatSpec = %.2f
  FormatSpecOverTolerance = %+.2f
  FormatSpecUnderTolerance = %+.2f
  Inverted = false
  LockPosition = false
  MeasureType = 1
  OverTolerance = 0
  References2D = -> [View016]
  Rotation = 0
  Scale = 0.15
  ScaleType = 0
  TheoreticalExact = false
  Type = 1
  UnderTolerance = 0
  X = 0.743631
  Y = -30.2078
FEATURE [TechDraw::DrawViewDimension] Dimension201
  Arbitrary = false
  ArbitraryTolerances = false
  EqualTolerance = true
  FormatSpec = %.2f
  FormatSpecOverTolerance = %+.2f
  FormatSpecUnderTolerance = %+.2f
  Inverted = false
  LockPosition = false
  MeasureType = 1
  OverTolerance = 0
  References2D = -> [View016]
  Rotation = 0
  Scale = 0.15
  ScaleType = 0
  TheoreticalExact = false
  Type = 2
  UnderTolerance = 0
  X = -43.1223
  Y = -19.6162
FEATURE [TechDraw::DrawViewDimension] Dimension202
  Arbitrary = false
  ArbitraryTolerances = false
  EqualTolerance = true
  FormatSpec = %.2f
  FormatSpecOverTolerance = %+.2f
  FormatSpecUnderTolerance = %+.2f
  Inverted = false
  LockPosition = false
  MeasureType = 1
  OverTolerance = 0
  References2D = -> [View016]
  Rotation = 0
  Scale = 0.15
  ScaleType = 0
  TheoreticalExact = false
  Type = 2
  UnderTolerance = 0
  X = -49.2578
  Y = -20.4755
FEATURE [TechDraw::DrawViewDimension] Dimension203
  Arbitrary = false
  ArbitraryTolerances = false
  EqualTolerance = true
  FormatSpec = %.2f
  FormatSpecOverTolerance = %+.2f
  FormatSpecUnderTolerance = %+.2f
  Inverted = false
  LockPosition = false
  MeasureType = 1
  OverTolerance = 0
  References2D = -> [View016]
  Rotation = 0
  Scale = 0.15
  ScaleType = 0
  TheoreticalExact = false
  Type = 2
  UnderTolerance = 0
  X = -54.9303
  Y = -20.6565
FEATURE [TechDraw::DrawViewDimension] Dimension204
  Arbitrary = false
  ArbitraryTolerances = false
  EqualTolerance = true
  FormatSpec = %.2f
  FormatSpecOverTolerance = %+.2f
  FormatSpecUnderTolerance = %+.2f
  Inverted = false
  LockPosition = false
  MeasureType = 1
  OverTolerance = 0
  References2D = -> [View016]
  Rotation = 0
  Scale = 0.15
  ScaleType = 0
  TheoreticalExact = false
  Type = 2
  UnderTolerance = 0
  X = -60.3712
  Y = -19.8595
FEATURE [TechDraw::DrawViewDimension] Dimension205
  Arbitrary = false
  ArbitraryTolerances = false
  EqualTolerance = true
  FormatSpec = %.2f
  FormatSpecOverTolerance = %+.2f
  FormatSpecUnderTolerance = %+.2f
  Inverted = false
  LockPosition = false
  MeasureType = 1
  OverTolerance = 0
  References2D = -> [View016]
  Rotation = 0
  Scale = 0.15
  ScaleType = 0
  TheoreticalExact = false
  Type = 2
  UnderTolerance = 0
  X = 49.9871
  Y = -17.6821
FEATURE [TechDraw::DrawViewDimension] Dimension206
  Arbitrary = false
  ArbitraryTolerances = false
  EqualTolerance = true
  FormatSpec = %.2f
  FormatSpecOverTolerance = %+.2f
  FormatSpecUnderTolerance = %+.2f
  Inverted = false
  LockPosition = false
  MeasureType = 1
  OverTolerance = 0
  References2D = -> [View016]
  Rotation = 0
  Scale = 0.15
  ScaleType = 0
  TheoreticalExact = false
  Type = 1
  UnderTolerance = 0
  X = -41.4792
  Y = 33.8481
FEATURE [TechDraw::DrawViewDimension] Dimension207
  Arbitrary = false
  ArbitraryTolerances = false
  EqualTolerance = true
  FormatSpec = %.2f
  FormatSpecOverTolerance = %+.2f
  FormatSpecUnderTolerance = %+.2f
  Inverted = false
  LockPosition = false
  MeasureType = 1
  OverTolerance = 0
  References2D = -> [View016]
  Rotation = 0
  Scale = 0.15
  ScaleType = 0
  TheoreticalExact = false
  Type = 1
  UnderTolerance = 0
  X = -41.9679
  Y = 40.7345
FEATURE [TechDraw::DrawViewDimension] Dimension208
  Arbitrary = false
  ArbitraryTolerances = false
  EqualTolerance = true
  FormatSpec = %.2f
  FormatSpecOverTolerance = %+.2f
  FormatSpecUnderTolerance = %+.2f
  Inverted = false
  LockPosition = false
  MeasureType = 1
  OverTolerance = 0
  References2D = -> [View016]
  Rotation = 0
  Scale = 0.15
  ScaleType = 0
  TheoreticalExact = false
  Type = 1
  UnderTolerance = 0
  X = -42.0528
  Y = 47.7875
FEATURE [TechDraw::DrawViewDimension] Dimension209
  Arbitrary = false
  ArbitraryTolerances = false
  EqualTolerance = true
  FormatSpec = ⌀%.2f
  FormatSpecOverTolerance = %+.2f
  FormatSpecUnderTolerance = %+.2f
  Inverted = false
  LockPosition = false
  MeasureType = 1
  OverTolerance = 0
  References2D = -> [View016]
  Rotation = 0
  Scale = 0.15
  ScaleType = 0
  TheoreticalExact = false
  Type = 5
  UnderTolerance = 0
  X = 31.5307
  Y = 38.461
FEATURE [TechDraw::DrawViewSection] SectionView015  label="Section P - P"
  BaseView = -> View016
  CoarseView = false
  CutSurfaceDisplay = 2
  Direction = (-1,0,0)
  FileGeomPattern = <userpath>/AppData/Local/Programs/FreeCAD 0.19/data/Mod/TechDraw/PAT/FCPAT.pat
  FileHatchPattern = <userpath>/AppData/Local/Programs/FreeCAD 0.19/data/Mod/TechDraw/Patterns/simple.svg
  Focus = 100
  FuseBeforeCut = false
  HardHidden = false
  HatchScale = 1
  IsoCount = 0
  IsoHidden = false
  IsoVisible = false
  LockPosition = false
  NameGeomPattern = Diamond
  Perspective = false
  Rotation = 0
  Scale = 0.15
  ScaleType = 0
  SeamHidden = false
  SeamVisible = true
  SectionDirection = 0
  SectionNormal = (-1,0,0)
  SectionOrigin = (-29,-2,0)
  SectionSymbol = P
  SmoothHidden = false
  SmoothVisible = true
  Source = -> [Pocket025]
  X = 139.36
  XDirection = (0,-1,0)
  Y = 224.688
FEATURE [TechDraw::DrawViewPart] View017
  CoarseView = false
  Direction = (1,0,0)
  Focus = 100
  HardHidden = false
  IsoCount = 0
  IsoHidden = false
  IsoVisible = false
  LockPosition = false
  Perspective = false
  Rotation = 0
  Scale = 0.15
  ScaleType = 0
  SeamHidden = false
  SeamVisible = true
  SmoothHidden = false
  SmoothVisible = true
  Source = -> [Fillet]
  X = 246.08
  XDirection = (0,1,0)
  Y = 224.548
FEATURE [TechDraw::DrawViewDimension] Dimension211
  Arbitrary = false
  ArbitraryTolerances = false
  EqualTolerance = true
  FormatSpec = %.2f
  FormatSpecOverTolerance = %+.2f
  FormatSpecUnderTolerance = %+.2f
  Inverted = false
  LockPosition = false
  MeasureType = 1
  OverTolerance = 0
  References2D = -> [View017]
  Rotation = 0
  Scale = 0.15
  ScaleType = 0
  TheoreticalExact = false
  Type = 1
  UnderTolerance = 0
  X = 0.366742
  Y = -63.6325
FEATURE [TechDraw::DrawViewDimension] Dimension212
  Arbitrary = false
  ArbitraryTolerances = false
  EqualTolerance = true
  FormatSpec = %.2f
  FormatSpecOverTolerance = %+.2f
  FormatSpecUnderTolerance = %+.2f
  Inverted = false
  LockPosition = false
  MeasureType = 1
  OverTolerance = 0
  References2D = -> [View017]
  Rotation = 0
  Scale = 0.15
  ScaleType = 0
  TheoreticalExact = false
  Type = 1
  UnderTolerance = 0
  X = 2.56734
  Y = -57.6302
FEATURE [TechDraw::DrawViewDimension] Dimension213
  Arbitrary = false
  ArbitraryTolerances = false
  EqualTolerance = true
  FormatSpec = %.2f
  FormatSpecOverTolerance = %+.2f
  FormatSpecUnderTolerance = %+.2f
  Inverted = false
  LockPosition = false
  MeasureType = 1
  OverTolerance = 0
  References2D = -> [View017]
  Rotation = 0
  Scale = 0.15
  ScaleType = 0
  TheoreticalExact = false
  Type = 1
  UnderTolerance = 0
  X = 1.8597
  Y = -51.9954
FEATURE [TechDraw::DrawViewDimension] Dimension214
  Arbitrary = false
  ArbitraryTolerances = false
  EqualTolerance = true
  FormatSpec = %.2f
  FormatSpecOverTolerance = %+.2f
  FormatSpecUnderTolerance = %+.2f
  Inverted = false
  LockPosition = false
  MeasureType = 1
  OverTolerance = 0
  References2D = -> [View017]
  Rotation = 0
  Scale = 0.15
  ScaleType = 0
  TheoreticalExact = false
  Type = 1
  UnderTolerance = 0
  X = 1.65976
  Y = -46.3662
FEATURE [TechDraw::DrawViewDimension] Dimension215
  Arbitrary = false
  ArbitraryTolerances = false
  EqualTolerance = true
  FormatSpec = %.2f
  FormatSpecOverTolerance = %+.2f
  FormatSpecUnderTolerance = %+.2f
  Inverted = false
  LockPosition = false
  MeasureType = 1
  OverTolerance = 0
  References2D = -> [View017]
  Rotation = 0
  Scale = 0.15
  ScaleType = 0
  TheoreticalExact = false
  Type = 1
  UnderTolerance = 0
  X = 2.33501
  Y = -40.652
FEATURE [TechDraw::DrawViewDimension] Dimension216
  Arbitrary = false
  ArbitraryTolerances = false
  EqualTolerance = true
  FormatSpec = %.2f
  FormatSpecOverTolerance = %+.2f
  FormatSpecUnderTolerance = %+.2f
  Inverted = false
  LockPosition = false
  MeasureType = 1
  OverTolerance = 0
  References2D = -> [View017]
  Rotation = 0
  Scale = 0.15
  ScaleType = 0
  TheoreticalExact = false
  Type = 1
  UnderTolerance = 0
  X = 2.15933
  Y = -34.8417
FEATURE [TechDraw::DrawViewDimension] Dimension217
  Arbitrary = false
  ArbitraryTolerances = false
  EqualTolerance = true
  FormatSpec = %.2f
  FormatSpecOverTolerance = %+.2f
  FormatSpecUnderTolerance = %+.2f
  Inverted = false
  LockPosition = false
  MeasureType = 1
  OverTolerance = 0
  References2D = -> [View017]
  Rotation = 0
  Scale = 0.15
  ScaleType = 0
  TheoreticalExact = false
  Type = 2
  UnderTolerance = 0
  X = 78.8959
  Y = -17.4331
FEATURE [TechDraw::DrawViewDimension] Dimension220
  Arbitrary = false
  ArbitraryTolerances = false
  EqualTolerance = true
  FormatSpec = %.2f
  FormatSpecOverTolerance = %+.2f
  FormatSpecUnderTolerance = %+.2f
  Inverted = false
  LockPosition = false
  MeasureType = 1
  OverTolerance = 0
  References2D = -> [View017]
  Rotation = 0
  Scale = 0.15
  ScaleType = 0
  TheoreticalExact = false
  Type = 2
  UnderTolerance = 0
  X = -31.2322
  Y = -19.613
FEATURE [TechDraw::DrawViewDimension] Dimension221
  Arbitrary = false
  ArbitraryTolerances = false
  EqualTolerance = true
  FormatSpec = R%.2f
  FormatSpecOverTolerance = %+.2f
  FormatSpecUnderTolerance = %+.2f
  Inverted = false
  LockPosition = false
  MeasureType = 1
  OverTolerance = 0
  References2D = -> [View017]
  Rotation = 0
  Scale = 0.15
  ScaleType = 0
  TheoreticalExact = false
  Type = 4
  UnderTolerance = 0
  X = -36.7176
  Y = 35.5635
FEATURE [TechDraw::DrawViewDimension] Dimension223
  Arbitrary = false
  ArbitraryTolerances = false
  EqualTolerance = true
  FormatSpec = %.2f
  FormatSpecOverTolerance = %+.2f
  FormatSpecUnderTolerance = %+.2f
  Inverted = false
  LockPosition = false
  MeasureType = 1
  OverTolerance = 0
  References2D = -> [View017]
  Rotation = 0
  Scale = 0.15
  ScaleType = 0
  TheoreticalExact = false
  Type = 2
  UnderTolerance = 0
  X = -37.956
  Y = -20.6301
FEATURE [TechDraw::DrawViewDimension] Dimension224
  Arbitrary = false
  ArbitraryTolerances = false
  EqualTolerance = true
  FormatSpec = %.2f
  FormatSpecOverTolerance = %+.2f
  FormatSpecUnderTolerance = %+.2f
  Inverted = false
  LockPosition = false
  MeasureType = 1
  OverTolerance = 0
  References2D = -> [View017]
  Rotation = 0
  Scale = 0.15
  ScaleType = 0
  TheoreticalExact = false
  Type = 1
  UnderTolerance = 0
  X = 1.31726
  Y = -29.4564
FEATURE [TechDraw::DrawViewDimension] Dimension225
  Arbitrary = false
  ArbitraryTolerances = false
  EqualTolerance = true
  FormatSpec = %.2f
  FormatSpecOverTolerance = %+.2f
  FormatSpecUnderTolerance = %+.2f
  Inverted = false
  LockPosition = false
  MeasureType = 1
  OverTolerance = 0
  References2D = -> [View017]
  Rotation = 0
  Scale = 0.15
  ScaleType = 0
  TheoreticalExact = false
  Type = 2
  UnderTolerance = 0
  X = 18.6066
  Y = -10.752
FEATURE [TechDraw::DrawViewDimension] Dimension226
  Arbitrary = false
  ArbitraryTolerances = false
  EqualTolerance = true
  FormatSpec = %.2f
  FormatSpecOverTolerance = %+.2f
  FormatSpecUnderTolerance = %+.2f
  Inverted = false
  LockPosition = false
  MeasureType = 1
  OverTolerance = 0
  References2D = -> [View017]
  Rotation = 0
  Scale = 0.15
  ScaleType = 0
  TheoreticalExact = false
  Type = 2
  UnderTolerance = 0
  X = 24.2919
  Y = -11.4383
FEATURE [TechDraw::DrawViewDimension] Dimension227
  Arbitrary = false
  ArbitraryTolerances = false
  EqualTolerance = true
  FormatSpec = %.2f
  FormatSpecOverTolerance = %+.2f
  FormatSpecUnderTolerance = %+.2f
  Inverted = false
  LockPosition = false
  MeasureType = 1
  OverTolerance = 0
  References2D = -> [View017]
  Rotation = 0
  Scale = 0.15
  ScaleType = 0
  TheoreticalExact = false
  Type = 2
  UnderTolerance = 0
  X = 29.9013
  Y = -11.3176
FEATURE [TechDraw::DrawViewDimension] Dimension228
  Arbitrary = false
  ArbitraryTolerances = false
  EqualTolerance = true
  FormatSpec = %.2f
  FormatSpecOverTolerance = %+.2f
  FormatSpecUnderTolerance = %+.2f
  Inverted = false
  LockPosition = false
  MeasureType = 1
  OverTolerance = 0
  References2D = -> [View017]
  Rotation = 0
  Scale = 0.15
  ScaleType = 0
  TheoreticalExact = false
  Type = 2
  UnderTolerance = 0
  X = 35.4311
  Y = -11.281
FEATURE [TechDraw::DrawViewDimension] Dimension229
  Arbitrary = false
  ArbitraryTolerances = false
  EqualTolerance = true
  FormatSpec = %.2f
  FormatSpecOverTolerance = %+.2f
  FormatSpecUnderTolerance = %+.2f
  Inverted = false
  LockPosition = false
  MeasureType = 1
  OverTolerance = 0
  References2D = -> [View017]
  Rotation = 0
  Scale = 0.15
  ScaleType = 0
  TheoreticalExact = false
  Type = 2
  UnderTolerance = 0
  X = 49.2331
  Y = -10.5401
FEATURE [TechDraw::DrawViewDimension] Dimension230
  Arbitrary = false
  ArbitraryTolerances = false
  EqualTolerance = true
  FormatSpec = %.2f
  FormatSpecOverTolerance = %+.2f
  FormatSpecUnderTolerance = %+.2f
  Inverted = false
  LockPosition = false
  MeasureType = 1
  OverTolerance = 0
  References2D = -> [View017]
  Rotation = 0
  Scale = 0.15
  ScaleType = 0
  TheoreticalExact = false
  Type = 2
  UnderTolerance = 0
  X = 42.1763
  Y = -10.4082
FEATURE [TechDraw::DrawViewSection] SectionView016  label="Section Q - Q"
  BaseView = -> View017
  CoarseView = false
  CutSurfaceDisplay = 2
  Direction = (0,-1,0)
  FileGeomPattern = <userpath>/AppData/Local/Programs/FreeCAD 0.19/data/Mod/TechDraw/PAT/FCPAT.pat
  FileHatchPattern = <userpath>/AppData/Local/Programs/FreeCAD 0.19/data/Mod/TechDraw/Patterns/simple.svg
  Focus = 100
  FuseBeforeCut = false
  HardHidden = false
  HatchScale = 1
  IsoCount = 0
  IsoHidden = false
  IsoVisible = false
  LockPosition = false
  NameGeomPattern = Diamond
  Perspective = false
  Rotation = 0
  Scale = 0.15
  ScaleType = 0
  SeamHidden = false
  SeamVisible = true
  SectionDirection = 0
  SectionNormal = (0,-1,0)
  SectionOrigin = (10,12,0)
  SectionSymbol = Q
  SmoothHidden = false
  SmoothVisible = true
  Source = -> [Fillet]
  X = 312.64
  XDirection = (1,0,0)
  Y = 224.505
FEATURE [TechDraw::DrawViewDimension] Dimension232
  Arbitrary = false
  ArbitraryTolerances = false
  EqualTolerance = true
  FormatSpec = R%.2f
  FormatSpecOverTolerance = %+.2f
  FormatSpecUnderTolerance = %+.2f
  Inverted = false
  LockPosition = false
  MeasureType = 1
  OverTolerance = 0
  References2D = -> [View017]
  Rotation = 0
  Scale = 0.15
  ScaleType = 0
  TheoreticalExact = false
  Type = 4
  UnderTolerance = 0
  X = 27.2843
  Y = 34.1973
FEATURE [TechDraw::DrawViewDimension] Dimension233
  Arbitrary = false
  ArbitraryTolerances = false
  EqualTolerance = true
  FormatSpec = %.2f
  FormatSpecOverTolerance = %+.2f
  FormatSpecUnderTolerance = %+.2f
  Inverted = false
  LockPosition = false
  MeasureType = 1
  OverTolerance = 0
  References2D = -> [View017]
  Rotation = 0
  Scale = 0.15
  ScaleType = 0
  TheoreticalExact = false
  Type = 1
  UnderTolerance = 0
  X = -9.94515
  Y = 34.6127
FEATURE [TechDraw::DrawViewDimension] Dimension234
  Arbitrary = false
  ArbitraryTolerances = false
  EqualTolerance = true
  FormatSpec = %.2f
  FormatSpecOverTolerance = %+.2f
  FormatSpecUnderTolerance = %+.2f
  Inverted = false
  LockPosition = false
  MeasureType = 1
  OverTolerance = 0
  References2D = -> [View017]
  Rotation = 0
  Scale = 0.15
  ScaleType = 0
  TheoreticalExact = false
  Type = 1
  UnderTolerance = 0
  X = -4.69515
  Y = 43.2544
FEATURE [TechDraw::DrawViewDimension] Dimension235
  Arbitrary = false
  ArbitraryTolerances = false
  EqualTolerance = true
  FormatSpec = %.2f
  FormatSpecOverTolerance = %+.2f
  FormatSpecUnderTolerance = %+.2f
  Inverted = false
  LockPosition = false
  MeasureType = 1
  OverTolerance = 0
  References2D = -> [View016]
  Rotation = 0
  Scale = 0.15
  ScaleType = 0
  TheoreticalExact = false
  Type = 2
  UnderTolerance = 0
  X = -36.6719
  Y = -19.6893
FEATURE [TechDraw::DrawViewDimension] Dimension236
  Arbitrary = false
  ArbitraryTolerances = false
  EqualTolerance = true
  FormatSpec = %.2f
  FormatSpecOverTolerance = %+.2f
  FormatSpecUnderTolerance = %+.2f
  Inverted = false
  LockPosition = false
  MeasureType = 1
  OverTolerance = 0
  References2D = -> [SectionView015]
  Rotation = 0
  Scale = 0.15
  ScaleType = 0
  TheoreticalExact = false
  Type = 1
  UnderTolerance = 0
  X = 14.1232
  Y = -28.7452
FEATURE [TechDraw::DrawViewDimension] Dimension237
  Arbitrary = false
  ArbitraryTolerances = false
  EqualTolerance = true
  FormatSpec = %.2f
  FormatSpecOverTolerance = %+.2f
  FormatSpecUnderTolerance = %+.2f
  Inverted = false
  LockPosition = false
  MeasureType = 1
  OverTolerance = 0
  References2D = -> [SectionView016]
  Rotation = 0
  Scale = 0.15
  ScaleType = 0
  TheoreticalExact = false
  Type = 1
  UnderTolerance = 0
  X = 15.43
  Y = -30.5926
FEATURE [TechDraw::DrawViewPart] View018
  CoarseView = false
  Direction = (0,0,1)
  Focus = 100
  HardHidden = false
  IsoCount = 0
  IsoHidden = false
  IsoVisible = false
  LockPosition = false
  Perspective = false
  Rotation = 0
  Scale = 0.15
  ScaleType = 0
  SeamHidden = false
  SeamVisible = true
  SmoothHidden = false
  SmoothVisible = true
  Source = -> [Pocket026]
  X = 100.939
  XDirection = (1,0,0)
  Y = 68.66
FEATURE [TechDraw::DrawViewDimension] Dimension238
  Arbitrary = false
  ArbitraryTolerances = false
  EqualTolerance = true
  FormatSpec = %.2f
  FormatSpecOverTolerance = %+.2f
  FormatSpecUnderTolerance = %+.2f
  Inverted = false
  LockPosition = false
  MeasureType = 1
  OverTolerance = 0
  References2D = -> [View018]
  Rotation = 0
  Scale = 0.15
  ScaleType = 0
  TheoreticalExact = false
  Type = 1
  UnderTolerance = 0
  X = -0.219133
  Y = -48.7466
FEATURE [TechDraw::DrawViewDimension] Dimension239
  Arbitrary = false
  ArbitraryTolerances = false
  EqualTolerance = true
  FormatSpec = %.2f
  FormatSpecOverTolerance = %+.2f
  FormatSpecUnderTolerance = %+.2f
  Inverted = false
  LockPosition = false
  MeasureType = 1
  OverTolerance = 0
  References2D = -> [View018]
  Rotation = 0
  Scale = 0.15
  ScaleType = 0
  TheoreticalExact = false
  Type = 2
  UnderTolerance = 0
  X = -34.461
  Y = -47.5277
FEATURE [TechDraw::DrawViewDimension] Dimension240
  Arbitrary = false
  ArbitraryTolerances = false
  EqualTolerance = true
  FormatSpec = %.2f
  FormatSpecOverTolerance = %+.2f
  FormatSpecUnderTolerance = %+.2f
  Inverted = false
  LockPosition = false
  MeasureType = 1
  OverTolerance = 0
  References2D = -> [View018]
  Rotation = 0
  Scale = 0.15
  ScaleType = 0
  TheoreticalExact = false
  Type = 2
  UnderTolerance = 0
  X = -40.6698
  Y = -48.3266
FEATURE [TechDraw::DrawViewDimension] Dimension241
  Arbitrary = false
  ArbitraryTolerances = false
  EqualTolerance = true
  FormatSpec = %.2f
  FormatSpecOverTolerance = %+.2f
  FormatSpecUnderTolerance = %+.2f
  Inverted = false
  LockPosition = false
  MeasureType = 1
  OverTolerance = 0
  References2D = -> [View018]
  Rotation = 0
  Scale = 0.15
  ScaleType = 0
  TheoreticalExact = false
  Type = 2
  UnderTolerance = 0
  X = -46.3308
  Y = -48.2353
FEATURE [TechDraw::DrawViewDimension] Dimension242
  Arbitrary = false
  ArbitraryTolerances = false
  EqualTolerance = true
  FormatSpec = %.2f
  FormatSpecOverTolerance = %+.2f
  FormatSpecUnderTolerance = %+.2f
  Inverted = false
  LockPosition = false
  MeasureType = 1
  OverTolerance = 0
  References2D = -> [View018]
  Rotation = 0
  Scale = 0.15
  ScaleType = 0
  TheoreticalExact = false
  Type = 2
  UnderTolerance = 0
  X = -51.8362
  Y = -47.2331
FEATURE [TechDraw::DrawViewDimension] Dimension243
  Arbitrary = false
  ArbitraryTolerances = false
  EqualTolerance = true
  FormatSpec = %.2f
  FormatSpecOverTolerance = %+.2f
  FormatSpecUnderTolerance = %+.2f
  Inverted = false
  LockPosition = false
  MeasureType = 1
  OverTolerance = 0
  References2D = -> [View018]
  Rotation = 0
  Scale = 0.15
  ScaleType = 0
  TheoreticalExact = false
  Type = 2
  UnderTolerance = 0
  X = -58.1477
  Y = -47.2842
FEATURE [TechDraw::DrawViewDimension] Dimension244
  Arbitrary = false
  ArbitraryTolerances = false
  EqualTolerance = true
  FormatSpec = %.2f
  FormatSpecOverTolerance = %+.2f
  FormatSpecUnderTolerance = %+.2f
  Inverted = false
  LockPosition = false
  MeasureType = 1
  OverTolerance = 0
  References2D = -> [View018]
  Rotation = 0
  Scale = 0.15
  ScaleType = 0
  TheoreticalExact = false
  Type = 2
  UnderTolerance = 0
  X = 31.5668
  Y = -30.6464
FEATURE [TechDraw::DrawViewDimension] Dimension245
  Arbitrary = false
  ArbitraryTolerances = false
  EqualTolerance = true
  FormatSpec = %.2f
  FormatSpecOverTolerance = %+.2f
  FormatSpecUnderTolerance = %+.2f
  Inverted = false
  LockPosition = false
  MeasureType = 1
  OverTolerance = 0
  References2D = -> [View018]
  Rotation = 0
  Scale = 0.15
  ScaleType = 0
  TheoreticalExact = false
  Type = 2
  UnderTolerance = 0
  X = 37.3418
  Y = -30.7127
FEATURE [TechDraw::DrawViewDimension] Dimension246
  Arbitrary = false
  ArbitraryTolerances = false
  EqualTolerance = true
  FormatSpec = %.2f
  FormatSpecOverTolerance = %+.2f
  FormatSpecUnderTolerance = %+.2f
  Inverted = false
  LockPosition = false
  MeasureType = 1
  OverTolerance = 0
  References2D = -> [View018]
  Rotation = 0
  Scale = 0.15
  ScaleType = 0
  TheoreticalExact = false
  Type = 2
  UnderTolerance = 0
  X = 43.8431
  Y = -31.4636
FEATURE [TechDraw::DrawViewDimension] Dimension247
  Arbitrary = false
  ArbitraryTolerances = false
  EqualTolerance = true
  FormatSpec = %.2f
  FormatSpecOverTolerance = %+.2f
  FormatSpecUnderTolerance = %+.2f
  Inverted = false
  LockPosition = false
  MeasureType = 1
  OverTolerance = 0
  References2D = -> [View018]
  Rotation = 0
  Scale = 0.15
  ScaleType = 0
  TheoreticalExact = false
  Type = 2
  UnderTolerance = 0
  X = 50.3444
  Y = -31.381
FEATURE [TechDraw::DrawViewDimension] Dimension248
  Arbitrary = false
  ArbitraryTolerances = false
  EqualTolerance = true
  FormatSpec = %.2f
  FormatSpecOverTolerance = %+.2f
  FormatSpecUnderTolerance = %+.2f
  Inverted = false
  LockPosition = false
  MeasureType = 1
  OverTolerance = 0
  References2D = -> [View018]
  Rotation = 0
  Scale = 0.15
  ScaleType = 0
  TheoreticalExact = false
  Type = 1
  UnderTolerance = 0
  X = -37.8268
  Y = 35.1196
FEATURE [TechDraw::DrawViewDimension] Dimension249
  Arbitrary = false
  ArbitraryTolerances = false
  EqualTolerance = true
  FormatSpec = %.2f
  FormatSpecOverTolerance = %+.2f
  FormatSpecUnderTolerance = %+.2f
  Inverted = false
  LockPosition = false
  MeasureType = 1
  OverTolerance = 0
  References2D = -> [View018]
  Rotation = 0
  Scale = 0.15
  ScaleType = 0
  TheoreticalExact = false
  Type = 1
  UnderTolerance = 0
  X = -37.7794
  Y = 40.9681
FEATURE [TechDraw::DrawViewDimension] Dimension250
  Arbitrary = false
  ArbitraryTolerances = false
  EqualTolerance = true
  FormatSpec = %.2f
  FormatSpecOverTolerance = %+.2f
  FormatSpecUnderTolerance = %+.2f
  Inverted = false
  LockPosition = false
  MeasureType = 1
  OverTolerance = 0
  References2D = -> [View018]
  Rotation = 0
  Scale = 0.15
  ScaleType = 0
  TheoreticalExact = false
  Type = 1
  UnderTolerance = 0
  X = -38.6592
  Y = 47.1493
FEATURE [TechDraw::DrawViewDimension] Dimension251
  Arbitrary = false
  ArbitraryTolerances = false
  EqualTolerance = true
  FormatSpec = %.2f
  FormatSpecOverTolerance = %+.2f
  FormatSpecUnderTolerance = %+.2f
  Inverted = false
  LockPosition = false
  MeasureType = 1
  OverTolerance = 0
  References2D = -> [View018]
  Rotation = 0
  Scale = 0.15
  ScaleType = 0
  TheoreticalExact = false
  Type = 1
  UnderTolerance = 0
  X = -38.6315
  Y = 53.0077
FEATURE [TechDraw::DrawViewDimension] Dimension252
  Arbitrary = false
  ArbitraryTolerances = false
  EqualTolerance = true
  FormatSpec = %.2f
  FormatSpecOverTolerance = %+.2f
  FormatSpecUnderTolerance = %+.2f
  Inverted = false
  LockPosition = false
  MeasureType = 1
  OverTolerance = 0
  References2D = -> [View018]
  Rotation = 0
  Scale = 0.15
  ScaleType = 0
  TheoreticalExact = false
  Type = 1
  UnderTolerance = 0
  X = -38.8027
  Y = 59.5237
FEATURE [TechDraw::DrawViewDimension] Dimension253
  Arbitrary = false
  ArbitraryTolerances = false
  EqualTolerance = true
  FormatSpec = %.2f
  FormatSpecOverTolerance = %+.2f
  FormatSpecUnderTolerance = %+.2f
  Inverted = false
  LockPosition = false
  MeasureType = 1
  OverTolerance = 0
  References2D = -> [View018]
  Rotation = 0
  Scale = 0.15
  ScaleType = 0
  TheoreticalExact = false
  Type = 1
  UnderTolerance = 0
  X = -39.1924
  Y = 65.562
FEATURE [TechDraw::DrawViewDimension] Dimension254
  Arbitrary = false
  ArbitraryTolerances = false
  EqualTolerance = true
  FormatSpec = %.2f
  FormatSpecOverTolerance = %+.2f
  FormatSpecUnderTolerance = %+.2f
  Inverted = false
  LockPosition = false
  MeasureType = 1
  OverTolerance = 0
  References2D = -> [View018]
  Rotation = 0
  Scale = 0.15
  ScaleType = 0
  TheoreticalExact = false
  Type = 1
  UnderTolerance = 0
  X = -39.2534
  Y = 71.8989
FEATURE [TechDraw::DrawViewDimension] Dimension255
  Arbitrary = false
  ArbitraryTolerances = false
  EqualTolerance = true
  FormatSpec = %.2f
  FormatSpecOverTolerance = %+.2f
  FormatSpecUnderTolerance = %+.2f
  Inverted = false
  LockPosition = false
  MeasureType = 1
  OverTolerance = 0
  References2D = -> [View018]
  Rotation = 0
  Scale = 0.15
  ScaleType = 0
  TheoreticalExact = false
  Type = 1
  UnderTolerance = 0
  X = -39.3145
  Y = 78.0346
FEATURE [TechDraw::DrawViewDimension] Dimension256
  Arbitrary = false
  ArbitraryTolerances = false
  EqualTolerance = true
  FormatSpec = %.2f
  FormatSpecOverTolerance = %+.2f
  FormatSpecUnderTolerance = %+.2f
  Inverted = false
  LockPosition = false
  MeasureType = 1
  OverTolerance = 0
  References2D = -> [View018]
  Rotation = 0
  Scale = 0.15
  ScaleType = 0
  TheoreticalExact = false
  Type = 1
  UnderTolerance = 0
  X = -39.5947
  Y = 83.9512
FEATURE [TechDraw::DrawViewSection] SectionView017  label="Section R - R"
  BaseView = -> View018
  CoarseView = false
  CutSurfaceDisplay = 2
  Direction = (-1,0,0)
  FileGeomPattern = <userpath>/AppData/Local/Programs/FreeCAD 0.19/data/Mod/TechDraw/PAT/FCPAT.pat
  FileHatchPattern = <userpath>/AppData/Local/Programs/FreeCAD 0.19/data/Mod/TechDraw/Patterns/simple.svg
  Focus = 100
  FuseBeforeCut = false
  HardHidden = false
  HatchScale = 1
  IsoCount = 0
  IsoHidden = false
  IsoVisible = false
  LockPosition = false
  NameGeomPattern = Diamond
  Perspective = false
  Rotation = 0
  Scale = 0.15
  ScaleType = 0
  SeamHidden = false
  SeamVisible = true
  SectionDirection = 0
  SectionNormal = (-1,0,0)
  SectionOrigin = (29,0,2)
  SectionSymbol = R
  SmoothHidden = false
  SmoothVisible = true
  Source = -> [Pocket026]
  X = 176.23
  XDirection = (0,0,1)
  Y = 68.6609
FEATURE [TechDraw::DrawViewDimension] Dimension257
  Arbitrary = false
  ArbitraryTolerances = false
  EqualTolerance = true
  FormatSpec = %.2f
  FormatSpecOverTolerance = %+.2f
  FormatSpecUnderTolerance = %+.2f
  Inverted = false
  LockPosition = false
  MeasureType = 1
  OverTolerance = 0
  References2D = -> [View018]
  Rotation = 0
  Scale = 0.15
  ScaleType = 0
  TheoreticalExact = false
  Type = 2
  UnderTolerance = 0
  X = 86.6294
  Y = 2.08376
FEATURE [TechDraw::DrawViewDimension] Dimension258
  Arbitrary = false
  ArbitraryTolerances = false
  EqualTolerance = true
  FormatSpec = %.2f
  FormatSpecOverTolerance = %+.2f
  FormatSpecUnderTolerance = %+.2f
  Inverted = false
  LockPosition = false
  MeasureType = 1
  OverTolerance = 0
  References2D = -> [SectionView017]
  Rotation = 0
  Scale = 0.15
  ScaleType = 0
  TheoreticalExact = false
  Type = 1
  UnderTolerance = 0
  X = 14.803
  Y = -28.0026
FEATURE [TechDraw::DrawViewDimension] Dimension259
  Arbitrary = false
  ArbitraryTolerances = false
  EqualTolerance = true
  FormatSpec = %.2f
  FormatSpecOverTolerance = %+.2f
  FormatSpecUnderTolerance = %+.2f
  Inverted = false
  LockPosition = false
  MeasureType = 1
  OverTolerance = 0
  References2D = -> [View018]
  Rotation = 0
  Scale = 0.15
  ScaleType = 0
  TheoreticalExact = false
  Type = 1
  UnderTolerance = 0
  X = 8.54209
  Y = -42.5357
FEATURE [TechDraw::DrawViewDimension] Dimension260
  Arbitrary = false
  ArbitraryTolerances = false
  EqualTolerance = true
  FormatSpec = %.2f
  FormatSpecOverTolerance = %+.2f
  FormatSpecUnderTolerance = %+.2f
  Inverted = false
  LockPosition = false
  MeasureType = 1
  OverTolerance = 0
  References2D = -> [View018]
  Rotation = 0
  Scale = 0.15
  ScaleType = 0
  TheoreticalExact = false
  Type = 1
  UnderTolerance = 0
  X = 8.46465
  Y = -37.0659
FEATURE [TechDraw::DrawViewDimension] Dimension261
  Arbitrary = false
  ArbitraryTolerances = false
  EqualTolerance = true
  FormatSpec = %.2f
  FormatSpecOverTolerance = %+.2f
  FormatSpecUnderTolerance = %+.2f
  Inverted = false
  LockPosition = false
  MeasureType = 1
  OverTolerance = 0
  References2D = -> [View018]
  Rotation = 0
  Scale = 0.15
  ScaleType = 0
  TheoreticalExact = false
  Type = 1
  UnderTolerance = 0
  X = -4.1025
  Y = -11.25
FEATURE [TechDraw::DrawPage] Page012  label="Electrical_equipment_enclosure_Drawing"
  KeepUpdated = true
  NextBalloonIndex = 1
  ProjectionType = 0
  Scale = 0.15
  Template = -> Template015
  Views = -> [View016,Dimension197,Dimension198,Dimension199,Dimension200,Dimension201,Dimension202,Dimension203,Dimension204,Dimension205,Dimension206,Dimension207,Dimension208,Dimension209,SectionView015,View017,Dimension211,Dimension212,Dimension213,Dimension214,Dimension215,Dimension216,Dimension217,Dimension220,Dimension221,Dimension223,Dimension224,Dimension225,Dimension226,Dimension227,Dimension228,+35 more]
FEATURE [Sketcher::SketchObject] Sketch120
  FullyConstrained = true
  MapMode = 5
  Support = -> [XY_Plane075]
  sketch-geometry (3):
    g0: LineSegment StartX=30 StartY=30 StartZ=0 EndX=30 EndY=-30 EndZ=0
    g1: LineSegment StartX=30 StartY=-30 StartZ=0 EndX=-30 EndY=-30 EndZ=0
    g2: LineSegment StartX=-30 StartY=-30 StartZ=0 EndX=30 EndY=30 EndZ=0
  constraints (9):
    c: Vertical(g0)
    c: Coincident(g0,g1)
    c: Horizontal(g1)
    c: Coincident(g1,g2)
    c: Coincident(g2,g0)
    c: DistanceY(g0,g-1) = 30
    c: DistanceY(g-1,g0) = 30
    c: DistanceX(g1,g-1) = 30
    c: PointOnObject(g-1,g2)
FEATURE [PartDesign::Pad] Pad075
  Direction = (1,1,1)
  Length = 4
  Length2 = 100
  Profile = -> Sketch120
  Type = 0
FEATURE [PartDesign::Body] Body075  label="70mm suport-031"
  Group = -> [Sketch120,Pad075]
  Origin = -> Origin075
  Placement = pos=(0,-2713,0) rot=(0,0,1;0rad)
  Tip = -> Pad075
FEATURE [Sketcher::SketchObject] Sketch121
  FullyConstrained = true
  MapMode = 5
  Support = -> [XY_Plane076]
  sketch-geometry (3):
    g0: LineSegment StartX=30 StartY=30 StartZ=0 EndX=30 EndY=-30 EndZ=0
    g1: LineSegment StartX=30 StartY=-30 StartZ=0 EndX=-30 EndY=-30 EndZ=0
    g2: LineSegment StartX=-30 StartY=-30 StartZ=0 EndX=30 EndY=30 EndZ=0
  constraints (9):
    c: Vertical(g0)
    c: Coincident(g0,g1)
    c: Horizontal(g1)
    c: Coincident(g1,g2)
    c: Coincident(g2,g0)
    c: DistanceY(g0,g-1) = 30
    c: DistanceY(g-1,g0) = 30
    c: DistanceX(g1,g-1) = 30
    c: PointOnObject(g-1,g2)
FEATURE [PartDesign::Pad] Pad076
  Direction = (1,1,1)
  Length = 4
  Length2 = 100
  Profile = -> Sketch121
  Type = 0
FEATURE [PartDesign::Body] Body076  label="70mm suport-032"
  Group = -> [Sketch121,Pad076]
  Origin = -> Origin076
  Placement = pos=(86,-2713,0) rot=(0,0,1;3.14159rad)
  Tip = -> Pad076
FEATURE [Sketcher::SketchObject] Sketch122
  FullyConstrained = true
  MapMode = 5
  Support = -> [XY_Plane077]
  sketch-geometry (3):
    g0: LineSegment StartX=30 StartY=30 StartZ=0 EndX=30 EndY=-30 EndZ=0
    g1: LineSegment StartX=30 StartY=-30 StartZ=0 EndX=-30 EndY=-30 EndZ=0
    g2: LineSegment StartX=-30 StartY=-30 StartZ=0 EndX=30 EndY=30 EndZ=0
  constraints (9):
    c: Vertical(g0)
    c: Coincident(g0,g1)
    c: Horizontal(g1)
    c: Coincident(g1,g2)
    c: Coincident(g2,g0)
    c: DistanceY(g0,g-1) = 30
    c: DistanceY(g-1,g0) = 30
    c: DistanceX(g1,g-1) = 30
    c: PointOnObject(g-1,g2)
FEATURE [PartDesign::Pad] Pad077
  Direction = (1,1,1)
  Length = 4
  Length2 = 100
  Profile = -> Sketch122
  Type = 0
FEATURE [Sketcher::SketchObject] Sketch123
  FullyConstrained = true
  MapMode = 5
  Support = -> [XY_Plane078]
  sketch-geometry (3):
    g0: LineSegment StartX=30 StartY=30 StartZ=0 EndX=30 EndY=-30 EndZ=0
    g1: LineSegment StartX=30 StartY=-30 StartZ=0 EndX=-30 EndY=-30 EndZ=0
    g2: LineSegment StartX=-30 StartY=-30 StartZ=0 EndX=30 EndY=30 EndZ=0
  constraints (9):
    c: Vertical(g0)
    c: Coincident(g0,g1)
    c: Horizontal(g1)
    c: Coincident(g1,g2)
    c: Coincident(g2,g0)
    c: DistanceY(g0,g-1) = 30
    c: DistanceY(g-1,g0) = 30
    c: DistanceX(g1,g-1) = 30
    c: PointOnObject(g-1,g2)
FEATURE [PartDesign::Pad] Pad078
  Direction = (1,1,1)
  Length = 4
  Length2 = 100
  Profile = -> Sketch123
  Type = 0
FEATURE [PartDesign::Body] Body077  label="70mm suport-033"
  Group = -> [Sketch122,Pad077]
  Origin = -> Origin078
  Placement = pos=(118,-2713,0) rot=(0,0,1;0rad)
  Tip = -> Pad077
FEATURE [PartDesign::Body] Body078  label="70mm suport-034"
  Group = -> [Sketch123,Pad078]
  Origin = -> Origin077
  Placement = pos=(210,-2713,0) rot=(0,0,1;3.14159rad)
  Tip = -> Pad078
FEATURE [Sketcher::SketchObject] Sketch124
  FullyConstrained = true
  MapMode = 5
  Support = -> [XY_Plane080]
  sketch-geometry (3):
    g0: LineSegment StartX=30 StartY=30 StartZ=0 EndX=30 EndY=-30 EndZ=0
    g1: LineSegment StartX=30 StartY=-30 StartZ=0 EndX=-30 EndY=-30 EndZ=0
    g2: LineSegment StartX=-30 StartY=-30 StartZ=0 EndX=30 EndY=30 EndZ=0
  constraints (9):
    c: Vertical(g0)
    c: Coincident(g0,g1)
    c: Horizontal(g1)
    c: Coincident(g1,g2)
    c: Coincident(g2,g0)
    c: DistanceY(g0,g-1) = 30
    c: DistanceY(g-1,g0) = 30
    c: DistanceX(g1,g-1) = 30
    c: PointOnObject(g-1,g2)
FEATURE [PartDesign::Pad] Pad079
  Direction = (1,1,1)
  Length = 4
  Length2 = 100
  Profile = -> Sketch124
  Type = 0
FEATURE [Sketcher::SketchObject] Sketch125
  FullyConstrained = true
  MapMode = 5
  Support = -> [XY_Plane079]
  sketch-geometry (3):
    g0: LineSegment StartX=30 StartY=30 StartZ=0 EndX=30 EndY=-30 EndZ=0
    g1: LineSegment StartX=30 StartY=-30 StartZ=0 EndX=-30 EndY=-30 EndZ=0
    g2: LineSegment StartX=-30 StartY=-30 StartZ=0 EndX=30 EndY=30 EndZ=0
  constraints (9):
    c: Vertical(g0)
    c: Coincident(g0,g1)
    c: Horizontal(g1)
    c: Coincident(g1,g2)
    c: Coincident(g2,g0)
    c: DistanceY(g0,g-1) = 30
    c: DistanceY(g-1,g0) = 30
    c: DistanceX(g1,g-1) = 30
    c: PointOnObject(g-1,g2)
FEATURE [PartDesign::Pad] Pad080
  Direction = (1,1,1)
  Length = 4
  Length2 = 100
  Profile = -> Sketch125
  Type = 0
FEATURE [PartDesign::Body] Body079  label="70mm suport-035"
  Group = -> [Sketch125,Pad080]
  Origin = -> Origin079
  Placement = pos=(330,-2713,0) rot=(0,0,1;3.14159rad)
  Tip = -> Pad080
FEATURE [PartDesign::Body] Body080  label="70mm suport-036"
  Group = -> [Sketch124,Pad079]
  Origin = -> Origin080
  Placement = pos=(242,-2713,0) rot=(0,0,1;0rad)
  Tip = -> Pad079
FEATURE [Sketcher::SketchObject] Sketch126
  FullyConstrained = true
  MapMode = 5
  Support = -> [XY_Plane082]
  sketch-geometry (3):
    g0: LineSegment StartX=30 StartY=30 StartZ=0 EndX=30 EndY=-30 EndZ=0
    g1: LineSegment StartX=30 StartY=-30 StartZ=0 EndX=-30 EndY=-30 EndZ=0
    g2: LineSegment StartX=-30 StartY=-30 StartZ=0 EndX=30 EndY=30 EndZ=0
  constraints (9):
    c: Vertical(g0)
    c: Coincident(g0,g1)
    c: Horizontal(g1)
    c: Coincident(g1,g2)
    c: Coincident(g2,g0)
    c: DistanceY(g0,g-1) = 30
    c: DistanceY(g-1,g0) = 30
    c: DistanceX(g1,g-1) = 30
    c: PointOnObject(g-1,g2)
FEATURE [Sketcher::SketchObject] Sketch127
  FullyConstrained = true
  MapMode = 5
  Support = -> [XY_Plane081]
  sketch-geometry (3):
    g0: LineSegment StartX=30 StartY=30 StartZ=0 EndX=30 EndY=-30 EndZ=0
    g1: LineSegment StartX=30 StartY=-30 StartZ=0 EndX=-30 EndY=-30 EndZ=0
    g2: LineSegment StartX=-30 StartY=-30 StartZ=0 EndX=30 EndY=30 EndZ=0
  constraints (9):
    c: Vertical(g0)
    c: Coincident(g0,g1)
    c: Horizontal(g1)
    c: Coincident(g1,g2)
    c: Coincident(g2,g0)
    c: DistanceY(g0,g-1) = 30
    c: DistanceY(g-1,g0) = 30
    c: DistanceX(g1,g-1) = 30
    c: PointOnObject(g-1,g2)
FEATURE [PartDesign::Pad] Pad081
  Direction = (1,1,1)
  Length = 4
  Length2 = 100
  Profile = -> Sketch127
  Type = 0
FEATURE [PartDesign::Body] Body082  label="70mm suport-038"
  Group = -> [Sketch127,Pad081]
  Origin = -> Origin082
  Placement = pos=(440,-2713,0) rot=(0,0,1;3.14159rad)
  Tip = -> Pad081
FEATURE [PartDesign::Pad] Pad082
  Direction = (1,1,1)
  Length = 4
  Length2 = 100
  Profile = -> Sketch126
  Type = 0
FEATURE [PartDesign::Body] Body081  label="70mm suport-037"
  Group = -> [Sketch126,Pad082]
  Origin = -> Origin081
  Placement = pos=(470,-2713,0) rot=(0,0,1;0rad)
  Tip = -> Pad082
FEATURE [Sketcher::SketchObject] Sketch128
  FullyConstrained = true
  MapMode = 5
  Support = -> [XY_Plane083]
  sketch-geometry (3):
    g0: LineSegment StartX=30 StartY=30 StartZ=0 EndX=30 EndY=-30 EndZ=0
    g1: LineSegment StartX=30 StartY=-30 StartZ=0 EndX=-30 EndY=-30 EndZ=0
    g2: LineSegment StartX=-30 StartY=-30 StartZ=0 EndX=30 EndY=30 EndZ=0
  constraints (9):
    c: Vertical(g0)
    c: Coincident(g0,g1)
    c: Horizontal(g1)
    c: Coincident(g1,g2)
    c: Coincident(g2,g0)
    c: DistanceY(g0,g-1) = 30
    c: DistanceY(g-1,g0) = 30
    c: DistanceX(g1,g-1) = 30
    c: PointOnObject(g-1,g2)
FEATURE [Sketcher::SketchObject] Sketch129
  FullyConstrained = true
  MapMode = 5
  Support = -> [XY_Plane084]
  sketch-geometry (3):
    g0: LineSegment StartX=30 StartY=30 StartZ=0 EndX=30 EndY=-30 EndZ=0
    g1: LineSegment StartX=30 StartY=-30 StartZ=0 EndX=-30 EndY=-30 EndZ=0
    g2: LineSegment StartX=-30 StartY=-30 StartZ=0 EndX=30 EndY=30 EndZ=0
  constraints (9):
    c: Vertical(g0)
    c: Coincident(g0,g1)
    c: Horizontal(g1)
    c: Coincident(g1,g2)
    c: Coincident(g2,g0)
    c: DistanceY(g0,g-1) = 30
    c: DistanceY(g-1,g0) = 30
    c: DistanceX(g1,g-1) = 30
    c: PointOnObject(g-1,g2)
FEATURE [PartDesign::Pad] Pad083
  Direction = (1,1,1)
  Length = 4
  Length2 = 100
  Profile = -> Sketch129
  Type = 0
FEATURE [PartDesign::Body] Body083  label="70mm suport-039"
  Group = -> [Sketch129,Pad083]
  Origin = -> Origin084
  Placement = pos=(550,-2713,0) rot=(0,0,1;3.14159rad)
  Tip = -> Pad083
FEATURE [PartDesign::Pad] Pad084
  Direction = (1,1,1)
  Length = 4
  Length2 = 100
  Profile = -> Sketch128
  Type = 0
FEATURE [PartDesign::Body] Body084  label="70mm suport-040"
  Group = -> [Sketch128,Pad084]
  Origin = -> Origin083
  Placement = pos=(580,-2713,0) rot=(0,0,1;0rad)
  Tip = -> Pad084
FEATURE [Sketcher::SketchObject] Sketch130
  FullyConstrained = true
  MapMode = 5
  Support = -> [XY_Plane085]
  sketch-geometry (3):
    g0: LineSegment StartX=30 StartY=30 StartZ=0 EndX=30 EndY=-30 EndZ=0
    g1: LineSegment StartX=30 StartY=-30 StartZ=0 EndX=-30 EndY=-30 EndZ=0
    g2: LineSegment StartX=-30 StartY=-30 StartZ=0 EndX=30 EndY=30 EndZ=0
  constraints (9):
    c: Vertical(g0)
    c: Coincident(g0,g1)
    c: Horizontal(g1)
    c: Coincident(g1,g2)
    c: Coincident(g2,g0)
    c: DistanceY(g0,g-1) = 30
    c: DistanceY(g-1,g0) = 30
    c: DistanceX(g1,g-1) = 30
    c: PointOnObject(g-1,g2)
FEATURE [PartDesign::Pad] Pad085
  Direction = (1,1,1)
  Length = 4
  Length2 = 100
  Profile = -> Sketch130
  Type = 0
FEATURE [PartDesign::Body] Body085  label="70mm suport-041"
  Group = -> [Sketch130,Pad085]
  Origin = -> Origin086
  Placement = pos=(660,-2713,0) rot=(0,0,1;3.14159rad)
  Tip = -> Pad085
FEATURE [Sketcher::SketchObject] Sketch131
  FullyConstrained = true
  MapMode = 5
  Support = -> [XY_Plane086]
  sketch-geometry (3):
    g0: LineSegment StartX=30 StartY=30 StartZ=0 EndX=30 EndY=-30 EndZ=0
    g1: LineSegment StartX=30 StartY=-30 StartZ=0 EndX=-30 EndY=-30 EndZ=0
    g2: LineSegment StartX=-30 StartY=-30 StartZ=0 EndX=30 EndY=30 EndZ=0
  constraints (9):
    c: Vertical(g0)
    c: Coincident(g0,g1)
    c: Horizontal(g1)
    c: Coincident(g1,g2)
    c: Coincident(g2,g0)
    c: DistanceY(g0,g-1) = 30
    c: DistanceY(g-1,g0) = 30
    c: DistanceX(g1,g-1) = 30
    c: PointOnObject(g-1,g2)
FEATURE [PartDesign::Pad] Pad086
  Direction = (1,1,1)
  Length = 4
  Length2 = 100
  Profile = -> Sketch131
  Type = 0
FEATURE [PartDesign::Body] Body086  label="70mm suport-042"
  Group = -> [Sketch131,Pad086]
  Origin = -> Origin085
  Placement = pos=(690,-2713,0) rot=(0,0,1;0rad)
  Tip = -> Pad086
FEATURE [Sketcher::SketchObject] Sketch132
  FullyConstrained = true
  MapMode = 5
  Support = -> [XY_Plane088]
  sketch-geometry (3):
    g0: LineSegment StartX=30 StartY=30 StartZ=0 EndX=30 EndY=-30 EndZ=0
    g1: LineSegment StartX=30 StartY=-30 StartZ=0 EndX=-30 EndY=-30 EndZ=0
    g2: LineSegment StartX=-30 StartY=-30 StartZ=0 EndX=30 EndY=30 EndZ=0
  constraints (9):
    c: Vertical(g0)
    c: Coincident(g0,g1)
    c: Horizontal(g1)
    c: Coincident(g1,g2)
    c: Coincident(g2,g0)
    c: DistanceY(g0,g-1) = 30
    c: DistanceY(g-1,g0) = 30
    c: DistanceX(g1,g-1) = 30
    c: PointOnObject(g-1,g2)
FEATURE [PartDesign::Pad] Pad088
  Direction = (1,1,1)
  Length = 4
  Length2 = 100
  Profile = -> Sketch132
  Type = 0
FEATURE [PartDesign::Body] Body088  label="70mm suport-044"
  Group = -> [Sketch132,Pad088]
  Origin = -> Origin087
  Placement = pos=(800,-2713,0) rot=(0,0,1;0rad)
  Tip = -> Pad088
FEATURE [Sketcher::SketchObject] Sketch133
  FullyConstrained = true
  MapMode = 5
  Support = -> [XY_Plane087]
  sketch-geometry (3):
    g0: LineSegment StartX=30 StartY=30 StartZ=0 EndX=30 EndY=-30 EndZ=0
    g1: LineSegment StartX=30 StartY=-30 StartZ=0 EndX=-30 EndY=-30 EndZ=0
    g2: LineSegment StartX=-30 StartY=-30 StartZ=0 EndX=30 EndY=30 EndZ=0
  constraints (9):
    c: Vertical(g0)
    c: Coincident(g0,g1)
    c: Horizontal(g1)
    c: Coincident(g1,g2)
    c: Coincident(g2,g0)
    c: DistanceY(g0,g-1) = 30
    c: DistanceY(g-1,g0) = 30
    c: DistanceX(g1,g-1) = 30
    c: PointOnObject(g-1,g2)
FEATURE [PartDesign::Pad] Pad087
  Direction = (1,1,1)
  Length = 4
  Length2 = 100
  Profile = -> Sketch133
  Type = 0
FEATURE [PartDesign::Body] Body087  label="70mm suport-043"
  Group = -> [Sketch133,Pad087]
  Origin = -> Origin088
  Placement = pos=(770,-2713,0) rot=(0,0,1;3.14159rad)
  Tip = -> Pad087
FEATURE [Sketcher::SketchObject] Sketch134
  FullyConstrained = true
  MapMode = 5
  Support = -> [XY_Plane089]
  sketch-geometry (3):
    g0: LineSegment StartX=30 StartY=30 StartZ=0 EndX=30 EndY=-30 EndZ=0
    g1: LineSegment StartX=30 StartY=-30 StartZ=0 EndX=-30 EndY=-30 EndZ=0
    g2: LineSegment StartX=-30 StartY=-30 StartZ=0 EndX=30 EndY=30 EndZ=0
  constraints (9):
    c: Vertical(g0)
    c: Coincident(g0,g1)
    c: Horizontal(g1)
    c: Coincident(g1,g2)
    c: Coincident(g2,g0)
    c: DistanceY(g0,g-1) = 30
    c: DistanceY(g-1,g0) = 30
    c: DistanceX(g1,g-1) = 30
    c: PointOnObject(g-1,g2)
FEATURE [PartDesign::Pad] Pad089
  Direction = (1,1,1)
  Length = 4
  Length2 = 100
  Profile = -> Sketch134
  Type = 0
FEATURE [PartDesign::Body] Body089  label="70mm suport-045"
  Group = -> [Sketch134,Pad089]
  Origin = -> Origin090
  Placement = pos=(880,-2713,0) rot=(0,0,1;3.14159rad)
  Tip = -> Pad089
FEATURE [Sketcher::SketchObject] Sketch135
  FullyConstrained = true
  MapMode = 5
  Support = -> [XY_Plane090]
  sketch-geometry (3):
    g0: LineSegment StartX=30 StartY=30 StartZ=0 EndX=30 EndY=-30 EndZ=0
    g1: LineSegment StartX=30 StartY=-30 StartZ=0 EndX=-30 EndY=-30 EndZ=0
    g2: LineSegment StartX=-30 StartY=-30 StartZ=0 EndX=30 EndY=30 EndZ=0
  constraints (9):
    c: Vertical(g0)
    c: Coincident(g0,g1)
    c: Horizontal(g1)
    c: Coincident(g1,g2)
    c: Coincident(g2,g0)
    c: DistanceY(g0,g-1) = 30
    c: DistanceY(g-1,g0) = 30
    c: DistanceX(g1,g-1) = 30
    c: PointOnObject(g-1,g2)
FEATURE [PartDesign::Pad] Pad090
  Direction = (1,1,1)
  Length = 4
  Length2 = 100
  Profile = -> Sketch135
  Type = 0
FEATURE [PartDesign::Body] Body090  label="70mm suport-046"
  Group = -> [Sketch135,Pad090]
  Origin = -> Origin089
  Placement = pos=(910,-2713,0) rot=(0,0,1;0rad)
  Tip = -> Pad090
FEATURE [Sketcher::SketchObject] Sketch136
  FullyConstrained = true
  MapMode = 5
  Support = -> [XY_Plane091]
  sketch-geometry (3):
    g0: LineSegment StartX=30 StartY=30 StartZ=0 EndX=30 EndY=-30 EndZ=0
    g1: LineSegment StartX=30 StartY=-30 StartZ=0 EndX=-30 EndY=-30 EndZ=0
    g2: LineSegment StartX=-30 StartY=-30 StartZ=0 EndX=30 EndY=30 EndZ=0
  constraints (9):
    c: Vertical(g0)
    c: Coincident(g0,g1)
    c: Horizontal(g1)
    c: Coincident(g1,g2)
    c: Coincident(g2,g0)
    c: DistanceY(g0,g-1) = 30
    c: DistanceY(g-1,g0) = 30
    c: DistanceX(g1,g-1) = 30
    c: PointOnObject(g-1,g2)
FEATURE [PartDesign::Pad] Pad091
  Direction = (1,1,1)
  Length = 4
  Length2 = 100
  Profile = -> Sketch136
  Type = 0
FEATURE [PartDesign::Body] Body091  label="70mm suport-047"
  Group = -> [Sketch136,Pad091]
  Origin = -> Origin091
  Placement = pos=(360,-2713,0) rot=(0,0,1;0rad)
  Tip = -> Pad091
FEATURE [Sketcher::SketchObject] Sketch137
  FullyConstrained = true
  MapMode = 5
  Support = -> [XY_Plane092]
  sketch-geometry (3):
    g0: LineSegment StartX=30 StartY=30 StartZ=0 EndX=30 EndY=-30 EndZ=0
    g1: LineSegment StartX=30 StartY=-30 StartZ=0 EndX=-30 EndY=-30 EndZ=0
    g2: LineSegment StartX=-30 StartY=-30 StartZ=0 EndX=30 EndY=30 EndZ=0
  constraints (9):
    c: Vertical(g0)
    c: Coincident(g0,g1)
    c: Horizontal(g1)
    c: Coincident(g1,g2)
    c: Coincident(g2,g0)
    c: DistanceY(g0,g-1) = 30
    c: DistanceY(g-1,g0) = 30
    c: DistanceX(g1,g-1) = 30
    c: PointOnObject(g-1,g2)
FEATURE [PartDesign::Pad] Pad092
  Direction = (1,1,1)
  Length = 4
  Length2 = 100
  Profile = -> Sketch137
  Type = 0
FEATURE [PartDesign::Body] Body093  label="70mm suport-049"
  Group = -> [Sketch137,Pad092]
  Origin = -> Origin093
  Placement = pos=(990,-2713,0) rot=(0,0,1;3.14159rad)
  Tip = -> Pad092
FEATURE [Sketcher::SketchObject] Sketch138
  FullyConstrained = true
  MapMode = 5
  Support = -> [XY_Plane093]
  sketch-geometry (3):
    g0: LineSegment StartX=30 StartY=30 StartZ=0 EndX=30 EndY=-30 EndZ=0
    g1: LineSegment StartX=30 StartY=-30 StartZ=0 EndX=-30 EndY=-30 EndZ=0
    g2: LineSegment StartX=-30 StartY=-30 StartZ=0 EndX=30 EndY=30 EndZ=0
  constraints (9):
    c: Vertical(g0)
    c: Coincident(g0,g1)
    c: Horizontal(g1)
    c: Coincident(g1,g2)
    c: Coincident(g2,g0)
    c: DistanceY(g0,g-1) = 30
    c: DistanceY(g-1,g0) = 30
    c: DistanceX(g1,g-1) = 30
    c: PointOnObject(g-1,g2)
FEATURE [PartDesign::Pad] Pad093
  Direction = (1,1,1)
  Length = 4
  Length2 = 100
  Profile = -> Sketch138
  Type = 0
FEATURE [PartDesign::Body] Body092  label="70mm suport-048"
  Group = -> [Sketch138,Pad093]
  Origin = -> Origin092
  Placement = pos=(1020,-2713,0) rot=(0,0,1;0rad)
  Tip = -> Pad093
FEATURE [Sketcher::SketchObject] Sketch139
  FullyConstrained = true
  MapMode = 5
  Support = -> [XY_Plane094]
  sketch-geometry (3):
    g0: LineSegment StartX=30 StartY=30 StartZ=0 EndX=30 EndY=-30 EndZ=0
    g1: LineSegment StartX=30 StartY=-30 StartZ=0 EndX=-30 EndY=-30 EndZ=0
    g2: LineSegment StartX=-30 StartY=-30 StartZ=0 EndX=30 EndY=30 EndZ=0
  constraints (9):
    c: Vertical(g0)
    c: Coincident(g0,g1)
    c: Horizontal(g1)
    c: Coincident(g1,g2)
    c: Coincident(g2,g0)
    c: DistanceY(g0,g-1) = 30
    c: DistanceY(g-1,g0) = 30
    c: DistanceX(g1,g-1) = 30
    c: PointOnObject(g-1,g2)
FEATURE [PartDesign::Pad] Pad094
  Direction = (1,1,1)
  Length = 4
  Length2 = 100
  Profile = -> Sketch139
  Type = 0
FEATURE [PartDesign::Body] Body095  label="70mm suport-051"
  Group = -> [Sketch139,Pad094]
  Origin = -> Origin095
  Placement = pos=(1100,-2713,0) rot=(0,0,1;3.14159rad)
  Tip = -> Pad094
FEATURE [Sketcher::SketchObject] Sketch140
  FullyConstrained = true
  MapMode = 5
  Support = -> [XY_Plane095]
  sketch-geometry (3):
    g0: LineSegment StartX=30 StartY=30 StartZ=0 EndX=30 EndY=-30 EndZ=0
    g1: LineSegment StartX=30 StartY=-30 StartZ=0 EndX=-30 EndY=-30 EndZ=0
    g2: LineSegment StartX=-30 StartY=-30 StartZ=0 EndX=30 EndY=30 EndZ=0
  constraints (9):
    c: Vertical(g0)
    c: Coincident(g0,g1)
    c: Horizontal(g1)
    c: Coincident(g1,g2)
    c: Coincident(g2,g0)
    c: DistanceY(g0,g-1) = 30
    c: DistanceY(g-1,g0) = 30
    c: DistanceX(g1,g-1) = 30
    c: PointOnObject(g-1,g2)
FEATURE [PartDesign::Pad] Pad095
  Direction = (1,1,1)
  Length = 4
  Length2 = 100
  Profile = -> Sketch140
  Type = 0
FEATURE [PartDesign::Body] Body094  label="70mm suport-050"
  Group = -> [Sketch140,Pad095]
  Origin = -> Origin094
  Placement = pos=(1130,-2713,0) rot=(0,0,1;0rad)
  Tip = -> Pad095
FEATURE [Sketcher::SketchObject] Sketch141
  FullyConstrained = true
  MapMode = 5
  Support = -> [XY_Plane096]
  sketch-geometry (3):
    g0: LineSegment StartX=30 StartY=30 StartZ=0 EndX=30 EndY=-30 EndZ=0
    g1: LineSegment StartX=30 StartY=-30 StartZ=0 EndX=-30 EndY=-30 EndZ=0
    g2: LineSegment StartX=-30 StartY=-30 StartZ=0 EndX=30 EndY=30 EndZ=0
  constraints (9):
    c: Vertical(g0)
    c: Coincident(g0,g1)
    c: Horizontal(g1)
    c: Coincident(g1,g2)
    c: Coincident(g2,g0)
    c: DistanceY(g0,g-1) = 30
    c: DistanceY(g-1,g0) = 30
    c: DistanceX(g1,g-1) = 30
    c: PointOnObject(g-1,g2)
FEATURE [Sketcher::SketchObject] Sketch142
  FullyConstrained = true
  MapMode = 5
  Support = -> [XY_Plane097]
  sketch-geometry (3):
    g0: LineSegment StartX=30 StartY=30 StartZ=0 EndX=30 EndY=-30 EndZ=0
    g1: LineSegment StartX=30 StartY=-30 StartZ=0 EndX=-30 EndY=-30 EndZ=0
    g2: LineSegment StartX=-30 StartY=-30 StartZ=0 EndX=30 EndY=30 EndZ=0
  constraints (9):
    c: Vertical(g0)
    c: Coincident(g0,g1)
    c: Horizontal(g1)
    c: Coincident(g1,g2)
    c: Coincident(g2,g0)
    c: DistanceY(g0,g-1) = 30
    c: DistanceY(g-1,g0) = 30
    c: DistanceX(g1,g-1) = 30
    c: PointOnObject(g-1,g2)
FEATURE [PartDesign::Pad] Pad096
  Direction = (1,1,1)
  Length = 4
  Length2 = 100
  Profile = -> Sketch142
  Type = 0
FEATURE [PartDesign::Body] Body096  label="70mm suport-052"
  Group = -> [Sketch142,Pad096]
  Origin = -> Origin097
  Placement = pos=(1240,-2713,0) rot=(0,0,1;0rad)
  Tip = -> Pad096
FEATURE [PartDesign::Pad] Pad097
  Direction = (1,1,1)
  Length = 4
  Length2 = 100
  Profile = -> Sketch141
  Type = 0
FEATURE [PartDesign::Body] Body097  label="70mm suport-053"
  Group = -> [Sketch141,Pad097]
  Origin = -> Origin096
  Placement = pos=(1210,-2713,0) rot=(0,0,1;3.14159rad)
  Tip = -> Pad097
FEATURE [Sketcher::SketchObject] Sketch143
  FullyConstrained = true
  MapMode = 5
  Support = -> [XY_Plane098]
  sketch-geometry (3):
    g0: LineSegment StartX=30 StartY=30 StartZ=0 EndX=30 EndY=-30 EndZ=0
    g1: LineSegment StartX=30 StartY=-30 StartZ=0 EndX=-30 EndY=-30 EndZ=0
    g2: LineSegment StartX=-30 StartY=-30 StartZ=0 EndX=30 EndY=30 EndZ=0
  constraints (9):
    c: Vertical(g0)
    c: Coincident(g0,g1)
    c: Horizontal(g1)
    c: Coincident(g1,g2)
    c: Coincident(g2,g0)
    c: DistanceY(g0,g-1) = 30
    c: DistanceY(g-1,g0) = 30
    c: DistanceX(g1,g-1) = 30
    c: PointOnObject(g-1,g2)
FEATURE [Sketcher::SketchObject] Sketch144
  FullyConstrained = true
  MapMode = 5
  Support = -> [XY_Plane099]
  sketch-geometry (3):
    g0: LineSegment StartX=30 StartY=30 StartZ=0 EndX=30 EndY=-30 EndZ=0
    g1: LineSegment StartX=30 StartY=-30 StartZ=0 EndX=-30 EndY=-30 EndZ=0
    g2: LineSegment StartX=-30 StartY=-30 StartZ=0 EndX=30 EndY=30 EndZ=0
  constraints (9):
    c: Vertical(g0)
    c: Coincident(g0,g1)
    c: Horizontal(g1)
    c: Coincident(g1,g2)
    c: Coincident(g2,g0)
    c: DistanceY(g0,g-1) = 30
    c: DistanceY(g-1,g0) = 30
    c: DistanceX(g1,g-1) = 30
    c: PointOnObject(g-1,g2)
FEATURE [PartDesign::Pad] Pad098
  Direction = (1,1,1)
  Length = 4
  Length2 = 100
  Profile = -> Sketch143
  Type = 0
FEATURE [PartDesign::Body] Body098  label="70mm suport-054"
  Group = -> [Sketch143,Pad098]
  Origin = -> Origin098
  Placement = pos=(1320,-2713,0) rot=(0,0,1;3.14159rad)
  Tip = -> Pad098
FEATURE [PartDesign::Pad] Pad099
  Direction = (1,1,1)
  Length = 4
  Length2 = 100
  Profile = -> Sketch144
  Type = 0
FEATURE [PartDesign::Body] Body099  label="70mm suport-055"
  Group = -> [Sketch144,Pad099]
  Origin = -> Origin099
  Placement = pos=(1350,-2713,0) rot=(0,0,1;0rad)
  Tip = -> Pad099
FEATURE [Sketcher::SketchObject] Sketch145
  FullyConstrained = true
  MapMode = 5
  Support = -> [XY_Plane100]
  sketch-geometry (3):
    g0: LineSegment StartX=30 StartY=30 StartZ=0 EndX=30 EndY=-30 EndZ=0
    g1: LineSegment StartX=30 StartY=-30 StartZ=0 EndX=-30 EndY=-30 EndZ=0
    g2: LineSegment StartX=-30 StartY=-30 StartZ=0 EndX=30 EndY=30 EndZ=0
  constraints (9):
    c: Vertical(g0)
    c: Coincident(g0,g1)
    c: Horizontal(g1)
    c: Coincident(g1,g2)
    c: Coincident(g2,g0)
    c: DistanceY(g0,g-1) = 30
    c: DistanceY(g-1,g0) = 30
    c: DistanceX(g1,g-1) = 30
    c: PointOnObject(g-1,g2)
FEATURE [Sketcher::SketchObject] Sketch146
  FullyConstrained = true
  MapMode = 5
  Support = -> [XY_Plane101]
  sketch-geometry (3):
    g0: LineSegment StartX=30 StartY=30 StartZ=0 EndX=30 EndY=-30 EndZ=0
    g1: LineSegment StartX=30 StartY=-30 StartZ=0 EndX=-30 EndY=-30 EndZ=0
    g2: LineSegment StartX=-30 StartY=-30 StartZ=0 EndX=30 EndY=30 EndZ=0
  constraints (9):
    c: Vertical(g0)
    c: Coincident(g0,g1)
    c: Horizontal(g1)
    c: Coincident(g1,g2)
    c: Coincident(g2,g0)
    c: DistanceY(g0,g-1) = 30
    c: DistanceY(g-1,g0) = 30
    c: DistanceX(g1,g-1) = 30
    c: PointOnObject(g-1,g2)
FEATURE [PartDesign::Pad] Pad100
  Direction = (1,1,1)
  Length = 4
  Length2 = 100
  Profile = -> Sketch146
  Type = 0
FEATURE [PartDesign::Body] Body101  label="70mm suport-057"
  Group = -> [Sketch146,Pad100]
  Origin = -> Origin101
  Placement = pos=(1460,-2713,0) rot=(0,0,1;0rad)
  Tip = -> Pad100
FEATURE [PartDesign::Pad] Pad101
  Direction = (1,1,1)
  Length = 4
  Length2 = 100
  Profile = -> Sketch145
  Type = 0
FEATURE [PartDesign::Body] Body100  label="70mm suport-056"
  Group = -> [Sketch145,Pad101]
  Origin = -> Origin100
  Placement = pos=(1430,-2713,0) rot=(0,0,1;3.14159rad)
  Tip = -> Pad101
FEATURE [Sketcher::SketchObject] Sketch147
  FullyConstrained = true
  MapMode = 5
  Support = -> [XY_Plane102]
  sketch-geometry (3):
    g0: LineSegment StartX=30 StartY=30 StartZ=0 EndX=30 EndY=-30 EndZ=0
    g1: LineSegment StartX=30 StartY=-30 StartZ=0 EndX=-30 EndY=-30 EndZ=0
    g2: LineSegment StartX=-30 StartY=-30 StartZ=0 EndX=30 EndY=30 EndZ=0
  constraints (9):
    c: Vertical(g0)
    c: Coincident(g0,g1)
    c: Horizontal(g1)
    c: Coincident(g1,g2)
    c: Coincident(g2,g0)
    c: DistanceY(g0,g-1) = 30
    c: DistanceY(g-1,g0) = 30
    c: DistanceX(g1,g-1) = 30
    c: PointOnObject(g-1,g2)
FEATURE [Sketcher::SketchObject] Sketch148
  FullyConstrained = true
  MapMode = 5
  Support = -> [XY_Plane103]
  sketch-geometry (3):
    g0: LineSegment StartX=30 StartY=30 StartZ=0 EndX=30 EndY=-30 EndZ=0
    g1: LineSegment StartX=30 StartY=-30 StartZ=0 EndX=-30 EndY=-30 EndZ=0
    g2: LineSegment StartX=-30 StartY=-30 StartZ=0 EndX=30 EndY=30 EndZ=0
  constraints (9):
    c: Vertical(g0)
    c: Coincident(g0,g1)
    c: Horizontal(g1)
    c: Coincident(g1,g2)
    c: Coincident(g2,g0)
    c: DistanceY(g0,g-1) = 30
    c: DistanceY(g-1,g0) = 30
    c: DistanceX(g1,g-1) = 30
    c: PointOnObject(g-1,g2)
FEATURE [PartDesign::Pad] Pad102
  Direction = (1,1,1)
  Length = 4
  Length2 = 100
  Profile = -> Sketch147
  Type = 0
FEATURE [PartDesign::Pad] Pad103
  Direction = (1,1,1)
  Length = 4
  Length2 = 100
  Profile = -> Sketch148
  Type = 0
FEATURE [PartDesign::Body] Body102  label="70mm suport-058"
  Group = -> [Sketch148,Pad103]
  Origin = -> Origin103
  Placement = pos=(1570,-2713,0) rot=(0,0,1;0rad)
  Tip = -> Pad103
FEATURE [PartDesign::Body] Body103  label="70mm suport-059"
  Group = -> [Sketch147,Pad102]
  Origin = -> Origin102
  Placement = pos=(1540,-2713,0) rot=(0,0,1;3.14159rad)
  Tip = -> Pad102
FEATURE [Sketcher::SketchObject] Sketch149
  FullyConstrained = true
  MapMode = 5
  Support = -> [XY_Plane104]
  sketch-geometry (4):
    g0: LineSegment StartX=-35 StartY=35 StartZ=0 EndX=35 EndY=35 EndZ=0
    g1: LineSegment StartX=35 StartY=35 StartZ=0 EndX=35 EndY=-35 EndZ=0
    g2: LineSegment StartX=35 StartY=-35 StartZ=0 EndX=-35 EndY=-35 EndZ=0
    g3: LineSegment StartX=-35 StartY=-35 StartZ=0 EndX=-35 EndY=35 EndZ=0
  constraints (11):
    c: Coincident(g0,g1)
    c: Coincident(g1,g2)
    c: Coincident(g2,g3)
    c: Coincident(g3,g0)
    c: Horizontal(g0)
    c: Horizontal(g2)
    c: Vertical(g1)
    c: Vertical(g3)
    c: Symmetric(g0,g1,g-1)
    c: DistanceX(g2,g1) = 70
    c: DistanceY(g2,g0) = 70
FEATURE [PartDesign::Pad] Pad104
  Direction = (1,1,1)
  Length = 4
  Length2 = 100
  Profile = -> Sketch149
  Type = 0
FEATURE [PartDesign::Body] Body104  label="70mm square suport-060"
  Group = -> [Sketch149,Pad104]
  Origin = -> Origin104
  Placement = pos=(0,-2813,0) rot=(0,0,1;0rad)
  Tip = -> Pad104
FEATURE [Sketcher::SketchObject] Sketch150
  FullyConstrained = true
  MapMode = 5
  Support = -> [XY_Plane105]
  sketch-geometry (4):
    g0: LineSegment StartX=-35 StartY=35 StartZ=0 EndX=35 EndY=35 EndZ=0
    g1: LineSegment StartX=35 StartY=35 StartZ=0 EndX=35 EndY=-35 EndZ=0
    g2: LineSegment StartX=35 StartY=-35 StartZ=0 EndX=-35 EndY=-35 EndZ=0
    g3: LineSegment StartX=-35 StartY=-35 StartZ=0 EndX=-35 EndY=35 EndZ=0
  constraints (11):
    c: Coincident(g0,g1)
    c: Coincident(g1,g2)
    c: Coincident(g2,g3)
    c: Coincident(g3,g0)
    c: Horizontal(g0)
    c: Horizontal(g2)
    c: Vertical(g1)
    c: Vertical(g3)
    c: Symmetric(g0,g1,g-1)
    c: DistanceX(g2,g1) = 70
    c: DistanceY(g2,g0) = 70
FEATURE [PartDesign::Pad] Pad105
  Direction = (1,1,1)
  Length = 4
  Length2 = 100
  Profile = -> Sketch150
  Type = 0
FEATURE [PartDesign::Body] Body105  label="70mm square suport-061"
  Group = -> [Sketch150,Pad105]
  Origin = -> Origin105
  Placement = pos=(0,-2913,0) rot=(0,0,1;0rad)
  Tip = -> Pad105
FEATURE [Sketcher::SketchObject] Sketch151
  FullyConstrained = true
  MapMode = 5
  Support = -> [XY_Plane107]
  sketch-geometry (4):
    g0: LineSegment StartX=-35 StartY=35 StartZ=0 EndX=35 EndY=35 EndZ=0
    g1: LineSegment StartX=35 StartY=35 StartZ=0 EndX=35 EndY=-35 EndZ=0
    g2: LineSegment StartX=35 StartY=-35 StartZ=0 EndX=-35 EndY=-35 EndZ=0
    g3: LineSegment StartX=-35 StartY=-35 StartZ=0 EndX=-35 EndY=35 EndZ=0
  constraints (11):
    c: Coincident(g0,g1)
    c: Coincident(g1,g2)
    c: Coincident(g2,g3)
    c: Coincident(g3,g0)
    c: Horizontal(g0)
    c: Horizontal(g2)
    c: Vertical(g1)
    c: Vertical(g3)
    c: Symmetric(g0,g1,g-1)
    c: DistanceX(g2,g1) = 70
    c: DistanceY(g2,g0) = 70
FEATURE [Sketcher::SketchObject] Sketch152
  FullyConstrained = true
  MapMode = 5
  Support = -> [XY_Plane106]
  sketch-geometry (4):
    g0: LineSegment StartX=-35 StartY=35 StartZ=0 EndX=35 EndY=35 EndZ=0
    g1: LineSegment StartX=35 StartY=35 StartZ=0 EndX=35 EndY=-35 EndZ=0
    g2: LineSegment StartX=35 StartY=-35 StartZ=0 EndX=-35 EndY=-35 EndZ=0
    g3: LineSegment StartX=-35 StartY=-35 StartZ=0 EndX=-35 EndY=35 EndZ=0
  constraints (11):
    c: Coincident(g0,g1)
    c: Coincident(g1,g2)
    c: Coincident(g2,g3)
    c: Coincident(g3,g0)
    c: Horizontal(g0)
    c: Horizontal(g2)
    c: Vertical(g1)
    c: Vertical(g3)
    c: Symmetric(g0,g1,g-1)
    c: DistanceX(g2,g1) = 70
    c: DistanceY(g2,g0) = 70
FEATURE [PartDesign::Pad] Pad106
  Direction = (1,1,1)
  Length = 4
  Length2 = 100
  Profile = -> Sketch151
  Type = 0
FEATURE [PartDesign::Body] Body106  label="70mm square suport-062"
  Group = -> [Sketch151,Pad106]
  Origin = -> Origin106
  Placement = pos=(100,-2813,0) rot=(0,0,1;0rad)
  Tip = -> Pad106
FEATURE [PartDesign::Pad] Pad107
  Direction = (1,1,1)
  Length = 4
  Length2 = 100
  Profile = -> Sketch152
  Type = 0
FEATURE [PartDesign::Body] Body107  label="70mm square suport-063"
  Group = -> [Sketch152,Pad107]
  Origin = -> Origin107
  Placement = pos=(100,-2913,0) rot=(0,0,1;0rad)
  Tip = -> Pad107
FEATURE [Sketcher::SketchObject] Sketch153
  FullyConstrained = true
  MapMode = 5
  Support = -> [XY_Plane108]
  sketch-geometry (4):
    g0: LineSegment StartX=-35 StartY=35 StartZ=0 EndX=35 EndY=35 EndZ=0
    g1: LineSegment StartX=35 StartY=35 StartZ=0 EndX=35 EndY=-35 EndZ=0
    g2: LineSegment StartX=35 StartY=-35 StartZ=0 EndX=-35 EndY=-35 EndZ=0
    g3: LineSegment StartX=-35 StartY=-35 StartZ=0 EndX=-35 EndY=35 EndZ=0
  constraints (11):
    c: Coincident(g0,g1)
    c: Coincident(g1,g2)
    c: Coincident(g2,g3)
    c: Coincident(g3,g0)
    c: Horizontal(g0)
    c: Horizontal(g2)
    c: Vertical(g1)
    c: Vertical(g3)
    c: Symmetric(g0,g1,g-1)
    c: DistanceX(g2,g1) = 70
    c: DistanceY(g2,g0) = 70
FEATURE [Sketcher::SketchObject] Sketch154
  FullyConstrained = true
  MapMode = 5
  Support = -> [XY_Plane109]
  sketch-geometry (4):
    g0: LineSegment StartX=-35 StartY=35 StartZ=0 EndX=35 EndY=35 EndZ=0
    g1: LineSegment StartX=35 StartY=35 StartZ=0 EndX=35 EndY=-35 EndZ=0
    g2: LineSegment StartX=35 StartY=-35 StartZ=0 EndX=-35 EndY=-35 EndZ=0
    g3: LineSegment StartX=-35 StartY=-35 StartZ=0 EndX=-35 EndY=35 EndZ=0
  constraints (11):
    c: Coincident(g0,g1)
    c: Coincident(g1,g2)
    c: Coincident(g2,g3)
    c: Coincident(g3,g0)
    c: Horizontal(g0)
    c: Horizontal(g2)
    c: Vertical(g1)
    c: Vertical(g3)
    c: Symmetric(g0,g1,g-1)
    c: DistanceX(g2,g1) = 70
    c: DistanceY(g2,g0) = 70
FEATURE [PartDesign::Pad] Pad108
  Direction = (1,1,1)
  Length = 4
  Length2 = 100
  Profile = -> Sketch153
  Type = 0
FEATURE [PartDesign::Body] Body109  label="70mm square suport-065"
  Group = -> [Sketch153,Pad108]
  Origin = -> Origin109
  Placement = pos=(200,-2913,0) rot=(0,0,1;0rad)
  Tip = -> Pad108
FEATURE [PartDesign::Pad] Pad109
  Direction = (1,1,1)
  Length = 4
  Length2 = 100
  Profile = -> Sketch154
  Type = 0
FEATURE [PartDesign::Body] Body108  label="70mm square suport-064"
  Group = -> [Sketch154,Pad109]
  Origin = -> Origin108
  Placement = pos=(200,-2813,0) rot=(0,0,1;0rad)
  Tip = -> Pad109
FEATURE [Sketcher::SketchObject] Sketch155
  FullyConstrained = true
  MapMode = 5
  Support = -> [XY_Plane111]
  sketch-geometry (4):
    g0: LineSegment StartX=-35 StartY=35 StartZ=0 EndX=35 EndY=35 EndZ=0
    g1: LineSegment StartX=35 StartY=35 StartZ=0 EndX=35 EndY=-35 EndZ=0
    g2: LineSegment StartX=35 StartY=-35 StartZ=0 EndX=-35 EndY=-35 EndZ=0
    g3: LineSegment StartX=-35 StartY=-35 StartZ=0 EndX=-35 EndY=35 EndZ=0
  constraints (11):
    c: Coincident(g0,g1)
    c: Coincident(g1,g2)
    c: Coincident(g2,g3)
    c: Coincident(g3,g0)
    c: Horizontal(g0)
    c: Horizontal(g2)
    c: Vertical(g1)
    c: Vertical(g3)
    c: Symmetric(g0,g1,g-1)
    c: DistanceX(g2,g1) = 70
    c: DistanceY(g2,g0) = 70
FEATURE [PartDesign::Pad] Pad111
  Direction = (1,1,1)
  Length = 4
  Length2 = 100
  Profile = -> Sketch155
  Type = 0
FEATURE [Sketcher::SketchObject] Sketch156
  FullyConstrained = true
  MapMode = 5
  Support = -> [XY_Plane110]
  sketch-geometry (4):
    g0: LineSegment StartX=-35 StartY=35 StartZ=0 EndX=35 EndY=35 EndZ=0
    g1: LineSegment StartX=35 StartY=35 StartZ=0 EndX=35 EndY=-35 EndZ=0
    g2: LineSegment StartX=35 StartY=-35 StartZ=0 EndX=-35 EndY=-35 EndZ=0
    g3: LineSegment StartX=-35 StartY=-35 StartZ=0 EndX=-35 EndY=35 EndZ=0
  constraints (11):
    c: Coincident(g0,g1)
    c: Coincident(g1,g2)
    c: Coincident(g2,g3)
    c: Coincident(g3,g0)
    c: Horizontal(g0)
    c: Horizontal(g2)
    c: Vertical(g1)
    c: Vertical(g3)
    c: Symmetric(g0,g1,g-1)
    c: DistanceX(g2,g1) = 70
    c: DistanceY(g2,g0) = 70
FEATURE [PartDesign::Pad] Pad110
  Direction = (1,1,1)
  Length = 4
  Length2 = 100
  Profile = -> Sketch156
  Type = 0
FEATURE [PartDesign::Body] Body110  label="70mm square suport-066"
  Group = -> [Sketch156,Pad110]
  Origin = -> Origin110
  Placement = pos=(300,-2813,0) rot=(0,0,1;0rad)
  Tip = -> Pad110
FEATURE [PartDesign::Body] Body111  label="70mm square suport-067"
  Group = -> [Sketch155,Pad111]
  Origin = -> Origin111
  Placement = pos=(300,-2913,0) rot=(0,0,1;0rad)
  Tip = -> Pad111
FEATURE [Sketcher::SketchObject] Sketch157
  FullyConstrained = true
  MapMode = 5
  Support = -> [XY_Plane113]
  sketch-geometry (4):
    g0: LineSegment StartX=-35 StartY=35 StartZ=0 EndX=35 EndY=35 EndZ=0
    g1: LineSegment StartX=35 StartY=35 StartZ=0 EndX=35 EndY=-35 EndZ=0
    g2: LineSegment StartX=35 StartY=-35 StartZ=0 EndX=-35 EndY=-35 EndZ=0
    g3: LineSegment StartX=-35 StartY=-35 StartZ=0 EndX=-35 EndY=35 EndZ=0
  constraints (11):
    c: Coincident(g0,g1)
    c: Coincident(g1,g2)
    c: Coincident(g2,g3)
    c: Coincident(g3,g0)
    c: Horizontal(g0)
    c: Horizontal(g2)
    c: Vertical(g1)
    c: Vertical(g3)
    c: Symmetric(g0,g1,g-1)
    c: DistanceX(g2,g1) = 70
    c: DistanceY(g2,g0) = 70
FEATURE [Sketcher::SketchObject] Sketch158
  FullyConstrained = true
  MapMode = 5
  Support = -> [XY_Plane112]
  sketch-geometry (4):
    g0: LineSegment StartX=-35 StartY=35 StartZ=0 EndX=35 EndY=35 EndZ=0
    g1: LineSegment StartX=35 StartY=35 StartZ=0 EndX=35 EndY=-35 EndZ=0
    g2: LineSegment StartX=35 StartY=-35 StartZ=0 EndX=-35 EndY=-35 EndZ=0
    g3: LineSegment StartX=-35 StartY=-35 StartZ=0 EndX=-35 EndY=35 EndZ=0
  constraints (11):
    c: Coincident(g0,g1)
    c: Coincident(g1,g2)
    c: Coincident(g2,g3)
    c: Coincident(g3,g0)
    c: Horizontal(g0)
    c: Horizontal(g2)
    c: Vertical(g1)
    c: Vertical(g3)
    c: Symmetric(g0,g1,g-1)
    c: DistanceX(g2,g1) = 70
    c: DistanceY(g2,g0) = 70
FEATURE [PartDesign::Pad] Pad112
  Direction = (1,1,1)
  Length = 4
  Length2 = 100
  Profile = -> Sketch158
  Type = 0
FEATURE [PartDesign::Body] Body113  label="70mm square suport-069"
  Group = -> [Sketch158,Pad112]
  Origin = -> Origin112
  Placement = pos=(400,-2813,0) rot=(0,0,1;0rad)
  Tip = -> Pad112
FEATURE [PartDesign::Pad] Pad113
  Direction = (1,1,1)
  Length = 4
  Length2 = 100
  Profile = -> Sketch157
  Type = 0
FEATURE [PartDesign::Body] Body112  label="70mm square suport-068"
  Group = -> [Sketch157,Pad113]
  Origin = -> Origin113
  Placement = pos=(400,-2913,0) rot=(0,0,1;0rad)
  Tip = -> Pad113
FEATURE [Sketcher::SketchObject] Sketch159
  FullyConstrained = true
  MapMode = 5
  Support = -> [XY_Plane115]
  sketch-geometry (4):
    g0: LineSegment StartX=-35 StartY=35 StartZ=0 EndX=35 EndY=35 EndZ=0
    g1: LineSegment StartX=35 StartY=35 StartZ=0 EndX=35 EndY=-35 EndZ=0
    g2: LineSegment StartX=35 StartY=-35 StartZ=0 EndX=-35 EndY=-35 EndZ=0
    g3: LineSegment StartX=-35 StartY=-35 StartZ=0 EndX=-35 EndY=35 EndZ=0
  constraints (11):
    c: Coincident(g0,g1)
    c: Coincident(g1,g2)
    c: Coincident(g2,g3)
    c: Coincident(g3,g0)
    c: Horizontal(g0)
    c: Horizontal(g2)
    c: Vertical(g1)
    c: Vertical(g3)
    c: Symmetric(g0,g1,g-1)
    c: DistanceX(g2,g1) = 70
    c: DistanceY(g2,g0) = 70
FEATURE [Sketcher::SketchObject] Sketch160
  FullyConstrained = true
  MapMode = 5
  Support = -> [XY_Plane114]
  sketch-geometry (4):
    g0: LineSegment StartX=-35 StartY=35 StartZ=0 EndX=35 EndY=35 EndZ=0
    g1: LineSegment StartX=35 StartY=35 StartZ=0 EndX=35 EndY=-35 EndZ=0
    g2: LineSegment StartX=35 StartY=-35 StartZ=0 EndX=-35 EndY=-35 EndZ=0
    g3: LineSegment StartX=-35 StartY=-35 StartZ=0 EndX=-35 EndY=35 EndZ=0
  constraints (11):
    c: Coincident(g0,g1)
    c: Coincident(g1,g2)
    c: Coincident(g2,g3)
    c: Coincident(g3,g0)
    c: Horizontal(g0)
    c: Horizontal(g2)
    c: Vertical(g1)
    c: Vertical(g3)
    c: Symmetric(g0,g1,g-1)
    c: DistanceX(g2,g1) = 70
    c: DistanceY(g2,g0) = 70
FEATURE [PartDesign::Pad] Pad114
  Direction = (1,1,1)
  Length = 4
  Length2 = 100
  Profile = -> Sketch160
  Type = 0
FEATURE [PartDesign::Body] Body115  label="70mm square suport-071"
  Group = -> [Sketch160,Pad114]
  Origin = -> Origin114
  Placement = pos=(500,-2813,0) rot=(0,0,1;0rad)
  Tip = -> Pad114
FEATURE [PartDesign::Pad] Pad115
  Direction = (1,1,1)
  Length = 4
  Length2 = 100
  Profile = -> Sketch159
  Type = 0
FEATURE [PartDesign::Body] Body114  label="70mm square suport-070"
  Group = -> [Sketch159,Pad115]
  Origin = -> Origin115
  Placement = pos=(500,-2913,0) rot=(0,0,1;0rad)
  Tip = -> Pad115
FEATURE [Sketcher::SketchObject] Sketch161
  FullyConstrained = true
  MapMode = 5
  Support = -> [XY_Plane117]
  sketch-geometry (4):
    g0: LineSegment StartX=-35 StartY=35 StartZ=0 EndX=35 EndY=35 EndZ=0
    g1: LineSegment StartX=35 StartY=35 StartZ=0 EndX=35 EndY=-35 EndZ=0
    g2: LineSegment StartX=35 StartY=-35 StartZ=0 EndX=-35 EndY=-35 EndZ=0
    g3: LineSegment StartX=-35 StartY=-35 StartZ=0 EndX=-35 EndY=35 EndZ=0
  constraints (11):
    c: Coincident(g0,g1)
    c: Coincident(g1,g2)
    c: Coincident(g2,g3)
    c: Coincident(g3,g0)
    c: Horizontal(g0)
    c: Horizontal(g2)
    c: Vertical(g1)
    c: Vertical(g3)
    c: Symmetric(g0,g1,g-1)
    c: DistanceX(g2,g1) = 70
    c: DistanceY(g2,g0) = 70
FEATURE [PartDesign::Pad] Pad117
  Direction = (1,1,1)
  Length = 4
  Length2 = 100
  Profile = -> Sketch161
  Type = 0
FEATURE [Sketcher::SketchObject] Sketch162
  FullyConstrained = true
  MapMode = 5
  Support = -> [XY_Plane116]
  sketch-geometry (4):
    g0: LineSegment StartX=-35 StartY=35 StartZ=0 EndX=35 EndY=35 EndZ=0
    g1: LineSegment StartX=35 StartY=35 StartZ=0 EndX=35 EndY=-35 EndZ=0
    g2: LineSegment StartX=35 StartY=-35 StartZ=0 EndX=-35 EndY=-35 EndZ=0
    g3: LineSegment StartX=-35 StartY=-35 StartZ=0 EndX=-35 EndY=35 EndZ=0
  constraints (11):
    c: Coincident(g0,g1)
    c: Coincident(g1,g2)
    c: Coincident(g2,g3)
    c: Coincident(g3,g0)
    c: Horizontal(g0)
    c: Horizontal(g2)
    c: Vertical(g1)
    c: Vertical(g3)
    c: Symmetric(g0,g1,g-1)
    c: DistanceX(g2,g1) = 70
    c: DistanceY(g2,g0) = 70
FEATURE [PartDesign::Pad] Pad116
  Direction = (1,1,1)
  Length = 4
  Length2 = 100
  Profile = -> Sketch162
  Type = 0
FEATURE [PartDesign::Body] Body116  label="70mm square suport-072"
  Group = -> [Sketch162,Pad116]
  Origin = -> Origin116
  Placement = pos=(600,-2813,0) rot=(0,0,1;0rad)
  Tip = -> Pad116
FEATURE [PartDesign::Body] Body117  label="70mm square suport-073"
  Group = -> [Sketch161,Pad117]
  Origin = -> Origin117
  Placement = pos=(600,-2913,0) rot=(0,0,1;0rad)
  Tip = -> Pad117
FEATURE [Sketcher::SketchObject] Sketch163
  FullyConstrained = true
  MapMode = 5
  Support = -> [XY_Plane118]
  sketch-geometry (4):
    g0: LineSegment StartX=-35 StartY=35 StartZ=0 EndX=35 EndY=35 EndZ=0
    g1: LineSegment StartX=35 StartY=35 StartZ=0 EndX=35 EndY=-35 EndZ=0
    g2: LineSegment StartX=35 StartY=-35 StartZ=0 EndX=-35 EndY=-35 EndZ=0
    g3: LineSegment StartX=-35 StartY=-35 StartZ=0 EndX=-35 EndY=35 EndZ=0
  constraints (11):
    c: Coincident(g0,g1)
    c: Coincident(g1,g2)
    c: Coincident(g2,g3)
    c: Coincident(g3,g0)
    c: Horizontal(g0)
    c: Horizontal(g2)
    c: Vertical(g1)
    c: Vertical(g3)
    c: Symmetric(g0,g1,g-1)
    c: DistanceX(g2,g1) = 70
    c: DistanceY(g2,g0) = 70
FEATURE [PartDesign::Pad] Pad118
  Direction = (1,1,1)
  Length = 4
  Length2 = 100
  Profile = -> Sketch163
  Type = 0
FEATURE [Sketcher::SketchObject] Sketch164
  FullyConstrained = true
  MapMode = 5
  Support = -> [XY_Plane119]
  sketch-geometry (4):
    g0: LineSegment StartX=-35 StartY=35 StartZ=0 EndX=35 EndY=35 EndZ=0
    g1: LineSegment StartX=35 StartY=35 StartZ=0 EndX=35 EndY=-35 EndZ=0
    g2: LineSegment StartX=35 StartY=-35 StartZ=0 EndX=-35 EndY=-35 EndZ=0
    g3: LineSegment StartX=-35 StartY=-35 StartZ=0 EndX=-35 EndY=35 EndZ=0
  constraints (11):
    c: Coincident(g0,g1)
    c: Coincident(g1,g2)
    c: Coincident(g2,g3)
    c: Coincident(g3,g0)
    c: Horizontal(g0)
    c: Horizontal(g2)
    c: Vertical(g1)
    c: Vertical(g3)
    c: Symmetric(g0,g1,g-1)
    c: DistanceX(g2,g1) = 70
    c: DistanceY(g2,g0) = 70
FEATURE [PartDesign::Pad] Pad119
  Direction = (1,1,1)
  Length = 4
  Length2 = 100
  Profile = -> Sketch164
  Type = 0
FEATURE [PartDesign::Body] Body118  label="70mm square suport-074"
  Group = -> [Sketch163,Pad118]
  Origin = -> Origin119
  Placement = pos=(700,-2813,0) rot=(0,0,1;0rad)
  Tip = -> Pad118
FEATURE [PartDesign::Body] Body119  label="70mm square suport-075"
  Group = -> [Sketch164,Pad119]
  Origin = -> Origin118
  Placement = pos=(700,-2913,0) rot=(0,0,1;0rad)
  Tip = -> Pad119
FEATURE [Sketcher::SketchObject] Sketch165
  FullyConstrained = true
  MapMode = 5
  Support = -> [XY_Plane120]
  sketch-geometry (4):
    g0: LineSegment StartX=-35 StartY=35 StartZ=0 EndX=35 EndY=35 EndZ=0
    g1: LineSegment StartX=35 StartY=35 StartZ=0 EndX=35 EndY=-35 EndZ=0
    g2: LineSegment StartX=35 StartY=-35 StartZ=0 EndX=-35 EndY=-35 EndZ=0
    g3: LineSegment StartX=-35 StartY=-35 StartZ=0 EndX=-35 EndY=35 EndZ=0
  constraints (11):
    c: Coincident(g0,g1)
    c: Coincident(g1,g2)
    c: Coincident(g2,g3)
    c: Coincident(g3,g0)
    c: Horizontal(g0)
    c: Horizontal(g2)
    c: Vertical(g1)
    c: Vertical(g3)
    c: Symmetric(g0,g1,g-1)
    c: DistanceX(g2,g1) = 70
    c: DistanceY(g2,g0) = 70
FEATURE [PartDesign::Pad] Pad121
  Direction = (1,1,1)
  Length = 4
  Length2 = 100
  Profile = -> Sketch165
  Type = 0
FEATURE [Sketcher::SketchObject] Sketch166
  FullyConstrained = true
  MapMode = 5
  Support = -> [XY_Plane121]
  sketch-geometry (4):
    g0: LineSegment StartX=-35 StartY=35 StartZ=0 EndX=35 EndY=35 EndZ=0
    g1: LineSegment StartX=35 StartY=35 StartZ=0 EndX=35 EndY=-35 EndZ=0
    g2: LineSegment StartX=35 StartY=-35 StartZ=0 EndX=-35 EndY=-35 EndZ=0
    g3: LineSegment StartX=-35 StartY=-35 StartZ=0 EndX=-35 EndY=35 EndZ=0
  constraints (11):
    c: Coincident(g0,g1)
    c: Coincident(g1,g2)
    c: Coincident(g2,g3)
    c: Coincident(g3,g0)
    c: Horizontal(g0)
    c: Horizontal(g2)
    c: Vertical(g1)
    c: Vertical(g3)
    c: Symmetric(g0,g1,g-1)
    c: DistanceX(g2,g1) = 70
    c: DistanceY(g2,g0) = 70
FEATURE [PartDesign::Pad] Pad120
  Direction = (1,1,1)
  Length = 4
  Length2 = 100
  Profile = -> Sketch166
  Type = 0
FEATURE [PartDesign::Body] Body120  label="70mm square suport-076"
  Group = -> [Sketch166,Pad120]
  Origin = -> Origin121
  Placement = pos=(800,-2913,0) rot=(0,0,1;0rad)
  Tip = -> Pad120
FEATURE [PartDesign::Body] Body121  label="70mm square suport-077"
  Group = -> [Sketch165,Pad121]
  Origin = -> Origin120
  Placement = pos=(800,-2813,0) rot=(0,0,1;0rad)
  Tip = -> Pad121
FEATURE [Sketcher::SketchObject] Sketch167
  FullyConstrained = true
  MapMode = 5
  Support = -> [XY_Plane122]
  sketch-geometry (4):
    g0: LineSegment StartX=-35 StartY=35 StartZ=0 EndX=35 EndY=35 EndZ=0
    g1: LineSegment StartX=35 StartY=35 StartZ=0 EndX=35 EndY=-35 EndZ=0
    g2: LineSegment StartX=35 StartY=-35 StartZ=0 EndX=-35 EndY=-35 EndZ=0
    g3: LineSegment StartX=-35 StartY=-35 StartZ=0 EndX=-35 EndY=35 EndZ=0
  constraints (11):
    c: Coincident(g0,g1)
    c: Coincident(g1,g2)
    c: Coincident(g2,g3)
    c: Coincident(g3,g0)
    c: Horizontal(g0)
    c: Horizontal(g2)
    c: Vertical(g1)
    c: Vertical(g3)
    c: Symmetric(g0,g1,g-1)
    c: DistanceX(g2,g1) = 70
    c: DistanceY(g2,g0) = 70
FEATURE [PartDesign::Pad] Pad123
  Direction = (1,1,1)
  Length = 4
  Length2 = 100
  Profile = -> Sketch167
  Type = 0
FEATURE [Sketcher::SketchObject] Sketch168
  FullyConstrained = true
  MapMode = 5
  Support = -> [XY_Plane123]
  sketch-geometry (4):
    g0: LineSegment StartX=-35 StartY=35 StartZ=0 EndX=35 EndY=35 EndZ=0
    g1: LineSegment StartX=35 StartY=35 StartZ=0 EndX=35 EndY=-35 EndZ=0
    g2: LineSegment StartX=35 StartY=-35 StartZ=0 EndX=-35 EndY=-35 EndZ=0
    g3: LineSegment StartX=-35 StartY=-35 StartZ=0 EndX=-35 EndY=35 EndZ=0
  constraints (11):
    c: Coincident(g0,g1)
    c: Coincident(g1,g2)
    c: Coincident(g2,g3)
    c: Coincident(g3,g0)
    c: Horizontal(g0)
    c: Horizontal(g2)
    c: Vertical(g1)
    c: Vertical(g3)
    c: Symmetric(g0,g1,g-1)
    c: DistanceX(g2,g1) = 70
    c: DistanceY(g2,g0) = 70
FEATURE [PartDesign::Pad] Pad122
  Direction = (1,1,1)
  Length = 4
  Length2 = 100
  Profile = -> Sketch168
  Type = 0
FEATURE [PartDesign::Body] Body122  label="70mm square suport-078"
  Group = -> [Sketch167,Pad123]
  Origin = -> Origin123
  Placement = pos=(900,-2913,0) rot=(0,0,1;0rad)
  Tip = -> Pad123
FEATURE [PartDesign::Body] Body123  label="70mm square suport-079"
  Group = -> [Sketch168,Pad122]
  Origin = -> Origin122
  Placement = pos=(900,-2813,0) rot=(0,0,1;0rad)
  Tip = -> Pad122
FEATURE [Sketcher::SketchObject] Sketch169
  FullyConstrained = true
  MapMode = 5
  Support = -> [XY_Plane124]
  sketch-geometry (3):
    g0: LineSegment StartX=15 StartY=15 StartZ=0 EndX=15 EndY=-15 EndZ=0
    g1: LineSegment StartX=15 StartY=-15 StartZ=0 EndX=-15 EndY=-15 EndZ=0
    g2: LineSegment StartX=-15 StartY=-15 StartZ=0 EndX=15 EndY=15 EndZ=0
  constraints (9):
    c: Vertical(g0)
    c: Coincident(g0,g1)
    c: Horizontal(g1)
    c: Coincident(g1,g2)
    c: Coincident(g2,g0)
    c: DistanceY(g0,g-1) = 15
    c: DistanceY(g-1,g0) = 15
    c: DistanceX(g1,g-1) = 15
    c: PointOnObject(g-1,g2)
FEATURE [PartDesign::Pad] Pad124
  Direction = (1,1,1)
  Length = 4
  Length2 = 100
  Profile = -> Sketch169
  Type = 0
FEATURE [PartDesign::Body] Body124  label="30mm suport-060"
  Group = -> [Sketch169,Pad124]
  Origin = -> Origin124
  Placement = pos=(0,-3013,0) rot=(0,0,1;0rad)
  Tip = -> Pad124
FEATURE [Sketcher::SketchObject] Sketch170
  FullyConstrained = true
  MapMode = 5
  Support = -> [XY_Plane125]
  sketch-geometry (3):
    g0: LineSegment StartX=15 StartY=15 StartZ=0 EndX=15 EndY=-15 EndZ=0
    g1: LineSegment StartX=15 StartY=-15 StartZ=0 EndX=-15 EndY=-15 EndZ=0
    g2: LineSegment StartX=-15 StartY=-15 StartZ=0 EndX=15 EndY=15 EndZ=0
  constraints (9):
    c: Vertical(g0)
    c: Coincident(g0,g1)
    c: Horizontal(g1)
    c: Coincident(g1,g2)
    c: Coincident(g2,g0)
    c: DistanceY(g0,g-1) = 15
    c: DistanceY(g-1,g0) = 15
    c: DistanceX(g1,g-1) = 15
    c: PointOnObject(g-1,g2)
FEATURE [PartDesign::Pad] Pad125
  Direction = (1,1,1)
  Length = 4
  Length2 = 100
  Profile = -> Sketch170
  Type = 0
FEATURE [PartDesign::Body] Body125  label="30mm support-061"
  Group = -> [Sketch170,Pad125]
  Origin = -> Origin125
  Placement = pos=(56,-3013,0) rot=(0,0,1;3.14159rad)
  Tip = -> Pad125
FEATURE [Sketcher::SketchObject] Sketch171
  FullyConstrained = true
  MapMode = 5
  Support = -> [XY_Plane127]
  sketch-geometry (3):
    g0: LineSegment StartX=15 StartY=15 StartZ=0 EndX=15 EndY=-15 EndZ=0
    g1: LineSegment StartX=15 StartY=-15 StartZ=0 EndX=-15 EndY=-15 EndZ=0
    g2: LineSegment StartX=-15 StartY=-15 StartZ=0 EndX=15 EndY=15 EndZ=0
  constraints (9):
    c: Vertical(g0)
    c: Coincident(g0,g1)
    c: Horizontal(g1)
    c: Coincident(g1,g2)
    c: Coincident(g2,g0)
    c: DistanceY(g0,g-1) = 15
    c: DistanceY(g-1,g0) = 15
    c: DistanceX(g1,g-1) = 15
    c: PointOnObject(g-1,g2)
FEATURE [PartDesign::Pad] Pad126
  Direction = (1,1,1)
  Length = 4
  Length2 = 100
  Profile = -> Sketch171
  Type = 0
FEATURE [Sketcher::SketchObject] Sketch172
  FullyConstrained = true
  MapMode = 5
  Support = -> [XY_Plane126]
  sketch-geometry (3):
    g0: LineSegment StartX=15 StartY=15 StartZ=0 EndX=15 EndY=-15 EndZ=0
    g1: LineSegment StartX=15 StartY=-15 StartZ=0 EndX=-15 EndY=-15 EndZ=0
    g2: LineSegment StartX=-15 StartY=-15 StartZ=0 EndX=15 EndY=15 EndZ=0
  constraints (9):
    c: Vertical(g0)
    c: Coincident(g0,g1)
    c: Horizontal(g1)
    c: Coincident(g1,g2)
    c: Coincident(g2,g0)
    c: DistanceY(g0,g-1) = 15
    c: DistanceY(g-1,g0) = 15
    c: DistanceX(g1,g-1) = 15
    c: PointOnObject(g-1,g2)
FEATURE [PartDesign::Pad] Pad127
  Direction = (1,1,1)
  Length = 4
  Length2 = 100
  Profile = -> Sketch172
  Type = 0
FEATURE [PartDesign::Body] Body126  label="30mm support-062"
  Group = -> [Sketch171,Pad126]
  Origin = -> Origin127
  Placement = pos=(136,-3013,0) rot=(0,0,1;3.14159rad)
  Tip = -> Pad126
FEATURE [PartDesign::Body] Body127  label="30mm suport-061"
  Group = -> [Sketch172,Pad127]
  Origin = -> Origin126
  Placement = pos=(80,-3013,0) rot=(0,0,1;0rad)
  Tip = -> Pad127
FEATURE [Sketcher::SketchObject] Sketch173
  FullyConstrained = true
  MapMode = 5
  Support = -> [XY_Plane128]
  sketch-geometry (3):
    g0: LineSegment StartX=15 StartY=15 StartZ=0 EndX=15 EndY=-15 EndZ=0
    g1: LineSegment StartX=15 StartY=-15 StartZ=0 EndX=-15 EndY=-15 EndZ=0
    g2: LineSegment StartX=-15 StartY=-15 StartZ=0 EndX=15 EndY=15 EndZ=0
  constraints (9):
    c: Vertical(g0)
    c: Coincident(g0,g1)
    c: Horizontal(g1)
    c: Coincident(g1,g2)
    c: Coincident(g2,g0)
    c: DistanceY(g0,g-1) = 15
    c: DistanceY(g-1,g0) = 15
    c: DistanceX(g1,g-1) = 15
    c: PointOnObject(g-1,g2)
FEATURE [PartDesign::Pad] Pad129
  Direction = (1,1,1)
  Length = 4
  Length2 = 100
  Profile = -> Sketch173
  Type = 0
FEATURE [Sketcher::SketchObject] Sketch174
  FullyConstrained = true
  MapMode = 5
  Support = -> [XY_Plane129]
  sketch-geometry (3):
    g0: LineSegment StartX=15 StartY=15 StartZ=0 EndX=15 EndY=-15 EndZ=0
    g1: LineSegment StartX=15 StartY=-15 StartZ=0 EndX=-15 EndY=-15 EndZ=0
    g2: LineSegment StartX=-15 StartY=-15 StartZ=0 EndX=15 EndY=15 EndZ=0
  constraints (9):
    c: Vertical(g0)
    c: Coincident(g0,g1)
    c: Horizontal(g1)
    c: Coincident(g1,g2)
    c: Coincident(g2,g0)
    c: DistanceY(g0,g-1) = 15
    c: DistanceY(g-1,g0) = 15
    c: DistanceX(g1,g-1) = 15
    c: PointOnObject(g-1,g2)
FEATURE [PartDesign::Pad] Pad128
  Direction = (1,1,1)
  Length = 4
  Length2 = 100
  Profile = -> Sketch174
  Type = 0
FEATURE [PartDesign::Body] Body128  label="30mm support-063"
  Group = -> [Sketch173,Pad129]
  Origin = -> Origin128
  Placement = pos=(216,-3013,0) rot=(0,0,1;3.14159rad)
  Tip = -> Pad129
FEATURE [PartDesign::Body] Body129  label="30mm suport-062"
  Group = -> [Sketch174,Pad128]
  Origin = -> Origin129
  Placement = pos=(160,-3013,0) rot=(0,0,1;0rad)
  Tip = -> Pad128
FEATURE [Sketcher::SketchObject] Sketch175
  FullyConstrained = true
  MapMode = 5
  Support = -> [XY_Plane131]
  sketch-geometry (3):
    g0: LineSegment StartX=15 StartY=15 StartZ=0 EndX=15 EndY=-15 EndZ=0
    g1: LineSegment StartX=15 StartY=-15 StartZ=0 EndX=-15 EndY=-15 EndZ=0
    g2: LineSegment StartX=-15 StartY=-15 StartZ=0 EndX=15 EndY=15 EndZ=0
  constraints (9):
    c: Vertical(g0)
    c: Coincident(g0,g1)
    c: Horizontal(g1)
    c: Coincident(g1,g2)
    c: Coincident(g2,g0)
    c: DistanceY(g0,g-1) = 15
    c: DistanceY(g-1,g0) = 15
    c: DistanceX(g1,g-1) = 15
    c: PointOnObject(g-1,g2)
FEATURE [PartDesign::Pad] Pad130
  Direction = (1,1,1)
  Length = 4
  Length2 = 100
  Profile = -> Sketch175
  Type = 0
FEATURE [Sketcher::SketchObject] Sketch176
  FullyConstrained = true
  MapMode = 5
  Support = -> [XY_Plane130]
  sketch-geometry (3):
    g0: LineSegment StartX=15 StartY=15 StartZ=0 EndX=15 EndY=-15 EndZ=0
    g1: LineSegment StartX=15 StartY=-15 StartZ=0 EndX=-15 EndY=-15 EndZ=0
    g2: LineSegment StartX=-15 StartY=-15 StartZ=0 EndX=15 EndY=15 EndZ=0
  constraints (9):
    c: Vertical(g0)
    c: Coincident(g0,g1)
    c: Horizontal(g1)
    c: Coincident(g1,g2)
    c: Coincident(g2,g0)
    c: DistanceY(g0,g-1) = 15
    c: DistanceY(g-1,g0) = 15
    c: DistanceX(g1,g-1) = 15
    c: PointOnObject(g-1,g2)
FEATURE [PartDesign::Body] Body131  label="30mm support-064"
  Group = -> [Sketch175,Pad130]
  Origin = -> Origin130
  Placement = pos=(246,-3013,0) rot=(0,0,1;6.28318rad)
  Tip = -> Pad130
FEATURE [PartDesign::Pad] Pad131
  Direction = (1,1,1)
  Length = 4
  Length2 = 100
  Profile = -> Sketch176
  Type = 0
FEATURE [PartDesign::Body] Body130  label="30mm suport-063"
  Group = -> [Sketch176,Pad131]
  Origin = -> Origin131
  Placement = pos=(325,-3013,0) rot=(0,0,1;0rad)
  Tip = -> Pad131
FEATURE [Sketcher::SketchObject] Sketch177
  FullyConstrained = true
  MapMode = 5
  Support = -> [XY_Plane132]
  sketch-geometry (3):
    g0: LineSegment StartX=15 StartY=15 StartZ=0 EndX=15 EndY=-15 EndZ=0
    g1: LineSegment StartX=15 StartY=-15 StartZ=0 EndX=-15 EndY=-15 EndZ=0
    g2: LineSegment StartX=-15 StartY=-15 StartZ=0 EndX=15 EndY=15 EndZ=0
  constraints (9):
    c: Vertical(g0)
    c: Coincident(g0,g1)
    c: Horizontal(g1)
    c: Coincident(g1,g2)
    c: Coincident(g2,g0)
    c: DistanceY(g0,g-1) = 15
    c: DistanceY(g-1,g0) = 15
    c: DistanceX(g1,g-1) = 15
    c: PointOnObject(g-1,g2)
FEATURE [PartDesign::Pad] Pad132
  Direction = (1,1,1)
  Length = 4
  Length2 = 100
  Profile = -> Sketch177
  Type = 0
FEATURE [PartDesign::Body] Body132  label="30mm support-065"
  Group = -> [Sketch177,Pad132]
  Origin = -> Origin132
  Placement = pos=(296,-3013,0) rot=(0,0,1;3.14159rad)
  Tip = -> Pad132
FEATURE [Sketcher::SketchObject] Sketch178
  FullyConstrained = true
  MapMode = 5
  Support = -> [XY_Plane134]
  sketch-geometry (3):
    g0: LineSegment StartX=15 StartY=15 StartZ=0 EndX=15 EndY=-15 EndZ=0
    g1: LineSegment StartX=15 StartY=-15 StartZ=0 EndX=-15 EndY=-15 EndZ=0
    g2: LineSegment StartX=-15 StartY=-15 StartZ=0 EndX=15 EndY=15 EndZ=0
  constraints (9):
    c: Vertical(g0)
    c: Coincident(g0,g1)
    c: Horizontal(g1)
    c: Coincident(g1,g2)
    c: Coincident(g2,g0)
    c: DistanceY(g0,g-1) = 15
    c: DistanceY(g-1,g0) = 15
    c: DistanceX(g1,g-1) = 15
    c: PointOnObject(g-1,g2)
FEATURE [PartDesign::Pad] Pad133
  Direction = (1,1,1)
  Length = 4
  Length2 = 100
  Profile = -> Sketch178
  Type = 0
FEATURE [Sketcher::SketchObject] Sketch179
  FullyConstrained = true
  MapMode = 5
  Support = -> [XY_Plane133]
  sketch-geometry (3):
    g0: LineSegment StartX=15 StartY=15 StartZ=0 EndX=15 EndY=-15 EndZ=0
    g1: LineSegment StartX=15 StartY=-15 StartZ=0 EndX=-15 EndY=-15 EndZ=0
    g2: LineSegment StartX=-15 StartY=-15 StartZ=0 EndX=15 EndY=15 EndZ=0
  constraints (9):
    c: Vertical(g0)
    c: Coincident(g0,g1)
    c: Horizontal(g1)
    c: Coincident(g1,g2)
    c: Coincident(g2,g0)
    c: DistanceY(g0,g-1) = 15
    c: DistanceY(g-1,g0) = 15
    c: DistanceX(g1,g-1) = 15
    c: PointOnObject(g-1,g2)
FEATURE [PartDesign::Pad] Pad134
  Direction = (1,1,1)
  Length = 4
  Length2 = 100
  Profile = -> Sketch179
  Type = 0
FEATURE [PartDesign::Body] Body133  label="30mm support-066"
  Group = -> [Sketch178,Pad133]
  Origin = -> Origin133
  Placement = pos=(376,-3013,0) rot=(0,0,1;3.14159rad)
  Tip = -> Pad133
FEATURE [PartDesign::Body] Body134  label="30mm suport-064"
  Group = -> [Sketch179,Pad134]
  Origin = -> Origin134
  Placement = pos=(405,-3013,0) rot=(0,0,1;0rad)
  Tip = -> Pad134
FEATURE [Sketcher::SketchObject] Sketch180
  FullyConstrained = true
  MapMode = 5
  Support = -> [XY_Plane136]
  sketch-geometry (3):
    g0: LineSegment StartX=15 StartY=15 StartZ=0 EndX=15 EndY=-15 EndZ=0
    g1: LineSegment StartX=15 StartY=-15 StartZ=0 EndX=-15 EndY=-15 EndZ=0
    g2: LineSegment StartX=-15 StartY=-15 StartZ=0 EndX=15 EndY=15 EndZ=0
  constraints (9):
    c: Vertical(g0)
    c: Coincident(g0,g1)
    c: Horizontal(g1)
    c: Coincident(g1,g2)
    c: Coincident(g2,g0)
    c: DistanceY(g0,g-1) = 15
    c: DistanceY(g-1,g0) = 15
    c: DistanceX(g1,g-1) = 15
    c: PointOnObject(g-1,g2)
FEATURE [Sketcher::SketchObject] Sketch181
  FullyConstrained = true
  MapMode = 5
  Support = -> [XY_Plane135]
  sketch-geometry (3):
    g0: LineSegment StartX=15 StartY=15 StartZ=0 EndX=15 EndY=-15 EndZ=0
    g1: LineSegment StartX=15 StartY=-15 StartZ=0 EndX=-15 EndY=-15 EndZ=0
    g2: LineSegment StartX=-15 StartY=-15 StartZ=0 EndX=15 EndY=15 EndZ=0
  constraints (9):
    c: Vertical(g0)
    c: Coincident(g0,g1)
    c: Horizontal(g1)
    c: Coincident(g1,g2)
    c: Coincident(g2,g0)
    c: DistanceY(g0,g-1) = 15
    c: DistanceY(g-1,g0) = 15
    c: DistanceX(g1,g-1) = 15
    c: PointOnObject(g-1,g2)
FEATURE [PartDesign::Pad] Pad135
  Direction = (1,1,1)
  Length = 4
  Length2 = 100
  Profile = -> Sketch180
  Type = 0
FEATURE [PartDesign::Pad] Pad136
  Direction = (1,1,1)
  Length = 4
  Length2 = 100
  Profile = -> Sketch181
  Type = 0
FEATURE [PartDesign::Body] Body135  label="30mm suport-065"
  Group = -> [Sketch181,Pad136]
  Origin = -> Origin136
  Placement = pos=(475,-3013,0) rot=(0,0,1;0rad)
  Tip = -> Pad136
FEATURE [PartDesign::Body] Body136  label="30mm support-067"
  Group = -> [Sketch180,Pad135]
  Origin = -> Origin135
  Placement = pos=(456,-3013,0) rot=(0,0,1;3.14159rad)
  Tip = -> Pad135
FEATURE [Sketcher::SketchObject] Sketch182
  FullyConstrained = true
  MapMode = 5
  Support = -> [XY_Plane138]
  sketch-geometry (3):
    g0: LineSegment StartX=15 StartY=15 StartZ=0 EndX=15 EndY=-15 EndZ=0
    g1: LineSegment StartX=15 StartY=-15 StartZ=0 EndX=-15 EndY=-15 EndZ=0
    g2: LineSegment StartX=-15 StartY=-15 StartZ=0 EndX=15 EndY=15 EndZ=0
  constraints (9):
    c: Vertical(g0)
    c: Coincident(g0,g1)
    c: Horizontal(g1)
    c: Coincident(g1,g2)
    c: Coincident(g2,g0)
    c: DistanceY(g0,g-1) = 15
    c: DistanceY(g-1,g0) = 15
    c: DistanceX(g1,g-1) = 15
    c: PointOnObject(g-1,g2)
FEATURE [Sketcher::SketchObject] Sketch183
  FullyConstrained = true
  MapMode = 5
  Support = -> [XY_Plane137]
  sketch-geometry (3):
    g0: LineSegment StartX=15 StartY=15 StartZ=0 EndX=15 EndY=-15 EndZ=0
    g1: LineSegment StartX=15 StartY=-15 StartZ=0 EndX=-15 EndY=-15 EndZ=0
    g2: LineSegment StartX=-15 StartY=-15 StartZ=0 EndX=15 EndY=15 EndZ=0
  constraints (9):
    c: Vertical(g0)
    c: Coincident(g0,g1)
    c: Horizontal(g1)
    c: Coincident(g1,g2)
    c: Coincident(g2,g0)
    c: DistanceY(g0,g-1) = 15
    c: DistanceY(g-1,g0) = 15
    c: DistanceX(g1,g-1) = 15
    c: PointOnObject(g-1,g2)
FEATURE [PartDesign::Pad] Pad137
  Direction = (1,1,1)
  Length = 4
  Length2 = 100
  Profile = -> Sketch182
  Type = 0
FEATURE [PartDesign::Pad] Pad138
  Direction = (1,1,1)
  Length = 4
  Length2 = 100
  Profile = -> Sketch183
  Type = 0
FEATURE [PartDesign::Body] Body137  label="30mm suport-066"
  Group = -> [Sketch183,Pad138]
  Origin = -> Origin138
  Placement = pos=(555,-3013,0) rot=(0,0,1;0rad)
  Tip = -> Pad138
FEATURE [PartDesign::Body] Body138  label="30mm support-068"
  Group = -> [Sketch182,Pad137]
  Origin = -> Origin137
  Placement = pos=(526,-3013,0) rot=(0,0,1;3.14159rad)
  Tip = -> Pad137
FEATURE [Sketcher::SketchObject] Sketch184
  FullyConstrained = true
  MapMode = 5
  Support = -> [XY_Plane140]
  sketch-geometry (3):
    g0: LineSegment StartX=15 StartY=15 StartZ=0 EndX=15 EndY=-15 EndZ=0
    g1: LineSegment StartX=15 StartY=-15 StartZ=0 EndX=-15 EndY=-15 EndZ=0
    g2: LineSegment StartX=-15 StartY=-15 StartZ=0 EndX=15 EndY=15 EndZ=0
  constraints (9):
    c: Vertical(g0)
    c: Coincident(g0,g1)
    c: Horizontal(g1)
    c: Coincident(g1,g2)
    c: Coincident(g2,g0)
    c: DistanceY(g0,g-1) = 15
    c: DistanceY(g-1,g0) = 15
    c: DistanceX(g1,g-1) = 15
    c: PointOnObject(g-1,g2)
FEATURE [Sketcher::SketchObject] Sketch185
  FullyConstrained = true
  MapMode = 5
  Support = -> [XY_Plane139]
  sketch-geometry (3):
    g0: LineSegment StartX=15 StartY=15 StartZ=0 EndX=15 EndY=-15 EndZ=0
    g1: LineSegment StartX=15 StartY=-15 StartZ=0 EndX=-15 EndY=-15 EndZ=0
    g2: LineSegment StartX=-15 StartY=-15 StartZ=0 EndX=15 EndY=15 EndZ=0
  constraints (9):
    c: Vertical(g0)
    c: Coincident(g0,g1)
    c: Horizontal(g1)
    c: Coincident(g1,g2)
    c: Coincident(g2,g0)
    c: DistanceY(g0,g-1) = 15
    c: DistanceY(g-1,g0) = 15
    c: DistanceX(g1,g-1) = 15
    c: PointOnObject(g-1,g2)
FEATURE [PartDesign::Pad] Pad139
  Direction = (1,1,1)
  Length = 4
  Length2 = 100
  Profile = -> Sketch184
  Type = 0
FEATURE [PartDesign::Pad] Pad140
  Direction = (1,1,1)
  Length = 4
  Length2 = 100
  Profile = -> Sketch185
  Type = 0
FEATURE [PartDesign::Body] Body139  label="30mm suport-067"
  Group = -> [Sketch184,Pad139]
  Origin = -> Origin140
  Placement = pos=(555,-3013,0) rot=(0,0,1;0rad)
  Tip = -> Pad139
FEATURE [PartDesign::Body] Body140  label="30mm support-069"
  Group = -> [Sketch185,Pad140]
  Origin = -> Origin139
  Placement = pos=(606,-3013,0) rot=(0,0,1;3.14159rad)
  Tip = -> Pad140
FEATURE [Sketcher::SketchObject] Sketch186
  FullyConstrained = true
  MapMode = 5
  Support = -> [XY_Plane142]
  sketch-geometry (3):
    g0: LineSegment StartX=15 StartY=15 StartZ=0 EndX=15 EndY=-15 EndZ=0
    g1: LineSegment StartX=15 StartY=-15 StartZ=0 EndX=-15 EndY=-15 EndZ=0
    g2: LineSegment StartX=-15 StartY=-15 StartZ=0 EndX=15 EndY=15 EndZ=0
  constraints (9):
    c: Vertical(g0)
    c: Coincident(g0,g1)
    c: Horizontal(g1)
    c: Coincident(g1,g2)
    c: Coincident(g2,g0)
    c: DistanceY(g0,g-1) = 15
    c: DistanceY(g-1,g0) = 15
    c: DistanceX(g1,g-1) = 15
    c: PointOnObject(g-1,g2)
FEATURE [Sketcher::SketchObject] Sketch187
  FullyConstrained = true
  MapMode = 5
  Support = -> [XY_Plane141]
  sketch-geometry (3):
    g0: LineSegment StartX=15 StartY=15 StartZ=0 EndX=15 EndY=-15 EndZ=0
    g1: LineSegment StartX=15 StartY=-15 StartZ=0 EndX=-15 EndY=-15 EndZ=0
    g2: LineSegment StartX=-15 StartY=-15 StartZ=0 EndX=15 EndY=15 EndZ=0
  constraints (9):
    c: Vertical(g0)
    c: Coincident(g0,g1)
    c: Horizontal(g1)
    c: Coincident(g1,g2)
    c: Coincident(g2,g0)
    c: DistanceY(g0,g-1) = 15
    c: DistanceY(g-1,g0) = 15
    c: DistanceX(g1,g-1) = 15
    c: PointOnObject(g-1,g2)
FEATURE [PartDesign::Pad] Pad141
  Direction = (1,1,1)
  Length = 4
  Length2 = 100
  Profile = -> Sketch187
  Type = 0
FEATURE [PartDesign::Pad] Pad142
  Direction = (1,1,1)
  Length = 4
  Length2 = 100
  Profile = -> Sketch186
  Type = 0
FEATURE [PartDesign::Body] Body141  label="30mm support-070"
  Group = -> [Sketch186,Pad142]
  Origin = -> Origin142
  Placement = pos=(686,-3013,0) rot=(0,0,1;3.14159rad)
  Tip = -> Pad142
FEATURE [PartDesign::Body] Body142  label="30mm suport-068"
  Group = -> [Sketch187,Pad141]
  Origin = -> Origin141
  Placement = pos=(635,-3013,0) rot=(0,0,1;0rad)
  Tip = -> Pad141
FEATURE [Sketcher::SketchObject] Sketch188
  FullyConstrained = true
  MapMode = 5
  Support = -> [XY_Plane144]
  sketch-geometry (3):
    g0: LineSegment StartX=15 StartY=15 StartZ=0 EndX=15 EndY=-15 EndZ=0
    g1: LineSegment StartX=15 StartY=-15 StartZ=0 EndX=-15 EndY=-15 EndZ=0
    g2: LineSegment StartX=-15 StartY=-15 StartZ=0 EndX=15 EndY=15 EndZ=0
  constraints (9):
    c: Vertical(g0)
    c: Coincident(g0,g1)
    c: Horizontal(g1)
    c: Coincident(g1,g2)
    c: Coincident(g2,g0)
    c: DistanceY(g0,g-1) = 15
    c: DistanceY(g-1,g0) = 15
    c: DistanceX(g1,g-1) = 15
    c: PointOnObject(g-1,g2)
FEATURE [Sketcher::SketchObject] Sketch189
  FullyConstrained = true
  MapMode = 5
  Support = -> [XY_Plane143]
  sketch-geometry (3):
    g0: LineSegment StartX=15 StartY=15 StartZ=0 EndX=15 EndY=-15 EndZ=0
    g1: LineSegment StartX=15 StartY=-15 StartZ=0 EndX=-15 EndY=-15 EndZ=0
    g2: LineSegment StartX=-15 StartY=-15 StartZ=0 EndX=15 EndY=15 EndZ=0
  constraints (9):
    c: Vertical(g0)
    c: Coincident(g0,g1)
    c: Horizontal(g1)
    c: Coincident(g1,g2)
    c: Coincident(g2,g0)
    c: DistanceY(g0,g-1) = 15
    c: DistanceY(g-1,g0) = 15
    c: DistanceX(g1,g-1) = 15
    c: PointOnObject(g-1,g2)
FEATURE [PartDesign::Pad] Pad143
  Direction = (1,1,1)
  Length = 4
  Length2 = 100
  Profile = -> Sketch189
  Type = 0
FEATURE [PartDesign::Body] Body144  label="30mm suport-069"
  Group = -> [Sketch189,Pad143]
  Origin = -> Origin144
  Placement = pos=(635,-3013,0) rot=(0,0,1;0rad)
  Tip = -> Pad143
FEATURE [PartDesign::Pad] Pad144
  Direction = (1,1,1)
  Length = 4
  Length2 = 100
  Profile = -> Sketch188
  Type = 0
FEATURE [PartDesign::Body] Body143  label="30mm support-071"
  Group = -> [Sketch188,Pad144]
  Origin = -> Origin143
  Placement = pos=(686,-3013,0) rot=(0,0,1;3.14159rad)
  Tip = -> Pad144
FEATURE [Sketcher::SketchObject] Sketch190
  FullyConstrained = true
  MapMode = 5
  Support = -> [XY_Plane145]
  sketch-geometry (3):
    g0: LineSegment StartX=15 StartY=15 StartZ=0 EndX=15 EndY=-15 EndZ=0
    g1: LineSegment StartX=15 StartY=-15 StartZ=0 EndX=-15 EndY=-15 EndZ=0
    g2: LineSegment StartX=-15 StartY=-15 StartZ=0 EndX=15 EndY=15 EndZ=0
  constraints (9):
    c: Vertical(g0)
    c: Coincident(g0,g1)
    c: Horizontal(g1)
    c: Coincident(g1,g2)
    c: Coincident(g2,g0)
    c: DistanceY(g0,g-1) = 15
    c: DistanceY(g-1,g0) = 15
    c: DistanceX(g1,g-1) = 15
    c: PointOnObject(g-1,g2)
FEATURE [Sketcher::SketchObject] Sketch191
  FullyConstrained = true
  MapMode = 5
  Support = -> [XY_Plane146]
  sketch-geometry (3):
    g0: LineSegment StartX=15 StartY=15 StartZ=0 EndX=15 EndY=-15 EndZ=0
    g1: LineSegment StartX=15 StartY=-15 StartZ=0 EndX=-15 EndY=-15 EndZ=0
    g2: LineSegment StartX=-15 StartY=-15 StartZ=0 EndX=15 EndY=15 EndZ=0
  constraints (9):
    c: Vertical(g0)
    c: Coincident(g0,g1)
    c: Horizontal(g1)
    c: Coincident(g1,g2)
    c: Coincident(g2,g0)
    c: DistanceY(g0,g-1) = 15
    c: DistanceY(g-1,g0) = 15
    c: DistanceX(g1,g-1) = 15
    c: PointOnObject(g-1,g2)
FEATURE [PartDesign::Pad] Pad145
  Direction = (1,1,1)
  Length = 4
  Length2 = 100
  Profile = -> Sketch190
  Type = 0
FEATURE [PartDesign::Body] Body146  label="30mm suport-070"
  Group = -> [Sketch190,Pad145]
  Origin = -> Origin146
  Placement = pos=(705,-3013,0) rot=(0,0,1;0rad)
  Tip = -> Pad145
FEATURE [PartDesign::Pad] Pad146
  Direction = (1,1,1)
  Length = 4
  Length2 = 100
  Profile = -> Sketch191
  Type = 0
FEATURE [PartDesign::Body] Body145  label="30mm support-072"
  Group = -> [Sketch191,Pad146]
  Origin = -> Origin145
  Placement = pos=(756,-3013,0) rot=(0,0,1;3.14159rad)
  Tip = -> Pad146
FEATURE [Sketcher::SketchObject] Sketch192
  FullyConstrained = true
  MapMode = 5
  Support = -> [XY_Plane147]
  sketch-geometry (3):
    g0: LineSegment StartX=15 StartY=15 StartZ=0 EndX=15 EndY=-15 EndZ=0
    g1: LineSegment StartX=15 StartY=-15 StartZ=0 EndX=-15 EndY=-15 EndZ=0
    g2: LineSegment StartX=-15 StartY=-15 StartZ=0 EndX=15 EndY=15 EndZ=0
  constraints (9):
    c: Vertical(g0)
    c: Coincident(g0,g1)
    c: Horizontal(g1)
    c: Coincident(g1,g2)
    c: Coincident(g2,g0)
    c: DistanceY(g0,g-1) = 15
    c: DistanceY(g-1,g0) = 15
    c: DistanceX(g1,g-1) = 15
    c: PointOnObject(g-1,g2)
FEATURE [PartDesign::Pad] Pad147
  Direction = (1,1,1)
  Length = 4
  Length2 = 100
  Profile = -> Sketch192
  Type = 0
FEATURE [PartDesign::Body] Body148  label="30mm suport-071"
  Group = -> [Sketch192,Pad147]
  Origin = -> Origin148
  Placement = pos=(785,-3013,0) rot=(0,0,1;0rad)
  Tip = -> Pad147
FEATURE [Sketcher::SketchObject] Sketch193
  FullyConstrained = true
  MapMode = 5
  Support = -> [XY_Plane148]
  sketch-geometry (3):
    g0: LineSegment StartX=15 StartY=15 StartZ=0 EndX=15 EndY=-15 EndZ=0
    g1: LineSegment StartX=15 StartY=-15 StartZ=0 EndX=-15 EndY=-15 EndZ=0
    g2: LineSegment StartX=-15 StartY=-15 StartZ=0 EndX=15 EndY=15 EndZ=0
  constraints (9):
    c: Vertical(g0)
    c: Coincident(g0,g1)
    c: Horizontal(g1)
    c: Coincident(g1,g2)
    c: Coincident(g2,g0)
    c: DistanceY(g0,g-1) = 15
    c: DistanceY(g-1,g0) = 15
    c: DistanceX(g1,g-1) = 15
    c: PointOnObject(g-1,g2)
FEATURE [PartDesign::Pad] Pad148
  Direction = (1,1,1)
  Length = 4
  Length2 = 100
  Profile = -> Sketch193
  Type = 0
FEATURE [PartDesign::Body] Body147  label="30mm support-073"
  Group = -> [Sketch193,Pad148]
  Origin = -> Origin147
  Placement = pos=(836,-3013,0) rot=(0,0,1;3.14159rad)
  Tip = -> Pad148
FEATURE [Sketcher::SketchObject] Sketch194
  FullyConstrained = true
  MapMode = 5
  Support = -> [XY_Plane149]
  sketch-geometry (3):
    g0: LineSegment StartX=15 StartY=15 StartZ=0 EndX=15 EndY=-15 EndZ=0
    g1: LineSegment StartX=15 StartY=-15 StartZ=0 EndX=-15 EndY=-15 EndZ=0
    g2: LineSegment StartX=-15 StartY=-15 StartZ=0 EndX=15 EndY=15 EndZ=0
  constraints (9):
    c: Vertical(g0)
    c: Coincident(g0,g1)
    c: Horizontal(g1)
    c: Coincident(g1,g2)
    c: Coincident(g2,g0)
    c: DistanceY(g0,g-1) = 15
    c: DistanceY(g-1,g0) = 15
    c: DistanceX(g1,g-1) = 15
    c: PointOnObject(g-1,g2)
FEATURE [PartDesign::Pad] Pad150
  Direction = (1,1,1)
  Length = 4
  Length2 = 100
  Profile = -> Sketch194
  Type = 0
FEATURE [PartDesign::Body] Body149  label="30mm suport-072"
  Group = -> [Sketch194,Pad150]
  Origin = -> Origin150
  Placement = pos=(865,-3013,0) rot=(0,0,1;0rad)
  Tip = -> Pad150
FEATURE [Sketcher::SketchObject] Sketch195
  FullyConstrained = true
  MapMode = 5
  Support = -> [XY_Plane150]
  sketch-geometry (3):
    g0: LineSegment StartX=15 StartY=15 StartZ=0 EndX=15 EndY=-15 EndZ=0
    g1: LineSegment StartX=15 StartY=-15 StartZ=0 EndX=-15 EndY=-15 EndZ=0
    g2: LineSegment StartX=-15 StartY=-15 StartZ=0 EndX=15 EndY=15 EndZ=0
  constraints (9):
    c: Vertical(g0)
    c: Coincident(g0,g1)
    c: Horizontal(g1)
    c: Coincident(g1,g2)
    c: Coincident(g2,g0)
    c: DistanceY(g0,g-1) = 15
    c: DistanceY(g-1,g0) = 15
    c: DistanceX(g1,g-1) = 15
    c: PointOnObject(g-1,g2)
FEATURE [PartDesign::Pad] Pad149
  Direction = (1,1,1)
  Length = 4
  Length2 = 100
  Profile = -> Sketch195
  Type = 0
FEATURE [PartDesign::Body] Body150  label="30mm support-074"
  Group = -> [Sketch195,Pad149]
  Origin = -> Origin149
  Placement = pos=(920,-3013,0) rot=(0,0,1;3.14159rad)
  Tip = -> Pad149
FEATURE [Sketcher::SketchObject] Sketch196
  FullyConstrained = true
  MapMode = 5
  Support = -> [XY_Plane151]
  sketch-geometry (3):
    g0: LineSegment StartX=15 StartY=15 StartZ=0 EndX=15 EndY=-15 EndZ=0
    g1: LineSegment StartX=15 StartY=-15 StartZ=0 EndX=-15 EndY=-15 EndZ=0
    g2: LineSegment StartX=-15 StartY=-15 StartZ=0 EndX=15 EndY=15 EndZ=0
  constraints (9):
    c: Vertical(g0)
    c: Coincident(g0,g1)
    c: Horizontal(g1)
    c: Coincident(g1,g2)
    c: Coincident(g2,g0)
    c: DistanceY(g0,g-1) = 15
    c: DistanceY(g-1,g0) = 15
    c: DistanceX(g1,g-1) = 15
    c: PointOnObject(g-1,g2)
FEATURE [PartDesign::Pad] Pad152
  Direction = (1,1,1)
  Length = 4
  Length2 = 100
  Profile = -> Sketch196
  Type = 0
FEATURE [PartDesign::Body] Body151  label="30mm suport-073"
  Group = -> [Sketch196,Pad152]
  Origin = -> Origin151
  Placement = pos=(945,-3013,0) rot=(0,0,1;0rad)
  Tip = -> Pad152
FEATURE [Sketcher::SketchObject] Sketch197
  FullyConstrained = true
  MapMode = 5
  Support = -> [XY_Plane152]
  sketch-geometry (3):
    g0: LineSegment StartX=15 StartY=15 StartZ=0 EndX=15 EndY=-15 EndZ=0
    g1: LineSegment StartX=15 StartY=-15 StartZ=0 EndX=-15 EndY=-15 EndZ=0
    g2: LineSegment StartX=-15 StartY=-15 StartZ=0 EndX=15 EndY=15 EndZ=0
  constraints (9):
    c: Vertical(g0)
    c: Coincident(g0,g1)
    c: Horizontal(g1)
    c: Coincident(g1,g2)
    c: Coincident(g2,g0)
    c: DistanceY(g0,g-1) = 15
    c: DistanceY(g-1,g0) = 15
    c: DistanceX(g1,g-1) = 15
    c: PointOnObject(g-1,g2)
FEATURE [PartDesign::Pad] Pad151
  Direction = (1,1,1)
  Length = 4
  Length2 = 100
  Profile = -> Sketch197
  Type = 0
FEATURE [PartDesign::Body] Body152  label="30mm support-075"
  Group = -> [Sketch197,Pad151]
  Origin = -> Origin152
  Placement = pos=(990,-3013,0) rot=(0,0,1;3.14159rad)
  Tip = -> Pad151
FEATURE [Sketcher::SketchObject] Sketch198
  FullyConstrained = true
  MapMode = 5
  Support = -> [XY_Plane153]
  sketch-geometry (3):
    g0: LineSegment StartX=15 StartY=15 StartZ=0 EndX=15 EndY=-15 EndZ=0
    g1: LineSegment StartX=15 StartY=-15 StartZ=0 EndX=-15 EndY=-15 EndZ=0
    g2: LineSegment StartX=-15 StartY=-15 StartZ=0 EndX=15 EndY=15 EndZ=0
  constraints (9):
    c: Vertical(g0)
    c: Coincident(g0,g1)
    c: Horizontal(g1)
    c: Coincident(g1,g2)
    c: Coincident(g2,g0)
    c: DistanceY(g0,g-1) = 15
    c: DistanceY(g-1,g0) = 15
    c: DistanceX(g1,g-1) = 15
    c: PointOnObject(g-1,g2)
FEATURE [PartDesign::Pad] Pad153
  Direction = (1,1,1)
  Length = 4
  Length2 = 100
  Profile = -> Sketch198
  Type = 0
FEATURE [PartDesign::Body] Body153  label="30mm suport-074"
  Group = -> [Sketch198,Pad153]
  Origin = -> Origin153
  Placement = pos=(1025,-3013,0) rot=(0,0,1;0rad)
  Tip = -> Pad153
FEATURE [Sketcher::SketchObject] Sketch199
  FullyConstrained = true
  MapMode = 5
  Support = -> [XY_Plane154]
  sketch-geometry (3):
    g0: LineSegment StartX=15 StartY=15 StartZ=0 EndX=15 EndY=-15 EndZ=0
    g1: LineSegment StartX=15 StartY=-15 StartZ=0 EndX=-15 EndY=-15 EndZ=0
    g2: LineSegment StartX=-15 StartY=-15 StartZ=0 EndX=15 EndY=15 EndZ=0
  constraints (9):
    c: Vertical(g0)
    c: Coincident(g0,g1)
    c: Horizontal(g1)
    c: Coincident(g1,g2)
    c: Coincident(g2,g0)
    c: DistanceY(g0,g-1) = 15
    c: DistanceY(g-1,g0) = 15
    c: DistanceX(g1,g-1) = 15
    c: PointOnObject(g-1,g2)
FEATURE [PartDesign::Pad] Pad154
  Direction = (1,1,1)
  Length = 4
  Length2 = 100
  Profile = -> Sketch199
  Type = 0
FEATURE [PartDesign::Body] Body154  label="30mm support-076"
  Group = -> [Sketch199,Pad154]
  Origin = -> Origin154
  Placement = pos=(1070,-3013,0) rot=(0,0,1;3.14159rad)
  Tip = -> Pad154
FEATURE [Sketcher::SketchObject] Sketch200
  FullyConstrained = true
  MapMode = 5
  Support = -> [XY_Plane156]
  sketch-geometry (3):
    g0: LineSegment StartX=15 StartY=15 StartZ=0 EndX=15 EndY=-15 EndZ=0
    g1: LineSegment StartX=15 StartY=-15 StartZ=0 EndX=-15 EndY=-15 EndZ=0
    g2: LineSegment StartX=-15 StartY=-15 StartZ=0 EndX=15 EndY=15 EndZ=0
  constraints (9):
    c: Vertical(g0)
    c: Coincident(g0,g1)
    c: Horizontal(g1)
    c: Coincident(g1,g2)
    c: Coincident(g2,g0)
    c: DistanceY(g0,g-1) = 15
    c: DistanceY(g-1,g0) = 15
    c: DistanceX(g1,g-1) = 15
    c: PointOnObject(g-1,g2)
FEATURE [PartDesign::Pad] Pad155
  Direction = (1,1,1)
  Length = 4
  Length2 = 100
  Profile = -> Sketch200
  Type = 0
FEATURE [PartDesign::Body] Body156  label="30mm suport-075"
  Group = -> [Sketch200,Pad155]
  Origin = -> Origin155
  Placement = pos=(1105,-3013,0) rot=(0,0,1;0rad)
  Tip = -> Pad155
FEATURE [Sketcher::SketchObject] Sketch201
  FullyConstrained = true
  MapMode = 5
  Support = -> [XY_Plane155]
  sketch-geometry (3):
    g0: LineSegment StartX=15 StartY=15 StartZ=0 EndX=15 EndY=-15 EndZ=0
    g1: LineSegment StartX=15 StartY=-15 StartZ=0 EndX=-15 EndY=-15 EndZ=0
    g2: LineSegment StartX=-15 StartY=-15 StartZ=0 EndX=15 EndY=15 EndZ=0
  constraints (9):
    c: Vertical(g0)
    c: Coincident(g0,g1)
    c: Horizontal(g1)
    c: Coincident(g1,g2)
    c: Coincident(g2,g0)
    c: DistanceY(g0,g-1) = 15
    c: DistanceY(g-1,g0) = 15
    c: DistanceX(g1,g-1) = 15
    c: PointOnObject(g-1,g2)
FEATURE [PartDesign::Pad] Pad156
  Direction = (1,1,1)
  Length = 4
  Length2 = 100
  Profile = -> Sketch201
  Type = 0
FEATURE [PartDesign::Body] Body155  label="30mm support-077"
  Group = -> [Sketch201,Pad156]
  Origin = -> Origin156
  Placement = pos=(1150,-3013,0) rot=(0,0,1;3.14159rad)
  Tip = -> Pad156
FEATURE [Sketcher::SketchObject] Sketch202
  FullyConstrained = true
  MapMode = 5
  Support = -> [XY_Plane158]
  sketch-geometry (3):
    g0: LineSegment StartX=15 StartY=15 StartZ=0 EndX=15 EndY=-15 EndZ=0
    g1: LineSegment StartX=15 StartY=-15 StartZ=0 EndX=-15 EndY=-15 EndZ=0
    g2: LineSegment StartX=-15 StartY=-15 StartZ=0 EndX=15 EndY=15 EndZ=0
  constraints (9):
    c: Vertical(g0)
    c: Coincident(g0,g1)
    c: Horizontal(g1)
    c: Coincident(g1,g2)
    c: Coincident(g2,g0)
    c: DistanceY(g0,g-1) = 15
    c: DistanceY(g-1,g0) = 15
    c: DistanceX(g1,g-1) = 15
    c: PointOnObject(g-1,g2)
FEATURE [PartDesign::Pad] Pad158
  Direction = (1,1,1)
  Length = 4
  Length2 = 100
  Profile = -> Sketch202
  Type = 0
FEATURE [PartDesign::Body] Body158  label="30mm support-078"
  Group = -> [Sketch202,Pad158]
  Origin = -> Origin157
  Placement = pos=(1230,-3013,0) rot=(0,0,1;3.14159rad)
  Tip = -> Pad158
FEATURE [Sketcher::SketchObject] Sketch203
  FullyConstrained = true
  MapMode = 5
  Support = -> [XY_Plane157]
  sketch-geometry (3):
    g0: LineSegment StartX=15 StartY=15 StartZ=0 EndX=15 EndY=-15 EndZ=0
    g1: LineSegment StartX=15 StartY=-15 StartZ=0 EndX=-15 EndY=-15 EndZ=0
    g2: LineSegment StartX=-15 StartY=-15 StartZ=0 EndX=15 EndY=15 EndZ=0
  constraints (9):
    c: Vertical(g0)
    c: Coincident(g0,g1)
    c: Horizontal(g1)
    c: Coincident(g1,g2)
    c: Coincident(g2,g0)
    c: DistanceY(g0,g-1) = 15
    c: DistanceY(g-1,g0) = 15
    c: DistanceX(g1,g-1) = 15
    c: PointOnObject(g-1,g2)
FEATURE [PartDesign::Pad] Pad157
  Direction = (1,1,1)
  Length = 4
  Length2 = 100
  Profile = -> Sketch203
  Type = 0
FEATURE [PartDesign::Body] Body157  label="30mm suport-076"
  Group = -> [Sketch203,Pad157]
  Origin = -> Origin158
  Placement = pos=(1185,-3013,0) rot=(0,0,1;0rad)
  Tip = -> Pad157
FEATURE [Sketcher::SketchObject] Sketch204
  FullyConstrained = true
  MapMode = 5
  Support = -> [XY_Plane159]
  sketch-geometry (3):
    g0: LineSegment StartX=15 StartY=15 StartZ=0 EndX=15 EndY=-15 EndZ=0
    g1: LineSegment StartX=15 StartY=-15 StartZ=0 EndX=-15 EndY=-15 EndZ=0
    g2: LineSegment StartX=-15 StartY=-15 StartZ=0 EndX=15 EndY=15 EndZ=0
  constraints (9):
    c: Vertical(g0)
    c: Coincident(g0,g1)
    c: Horizontal(g1)
    c: Coincident(g1,g2)
    c: Coincident(g2,g0)
    c: DistanceY(g0,g-1) = 15
    c: DistanceY(g-1,g0) = 15
    c: DistanceX(g1,g-1) = 15
    c: PointOnObject(g-1,g2)
FEATURE [PartDesign::Pad] Pad160
  Direction = (1,1,1)
  Length = 4
  Length2 = 100
  Profile = -> Sketch204
  Type = 0
FEATURE [PartDesign::Body] Body160  label="30mm support-079"
  Group = -> [Sketch204,Pad160]
  Origin = -> Origin160
  Placement = pos=(1310,-3013,0) rot=(0,0,1;3.14159rad)
  Tip = -> Pad160
FEATURE [Sketcher::SketchObject] Sketch205
  FullyConstrained = true
  MapMode = 5
  Support = -> [XY_Plane160]
  sketch-geometry (3):
    g0: LineSegment StartX=15 StartY=15 StartZ=0 EndX=15 EndY=-15 EndZ=0
    g1: LineSegment StartX=15 StartY=-15 StartZ=0 EndX=-15 EndY=-15 EndZ=0
    g2: LineSegment StartX=-15 StartY=-15 StartZ=0 EndX=15 EndY=15 EndZ=0
  constraints (9):
    c: Vertical(g0)
    c: Coincident(g0,g1)
    c: Horizontal(g1)
    c: Coincident(g1,g2)
    c: Coincident(g2,g0)
    c: DistanceY(g0,g-1) = 15
    c: DistanceY(g-1,g0) = 15
    c: DistanceX(g1,g-1) = 15
    c: PointOnObject(g-1,g2)
FEATURE [PartDesign::Pad] Pad159
  Direction = (1,1,1)
  Length = 4
  Length2 = 100
  Profile = -> Sketch205
  Type = 0
FEATURE [PartDesign::Body] Body159  label="30mm suport-077"
  Group = -> [Sketch205,Pad159]
  Origin = -> Origin159
  Placement = pos=(1265,-3013,0) rot=(0,0,1;0rad)
  Tip = -> Pad159
FEATURE [Sketcher::SketchObject] Sketch206
  FullyConstrained = true
  MapMode = 5
  Support = -> [XY_Plane162]
  sketch-geometry (3):
    g0: LineSegment StartX=15 StartY=15 StartZ=0 EndX=15 EndY=-15 EndZ=0
    g1: LineSegment StartX=15 StartY=-15 StartZ=0 EndX=-15 EndY=-15 EndZ=0
    g2: LineSegment StartX=-15 StartY=-15 StartZ=0 EndX=15 EndY=15 EndZ=0
  constraints (9):
    c: Vertical(g0)
    c: Coincident(g0,g1)
    c: Horizontal(g1)
    c: Coincident(g1,g2)
    c: Coincident(g2,g0)
    c: DistanceY(g0,g-1) = 15
    c: DistanceY(g-1,g0) = 15
    c: DistanceX(g1,g-1) = 15
    c: PointOnObject(g-1,g2)
FEATURE [PartDesign::Pad] Pad161
  Direction = (1,1,1)
  Length = 4
  Length2 = 100
  Profile = -> Sketch206
  Type = 0
FEATURE [PartDesign::Body] Body161  label="30mm support-080"
  Group = -> [Sketch206,Pad161]
  Origin = -> Origin162
  Placement = pos=(1390,-3013,0) rot=(0,0,1;3.14159rad)
  Tip = -> Pad161
FEATURE [Sketcher::SketchObject] Sketch207
  FullyConstrained = true
  MapMode = 5
  Support = -> [XY_Plane161]
  sketch-geometry (3):
    g0: LineSegment StartX=15 StartY=15 StartZ=0 EndX=15 EndY=-15 EndZ=0
    g1: LineSegment StartX=15 StartY=-15 StartZ=0 EndX=-15 EndY=-15 EndZ=0
    g2: LineSegment StartX=-15 StartY=-15 StartZ=0 EndX=15 EndY=15 EndZ=0
  constraints (9):
    c: Vertical(g0)
    c: Coincident(g0,g1)
    c: Horizontal(g1)
    c: Coincident(g1,g2)
    c: Coincident(g2,g0)
    c: DistanceY(g0,g-1) = 15
    c: DistanceY(g-1,g0) = 15
    c: DistanceX(g1,g-1) = 15
    c: PointOnObject(g-1,g2)
FEATURE [PartDesign::Pad] Pad162
  Direction = (1,1,1)
  Length = 4
  Length2 = 100
  Profile = -> Sketch207
  Type = 0
FEATURE [PartDesign::Body] Body162  label="30mm suport-078"
  Group = -> [Sketch207,Pad162]
  Origin = -> Origin161
  Placement = pos=(1345,-3013,0) rot=(0,0,1;0rad)
  Tip = -> Pad162
FEATURE [Sketcher::SketchObject] Sketch208
  FullyConstrained = true
  MapMode = 5
  Support = -> [XY_Plane164]
  sketch-geometry (3):
    g0: LineSegment StartX=15 StartY=15 StartZ=0 EndX=15 EndY=-15 EndZ=0
    g1: LineSegment StartX=15 StartY=-15 StartZ=0 EndX=-15 EndY=-15 EndZ=0
    g2: LineSegment StartX=-15 StartY=-15 StartZ=0 EndX=15 EndY=15 EndZ=0
  constraints (9):
    c: Vertical(g0)
    c: Coincident(g0,g1)
    c: Horizontal(g1)
    c: Coincident(g1,g2)
    c: Coincident(g2,g0)
    c: DistanceY(g0,g-1) = 15
    c: DistanceY(g-1,g0) = 15
    c: DistanceX(g1,g-1) = 15
    c: PointOnObject(g-1,g2)
FEATURE [Sketcher::SketchObject] Sketch209
  FullyConstrained = true
  MapMode = 5
  Support = -> [XY_Plane163]
  sketch-geometry (3):
    g0: LineSegment StartX=15 StartY=15 StartZ=0 EndX=15 EndY=-15 EndZ=0
    g1: LineSegment StartX=15 StartY=-15 StartZ=0 EndX=-15 EndY=-15 EndZ=0
    g2: LineSegment StartX=-15 StartY=-15 StartZ=0 EndX=15 EndY=15 EndZ=0
  constraints (9):
    c: Vertical(g0)
    c: Coincident(g0,g1)
    c: Horizontal(g1)
    c: Coincident(g1,g2)
    c: Coincident(g2,g0)
    c: DistanceY(g0,g-1) = 15
    c: DistanceY(g-1,g0) = 15
    c: DistanceX(g1,g-1) = 15
    c: PointOnObject(g-1,g2)
FEATURE [PartDesign::Pad] Pad163
  Direction = (1,1,1)
  Length = 4
  Length2 = 100
  Profile = -> Sketch209
  Type = 0
FEATURE [PartDesign::Body] Body163  label="30mm support-081"
  Group = -> [Sketch209,Pad163]
  Origin = -> Origin163
  Placement = pos=(1470,-3013,0) rot=(0,0,1;3.14159rad)
  Tip = -> Pad163
FEATURE [PartDesign::Pad] Pad164
  Direction = (1,1,1)
  Length = 4
  Length2 = 100
  Profile = -> Sketch208
  Type = 0
FEATURE [PartDesign::Body] Body164  label="30mm suport-079"
  Group = -> [Sketch208,Pad164]
  Origin = -> Origin164
  Placement = pos=(1425,-3013,0) rot=(0,0,1;0rad)
  Tip = -> Pad164
FEATURE [Sketcher::SketchObject] Sketch210
  FullyConstrained = true
  MapMode = 5
  Support = -> [XY_Plane166]
  sketch-geometry (3):
    g0: LineSegment StartX=15 StartY=15 StartZ=0 EndX=15 EndY=-15 EndZ=0
    g1: LineSegment StartX=15 StartY=-15 StartZ=0 EndX=-15 EndY=-15 EndZ=0
    g2: LineSegment StartX=-15 StartY=-15 StartZ=0 EndX=15 EndY=15 EndZ=0
  constraints (9):
    c: Vertical(g0)
    c: Coincident(g0,g1)
    c: Horizontal(g1)
    c: Coincident(g1,g2)
    c: Coincident(g2,g0)
    c: DistanceY(g0,g-1) = 15
    c: DistanceY(g-1,g0) = 15
    c: DistanceX(g1,g-1) = 15
    c: PointOnObject(g-1,g2)
FEATURE [Sketcher::SketchObject] Sketch211
  FullyConstrained = true
  MapMode = 5
  Support = -> [XY_Plane165]
  sketch-geometry (3):
    g0: LineSegment StartX=15 StartY=15 StartZ=0 EndX=15 EndY=-15 EndZ=0
    g1: LineSegment StartX=15 StartY=-15 StartZ=0 EndX=-15 EndY=-15 EndZ=0
    g2: LineSegment StartX=-15 StartY=-15 StartZ=0 EndX=15 EndY=15 EndZ=0
  constraints (9):
    c: Vertical(g0)
    c: Coincident(g0,g1)
    c: Horizontal(g1)
    c: Coincident(g1,g2)
    c: Coincident(g2,g0)
    c: DistanceY(g0,g-1) = 15
    c: DistanceY(g-1,g0) = 15
    c: DistanceX(g1,g-1) = 15
    c: PointOnObject(g-1,g2)
FEATURE [PartDesign::Pad] Pad165
  Direction = (1,1,1)
  Length = 4
  Length2 = 100
  Profile = -> Sketch210
  Type = 0
FEATURE [PartDesign::Body] Body165  label="30mm suport-080"
  Group = -> [Sketch210,Pad165]
  Origin = -> Origin166
  Placement = pos=(1505,-3013,0) rot=(0,0,1;0rad)
  Tip = -> Pad165
FEATURE [PartDesign::Pad] Pad166
  Direction = (1,1,1)
  Length = 4
  Length2 = 100
  Profile = -> Sketch211
  Type = 0
FEATURE [PartDesign::Body] Body166  label="30mm support-082"
  Group = -> [Sketch211,Pad166]
  Origin = -> Origin165
  Placement = pos=(1550,-3013,0) rot=(0,0,1;3.14159rad)
  Tip = -> Pad166
FEATURE [Sketcher::SketchObject] Sketch212
  FullyConstrained = true
  MapMode = 5
  Support = -> [XY_Plane168]
  sketch-geometry (3):
    g0: LineSegment StartX=15 StartY=15 StartZ=0 EndX=15 EndY=-15 EndZ=0
    g1: LineSegment StartX=15 StartY=-15 StartZ=0 EndX=-15 EndY=-15 EndZ=0
    g2: LineSegment StartX=-15 StartY=-15 StartZ=0 EndX=15 EndY=15 EndZ=0
  constraints (9):
    c: Vertical(g0)
    c: Coincident(g0,g1)
    c: Horizontal(g1)
    c: Coincident(g1,g2)
    c: Coincident(g2,g0)
    c: DistanceY(g0,g-1) = 15
    c: DistanceY(g-1,g0) = 15
    c: DistanceX(g1,g-1) = 15
    c: PointOnObject(g-1,g2)
FEATURE [Sketcher::SketchObject] Sketch213
  FullyConstrained = true
  MapMode = 5
  Support = -> [XY_Plane167]
  sketch-geometry (3):
    g0: LineSegment StartX=15 StartY=15 StartZ=0 EndX=15 EndY=-15 EndZ=0
    g1: LineSegment StartX=15 StartY=-15 StartZ=0 EndX=-15 EndY=-15 EndZ=0
    g2: LineSegment StartX=-15 StartY=-15 StartZ=0 EndX=15 EndY=15 EndZ=0
  constraints (9):
    c: Vertical(g0)
    c: Coincident(g0,g1)
    c: Horizontal(g1)
    c: Coincident(g1,g2)
    c: Coincident(g2,g0)
    c: DistanceY(g0,g-1) = 15
    c: DistanceY(g-1,g0) = 15
    c: DistanceX(g1,g-1) = 15
    c: PointOnObject(g-1,g2)
FEATURE [PartDesign::Pad] Pad167
  Direction = (1,1,1)
  Length = 4
  Length2 = 100
  Profile = -> Sketch212
  Type = 0
FEATURE [PartDesign::Body] Body168  label="30mm support-083"
  Group = -> [Sketch212,Pad167]
  Origin = -> Origin168
  Placement = pos=(1630,-3013,0) rot=(0,0,1;3.14159rad)
  Tip = -> Pad167
FEATURE [PartDesign::Pad] Pad168
  Direction = (1,1,1)
  Length = 4
  Length2 = 100
  Profile = -> Sketch213
  Type = 0
FEATURE [PartDesign::Body] Body167  label="30mm suport-081"
  Group = -> [Sketch213,Pad168]
  Origin = -> Origin167
  Placement = pos=(1585,-3013,0) rot=(0,0,1;0rad)
  Tip = -> Pad168
FEATURE [Sketcher::SketchObject] Sketch214
  FullyConstrained = true
  MapMode = 5
  Support = -> [XY_Plane170]
  sketch-geometry (3):
    g0: LineSegment StartX=15 StartY=15 StartZ=0 EndX=15 EndY=-15 EndZ=0
    g1: LineSegment StartX=15 StartY=-15 StartZ=0 EndX=-15 EndY=-15 EndZ=0
    g2: LineSegment StartX=-15 StartY=-15 StartZ=0 EndX=15 EndY=15 EndZ=0
  constraints (9):
    c: Vertical(g0)
    c: Coincident(g0,g1)
    c: Horizontal(g1)
    c: Coincident(g1,g2)
    c: Coincident(g2,g0)
    c: DistanceY(g0,g-1) = 15
    c: DistanceY(g-1,g0) = 15
    c: DistanceX(g1,g-1) = 15
    c: PointOnObject(g-1,g2)
FEATURE [Sketcher::SketchObject] Sketch215
  FullyConstrained = true
  MapMode = 5
  Support = -> [XY_Plane169]
  sketch-geometry (3):
    g0: LineSegment StartX=15 StartY=15 StartZ=0 EndX=15 EndY=-15 EndZ=0
    g1: LineSegment StartX=15 StartY=-15 StartZ=0 EndX=-15 EndY=-15 EndZ=0
    g2: LineSegment StartX=-15 StartY=-15 StartZ=0 EndX=15 EndY=15 EndZ=0
  constraints (9):
    c: Vertical(g0)
    c: Coincident(g0,g1)
    c: Horizontal(g1)
    c: Coincident(g1,g2)
    c: Coincident(g2,g0)
    c: DistanceY(g0,g-1) = 15
    c: DistanceY(g-1,g0) = 15
    c: DistanceX(g1,g-1) = 15
    c: PointOnObject(g-1,g2)
FEATURE [PartDesign::Pad] Pad169
  Direction = (1,1,1)
  Length = 4
  Length2 = 100
  Profile = -> Sketch215
  Type = 0
FEATURE [PartDesign::Body] Body169  label="30mm suport-082"
  Group = -> [Sketch215,Pad169]
  Origin = -> Origin169
  Placement = pos=(1665,-3013,0) rot=(0,0,1;0rad)
  Tip = -> Pad169
FEATURE [PartDesign::Pad] Pad170
  Direction = (1,1,1)
  Length = 4
  Length2 = 100
  Profile = -> Sketch214
  Type = 0
FEATURE [PartDesign::Body] Body170  label="30mm support-084"
  Group = -> [Sketch214,Pad170]
  Origin = -> Origin170
  Placement = pos=(1710,-3013,0) rot=(0,0,1;3.14159rad)
  Tip = -> Pad170
FEATURE [Sketcher::SketchObject] Sketch216
  FullyConstrained = true
  MapMode = 5
  Support = -> [XY_Plane171]
  sketch-geometry (3):
    g0: LineSegment StartX=15 StartY=15 StartZ=0 EndX=15 EndY=-15 EndZ=0
    g1: LineSegment StartX=15 StartY=-15 StartZ=0 EndX=-15 EndY=-15 EndZ=0
    g2: LineSegment StartX=-15 StartY=-15 StartZ=0 EndX=15 EndY=15 EndZ=0
  constraints (9):
    c: Vertical(g0)
    c: Coincident(g0,g1)
    c: Horizontal(g1)
    c: Coincident(g1,g2)
    c: Coincident(g2,g0)
    c: DistanceY(g0,g-1) = 15
    c: DistanceY(g-1,g0) = 15
    c: DistanceX(g1,g-1) = 15
    c: PointOnObject(g-1,g2)
FEATURE [Sketcher::SketchObject] Sketch217
  FullyConstrained = true
  MapMode = 5
  Support = -> [XY_Plane172]
  sketch-geometry (3):
    g0: LineSegment StartX=15 StartY=15 StartZ=0 EndX=15 EndY=-15 EndZ=0
    g1: LineSegment StartX=15 StartY=-15 StartZ=0 EndX=-15 EndY=-15 EndZ=0
    g2: LineSegment StartX=-15 StartY=-15 StartZ=0 EndX=15 EndY=15 EndZ=0
  constraints (9):
    c: Vertical(g0)
    c: Coincident(g0,g1)
    c: Horizontal(g1)
    c: Coincident(g1,g2)
    c: Coincident(g2,g0)
    c: DistanceY(g0,g-1) = 15
    c: DistanceY(g-1,g0) = 15
    c: DistanceX(g1,g-1) = 15
    c: PointOnObject(g-1,g2)
FEATURE [PartDesign::Pad] Pad171
  Direction = (1,1,1)
  Length = 4
  Length2 = 100
  Profile = -> Sketch217
  Type = 0
FEATURE [PartDesign::Body] Body171  label="30mm suport-083"
  Group = -> [Sketch217,Pad171]
  Origin = -> Origin171
  Placement = pos=(1745,-3013,0) rot=(0,0,1;0rad)
  Tip = -> Pad171
FEATURE [PartDesign::Pad] Pad172
  Direction = (1,1,1)
  Length = 4
  Length2 = 100
  Profile = -> Sketch216
  Type = 0
FEATURE [PartDesign::Body] Body172  label="30mm support-085"
  Group = -> [Sketch216,Pad172]
  Origin = -> Origin172
  Placement = pos=(1790,-3013,0) rot=(0,0,1;3.14159rad)
  Tip = -> Pad172
FEATURE [Sketcher::SketchObject] Sketch218
  FullyConstrained = true
  MapMode = 5
  Support = -> [XY_Plane174]
  sketch-geometry (3):
    g0: LineSegment StartX=15 StartY=15 StartZ=0 EndX=15 EndY=-15 EndZ=0
    g1: LineSegment StartX=15 StartY=-15 StartZ=0 EndX=-15 EndY=-15 EndZ=0
    g2: LineSegment StartX=-15 StartY=-15 StartZ=0 EndX=15 EndY=15 EndZ=0
  constraints (9):
    c: Vertical(g0)
    c: Coincident(g0,g1)
    c: Horizontal(g1)
    c: Coincident(g1,g2)
    c: Coincident(g2,g0)
    c: DistanceY(g0,g-1) = 15
    c: DistanceY(g-1,g0) = 15
    c: DistanceX(g1,g-1) = 15
    c: PointOnObject(g-1,g2)
FEATURE [Sketcher::SketchObject] Sketch219
  FullyConstrained = true
  MapMode = 5
  Support = -> [XY_Plane173]
  sketch-geometry (3):
    g0: LineSegment StartX=15 StartY=15 StartZ=0 EndX=15 EndY=-15 EndZ=0
    g1: LineSegment StartX=15 StartY=-15 StartZ=0 EndX=-15 EndY=-15 EndZ=0
    g2: LineSegment StartX=-15 StartY=-15 StartZ=0 EndX=15 EndY=15 EndZ=0
  constraints (9):
    c: Vertical(g0)
    c: Coincident(g0,g1)
    c: Horizontal(g1)
    c: Coincident(g1,g2)
    c: Coincident(g2,g0)
    c: DistanceY(g0,g-1) = 15
    c: DistanceY(g-1,g0) = 15
    c: DistanceX(g1,g-1) = 15
    c: PointOnObject(g-1,g2)
FEATURE [PartDesign::Pad] Pad173
  Direction = (1,1,1)
  Length = 4
  Length2 = 100
  Profile = -> Sketch218
  Type = 0
FEATURE [PartDesign::Body] Body173  label="30mm suport-084"
  Group = -> [Sketch218,Pad173]
  Origin = -> Origin174
  Placement = pos=(1825,-3013,0) rot=(0,0,1;0rad)
  Tip = -> Pad173
FEATURE [PartDesign::Pad] Pad174
  Direction = (1,1,1)
  Length = 4
  Length2 = 100
  Profile = -> Sketch219
  Type = 0
FEATURE [PartDesign::Body] Body174  label="30mm support-086"
  Group = -> [Sketch219,Pad174]
  Origin = -> Origin173
  Placement = pos=(1870,-3013,0) rot=(0,0,1;3.14159rad)
  Tip = -> Pad174
FEATURE [Sketcher::SketchObject] Sketch220
  FullyConstrained = true
  MapMode = 5
  Support = -> [XY_Plane175]
  sketch-geometry (3):
    g0: LineSegment StartX=15 StartY=15 StartZ=0 EndX=15 EndY=-15 EndZ=0
    g1: LineSegment StartX=15 StartY=-15 StartZ=0 EndX=-15 EndY=-15 EndZ=0
    g2: LineSegment StartX=-15 StartY=-15 StartZ=0 EndX=15 EndY=15 EndZ=0
  constraints (9):
    c: Vertical(g0)
    c: Coincident(g0,g1)
    c: Horizontal(g1)
    c: Coincident(g1,g2)
    c: Coincident(g2,g0)
    c: DistanceY(g0,g-1) = 15
    c: DistanceY(g-1,g0) = 15
    c: DistanceX(g1,g-1) = 15
    c: PointOnObject(g-1,g2)
FEATURE [Sketcher::SketchObject] Sketch221
  FullyConstrained = true
  MapMode = 5
  Support = -> [XY_Plane176]
  sketch-geometry (3):
    g0: LineSegment StartX=15 StartY=15 StartZ=0 EndX=15 EndY=-15 EndZ=0
    g1: LineSegment StartX=15 StartY=-15 StartZ=0 EndX=-15 EndY=-15 EndZ=0
    g2: LineSegment StartX=-15 StartY=-15 StartZ=0 EndX=15 EndY=15 EndZ=0
  constraints (9):
    c: Vertical(g0)
    c: Coincident(g0,g1)
    c: Horizontal(g1)
    c: Coincident(g1,g2)
    c: Coincident(g2,g0)
    c: DistanceY(g0,g-1) = 15
    c: DistanceY(g-1,g0) = 15
    c: DistanceX(g1,g-1) = 15
    c: PointOnObject(g-1,g2)
FEATURE [PartDesign::Pad] Pad175
  Direction = (1,1,1)
  Length = 4
  Length2 = 100
  Profile = -> Sketch221
  Type = 0
FEATURE [PartDesign::Body] Body176  label="30mm support-087"
  Group = -> [Sketch221,Pad175]
  Origin = -> Origin175
  Placement = pos=(1950,-3013,0) rot=(0,0,1;3.14159rad)
  Tip = -> Pad175
FEATURE [PartDesign::Pad] Pad176
  Direction = (1,1,1)
  Length = 4
  Length2 = 100
  Profile = -> Sketch220
  Type = 0
FEATURE [PartDesign::Body] Body175  label="30mm suport-085"
  Group = -> [Sketch220,Pad176]
  Origin = -> Origin176
  Placement = pos=(1905,-3013,0) rot=(0,0,1;0rad)
  Tip = -> Pad176
FEATURE [Sketcher::SketchObject] Sketch222
  FullyConstrained = true
  MapMode = 5
  Support = -> [XY_Plane177]
  sketch-geometry (3):
    g0: LineSegment StartX=15 StartY=15 StartZ=0 EndX=15 EndY=-15 EndZ=0
    g1: LineSegment StartX=15 StartY=-15 StartZ=0 EndX=-15 EndY=-15 EndZ=0
    g2: LineSegment StartX=-15 StartY=-15 StartZ=0 EndX=15 EndY=15 EndZ=0
  constraints (9):
    c: Vertical(g0)
    c: Coincident(g0,g1)
    c: Horizontal(g1)
    c: Coincident(g1,g2)
    c: Coincident(g2,g0)
    c: DistanceY(g0,g-1) = 15
    c: DistanceY(g-1,g0) = 15
    c: DistanceX(g1,g-1) = 15
    c: PointOnObject(g-1,g2)
FEATURE [Sketcher::SketchObject] Sketch223
  FullyConstrained = true
  MapMode = 5
  Support = -> [XY_Plane178]
  sketch-geometry (3):
    g0: LineSegment StartX=15 StartY=15 StartZ=0 EndX=15 EndY=-15 EndZ=0
    g1: LineSegment StartX=15 StartY=-15 StartZ=0 EndX=-15 EndY=-15 EndZ=0
    g2: LineSegment StartX=-15 StartY=-15 StartZ=0 EndX=15 EndY=15 EndZ=0
  constraints (9):
    c: Vertical(g0)
    c: Coincident(g0,g1)
    c: Horizontal(g1)
    c: Coincident(g1,g2)
    c: Coincident(g2,g0)
    c: DistanceY(g0,g-1) = 15
    c: DistanceY(g-1,g0) = 15
    c: DistanceX(g1,g-1) = 15
    c: PointOnObject(g-1,g2)
FEATURE [PartDesign::Pad] Pad177
  Direction = (1,1,1)
  Length = 4
  Length2 = 100
  Profile = -> Sketch222
  Type = 0
FEATURE [PartDesign::Body] Body177  label="30mm suport-086"
  Group = -> [Sketch222,Pad177]
  Origin = -> Origin177
  Placement = pos=(1985,-3013,0) rot=(0,0,1;0rad)
  Tip = -> Pad177
FEATURE [PartDesign::Pad] Pad178
  Direction = (1,1,1)
  Length = 4
  Length2 = 100
  Profile = -> Sketch223
  Type = 0
FEATURE [PartDesign::Body] Body178  label="30mm support-088"
  Group = -> [Sketch223,Pad178]
  Origin = -> Origin178
  Placement = pos=(2030,-3013,0) rot=(0,0,1;3.14159rad)
  Tip = -> Pad178
FEATURE [Sketcher::SketchObject] Sketch224
  FullyConstrained = true
  MapMode = 5
  Support = -> [XY_Plane179]
  sketch-geometry (3):
    g0: LineSegment StartX=15 StartY=15 StartZ=0 EndX=15 EndY=-15 EndZ=0
    g1: LineSegment StartX=15 StartY=-15 StartZ=0 EndX=-15 EndY=-15 EndZ=0
    g2: LineSegment StartX=-15 StartY=-15 StartZ=0 EndX=15 EndY=15 EndZ=0
  constraints (9):
    c: Vertical(g0)
    c: Coincident(g0,g1)
    c: Horizontal(g1)
    c: Coincident(g1,g2)
    c: Coincident(g2,g0)
    c: DistanceY(g0,g-1) = 15
    c: DistanceY(g-1,g0) = 15
    c: DistanceX(g1,g-1) = 15
    c: PointOnObject(g-1,g2)
FEATURE [Sketcher::SketchObject] Sketch225
  FullyConstrained = true
  MapMode = 5
  Support = -> [XY_Plane180]
  sketch-geometry (3):
    g0: LineSegment StartX=15 StartY=15 StartZ=0 EndX=15 EndY=-15 EndZ=0
    g1: LineSegment StartX=15 StartY=-15 StartZ=0 EndX=-15 EndY=-15 EndZ=0
    g2: LineSegment StartX=-15 StartY=-15 StartZ=0 EndX=15 EndY=15 EndZ=0
  constraints (9):
    c: Vertical(g0)
    c: Coincident(g0,g1)
    c: Horizontal(g1)
    c: Coincident(g1,g2)
    c: Coincident(g2,g0)
    c: DistanceY(g0,g-1) = 15
    c: DistanceY(g-1,g0) = 15
    c: DistanceX(g1,g-1) = 15
    c: PointOnObject(g-1,g2)
FEATURE [PartDesign::Pad] Pad179
  Direction = (1,1,1)
  Length = 4
  Length2 = 100
  Profile = -> Sketch225
  Type = 0
FEATURE [PartDesign::Body] Body180  label="30mm support-089"
  Group = -> [Sketch225,Pad179]
  Origin = -> Origin180
  Placement = pos=(2110,-3013,0) rot=(0,0,1;3.14159rad)
  Tip = -> Pad179
FEATURE [PartDesign::Pad] Pad180
  Direction = (1,1,1)
  Length = 4
  Length2 = 100
  Profile = -> Sketch224
  Type = 0
FEATURE [PartDesign::Body] Body179  label="30mm suport-087"
  Group = -> [Sketch224,Pad180]
  Origin = -> Origin179
  Placement = pos=(2065,-3013,0) rot=(0,0,1;0rad)
  Tip = -> Pad180
FEATURE [Sketcher::SketchObject] Sketch226
  FullyConstrained = true
  MapMode = 5
  Support = -> [XY_Plane181]
  sketch-geometry (3):
    g0: LineSegment StartX=15 StartY=15 StartZ=0 EndX=15 EndY=-15 EndZ=0
    g1: LineSegment StartX=15 StartY=-15 StartZ=0 EndX=-15 EndY=-15 EndZ=0
    g2: LineSegment StartX=-15 StartY=-15 StartZ=0 EndX=15 EndY=15 EndZ=0
  constraints (9):
    c: Vertical(g0)
    c: Coincident(g0,g1)
    c: Horizontal(g1)
    c: Coincident(g1,g2)
    c: Coincident(g2,g0)
    c: DistanceY(g0,g-1) = 15
    c: DistanceY(g-1,g0) = 15
    c: DistanceX(g1,g-1) = 15
    c: PointOnObject(g-1,g2)
FEATURE [Sketcher::SketchObject] Sketch227
  FullyConstrained = true
  MapMode = 5
  Support = -> [XY_Plane182]
  sketch-geometry (3):
    g0: LineSegment StartX=15 StartY=15 StartZ=0 EndX=15 EndY=-15 EndZ=0
    g1: LineSegment StartX=15 StartY=-15 StartZ=0 EndX=-15 EndY=-15 EndZ=0
    g2: LineSegment StartX=-15 StartY=-15 StartZ=0 EndX=15 EndY=15 EndZ=0
  constraints (9):
    c: Vertical(g0)
    c: Coincident(g0,g1)
    c: Horizontal(g1)
    c: Coincident(g1,g2)
    c: Coincident(g2,g0)
    c: DistanceY(g0,g-1) = 15
    c: DistanceY(g-1,g0) = 15
    c: DistanceX(g1,g-1) = 15
    c: PointOnObject(g-1,g2)
FEATURE [PartDesign::Pad] Pad181
  Direction = (1,1,1)
  Length = 4
  Length2 = 100
  Profile = -> Sketch226
  Type = 0
FEATURE [PartDesign::Body] Body182  label="30mm suport-088"
  Group = -> [Sketch226,Pad181]
  Origin = -> Origin182
  Placement = pos=(2145,-3013,0) rot=(0,0,1;0rad)
  Tip = -> Pad181
FEATURE [PartDesign::Pad] Pad182
  Direction = (1,1,1)
  Length = 4
  Length2 = 100
  Profile = -> Sketch227
  Type = 0
FEATURE [PartDesign::Body] Body181  label="30mm support-090"
  Group = -> [Sketch227,Pad182]
  Origin = -> Origin181
  Placement = pos=(2190,-3013,0) rot=(0,0,1;3.14159rad)
  Tip = -> Pad182
FEATURE [Sketcher::SketchObject] Sketch228
  FullyConstrained = true
  MapMode = 5
  Support = -> [XY_Plane183]
  sketch-geometry (4):
    g0: LineSegment StartX=-1004 StartY=50 StartZ=0 EndX=1004 EndY=50 EndZ=0
    g1: LineSegment StartX=1004 StartY=50 StartZ=0 EndX=1004 EndY=-50 EndZ=0
    g2: LineSegment StartX=1004 StartY=-50 StartZ=0 EndX=-1004 EndY=-50 EndZ=0
    g3: LineSegment StartX=-1004 StartY=-50 StartZ=0 EndX=-1004 EndY=50 EndZ=0
  constraints (11):
    c: Coincident(g0,g1)
    c: Coincident(g1,g2)
    c: Coincident(g2,g3)
    c: Coincident(g3,g0)
    c: Horizontal(g0)
    c: Horizontal(g2)
    c: Vertical(g1)
    c: Vertical(g3)
    c: Symmetric(g0,g1,g-1)
    c: DistanceX(g2,g1) = 2008
    c: DistanceY(g2,g0) = 100
FEATURE [PartDesign::Pad] Pad183
  Direction = (1,1,1)
  Length = 4
  Length2 = 100
  Profile = -> Sketch228
  Type = 0
FEATURE [PartDesign::Body] Body183  label="Residue-001"
  Group = -> [Sketch228,Pad183]
  Origin = -> Origin183
  Placement = pos=(1004,-3113,0) rot=(0,0,1;0rad)
  Tip = -> Pad183
FEATURE [Sketcher::SketchObject] Sketch229
  FullyConstrained = true
  MapMode = 5
  Support = -> [XY_Plane184]
  sketch-geometry (4):
    g0: LineSegment StartX=-1004 StartY=50 StartZ=0 EndX=1004 EndY=50 EndZ=0
    g1: LineSegment StartX=1004 StartY=50 StartZ=0 EndX=1004 EndY=-50 EndZ=0
    g2: LineSegment StartX=1004 StartY=-50 StartZ=0 EndX=-1004 EndY=-50 EndZ=0
    g3: LineSegment StartX=-1004 StartY=-50 StartZ=0 EndX=-1004 EndY=50 EndZ=0
  constraints (11):
    c: Coincident(g0,g1)
    c: Coincident(g1,g2)
    c: Coincident(g2,g3)
    c: Coincident(g3,g0)
    c: Horizontal(g0)
    c: Horizontal(g2)
    c: Vertical(g1)
    c: Vertical(g3)
    c: Symmetric(g0,g1,g-1)
    c: DistanceX(g2,g1) = 2008
    c: DistanceY(g2,g0) = 100
FEATURE [PartDesign::Pad] Pad184
  Direction = (1,1,1)
  Length = 4
  Length2 = 100
  Profile = -> Sketch229
  Type = 0
FEATURE [PartDesign::Body] Body184  label="Residue-002"
  Group = -> [Sketch229,Pad184]
  Origin = -> Origin184
  Placement = pos=(1004,-3223,0) rot=(0,0,1;0rad)
  Tip = -> Pad184
FEATURE [Sketcher::SketchObject] Sketch230
  FullyConstrained = true
  MapMode = 5
  Support = -> [XY_Plane185]
  sketch-geometry (4):
    g0: LineSegment StartX=-1004 StartY=50 StartZ=0 EndX=1004 EndY=50 EndZ=0
    g1: LineSegment StartX=1004 StartY=50 StartZ=0 EndX=1004 EndY=-50 EndZ=0
    g2: LineSegment StartX=1004 StartY=-50 StartZ=0 EndX=-1004 EndY=-50 EndZ=0
    g3: LineSegment StartX=-1004 StartY=-50 StartZ=0 EndX=-1004 EndY=50 EndZ=0
  constraints (11):
    c: Coincident(g0,g1)
    c: Coincident(g1,g2)
    c: Coincident(g2,g3)
    c: Coincident(g3,g0)
    c: Horizontal(g0)
    c: Horizontal(g2)
    c: Vertical(g1)
    c: Vertical(g3)
    c: Symmetric(g0,g1,g-1)
    c: DistanceX(g2,g1) = 2008
    c: DistanceY(g2,g0) = 100
FEATURE [PartDesign::Pad] Pad185
  Direction = (1,1,1)
  Length = 4
  Length2 = 100
  Profile = -> Sketch230
  Type = 0
FEATURE [PartDesign::Body] Body185  label="Residue-003"
  Group = -> [Sketch230,Pad185]
  Origin = -> Origin185
  Placement = pos=(1004,-3333,0) rot=(0,0,1;0rad)
  Tip = -> Pad185
FEATURE [App::DocumentObjectGroup] Group  label="Supports - 70 mm brackets "
  Group = -> [Body075,Body076,Body078,Body077,Body080,Body079,Body082,Body081,Body083,Body084,Body085,Body086,Body087,Body088,Body090,Body089,Body091,Body092,Body093,Body094,Body095,Body097,Body096,Body098,Body099,Body101,Body100,Body102,Body103,Body104,Body105,Body106,Body107,Body108,Body109,Body111,Body110,Body112,Body113,Body115,Body114,Body116,Body117,Body119,Body118,Body120,Body121,Body122,Body123,Body124,+61 more]
FEATURE [TechDraw::DrawViewDimension] Dimension262
  Arbitrary = false
  ArbitraryTolerances = false
  EqualTolerance = true
  FormatSpec = %.2f
  FormatSpecOverTolerance = %+.2f
  FormatSpecUnderTolerance = %+.2f
  Inverted = false
  LockPosition = false
  MeasureType = 1
  OverTolerance = 0
  References2D = -> [View013]
  Rotation = 0
  Scale = 0.15
  ScaleType = 0
  TheoreticalExact = false
  Type = 1
  UnderTolerance = 0
  X = -118.902
  Y = 18.0562
FEATURE [TechDraw::DrawViewDimension] Dimension263
  Arbitrary = false
  ArbitraryTolerances = false
  EqualTolerance = true
  FormatSpec = %.2f
  FormatSpecOverTolerance = %+.2f
  FormatSpecUnderTolerance = %+.2f
  Inverted = false
  LockPosition = false
  MeasureType = 1
  OverTolerance = 0
  References2D = -> [View013]
  Rotation = 0
  Scale = 0.15
  ScaleType = 0
  TheoreticalExact = false
  Type = 1
  UnderTolerance = 0
  X = -61.2313
  Y = 18.2935
FEATURE [TechDraw::DrawViewDimension] Dimension264
  Arbitrary = false
  ArbitraryTolerances = false
  EqualTolerance = true
  FormatSpec = %.2f
  FormatSpecOverTolerance = %+.2f
  FormatSpecUnderTolerance = %+.2f
  Inverted = false
  LockPosition = false
  MeasureType = 1
  OverTolerance = 0
  References2D = -> [View013]
  Rotation = 0
  Scale = 0.15
  ScaleType = 0
  TheoreticalExact = false
  Type = 1
  UnderTolerance = 0
  X = 41.5271
  Y = 19.6761
FEATURE [TechDraw::DrawPage] Page011  label="Driving_console_Drawing"
  KeepUpdated = true
  NextBalloonIndex = 1
  ProjectionType = 0
  Scale = 0.15
  Template = -> Template014
  Views = -> [View011,Dimension156,Dimension157,Dimension158,Dimension159,Dimension160,Dimension161,Dimension162,SectionView011,Dimension163,Dimension164,Dimension165,View012,Dimension166,Dimension167,Dimension168,Dimension169,Dimension170,Dimension171,View013,Dimension172,Dimension173,Dimension174,Dimension175,Dimension176,Dimension177,Dimension178,Dimension179,SectionView012,Dimension180,View014,Dimension181,+18 more]
FEATURE [TechDraw::DrawViewDimension] Dimension265
  Arbitrary = false
  ArbitraryTolerances = false
  EqualTolerance = true
  FormatSpec = %.2f
  FormatSpecOverTolerance = %+.2f
  FormatSpecUnderTolerance = %+.2f
  Inverted = false
  LockPosition = false
  MeasureType = 1
  OverTolerance = 0
  References2D = -> [View009]
  Rotation = 0
  ScaleType = 0
  TheoreticalExact = false
  Type = 2
  UnderTolerance = 0
  X = 194.154
  Y = 22.8142
FEATURE [TechDraw::DrawPage] Page006  label="Outer_front_frame_Drawing"
  KeepUpdated = true
  NextBalloonIndex = 1
  ProjectionType = 0
  Template = -> Template006
  Views = -> [View009,Dimension127,Dimension128,Dimension129,Dimension130,Dimension131,Dimension132,Dimension133,Dimension134,Dimension135,SectionView009,Dimension137,Dimension138,Dimension265]
